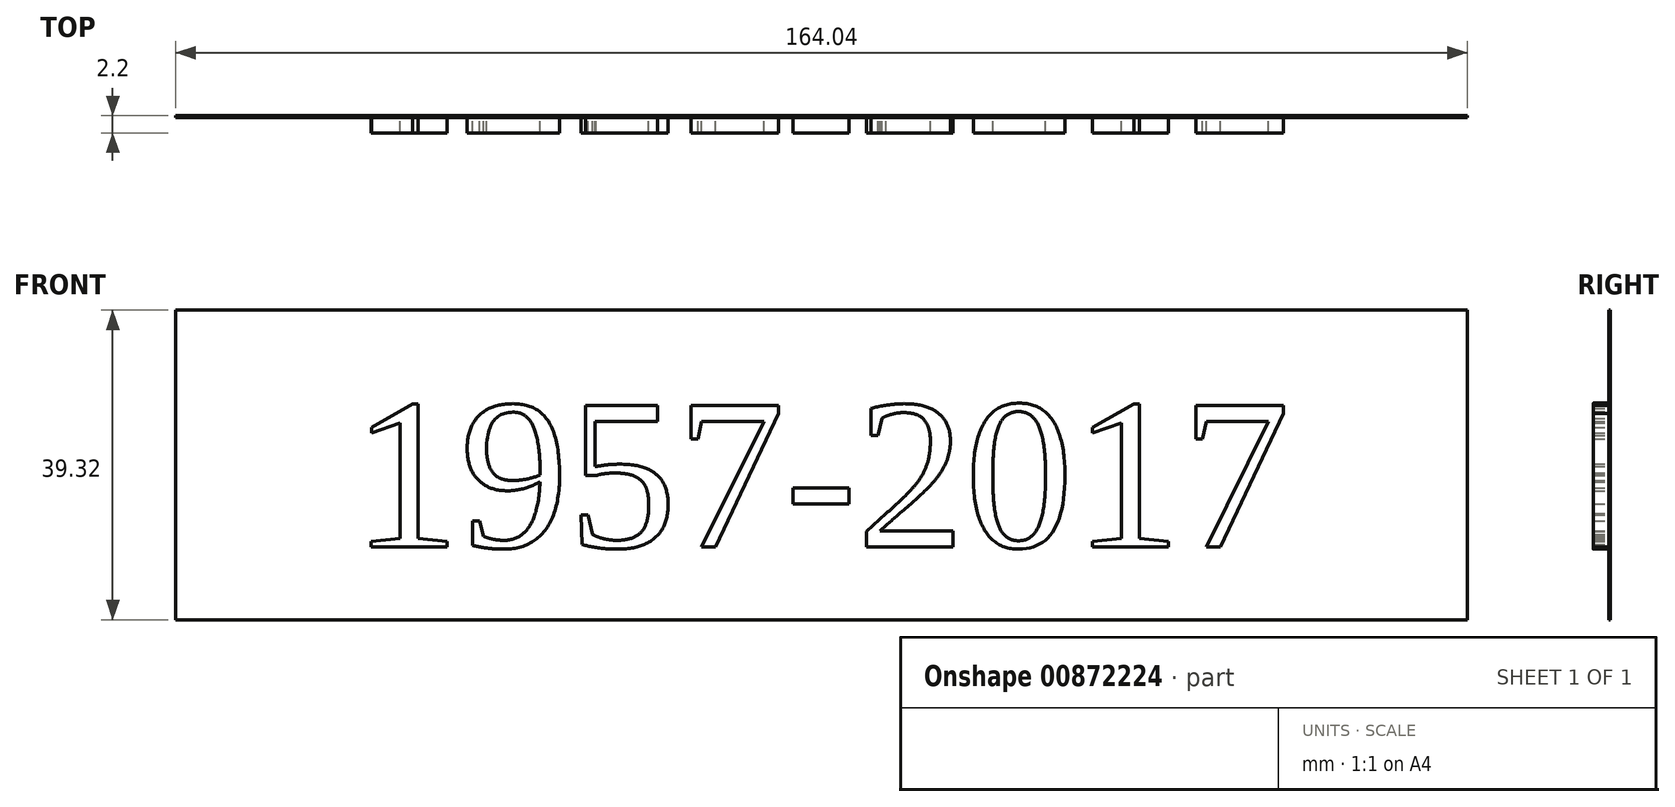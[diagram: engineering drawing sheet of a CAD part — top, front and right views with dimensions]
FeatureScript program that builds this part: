
annotation { "Feature Type Name" : "Feature", "Feature Type Description" : "" }
export const myFeature = defineFeature(function(context is Context, id is Id, definition is map)
    precondition{}
    {
        {
            var Q0;
            Q0=qCreatedBy(makeId("Front.planeOp"),FACE);
            var Q1;
            Q1=qCreatedBy(makeId("Front.planeOp"),FACE);
            var sketch = newSketch(context, id + "F0", { "sketchPlane" : qUnion([Q0, Q1])});
            skLineSegment(sketch, "E0.bottom", {"start": v(-138.77, 57.72) * mm, "end": v(138.77, 57.72) * mm});
            skLineSegment(sketch, "E0.top", {"start": v(-138.77, -57.72) * mm, "end": v(138.77, -57.72) * mm});
            skLineSegment(sketch, "E0.left", {"start": v(-138.77, 57.72) * mm, "end": v(-138.77, -57.72) * mm});
            skLineSegment(sketch, "E0.right", {"start": v(138.77, 57.72) * mm, "end": v(138.77, -57.72) * mm});
            skPoint(sketch, "E0.middle", {"position": v(0, 0) * mm});
            skSolve(sketch);
        }
        {
            var Q0;
            Q0=qCreatedBy(makeId("Front.planeOp"),FACE);
            var sketch = newSketch(context, id + "F1", { "sketchPlane" : qUnion([Q0])});
            skLineSegment(sketch, "E1", {"start": v(-87.08, -6.74) * mm, "end": v(-86.38, -7.27) * mm});
            skLineSegment(sketch, "E2", {"start": v(-86.38, -7.27) * mm, "end": v(-86.52, -7.55) * mm});
            skLineSegment(sketch, "E3", {"start": v(-86.52, -7.55) * mm, "end": v(-86.65, -7.82) * mm});
            skLineSegment(sketch, "E4", {"start": v(-86.65, -7.82) * mm, "end": v(-86.78, -8.07) * mm});
            skLineSegment(sketch, "E5", {"start": v(-86.78, -8.07) * mm, "end": v(-86.91, -8.3) * mm});
            skLineSegment(sketch, "E6", {"start": v(-86.91, -8.3) * mm, "end": v(-86.98, -8.42) * mm});
            skLineSegment(sketch, "E7", {"start": v(-86.98, -8.42) * mm, "end": v(-87.04, -8.54) * mm});
            skLineSegment(sketch, "E8", {"start": v(-87.04, -8.54) * mm, "end": v(-87.12, -8.66) * mm});
            skLineSegment(sketch, "E9", {"start": v(-87.12, -8.66) * mm, "end": v(-87.2, -8.8) * mm});
            skLineSegment(sketch, "E10", {"start": v(-87.2, -8.8) * mm, "end": v(-87.35, -9.07) * mm});
            skLineSegment(sketch, "E11", {"start": v(-87.35, -9.07) * mm, "end": v(-87.52, -9.38) * mm});
            skLineSegment(sketch, "E12", {"start": v(-87.52, -9.38) * mm, "end": v(-87.61, -9.53) * mm});
            skLineSegment(sketch, "E13", {"start": v(-87.61, -9.53) * mm, "end": v(-87.7, -9.67) * mm});
            skLineSegment(sketch, "E14", {"start": v(-87.7, -9.67) * mm, "end": v(-87.77, -9.8) * mm});
            skLineSegment(sketch, "E15", {"start": v(-87.77, -9.8) * mm, "end": v(-87.84, -9.93) * mm});
            skLineSegment(sketch, "E16", {"start": v(-87.84, -9.93) * mm, "end": v(-87.9, -10.05) * mm});
            skLineSegment(sketch, "E17", {"start": v(-87.9, -10.05) * mm, "end": v(-87.94, -10.1) * mm});
            skLineSegment(sketch, "E18", {"start": v(-87.94, -10.1) * mm, "end": v(-87.97, -10.15) * mm});
            skLineSegment(sketch, "E19", {"start": v(-87.97, -10.15) * mm, "end": v(-88, -10.2) * mm});
            skLineSegment(sketch, "E20", {"start": v(-88, -10.2) * mm, "end": v(-88.02, -10.24) * mm});
            skLineSegment(sketch, "E21", {"start": v(-88.02, -10.24) * mm, "end": v(-88.05, -10.29) * mm});
            skLineSegment(sketch, "E22", {"start": v(-88.05, -10.29) * mm, "end": v(-88.07, -10.33) * mm});
            skLineSegment(sketch, "E23", {"start": v(-88.07, -10.33) * mm, "end": v(-88.27, -10.66) * mm});
            skLineSegment(sketch, "E24", {"start": v(-88.27, -10.66) * mm, "end": v(-88.46, -10.97) * mm});
            skLineSegment(sketch, "E25", {"start": v(-88.46, -10.97) * mm, "end": v(-88.66, -11.27) * mm});
            skLineSegment(sketch, "E26", {"start": v(-88.66, -11.27) * mm, "end": v(-88.85, -11.54) * mm});
            skLineSegment(sketch, "E27", {"start": v(-88.85, -11.54) * mm, "end": v(-89.04, -11.78) * mm});
            skLineSegment(sketch, "E28", {"start": v(-89.04, -11.78) * mm, "end": v(-89.23, -12.01) * mm});
            skLineSegment(sketch, "E29", {"start": v(-89.23, -12.01) * mm, "end": v(-89.42, -12.22) * mm});
            skLineSegment(sketch, "E30", {"start": v(-89.42, -12.22) * mm, "end": v(-89.6, -12.4) * mm});
            skLineSegment(sketch, "E31", {"start": v(-89.6, -12.4) * mm, "end": v(-89.7, -12.48) * mm});
            skLineSegment(sketch, "E32", {"start": v(-89.7, -12.48) * mm, "end": v(-89.8, -12.56) * mm});
            skLineSegment(sketch, "E33", {"start": v(-89.8, -12.56) * mm, "end": v(-89.88, -12.63) * mm});
            skLineSegment(sketch, "E34", {"start": v(-89.88, -12.63) * mm, "end": v(-89.98, -12.7) * mm});
            skLineSegment(sketch, "E35", {"start": v(-89.98, -12.7) * mm, "end": v(-90.07, -12.76) * mm});
            skLineSegment(sketch, "E36", {"start": v(-90.07, -12.76) * mm, "end": v(-90.16, -12.82) * mm});
            skLineSegment(sketch, "E37", {"start": v(-90.16, -12.82) * mm, "end": v(-90.25, -12.87) * mm});
            skLineSegment(sketch, "E38", {"start": v(-90.25, -12.87) * mm, "end": v(-90.34, -12.92) * mm});
            skLineSegment(sketch, "E39", {"start": v(-90.34, -12.92) * mm, "end": v(-90.43, -12.96) * mm});
            skLineSegment(sketch, "E40", {"start": v(-90.43, -12.96) * mm, "end": v(-90.52, -13) * mm});
            skLineSegment(sketch, "E41", {"start": v(-90.52, -13) * mm, "end": v(-90.6, -13.02) * mm});
            skLineSegment(sketch, "E42", {"start": v(-90.6, -13.02) * mm, "end": v(-90.7, -13.05) * mm});
            skLineSegment(sketch, "E43", {"start": v(-90.7, -13.05) * mm, "end": v(-90.78, -13.07) * mm});
            skLineSegment(sketch, "E44", {"start": v(-90.78, -13.07) * mm, "end": v(-90.87, -13.08) * mm});
            skLineSegment(sketch, "E45", {"start": v(-90.87, -13.08) * mm, "end": v(-90.96, -13.09) * mm});
            skLineSegment(sketch, "E46", {"start": v(-90.96, -13.09) * mm, "end": v(-91.05, -13.1) * mm});
            skLineSegment(sketch, "E47", {"start": v(-91.05, -13.1) * mm, "end": v(-91.12, -13.09) * mm});
            skLineSegment(sketch, "E48", {"start": v(-91.12, -13.09) * mm, "end": v(-91.2, -13.08) * mm});
            skLineSegment(sketch, "E49", {"start": v(-91.2, -13.08) * mm, "end": v(-91.26, -13.07) * mm});
            skLineSegment(sketch, "E50", {"start": v(-91.26, -13.07) * mm, "end": v(-91.33, -13.06) * mm});
            skLineSegment(sketch, "E51", {"start": v(-91.33, -13.06) * mm, "end": v(-91.4, -13.05) * mm});
            skLineSegment(sketch, "E52", {"start": v(-91.4, -13.05) * mm, "end": v(-91.47, -13.03) * mm});
            skLineSegment(sketch, "E53", {"start": v(-91.47, -13.03) * mm, "end": v(-91.53, -13) * mm});
            skLineSegment(sketch, "E54", {"start": v(-91.53, -13) * mm, "end": v(-91.6, -12.97) * mm});
            skLineSegment(sketch, "E55", {"start": v(-91.6, -12.97) * mm, "end": v(-91.66, -12.94) * mm});
            skLineSegment(sketch, "E56", {"start": v(-91.66, -12.94) * mm, "end": v(-91.72, -12.9) * mm});
            skLineSegment(sketch, "E57", {"start": v(-91.72, -12.9) * mm, "end": v(-91.78, -12.87) * mm});
            skLineSegment(sketch, "E58", {"start": v(-91.78, -12.87) * mm, "end": v(-91.84, -12.83) * mm});
            skLineSegment(sketch, "E59", {"start": v(-91.84, -12.83) * mm, "end": v(-91.9, -12.78) * mm});
            skLineSegment(sketch, "E60", {"start": v(-91.9, -12.78) * mm, "end": v(-91.95, -12.74) * mm});
            skLineSegment(sketch, "E61", {"start": v(-91.95, -12.74) * mm, "end": v(-92, -12.68) * mm});
            skLineSegment(sketch, "E62", {"start": v(-92, -12.68) * mm, "end": v(-92.06, -12.63) * mm});
            skLineSegment(sketch, "E63", {"start": v(-92.06, -12.63) * mm, "end": v(-92.11, -12.57) * mm});
            skLineSegment(sketch, "E64", {"start": v(-92.11, -12.57) * mm, "end": v(-92.16, -12.5) * mm});
            skLineSegment(sketch, "E65", {"start": v(-92.16, -12.5) * mm, "end": v(-92.2, -12.44) * mm});
            skLineSegment(sketch, "E66", {"start": v(-92.2, -12.44) * mm, "end": v(-92.24, -12.37) * mm});
            skLineSegment(sketch, "E67", {"start": v(-92.24, -12.37) * mm, "end": v(-92.28, -12.3) * mm});
            skLineSegment(sketch, "E68", {"start": v(-92.28, -12.3) * mm, "end": v(-92.32, -12.23) * mm});
            skLineSegment(sketch, "E69", {"start": v(-92.32, -12.23) * mm, "end": v(-92.35, -12.16) * mm});
            skLineSegment(sketch, "E70", {"start": v(-92.35, -12.16) * mm, "end": v(-92.38, -12.08) * mm});
            skLineSegment(sketch, "E71", {"start": v(-92.38, -12.08) * mm, "end": v(-92.4, -12) * mm});
            skLineSegment(sketch, "E72", {"start": v(-92.4, -12) * mm, "end": v(-92.42, -11.91) * mm});
            skLineSegment(sketch, "E73", {"start": v(-92.42, -11.91) * mm, "end": v(-92.44, -11.83) * mm});
            skLineSegment(sketch, "E74", {"start": v(-92.44, -11.83) * mm, "end": v(-92.45, -11.74) * mm});
            skLineSegment(sketch, "E75", {"start": v(-92.45, -11.74) * mm, "end": v(-92.47, -11.65) * mm});
            skLineSegment(sketch, "E76", {"start": v(-92.47, -11.65) * mm, "end": v(-92.47, -11.56) * mm});
            skLineSegment(sketch, "E77", {"start": v(-92.47, -11.56) * mm, "end": v(-92.48, -11.36) * mm});
            skLineSegment(sketch, "E78", {"start": v(-92.48, -11.36) * mm, "end": v(-92.48, -11.21) * mm});
            skLineSegment(sketch, "E79", {"start": v(-92.48, -11.21) * mm, "end": v(-92.47, -11.06) * mm});
            skLineSegment(sketch, "E80", {"start": v(-92.47, -11.06) * mm, "end": v(-92.45, -10.9) * mm});
            skLineSegment(sketch, "E81", {"start": v(-92.45, -10.9) * mm, "end": v(-92.43, -10.74) * mm});
            skLineSegment(sketch, "E82", {"start": v(-92.43, -10.74) * mm, "end": v(-92.4, -10.57) * mm});
            skLineSegment(sketch, "E83", {"start": v(-92.4, -10.57) * mm, "end": v(-92.37, -10.39) * mm});
            skLineSegment(sketch, "E84", {"start": v(-92.37, -10.39) * mm, "end": v(-92.33, -10.2) * mm});
            skLineSegment(sketch, "E85", {"start": v(-92.33, -10.2) * mm, "end": v(-92.28, -10.01) * mm});
            skLineSegment(sketch, "E86", {"start": v(-92.28, -10.01) * mm, "end": v(-92.17, -9.6) * mm});
            skLineSegment(sketch, "E87", {"start": v(-92.17, -9.6) * mm, "end": v(-92.03, -9.18) * mm});
            skLineSegment(sketch, "E88", {"start": v(-92.03, -9.18) * mm, "end": v(-91.87, -8.72) * mm});
            skLineSegment(sketch, "E89", {"start": v(-91.87, -8.72) * mm, "end": v(-91.68, -8.24) * mm});
            skLineSegment(sketch, "E90", {"start": v(-91.68, -8.24) * mm, "end": v(-91.46, -7.73) * mm});
            skLineSegment(sketch, "E91", {"start": v(-91.46, -7.73) * mm, "end": v(-91.21, -7.2) * mm});
            skLineSegment(sketch, "E92", {"start": v(-91.21, -7.2) * mm, "end": v(-90.94, -6.62) * mm});
            skLineSegment(sketch, "E93", {"start": v(-90.94, -6.62) * mm, "end": v(-90.64, -6.03) * mm});
            skLineSegment(sketch, "E94", {"start": v(-90.64, -6.03) * mm, "end": v(-90.31, -5.4) * mm});
            skLineSegment(sketch, "E95", {"start": v(-90.31, -5.4) * mm, "end": v(-89.96, -4.75) * mm});
            skLineSegment(sketch, "E96", {"start": v(-89.96, -4.75) * mm, "end": v(-89.58, -4.07) * mm});
            skLineSegment(sketch, "E97", {"start": v(-89.58, -4.07) * mm, "end": v(-89.17, -3.37) * mm});
            skLineSegment(sketch, "E98", {"start": v(-89.17, -3.37) * mm, "end": v(-88.26, -1.86) * mm});
            skLineSegment(sketch, "E99", {"start": v(-88.26, -1.86) * mm, "end": v(-87.24, -0.26) * mm});
            skLineSegment(sketch, "E100", {"start": v(-87.24, -0.26) * mm, "end": v(-86.12, 1.43) * mm});
            skLineSegment(sketch, "E101", {"start": v(-86.12, 1.43) * mm, "end": v(-84.89, 3.22) * mm});
            skLineSegment(sketch, "E102", {"start": v(-84.89, 3.22) * mm, "end": v(-83.56, 5.08) * mm});
            skLineSegment(sketch, "E103", {"start": v(-83.56, 5.08) * mm, "end": v(-80.66, 8.95) * mm});
            skLineSegment(sketch, "E104", {"start": v(-80.66, 8.95) * mm, "end": v(-79.08, 10.96) * mm});
            skLineSegment(sketch, "E105", {"start": v(-79.08, 10.96) * mm, "end": v(-79.56, 11.02) * mm});
            skLineSegment(sketch, "E106", {"start": v(-79.56, 11.02) * mm, "end": v(-80.06, 11.08) * mm});
            skLineSegment(sketch, "E107", {"start": v(-80.06, 11.08) * mm, "end": v(-80.57, 11.13) * mm});
            skLineSegment(sketch, "E108", {"start": v(-80.57, 11.13) * mm, "end": v(-81.68, 11.2) * mm});
            skLineSegment(sketch, "E109", {"start": v(-81.68, 11.2) * mm, "end": v(-82.87, 11.23) * mm});
            skLineSegment(sketch, "E110", {"start": v(-82.87, 11.23) * mm, "end": v(-83.5, 11.23) * mm});
            skLineSegment(sketch, "E111", {"start": v(-83.5, 11.23) * mm, "end": v(-85, 11.2) * mm});
            skLineSegment(sketch, "E112", {"start": v(-85, 11.2) * mm, "end": v(-86.6, 11.07) * mm});
            skLineSegment(sketch, "E113", {"start": v(-86.6, 11.07) * mm, "end": v(-88.27, 10.87) * mm});
            skLineSegment(sketch, "E114", {"start": v(-88.27, 10.87) * mm, "end": v(-90.03, 10.58) * mm});
            skLineSegment(sketch, "E115", {"start": v(-90.03, 10.58) * mm, "end": v(-91.77, 10.24) * mm});
            skLineSegment(sketch, "E116", {"start": v(-91.77, 10.24) * mm, "end": v(-93.4, 9.87) * mm});
            skLineSegment(sketch, "E117", {"start": v(-93.4, 9.87) * mm, "end": v(-94.9, 9.48) * mm});
            skLineSegment(sketch, "E118", {"start": v(-94.9, 9.48) * mm, "end": v(-96.3, 9.06) * mm});
            skLineSegment(sketch, "E119", {"start": v(-96.3, 9.06) * mm, "end": v(-96.62, 8.96) * mm});
            skLineSegment(sketch, "E120", {"start": v(-96.62, 8.96) * mm, "end": v(-96.92, 8.86) * mm});
            skLineSegment(sketch, "E121", {"start": v(-96.92, 8.86) * mm, "end": v(-97.2, 8.76) * mm});
            skLineSegment(sketch, "E122", {"start": v(-97.2, 8.76) * mm, "end": v(-97.46, 8.67) * mm});
            skLineSegment(sketch, "E123", {"start": v(-97.46, 8.67) * mm, "end": v(-97.7, 8.58) * mm});
            skLineSegment(sketch, "E124", {"start": v(-97.7, 8.58) * mm, "end": v(-97.81, 8.53) * mm});
            skLineSegment(sketch, "E125", {"start": v(-97.81, 8.53) * mm, "end": v(-97.92, 8.5) * mm});
            skLineSegment(sketch, "E126", {"start": v(-97.92, 8.5) * mm, "end": v(-98.02, 8.45) * mm});
            skLineSegment(sketch, "E127", {"start": v(-98.02, 8.45) * mm, "end": v(-98.12, 8.4) * mm});
            skLineSegment(sketch, "E128", {"start": v(-98.12, 8.4) * mm, "end": v(-98.2, 8.37) * mm});
            skLineSegment(sketch, "E129", {"start": v(-98.2, 8.37) * mm, "end": v(-98.3, 8.33) * mm});
            skLineSegment(sketch, "E130", {"start": v(-98.3, 8.33) * mm, "end": v(-98.37, 8.29) * mm});
            skLineSegment(sketch, "E131", {"start": v(-98.37, 8.29) * mm, "end": v(-98.45, 8.25) * mm});
            skLineSegment(sketch, "E132", {"start": v(-98.45, 8.25) * mm, "end": v(-98.52, 8.22) * mm});
            skLineSegment(sketch, "E133", {"start": v(-98.52, 8.22) * mm, "end": v(-98.58, 8.18) * mm});
            skLineSegment(sketch, "E134", {"start": v(-98.58, 8.18) * mm, "end": v(-98.64, 8.14) * mm});
            skLineSegment(sketch, "E135", {"start": v(-98.64, 8.14) * mm, "end": v(-98.7, 8.11) * mm});
            skLineSegment(sketch, "E136", {"start": v(-98.7, 8.11) * mm, "end": v(-98.72, 8.1) * mm});
            skLineSegment(sketch, "E137", {"start": v(-98.72, 8.1) * mm, "end": v(-98.75, 8.08) * mm});
            skLineSegment(sketch, "E138", {"start": v(-98.75, 8.08) * mm, "end": v(-98.77, 8.06) * mm});
            skLineSegment(sketch, "E139", {"start": v(-98.77, 8.06) * mm, "end": v(-98.8, 8.04) * mm});
            skLineSegment(sketch, "E140", {"start": v(-98.8, 8.04) * mm, "end": v(-98.81, 8.03) * mm});
            skLineSegment(sketch, "E141", {"start": v(-98.81, 8.03) * mm, "end": v(-98.83, 8.01) * mm});
            skLineSegment(sketch, "E142", {"start": v(-98.83, 8.01) * mm, "end": v(-98.85, 8) * mm});
            skLineSegment(sketch, "E143", {"start": v(-98.85, 8) * mm, "end": v(-98.86, 7.98) * mm});
            skLineSegment(sketch, "E144", {"start": v(-98.86, 7.98) * mm, "end": v(-98.88, 7.97) * mm});
            skLineSegment(sketch, "E145", {"start": v(-98.88, 7.97) * mm, "end": v(-98.9, 7.95) * mm});
            skLineSegment(sketch, "E146", {"start": v(-98.9, 7.95) * mm, "end": v(-98.9, 7.94) * mm});
            skLineSegment(sketch, "E147", {"start": v(-98.9, 7.94) * mm, "end": v(-98.92, 7.92) * mm});
            skLineSegment(sketch, "E148", {"start": v(-98.92, 7.92) * mm, "end": v(-98.93, 7.9) * mm});
            skLineSegment(sketch, "E149", {"start": v(-98.93, 7.9) * mm, "end": v(-98.93, 7.9) * mm});
            skLineSegment(sketch, "E150", {"start": v(-98.93, 7.9) * mm, "end": v(-98.94, 7.88) * mm});
            skLineSegment(sketch, "E151", {"start": v(-98.94, 7.88) * mm, "end": v(-98.94, 7.88) * mm});
            skLineSegment(sketch, "E152", {"start": v(-98.94, 7.88) * mm, "end": v(-98.95, 7.87) * mm});
            skLineSegment(sketch, "E153", {"start": v(-98.95, 7.87) * mm, "end": v(-98.95, 7.86) * mm});
            skLineSegment(sketch, "E154", {"start": v(-98.95, 7.86) * mm, "end": v(-98.95, 7.86) * mm});
            skLineSegment(sketch, "E155", {"start": v(-98.95, 7.86) * mm, "end": v(-98.95, 7.85) * mm});
            skLineSegment(sketch, "E156", {"start": v(-98.95, 7.85) * mm, "end": v(-98.96, 7.84) * mm});
            skLineSegment(sketch, "E157", {"start": v(-98.96, 7.84) * mm, "end": v(-98.96, 7.84) * mm});
            skLineSegment(sketch, "E158", {"start": v(-98.96, 7.84) * mm, "end": v(-98.96, 7.83) * mm});
            skLineSegment(sketch, "E159", {"start": v(-98.96, 7.83) * mm, "end": v(-98.96, 7.82) * mm});
            skLineSegment(sketch, "E160", {"start": v(-98.96, 7.82) * mm, "end": v(-98.96, 7.82) * mm});
            skLineSegment(sketch, "E161", {"start": v(-98.96, 7.82) * mm, "end": v(-98.96, 7.8) * mm});
            skLineSegment(sketch, "E162", {"start": v(-98.96, 7.8) * mm, "end": v(-98.96, 7.78) * mm});
            skLineSegment(sketch, "E163", {"start": v(-98.96, 7.78) * mm, "end": v(-98.95, 7.76) * mm});
            skLineSegment(sketch, "E164", {"start": v(-98.95, 7.76) * mm, "end": v(-98.95, 7.75) * mm});
            skLineSegment(sketch, "E165", {"start": v(-98.95, 7.75) * mm, "end": v(-98.95, 7.73) * mm});
            skLineSegment(sketch, "E166", {"start": v(-98.95, 7.73) * mm, "end": v(-98.94, 7.72) * mm});
            skLineSegment(sketch, "E167", {"start": v(-98.94, 7.72) * mm, "end": v(-98.94, 7.7) * mm});
            skLineSegment(sketch, "E168", {"start": v(-98.94, 7.7) * mm, "end": v(-98.93, 7.69) * mm});
            skLineSegment(sketch, "E169", {"start": v(-98.93, 7.69) * mm, "end": v(-98.92, 7.68) * mm});
            skLineSegment(sketch, "E170", {"start": v(-98.92, 7.68) * mm, "end": v(-98.92, 7.66) * mm});
            skLineSegment(sketch, "E171", {"start": v(-98.92, 7.66) * mm, "end": v(-98.9, 7.65) * mm});
            skLineSegment(sketch, "E172", {"start": v(-98.9, 7.65) * mm, "end": v(-98.9, 7.64) * mm});
            skLineSegment(sketch, "E173", {"start": v(-98.9, 7.64) * mm, "end": v(-98.89, 7.63) * mm});
            skLineSegment(sketch, "E174", {"start": v(-98.89, 7.63) * mm, "end": v(-98.88, 7.62) * mm});
            skLineSegment(sketch, "E175", {"start": v(-98.88, 7.62) * mm, "end": v(-98.87, 7.61) * mm});
            skLineSegment(sketch, "E176", {"start": v(-98.87, 7.61) * mm, "end": v(-98.85, 7.6) * mm});
            skLineSegment(sketch, "E177", {"start": v(-98.85, 7.6) * mm, "end": v(-98.84, 7.6) * mm});
            skLineSegment(sketch, "E178", {"start": v(-98.84, 7.6) * mm, "end": v(-98.82, 7.6) * mm});
            skLineSegment(sketch, "E179", {"start": v(-98.82, 7.6) * mm, "end": v(-98.8, 7.59) * mm});
            skLineSegment(sketch, "E180", {"start": v(-98.8, 7.59) * mm, "end": v(-98.8, 7.58) * mm});
            skLineSegment(sketch, "E181", {"start": v(-98.8, 7.58) * mm, "end": v(-98.77, 7.58) * mm});
            skLineSegment(sketch, "E182", {"start": v(-98.77, 7.58) * mm, "end": v(-98.76, 7.57) * mm});
            skLineSegment(sketch, "E183", {"start": v(-98.76, 7.57) * mm, "end": v(-98.74, 7.57) * mm});
            skLineSegment(sketch, "E184", {"start": v(-98.74, 7.57) * mm, "end": v(-98.72, 7.56) * mm});
            skLineSegment(sketch, "E185", {"start": v(-98.72, 7.56) * mm, "end": v(-98.67, 7.55) * mm});
            skLineSegment(sketch, "E186", {"start": v(-98.67, 7.55) * mm, "end": v(-98.62, 7.54) * mm});
            skLineSegment(sketch, "E187", {"start": v(-98.62, 7.54) * mm, "end": v(-98.57, 7.53) * mm});
            skLineSegment(sketch, "E188", {"start": v(-98.57, 7.53) * mm, "end": v(-98.51, 7.52) * mm});
            skLineSegment(sketch, "E189", {"start": v(-98.51, 7.52) * mm, "end": v(-98.45, 7.52) * mm});
            skLineSegment(sketch, "E190", {"start": v(-98.45, 7.52) * mm, "end": v(-98.38, 7.5) * mm});
            skLineSegment(sketch, "E191", {"start": v(-98.38, 7.5) * mm, "end": v(-98.3, 7.5) * mm});
            skLineSegment(sketch, "E192", {"start": v(-98.3, 7.5) * mm, "end": v(-98.23, 7.5) * mm});
            skLineSegment(sketch, "E193", {"start": v(-98.23, 7.5) * mm, "end": v(-98.15, 7.49) * mm});
            skLineSegment(sketch, "E194", {"start": v(-98.15, 7.49) * mm, "end": v(-98.06, 7.48) * mm});
            skLineSegment(sketch, "E195", {"start": v(-98.06, 7.48) * mm, "end": v(-97.97, 7.47) * mm});
            skLineSegment(sketch, "E196", {"start": v(-97.97, 7.47) * mm, "end": v(-97.88, 7.46) * mm});
            skLineSegment(sketch, "E197", {"start": v(-97.88, 7.46) * mm, "end": v(-97.58, 7.42) * mm});
            skLineSegment(sketch, "E198", {"start": v(-97.58, 7.42) * mm, "end": v(-97.3, 7.37) * mm});
            skLineSegment(sketch, "E199", {"start": v(-97.3, 7.37) * mm, "end": v(-97.04, 7.33) * mm});
            skLineSegment(sketch, "E200", {"start": v(-97.04, 7.33) * mm, "end": v(-96.8, 7.28) * mm});
            skLineSegment(sketch, "E201", {"start": v(-96.8, 7.28) * mm, "end": v(-96.58, 7.24) * mm});
            skLineSegment(sketch, "E202", {"start": v(-96.58, 7.24) * mm, "end": v(-96.48, 7.22) * mm});
            skLineSegment(sketch, "E203", {"start": v(-96.48, 7.22) * mm, "end": v(-96.38, 7.2) * mm});
            skLineSegment(sketch, "E204", {"start": v(-96.38, 7.2) * mm, "end": v(-96.28, 7.17) * mm});
            skLineSegment(sketch, "E205", {"start": v(-96.28, 7.17) * mm, "end": v(-96.2, 7.15) * mm});
            skLineSegment(sketch, "E206", {"start": v(-96.2, 7.15) * mm, "end": v(-96.11, 7.12) * mm});
            skLineSegment(sketch, "E207", {"start": v(-96.11, 7.12) * mm, "end": v(-96.03, 7.1) * mm});
            skLineSegment(sketch, "E208", {"start": v(-96.03, 7.1) * mm, "end": v(-95.96, 7.08) * mm});
            skLineSegment(sketch, "E209", {"start": v(-95.96, 7.08) * mm, "end": v(-95.89, 7.05) * mm});
            skLineSegment(sketch, "E210", {"start": v(-95.89, 7.05) * mm, "end": v(-95.82, 7.03) * mm});
            skLineSegment(sketch, "E211", {"start": v(-95.82, 7.03) * mm, "end": v(-95.76, 7) * mm});
            skLineSegment(sketch, "E212", {"start": v(-95.76, 7) * mm, "end": v(-95.7, 6.98) * mm});
            skLineSegment(sketch, "E213", {"start": v(-95.7, 6.98) * mm, "end": v(-95.65, 6.95) * mm});
            skLineSegment(sketch, "E214", {"start": v(-95.65, 6.95) * mm, "end": v(-95.63, 6.94) * mm});
            skLineSegment(sketch, "E215", {"start": v(-95.63, 6.94) * mm, "end": v(-95.6, 6.93) * mm});
            skLineSegment(sketch, "E216", {"start": v(-95.6, 6.93) * mm, "end": v(-95.59, 6.92) * mm});
            skLineSegment(sketch, "E217", {"start": v(-95.59, 6.92) * mm, "end": v(-95.57, 6.9) * mm});
            skLineSegment(sketch, "E218", {"start": v(-95.57, 6.9) * mm, "end": v(-95.55, 6.9) * mm});
            skLineSegment(sketch, "E219", {"start": v(-95.55, 6.9) * mm, "end": v(-95.53, 6.88) * mm});
            skLineSegment(sketch, "E220", {"start": v(-95.53, 6.88) * mm, "end": v(-95.52, 6.87) * mm});
            skLineSegment(sketch, "E221", {"start": v(-95.52, 6.87) * mm, "end": v(-95.5, 6.85) * mm});
            skLineSegment(sketch, "E222", {"start": v(-95.5, 6.85) * mm, "end": v(-95.49, 6.84) * mm});
            skLineSegment(sketch, "E223", {"start": v(-95.49, 6.84) * mm, "end": v(-95.47, 6.83) * mm});
            skLineSegment(sketch, "E224", {"start": v(-95.47, 6.83) * mm, "end": v(-95.46, 6.82) * mm});
            skLineSegment(sketch, "E225", {"start": v(-95.46, 6.82) * mm, "end": v(-95.45, 6.8) * mm});
            skLineSegment(sketch, "E226", {"start": v(-95.45, 6.8) * mm, "end": v(-95.44, 6.79) * mm});
            skLineSegment(sketch, "E227", {"start": v(-95.44, 6.79) * mm, "end": v(-95.44, 6.78) * mm});
            skLineSegment(sketch, "E228", {"start": v(-95.44, 6.78) * mm, "end": v(-95.43, 6.76) * mm});
            skLineSegment(sketch, "E229", {"start": v(-95.43, 6.76) * mm, "end": v(-95.42, 6.75) * mm});
            skLineSegment(sketch, "E230", {"start": v(-95.42, 6.75) * mm, "end": v(-95.42, 6.74) * mm});
            skLineSegment(sketch, "E231", {"start": v(-95.42, 6.74) * mm, "end": v(-95.42, 6.74) * mm});
            skLineSegment(sketch, "E232", {"start": v(-95.42, 6.74) * mm, "end": v(-95.42, 6.73) * mm});
            skLineSegment(sketch, "E233", {"start": v(-95.42, 6.73) * mm, "end": v(-95.42, 6.72) * mm});
            skLineSegment(sketch, "E234", {"start": v(-95.42, 6.72) * mm, "end": v(-95.41, 6.72) * mm});
            skLineSegment(sketch, "E235", {"start": v(-95.41, 6.72) * mm, "end": v(-95.41, 6.71) * mm});
            skLineSegment(sketch, "E236", {"start": v(-95.41, 6.71) * mm, "end": v(-95.41, 6.7) * mm});
            skLineSegment(sketch, "E237", {"start": v(-95.41, 6.7) * mm, "end": v(-95.41, 6.7) * mm});
            skLineSegment(sketch, "E238", {"start": v(-95.41, 6.7) * mm, "end": v(-95.41, 6.69) * mm});
            skLineSegment(sketch, "E239", {"start": v(-95.41, 6.69) * mm, "end": v(-95.42, 6.68) * mm});
            skLineSegment(sketch, "E240", {"start": v(-95.42, 6.68) * mm, "end": v(-95.42, 6.67) * mm});
            skLineSegment(sketch, "E241", {"start": v(-95.42, 6.67) * mm, "end": v(-95.42, 6.67) * mm});
            skLineSegment(sketch, "E242", {"start": v(-95.42, 6.67) * mm, "end": v(-95.42, 6.66) * mm});
            skLineSegment(sketch, "E243", {"start": v(-95.42, 6.66) * mm, "end": v(-95.43, 6.65) * mm});
            skLineSegment(sketch, "E244", {"start": v(-95.43, 6.65) * mm, "end": v(-95.43, 6.65) * mm});
            skLineSegment(sketch, "E245", {"start": v(-95.43, 6.65) * mm, "end": v(-95.43, 6.64) * mm});
            skLineSegment(sketch, "E246", {"start": v(-95.43, 6.64) * mm, "end": v(-95.44, 6.64) * mm});
            skLineSegment(sketch, "E247", {"start": v(-95.44, 6.64) * mm, "end": v(-95.45, 6.63) * mm});
            skLineSegment(sketch, "E248", {"start": v(-95.45, 6.63) * mm, "end": v(-95.45, 6.63) * mm});
            skLineSegment(sketch, "E249", {"start": v(-95.45, 6.63) * mm, "end": v(-95.46, 6.62) * mm});
            skLineSegment(sketch, "E250", {"start": v(-95.46, 6.62) * mm, "end": v(-95.47, 6.62) * mm});
            skLineSegment(sketch, "E251", {"start": v(-95.47, 6.62) * mm, "end": v(-95.47, 6.61) * mm});
            skLineSegment(sketch, "E252", {"start": v(-95.47, 6.61) * mm, "end": v(-95.48, 6.6) * mm});
            skLineSegment(sketch, "E253", {"start": v(-95.48, 6.6) * mm, "end": v(-95.49, 6.6) * mm});
            skLineSegment(sketch, "E254", {"start": v(-95.49, 6.6) * mm, "end": v(-95.5, 6.6) * mm});
            skLineSegment(sketch, "E255", {"start": v(-95.5, 6.6) * mm, "end": v(-95.5, 6.6) * mm});
            skLineSegment(sketch, "E256", {"start": v(-95.5, 6.6) * mm, "end": v(-95.52, 6.59) * mm});
            skLineSegment(sketch, "E257", {"start": v(-95.52, 6.59) * mm, "end": v(-95.53, 6.58) * mm});
            skLineSegment(sketch, "E258", {"start": v(-95.53, 6.58) * mm, "end": v(-95.55, 6.57) * mm});
            skLineSegment(sketch, "E259", {"start": v(-95.55, 6.57) * mm, "end": v(-95.58, 6.57) * mm});
            skLineSegment(sketch, "E260", {"start": v(-95.58, 6.57) * mm, "end": v(-95.6, 6.56) * mm});
            skLineSegment(sketch, "E261", {"start": v(-95.6, 6.56) * mm, "end": v(-95.63, 6.55) * mm});
            skLineSegment(sketch, "E262", {"start": v(-95.63, 6.55) * mm, "end": v(-95.67, 6.54) * mm});
            skLineSegment(sketch, "E263", {"start": v(-95.67, 6.54) * mm, "end": v(-95.7, 6.54) * mm});
            skLineSegment(sketch, "E264", {"start": v(-95.7, 6.54) * mm, "end": v(-95.74, 6.53) * mm});
            skLineSegment(sketch, "E265", {"start": v(-95.74, 6.53) * mm, "end": v(-95.77, 6.52) * mm});
            skLineSegment(sketch, "E266", {"start": v(-95.77, 6.52) * mm, "end": v(-95.81, 6.52) * mm});
            skLineSegment(sketch, "E267", {"start": v(-95.81, 6.52) * mm, "end": v(-95.86, 6.51) * mm});
            skLineSegment(sketch, "E268", {"start": v(-95.86, 6.51) * mm, "end": v(-95.9, 6.51) * mm});
            skLineSegment(sketch, "E269", {"start": v(-95.9, 6.51) * mm, "end": v(-95.95, 6.5) * mm});
            skLineSegment(sketch, "E270", {"start": v(-95.95, 6.5) * mm, "end": v(-96.04, 6.5) * mm});
            skLineSegment(sketch, "E271", {"start": v(-96.04, 6.5) * mm, "end": v(-96.15, 6.5) * mm});
            skLineSegment(sketch, "E272", {"start": v(-96.15, 6.5) * mm, "end": v(-96.27, 6.49) * mm});
            skLineSegment(sketch, "E273", {"start": v(-96.27, 6.49) * mm, "end": v(-96.4, 6.49) * mm});
            skLineSegment(sketch, "E274", {"start": v(-96.4, 6.49) * mm, "end": v(-96.49, 6.49) * mm});
            skLineSegment(sketch, "E275", {"start": v(-96.49, 6.49) * mm, "end": v(-96.77, 6.5) * mm});
            skLineSegment(sketch, "E276", {"start": v(-96.77, 6.5) * mm, "end": v(-97.06, 6.5) * mm});
            skLineSegment(sketch, "E277", {"start": v(-97.06, 6.5) * mm, "end": v(-97.36, 6.5) * mm});
            skLineSegment(sketch, "E278", {"start": v(-97.36, 6.5) * mm, "end": v(-98, 6.5) * mm});
            skLineSegment(sketch, "E279", {"start": v(-98, 6.5) * mm, "end": v(-98.71, 6.5) * mm});
            skLineSegment(sketch, "E280", {"start": v(-98.71, 6.5) * mm, "end": v(-99.08, 6.5) * mm});
            skLineSegment(sketch, "E281", {"start": v(-99.08, 6.5) * mm, "end": v(-99.37, 6.5) * mm});
            skLineSegment(sketch, "E282", {"start": v(-99.37, 6.5) * mm, "end": v(-99.64, 6.51) * mm});
            skLineSegment(sketch, "E283", {"start": v(-99.64, 6.51) * mm, "end": v(-99.9, 6.52) * mm});
            skLineSegment(sketch, "E284", {"start": v(-99.9, 6.52) * mm, "end": v(-100.01, 6.52) * mm});
            skLineSegment(sketch, "E285", {"start": v(-100.01, 6.52) * mm, "end": v(-100.12, 6.53) * mm});
            skLineSegment(sketch, "E286", {"start": v(-100.12, 6.53) * mm, "end": v(-100.23, 6.54) * mm});
            skLineSegment(sketch, "E287", {"start": v(-100.23, 6.54) * mm, "end": v(-100.33, 6.54) * mm});
            skLineSegment(sketch, "E288", {"start": v(-100.33, 6.54) * mm, "end": v(-100.43, 6.55) * mm});
            skLineSegment(sketch, "E289", {"start": v(-100.43, 6.55) * mm, "end": v(-100.52, 6.56) * mm});
            skLineSegment(sketch, "E290", {"start": v(-100.52, 6.56) * mm, "end": v(-100.6, 6.56) * mm});
            skLineSegment(sketch, "E291", {"start": v(-100.6, 6.56) * mm, "end": v(-100.69, 6.57) * mm});
            skLineSegment(sketch, "E292", {"start": v(-100.69, 6.57) * mm, "end": v(-100.76, 6.58) * mm});
            skLineSegment(sketch, "E293", {"start": v(-100.76, 6.58) * mm, "end": v(-100.84, 6.6) * mm});
            skLineSegment(sketch, "E294", {"start": v(-100.84, 6.6) * mm, "end": v(-100.9, 6.6) * mm});
            skLineSegment(sketch, "E295", {"start": v(-100.9, 6.6) * mm, "end": v(-100.96, 6.62) * mm});
            skLineSegment(sketch, "E296", {"start": v(-100.96, 6.62) * mm, "end": v(-101.02, 6.64) * mm});
            skLineSegment(sketch, "E297", {"start": v(-101.02, 6.64) * mm, "end": v(-101.08, 6.65) * mm});
            skLineSegment(sketch, "E298", {"start": v(-101.08, 6.65) * mm, "end": v(-101.13, 6.67) * mm});
            skLineSegment(sketch, "E299", {"start": v(-101.13, 6.67) * mm, "end": v(-101.18, 6.7) * mm});
            skLineSegment(sketch, "E300", {"start": v(-101.18, 6.7) * mm, "end": v(-101.23, 6.71) * mm});
            skLineSegment(sketch, "E301", {"start": v(-101.23, 6.71) * mm, "end": v(-101.28, 6.74) * mm});
            skLineSegment(sketch, "E302", {"start": v(-101.28, 6.74) * mm, "end": v(-101.32, 6.76) * mm});
            skLineSegment(sketch, "E303", {"start": v(-101.32, 6.76) * mm, "end": v(-101.36, 6.78) * mm});
            skLineSegment(sketch, "E304", {"start": v(-101.36, 6.78) * mm, "end": v(-101.4, 6.8) * mm});
            skLineSegment(sketch, "E305", {"start": v(-101.4, 6.8) * mm, "end": v(-101.44, 6.83) * mm});
            skLineSegment(sketch, "E306", {"start": v(-101.44, 6.83) * mm, "end": v(-101.47, 6.86) * mm});
            skLineSegment(sketch, "E307", {"start": v(-101.47, 6.86) * mm, "end": v(-101.5, 6.9) * mm});
            skLineSegment(sketch, "E308", {"start": v(-101.5, 6.9) * mm, "end": v(-101.53, 6.92) * mm});
            skLineSegment(sketch, "E309", {"start": v(-101.53, 6.92) * mm, "end": v(-101.55, 6.95) * mm});
            skLineSegment(sketch, "E310", {"start": v(-101.55, 6.95) * mm, "end": v(-101.57, 6.99) * mm});
            skLineSegment(sketch, "E311", {"start": v(-101.57, 6.99) * mm, "end": v(-101.6, 7.02) * mm});
            skLineSegment(sketch, "E312", {"start": v(-101.6, 7.02) * mm, "end": v(-101.61, 7.06) * mm});
            skLineSegment(sketch, "E313", {"start": v(-101.61, 7.06) * mm, "end": v(-101.63, 7.1) * mm});
            skLineSegment(sketch, "E314", {"start": v(-101.63, 7.1) * mm, "end": v(-101.64, 7.15) * mm});
            skLineSegment(sketch, "E315", {"start": v(-101.64, 7.15) * mm, "end": v(-101.66, 7.2) * mm});
            skLineSegment(sketch, "E316", {"start": v(-101.66, 7.2) * mm, "end": v(-101.67, 7.24) * mm});
            skLineSegment(sketch, "E317", {"start": v(-101.67, 7.24) * mm, "end": v(-101.68, 7.3) * mm});
            skLineSegment(sketch, "E318", {"start": v(-101.68, 7.3) * mm, "end": v(-101.69, 7.35) * mm});
            skLineSegment(sketch, "E319", {"start": v(-101.69, 7.35) * mm, "end": v(-101.7, 7.4) * mm});
            skLineSegment(sketch, "E320", {"start": v(-101.7, 7.4) * mm, "end": v(-101.71, 7.52) * mm});
            skLineSegment(sketch, "E321", {"start": v(-101.71, 7.52) * mm, "end": v(-101.72, 7.64) * mm});
            skLineSegment(sketch, "E322", {"start": v(-101.72, 7.64) * mm, "end": v(-101.72, 7.77) * mm});
            skLineSegment(sketch, "E323", {"start": v(-101.72, 7.77) * mm, "end": v(-101.72, 7.8) * mm});
            skLineSegment(sketch, "E324", {"start": v(-101.72, 7.8) * mm, "end": v(-101.72, 7.82) * mm});
            skLineSegment(sketch, "E325", {"start": v(-101.72, 7.82) * mm, "end": v(-101.72, 7.85) * mm});
            skLineSegment(sketch, "E326", {"start": v(-101.72, 7.85) * mm, "end": v(-101.72, 7.88) * mm});
            skLineSegment(sketch, "E327", {"start": v(-101.72, 7.88) * mm, "end": v(-101.72, 7.9) * mm});
            skLineSegment(sketch, "E328", {"start": v(-101.72, 7.9) * mm, "end": v(-101.71, 7.94) * mm});
            skLineSegment(sketch, "E329", {"start": v(-101.71, 7.94) * mm, "end": v(-101.71, 7.97) * mm});
            skLineSegment(sketch, "E330", {"start": v(-101.71, 7.97) * mm, "end": v(-101.7, 8) * mm});
            skLineSegment(sketch, "E331", {"start": v(-101.7, 8) * mm, "end": v(-101.7, 8.04) * mm});
            skLineSegment(sketch, "E332", {"start": v(-101.7, 8.04) * mm, "end": v(-101.7, 8.12) * mm});
            skLineSegment(sketch, "E333", {"start": v(-101.7, 8.12) * mm, "end": v(-101.69, 8.2) * mm});
            skLineSegment(sketch, "E334", {"start": v(-101.69, 8.2) * mm, "end": v(-101.68, 8.3) * mm});
            skLineSegment(sketch, "E335", {"start": v(-101.68, 8.3) * mm, "end": v(-101.66, 8.4) * mm});
            skLineSegment(sketch, "E336", {"start": v(-101.66, 8.4) * mm, "end": v(-101.65, 8.5) * mm});
            skLineSegment(sketch, "E337", {"start": v(-101.65, 8.5) * mm, "end": v(-101.63, 8.6) * mm});
            skLineSegment(sketch, "E338", {"start": v(-101.63, 8.6) * mm, "end": v(-101.61, 8.73) * mm});
            skLineSegment(sketch, "E339", {"start": v(-101.61, 8.73) * mm, "end": v(-101.6, 8.85) * mm});
            skLineSegment(sketch, "E340", {"start": v(-101.6, 8.85) * mm, "end": v(-101.57, 8.98) * mm});
            skLineSegment(sketch, "E341", {"start": v(-101.57, 8.98) * mm, "end": v(-101.55, 9.12) * mm});
            skLineSegment(sketch, "E342", {"start": v(-101.55, 9.12) * mm, "end": v(-101.51, 9.34) * mm});
            skLineSegment(sketch, "E343", {"start": v(-101.51, 9.34) * mm, "end": v(-101.4, 9.88) * mm});
            skLineSegment(sketch, "E344", {"start": v(-101.4, 9.88) * mm, "end": v(-101.28, 10.4) * mm});
            skLineSegment(sketch, "E345", {"start": v(-101.28, 10.4) * mm, "end": v(-101.15, 10.89) * mm});
            skLineSegment(sketch, "E346", {"start": v(-101.15, 10.89) * mm, "end": v(-101, 11.35) * mm});
            skLineSegment(sketch, "E347", {"start": v(-101, 11.35) * mm, "end": v(-100.84, 11.78) * mm});
            skLineSegment(sketch, "E348", {"start": v(-100.84, 11.78) * mm, "end": v(-100.67, 12.2) * mm});
            skLineSegment(sketch, "E349", {"start": v(-100.67, 12.2) * mm, "end": v(-100.49, 12.57) * mm});
            skLineSegment(sketch, "E350", {"start": v(-100.49, 12.57) * mm, "end": v(-100.29, 12.92) * mm});
            skLineSegment(sketch, "E351", {"start": v(-100.29, 12.92) * mm, "end": v(-100.06, 13.25) * mm});
            skLineSegment(sketch, "E352", {"start": v(-100.06, 13.25) * mm, "end": v(-99.81, 13.57) * mm});
            skLineSegment(sketch, "E353", {"start": v(-99.81, 13.57) * mm, "end": v(-99.53, 13.86) * mm});
            skLineSegment(sketch, "E354", {"start": v(-99.53, 13.86) * mm, "end": v(-99.23, 14.15) * mm});
            skLineSegment(sketch, "E355", {"start": v(-99.23, 14.15) * mm, "end": v(-98.9, 14.41) * mm});
            skLineSegment(sketch, "E356", {"start": v(-98.9, 14.41) * mm, "end": v(-98.53, 14.66) * mm});
            skLineSegment(sketch, "E357", {"start": v(-98.53, 14.66) * mm, "end": v(-98.15, 14.9) * mm});
            skLineSegment(sketch, "E358", {"start": v(-98.15, 14.9) * mm, "end": v(-97.73, 15.12) * mm});
            skLineSegment(sketch, "E359", {"start": v(-97.73, 15.12) * mm, "end": v(-97.28, 15.33) * mm});
            skLineSegment(sketch, "E360", {"start": v(-97.28, 15.33) * mm, "end": v(-96.79, 15.53) * mm});
            skLineSegment(sketch, "E361", {"start": v(-96.79, 15.53) * mm, "end": v(-96.26, 15.71) * mm});
            skLineSegment(sketch, "E362", {"start": v(-96.26, 15.71) * mm, "end": v(-95.68, 15.9) * mm});
            skLineSegment(sketch, "E363", {"start": v(-95.68, 15.9) * mm, "end": v(-95.07, 16.06) * mm});
            skLineSegment(sketch, "E364", {"start": v(-95.07, 16.06) * mm, "end": v(-94.42, 16.21) * mm});
            skLineSegment(sketch, "E365", {"start": v(-94.42, 16.21) * mm, "end": v(-93.72, 16.36) * mm});
            skLineSegment(sketch, "E366", {"start": v(-93.72, 16.36) * mm, "end": v(-92.99, 16.49) * mm});
            skLineSegment(sketch, "E367", {"start": v(-92.99, 16.49) * mm, "end": v(-91.75, 16.7) * mm});
            skLineSegment(sketch, "E368", {"start": v(-91.75, 16.7) * mm, "end": v(-90.57, 16.87) * mm});
            skLineSegment(sketch, "E369", {"start": v(-90.57, 16.87) * mm, "end": v(-89.44, 17.01) * mm});
            skLineSegment(sketch, "E370", {"start": v(-89.44, 17.01) * mm, "end": v(-88.36, 17.14) * mm});
            skLineSegment(sketch, "E371", {"start": v(-88.36, 17.14) * mm, "end": v(-87.34, 17.23) * mm});
            skLineSegment(sketch, "E372", {"start": v(-87.34, 17.23) * mm, "end": v(-86.38, 17.3) * mm});
            skLineSegment(sketch, "E373", {"start": v(-86.38, 17.3) * mm, "end": v(-85.47, 17.34) * mm});
            skLineSegment(sketch, "E374", {"start": v(-85.47, 17.34) * mm, "end": v(-84.61, 17.35) * mm});
            skLineSegment(sketch, "E375", {"start": v(-84.61, 17.35) * mm, "end": v(-84.02, 17.35) * mm});
            skLineSegment(sketch, "E376", {"start": v(-84.02, 17.35) * mm, "end": v(-83.45, 17.34) * mm});
            skLineSegment(sketch, "E377", {"start": v(-83.45, 17.34) * mm, "end": v(-82.92, 17.32) * mm});
            skLineSegment(sketch, "E378", {"start": v(-82.92, 17.32) * mm, "end": v(-82.42, 17.3) * mm});
            skLineSegment(sketch, "E379", {"start": v(-82.42, 17.3) * mm, "end": v(-81.96, 17.27) * mm});
            skLineSegment(sketch, "E380", {"start": v(-81.96, 17.27) * mm, "end": v(-81.52, 17.23) * mm});
            skLineSegment(sketch, "E381", {"start": v(-81.52, 17.23) * mm, "end": v(-81.12, 17.2) * mm});
            skLineSegment(sketch, "E382", {"start": v(-81.12, 17.2) * mm, "end": v(-80.93, 17.17) * mm});
            skLineSegment(sketch, "E383", {"start": v(-80.93, 17.17) * mm, "end": v(-80.75, 17.14) * mm});
            skLineSegment(sketch, "E384", {"start": v(-80.75, 17.14) * mm, "end": v(-80.4, 17.1) * mm});
            skLineSegment(sketch, "E385", {"start": v(-80.4, 17.1) * mm, "end": v(-80.1, 17.03) * mm});
            skLineSegment(sketch, "E386", {"start": v(-80.1, 17.03) * mm, "end": v(-79.8, 16.97) * mm});
            skLineSegment(sketch, "E387", {"start": v(-79.8, 16.97) * mm, "end": v(-79.66, 16.94) * mm});
            skLineSegment(sketch, "E388", {"start": v(-79.66, 16.94) * mm, "end": v(-79.53, 16.9) * mm});
            skLineSegment(sketch, "E389", {"start": v(-79.53, 16.9) * mm, "end": v(-79.4, 16.87) * mm});
            skLineSegment(sketch, "E390", {"start": v(-79.4, 16.87) * mm, "end": v(-79.28, 16.83) * mm});
            skLineSegment(sketch, "E391", {"start": v(-79.28, 16.83) * mm, "end": v(-79.17, 16.8) * mm});
            skLineSegment(sketch, "E392", {"start": v(-79.17, 16.8) * mm, "end": v(-79.06, 16.75) * mm});
            skLineSegment(sketch, "E393", {"start": v(-79.06, 16.75) * mm, "end": v(-78.96, 16.7) * mm});
            skLineSegment(sketch, "E394", {"start": v(-78.96, 16.7) * mm, "end": v(-78.86, 16.66) * mm});
            skLineSegment(sketch, "E395", {"start": v(-78.86, 16.66) * mm, "end": v(-78.77, 16.62) * mm});
            skLineSegment(sketch, "E396", {"start": v(-78.77, 16.62) * mm, "end": v(-78.68, 16.57) * mm});
            skLineSegment(sketch, "E397", {"start": v(-78.68, 16.57) * mm, "end": v(-78.52, 16.48) * mm});
            skLineSegment(sketch, "E398", {"start": v(-78.52, 16.48) * mm, "end": v(-78.45, 16.43) * mm});
            skLineSegment(sketch, "E399", {"start": v(-78.45, 16.43) * mm, "end": v(-78.38, 16.38) * mm});
            skLineSegment(sketch, "E400", {"start": v(-78.38, 16.38) * mm, "end": v(-78.31, 16.33) * mm});
            skLineSegment(sketch, "E401", {"start": v(-78.31, 16.33) * mm, "end": v(-78.25, 16.29) * mm});
            skLineSegment(sketch, "E402", {"start": v(-78.25, 16.29) * mm, "end": v(-78.19, 16.24) * mm});
            skLineSegment(sketch, "E403", {"start": v(-78.19, 16.24) * mm, "end": v(-78.14, 16.2) * mm});
            skLineSegment(sketch, "E404", {"start": v(-78.14, 16.2) * mm, "end": v(-78.08, 16.14) * mm});
            skLineSegment(sketch, "E405", {"start": v(-78.08, 16.14) * mm, "end": v(-78.04, 16.1) * mm});
            skLineSegment(sketch, "E406", {"start": v(-78.04, 16.1) * mm, "end": v(-78, 16.05) * mm});
            skLineSegment(sketch, "E407", {"start": v(-78, 16.05) * mm, "end": v(-77.96, 16) * mm});
            skLineSegment(sketch, "E408", {"start": v(-77.96, 16) * mm, "end": v(-77.92, 15.95) * mm});
            skLineSegment(sketch, "E409", {"start": v(-77.92, 15.95) * mm, "end": v(-77.89, 15.9) * mm});
            skLineSegment(sketch, "E410", {"start": v(-77.89, 15.9) * mm, "end": v(-77.86, 15.86) * mm});
            skLineSegment(sketch, "E411", {"start": v(-77.86, 15.86) * mm, "end": v(-77.84, 15.81) * mm});
            skLineSegment(sketch, "E412", {"start": v(-77.84, 15.81) * mm, "end": v(-77.82, 15.77) * mm});
            skLineSegment(sketch, "E413", {"start": v(-77.82, 15.77) * mm, "end": v(-77.8, 15.71) * mm});
            skLineSegment(sketch, "E414", {"start": v(-77.8, 15.71) * mm, "end": v(-77.76, 15.66) * mm});
            skLineSegment(sketch, "E415", {"start": v(-77.76, 15.66) * mm, "end": v(-77.74, 15.6) * mm});
            skLineSegment(sketch, "E416", {"start": v(-77.74, 15.6) * mm, "end": v(-77.71, 15.53) * mm});
            skLineSegment(sketch, "E417", {"start": v(-77.71, 15.53) * mm, "end": v(-77.68, 15.47) * mm});
            skLineSegment(sketch, "E418", {"start": v(-77.68, 15.47) * mm, "end": v(-77.65, 15.4) * mm});
            skLineSegment(sketch, "E419", {"start": v(-77.65, 15.4) * mm, "end": v(-77.62, 15.32) * mm});
            skLineSegment(sketch, "E420", {"start": v(-77.62, 15.32) * mm, "end": v(-77.6, 15.24) * mm});
            skLineSegment(sketch, "E421", {"start": v(-77.6, 15.24) * mm, "end": v(-77.56, 15.15) * mm});
            skLineSegment(sketch, "E422", {"start": v(-77.56, 15.15) * mm, "end": v(-77.53, 15.06) * mm});
            skLineSegment(sketch, "E423", {"start": v(-77.53, 15.06) * mm, "end": v(-77.46, 14.87) * mm});
            skLineSegment(sketch, "E424", {"start": v(-77.46, 14.87) * mm, "end": v(-77.4, 14.66) * mm});
            skLineSegment(sketch, "E425", {"start": v(-77.4, 14.66) * mm, "end": v(-77.35, 14.55) * mm});
            skLineSegment(sketch, "E426", {"start": v(-77.35, 14.55) * mm, "end": v(-76.7, 12.6) * mm});
            skLineSegment(sketch, "E427", {"start": v(-76.7, 12.6) * mm, "end": v(-76.67, 12.51) * mm});
            skLineSegment(sketch, "E428", {"start": v(-76.67, 12.51) * mm, "end": v(-76.66, 12.47) * mm});
            skLineSegment(sketch, "E429", {"start": v(-76.66, 12.47) * mm, "end": v(-76.64, 12.43) * mm});
            skLineSegment(sketch, "E430", {"start": v(-76.64, 12.43) * mm, "end": v(-76.63, 12.4) * mm});
            skLineSegment(sketch, "E431", {"start": v(-76.63, 12.4) * mm, "end": v(-76.62, 12.36) * mm});
            skLineSegment(sketch, "E432", {"start": v(-76.62, 12.36) * mm, "end": v(-76.6, 12.32) * mm});
            skLineSegment(sketch, "E433", {"start": v(-76.6, 12.32) * mm, "end": v(-76.6, 12.29) * mm});
            skLineSegment(sketch, "E434", {"start": v(-76.6, 12.29) * mm, "end": v(-76.58, 12.23) * mm});
            skLineSegment(sketch, "E435", {"start": v(-76.58, 12.23) * mm, "end": v(-76.56, 12.18) * mm});
            skLineSegment(sketch, "E436", {"start": v(-76.56, 12.18) * mm, "end": v(-76.54, 12.12) * mm});
            skLineSegment(sketch, "E437", {"start": v(-76.54, 12.12) * mm, "end": v(-76.53, 12.06) * mm});
            skLineSegment(sketch, "E438", {"start": v(-76.53, 12.06) * mm, "end": v(-76.52, 12.03) * mm});
            skLineSegment(sketch, "E439", {"start": v(-76.52, 12.03) * mm, "end": v(-76.51, 12) * mm});
            skLineSegment(sketch, "E440", {"start": v(-76.51, 12) * mm, "end": v(-76.5, 11.96) * mm});
            skLineSegment(sketch, "E441", {"start": v(-76.5, 11.96) * mm, "end": v(-76.5, 11.94) * mm});
            skLineSegment(sketch, "E442", {"start": v(-76.5, 11.94) * mm, "end": v(-76.5, 11.9) * mm});
            skLineSegment(sketch, "E443", {"start": v(-76.5, 11.9) * mm, "end": v(-76.5, 11.88) * mm});
            skLineSegment(sketch, "E444", {"start": v(-76.5, 11.88) * mm, "end": v(-76.5, 11.85) * mm});
            skLineSegment(sketch, "E445", {"start": v(-76.5, 11.85) * mm, "end": v(-76.49, 11.82) * mm});
            skLineSegment(sketch, "E446", {"start": v(-76.49, 11.82) * mm, "end": v(-76.5, 11.62) * mm});
            skLineSegment(sketch, "E447", {"start": v(-76.5, 11.62) * mm, "end": v(-76.51, 11.42) * mm});
            skLineSegment(sketch, "E448", {"start": v(-76.51, 11.42) * mm, "end": v(-76.54, 11.23) * mm});
            skLineSegment(sketch, "E449", {"start": v(-76.54, 11.23) * mm, "end": v(-76.58, 11.04) * mm});
            skLineSegment(sketch, "E450", {"start": v(-76.58, 11.04) * mm, "end": v(-76.64, 10.86) * mm});
            skLineSegment(sketch, "E451", {"start": v(-76.64, 10.86) * mm, "end": v(-76.7, 10.69) * mm});
            skLineSegment(sketch, "E452", {"start": v(-76.7, 10.69) * mm, "end": v(-76.78, 10.51) * mm});
            skLineSegment(sketch, "E453", {"start": v(-76.78, 10.51) * mm, "end": v(-76.87, 10.35) * mm});
            skLineSegment(sketch, "E454", {"start": v(-76.87, 10.35) * mm, "end": v(-76.92, 10.26) * mm});
            skLineSegment(sketch, "E455", {"start": v(-76.92, 10.26) * mm, "end": v(-76.97, 10.17) * mm});
            skLineSegment(sketch, "E456", {"start": v(-76.97, 10.17) * mm, "end": v(-77.03, 10.08) * mm});
            skLineSegment(sketch, "E457", {"start": v(-77.03, 10.08) * mm, "end": v(-77.09, 9.98) * mm});
            skLineSegment(sketch, "E458", {"start": v(-77.09, 9.98) * mm, "end": v(-77.16, 9.88) * mm});
            skLineSegment(sketch, "E459", {"start": v(-77.16, 9.88) * mm, "end": v(-77.23, 9.77) * mm});
            skLineSegment(sketch, "E460", {"start": v(-77.23, 9.77) * mm, "end": v(-77.3, 9.65) * mm});
            skLineSegment(sketch, "E461", {"start": v(-77.3, 9.65) * mm, "end": v(-77.39, 9.53) * mm});
            skLineSegment(sketch, "E462", {"start": v(-77.39, 9.53) * mm, "end": v(-77.47, 9.4) * mm});
            skLineSegment(sketch, "E463", {"start": v(-77.47, 9.4) * mm, "end": v(-77.56, 9.28) * mm});
            skLineSegment(sketch, "E464", {"start": v(-77.56, 9.28) * mm, "end": v(-77.76, 9) * mm});
            skLineSegment(sketch, "E465", {"start": v(-77.76, 9) * mm, "end": v(-77.98, 8.7) * mm});
            skLineSegment(sketch, "E466", {"start": v(-77.98, 8.7) * mm, "end": v(-78.22, 8.39) * mm});
            skLineSegment(sketch, "E467", {"start": v(-78.22, 8.39) * mm, "end": v(-78.45, 8.07) * mm});
            skLineSegment(sketch, "E468", {"start": v(-78.45, 8.07) * mm, "end": v(-78.67, 7.77) * mm});
            skLineSegment(sketch, "E469", {"start": v(-78.67, 7.77) * mm, "end": v(-78.88, 7.49) * mm});
            skLineSegment(sketch, "E470", {"start": v(-78.88, 7.49) * mm, "end": v(-79.06, 7.22) * mm});
            skLineSegment(sketch, "E471", {"start": v(-79.06, 7.22) * mm, "end": v(-79.23, 6.97) * mm});
            skLineSegment(sketch, "E472", {"start": v(-79.23, 6.97) * mm, "end": v(-79.4, 6.74) * mm});
            skLineSegment(sketch, "E473", {"start": v(-79.4, 6.74) * mm, "end": v(-79.46, 6.64) * mm});
            skLineSegment(sketch, "E474", {"start": v(-79.46, 6.64) * mm, "end": v(-79.53, 6.53) * mm});
            skLineSegment(sketch, "E475", {"start": v(-79.53, 6.53) * mm, "end": v(-79.6, 6.43) * mm});
            skLineSegment(sketch, "E476", {"start": v(-79.6, 6.43) * mm, "end": v(-79.65, 6.34) * mm});
            skLineSegment(sketch, "E477", {"start": v(-79.65, 6.34) * mm, "end": v(-80.96, 4.2) * mm});
            skLineSegment(sketch, "E478", {"start": v(-80.96, 4.2) * mm, "end": v(-82.16, 2.2) * mm});
            skLineSegment(sketch, "E479", {"start": v(-82.16, 2.2) * mm, "end": v(-83.25, 0.36) * mm});
            skLineSegment(sketch, "E480", {"start": v(-83.25, 0.36) * mm, "end": v(-83.75, -0.51) * mm});
            skLineSegment(sketch, "E481", {"start": v(-83.75, -0.51) * mm, "end": v(-84.23, -1.35) * mm});
            skLineSegment(sketch, "E482", {"start": v(-84.23, -1.35) * mm, "end": v(-84.68, -2.15) * mm});
            skLineSegment(sketch, "E483", {"start": v(-84.68, -2.15) * mm, "end": v(-85.1, -2.91) * mm});
            skLineSegment(sketch, "E484", {"start": v(-85.1, -2.91) * mm, "end": v(-85.5, -3.64) * mm});
            skLineSegment(sketch, "E485", {"start": v(-85.5, -3.64) * mm, "end": v(-85.87, -4.33) * mm});
            skLineSegment(sketch, "E486", {"start": v(-85.87, -4.33) * mm, "end": v(-86.21, -4.99) * mm});
            skLineSegment(sketch, "E487", {"start": v(-86.21, -4.99) * mm, "end": v(-86.53, -5.6) * mm});
            skLineSegment(sketch, "E488", {"start": v(-86.53, -5.6) * mm, "end": v(-86.82, -6.2) * mm});
            skLineSegment(sketch, "E489", {"start": v(-86.82, -6.2) * mm, "end": v(-87.08, -6.74) * mm});
            skLineSegment(sketch, "E490", {"start": v(-65.79, -2.86) * mm, "end": v(-66.53, -3.83) * mm});
            skLineSegment(sketch, "E491", {"start": v(-66.53, -3.83) * mm, "end": v(-67.23, -4.74) * mm});
            skLineSegment(sketch, "E492", {"start": v(-67.23, -4.74) * mm, "end": v(-67.88, -5.57) * mm});
            skLineSegment(sketch, "E493", {"start": v(-67.88, -5.57) * mm, "end": v(-68.19, -5.95) * mm});
            skLineSegment(sketch, "E494", {"start": v(-68.19, -5.95) * mm, "end": v(-68.48, -6.32) * mm});
            skLineSegment(sketch, "E495", {"start": v(-68.48, -6.32) * mm, "end": v(-68.77, -6.67) * mm});
            skLineSegment(sketch, "E496", {"start": v(-68.77, -6.67) * mm, "end": v(-69.04, -7) * mm});
            skLineSegment(sketch, "E497", {"start": v(-69.04, -7) * mm, "end": v(-69.3, -7.32) * mm});
            skLineSegment(sketch, "E498", {"start": v(-69.3, -7.32) * mm, "end": v(-69.56, -7.62) * mm});
            skLineSegment(sketch, "E499", {"start": v(-69.56, -7.62) * mm, "end": v(-69.8, -7.9) * mm});
            skLineSegment(sketch, "E500", {"start": v(-69.8, -7.9) * mm, "end": v(-70.03, -8.15) * mm});
            skLineSegment(sketch, "E501", {"start": v(-70.03, -8.15) * mm, "end": v(-70.25, -8.4) * mm});
            skLineSegment(sketch, "E502", {"start": v(-70.25, -8.4) * mm, "end": v(-70.45, -8.62) * mm});
            skLineSegment(sketch, "E503", {"start": v(-70.45, -8.62) * mm, "end": v(-70.65, -8.83) * mm});
            skLineSegment(sketch, "E504", {"start": v(-70.65, -8.83) * mm, "end": v(-70.84, -9.02) * mm});
            skLineSegment(sketch, "E505", {"start": v(-70.84, -9.02) * mm, "end": v(-71.03, -9.2) * mm});
            skLineSegment(sketch, "E506", {"start": v(-71.03, -9.2) * mm, "end": v(-71.2, -9.37) * mm});
            skLineSegment(sketch, "E507", {"start": v(-71.2, -9.37) * mm, "end": v(-71.39, -9.52) * mm});
            skLineSegment(sketch, "E508", {"start": v(-71.39, -9.52) * mm, "end": v(-71.56, -9.66) * mm});
            skLineSegment(sketch, "E509", {"start": v(-71.56, -9.66) * mm, "end": v(-71.73, -9.79) * mm});
            skLineSegment(sketch, "E510", {"start": v(-71.73, -9.79) * mm, "end": v(-71.9, -9.9) * mm});
            skLineSegment(sketch, "E511", {"start": v(-71.9, -9.9) * mm, "end": v(-72.05, -10) * mm});
            skLineSegment(sketch, "E512", {"start": v(-72.05, -10) * mm, "end": v(-72.2, -10.09) * mm});
            skLineSegment(sketch, "E513", {"start": v(-72.2, -10.09) * mm, "end": v(-72.36, -10.16) * mm});
            skLineSegment(sketch, "E514", {"start": v(-72.36, -10.16) * mm, "end": v(-72.43, -10.2) * mm});
            skLineSegment(sketch, "E515", {"start": v(-72.43, -10.2) * mm, "end": v(-72.5, -10.22) * mm});
            skLineSegment(sketch, "E516", {"start": v(-72.5, -10.22) * mm, "end": v(-72.58, -10.25) * mm});
            skLineSegment(sketch, "E517", {"start": v(-72.58, -10.25) * mm, "end": v(-72.65, -10.27) * mm});
            skLineSegment(sketch, "E518", {"start": v(-72.65, -10.27) * mm, "end": v(-72.72, -10.29) * mm});
            skLineSegment(sketch, "E519", {"start": v(-72.72, -10.29) * mm, "end": v(-72.78, -10.3) * mm});
            skLineSegment(sketch, "E520", {"start": v(-72.78, -10.3) * mm, "end": v(-72.85, -10.31) * mm});
            skLineSegment(sketch, "E521", {"start": v(-72.85, -10.31) * mm, "end": v(-72.92, -10.32) * mm});
            skLineSegment(sketch, "E522", {"start": v(-72.92, -10.32) * mm, "end": v(-72.98, -10.33) * mm});
            skLineSegment(sketch, "E523", {"start": v(-72.98, -10.33) * mm, "end": v(-73.05, -10.33) * mm});
            skLineSegment(sketch, "E524", {"start": v(-73.05, -10.33) * mm, "end": v(-73.15, -10.32) * mm});
            skLineSegment(sketch, "E525", {"start": v(-73.15, -10.32) * mm, "end": v(-73.25, -10.32) * mm});
            skLineSegment(sketch, "E526", {"start": v(-73.25, -10.32) * mm, "end": v(-73.34, -10.3) * mm});
            skLineSegment(sketch, "E527", {"start": v(-73.34, -10.3) * mm, "end": v(-73.44, -10.29) * mm});
            skLineSegment(sketch, "E528", {"start": v(-73.44, -10.29) * mm, "end": v(-73.54, -10.26) * mm});
            skLineSegment(sketch, "E529", {"start": v(-73.54, -10.26) * mm, "end": v(-73.63, -10.24) * mm});
            skLineSegment(sketch, "E530", {"start": v(-73.63, -10.24) * mm, "end": v(-73.72, -10.2) * mm});
            skLineSegment(sketch, "E531", {"start": v(-73.72, -10.2) * mm, "end": v(-73.82, -10.16) * mm});
            skLineSegment(sketch, "E532", {"start": v(-73.82, -10.16) * mm, "end": v(-73.9, -10.12) * mm});
            skLineSegment(sketch, "E533", {"start": v(-73.9, -10.12) * mm, "end": v(-74, -10.07) * mm});
            skLineSegment(sketch, "E534", {"start": v(-74, -10.07) * mm, "end": v(-74.09, -10.02) * mm});
            skLineSegment(sketch, "E535", {"start": v(-74.09, -10.02) * mm, "end": v(-74.18, -9.96) * mm});
            skLineSegment(sketch, "E536", {"start": v(-74.18, -9.96) * mm, "end": v(-74.27, -9.9) * mm});
            skLineSegment(sketch, "E537", {"start": v(-74.27, -9.9) * mm, "end": v(-74.35, -9.83) * mm});
            skLineSegment(sketch, "E538", {"start": v(-74.35, -9.83) * mm, "end": v(-74.44, -9.75) * mm});
            skLineSegment(sketch, "E539", {"start": v(-74.44, -9.75) * mm, "end": v(-74.52, -9.67) * mm});
            skLineSegment(sketch, "E540", {"start": v(-74.52, -9.67) * mm, "end": v(-74.69, -9.5) * mm});
            skLineSegment(sketch, "E541", {"start": v(-74.69, -9.5) * mm, "end": v(-74.84, -9.3) * mm});
            skLineSegment(sketch, "E542", {"start": v(-74.84, -9.3) * mm, "end": v(-74.99, -9.1) * mm});
            skLineSegment(sketch, "E543", {"start": v(-74.99, -9.1) * mm, "end": v(-75.12, -8.89) * mm});
            skLineSegment(sketch, "E544", {"start": v(-75.12, -8.89) * mm, "end": v(-75.25, -8.66) * mm});
            skLineSegment(sketch, "E545", {"start": v(-75.25, -8.66) * mm, "end": v(-75.37, -8.41) * mm});
            skLineSegment(sketch, "E546", {"start": v(-75.37, -8.41) * mm, "end": v(-75.48, -8.15) * mm});
            skLineSegment(sketch, "E547", {"start": v(-75.48, -8.15) * mm, "end": v(-75.58, -7.88) * mm});
            skLineSegment(sketch, "E548", {"start": v(-75.58, -7.88) * mm, "end": v(-75.74, -7.3) * mm});
            skLineSegment(sketch, "E549", {"start": v(-75.74, -7.3) * mm, "end": v(-75.85, -6.7) * mm});
            skLineSegment(sketch, "E550", {"start": v(-75.85, -6.7) * mm, "end": v(-75.91, -6.09) * mm});
            skLineSegment(sketch, "E551", {"start": v(-75.91, -6.09) * mm, "end": v(-75.94, -5.45) * mm});
            skLineSegment(sketch, "E552", {"start": v(-75.94, -5.45) * mm, "end": v(-75.93, -5.04) * mm});
            skLineSegment(sketch, "E553", {"start": v(-75.93, -5.04) * mm, "end": v(-75.9, -4.65) * mm});
            skLineSegment(sketch, "E554", {"start": v(-75.9, -4.65) * mm, "end": v(-75.85, -4.28) * mm});
            skLineSegment(sketch, "E555", {"start": v(-75.85, -4.28) * mm, "end": v(-75.79, -3.93) * mm});
            skLineSegment(sketch, "E556", {"start": v(-75.79, -3.93) * mm, "end": v(-75.74, -3.76) * mm});
            skLineSegment(sketch, "E557", {"start": v(-75.74, -3.76) * mm, "end": v(-75.69, -3.59) * mm});
            skLineSegment(sketch, "E558", {"start": v(-75.69, -3.59) * mm, "end": v(-75.62, -3.41) * mm});
            skLineSegment(sketch, "E559", {"start": v(-75.62, -3.41) * mm, "end": v(-75.55, -3.23) * mm});
            skLineSegment(sketch, "E560", {"start": v(-75.55, -3.23) * mm, "end": v(-75.47, -3.04) * mm});
            skLineSegment(sketch, "E561", {"start": v(-75.47, -3.04) * mm, "end": v(-75.38, -2.85) * mm});
            skLineSegment(sketch, "E562", {"start": v(-75.38, -2.85) * mm, "end": v(-75.18, -2.46) * mm});
            skLineSegment(sketch, "E563", {"start": v(-75.18, -2.46) * mm, "end": v(-74.94, -2.04) * mm});
            skLineSegment(sketch, "E564", {"start": v(-74.94, -2.04) * mm, "end": v(-74.67, -1.6) * mm});
            skLineSegment(sketch, "E565", {"start": v(-74.67, -1.6) * mm, "end": v(-74.36, -1.15) * mm});
            skLineSegment(sketch, "E566", {"start": v(-74.36, -1.15) * mm, "end": v(-74.02, -0.69) * mm});
            skLineSegment(sketch, "E567", {"start": v(-74.02, -0.69) * mm, "end": v(-73.63, -0.2) * mm});
            skLineSegment(sketch, "E568", {"start": v(-73.63, -0.2) * mm, "end": v(-73.2, 0.33) * mm});
            skLineSegment(sketch, "E569", {"start": v(-73.2, 0.33) * mm, "end": v(-72.73, 0.88) * mm});
            skLineSegment(sketch, "E570", {"start": v(-72.73, 0.88) * mm, "end": v(-72.22, 1.47) * mm});
            skLineSegment(sketch, "E571", {"start": v(-72.22, 1.47) * mm, "end": v(-71.92, 1.82) * mm});
            skLineSegment(sketch, "E572", {"start": v(-71.92, 1.82) * mm, "end": v(-71.78, 1.99) * mm});
            skLineSegment(sketch, "E573", {"start": v(-71.78, 1.99) * mm, "end": v(-71.64, 2.15) * mm});
            skLineSegment(sketch, "E574", {"start": v(-71.64, 2.15) * mm, "end": v(-71.52, 2.3) * mm});
            skLineSegment(sketch, "E575", {"start": v(-71.52, 2.3) * mm, "end": v(-71.4, 2.44) * mm});
            skLineSegment(sketch, "E576", {"start": v(-71.4, 2.44) * mm, "end": v(-71.28, 2.58) * mm});
            skLineSegment(sketch, "E577", {"start": v(-71.28, 2.58) * mm, "end": v(-71.17, 2.71) * mm});
            skLineSegment(sketch, "E578", {"start": v(-71.17, 2.71) * mm, "end": v(-71.06, 2.83) * mm});
            skLineSegment(sketch, "E579", {"start": v(-71.06, 2.83) * mm, "end": v(-70.95, 2.94) * mm});
            skLineSegment(sketch, "E580", {"start": v(-70.95, 2.94) * mm, "end": v(-70.84, 3.04) * mm});
            skLineSegment(sketch, "E581", {"start": v(-70.84, 3.04) * mm, "end": v(-70.74, 3.13) * mm});
            skLineSegment(sketch, "E582", {"start": v(-70.74, 3.13) * mm, "end": v(-70.63, 3.21) * mm});
            skLineSegment(sketch, "E583", {"start": v(-70.63, 3.21) * mm, "end": v(-70.53, 3.28) * mm});
            skLineSegment(sketch, "E584", {"start": v(-70.53, 3.28) * mm, "end": v(-70.48, 3.31) * mm});
            skLineSegment(sketch, "E585", {"start": v(-70.48, 3.31) * mm, "end": v(-70.43, 3.34) * mm});
            skLineSegment(sketch, "E586", {"start": v(-70.43, 3.34) * mm, "end": v(-70.38, 3.36) * mm});
            skLineSegment(sketch, "E587", {"start": v(-70.38, 3.36) * mm, "end": v(-70.33, 3.39) * mm});
            skLineSegment(sketch, "E588", {"start": v(-70.33, 3.39) * mm, "end": v(-70.27, 3.4) * mm});
            skLineSegment(sketch, "E589", {"start": v(-70.27, 3.4) * mm, "end": v(-70.21, 3.43) * mm});
            skLineSegment(sketch, "E590", {"start": v(-70.21, 3.43) * mm, "end": v(-70.15, 3.45) * mm});
            skLineSegment(sketch, "E591", {"start": v(-70.15, 3.45) * mm, "end": v(-70.08, 3.47) * mm});
            skLineSegment(sketch, "E592", {"start": v(-70.08, 3.47) * mm, "end": v(-70.01, 3.49) * mm});
            skLineSegment(sketch, "E593", {"start": v(-70.01, 3.49) * mm, "end": v(-69.94, 3.5) * mm});
            skLineSegment(sketch, "E594", {"start": v(-69.94, 3.5) * mm, "end": v(-69.86, 3.52) * mm});
            skLineSegment(sketch, "E595", {"start": v(-69.86, 3.52) * mm, "end": v(-69.78, 3.53) * mm});
            skLineSegment(sketch, "E596", {"start": v(-69.78, 3.53) * mm, "end": v(-69.7, 3.54) * mm});
            skLineSegment(sketch, "E597", {"start": v(-69.7, 3.54) * mm, "end": v(-69.6, 3.55) * mm});
            skLineSegment(sketch, "E598", {"start": v(-69.6, 3.55) * mm, "end": v(-69.5, 3.56) * mm});
            skLineSegment(sketch, "E599", {"start": v(-69.5, 3.56) * mm, "end": v(-69.3, 3.57) * mm});
            skLineSegment(sketch, "E600", {"start": v(-69.3, 3.57) * mm, "end": v(-69.09, 3.58) * mm});
            skLineSegment(sketch, "E601", {"start": v(-69.09, 3.58) * mm, "end": v(-68.97, 3.58) * mm});
            skLineSegment(sketch, "E602", {"start": v(-68.97, 3.58) * mm, "end": v(-68.64, 3.56) * mm});
            skLineSegment(sketch, "E603", {"start": v(-68.64, 3.56) * mm, "end": v(-68.32, 3.53) * mm});
            skLineSegment(sketch, "E604", {"start": v(-68.32, 3.53) * mm, "end": v(-68, 3.47) * mm});
            skLineSegment(sketch, "E605", {"start": v(-68, 3.47) * mm, "end": v(-67.69, 3.39) * mm});
            skLineSegment(sketch, "E606", {"start": v(-67.69, 3.39) * mm, "end": v(-67.61, 3.36) * mm});
            skLineSegment(sketch, "E607", {"start": v(-67.61, 3.36) * mm, "end": v(-67.54, 3.34) * mm});
            skLineSegment(sketch, "E608", {"start": v(-67.54, 3.34) * mm, "end": v(-67.48, 3.32) * mm});
            skLineSegment(sketch, "E609", {"start": v(-67.48, 3.32) * mm, "end": v(-67.42, 3.3) * mm});
            skLineSegment(sketch, "E610", {"start": v(-67.42, 3.3) * mm, "end": v(-67.37, 3.28) * mm});
            skLineSegment(sketch, "E611", {"start": v(-67.37, 3.28) * mm, "end": v(-67.34, 3.27) * mm});
            skLineSegment(sketch, "E612", {"start": v(-67.34, 3.27) * mm, "end": v(-67.32, 3.26) * mm});
            skLineSegment(sketch, "E613", {"start": v(-67.32, 3.26) * mm, "end": v(-67.3, 3.25) * mm});
            skLineSegment(sketch, "E614", {"start": v(-67.3, 3.25) * mm, "end": v(-67.27, 3.23) * mm});
            skLineSegment(sketch, "E615", {"start": v(-67.27, 3.23) * mm, "end": v(-67.25, 3.22) * mm});
            skLineSegment(sketch, "E616", {"start": v(-67.25, 3.22) * mm, "end": v(-67.23, 3.21) * mm});
            skLineSegment(sketch, "E617", {"start": v(-67.23, 3.21) * mm, "end": v(-67.21, 3.2) * mm});
            skLineSegment(sketch, "E618", {"start": v(-67.21, 3.2) * mm, "end": v(-67.2, 3.19) * mm});
            skLineSegment(sketch, "E619", {"start": v(-67.2, 3.19) * mm, "end": v(-67.18, 3.18) * mm});
            skLineSegment(sketch, "E620", {"start": v(-67.18, 3.18) * mm, "end": v(-67.16, 3.17) * mm});
            skLineSegment(sketch, "E621", {"start": v(-67.16, 3.17) * mm, "end": v(-67.15, 3.16) * mm});
            skLineSegment(sketch, "E622", {"start": v(-67.15, 3.16) * mm, "end": v(-67.14, 3.14) * mm});
            skLineSegment(sketch, "E623", {"start": v(-67.14, 3.14) * mm, "end": v(-67.12, 3.13) * mm});
            skLineSegment(sketch, "E624", {"start": v(-67.12, 3.13) * mm, "end": v(-67.11, 3.12) * mm});
            skLineSegment(sketch, "E625", {"start": v(-67.11, 3.12) * mm, "end": v(-67.1, 3.1) * mm});
            skLineSegment(sketch, "E626", {"start": v(-67.1, 3.1) * mm, "end": v(-67.1, 3.1) * mm});
            skLineSegment(sketch, "E627", {"start": v(-67.1, 3.1) * mm, "end": v(-67.1, 3.09) * mm});
            skLineSegment(sketch, "E628", {"start": v(-67.1, 3.09) * mm, "end": v(-67.09, 3.08) * mm});
            skLineSegment(sketch, "E629", {"start": v(-67.09, 3.08) * mm, "end": v(-67.09, 3.07) * mm});
            skLineSegment(sketch, "E630", {"start": v(-67.09, 3.07) * mm, "end": v(-67.08, 3.07) * mm});
            skLineSegment(sketch, "E631", {"start": v(-67.08, 3.07) * mm, "end": v(-67.08, 3.06) * mm});
            skLineSegment(sketch, "E632", {"start": v(-67.08, 3.06) * mm, "end": v(-67.08, 3.06) * mm});
            skLineSegment(sketch, "E633", {"start": v(-67.08, 3.06) * mm, "end": v(-67.08, 3.05) * mm});
            skLineSegment(sketch, "E634", {"start": v(-67.08, 3.05) * mm, "end": v(-67.08, 3.05) * mm});
            skLineSegment(sketch, "E635", {"start": v(-67.08, 3.05) * mm, "end": v(-67.08, 3.04) * mm});
            skLineSegment(sketch, "E636", {"start": v(-67.08, 3.04) * mm, "end": v(-67.08, 3.03) * mm});
            skLineSegment(sketch, "E637", {"start": v(-67.08, 3.03) * mm, "end": v(-67.08, 3.03) * mm});
            skLineSegment(sketch, "E638", {"start": v(-67.08, 3.03) * mm, "end": v(-67.08, 3) * mm});
            skLineSegment(sketch, "E639", {"start": v(-67.08, 3) * mm, "end": v(-67.08, 2.98) * mm});
            skLineSegment(sketch, "E640", {"start": v(-67.08, 2.98) * mm, "end": v(-67.08, 2.95) * mm});
            skLineSegment(sketch, "E641", {"start": v(-67.08, 2.95) * mm, "end": v(-67.09, 2.92) * mm});
            skLineSegment(sketch, "E642", {"start": v(-67.09, 2.92) * mm, "end": v(-67.1, 2.9) * mm});
            skLineSegment(sketch, "E643", {"start": v(-67.1, 2.9) * mm, "end": v(-67.1, 2.86) * mm});
            skLineSegment(sketch, "E644", {"start": v(-67.1, 2.86) * mm, "end": v(-67.1, 2.83) * mm});
            skLineSegment(sketch, "E645", {"start": v(-67.1, 2.83) * mm, "end": v(-67.12, 2.8) * mm});
            skLineSegment(sketch, "E646", {"start": v(-67.12, 2.8) * mm, "end": v(-67.13, 2.77) * mm});
            skLineSegment(sketch, "E647", {"start": v(-67.13, 2.77) * mm, "end": v(-67.14, 2.73) * mm});
            skLineSegment(sketch, "E648", {"start": v(-67.14, 2.73) * mm, "end": v(-67.15, 2.7) * mm});
            skLineSegment(sketch, "E649", {"start": v(-67.15, 2.7) * mm, "end": v(-67.18, 2.62) * mm});
            skLineSegment(sketch, "E650", {"start": v(-67.18, 2.62) * mm, "end": v(-67.22, 2.54) * mm});
            skLineSegment(sketch, "E651", {"start": v(-67.22, 2.54) * mm, "end": v(-67.25, 2.45) * mm});
            skLineSegment(sketch, "E652", {"start": v(-67.25, 2.45) * mm, "end": v(-67.3, 2.36) * mm});
            skLineSegment(sketch, "E653", {"start": v(-67.3, 2.36) * mm, "end": v(-67.35, 2.27) * mm});
            skLineSegment(sketch, "E654", {"start": v(-67.35, 2.27) * mm, "end": v(-67.4, 2.17) * mm});
            skLineSegment(sketch, "E655", {"start": v(-67.4, 2.17) * mm, "end": v(-67.46, 2.06) * mm});
            skLineSegment(sketch, "E656", {"start": v(-67.46, 2.06) * mm, "end": v(-67.53, 1.95) * mm});
            skLineSegment(sketch, "E657", {"start": v(-67.53, 1.95) * mm, "end": v(-67.6, 1.84) * mm});
            skLineSegment(sketch, "E658", {"start": v(-67.6, 1.84) * mm, "end": v(-67.7, 1.66) * mm});
            skLineSegment(sketch, "E659", {"start": v(-67.7, 1.66) * mm, "end": v(-67.79, 1.53) * mm});
            skLineSegment(sketch, "E660", {"start": v(-67.79, 1.53) * mm, "end": v(-67.87, 1.4) * mm});
            skLineSegment(sketch, "E661", {"start": v(-67.87, 1.4) * mm, "end": v(-68.06, 1.13) * mm});
            skLineSegment(sketch, "E662", {"start": v(-68.06, 1.13) * mm, "end": v(-68.28, 0.85) * mm});
            skLineSegment(sketch, "E663", {"start": v(-68.28, 0.85) * mm, "end": v(-68.52, 0.55) * mm});
            skLineSegment(sketch, "E664", {"start": v(-68.52, 0.55) * mm, "end": v(-68.78, 0.24) * mm});
            skLineSegment(sketch, "E665", {"start": v(-68.78, 0.24) * mm, "end": v(-69.07, -0.08) * mm});
            skLineSegment(sketch, "E666", {"start": v(-69.07, -0.08) * mm, "end": v(-69.38, -0.42) * mm});
            skLineSegment(sketch, "E667", {"start": v(-69.38, -0.42) * mm, "end": v(-69.71, -0.77) * mm});
            skLineSegment(sketch, "E668", {"start": v(-69.71, -0.77) * mm, "end": v(-70.43, -1.47) * mm});
            skLineSegment(sketch, "E669", {"start": v(-70.43, -1.47) * mm, "end": v(-71.2, -2.17) * mm});
            skLineSegment(sketch, "E670", {"start": v(-71.2, -2.17) * mm, "end": v(-72.02, -2.87) * mm});
            skLineSegment(sketch, "E671", {"start": v(-72.02, -2.87) * mm, "end": v(-72.9, -3.55) * mm});
            skLineSegment(sketch, "E672", {"start": v(-72.9, -3.55) * mm, "end": v(-73, -3.86) * mm});
            skLineSegment(sketch, "E673", {"start": v(-73, -3.86) * mm, "end": v(-73.07, -4.14) * mm});
            skLineSegment(sketch, "E674", {"start": v(-73.07, -4.14) * mm, "end": v(-73.14, -4.4) * mm});
            skLineSegment(sketch, "E675", {"start": v(-73.14, -4.4) * mm, "end": v(-73.17, -4.53) * mm});
            skLineSegment(sketch, "E676", {"start": v(-73.17, -4.53) * mm, "end": v(-73.2, -4.65) * mm});
            skLineSegment(sketch, "E677", {"start": v(-73.2, -4.65) * mm, "end": v(-73.22, -4.77) * mm});
            skLineSegment(sketch, "E678", {"start": v(-73.22, -4.77) * mm, "end": v(-73.24, -4.88) * mm});
            skLineSegment(sketch, "E679", {"start": v(-73.24, -4.88) * mm, "end": v(-73.26, -4.99) * mm});
            skLineSegment(sketch, "E680", {"start": v(-73.26, -4.99) * mm, "end": v(-73.27, -5.09) * mm});
            skLineSegment(sketch, "E681", {"start": v(-73.27, -5.09) * mm, "end": v(-73.29, -5.19) * mm});
            skLineSegment(sketch, "E682", {"start": v(-73.29, -5.19) * mm, "end": v(-73.3, -5.28) * mm});
            skLineSegment(sketch, "E683", {"start": v(-73.3, -5.28) * mm, "end": v(-73.3, -5.37) * mm});
            skLineSegment(sketch, "E684", {"start": v(-73.3, -5.37) * mm, "end": v(-73.3, -5.45) * mm});
            skLineSegment(sketch, "E685", {"start": v(-73.3, -5.45) * mm, "end": v(-73.3, -5.56) * mm});
            skLineSegment(sketch, "E686", {"start": v(-73.3, -5.56) * mm, "end": v(-73.29, -5.67) * mm});
            skLineSegment(sketch, "E687", {"start": v(-73.29, -5.67) * mm, "end": v(-73.28, -5.71) * mm});
            skLineSegment(sketch, "E688", {"start": v(-73.28, -5.71) * mm, "end": v(-73.28, -5.76) * mm});
            skLineSegment(sketch, "E689", {"start": v(-73.28, -5.76) * mm, "end": v(-73.27, -5.8) * mm});
            skLineSegment(sketch, "E690", {"start": v(-73.27, -5.8) * mm, "end": v(-73.26, -5.85) * mm});
            skLineSegment(sketch, "E691", {"start": v(-73.26, -5.85) * mm, "end": v(-73.24, -5.9) * mm});
            skLineSegment(sketch, "E692", {"start": v(-73.24, -5.9) * mm, "end": v(-73.23, -5.93) * mm});
            skLineSegment(sketch, "E693", {"start": v(-73.23, -5.93) * mm, "end": v(-73.22, -5.97) * mm});
            skLineSegment(sketch, "E694", {"start": v(-73.22, -5.97) * mm, "end": v(-73.2, -6) * mm});
            skLineSegment(sketch, "E695", {"start": v(-73.2, -6) * mm, "end": v(-73.18, -6.04) * mm});
            skLineSegment(sketch, "E696", {"start": v(-73.18, -6.04) * mm, "end": v(-73.17, -6.07) * mm});
            skLineSegment(sketch, "E697", {"start": v(-73.17, -6.07) * mm, "end": v(-73.15, -6.1) * mm});
            skLineSegment(sketch, "E698", {"start": v(-73.15, -6.1) * mm, "end": v(-73.13, -6.13) * mm});
            skLineSegment(sketch, "E699", {"start": v(-73.13, -6.13) * mm, "end": v(-73.1, -6.16) * mm});
            skLineSegment(sketch, "E700", {"start": v(-73.1, -6.16) * mm, "end": v(-73.08, -6.19) * mm});
            skLineSegment(sketch, "E701", {"start": v(-73.08, -6.19) * mm, "end": v(-73.05, -6.21) * mm});
            skLineSegment(sketch, "E702", {"start": v(-73.05, -6.21) * mm, "end": v(-73.03, -6.23) * mm});
            skLineSegment(sketch, "E703", {"start": v(-73.03, -6.23) * mm, "end": v(-73, -6.25) * mm});
            skLineSegment(sketch, "E704", {"start": v(-73, -6.25) * mm, "end": v(-72.97, -6.27) * mm});
            skLineSegment(sketch, "E705", {"start": v(-72.97, -6.27) * mm, "end": v(-72.94, -6.29) * mm});
            skLineSegment(sketch, "E706", {"start": v(-72.94, -6.29) * mm, "end": v(-72.9, -6.3) * mm});
            skLineSegment(sketch, "E707", {"start": v(-72.9, -6.3) * mm, "end": v(-72.87, -6.32) * mm});
            skLineSegment(sketch, "E708", {"start": v(-72.87, -6.32) * mm, "end": v(-72.84, -6.33) * mm});
            skLineSegment(sketch, "E709", {"start": v(-72.84, -6.33) * mm, "end": v(-72.8, -6.34) * mm});
            skLineSegment(sketch, "E710", {"start": v(-72.8, -6.34) * mm, "end": v(-72.77, -6.35) * mm});
            skLineSegment(sketch, "E711", {"start": v(-72.77, -6.35) * mm, "end": v(-72.73, -6.35) * mm});
            skLineSegment(sketch, "E712", {"start": v(-72.73, -6.35) * mm, "end": v(-72.69, -6.36) * mm});
            skLineSegment(sketch, "E713", {"start": v(-72.69, -6.36) * mm, "end": v(-72.65, -6.36) * mm});
            skLineSegment(sketch, "E714", {"start": v(-72.65, -6.36) * mm, "end": v(-72.6, -6.36) * mm});
            skLineSegment(sketch, "E715", {"start": v(-72.6, -6.36) * mm, "end": v(-72.59, -6.36) * mm});
            skLineSegment(sketch, "E716", {"start": v(-72.59, -6.36) * mm, "end": v(-72.57, -6.36) * mm});
            skLineSegment(sketch, "E717", {"start": v(-72.57, -6.36) * mm, "end": v(-72.55, -6.36) * mm});
            skLineSegment(sketch, "E718", {"start": v(-72.55, -6.36) * mm, "end": v(-72.54, -6.35) * mm});
            skLineSegment(sketch, "E719", {"start": v(-72.54, -6.35) * mm, "end": v(-72.52, -6.35) * mm});
            skLineSegment(sketch, "E720", {"start": v(-72.52, -6.35) * mm, "end": v(-72.5, -6.35) * mm});
            skLineSegment(sketch, "E721", {"start": v(-72.5, -6.35) * mm, "end": v(-72.48, -6.34) * mm});
            skLineSegment(sketch, "E722", {"start": v(-72.48, -6.34) * mm, "end": v(-72.46, -6.33) * mm});
            skLineSegment(sketch, "E723", {"start": v(-72.46, -6.33) * mm, "end": v(-72.43, -6.33) * mm});
            skLineSegment(sketch, "E724", {"start": v(-72.43, -6.33) * mm, "end": v(-72.41, -6.32) * mm});
            skLineSegment(sketch, "E725", {"start": v(-72.41, -6.32) * mm, "end": v(-72.37, -6.3) * mm});
            skLineSegment(sketch, "E726", {"start": v(-72.37, -6.3) * mm, "end": v(-72.32, -6.28) * mm});
            skLineSegment(sketch, "E727", {"start": v(-72.32, -6.28) * mm, "end": v(-72.27, -6.26) * mm});
            skLineSegment(sketch, "E728", {"start": v(-72.27, -6.26) * mm, "end": v(-72.21, -6.23) * mm});
            skLineSegment(sketch, "E729", {"start": v(-72.21, -6.23) * mm, "end": v(-72.16, -6.2) * mm});
            skLineSegment(sketch, "E730", {"start": v(-72.16, -6.2) * mm, "end": v(-72.1, -6.16) * mm});
            skLineSegment(sketch, "E731", {"start": v(-72.1, -6.16) * mm, "end": v(-72.03, -6.12) * mm});
            skLineSegment(sketch, "E732", {"start": v(-72.03, -6.12) * mm, "end": v(-71.97, -6.08) * mm});
            skLineSegment(sketch, "E733", {"start": v(-71.97, -6.08) * mm, "end": v(-71.9, -6.04) * mm});
            skLineSegment(sketch, "E734", {"start": v(-71.9, -6.04) * mm, "end": v(-71.83, -5.99) * mm});
            skLineSegment(sketch, "E735", {"start": v(-71.83, -5.99) * mm, "end": v(-71.76, -5.94) * mm});
            skLineSegment(sketch, "E736", {"start": v(-71.76, -5.94) * mm, "end": v(-71.72, -5.91) * mm});
            skLineSegment(sketch, "E737", {"start": v(-71.72, -5.91) * mm, "end": v(-71.64, -5.85) * mm});
            skLineSegment(sketch, "E738", {"start": v(-71.64, -5.85) * mm, "end": v(-71.56, -5.78) * mm});
            skLineSegment(sketch, "E739", {"start": v(-71.56, -5.78) * mm, "end": v(-71.46, -5.7) * mm});
            skLineSegment(sketch, "E740", {"start": v(-71.46, -5.7) * mm, "end": v(-71.36, -5.63) * mm});
            skLineSegment(sketch, "E741", {"start": v(-71.36, -5.63) * mm, "end": v(-71.26, -5.54) * mm});
            skLineSegment(sketch, "E742", {"start": v(-71.26, -5.54) * mm, "end": v(-71.15, -5.45) * mm});
            skLineSegment(sketch, "E743", {"start": v(-71.15, -5.45) * mm, "end": v(-71.03, -5.35) * mm});
            skLineSegment(sketch, "E744", {"start": v(-71.03, -5.35) * mm, "end": v(-70.9, -5.25) * mm});
            skLineSegment(sketch, "E745", {"start": v(-70.9, -5.25) * mm, "end": v(-70.78, -5.14) * mm});
            skLineSegment(sketch, "E746", {"start": v(-70.78, -5.14) * mm, "end": v(-70.64, -5.02) * mm});
            skLineSegment(sketch, "E747", {"start": v(-70.64, -5.02) * mm, "end": v(-70.5, -4.9) * mm});
            skLineSegment(sketch, "E748", {"start": v(-70.5, -4.9) * mm, "end": v(-70.2, -4.64) * mm});
            skLineSegment(sketch, "E749", {"start": v(-70.2, -4.64) * mm, "end": v(-69.86, -4.35) * mm});
            skLineSegment(sketch, "E750", {"start": v(-69.86, -4.35) * mm, "end": v(-69.78, -4.27) * mm});
            skLineSegment(sketch, "E751", {"start": v(-69.78, -4.27) * mm, "end": v(-69.09, -3.67) * mm});
            skLineSegment(sketch, "E752", {"start": v(-69.09, -3.67) * mm, "end": v(-68.44, -3.1) * mm});
            skLineSegment(sketch, "E753", {"start": v(-68.44, -3.1) * mm, "end": v(-67.82, -2.57) * mm});
            skLineSegment(sketch, "E754", {"start": v(-67.82, -2.57) * mm, "end": v(-67.25, -2.08) * mm});
            skLineSegment(sketch, "E755", {"start": v(-67.25, -2.08) * mm, "end": v(-67.04, -1.89) * mm});
            skLineSegment(sketch, "E756", {"start": v(-67.04, -1.89) * mm, "end": v(-66.82, -1.68) * mm});
            skLineSegment(sketch, "E757", {"start": v(-66.82, -1.68) * mm, "end": v(-66.6, -1.44) * mm});
            skLineSegment(sketch, "E758", {"start": v(-66.6, -1.44) * mm, "end": v(-66.36, -1.19) * mm});
            skLineSegment(sketch, "E759", {"start": v(-66.36, -1.19) * mm, "end": v(-66.12, -0.9) * mm});
            skLineSegment(sketch, "E760", {"start": v(-66.12, -0.9) * mm, "end": v(-65.87, -0.61) * mm});
            skLineSegment(sketch, "E761", {"start": v(-65.87, -0.61) * mm, "end": v(-65.61, -0.29) * mm});
            skLineSegment(sketch, "E762", {"start": v(-65.61, -0.29) * mm, "end": v(-65.35, 0.05) * mm});
            skLineSegment(sketch, "E763", {"start": v(-65.35, 0.05) * mm, "end": v(-65.08, 0.4) * mm});
            skLineSegment(sketch, "E764", {"start": v(-65.08, 0.4) * mm, "end": v(-64.82, 0.73) * mm});
            skLineSegment(sketch, "E765", {"start": v(-64.82, 0.73) * mm, "end": v(-64.58, 1.03) * mm});
            skLineSegment(sketch, "E766", {"start": v(-64.58, 1.03) * mm, "end": v(-64.35, 1.3) * mm});
            skLineSegment(sketch, "E767", {"start": v(-64.35, 1.3) * mm, "end": v(-64.14, 1.57) * mm});
            skLineSegment(sketch, "E768", {"start": v(-64.14, 1.57) * mm, "end": v(-63.94, 1.8) * mm});
            skLineSegment(sketch, "E769", {"start": v(-63.94, 1.8) * mm, "end": v(-63.84, 1.91) * mm});
            skLineSegment(sketch, "E770", {"start": v(-63.84, 1.91) * mm, "end": v(-63.75, 2.01) * mm});
            skLineSegment(sketch, "E771", {"start": v(-63.75, 2.01) * mm, "end": v(-63.66, 2.11) * mm});
            skLineSegment(sketch, "E772", {"start": v(-63.66, 2.11) * mm, "end": v(-63.57, 2.2) * mm});
            skLineSegment(sketch, "E773", {"start": v(-63.57, 2.2) * mm, "end": v(-63.38, 2.4) * mm});
            skLineSegment(sketch, "E774", {"start": v(-63.38, 2.4) * mm, "end": v(-63.2, 2.6) * mm});
            skLineSegment(sketch, "E775", {"start": v(-63.2, 2.6) * mm, "end": v(-63.02, 2.78) * mm});
            skLineSegment(sketch, "E776", {"start": v(-63.02, 2.78) * mm, "end": v(-62.86, 2.95) * mm});
            skLineSegment(sketch, "E777", {"start": v(-62.86, 2.95) * mm, "end": v(-62.7, 3.12) * mm});
            skLineSegment(sketch, "E778", {"start": v(-62.7, 3.12) * mm, "end": v(-62.54, 3.28) * mm});
            skLineSegment(sketch, "E779", {"start": v(-62.54, 3.28) * mm, "end": v(-62.4, 3.42) * mm});
            skLineSegment(sketch, "E780", {"start": v(-62.4, 3.42) * mm, "end": v(-62.26, 3.56) * mm});
            skLineSegment(sketch, "E781", {"start": v(-62.26, 3.56) * mm, "end": v(-62.13, 3.69) * mm});
            skLineSegment(sketch, "E782", {"start": v(-62.13, 3.69) * mm, "end": v(-62, 3.8) * mm});
            skLineSegment(sketch, "E783", {"start": v(-62, 3.8) * mm, "end": v(-61.9, 3.92) * mm});
            skLineSegment(sketch, "E784", {"start": v(-61.9, 3.92) * mm, "end": v(-61.8, 4.02) * mm});
            skLineSegment(sketch, "E785", {"start": v(-61.8, 4.02) * mm, "end": v(-61.74, 4.07) * mm});
            skLineSegment(sketch, "E786", {"start": v(-61.74, 4.07) * mm, "end": v(-61.7, 4.11) * mm});
            skLineSegment(sketch, "E787", {"start": v(-61.7, 4.11) * mm, "end": v(-61.65, 4.16) * mm});
            skLineSegment(sketch, "E788", {"start": v(-61.65, 4.16) * mm, "end": v(-61.6, 4.2) * mm});
            skLineSegment(sketch, "E789", {"start": v(-61.6, 4.2) * mm, "end": v(-61.56, 4.23) * mm});
            skLineSegment(sketch, "E790", {"start": v(-61.56, 4.23) * mm, "end": v(-61.52, 4.27) * mm});
            skLineSegment(sketch, "E791", {"start": v(-61.52, 4.27) * mm, "end": v(-61.48, 4.3) * mm});
            skLineSegment(sketch, "E792", {"start": v(-61.48, 4.3) * mm, "end": v(-61.44, 4.34) * mm});
            skLineSegment(sketch, "E793", {"start": v(-61.44, 4.34) * mm, "end": v(-61.3, 4.45) * mm});
            skLineSegment(sketch, "E794", {"start": v(-61.3, 4.45) * mm, "end": v(-61.23, 4.5) * mm});
            skLineSegment(sketch, "E795", {"start": v(-61.23, 4.5) * mm, "end": v(-61.16, 4.56) * mm});
            skLineSegment(sketch, "E796", {"start": v(-61.16, 4.56) * mm, "end": v(-61.1, 4.6) * mm});
            skLineSegment(sketch, "E797", {"start": v(-61.1, 4.6) * mm, "end": v(-61.02, 4.64) * mm});
            skLineSegment(sketch, "E798", {"start": v(-61.02, 4.64) * mm, "end": v(-60.95, 4.68) * mm});
            skLineSegment(sketch, "E799", {"start": v(-60.95, 4.68) * mm, "end": v(-60.88, 4.72) * mm});
            skLineSegment(sketch, "E800", {"start": v(-60.88, 4.72) * mm, "end": v(-60.82, 4.74) * mm});
            skLineSegment(sketch, "E801", {"start": v(-60.82, 4.74) * mm, "end": v(-60.75, 4.77) * mm});
            skLineSegment(sketch, "E802", {"start": v(-60.75, 4.77) * mm, "end": v(-60.68, 4.8) * mm});
            skLineSegment(sketch, "E803", {"start": v(-60.68, 4.8) * mm, "end": v(-60.61, 4.81) * mm});
            skLineSegment(sketch, "E804", {"start": v(-60.61, 4.81) * mm, "end": v(-60.55, 4.82) * mm});
            skLineSegment(sketch, "E805", {"start": v(-60.55, 4.82) * mm, "end": v(-60.48, 4.83) * mm});
            skLineSegment(sketch, "E806", {"start": v(-60.48, 4.83) * mm, "end": v(-60.41, 4.84) * mm});
            skLineSegment(sketch, "E807", {"start": v(-60.41, 4.84) * mm, "end": v(-60.35, 4.84) * mm});
            skLineSegment(sketch, "E808", {"start": v(-60.35, 4.84) * mm, "end": v(-60.28, 4.84) * mm});
            skLineSegment(sketch, "E809", {"start": v(-60.28, 4.84) * mm, "end": v(-60.22, 4.84) * mm});
            skLineSegment(sketch, "E810", {"start": v(-60.22, 4.84) * mm, "end": v(-60.17, 4.83) * mm});
            skLineSegment(sketch, "E811", {"start": v(-60.17, 4.83) * mm, "end": v(-60.11, 4.82) * mm});
            skLineSegment(sketch, "E812", {"start": v(-60.11, 4.82) * mm, "end": v(-60.06, 4.81) * mm});
            skLineSegment(sketch, "E813", {"start": v(-60.06, 4.81) * mm, "end": v(-60.01, 4.8) * mm});
            skLineSegment(sketch, "E814", {"start": v(-60.01, 4.8) * mm, "end": v(-59.97, 4.78) * mm});
            skLineSegment(sketch, "E815", {"start": v(-59.97, 4.78) * mm, "end": v(-59.92, 4.76) * mm});
            skLineSegment(sketch, "E816", {"start": v(-59.92, 4.76) * mm, "end": v(-59.88, 4.74) * mm});
            skLineSegment(sketch, "E817", {"start": v(-59.88, 4.74) * mm, "end": v(-59.85, 4.72) * mm});
            skLineSegment(sketch, "E818", {"start": v(-59.85, 4.72) * mm, "end": v(-59.8, 4.7) * mm});
            skLineSegment(sketch, "E819", {"start": v(-59.8, 4.7) * mm, "end": v(-59.78, 4.66) * mm});
            skLineSegment(sketch, "E820", {"start": v(-59.78, 4.66) * mm, "end": v(-59.75, 4.63) * mm});
            skLineSegment(sketch, "E821", {"start": v(-59.75, 4.63) * mm, "end": v(-59.72, 4.6) * mm});
            skLineSegment(sketch, "E822", {"start": v(-59.72, 4.6) * mm, "end": v(-59.7, 4.56) * mm});
            skLineSegment(sketch, "E823", {"start": v(-59.7, 4.56) * mm, "end": v(-59.67, 4.53) * mm});
            skLineSegment(sketch, "E824", {"start": v(-59.67, 4.53) * mm, "end": v(-59.66, 4.5) * mm});
            skLineSegment(sketch, "E825", {"start": v(-59.66, 4.5) * mm, "end": v(-59.65, 4.48) * mm});
            skLineSegment(sketch, "E826", {"start": v(-59.65, 4.48) * mm, "end": v(-59.64, 4.46) * mm});
            skLineSegment(sketch, "E827", {"start": v(-59.64, 4.46) * mm, "end": v(-59.63, 4.44) * mm});
            skLineSegment(sketch, "E828", {"start": v(-59.63, 4.44) * mm, "end": v(-59.62, 4.41) * mm});
            skLineSegment(sketch, "E829", {"start": v(-59.62, 4.41) * mm, "end": v(-59.6, 4.38) * mm});
            skLineSegment(sketch, "E830", {"start": v(-59.6, 4.38) * mm, "end": v(-59.6, 4.36) * mm});
            skLineSegment(sketch, "E831", {"start": v(-59.6, 4.36) * mm, "end": v(-59.58, 4.3) * mm});
            skLineSegment(sketch, "E832", {"start": v(-59.58, 4.3) * mm, "end": v(-59.56, 4.23) * mm});
            skLineSegment(sketch, "E833", {"start": v(-59.56, 4.23) * mm, "end": v(-59.55, 4.16) * mm});
            skLineSegment(sketch, "E834", {"start": v(-59.55, 4.16) * mm, "end": v(-59.53, 4.08) * mm});
            skLineSegment(sketch, "E835", {"start": v(-59.53, 4.08) * mm, "end": v(-59.52, 4) * mm});
            skLineSegment(sketch, "E836", {"start": v(-59.52, 4) * mm, "end": v(-59.51, 3.92) * mm});
            skLineSegment(sketch, "E837", {"start": v(-59.51, 3.92) * mm, "end": v(-59.5, 3.83) * mm});
            skLineSegment(sketch, "E838", {"start": v(-59.5, 3.83) * mm, "end": v(-59.5, 3.73) * mm});
            skLineSegment(sketch, "E839", {"start": v(-59.5, 3.73) * mm, "end": v(-59.5, 3.63) * mm});
            skLineSegment(sketch, "E840", {"start": v(-59.5, 3.63) * mm, "end": v(-59.49, 3.53) * mm});
            skLineSegment(sketch, "E841", {"start": v(-59.49, 3.53) * mm, "end": v(-59.48, 3.41) * mm});
            skLineSegment(sketch, "E842", {"start": v(-59.48, 3.41) * mm, "end": v(-59.48, 3.24) * mm});
            skLineSegment(sketch, "E843", {"start": v(-59.48, 3.24) * mm, "end": v(-59.48, 3.13) * mm});
            skLineSegment(sketch, "E844", {"start": v(-59.48, 3.13) * mm, "end": v(-59.49, 3.03) * mm});
            skLineSegment(sketch, "E845", {"start": v(-59.49, 3.03) * mm, "end": v(-59.5, 2.93) * mm});
            skLineSegment(sketch, "E846", {"start": v(-59.5, 2.93) * mm, "end": v(-59.5, 2.84) * mm});
            skLineSegment(sketch, "E847", {"start": v(-59.5, 2.84) * mm, "end": v(-59.51, 2.75) * mm});
            skLineSegment(sketch, "E848", {"start": v(-59.51, 2.75) * mm, "end": v(-59.53, 2.67) * mm});
            skLineSegment(sketch, "E849", {"start": v(-59.53, 2.67) * mm, "end": v(-59.55, 2.6) * mm});
            skLineSegment(sketch, "E850", {"start": v(-59.55, 2.6) * mm, "end": v(-59.57, 2.52) * mm});
            skLineSegment(sketch, "E851", {"start": v(-59.57, 2.52) * mm, "end": v(-59.58, 2.49) * mm});
            skLineSegment(sketch, "E852", {"start": v(-59.58, 2.49) * mm, "end": v(-59.59, 2.45) * mm});
            skLineSegment(sketch, "E853", {"start": v(-59.59, 2.45) * mm, "end": v(-59.6, 2.41) * mm});
            skLineSegment(sketch, "E854", {"start": v(-59.6, 2.41) * mm, "end": v(-59.62, 2.37) * mm});
            skLineSegment(sketch, "E855", {"start": v(-59.62, 2.37) * mm, "end": v(-59.64, 2.33) * mm});
            skLineSegment(sketch, "E856", {"start": v(-59.64, 2.33) * mm, "end": v(-59.68, 2.25) * mm});
            skLineSegment(sketch, "E857", {"start": v(-59.68, 2.25) * mm, "end": v(-59.72, 2.16) * mm});
            skLineSegment(sketch, "E858", {"start": v(-59.72, 2.16) * mm, "end": v(-59.77, 2.06) * mm});
            skLineSegment(sketch, "E859", {"start": v(-59.77, 2.06) * mm, "end": v(-59.83, 1.96) * mm});
            skLineSegment(sketch, "E860", {"start": v(-59.83, 1.96) * mm, "end": v(-59.9, 1.86) * mm});
            skLineSegment(sketch, "E861", {"start": v(-59.9, 1.86) * mm, "end": v(-59.92, 1.8) * mm});
            skLineSegment(sketch, "E862", {"start": v(-59.92, 1.8) * mm, "end": v(-59.94, 1.78) * mm});
            skLineSegment(sketch, "E863", {"start": v(-59.94, 1.78) * mm, "end": v(-59.96, 1.75) * mm});
            skLineSegment(sketch, "E864", {"start": v(-59.96, 1.75) * mm, "end": v(-59.98, 1.72) * mm});
            skLineSegment(sketch, "E865", {"start": v(-59.98, 1.72) * mm, "end": v(-60, 1.69) * mm});
            skLineSegment(sketch, "E866", {"start": v(-60, 1.69) * mm, "end": v(-60.02, 1.65) * mm});
            skLineSegment(sketch, "E867", {"start": v(-60.02, 1.65) * mm, "end": v(-60.06, 1.58) * mm});
            skLineSegment(sketch, "E868", {"start": v(-60.06, 1.58) * mm, "end": v(-60.11, 1.5) * mm});
            skLineSegment(sketch, "E869", {"start": v(-60.11, 1.5) * mm, "end": v(-60.16, 1.43) * mm});
            skLineSegment(sketch, "E870", {"start": v(-60.16, 1.43) * mm, "end": v(-60.22, 1.34) * mm});
            skLineSegment(sketch, "E871", {"start": v(-60.22, 1.34) * mm, "end": v(-60.28, 1.25) * mm});
            skLineSegment(sketch, "E872", {"start": v(-60.28, 1.25) * mm, "end": v(-60.35, 1.15) * mm});
            skLineSegment(sketch, "E873", {"start": v(-60.35, 1.15) * mm, "end": v(-60.42, 1.04) * mm});
            skLineSegment(sketch, "E874", {"start": v(-60.42, 1.04) * mm, "end": v(-60.5, 0.93) * mm});
            skLineSegment(sketch, "E875", {"start": v(-60.5, 0.93) * mm, "end": v(-60.57, 0.82) * mm});
            skLineSegment(sketch, "E876", {"start": v(-60.57, 0.82) * mm, "end": v(-60.65, 0.7) * mm});
            skLineSegment(sketch, "E877", {"start": v(-60.65, 0.7) * mm, "end": v(-60.74, 0.57) * mm});
            skLineSegment(sketch, "E878", {"start": v(-60.74, 0.57) * mm, "end": v(-60.93, 0.3) * mm});
            skLineSegment(sketch, "E879", {"start": v(-60.93, 0.3) * mm, "end": v(-60.98, 0.22) * mm});
            skLineSegment(sketch, "E880", {"start": v(-60.98, 0.22) * mm, "end": v(-61.18, -0.08) * mm});
            skLineSegment(sketch, "E881", {"start": v(-61.18, -0.08) * mm, "end": v(-61.62, -0.7) * mm});
            skLineSegment(sketch, "E882", {"start": v(-61.62, -0.7) * mm, "end": v(-62.1, -1.4) * mm});
            skLineSegment(sketch, "E883", {"start": v(-62.1, -1.4) * mm, "end": v(-62.6, -2.13) * mm});
            skLineSegment(sketch, "E884", {"start": v(-62.6, -2.13) * mm, "end": v(-62.88, -2.52) * mm});
            skLineSegment(sketch, "E885", {"start": v(-62.88, -2.52) * mm, "end": v(-63.16, -2.95) * mm});
            skLineSegment(sketch, "E886", {"start": v(-63.16, -2.95) * mm, "end": v(-63.43, -3.4) * mm});
            skLineSegment(sketch, "E887", {"start": v(-63.43, -3.4) * mm, "end": v(-63.68, -3.88) * mm});
            skLineSegment(sketch, "E888", {"start": v(-63.68, -3.88) * mm, "end": v(-63.91, -4.38) * mm});
            skLineSegment(sketch, "E889", {"start": v(-63.91, -4.38) * mm, "end": v(-64.02, -4.62) * mm});
            skLineSegment(sketch, "E890", {"start": v(-64.02, -4.62) * mm, "end": v(-64.1, -4.84) * mm});
            skLineSegment(sketch, "E891", {"start": v(-64.1, -4.84) * mm, "end": v(-64.15, -4.95) * mm});
            skLineSegment(sketch, "E892", {"start": v(-64.15, -4.95) * mm, "end": v(-64.18, -5.05) * mm});
            skLineSegment(sketch, "E893", {"start": v(-64.18, -5.05) * mm, "end": v(-64.21, -5.15) * mm});
            skLineSegment(sketch, "E894", {"start": v(-64.21, -5.15) * mm, "end": v(-64.24, -5.25) * mm});
            skLineSegment(sketch, "E895", {"start": v(-64.24, -5.25) * mm, "end": v(-64.27, -5.34) * mm});
            skLineSegment(sketch, "E896", {"start": v(-64.27, -5.34) * mm, "end": v(-64.3, -5.43) * mm});
            skLineSegment(sketch, "E897", {"start": v(-64.3, -5.43) * mm, "end": v(-64.31, -5.51) * mm});
            skLineSegment(sketch, "E898", {"start": v(-64.31, -5.51) * mm, "end": v(-64.33, -5.6) * mm});
            skLineSegment(sketch, "E899", {"start": v(-64.33, -5.6) * mm, "end": v(-64.34, -5.67) * mm});
            skLineSegment(sketch, "E900", {"start": v(-64.34, -5.67) * mm, "end": v(-64.35, -5.74) * mm});
            skLineSegment(sketch, "E901", {"start": v(-64.35, -5.74) * mm, "end": v(-64.35, -5.81) * mm});
            skLineSegment(sketch, "E902", {"start": v(-64.35, -5.81) * mm, "end": v(-64.35, -5.88) * mm});
            skLineSegment(sketch, "E903", {"start": v(-64.35, -5.88) * mm, "end": v(-64.35, -6) * mm});
            skLineSegment(sketch, "E904", {"start": v(-64.35, -6) * mm, "end": v(-64.35, -6.07) * mm});
            skLineSegment(sketch, "E905", {"start": v(-64.35, -6.07) * mm, "end": v(-64.34, -6.13) * mm});
            skLineSegment(sketch, "E906", {"start": v(-64.34, -6.13) * mm, "end": v(-64.33, -6.2) * mm});
            skLineSegment(sketch, "E907", {"start": v(-64.33, -6.2) * mm, "end": v(-64.32, -6.25) * mm});
            skLineSegment(sketch, "E908", {"start": v(-64.32, -6.25) * mm, "end": v(-64.31, -6.3) * mm});
            skLineSegment(sketch, "E909", {"start": v(-64.31, -6.3) * mm, "end": v(-64.3, -6.36) * mm});
            skLineSegment(sketch, "E910", {"start": v(-64.3, -6.36) * mm, "end": v(-64.29, -6.4) * mm});
            skLineSegment(sketch, "E911", {"start": v(-64.29, -6.4) * mm, "end": v(-64.27, -6.45) * mm});
            skLineSegment(sketch, "E912", {"start": v(-64.27, -6.45) * mm, "end": v(-64.25, -6.5) * mm});
            skLineSegment(sketch, "E913", {"start": v(-64.25, -6.5) * mm, "end": v(-64.23, -6.54) * mm});
            skLineSegment(sketch, "E914", {"start": v(-64.23, -6.54) * mm, "end": v(-64.21, -6.59) * mm});
            skLineSegment(sketch, "E915", {"start": v(-64.21, -6.59) * mm, "end": v(-64.19, -6.63) * mm});
            skLineSegment(sketch, "E916", {"start": v(-64.19, -6.63) * mm, "end": v(-64.16, -6.66) * mm});
            skLineSegment(sketch, "E917", {"start": v(-64.16, -6.66) * mm, "end": v(-64.14, -6.7) * mm});
            skLineSegment(sketch, "E918", {"start": v(-64.14, -6.7) * mm, "end": v(-64.11, -6.73) * mm});
            skLineSegment(sketch, "E919", {"start": v(-64.11, -6.73) * mm, "end": v(-64.08, -6.76) * mm});
            skLineSegment(sketch, "E920", {"start": v(-64.08, -6.76) * mm, "end": v(-64.05, -6.8) * mm});
            skLineSegment(sketch, "E921", {"start": v(-64.05, -6.8) * mm, "end": v(-64.02, -6.82) * mm});
            skLineSegment(sketch, "E922", {"start": v(-64.02, -6.82) * mm, "end": v(-63.98, -6.84) * mm});
            skLineSegment(sketch, "E923", {"start": v(-63.98, -6.84) * mm, "end": v(-63.95, -6.87) * mm});
            skLineSegment(sketch, "E924", {"start": v(-63.95, -6.87) * mm, "end": v(-63.9, -6.89) * mm});
            skLineSegment(sketch, "E925", {"start": v(-63.9, -6.89) * mm, "end": v(-63.87, -6.9) * mm});
            skLineSegment(sketch, "E926", {"start": v(-63.87, -6.9) * mm, "end": v(-63.83, -6.92) * mm});
            skLineSegment(sketch, "E927", {"start": v(-63.83, -6.92) * mm, "end": v(-63.78, -6.93) * mm});
            skLineSegment(sketch, "E928", {"start": v(-63.78, -6.93) * mm, "end": v(-63.74, -6.95) * mm});
            skLineSegment(sketch, "E929", {"start": v(-63.74, -6.95) * mm, "end": v(-63.7, -6.96) * mm});
            skLineSegment(sketch, "E930", {"start": v(-63.7, -6.96) * mm, "end": v(-63.64, -6.96) * mm});
            skLineSegment(sketch, "E931", {"start": v(-63.64, -6.96) * mm, "end": v(-63.6, -6.97) * mm});
            skLineSegment(sketch, "E932", {"start": v(-63.6, -6.97) * mm, "end": v(-63.54, -6.97) * mm});
            skLineSegment(sketch, "E933", {"start": v(-63.54, -6.97) * mm, "end": v(-63.49, -6.97) * mm});
            skLineSegment(sketch, "E934", {"start": v(-63.49, -6.97) * mm, "end": v(-63.4, -6.97) * mm});
            skLineSegment(sketch, "E935", {"start": v(-63.4, -6.97) * mm, "end": v(-63.3, -6.96) * mm});
            skLineSegment(sketch, "E936", {"start": v(-63.3, -6.96) * mm, "end": v(-63.21, -6.95) * mm});
            skLineSegment(sketch, "E937", {"start": v(-63.21, -6.95) * mm, "end": v(-63.12, -6.94) * mm});
            skLineSegment(sketch, "E938", {"start": v(-63.12, -6.94) * mm, "end": v(-63.02, -6.91) * mm});
            skLineSegment(sketch, "E939", {"start": v(-63.02, -6.91) * mm, "end": v(-62.92, -6.89) * mm});
            skLineSegment(sketch, "E940", {"start": v(-62.92, -6.89) * mm, "end": v(-62.82, -6.86) * mm});
            skLineSegment(sketch, "E941", {"start": v(-62.82, -6.86) * mm, "end": v(-62.71, -6.82) * mm});
            skLineSegment(sketch, "E942", {"start": v(-62.71, -6.82) * mm, "end": v(-62.5, -6.74) * mm});
            skLineSegment(sketch, "E943", {"start": v(-62.5, -6.74) * mm, "end": v(-62.28, -6.64) * mm});
            skLineSegment(sketch, "E944", {"start": v(-62.28, -6.64) * mm, "end": v(-62.06, -6.52) * mm});
            skLineSegment(sketch, "E945", {"start": v(-62.06, -6.52) * mm, "end": v(-61.82, -6.38) * mm});
            skLineSegment(sketch, "E946", {"start": v(-61.82, -6.38) * mm, "end": v(-61.7, -6.3) * mm});
            skLineSegment(sketch, "E947", {"start": v(-61.7, -6.3) * mm, "end": v(-61.57, -6.22) * mm});
            skLineSegment(sketch, "E948", {"start": v(-61.57, -6.22) * mm, "end": v(-61.43, -6.13) * mm});
            skLineSegment(sketch, "E949", {"start": v(-61.43, -6.13) * mm, "end": v(-61.29, -6.03) * mm});
            skLineSegment(sketch, "E950", {"start": v(-61.29, -6.03) * mm, "end": v(-61.13, -5.92) * mm});
            skLineSegment(sketch, "E951", {"start": v(-61.13, -5.92) * mm, "end": v(-60.97, -5.8) * mm});
            skLineSegment(sketch, "E952", {"start": v(-60.97, -5.8) * mm, "end": v(-60.8, -5.68) * mm});
            skLineSegment(sketch, "E953", {"start": v(-60.8, -5.68) * mm, "end": v(-60.62, -5.55) * mm});
            skLineSegment(sketch, "E954", {"start": v(-60.62, -5.55) * mm, "end": v(-60.43, -5.42) * mm});
            skLineSegment(sketch, "E955", {"start": v(-60.43, -5.42) * mm, "end": v(-60.24, -5.27) * mm});
            skLineSegment(sketch, "E956", {"start": v(-60.24, -5.27) * mm, "end": v(-59.83, -4.96) * mm});
            skLineSegment(sketch, "E957", {"start": v(-59.83, -4.96) * mm, "end": v(-59.39, -4.62) * mm});
            skLineSegment(sketch, "E958", {"start": v(-59.39, -4.62) * mm, "end": v(-58.91, -4.25) * mm});
            skLineSegment(sketch, "E959", {"start": v(-58.91, -4.25) * mm, "end": v(-58.91, -5.66) * mm});
            skLineSegment(sketch, "E960", {"start": v(-58.91, -5.66) * mm, "end": v(-59.5, -6.21) * mm});
            skLineSegment(sketch, "E961", {"start": v(-59.5, -6.21) * mm, "end": v(-60.07, -6.73) * mm});
            skLineSegment(sketch, "E962", {"start": v(-60.07, -6.73) * mm, "end": v(-60.58, -7.2) * mm});
            skLineSegment(sketch, "E963", {"start": v(-60.58, -7.2) * mm, "end": v(-61.06, -7.63) * mm});
            skLineSegment(sketch, "E964", {"start": v(-61.06, -7.63) * mm, "end": v(-61.28, -7.83) * mm});
            skLineSegment(sketch, "E965", {"start": v(-61.28, -7.83) * mm, "end": v(-61.5, -8.03) * mm});
            skLineSegment(sketch, "E966", {"start": v(-61.5, -8.03) * mm, "end": v(-61.7, -8.2) * mm});
            skLineSegment(sketch, "E967", {"start": v(-61.7, -8.2) * mm, "end": v(-61.9, -8.38) * mm});
            skLineSegment(sketch, "E968", {"start": v(-61.9, -8.38) * mm, "end": v(-62.07, -8.55) * mm});
            skLineSegment(sketch, "E969", {"start": v(-62.07, -8.55) * mm, "end": v(-62.25, -8.7) * mm});
            skLineSegment(sketch, "E970", {"start": v(-62.25, -8.7) * mm, "end": v(-62.4, -8.84) * mm});
            skLineSegment(sketch, "E971", {"start": v(-62.4, -8.84) * mm, "end": v(-62.56, -8.98) * mm});
            skLineSegment(sketch, "E972", {"start": v(-62.56, -8.98) * mm, "end": v(-62.85, -9.23) * mm});
            skLineSegment(sketch, "E973", {"start": v(-62.85, -9.23) * mm, "end": v(-63.13, -9.46) * mm});
            skLineSegment(sketch, "E974", {"start": v(-63.13, -9.46) * mm, "end": v(-63.4, -9.68) * mm});
            skLineSegment(sketch, "E975", {"start": v(-63.4, -9.68) * mm, "end": v(-63.66, -9.88) * mm});
            skLineSegment(sketch, "E976", {"start": v(-63.66, -9.88) * mm, "end": v(-63.91, -10.07) * mm});
            skLineSegment(sketch, "E977", {"start": v(-63.91, -10.07) * mm, "end": v(-64.16, -10.24) * mm});
            skLineSegment(sketch, "E978", {"start": v(-64.16, -10.24) * mm, "end": v(-64.39, -10.4) * mm});
            skLineSegment(sketch, "E979", {"start": v(-64.39, -10.4) * mm, "end": v(-64.6, -10.54) * mm});
            skLineSegment(sketch, "E980", {"start": v(-64.6, -10.54) * mm, "end": v(-64.82, -10.66) * mm});
            skLineSegment(sketch, "E981", {"start": v(-64.82, -10.66) * mm, "end": v(-65.04, -10.77) * mm});
            skLineSegment(sketch, "E982", {"start": v(-65.04, -10.77) * mm, "end": v(-65.24, -10.86) * mm});
            skLineSegment(sketch, "E983", {"start": v(-65.24, -10.86) * mm, "end": v(-65.45, -10.93) * mm});
            skLineSegment(sketch, "E984", {"start": v(-65.45, -10.93) * mm, "end": v(-65.66, -11) * mm});
            skLineSegment(sketch, "E985", {"start": v(-65.66, -11) * mm, "end": v(-65.86, -11.03) * mm});
            skLineSegment(sketch, "E986", {"start": v(-65.86, -11.03) * mm, "end": v(-66.06, -11.06) * mm});
            skLineSegment(sketch, "E987", {"start": v(-66.06, -11.06) * mm, "end": v(-66.25, -11.07) * mm});
            skLineSegment(sketch, "E988", {"start": v(-66.25, -11.07) * mm, "end": v(-66.36, -11.06) * mm});
            skLineSegment(sketch, "E989", {"start": v(-66.36, -11.06) * mm, "end": v(-66.47, -11.06) * mm});
            skLineSegment(sketch, "E990", {"start": v(-66.47, -11.06) * mm, "end": v(-66.57, -11.05) * mm});
            skLineSegment(sketch, "E991", {"start": v(-66.57, -11.05) * mm, "end": v(-66.67, -11.03) * mm});
            skLineSegment(sketch, "E992", {"start": v(-66.67, -11.03) * mm, "end": v(-66.76, -11.01) * mm});
            skLineSegment(sketch, "E993", {"start": v(-66.76, -11.01) * mm, "end": v(-66.86, -11) * mm});
            skLineSegment(sketch, "E994", {"start": v(-66.86, -11) * mm, "end": v(-66.94, -10.96) * mm});
            skLineSegment(sketch, "E995", {"start": v(-66.94, -10.96) * mm, "end": v(-67.03, -10.93) * mm});
            skLineSegment(sketch, "E996", {"start": v(-67.03, -10.93) * mm, "end": v(-67.11, -10.9) * mm});
            skLineSegment(sketch, "E997", {"start": v(-67.11, -10.9) * mm, "end": v(-67.19, -10.86) * mm});
            skLineSegment(sketch, "E998", {"start": v(-67.19, -10.86) * mm, "end": v(-67.26, -10.82) * mm});
            skLineSegment(sketch, "E999", {"start": v(-67.26, -10.82) * mm, "end": v(-67.33, -10.77) * mm});
            skLineSegment(sketch, "E1000", {"start": v(-67.33, -10.77) * mm, "end": v(-67.4, -10.72) * mm});
            skLineSegment(sketch, "E1001", {"start": v(-67.4, -10.72) * mm, "end": v(-67.46, -10.66) * mm});
            skLineSegment(sketch, "E1002", {"start": v(-67.46, -10.66) * mm, "end": v(-67.53, -10.6) * mm});
            skLineSegment(sketch, "E1003", {"start": v(-67.53, -10.6) * mm, "end": v(-67.58, -10.54) * mm});
            skLineSegment(sketch, "E1004", {"start": v(-67.58, -10.54) * mm, "end": v(-67.64, -10.47) * mm});
            skLineSegment(sketch, "E1005", {"start": v(-67.64, -10.47) * mm, "end": v(-67.69, -10.4) * mm});
            skLineSegment(sketch, "E1006", {"start": v(-67.69, -10.4) * mm, "end": v(-67.73, -10.32) * mm});
            skLineSegment(sketch, "E1007", {"start": v(-67.73, -10.32) * mm, "end": v(-67.78, -10.24) * mm});
            skLineSegment(sketch, "E1008", {"start": v(-67.78, -10.24) * mm, "end": v(-67.82, -10.16) * mm});
            skLineSegment(sketch, "E1009", {"start": v(-67.82, -10.16) * mm, "end": v(-67.85, -10.07) * mm});
            skLineSegment(sketch, "E1010", {"start": v(-67.85, -10.07) * mm, "end": v(-67.89, -9.98) * mm});
            skLineSegment(sketch, "E1011", {"start": v(-67.89, -9.98) * mm, "end": v(-67.91, -9.88) * mm});
            skLineSegment(sketch, "E1012", {"start": v(-67.91, -9.88) * mm, "end": v(-67.94, -9.78) * mm});
            skLineSegment(sketch, "E1013", {"start": v(-67.94, -9.78) * mm, "end": v(-67.96, -9.67) * mm});
            skLineSegment(sketch, "E1014", {"start": v(-67.96, -9.67) * mm, "end": v(-67.98, -9.56) * mm});
            skLineSegment(sketch, "E1015", {"start": v(-67.98, -9.56) * mm, "end": v(-68, -9.45) * mm});
            skLineSegment(sketch, "E1016", {"start": v(-68, -9.45) * mm, "end": v(-68.01, -9.33) * mm});
            skLineSegment(sketch, "E1017", {"start": v(-68.01, -9.33) * mm, "end": v(-68.02, -9.09) * mm});
            skLineSegment(sketch, "E1018", {"start": v(-68.02, -9.09) * mm, "end": v(-68.03, -8.96) * mm});
            skLineSegment(sketch, "E1019", {"start": v(-68.03, -8.96) * mm, "end": v(-68.02, -8.85) * mm});
            skLineSegment(sketch, "E1020", {"start": v(-68.02, -8.85) * mm, "end": v(-68.02, -8.75) * mm});
            skLineSegment(sketch, "E1021", {"start": v(-68.02, -8.75) * mm, "end": v(-68, -8.64) * mm});
            skLineSegment(sketch, "E1022", {"start": v(-68, -8.64) * mm, "end": v(-68, -8.52) * mm});
            skLineSegment(sketch, "E1023", {"start": v(-68, -8.52) * mm, "end": v(-67.97, -8.4) * mm});
            skLineSegment(sketch, "E1024", {"start": v(-67.97, -8.4) * mm, "end": v(-67.95, -8.28) * mm});
            skLineSegment(sketch, "E1025", {"start": v(-67.95, -8.28) * mm, "end": v(-67.92, -8.15) * mm});
            skLineSegment(sketch, "E1026", {"start": v(-67.92, -8.15) * mm, "end": v(-67.86, -7.88) * mm});
            skLineSegment(sketch, "E1027", {"start": v(-67.86, -7.88) * mm, "end": v(-67.78, -7.6) * mm});
            skLineSegment(sketch, "E1028", {"start": v(-67.78, -7.6) * mm, "end": v(-67.68, -7.3) * mm});
            skLineSegment(sketch, "E1029", {"start": v(-67.68, -7.3) * mm, "end": v(-67.56, -6.97) * mm});
            skLineSegment(sketch, "E1030", {"start": v(-67.56, -6.97) * mm, "end": v(-67.5, -6.8) * mm});
            skLineSegment(sketch, "E1031", {"start": v(-67.5, -6.8) * mm, "end": v(-67.43, -6.63) * mm});
            skLineSegment(sketch, "E1032", {"start": v(-67.43, -6.63) * mm, "end": v(-67.36, -6.44) * mm});
            skLineSegment(sketch, "E1033", {"start": v(-67.36, -6.44) * mm, "end": v(-67.28, -6.25) * mm});
            skLineSegment(sketch, "E1034", {"start": v(-67.28, -6.25) * mm, "end": v(-67.2, -6.04) * mm});
            skLineSegment(sketch, "E1035", {"start": v(-67.2, -6.04) * mm, "end": v(-67.1, -5.83) * mm});
            skLineSegment(sketch, "E1036", {"start": v(-67.1, -5.83) * mm, "end": v(-66.91, -5.37) * mm});
            skLineSegment(sketch, "E1037", {"start": v(-66.91, -5.37) * mm, "end": v(-66.7, -4.88) * mm});
            skLineSegment(sketch, "E1038", {"start": v(-66.7, -4.88) * mm, "end": v(-66.46, -4.35) * mm});
            skLineSegment(sketch, "E1039", {"start": v(-66.46, -4.35) * mm, "end": v(-66.2, -3.78) * mm});
            skLineSegment(sketch, "E1040", {"start": v(-66.2, -3.78) * mm, "end": v(-65.93, -3.18) * mm});
            skLineSegment(sketch, "E1041", {"start": v(-65.93, -3.18) * mm, "end": v(-65.79, -2.86) * mm});
            skLineSegment(sketch, "E1042", {"start": v(-48.06, -4.06) * mm, "end": v(-48.06, -5.62) * mm});
            skLineSegment(sketch, "E1043", {"start": v(-48.06, -5.62) * mm, "end": v(-48.6, -6.33) * mm});
            skLineSegment(sketch, "E1044", {"start": v(-48.6, -6.33) * mm, "end": v(-49.14, -7) * mm});
            skLineSegment(sketch, "E1045", {"start": v(-49.14, -7) * mm, "end": v(-49.66, -7.6) * mm});
            skLineSegment(sketch, "E1046", {"start": v(-49.66, -7.6) * mm, "end": v(-50.17, -8.18) * mm});
            skLineSegment(sketch, "E1047", {"start": v(-50.17, -8.18) * mm, "end": v(-50.66, -8.7) * mm});
            skLineSegment(sketch, "E1048", {"start": v(-50.66, -8.7) * mm, "end": v(-51.14, -9.18) * mm});
            skLineSegment(sketch, "E1049", {"start": v(-51.14, -9.18) * mm, "end": v(-51.6, -9.62) * mm});
            skLineSegment(sketch, "E1050", {"start": v(-51.6, -9.62) * mm, "end": v(-52.06, -10) * mm});
            skLineSegment(sketch, "E1051", {"start": v(-52.06, -10) * mm, "end": v(-52.5, -10.35) * mm});
            skLineSegment(sketch, "E1052", {"start": v(-52.5, -10.35) * mm, "end": v(-52.72, -10.5) * mm});
            skLineSegment(sketch, "E1053", {"start": v(-52.72, -10.5) * mm, "end": v(-52.93, -10.64) * mm});
            skLineSegment(sketch, "E1054", {"start": v(-52.93, -10.64) * mm, "end": v(-53.14, -10.78) * mm});
            skLineSegment(sketch, "E1055", {"start": v(-53.14, -10.78) * mm, "end": v(-53.35, -10.9) * mm});
            skLineSegment(sketch, "E1056", {"start": v(-53.35, -10.9) * mm, "end": v(-53.55, -11) * mm});
            skLineSegment(sketch, "E1057", {"start": v(-53.55, -11) * mm, "end": v(-53.75, -11.1) * mm});
            skLineSegment(sketch, "E1058", {"start": v(-53.75, -11.1) * mm, "end": v(-53.95, -11.19) * mm});
            skLineSegment(sketch, "E1059", {"start": v(-53.95, -11.19) * mm, "end": v(-54.14, -11.26) * mm});
            skLineSegment(sketch, "E1060", {"start": v(-54.14, -11.26) * mm, "end": v(-54.33, -11.32) * mm});
            skLineSegment(sketch, "E1061", {"start": v(-54.33, -11.32) * mm, "end": v(-54.52, -11.37) * mm});
            skLineSegment(sketch, "E1062", {"start": v(-54.52, -11.37) * mm, "end": v(-54.7, -11.41) * mm});
            skLineSegment(sketch, "E1063", {"start": v(-54.7, -11.41) * mm, "end": v(-54.88, -11.44) * mm});
            skLineSegment(sketch, "E1064", {"start": v(-54.88, -11.44) * mm, "end": v(-55.06, -11.46) * mm});
            skLineSegment(sketch, "E1065", {"start": v(-55.06, -11.46) * mm, "end": v(-55.24, -11.47) * mm});
            skLineSegment(sketch, "E1066", {"start": v(-55.24, -11.47) * mm, "end": v(-55.42, -11.46) * mm});
            skLineSegment(sketch, "E1067", {"start": v(-55.42, -11.46) * mm, "end": v(-55.6, -11.44) * mm});
            skLineSegment(sketch, "E1068", {"start": v(-55.6, -11.44) * mm, "end": v(-55.78, -11.4) * mm});
            skLineSegment(sketch, "E1069", {"start": v(-55.78, -11.4) * mm, "end": v(-55.95, -11.36) * mm});
            skLineSegment(sketch, "E1070", {"start": v(-55.95, -11.36) * mm, "end": v(-56.11, -11.3) * mm});
            skLineSegment(sketch, "E1071", {"start": v(-56.11, -11.3) * mm, "end": v(-56.27, -11.24) * mm});
            skLineSegment(sketch, "E1072", {"start": v(-56.27, -11.24) * mm, "end": v(-56.43, -11.16) * mm});
            skLineSegment(sketch, "E1073", {"start": v(-56.43, -11.16) * mm, "end": v(-56.58, -11.06) * mm});
            skLineSegment(sketch, "E1074", {"start": v(-56.58, -11.06) * mm, "end": v(-56.72, -10.95) * mm});
            skLineSegment(sketch, "E1075", {"start": v(-56.72, -10.95) * mm, "end": v(-56.86, -10.83) * mm});
            skLineSegment(sketch, "E1076", {"start": v(-56.86, -10.83) * mm, "end": v(-57, -10.7) * mm});
            skLineSegment(sketch, "E1077", {"start": v(-57, -10.7) * mm, "end": v(-57.13, -10.55) * mm});
            skLineSegment(sketch, "E1078", {"start": v(-57.13, -10.55) * mm, "end": v(-57.25, -10.4) * mm});
            skLineSegment(sketch, "E1079", {"start": v(-57.25, -10.4) * mm, "end": v(-57.37, -10.22) * mm});
            skLineSegment(sketch, "E1080", {"start": v(-57.37, -10.22) * mm, "end": v(-57.49, -10.04) * mm});
            skLineSegment(sketch, "E1081", {"start": v(-57.49, -10.04) * mm, "end": v(-57.6, -9.84) * mm});
            skLineSegment(sketch, "E1082", {"start": v(-57.6, -9.84) * mm, "end": v(-57.7, -9.63) * mm});
            skLineSegment(sketch, "E1083", {"start": v(-57.7, -9.63) * mm, "end": v(-57.89, -9.19) * mm});
            skLineSegment(sketch, "E1084", {"start": v(-57.89, -9.19) * mm, "end": v(-58.04, -8.71) * mm});
            skLineSegment(sketch, "E1085", {"start": v(-58.04, -8.71) * mm, "end": v(-58.18, -8.2) * mm});
            skLineSegment(sketch, "E1086", {"start": v(-58.18, -8.2) * mm, "end": v(-58.28, -7.67) * mm});
            skLineSegment(sketch, "E1087", {"start": v(-58.28, -7.67) * mm, "end": v(-58.36, -7.1) * mm});
            skLineSegment(sketch, "E1088", {"start": v(-58.36, -7.1) * mm, "end": v(-58.41, -6.5) * mm});
            skLineSegment(sketch, "E1089", {"start": v(-58.41, -6.5) * mm, "end": v(-58.44, -5.87) * mm});
            skLineSegment(sketch, "E1090", {"start": v(-58.44, -5.87) * mm, "end": v(-58.44, -5.54) * mm});
            skLineSegment(sketch, "E1091", {"start": v(-58.44, -5.54) * mm, "end": v(-58.43, -4.99) * mm});
            skLineSegment(sketch, "E1092", {"start": v(-58.43, -4.99) * mm, "end": v(-58.38, -4.41) * mm});
            skLineSegment(sketch, "E1093", {"start": v(-58.38, -4.41) * mm, "end": v(-58.3, -3.81) * mm});
            skLineSegment(sketch, "E1094", {"start": v(-58.3, -3.81) * mm, "end": v(-58.2, -3.19) * mm});
            skLineSegment(sketch, "E1095", {"start": v(-58.2, -3.19) * mm, "end": v(-58.05, -2.53) * mm});
            skLineSegment(sketch, "E1096", {"start": v(-58.05, -2.53) * mm, "end": v(-57.87, -1.86) * mm});
            skLineSegment(sketch, "E1097", {"start": v(-57.87, -1.86) * mm, "end": v(-57.67, -1.16) * mm});
            skLineSegment(sketch, "E1098", {"start": v(-57.67, -1.16) * mm, "end": v(-57.43, -0.43) * mm});
            skLineSegment(sketch, "E1099", {"start": v(-57.43, -0.43) * mm, "end": v(-56.88, 1.06) * mm});
            skLineSegment(sketch, "E1100", {"start": v(-56.88, 1.06) * mm, "end": v(-56.25, 2.56) * mm});
            skLineSegment(sketch, "E1101", {"start": v(-56.25, 2.56) * mm, "end": v(-55.53, 4.07) * mm});
            skLineSegment(sketch, "E1102", {"start": v(-55.53, 4.07) * mm, "end": v(-54.73, 5.58) * mm});
            skLineSegment(sketch, "E1103", {"start": v(-54.73, 5.58) * mm, "end": v(-53.87, 7.06) * mm});
            skLineSegment(sketch, "E1104", {"start": v(-53.87, 7.06) * mm, "end": v(-53, 8.44) * mm});
            skLineSegment(sketch, "E1105", {"start": v(-53, 8.44) * mm, "end": v(-52.1, 9.72) * mm});
            skLineSegment(sketch, "E1106", {"start": v(-52.1, 9.72) * mm, "end": v(-51.2, 10.9) * mm});
            skLineSegment(sketch, "E1107", {"start": v(-51.2, 10.9) * mm, "end": v(-50.75, 11.44) * mm});
            skLineSegment(sketch, "E1108", {"start": v(-50.75, 11.44) * mm, "end": v(-50.3, 11.95) * mm});
            skLineSegment(sketch, "E1109", {"start": v(-50.3, 11.95) * mm, "end": v(-49.87, 12.41) * mm});
            skLineSegment(sketch, "E1110", {"start": v(-49.87, 12.41) * mm, "end": v(-49.44, 12.83) * mm});
            skLineSegment(sketch, "E1111", {"start": v(-49.44, 12.83) * mm, "end": v(-49.02, 13.2) * mm});
            skLineSegment(sketch, "E1112", {"start": v(-49.02, 13.2) * mm, "end": v(-48.6, 13.54) * mm});
            skLineSegment(sketch, "E1113", {"start": v(-48.6, 13.54) * mm, "end": v(-48.4, 13.7) * mm});
            skLineSegment(sketch, "E1114", {"start": v(-48.4, 13.7) * mm, "end": v(-48.2, 13.83) * mm});
            skLineSegment(sketch, "E1115", {"start": v(-48.2, 13.83) * mm, "end": v(-48, 13.96) * mm});
            skLineSegment(sketch, "E1116", {"start": v(-48, 13.96) * mm, "end": v(-47.81, 14.08) * mm});
            skLineSegment(sketch, "E1117", {"start": v(-47.81, 14.08) * mm, "end": v(-47.66, 14.17) * mm});
            skLineSegment(sketch, "E1118", {"start": v(-47.66, 14.17) * mm, "end": v(-47.58, 14.21) * mm});
            skLineSegment(sketch, "E1119", {"start": v(-47.58, 14.21) * mm, "end": v(-47.51, 14.25) * mm});
            skLineSegment(sketch, "E1120", {"start": v(-47.51, 14.25) * mm, "end": v(-47.44, 14.28) * mm});
            skLineSegment(sketch, "E1121", {"start": v(-47.44, 14.28) * mm, "end": v(-47.37, 14.31) * mm});
            skLineSegment(sketch, "E1122", {"start": v(-47.37, 14.31) * mm, "end": v(-47.3, 14.34) * mm});
            skLineSegment(sketch, "E1123", {"start": v(-47.3, 14.34) * mm, "end": v(-47.25, 14.37) * mm});
            skLineSegment(sketch, "E1124", {"start": v(-47.25, 14.37) * mm, "end": v(-47.19, 14.39) * mm});
            skLineSegment(sketch, "E1125", {"start": v(-47.19, 14.39) * mm, "end": v(-47.13, 14.4) * mm});
            skLineSegment(sketch, "E1126", {"start": v(-47.13, 14.4) * mm, "end": v(-47.07, 14.43) * mm});
            skLineSegment(sketch, "E1127", {"start": v(-47.07, 14.43) * mm, "end": v(-47.02, 14.44) * mm});
            skLineSegment(sketch, "E1128", {"start": v(-47.02, 14.44) * mm, "end": v(-46.96, 14.45) * mm});
            skLineSegment(sketch, "E1129", {"start": v(-46.96, 14.45) * mm, "end": v(-46.91, 14.46) * mm});
            skLineSegment(sketch, "E1130", {"start": v(-46.91, 14.46) * mm, "end": v(-46.86, 14.46) * mm});
            skLineSegment(sketch, "E1131", {"start": v(-46.86, 14.46) * mm, "end": v(-46.82, 14.46) * mm});
            skLineSegment(sketch, "E1132", {"start": v(-46.82, 14.46) * mm, "end": v(-46.76, 14.46) * mm});
            skLineSegment(sketch, "E1133", {"start": v(-46.76, 14.46) * mm, "end": v(-46.71, 14.46) * mm});
            skLineSegment(sketch, "E1134", {"start": v(-46.71, 14.46) * mm, "end": v(-46.66, 14.45) * mm});
            skLineSegment(sketch, "E1135", {"start": v(-46.66, 14.45) * mm, "end": v(-46.62, 14.44) * mm});
            skLineSegment(sketch, "E1136", {"start": v(-46.62, 14.44) * mm, "end": v(-46.57, 14.42) * mm});
            skLineSegment(sketch, "E1137", {"start": v(-46.57, 14.42) * mm, "end": v(-46.53, 14.4) * mm});
            skLineSegment(sketch, "E1138", {"start": v(-46.53, 14.4) * mm, "end": v(-46.49, 14.39) * mm});
            skLineSegment(sketch, "E1139", {"start": v(-46.49, 14.39) * mm, "end": v(-46.45, 14.36) * mm});
            skLineSegment(sketch, "E1140", {"start": v(-46.45, 14.36) * mm, "end": v(-46.43, 14.35) * mm});
            skLineSegment(sketch, "E1141", {"start": v(-46.43, 14.35) * mm, "end": v(-46.4, 14.32) * mm});
            skLineSegment(sketch, "E1142", {"start": v(-46.4, 14.32) * mm, "end": v(-46.36, 14.29) * mm});
            skLineSegment(sketch, "E1143", {"start": v(-46.36, 14.29) * mm, "end": v(-46.33, 14.25) * mm});
            skLineSegment(sketch, "E1144", {"start": v(-46.33, 14.25) * mm, "end": v(-46.3, 14.22) * mm});
            skLineSegment(sketch, "E1145", {"start": v(-46.3, 14.22) * mm, "end": v(-46.28, 14.18) * mm});
            skLineSegment(sketch, "E1146", {"start": v(-46.28, 14.18) * mm, "end": v(-46.26, 14.13) * mm});
            skLineSegment(sketch, "E1147", {"start": v(-46.26, 14.13) * mm, "end": v(-46.24, 14.09) * mm});
            skLineSegment(sketch, "E1148", {"start": v(-46.24, 14.09) * mm, "end": v(-46.23, 14.06) * mm});
            skLineSegment(sketch, "E1149", {"start": v(-46.23, 14.06) * mm, "end": v(-46.21, 14.01) * mm});
            skLineSegment(sketch, "E1150", {"start": v(-46.21, 14.01) * mm, "end": v(-46.2, 13.96) * mm});
            skLineSegment(sketch, "E1151", {"start": v(-46.2, 13.96) * mm, "end": v(-46.18, 13.9) * mm});
            skLineSegment(sketch, "E1152", {"start": v(-46.18, 13.9) * mm, "end": v(-46.16, 13.84) * mm});
            skLineSegment(sketch, "E1153", {"start": v(-46.16, 13.84) * mm, "end": v(-46.15, 13.77) * mm});
            skLineSegment(sketch, "E1154", {"start": v(-46.15, 13.77) * mm, "end": v(-46.14, 13.7) * mm});
            skLineSegment(sketch, "E1155", {"start": v(-46.14, 13.7) * mm, "end": v(-46.13, 13.62) * mm});
            skLineSegment(sketch, "E1156", {"start": v(-46.13, 13.62) * mm, "end": v(-46.12, 13.54) * mm});
            skLineSegment(sketch, "E1157", {"start": v(-46.12, 13.54) * mm, "end": v(-46.1, 13.45) * mm});
            skLineSegment(sketch, "E1158", {"start": v(-46.1, 13.45) * mm, "end": v(-46.1, 13.36) * mm});
            skLineSegment(sketch, "E1159", {"start": v(-46.1, 13.36) * mm, "end": v(-46.1, 13.27) * mm});
            skLineSegment(sketch, "E1160", {"start": v(-46.1, 13.27) * mm, "end": v(-46.09, 13.17) * mm});
            skLineSegment(sketch, "E1161", {"start": v(-46.09, 13.17) * mm, "end": v(-46.09, 13.07) * mm});
            skLineSegment(sketch, "E1162", {"start": v(-46.09, 13.07) * mm, "end": v(-46.08, 12.85) * mm});
            skLineSegment(sketch, "E1163", {"start": v(-46.08, 12.85) * mm, "end": v(-46.08, 12.73) * mm});
            skLineSegment(sketch, "E1164", {"start": v(-46.08, 12.73) * mm, "end": v(-46.09, 12.36) * mm});
            skLineSegment(sketch, "E1165", {"start": v(-46.09, 12.36) * mm, "end": v(-46.12, 11.98) * mm});
            skLineSegment(sketch, "E1166", {"start": v(-46.12, 11.98) * mm, "end": v(-46.16, 11.58) * mm});
            skLineSegment(sketch, "E1167", {"start": v(-46.16, 11.58) * mm, "end": v(-46.23, 11.18) * mm});
            skLineSegment(sketch, "E1168", {"start": v(-46.23, 11.18) * mm, "end": v(-46.31, 10.77) * mm});
            skLineSegment(sketch, "E1169", {"start": v(-46.31, 10.77) * mm, "end": v(-46.42, 10.34) * mm});
            skLineSegment(sketch, "E1170", {"start": v(-46.42, 10.34) * mm, "end": v(-46.54, 9.9) * mm});
            skLineSegment(sketch, "E1171", {"start": v(-46.54, 9.9) * mm, "end": v(-46.68, 9.46) * mm});
            skLineSegment(sketch, "E1172", {"start": v(-46.68, 9.46) * mm, "end": v(-47.01, 8.54) * mm});
            skLineSegment(sketch, "E1173", {"start": v(-47.01, 8.54) * mm, "end": v(-47.42, 7.57) * mm});
            skLineSegment(sketch, "E1174", {"start": v(-47.42, 7.57) * mm, "end": v(-47.9, 6.57) * mm});
            skLineSegment(sketch, "E1175", {"start": v(-47.9, 6.57) * mm, "end": v(-48.46, 5.52) * mm});
            skLineSegment(sketch, "E1176", {"start": v(-48.46, 5.52) * mm, "end": v(-49.09, 4.45) * mm});
            skLineSegment(sketch, "E1177", {"start": v(-49.09, 4.45) * mm, "end": v(-49.77, 3.37) * mm});
            skLineSegment(sketch, "E1178", {"start": v(-49.77, 3.37) * mm, "end": v(-50.52, 2.3) * mm});
            skLineSegment(sketch, "E1179", {"start": v(-50.52, 2.3) * mm, "end": v(-52.18, 0.12) * mm});
            skLineSegment(sketch, "E1180", {"start": v(-52.18, 0.12) * mm, "end": v(-54.07, -2.09) * mm});
            skLineSegment(sketch, "E1181", {"start": v(-54.07, -2.09) * mm, "end": v(-55.11, -3.2) * mm});
            skLineSegment(sketch, "E1182", {"start": v(-55.11, -3.2) * mm, "end": v(-55.16, -3.46) * mm});
            skLineSegment(sketch, "E1183", {"start": v(-55.16, -3.46) * mm, "end": v(-55.2, -3.71) * mm});
            skLineSegment(sketch, "E1184", {"start": v(-55.2, -3.71) * mm, "end": v(-55.24, -3.95) * mm});
            skLineSegment(sketch, "E1185", {"start": v(-55.24, -3.95) * mm, "end": v(-55.27, -4.17) * mm});
            skLineSegment(sketch, "E1186", {"start": v(-55.27, -4.17) * mm, "end": v(-55.3, -4.37) * mm});
            skLineSegment(sketch, "E1187", {"start": v(-55.3, -4.37) * mm, "end": v(-55.3, -4.47) * mm});
            skLineSegment(sketch, "E1188", {"start": v(-55.3, -4.47) * mm, "end": v(-55.3, -4.56) * mm});
            skLineSegment(sketch, "E1189", {"start": v(-55.3, -4.56) * mm, "end": v(-55.31, -4.64) * mm});
            skLineSegment(sketch, "E1190", {"start": v(-55.31, -4.64) * mm, "end": v(-55.32, -4.73) * mm});
            skLineSegment(sketch, "E1191", {"start": v(-55.32, -4.73) * mm, "end": v(-55.32, -4.8) * mm});
            skLineSegment(sketch, "E1192", {"start": v(-55.32, -4.8) * mm, "end": v(-55.32, -4.88) * mm});
            skLineSegment(sketch, "E1193", {"start": v(-55.32, -4.88) * mm, "end": v(-55.31, -5.21) * mm});
            skLineSegment(sketch, "E1194", {"start": v(-55.31, -5.21) * mm, "end": v(-55.29, -5.53) * mm});
            skLineSegment(sketch, "E1195", {"start": v(-55.29, -5.53) * mm, "end": v(-55.24, -5.83) * mm});
            skLineSegment(sketch, "E1196", {"start": v(-55.24, -5.83) * mm, "end": v(-55.18, -6.1) * mm});
            skLineSegment(sketch, "E1197", {"start": v(-55.18, -6.1) * mm, "end": v(-55.1, -6.37) * mm});
            skLineSegment(sketch, "E1198", {"start": v(-55.1, -6.37) * mm, "end": v(-55.05, -6.5) * mm});
            skLineSegment(sketch, "E1199", {"start": v(-55.05, -6.5) * mm, "end": v(-55, -6.62) * mm});
            skLineSegment(sketch, "E1200", {"start": v(-55, -6.62) * mm, "end": v(-54.95, -6.74) * mm});
            skLineSegment(sketch, "E1201", {"start": v(-54.95, -6.74) * mm, "end": v(-54.89, -6.86) * mm});
            skLineSegment(sketch, "E1202", {"start": v(-54.89, -6.86) * mm, "end": v(-54.82, -6.97) * mm});
            skLineSegment(sketch, "E1203", {"start": v(-54.82, -6.97) * mm, "end": v(-54.75, -7.08) * mm});
            skLineSegment(sketch, "E1204", {"start": v(-54.75, -7.08) * mm, "end": v(-54.68, -7.18) * mm});
            skLineSegment(sketch, "E1205", {"start": v(-54.68, -7.18) * mm, "end": v(-54.6, -7.28) * mm});
            skLineSegment(sketch, "E1206", {"start": v(-54.6, -7.28) * mm, "end": v(-54.51, -7.36) * mm});
            skLineSegment(sketch, "E1207", {"start": v(-54.51, -7.36) * mm, "end": v(-54.43, -7.45) * mm});
            skLineSegment(sketch, "E1208", {"start": v(-54.43, -7.45) * mm, "end": v(-54.34, -7.52) * mm});
            skLineSegment(sketch, "E1209", {"start": v(-54.34, -7.52) * mm, "end": v(-54.25, -7.6) * mm});
            skLineSegment(sketch, "E1210", {"start": v(-54.25, -7.6) * mm, "end": v(-54.15, -7.65) * mm});
            skLineSegment(sketch, "E1211", {"start": v(-54.15, -7.65) * mm, "end": v(-54.05, -7.71) * mm});
            skLineSegment(sketch, "E1212", {"start": v(-54.05, -7.71) * mm, "end": v(-53.95, -7.76) * mm});
            skLineSegment(sketch, "E1213", {"start": v(-53.95, -7.76) * mm, "end": v(-53.84, -7.8) * mm});
            skLineSegment(sketch, "E1214", {"start": v(-53.84, -7.8) * mm, "end": v(-53.73, -7.84) * mm});
            skLineSegment(sketch, "E1215", {"start": v(-53.73, -7.84) * mm, "end": v(-53.62, -7.87) * mm});
            skLineSegment(sketch, "E1216", {"start": v(-53.62, -7.87) * mm, "end": v(-53.5, -7.9) * mm});
            skLineSegment(sketch, "E1217", {"start": v(-53.5, -7.9) * mm, "end": v(-53.38, -7.9) * mm});
            skLineSegment(sketch, "E1218", {"start": v(-53.38, -7.9) * mm, "end": v(-53.25, -7.92) * mm});
            skLineSegment(sketch, "E1219", {"start": v(-53.25, -7.92) * mm, "end": v(-53.13, -7.92) * mm});
            skLineSegment(sketch, "E1220", {"start": v(-53.13, -7.92) * mm, "end": v(-53.06, -7.92) * mm});
            skLineSegment(sketch, "E1221", {"start": v(-53.06, -7.92) * mm, "end": v(-53, -7.92) * mm});
            skLineSegment(sketch, "E1222", {"start": v(-53, -7.92) * mm, "end": v(-52.93, -7.9) * mm});
            skLineSegment(sketch, "E1223", {"start": v(-52.93, -7.9) * mm, "end": v(-52.86, -7.9) * mm});
            skLineSegment(sketch, "E1224", {"start": v(-52.86, -7.9) * mm, "end": v(-52.79, -7.88) * mm});
            skLineSegment(sketch, "E1225", {"start": v(-52.79, -7.88) * mm, "end": v(-52.72, -7.87) * mm});
            skLineSegment(sketch, "E1226", {"start": v(-52.72, -7.87) * mm, "end": v(-52.58, -7.82) * mm});
            skLineSegment(sketch, "E1227", {"start": v(-52.58, -7.82) * mm, "end": v(-52.43, -7.77) * mm});
            skLineSegment(sketch, "E1228", {"start": v(-52.43, -7.77) * mm, "end": v(-52.29, -7.7) * mm});
            skLineSegment(sketch, "E1229", {"start": v(-52.29, -7.7) * mm, "end": v(-52.14, -7.62) * mm});
            skLineSegment(sketch, "E1230", {"start": v(-52.14, -7.62) * mm, "end": v(-51.99, -7.52) * mm});
            skLineSegment(sketch, "E1231", {"start": v(-51.99, -7.52) * mm, "end": v(-51.68, -7.3) * mm});
            skLineSegment(sketch, "E1232", {"start": v(-51.68, -7.3) * mm, "end": v(-51.36, -7.05) * mm});
            skLineSegment(sketch, "E1233", {"start": v(-51.36, -7.05) * mm, "end": v(-51.03, -6.78) * mm});
            skLineSegment(sketch, "E1234", {"start": v(-51.03, -6.78) * mm, "end": v(-50.7, -6.49) * mm});
            skLineSegment(sketch, "E1235", {"start": v(-50.7, -6.49) * mm, "end": v(-50.66, -6.45) * mm});
            skLineSegment(sketch, "E1236", {"start": v(-50.66, -6.45) * mm, "end": v(-50.61, -6.4) * mm});
            skLineSegment(sketch, "E1237", {"start": v(-50.61, -6.4) * mm, "end": v(-50.56, -6.36) * mm});
            skLineSegment(sketch, "E1238", {"start": v(-50.56, -6.36) * mm, "end": v(-50.51, -6.32) * mm});
            skLineSegment(sketch, "E1239", {"start": v(-50.51, -6.32) * mm, "end": v(-50.46, -6.27) * mm});
            skLineSegment(sketch, "E1240", {"start": v(-50.46, -6.27) * mm, "end": v(-50.4, -6.22) * mm});
            skLineSegment(sketch, "E1241", {"start": v(-50.4, -6.22) * mm, "end": v(-50.28, -6.1) * mm});
            skLineSegment(sketch, "E1242", {"start": v(-50.28, -6.1) * mm, "end": v(-50.15, -5.99) * mm});
            skLineSegment(sketch, "E1243", {"start": v(-50.15, -5.99) * mm, "end": v(-50.01, -5.86) * mm});
            skLineSegment(sketch, "E1244", {"start": v(-50.01, -5.86) * mm, "end": v(-49.86, -5.72) * mm});
            skLineSegment(sketch, "E1245", {"start": v(-49.86, -5.72) * mm, "end": v(-49.7, -5.57) * mm});
            skLineSegment(sketch, "E1246", {"start": v(-49.7, -5.57) * mm, "end": v(-49.53, -5.42) * mm});
            skLineSegment(sketch, "E1247", {"start": v(-49.53, -5.42) * mm, "end": v(-49.35, -5.25) * mm});
            skLineSegment(sketch, "E1248", {"start": v(-49.35, -5.25) * mm, "end": v(-49.16, -5.08) * mm});
            skLineSegment(sketch, "E1249", {"start": v(-49.16, -5.08) * mm, "end": v(-48.96, -4.9) * mm});
            skLineSegment(sketch, "E1250", {"start": v(-48.96, -4.9) * mm, "end": v(-48.75, -4.7) * mm});
            skLineSegment(sketch, "E1251", {"start": v(-48.75, -4.7) * mm, "end": v(-48.53, -4.5) * mm});
            skLineSegment(sketch, "E1252", {"start": v(-48.53, -4.5) * mm, "end": v(-48.06, -4.06) * mm});
            skLineSegment(sketch, "E1253", {"start": v(-54.37, -0.26) * mm, "end": v(-53.83, 0.3) * mm});
            skLineSegment(sketch, "E1254", {"start": v(-53.83, 0.3) * mm, "end": v(-53.3, 0.89) * mm});
            skLineSegment(sketch, "E1255", {"start": v(-53.3, 0.89) * mm, "end": v(-52.77, 1.52) * mm});
            skLineSegment(sketch, "E1256", {"start": v(-52.77, 1.52) * mm, "end": v(-52.26, 2.18) * mm});
            skLineSegment(sketch, "E1257", {"start": v(-52.26, 2.18) * mm, "end": v(-51.75, 2.88) * mm});
            skLineSegment(sketch, "E1258", {"start": v(-51.75, 2.88) * mm, "end": v(-50.78, 4.35) * mm});
            skLineSegment(sketch, "E1259", {"start": v(-50.78, 4.35) * mm, "end": v(-50.32, 5.12) * mm});
            skLineSegment(sketch, "E1260", {"start": v(-50.32, 5.12) * mm, "end": v(-49.9, 5.88) * mm});
            skLineSegment(sketch, "E1261", {"start": v(-49.9, 5.88) * mm, "end": v(-49.51, 6.6) * mm});
            skLineSegment(sketch, "E1262", {"start": v(-49.51, 6.6) * mm, "end": v(-49.19, 7.28) * mm});
            skLineSegment(sketch, "E1263", {"start": v(-49.19, 7.28) * mm, "end": v(-49.04, 7.6) * mm});
            skLineSegment(sketch, "E1264", {"start": v(-49.04, 7.6) * mm, "end": v(-48.9, 7.92) * mm});
            skLineSegment(sketch, "E1265", {"start": v(-48.9, 7.92) * mm, "end": v(-48.78, 8.22) * mm});
            skLineSegment(sketch, "E1266", {"start": v(-48.78, 8.22) * mm, "end": v(-48.68, 8.5) * mm});
            skLineSegment(sketch, "E1267", {"start": v(-48.68, 8.5) * mm, "end": v(-48.63, 8.64) * mm});
            skLineSegment(sketch, "E1268", {"start": v(-48.63, 8.64) * mm, "end": v(-48.59, 8.77) * mm});
            skLineSegment(sketch, "E1269", {"start": v(-48.59, 8.77) * mm, "end": v(-48.55, 8.9) * mm});
            skLineSegment(sketch, "E1270", {"start": v(-48.55, 8.9) * mm, "end": v(-48.51, 9.01) * mm});
            skLineSegment(sketch, "E1271", {"start": v(-48.51, 9.01) * mm, "end": v(-48.48, 9.13) * mm});
            skLineSegment(sketch, "E1272", {"start": v(-48.48, 9.13) * mm, "end": v(-48.45, 9.24) * mm});
            skLineSegment(sketch, "E1273", {"start": v(-48.45, 9.24) * mm, "end": v(-48.43, 9.34) * mm});
            skLineSegment(sketch, "E1274", {"start": v(-48.43, 9.34) * mm, "end": v(-48.41, 9.44) * mm});
            skLineSegment(sketch, "E1275", {"start": v(-48.41, 9.44) * mm, "end": v(-48.4, 9.54) * mm});
            skLineSegment(sketch, "E1276", {"start": v(-48.4, 9.54) * mm, "end": v(-48.39, 9.63) * mm});
            skLineSegment(sketch, "E1277", {"start": v(-48.39, 9.63) * mm, "end": v(-48.38, 9.72) * mm});
            skLineSegment(sketch, "E1278", {"start": v(-48.38, 9.72) * mm, "end": v(-48.38, 9.8) * mm});
            skLineSegment(sketch, "E1279", {"start": v(-48.38, 9.8) * mm, "end": v(-48.38, 9.86) * mm});
            skLineSegment(sketch, "E1280", {"start": v(-48.38, 9.86) * mm, "end": v(-48.39, 9.91) * mm});
            skLineSegment(sketch, "E1281", {"start": v(-48.39, 9.91) * mm, "end": v(-48.39, 9.94) * mm});
            skLineSegment(sketch, "E1282", {"start": v(-48.39, 9.94) * mm, "end": v(-48.4, 9.96) * mm});
            skLineSegment(sketch, "E1283", {"start": v(-48.4, 9.96) * mm, "end": v(-48.4, 9.99) * mm});
            skLineSegment(sketch, "E1284", {"start": v(-48.4, 9.99) * mm, "end": v(-48.4, 10.01) * mm});
            skLineSegment(sketch, "E1285", {"start": v(-48.4, 10.01) * mm, "end": v(-48.4, 10.03) * mm});
            skLineSegment(sketch, "E1286", {"start": v(-48.4, 10.03) * mm, "end": v(-48.41, 10.06) * mm});
            skLineSegment(sketch, "E1287", {"start": v(-48.41, 10.06) * mm, "end": v(-48.42, 10.08) * mm});
            skLineSegment(sketch, "E1288", {"start": v(-48.42, 10.08) * mm, "end": v(-48.43, 10.1) * mm});
            skLineSegment(sketch, "E1289", {"start": v(-48.43, 10.1) * mm, "end": v(-48.44, 10.11) * mm});
            skLineSegment(sketch, "E1290", {"start": v(-48.44, 10.11) * mm, "end": v(-48.44, 10.13) * mm});
            skLineSegment(sketch, "E1291", {"start": v(-48.44, 10.13) * mm, "end": v(-48.45, 10.15) * mm});
            skLineSegment(sketch, "E1292", {"start": v(-48.45, 10.15) * mm, "end": v(-48.46, 10.16) * mm});
            skLineSegment(sketch, "E1293", {"start": v(-48.46, 10.16) * mm, "end": v(-48.48, 10.18) * mm});
            skLineSegment(sketch, "E1294", {"start": v(-48.48, 10.18) * mm, "end": v(-48.49, 10.2) * mm});
            skLineSegment(sketch, "E1295", {"start": v(-48.49, 10.2) * mm, "end": v(-48.5, 10.2) * mm});
            skLineSegment(sketch, "E1296", {"start": v(-48.5, 10.2) * mm, "end": v(-48.51, 10.22) * mm});
            skLineSegment(sketch, "E1297", {"start": v(-48.51, 10.22) * mm, "end": v(-48.53, 10.23) * mm});
            skLineSegment(sketch, "E1298", {"start": v(-48.53, 10.23) * mm, "end": v(-48.54, 10.24) * mm});
            skLineSegment(sketch, "E1299", {"start": v(-48.54, 10.24) * mm, "end": v(-48.55, 10.25) * mm});
            skLineSegment(sketch, "E1300", {"start": v(-48.55, 10.25) * mm, "end": v(-48.57, 10.25) * mm});
            skLineSegment(sketch, "E1301", {"start": v(-48.57, 10.25) * mm, "end": v(-48.59, 10.26) * mm});
            skLineSegment(sketch, "E1302", {"start": v(-48.59, 10.26) * mm, "end": v(-48.6, 10.27) * mm});
            skLineSegment(sketch, "E1303", {"start": v(-48.6, 10.27) * mm, "end": v(-48.62, 10.27) * mm});
            skLineSegment(sketch, "E1304", {"start": v(-48.62, 10.27) * mm, "end": v(-48.64, 10.28) * mm});
            skLineSegment(sketch, "E1305", {"start": v(-48.64, 10.28) * mm, "end": v(-48.66, 10.28) * mm});
            skLineSegment(sketch, "E1306", {"start": v(-48.66, 10.28) * mm, "end": v(-48.68, 10.28) * mm});
            skLineSegment(sketch, "E1307", {"start": v(-48.68, 10.28) * mm, "end": v(-48.7, 10.28) * mm});
            skLineSegment(sketch, "E1308", {"start": v(-48.7, 10.28) * mm, "end": v(-48.72, 10.28) * mm});
            skLineSegment(sketch, "E1309", {"start": v(-48.72, 10.28) * mm, "end": v(-48.73, 10.28) * mm});
            skLineSegment(sketch, "E1310", {"start": v(-48.73, 10.28) * mm, "end": v(-48.73, 10.28) * mm});
            skLineSegment(sketch, "E1311", {"start": v(-48.73, 10.28) * mm, "end": v(-48.74, 10.28) * mm});
            skLineSegment(sketch, "E1312", {"start": v(-48.74, 10.28) * mm, "end": v(-48.75, 10.28) * mm});
            skLineSegment(sketch, "E1313", {"start": v(-48.75, 10.28) * mm, "end": v(-48.76, 10.28) * mm});
            skLineSegment(sketch, "E1314", {"start": v(-48.76, 10.28) * mm, "end": v(-48.77, 10.28) * mm});
            skLineSegment(sketch, "E1315", {"start": v(-48.77, 10.28) * mm, "end": v(-48.78, 10.27) * mm});
            skLineSegment(sketch, "E1316", {"start": v(-48.78, 10.27) * mm, "end": v(-48.8, 10.27) * mm});
            skLineSegment(sketch, "E1317", {"start": v(-48.8, 10.27) * mm, "end": v(-48.8, 10.27) * mm});
            skLineSegment(sketch, "E1318", {"start": v(-48.8, 10.27) * mm, "end": v(-48.82, 10.26) * mm});
            skLineSegment(sketch, "E1319", {"start": v(-48.82, 10.26) * mm, "end": v(-48.83, 10.26) * mm});
            skLineSegment(sketch, "E1320", {"start": v(-48.83, 10.26) * mm, "end": v(-48.85, 10.25) * mm});
            skLineSegment(sketch, "E1321", {"start": v(-48.85, 10.25) * mm, "end": v(-48.87, 10.24) * mm});
            skLineSegment(sketch, "E1322", {"start": v(-48.87, 10.24) * mm, "end": v(-48.9, 10.23) * mm});
            skLineSegment(sketch, "E1323", {"start": v(-48.9, 10.23) * mm, "end": v(-48.93, 10.21) * mm});
            skLineSegment(sketch, "E1324", {"start": v(-48.93, 10.21) * mm, "end": v(-48.97, 10.2) * mm});
            skLineSegment(sketch, "E1325", {"start": v(-48.97, 10.2) * mm, "end": v(-49, 10.18) * mm});
            skLineSegment(sketch, "E1326", {"start": v(-49, 10.18) * mm, "end": v(-49.04, 10.15) * mm});
            skLineSegment(sketch, "E1327", {"start": v(-49.04, 10.15) * mm, "end": v(-49.08, 10.13) * mm});
            skLineSegment(sketch, "E1328", {"start": v(-49.08, 10.13) * mm, "end": v(-49.12, 10.1) * mm});
            skLineSegment(sketch, "E1329", {"start": v(-49.12, 10.1) * mm, "end": v(-49.16, 10.08) * mm});
            skLineSegment(sketch, "E1330", {"start": v(-49.16, 10.08) * mm, "end": v(-49.2, 10.05) * mm});
            skLineSegment(sketch, "E1331", {"start": v(-49.2, 10.05) * mm, "end": v(-49.37, 9.91) * mm});
            skLineSegment(sketch, "E1332", {"start": v(-49.37, 9.91) * mm, "end": v(-49.53, 9.76) * mm});
            skLineSegment(sketch, "E1333", {"start": v(-49.53, 9.76) * mm, "end": v(-49.7, 9.59) * mm});
            skLineSegment(sketch, "E1334", {"start": v(-49.7, 9.59) * mm, "end": v(-49.87, 9.4) * mm});
            skLineSegment(sketch, "E1335", {"start": v(-49.87, 9.4) * mm, "end": v(-50.04, 9.2) * mm});
            skLineSegment(sketch, "E1336", {"start": v(-50.04, 9.2) * mm, "end": v(-50.21, 8.98) * mm});
            skLineSegment(sketch, "E1337", {"start": v(-50.21, 8.98) * mm, "end": v(-50.39, 8.74) * mm});
            skLineSegment(sketch, "E1338", {"start": v(-50.39, 8.74) * mm, "end": v(-50.57, 8.5) * mm});
            skLineSegment(sketch, "E1339", {"start": v(-50.57, 8.5) * mm, "end": v(-50.75, 8.23) * mm});
            skLineSegment(sketch, "E1340", {"start": v(-50.75, 8.23) * mm, "end": v(-50.94, 7.94) * mm});
            skLineSegment(sketch, "E1341", {"start": v(-50.94, 7.94) * mm, "end": v(-51.12, 7.65) * mm});
            skLineSegment(sketch, "E1342", {"start": v(-51.12, 7.65) * mm, "end": v(-51.5, 7) * mm});
            skLineSegment(sketch, "E1343", {"start": v(-51.5, 7) * mm, "end": v(-51.9, 6.3) * mm});
            skLineSegment(sketch, "E1344", {"start": v(-51.9, 6.3) * mm, "end": v(-52.1, 5.92) * mm});
            skLineSegment(sketch, "E1345", {"start": v(-52.1, 5.92) * mm, "end": v(-52.84, 4.38) * mm});
            skLineSegment(sketch, "E1346", {"start": v(-52.84, 4.38) * mm, "end": v(-53.46, 2.84) * mm});
            skLineSegment(sketch, "E1347", {"start": v(-53.46, 2.84) * mm, "end": v(-53.98, 1.3) * mm});
            skLineSegment(sketch, "E1348", {"start": v(-53.98, 1.3) * mm, "end": v(-54.37, -0.26) * mm});
            skLineSegment(sketch, "E1349", {"start": v(-35.23, -4.06) * mm, "end": v(-35.23, -5.62) * mm});
            skLineSegment(sketch, "E1350", {"start": v(-35.23, -5.62) * mm, "end": v(-35.78, -6.33) * mm});
            skLineSegment(sketch, "E1351", {"start": v(-35.78, -6.33) * mm, "end": v(-36.3, -7) * mm});
            skLineSegment(sketch, "E1352", {"start": v(-36.3, -7) * mm, "end": v(-36.83, -7.6) * mm});
            skLineSegment(sketch, "E1353", {"start": v(-36.83, -7.6) * mm, "end": v(-37.33, -8.18) * mm});
            skLineSegment(sketch, "E1354", {"start": v(-37.33, -8.18) * mm, "end": v(-37.83, -8.7) * mm});
            skLineSegment(sketch, "E1355", {"start": v(-37.83, -8.7) * mm, "end": v(-38.3, -9.18) * mm});
            skLineSegment(sketch, "E1356", {"start": v(-38.3, -9.18) * mm, "end": v(-38.78, -9.62) * mm});
            skLineSegment(sketch, "E1357", {"start": v(-38.78, -9.62) * mm, "end": v(-39.23, -10) * mm});
            skLineSegment(sketch, "E1358", {"start": v(-39.23, -10) * mm, "end": v(-39.67, -10.35) * mm});
            skLineSegment(sketch, "E1359", {"start": v(-39.67, -10.35) * mm, "end": v(-39.89, -10.5) * mm});
            skLineSegment(sketch, "E1360", {"start": v(-39.89, -10.5) * mm, "end": v(-40.1, -10.64) * mm});
            skLineSegment(sketch, "E1361", {"start": v(-40.1, -10.64) * mm, "end": v(-40.31, -10.78) * mm});
            skLineSegment(sketch, "E1362", {"start": v(-40.31, -10.78) * mm, "end": v(-40.52, -10.9) * mm});
            skLineSegment(sketch, "E1363", {"start": v(-40.52, -10.9) * mm, "end": v(-40.72, -11) * mm});
            skLineSegment(sketch, "E1364", {"start": v(-40.72, -11) * mm, "end": v(-40.92, -11.1) * mm});
            skLineSegment(sketch, "E1365", {"start": v(-40.92, -11.1) * mm, "end": v(-41.12, -11.19) * mm});
            skLineSegment(sketch, "E1366", {"start": v(-41.12, -11.19) * mm, "end": v(-41.31, -11.26) * mm});
            skLineSegment(sketch, "E1367", {"start": v(-41.31, -11.26) * mm, "end": v(-41.5, -11.32) * mm});
            skLineSegment(sketch, "E1368", {"start": v(-41.5, -11.32) * mm, "end": v(-41.69, -11.37) * mm});
            skLineSegment(sketch, "E1369", {"start": v(-41.69, -11.37) * mm, "end": v(-41.87, -11.41) * mm});
            skLineSegment(sketch, "E1370", {"start": v(-41.87, -11.41) * mm, "end": v(-42.05, -11.44) * mm});
            skLineSegment(sketch, "E1371", {"start": v(-42.05, -11.44) * mm, "end": v(-42.23, -11.46) * mm});
            skLineSegment(sketch, "E1372", {"start": v(-42.23, -11.46) * mm, "end": v(-42.4, -11.47) * mm});
            skLineSegment(sketch, "E1373", {"start": v(-42.4, -11.47) * mm, "end": v(-42.6, -11.46) * mm});
            skLineSegment(sketch, "E1374", {"start": v(-42.6, -11.46) * mm, "end": v(-42.77, -11.44) * mm});
            skLineSegment(sketch, "E1375", {"start": v(-42.77, -11.44) * mm, "end": v(-42.95, -11.4) * mm});
            skLineSegment(sketch, "E1376", {"start": v(-42.95, -11.4) * mm, "end": v(-43.12, -11.36) * mm});
            skLineSegment(sketch, "E1377", {"start": v(-43.12, -11.36) * mm, "end": v(-43.28, -11.3) * mm});
            skLineSegment(sketch, "E1378", {"start": v(-43.28, -11.3) * mm, "end": v(-43.44, -11.24) * mm});
            skLineSegment(sketch, "E1379", {"start": v(-43.44, -11.24) * mm, "end": v(-43.6, -11.16) * mm});
            skLineSegment(sketch, "E1380", {"start": v(-43.6, -11.16) * mm, "end": v(-43.75, -11.06) * mm});
            skLineSegment(sketch, "E1381", {"start": v(-43.75, -11.06) * mm, "end": v(-43.9, -10.95) * mm});
            skLineSegment(sketch, "E1382", {"start": v(-43.9, -10.95) * mm, "end": v(-44.03, -10.83) * mm});
            skLineSegment(sketch, "E1383", {"start": v(-44.03, -10.83) * mm, "end": v(-44.17, -10.7) * mm});
            skLineSegment(sketch, "E1384", {"start": v(-44.17, -10.7) * mm, "end": v(-44.3, -10.55) * mm});
            skLineSegment(sketch, "E1385", {"start": v(-44.3, -10.55) * mm, "end": v(-44.42, -10.4) * mm});
            skLineSegment(sketch, "E1386", {"start": v(-44.42, -10.4) * mm, "end": v(-44.54, -10.22) * mm});
            skLineSegment(sketch, "E1387", {"start": v(-44.54, -10.22) * mm, "end": v(-44.66, -10.04) * mm});
            skLineSegment(sketch, "E1388", {"start": v(-44.66, -10.04) * mm, "end": v(-44.77, -9.84) * mm});
            skLineSegment(sketch, "E1389", {"start": v(-44.77, -9.84) * mm, "end": v(-44.87, -9.63) * mm});
            skLineSegment(sketch, "E1390", {"start": v(-44.87, -9.63) * mm, "end": v(-45.06, -9.19) * mm});
            skLineSegment(sketch, "E1391", {"start": v(-45.06, -9.19) * mm, "end": v(-45.21, -8.71) * mm});
            skLineSegment(sketch, "E1392", {"start": v(-45.21, -8.71) * mm, "end": v(-45.35, -8.2) * mm});
            skLineSegment(sketch, "E1393", {"start": v(-45.35, -8.2) * mm, "end": v(-45.45, -7.67) * mm});
            skLineSegment(sketch, "E1394", {"start": v(-45.45, -7.67) * mm, "end": v(-45.53, -7.1) * mm});
            skLineSegment(sketch, "E1395", {"start": v(-45.53, -7.1) * mm, "end": v(-45.58, -6.5) * mm});
            skLineSegment(sketch, "E1396", {"start": v(-45.58, -6.5) * mm, "end": v(-45.6, -5.87) * mm});
            skLineSegment(sketch, "E1397", {"start": v(-45.6, -5.87) * mm, "end": v(-45.61, -5.54) * mm});
            skLineSegment(sketch, "E1398", {"start": v(-45.61, -5.54) * mm, "end": v(-45.6, -4.99) * mm});
            skLineSegment(sketch, "E1399", {"start": v(-45.6, -4.99) * mm, "end": v(-45.55, -4.41) * mm});
            skLineSegment(sketch, "E1400", {"start": v(-45.55, -4.41) * mm, "end": v(-45.47, -3.81) * mm});
            skLineSegment(sketch, "E1401", {"start": v(-45.47, -3.81) * mm, "end": v(-45.36, -3.19) * mm});
            skLineSegment(sketch, "E1402", {"start": v(-45.36, -3.19) * mm, "end": v(-45.22, -2.53) * mm});
            skLineSegment(sketch, "E1403", {"start": v(-45.22, -2.53) * mm, "end": v(-45.04, -1.86) * mm});
            skLineSegment(sketch, "E1404", {"start": v(-45.04, -1.86) * mm, "end": v(-44.84, -1.16) * mm});
            skLineSegment(sketch, "E1405", {"start": v(-44.84, -1.16) * mm, "end": v(-44.6, -0.43) * mm});
            skLineSegment(sketch, "E1406", {"start": v(-44.6, -0.43) * mm, "end": v(-44.05, 1.06) * mm});
            skLineSegment(sketch, "E1407", {"start": v(-44.05, 1.06) * mm, "end": v(-43.42, 2.56) * mm});
            skLineSegment(sketch, "E1408", {"start": v(-43.42, 2.56) * mm, "end": v(-42.7, 4.07) * mm});
            skLineSegment(sketch, "E1409", {"start": v(-42.7, 4.07) * mm, "end": v(-41.9, 5.58) * mm});
            skLineSegment(sketch, "E1410", {"start": v(-41.9, 5.58) * mm, "end": v(-41.04, 7.06) * mm});
            skLineSegment(sketch, "E1411", {"start": v(-41.04, 7.06) * mm, "end": v(-40.16, 8.44) * mm});
            skLineSegment(sketch, "E1412", {"start": v(-40.16, 8.44) * mm, "end": v(-39.28, 9.72) * mm});
            skLineSegment(sketch, "E1413", {"start": v(-39.28, 9.72) * mm, "end": v(-38.38, 10.9) * mm});
            skLineSegment(sketch, "E1414", {"start": v(-38.38, 10.9) * mm, "end": v(-37.92, 11.44) * mm});
            skLineSegment(sketch, "E1415", {"start": v(-37.92, 11.44) * mm, "end": v(-37.48, 11.95) * mm});
            skLineSegment(sketch, "E1416", {"start": v(-37.48, 11.95) * mm, "end": v(-37.04, 12.41) * mm});
            skLineSegment(sketch, "E1417", {"start": v(-37.04, 12.41) * mm, "end": v(-36.6, 12.83) * mm});
            skLineSegment(sketch, "E1418", {"start": v(-36.6, 12.83) * mm, "end": v(-36.19, 13.2) * mm});
            skLineSegment(sketch, "E1419", {"start": v(-36.19, 13.2) * mm, "end": v(-35.78, 13.54) * mm});
            skLineSegment(sketch, "E1420", {"start": v(-35.78, 13.54) * mm, "end": v(-35.57, 13.7) * mm});
            skLineSegment(sketch, "E1421", {"start": v(-35.57, 13.7) * mm, "end": v(-35.37, 13.83) * mm});
            skLineSegment(sketch, "E1422", {"start": v(-35.37, 13.83) * mm, "end": v(-35.18, 13.96) * mm});
            skLineSegment(sketch, "E1423", {"start": v(-35.18, 13.96) * mm, "end": v(-34.98, 14.08) * mm});
            skLineSegment(sketch, "E1424", {"start": v(-34.98, 14.08) * mm, "end": v(-34.83, 14.17) * mm});
            skLineSegment(sketch, "E1425", {"start": v(-34.83, 14.17) * mm, "end": v(-34.75, 14.21) * mm});
            skLineSegment(sketch, "E1426", {"start": v(-34.75, 14.21) * mm, "end": v(-34.68, 14.25) * mm});
            skLineSegment(sketch, "E1427", {"start": v(-34.68, 14.25) * mm, "end": v(-34.61, 14.28) * mm});
            skLineSegment(sketch, "E1428", {"start": v(-34.61, 14.28) * mm, "end": v(-34.54, 14.31) * mm});
            skLineSegment(sketch, "E1429", {"start": v(-34.54, 14.31) * mm, "end": v(-34.48, 14.34) * mm});
            skLineSegment(sketch, "E1430", {"start": v(-34.48, 14.34) * mm, "end": v(-34.42, 14.37) * mm});
            skLineSegment(sketch, "E1431", {"start": v(-34.42, 14.37) * mm, "end": v(-34.35, 14.39) * mm});
            skLineSegment(sketch, "E1432", {"start": v(-34.35, 14.39) * mm, "end": v(-34.3, 14.4) * mm});
            skLineSegment(sketch, "E1433", {"start": v(-34.3, 14.4) * mm, "end": v(-34.24, 14.43) * mm});
            skLineSegment(sketch, "E1434", {"start": v(-34.24, 14.43) * mm, "end": v(-34.18, 14.44) * mm});
            skLineSegment(sketch, "E1435", {"start": v(-34.18, 14.44) * mm, "end": v(-34.13, 14.45) * mm});
            skLineSegment(sketch, "E1436", {"start": v(-34.13, 14.45) * mm, "end": v(-34.08, 14.46) * mm});
            skLineSegment(sketch, "E1437", {"start": v(-34.08, 14.46) * mm, "end": v(-34.03, 14.46) * mm});
            skLineSegment(sketch, "E1438", {"start": v(-34.03, 14.46) * mm, "end": v(-33.99, 14.46) * mm});
            skLineSegment(sketch, "E1439", {"start": v(-33.99, 14.46) * mm, "end": v(-33.93, 14.46) * mm});
            skLineSegment(sketch, "E1440", {"start": v(-33.93, 14.46) * mm, "end": v(-33.88, 14.46) * mm});
            skLineSegment(sketch, "E1441", {"start": v(-33.88, 14.46) * mm, "end": v(-33.83, 14.45) * mm});
            skLineSegment(sketch, "E1442", {"start": v(-33.83, 14.45) * mm, "end": v(-33.79, 14.44) * mm});
            skLineSegment(sketch, "E1443", {"start": v(-33.79, 14.44) * mm, "end": v(-33.74, 14.42) * mm});
            skLineSegment(sketch, "E1444", {"start": v(-33.74, 14.42) * mm, "end": v(-33.7, 14.4) * mm});
            skLineSegment(sketch, "E1445", {"start": v(-33.7, 14.4) * mm, "end": v(-33.66, 14.39) * mm});
            skLineSegment(sketch, "E1446", {"start": v(-33.66, 14.39) * mm, "end": v(-33.62, 14.36) * mm});
            skLineSegment(sketch, "E1447", {"start": v(-33.62, 14.36) * mm, "end": v(-33.6, 14.35) * mm});
            skLineSegment(sketch, "E1448", {"start": v(-33.6, 14.35) * mm, "end": v(-33.57, 14.32) * mm});
            skLineSegment(sketch, "E1449", {"start": v(-33.57, 14.32) * mm, "end": v(-33.53, 14.29) * mm});
            skLineSegment(sketch, "E1450", {"start": v(-33.53, 14.29) * mm, "end": v(-33.5, 14.25) * mm});
            skLineSegment(sketch, "E1451", {"start": v(-33.5, 14.25) * mm, "end": v(-33.48, 14.22) * mm});
            skLineSegment(sketch, "E1452", {"start": v(-33.48, 14.22) * mm, "end": v(-33.45, 14.18) * mm});
            skLineSegment(sketch, "E1453", {"start": v(-33.45, 14.18) * mm, "end": v(-33.43, 14.13) * mm});
            skLineSegment(sketch, "E1454", {"start": v(-33.43, 14.13) * mm, "end": v(-33.4, 14.09) * mm});
            skLineSegment(sketch, "E1455", {"start": v(-33.4, 14.09) * mm, "end": v(-33.4, 14.06) * mm});
            skLineSegment(sketch, "E1456", {"start": v(-33.4, 14.06) * mm, "end": v(-33.38, 14.01) * mm});
            skLineSegment(sketch, "E1457", {"start": v(-33.38, 14.01) * mm, "end": v(-33.36, 13.96) * mm});
            skLineSegment(sketch, "E1458", {"start": v(-33.36, 13.96) * mm, "end": v(-33.35, 13.9) * mm});
            skLineSegment(sketch, "E1459", {"start": v(-33.35, 13.9) * mm, "end": v(-33.33, 13.84) * mm});
            skLineSegment(sketch, "E1460", {"start": v(-33.33, 13.84) * mm, "end": v(-33.32, 13.77) * mm});
            skLineSegment(sketch, "E1461", {"start": v(-33.32, 13.77) * mm, "end": v(-33.3, 13.7) * mm});
            skLineSegment(sketch, "E1462", {"start": v(-33.3, 13.7) * mm, "end": v(-33.3, 13.62) * mm});
            skLineSegment(sketch, "E1463", {"start": v(-33.3, 13.62) * mm, "end": v(-33.29, 13.54) * mm});
            skLineSegment(sketch, "E1464", {"start": v(-33.29, 13.54) * mm, "end": v(-33.28, 13.45) * mm});
            skLineSegment(sketch, "E1465", {"start": v(-33.28, 13.45) * mm, "end": v(-33.27, 13.36) * mm});
            skLineSegment(sketch, "E1466", {"start": v(-33.27, 13.36) * mm, "end": v(-33.26, 13.27) * mm});
            skLineSegment(sketch, "E1467", {"start": v(-33.26, 13.27) * mm, "end": v(-33.26, 13.17) * mm});
            skLineSegment(sketch, "E1468", {"start": v(-33.26, 13.17) * mm, "end": v(-33.25, 13.07) * mm});
            skLineSegment(sketch, "E1469", {"start": v(-33.25, 13.07) * mm, "end": v(-33.25, 12.85) * mm});
            skLineSegment(sketch, "E1470", {"start": v(-33.25, 12.85) * mm, "end": v(-33.25, 12.73) * mm});
            skLineSegment(sketch, "E1471", {"start": v(-33.25, 12.73) * mm, "end": v(-33.26, 12.36) * mm});
            skLineSegment(sketch, "E1472", {"start": v(-33.26, 12.36) * mm, "end": v(-33.29, 11.98) * mm});
            skLineSegment(sketch, "E1473", {"start": v(-33.29, 11.98) * mm, "end": v(-33.33, 11.58) * mm});
            skLineSegment(sketch, "E1474", {"start": v(-33.33, 11.58) * mm, "end": v(-33.4, 11.18) * mm});
            skLineSegment(sketch, "E1475", {"start": v(-33.4, 11.18) * mm, "end": v(-33.48, 10.77) * mm});
            skLineSegment(sketch, "E1476", {"start": v(-33.48, 10.77) * mm, "end": v(-33.58, 10.34) * mm});
            skLineSegment(sketch, "E1477", {"start": v(-33.58, 10.34) * mm, "end": v(-33.7, 9.9) * mm});
            skLineSegment(sketch, "E1478", {"start": v(-33.7, 9.9) * mm, "end": v(-33.85, 9.46) * mm});
            skLineSegment(sketch, "E1479", {"start": v(-33.85, 9.46) * mm, "end": v(-34.18, 8.54) * mm});
            skLineSegment(sketch, "E1480", {"start": v(-34.18, 8.54) * mm, "end": v(-34.6, 7.57) * mm});
            skLineSegment(sketch, "E1481", {"start": v(-34.6, 7.57) * mm, "end": v(-35.07, 6.57) * mm});
            skLineSegment(sketch, "E1482", {"start": v(-35.07, 6.57) * mm, "end": v(-35.63, 5.52) * mm});
            skLineSegment(sketch, "E1483", {"start": v(-35.63, 5.52) * mm, "end": v(-36.26, 4.45) * mm});
            skLineSegment(sketch, "E1484", {"start": v(-36.26, 4.45) * mm, "end": v(-36.94, 3.37) * mm});
            skLineSegment(sketch, "E1485", {"start": v(-36.94, 3.37) * mm, "end": v(-37.69, 2.3) * mm});
            skLineSegment(sketch, "E1486", {"start": v(-37.69, 2.3) * mm, "end": v(-39.35, 0.12) * mm});
            skLineSegment(sketch, "E1487", {"start": v(-39.35, 0.12) * mm, "end": v(-41.24, -2.09) * mm});
            skLineSegment(sketch, "E1488", {"start": v(-41.24, -2.09) * mm, "end": v(-42.28, -3.2) * mm});
            skLineSegment(sketch, "E1489", {"start": v(-42.28, -3.2) * mm, "end": v(-42.33, -3.46) * mm});
            skLineSegment(sketch, "E1490", {"start": v(-42.33, -3.46) * mm, "end": v(-42.37, -3.71) * mm});
            skLineSegment(sketch, "E1491", {"start": v(-42.37, -3.71) * mm, "end": v(-42.4, -3.95) * mm});
            skLineSegment(sketch, "E1492", {"start": v(-42.4, -3.95) * mm, "end": v(-42.44, -4.17) * mm});
            skLineSegment(sketch, "E1493", {"start": v(-42.44, -4.17) * mm, "end": v(-42.46, -4.37) * mm});
            skLineSegment(sketch, "E1494", {"start": v(-42.46, -4.37) * mm, "end": v(-42.47, -4.47) * mm});
            skLineSegment(sketch, "E1495", {"start": v(-42.47, -4.47) * mm, "end": v(-42.48, -4.56) * mm});
            skLineSegment(sketch, "E1496", {"start": v(-42.48, -4.56) * mm, "end": v(-42.48, -4.64) * mm});
            skLineSegment(sketch, "E1497", {"start": v(-42.48, -4.64) * mm, "end": v(-42.49, -4.73) * mm});
            skLineSegment(sketch, "E1498", {"start": v(-42.49, -4.73) * mm, "end": v(-42.49, -4.8) * mm});
            skLineSegment(sketch, "E1499", {"start": v(-42.49, -4.8) * mm, "end": v(-42.5, -4.88) * mm});
            skLineSegment(sketch, "E1500", {"start": v(-42.5, -4.88) * mm, "end": v(-42.48, -5.21) * mm});
            skLineSegment(sketch, "E1501", {"start": v(-42.48, -5.21) * mm, "end": v(-42.45, -5.53) * mm});
            skLineSegment(sketch, "E1502", {"start": v(-42.45, -5.53) * mm, "end": v(-42.41, -5.83) * mm});
            skLineSegment(sketch, "E1503", {"start": v(-42.41, -5.83) * mm, "end": v(-42.35, -6.1) * mm});
            skLineSegment(sketch, "E1504", {"start": v(-42.35, -6.1) * mm, "end": v(-42.27, -6.37) * mm});
            skLineSegment(sketch, "E1505", {"start": v(-42.27, -6.37) * mm, "end": v(-42.22, -6.5) * mm});
            skLineSegment(sketch, "E1506", {"start": v(-42.22, -6.5) * mm, "end": v(-42.17, -6.62) * mm});
            skLineSegment(sketch, "E1507", {"start": v(-42.17, -6.62) * mm, "end": v(-42.11, -6.74) * mm});
            skLineSegment(sketch, "E1508", {"start": v(-42.11, -6.74) * mm, "end": v(-42.05, -6.86) * mm});
            skLineSegment(sketch, "E1509", {"start": v(-42.05, -6.86) * mm, "end": v(-41.99, -6.97) * mm});
            skLineSegment(sketch, "E1510", {"start": v(-41.99, -6.97) * mm, "end": v(-41.92, -7.08) * mm});
            skLineSegment(sketch, "E1511", {"start": v(-41.92, -7.08) * mm, "end": v(-41.84, -7.18) * mm});
            skLineSegment(sketch, "E1512", {"start": v(-41.84, -7.18) * mm, "end": v(-41.77, -7.28) * mm});
            skLineSegment(sketch, "E1513", {"start": v(-41.77, -7.28) * mm, "end": v(-41.68, -7.36) * mm});
            skLineSegment(sketch, "E1514", {"start": v(-41.68, -7.36) * mm, "end": v(-41.6, -7.45) * mm});
            skLineSegment(sketch, "E1515", {"start": v(-41.6, -7.45) * mm, "end": v(-41.5, -7.52) * mm});
            skLineSegment(sketch, "E1516", {"start": v(-41.5, -7.52) * mm, "end": v(-41.42, -7.6) * mm});
            skLineSegment(sketch, "E1517", {"start": v(-41.42, -7.6) * mm, "end": v(-41.32, -7.65) * mm});
            skLineSegment(sketch, "E1518", {"start": v(-41.32, -7.65) * mm, "end": v(-41.22, -7.71) * mm});
            skLineSegment(sketch, "E1519", {"start": v(-41.22, -7.71) * mm, "end": v(-41.12, -7.76) * mm});
            skLineSegment(sketch, "E1520", {"start": v(-41.12, -7.76) * mm, "end": v(-41, -7.8) * mm});
            skLineSegment(sketch, "E1521", {"start": v(-41, -7.8) * mm, "end": v(-40.9, -7.84) * mm});
            skLineSegment(sketch, "E1522", {"start": v(-40.9, -7.84) * mm, "end": v(-40.79, -7.87) * mm});
            skLineSegment(sketch, "E1523", {"start": v(-40.79, -7.87) * mm, "end": v(-40.67, -7.9) * mm});
            skLineSegment(sketch, "E1524", {"start": v(-40.67, -7.9) * mm, "end": v(-40.55, -7.9) * mm});
            skLineSegment(sketch, "E1525", {"start": v(-40.55, -7.9) * mm, "end": v(-40.42, -7.92) * mm});
            skLineSegment(sketch, "E1526", {"start": v(-40.42, -7.92) * mm, "end": v(-40.3, -7.92) * mm});
            skLineSegment(sketch, "E1527", {"start": v(-40.3, -7.92) * mm, "end": v(-40.23, -7.92) * mm});
            skLineSegment(sketch, "E1528", {"start": v(-40.23, -7.92) * mm, "end": v(-40.16, -7.92) * mm});
            skLineSegment(sketch, "E1529", {"start": v(-40.16, -7.92) * mm, "end": v(-40.1, -7.9) * mm});
            skLineSegment(sketch, "E1530", {"start": v(-40.1, -7.9) * mm, "end": v(-40.03, -7.9) * mm});
            skLineSegment(sketch, "E1531", {"start": v(-40.03, -7.9) * mm, "end": v(-39.96, -7.88) * mm});
            skLineSegment(sketch, "E1532", {"start": v(-39.96, -7.88) * mm, "end": v(-39.89, -7.87) * mm});
            skLineSegment(sketch, "E1533", {"start": v(-39.89, -7.87) * mm, "end": v(-39.75, -7.82) * mm});
            skLineSegment(sketch, "E1534", {"start": v(-39.75, -7.82) * mm, "end": v(-39.6, -7.77) * mm});
            skLineSegment(sketch, "E1535", {"start": v(-39.6, -7.77) * mm, "end": v(-39.46, -7.7) * mm});
            skLineSegment(sketch, "E1536", {"start": v(-39.46, -7.7) * mm, "end": v(-39.3, -7.62) * mm});
            skLineSegment(sketch, "E1537", {"start": v(-39.3, -7.62) * mm, "end": v(-39.16, -7.52) * mm});
            skLineSegment(sketch, "E1538", {"start": v(-39.16, -7.52) * mm, "end": v(-38.85, -7.3) * mm});
            skLineSegment(sketch, "E1539", {"start": v(-38.85, -7.3) * mm, "end": v(-38.53, -7.05) * mm});
            skLineSegment(sketch, "E1540", {"start": v(-38.53, -7.05) * mm, "end": v(-38.2, -6.78) * mm});
            skLineSegment(sketch, "E1541", {"start": v(-38.2, -6.78) * mm, "end": v(-37.87, -6.49) * mm});
            skLineSegment(sketch, "E1542", {"start": v(-37.87, -6.49) * mm, "end": v(-37.83, -6.45) * mm});
            skLineSegment(sketch, "E1543", {"start": v(-37.83, -6.45) * mm, "end": v(-37.78, -6.4) * mm});
            skLineSegment(sketch, "E1544", {"start": v(-37.78, -6.4) * mm, "end": v(-37.73, -6.36) * mm});
            skLineSegment(sketch, "E1545", {"start": v(-37.73, -6.36) * mm, "end": v(-37.68, -6.32) * mm});
            skLineSegment(sketch, "E1546", {"start": v(-37.68, -6.32) * mm, "end": v(-37.63, -6.27) * mm});
            skLineSegment(sketch, "E1547", {"start": v(-37.63, -6.27) * mm, "end": v(-37.57, -6.22) * mm});
            skLineSegment(sketch, "E1548", {"start": v(-37.57, -6.22) * mm, "end": v(-37.45, -6.1) * mm});
            skLineSegment(sketch, "E1549", {"start": v(-37.45, -6.1) * mm, "end": v(-37.32, -5.99) * mm});
            skLineSegment(sketch, "E1550", {"start": v(-37.32, -5.99) * mm, "end": v(-37.18, -5.86) * mm});
            skLineSegment(sketch, "E1551", {"start": v(-37.18, -5.86) * mm, "end": v(-37.03, -5.72) * mm});
            skLineSegment(sketch, "E1552", {"start": v(-37.03, -5.72) * mm, "end": v(-36.87, -5.57) * mm});
            skLineSegment(sketch, "E1553", {"start": v(-36.87, -5.57) * mm, "end": v(-36.7, -5.42) * mm});
            skLineSegment(sketch, "E1554", {"start": v(-36.7, -5.42) * mm, "end": v(-36.52, -5.25) * mm});
            skLineSegment(sketch, "E1555", {"start": v(-36.52, -5.25) * mm, "end": v(-36.33, -5.08) * mm});
            skLineSegment(sketch, "E1556", {"start": v(-36.33, -5.08) * mm, "end": v(-36.13, -4.9) * mm});
            skLineSegment(sketch, "E1557", {"start": v(-36.13, -4.9) * mm, "end": v(-35.92, -4.7) * mm});
            skLineSegment(sketch, "E1558", {"start": v(-35.92, -4.7) * mm, "end": v(-35.7, -4.5) * mm});
            skLineSegment(sketch, "E1559", {"start": v(-35.7, -4.5) * mm, "end": v(-35.23, -4.06) * mm});
            skLineSegment(sketch, "E1560", {"start": v(-41.54, -0.26) * mm, "end": v(-41, 0.3) * mm});
            skLineSegment(sketch, "E1561", {"start": v(-41, 0.3) * mm, "end": v(-40.46, 0.89) * mm});
            skLineSegment(sketch, "E1562", {"start": v(-40.46, 0.89) * mm, "end": v(-39.94, 1.52) * mm});
            skLineSegment(sketch, "E1563", {"start": v(-39.94, 1.52) * mm, "end": v(-39.43, 2.18) * mm});
            skLineSegment(sketch, "E1564", {"start": v(-39.43, 2.18) * mm, "end": v(-38.92, 2.88) * mm});
            skLineSegment(sketch, "E1565", {"start": v(-38.92, 2.88) * mm, "end": v(-37.95, 4.35) * mm});
            skLineSegment(sketch, "E1566", {"start": v(-37.95, 4.35) * mm, "end": v(-37.5, 5.12) * mm});
            skLineSegment(sketch, "E1567", {"start": v(-37.5, 5.12) * mm, "end": v(-37.06, 5.88) * mm});
            skLineSegment(sketch, "E1568", {"start": v(-37.06, 5.88) * mm, "end": v(-36.68, 6.6) * mm});
            skLineSegment(sketch, "E1569", {"start": v(-36.68, 6.6) * mm, "end": v(-36.35, 7.28) * mm});
            skLineSegment(sketch, "E1570", {"start": v(-36.35, 7.28) * mm, "end": v(-36.2, 7.6) * mm});
            skLineSegment(sketch, "E1571", {"start": v(-36.2, 7.6) * mm, "end": v(-36.08, 7.92) * mm});
            skLineSegment(sketch, "E1572", {"start": v(-36.08, 7.92) * mm, "end": v(-35.95, 8.22) * mm});
            skLineSegment(sketch, "E1573", {"start": v(-35.95, 8.22) * mm, "end": v(-35.85, 8.5) * mm});
            skLineSegment(sketch, "E1574", {"start": v(-35.85, 8.5) * mm, "end": v(-35.8, 8.64) * mm});
            skLineSegment(sketch, "E1575", {"start": v(-35.8, 8.64) * mm, "end": v(-35.76, 8.77) * mm});
            skLineSegment(sketch, "E1576", {"start": v(-35.76, 8.77) * mm, "end": v(-35.72, 8.9) * mm});
            skLineSegment(sketch, "E1577", {"start": v(-35.72, 8.9) * mm, "end": v(-35.68, 9.01) * mm});
            skLineSegment(sketch, "E1578", {"start": v(-35.68, 9.01) * mm, "end": v(-35.65, 9.13) * mm});
            skLineSegment(sketch, "E1579", {"start": v(-35.65, 9.13) * mm, "end": v(-35.62, 9.24) * mm});
            skLineSegment(sketch, "E1580", {"start": v(-35.62, 9.24) * mm, "end": v(-35.6, 9.34) * mm});
            skLineSegment(sketch, "E1581", {"start": v(-35.6, 9.34) * mm, "end": v(-35.58, 9.44) * mm});
            skLineSegment(sketch, "E1582", {"start": v(-35.58, 9.44) * mm, "end": v(-35.57, 9.54) * mm});
            skLineSegment(sketch, "E1583", {"start": v(-35.57, 9.54) * mm, "end": v(-35.56, 9.63) * mm});
            skLineSegment(sketch, "E1584", {"start": v(-35.56, 9.63) * mm, "end": v(-35.55, 9.72) * mm});
            skLineSegment(sketch, "E1585", {"start": v(-35.55, 9.72) * mm, "end": v(-35.55, 9.8) * mm});
            skLineSegment(sketch, "E1586", {"start": v(-35.55, 9.8) * mm, "end": v(-35.55, 9.86) * mm});
            skLineSegment(sketch, "E1587", {"start": v(-35.55, 9.86) * mm, "end": v(-35.55, 9.91) * mm});
            skLineSegment(sketch, "E1588", {"start": v(-35.55, 9.91) * mm, "end": v(-35.56, 9.94) * mm});
            skLineSegment(sketch, "E1589", {"start": v(-35.56, 9.94) * mm, "end": v(-35.56, 9.96) * mm});
            skLineSegment(sketch, "E1590", {"start": v(-35.56, 9.96) * mm, "end": v(-35.57, 9.99) * mm});
            skLineSegment(sketch, "E1591", {"start": v(-35.57, 9.99) * mm, "end": v(-35.57, 10.01) * mm});
            skLineSegment(sketch, "E1592", {"start": v(-35.57, 10.01) * mm, "end": v(-35.58, 10.03) * mm});
            skLineSegment(sketch, "E1593", {"start": v(-35.58, 10.03) * mm, "end": v(-35.58, 10.06) * mm});
            skLineSegment(sketch, "E1594", {"start": v(-35.58, 10.06) * mm, "end": v(-35.59, 10.08) * mm});
            skLineSegment(sketch, "E1595", {"start": v(-35.59, 10.08) * mm, "end": v(-35.6, 10.1) * mm});
            skLineSegment(sketch, "E1596", {"start": v(-35.6, 10.1) * mm, "end": v(-35.6, 10.11) * mm});
            skLineSegment(sketch, "E1597", {"start": v(-35.6, 10.11) * mm, "end": v(-35.61, 10.13) * mm});
            skLineSegment(sketch, "E1598", {"start": v(-35.61, 10.13) * mm, "end": v(-35.62, 10.15) * mm});
            skLineSegment(sketch, "E1599", {"start": v(-35.62, 10.15) * mm, "end": v(-35.63, 10.16) * mm});
            skLineSegment(sketch, "E1600", {"start": v(-35.63, 10.16) * mm, "end": v(-35.64, 10.18) * mm});
            skLineSegment(sketch, "E1601", {"start": v(-35.64, 10.18) * mm, "end": v(-35.66, 10.2) * mm});
            skLineSegment(sketch, "E1602", {"start": v(-35.66, 10.2) * mm, "end": v(-35.67, 10.2) * mm});
            skLineSegment(sketch, "E1603", {"start": v(-35.67, 10.2) * mm, "end": v(-35.68, 10.22) * mm});
            skLineSegment(sketch, "E1604", {"start": v(-35.68, 10.22) * mm, "end": v(-35.7, 10.23) * mm});
            skLineSegment(sketch, "E1605", {"start": v(-35.7, 10.23) * mm, "end": v(-35.7, 10.24) * mm});
            skLineSegment(sketch, "E1606", {"start": v(-35.7, 10.24) * mm, "end": v(-35.72, 10.25) * mm});
            skLineSegment(sketch, "E1607", {"start": v(-35.72, 10.25) * mm, "end": v(-35.74, 10.25) * mm});
            skLineSegment(sketch, "E1608", {"start": v(-35.74, 10.25) * mm, "end": v(-35.76, 10.26) * mm});
            skLineSegment(sketch, "E1609", {"start": v(-35.76, 10.26) * mm, "end": v(-35.77, 10.27) * mm});
            skLineSegment(sketch, "E1610", {"start": v(-35.77, 10.27) * mm, "end": v(-35.79, 10.27) * mm});
            skLineSegment(sketch, "E1611", {"start": v(-35.79, 10.27) * mm, "end": v(-35.8, 10.28) * mm});
            skLineSegment(sketch, "E1612", {"start": v(-35.8, 10.28) * mm, "end": v(-35.83, 10.28) * mm});
            skLineSegment(sketch, "E1613", {"start": v(-35.83, 10.28) * mm, "end": v(-35.85, 10.28) * mm});
            skLineSegment(sketch, "E1614", {"start": v(-35.85, 10.28) * mm, "end": v(-35.87, 10.28) * mm});
            skLineSegment(sketch, "E1615", {"start": v(-35.87, 10.28) * mm, "end": v(-35.89, 10.28) * mm});
            skLineSegment(sketch, "E1616", {"start": v(-35.89, 10.28) * mm, "end": v(-35.9, 10.28) * mm});
            skLineSegment(sketch, "E1617", {"start": v(-35.9, 10.28) * mm, "end": v(-35.9, 10.28) * mm});
            skLineSegment(sketch, "E1618", {"start": v(-35.9, 10.28) * mm, "end": v(-35.91, 10.28) * mm});
            skLineSegment(sketch, "E1619", {"start": v(-35.91, 10.28) * mm, "end": v(-35.92, 10.28) * mm});
            skLineSegment(sketch, "E1620", {"start": v(-35.92, 10.28) * mm, "end": v(-35.93, 10.28) * mm});
            skLineSegment(sketch, "E1621", {"start": v(-35.93, 10.28) * mm, "end": v(-35.94, 10.28) * mm});
            skLineSegment(sketch, "E1622", {"start": v(-35.94, 10.28) * mm, "end": v(-35.95, 10.27) * mm});
            skLineSegment(sketch, "E1623", {"start": v(-35.95, 10.27) * mm, "end": v(-35.96, 10.27) * mm});
            skLineSegment(sketch, "E1624", {"start": v(-35.96, 10.27) * mm, "end": v(-35.98, 10.27) * mm});
            skLineSegment(sketch, "E1625", {"start": v(-35.98, 10.27) * mm, "end": v(-35.99, 10.26) * mm});
            skLineSegment(sketch, "E1626", {"start": v(-35.99, 10.26) * mm, "end": v(-36, 10.26) * mm});
            skLineSegment(sketch, "E1627", {"start": v(-36, 10.26) * mm, "end": v(-36.01, 10.25) * mm});
            skLineSegment(sketch, "E1628", {"start": v(-36.01, 10.25) * mm, "end": v(-36.04, 10.24) * mm});
            skLineSegment(sketch, "E1629", {"start": v(-36.04, 10.24) * mm, "end": v(-36.07, 10.23) * mm});
            skLineSegment(sketch, "E1630", {"start": v(-36.07, 10.23) * mm, "end": v(-36.1, 10.21) * mm});
            skLineSegment(sketch, "E1631", {"start": v(-36.1, 10.21) * mm, "end": v(-36.14, 10.2) * mm});
            skLineSegment(sketch, "E1632", {"start": v(-36.14, 10.2) * mm, "end": v(-36.17, 10.18) * mm});
            skLineSegment(sketch, "E1633", {"start": v(-36.17, 10.18) * mm, "end": v(-36.2, 10.15) * mm});
            skLineSegment(sketch, "E1634", {"start": v(-36.2, 10.15) * mm, "end": v(-36.25, 10.13) * mm});
            skLineSegment(sketch, "E1635", {"start": v(-36.25, 10.13) * mm, "end": v(-36.29, 10.1) * mm});
            skLineSegment(sketch, "E1636", {"start": v(-36.29, 10.1) * mm, "end": v(-36.33, 10.08) * mm});
            skLineSegment(sketch, "E1637", {"start": v(-36.33, 10.08) * mm, "end": v(-36.37, 10.05) * mm});
            skLineSegment(sketch, "E1638", {"start": v(-36.37, 10.05) * mm, "end": v(-36.53, 9.91) * mm});
            skLineSegment(sketch, "E1639", {"start": v(-36.53, 9.91) * mm, "end": v(-36.7, 9.76) * mm});
            skLineSegment(sketch, "E1640", {"start": v(-36.7, 9.76) * mm, "end": v(-36.87, 9.59) * mm});
            skLineSegment(sketch, "E1641", {"start": v(-36.87, 9.59) * mm, "end": v(-37.04, 9.4) * mm});
            skLineSegment(sketch, "E1642", {"start": v(-37.04, 9.4) * mm, "end": v(-37.2, 9.2) * mm});
            skLineSegment(sketch, "E1643", {"start": v(-37.2, 9.2) * mm, "end": v(-37.38, 8.98) * mm});
            skLineSegment(sketch, "E1644", {"start": v(-37.38, 8.98) * mm, "end": v(-37.56, 8.74) * mm});
            skLineSegment(sketch, "E1645", {"start": v(-37.56, 8.74) * mm, "end": v(-37.74, 8.5) * mm});
            skLineSegment(sketch, "E1646", {"start": v(-37.74, 8.5) * mm, "end": v(-37.92, 8.23) * mm});
            skLineSegment(sketch, "E1647", {"start": v(-37.92, 8.23) * mm, "end": v(-38.1, 7.94) * mm});
            skLineSegment(sketch, "E1648", {"start": v(-38.1, 7.94) * mm, "end": v(-38.3, 7.65) * mm});
            skLineSegment(sketch, "E1649", {"start": v(-38.3, 7.65) * mm, "end": v(-38.67, 7) * mm});
            skLineSegment(sketch, "E1650", {"start": v(-38.67, 7) * mm, "end": v(-39.06, 6.3) * mm});
            skLineSegment(sketch, "E1651", {"start": v(-39.06, 6.3) * mm, "end": v(-39.26, 5.92) * mm});
            skLineSegment(sketch, "E1652", {"start": v(-39.26, 5.92) * mm, "end": v(-40, 4.38) * mm});
            skLineSegment(sketch, "E1653", {"start": v(-40, 4.38) * mm, "end": v(-40.63, 2.84) * mm});
            skLineSegment(sketch, "E1654", {"start": v(-40.63, 2.84) * mm, "end": v(-41.15, 1.3) * mm});
            skLineSegment(sketch, "E1655", {"start": v(-41.15, 1.3) * mm, "end": v(-41.54, -0.26) * mm});
            skLineSegment(sketch, "E1656", {"start": v(-29.11, -5.05) * mm, "end": v(-29.11, -5.58) * mm});
            skLineSegment(sketch, "E1657", {"start": v(-29.11, -5.58) * mm, "end": v(-29.1, -5.88) * mm});
            skLineSegment(sketch, "E1658", {"start": v(-29.1, -5.88) * mm, "end": v(-29.09, -6.03) * mm});
            skLineSegment(sketch, "E1659", {"start": v(-29.09, -6.03) * mm, "end": v(-29.07, -6.17) * mm});
            skLineSegment(sketch, "E1660", {"start": v(-29.07, -6.17) * mm, "end": v(-29.05, -6.3) * mm});
            skLineSegment(sketch, "E1661", {"start": v(-29.05, -6.3) * mm, "end": v(-29.02, -6.44) * mm});
            skLineSegment(sketch, "E1662", {"start": v(-29.02, -6.44) * mm, "end": v(-29, -6.56) * mm});
            skLineSegment(sketch, "E1663", {"start": v(-29, -6.56) * mm, "end": v(-28.96, -6.69) * mm});
            skLineSegment(sketch, "E1664", {"start": v(-28.96, -6.69) * mm, "end": v(-28.92, -6.8) * mm});
            skLineSegment(sketch, "E1665", {"start": v(-28.92, -6.8) * mm, "end": v(-28.87, -6.92) * mm});
            skLineSegment(sketch, "E1666", {"start": v(-28.87, -6.92) * mm, "end": v(-28.82, -7.03) * mm});
            skLineSegment(sketch, "E1667", {"start": v(-28.82, -7.03) * mm, "end": v(-28.77, -7.14) * mm});
            skLineSegment(sketch, "E1668", {"start": v(-28.77, -7.14) * mm, "end": v(-28.7, -7.24) * mm});
            skLineSegment(sketch, "E1669", {"start": v(-28.7, -7.24) * mm, "end": v(-28.64, -7.34) * mm});
            skLineSegment(sketch, "E1670", {"start": v(-28.64, -7.34) * mm, "end": v(-28.57, -7.43) * mm});
            skLineSegment(sketch, "E1671", {"start": v(-28.57, -7.43) * mm, "end": v(-28.5, -7.52) * mm});
            skLineSegment(sketch, "E1672", {"start": v(-28.5, -7.52) * mm, "end": v(-28.42, -7.6) * mm});
            skLineSegment(sketch, "E1673", {"start": v(-28.42, -7.6) * mm, "end": v(-28.34, -7.68) * mm});
            skLineSegment(sketch, "E1674", {"start": v(-28.34, -7.68) * mm, "end": v(-28.26, -7.76) * mm});
            skLineSegment(sketch, "E1675", {"start": v(-28.26, -7.76) * mm, "end": v(-28.17, -7.83) * mm});
            skLineSegment(sketch, "E1676", {"start": v(-28.17, -7.83) * mm, "end": v(-28.08, -7.89) * mm});
            skLineSegment(sketch, "E1677", {"start": v(-28.08, -7.89) * mm, "end": v(-27.99, -7.95) * mm});
            skLineSegment(sketch, "E1678", {"start": v(-27.99, -7.95) * mm, "end": v(-27.9, -8) * mm});
            skLineSegment(sketch, "E1679", {"start": v(-27.9, -8) * mm, "end": v(-27.8, -8.04) * mm});
            skLineSegment(sketch, "E1680", {"start": v(-27.8, -8.04) * mm, "end": v(-27.7, -8.08) * mm});
            skLineSegment(sketch, "E1681", {"start": v(-27.7, -8.08) * mm, "end": v(-27.59, -8.12) * mm});
            skLineSegment(sketch, "E1682", {"start": v(-27.59, -8.12) * mm, "end": v(-27.48, -8.15) * mm});
            skLineSegment(sketch, "E1683", {"start": v(-27.48, -8.15) * mm, "end": v(-27.37, -8.17) * mm});
            skLineSegment(sketch, "E1684", {"start": v(-27.37, -8.17) * mm, "end": v(-27.25, -8.2) * mm});
            skLineSegment(sketch, "E1685", {"start": v(-27.25, -8.2) * mm, "end": v(-27.14, -8.2) * mm});
            skLineSegment(sketch, "E1686", {"start": v(-27.14, -8.2) * mm, "end": v(-27.02, -8.21) * mm});
            skLineSegment(sketch, "E1687", {"start": v(-27.02, -8.21) * mm, "end": v(-26.9, -8.22) * mm});
            skLineSegment(sketch, "E1688", {"start": v(-26.9, -8.22) * mm, "end": v(-26.64, -8.2) * mm});
            skLineSegment(sketch, "E1689", {"start": v(-26.64, -8.2) * mm, "end": v(-26.37, -8.19) * mm});
            skLineSegment(sketch, "E1690", {"start": v(-26.37, -8.19) * mm, "end": v(-26.11, -8.15) * mm});
            skLineSegment(sketch, "E1691", {"start": v(-26.11, -8.15) * mm, "end": v(-25.85, -8.1) * mm});
            skLineSegment(sketch, "E1692", {"start": v(-25.85, -8.1) * mm, "end": v(-25.58, -8.03) * mm});
            skLineSegment(sketch, "E1693", {"start": v(-25.58, -8.03) * mm, "end": v(-25.3, -7.94) * mm});
            skLineSegment(sketch, "E1694", {"start": v(-25.3, -7.94) * mm, "end": v(-25.04, -7.85) * mm});
            skLineSegment(sketch, "E1695", {"start": v(-25.04, -7.85) * mm, "end": v(-24.76, -7.73) * mm});
            skLineSegment(sketch, "E1696", {"start": v(-24.76, -7.73) * mm, "end": v(-24.2, -7.47) * mm});
            skLineSegment(sketch, "E1697", {"start": v(-24.2, -7.47) * mm, "end": v(-23.65, -7.17) * mm});
            skLineSegment(sketch, "E1698", {"start": v(-23.65, -7.17) * mm, "end": v(-23.1, -6.83) * mm});
            skLineSegment(sketch, "E1699", {"start": v(-23.1, -6.83) * mm, "end": v(-22.55, -6.45) * mm});
            skLineSegment(sketch, "E1700", {"start": v(-22.55, -6.45) * mm, "end": v(-22.27, -6.24) * mm});
            skLineSegment(sketch, "E1701", {"start": v(-22.27, -6.24) * mm, "end": v(-21.97, -6.01) * mm});
            skLineSegment(sketch, "E1702", {"start": v(-21.97, -6.01) * mm, "end": v(-21.66, -5.77) * mm});
            skLineSegment(sketch, "E1703", {"start": v(-21.66, -5.77) * mm, "end": v(-21.33, -5.5) * mm});
            skLineSegment(sketch, "E1704", {"start": v(-21.33, -5.5) * mm, "end": v(-20.99, -5.23) * mm});
            skLineSegment(sketch, "E1705", {"start": v(-20.99, -5.23) * mm, "end": v(-20.63, -4.93) * mm});
            skLineSegment(sketch, "E1706", {"start": v(-20.63, -4.93) * mm, "end": v(-20.26, -4.62) * mm});
            skLineSegment(sketch, "E1707", {"start": v(-20.26, -4.62) * mm, "end": v(-19.87, -4.3) * mm});
            skLineSegment(sketch, "E1708", {"start": v(-19.87, -4.3) * mm, "end": v(-19.87, -5.58) * mm});
            skLineSegment(sketch, "E1709", {"start": v(-19.87, -5.58) * mm, "end": v(-20.46, -6.28) * mm});
            skLineSegment(sketch, "E1710", {"start": v(-20.46, -6.28) * mm, "end": v(-21.04, -6.93) * mm});
            skLineSegment(sketch, "E1711", {"start": v(-21.04, -6.93) * mm, "end": v(-21.62, -7.55) * mm});
            skLineSegment(sketch, "E1712", {"start": v(-21.62, -7.55) * mm, "end": v(-22.18, -8.12) * mm});
            skLineSegment(sketch, "E1713", {"start": v(-22.18, -8.12) * mm, "end": v(-22.73, -8.65) * mm});
            skLineSegment(sketch, "E1714", {"start": v(-22.73, -8.65) * mm, "end": v(-23.28, -9.14) * mm});
            skLineSegment(sketch, "E1715", {"start": v(-23.28, -9.14) * mm, "end": v(-23.82, -9.58) * mm});
            skLineSegment(sketch, "E1716", {"start": v(-23.82, -9.58) * mm, "end": v(-24.34, -9.99) * mm});
            skLineSegment(sketch, "E1717", {"start": v(-24.34, -9.99) * mm, "end": v(-24.87, -10.35) * mm});
            skLineSegment(sketch, "E1718", {"start": v(-24.87, -10.35) * mm, "end": v(-25.4, -10.65) * mm});
            skLineSegment(sketch, "E1719", {"start": v(-25.4, -10.65) * mm, "end": v(-25.92, -10.92) * mm});
            skLineSegment(sketch, "E1720", {"start": v(-25.92, -10.92) * mm, "end": v(-26.45, -11.13) * mm});
            skLineSegment(sketch, "E1721", {"start": v(-26.45, -11.13) * mm, "end": v(-26.98, -11.3) * mm});
            skLineSegment(sketch, "E1722", {"start": v(-26.98, -11.3) * mm, "end": v(-27.51, -11.41) * mm});
            skLineSegment(sketch, "E1723", {"start": v(-27.51, -11.41) * mm, "end": v(-27.78, -11.46) * mm});
            skLineSegment(sketch, "E1724", {"start": v(-27.78, -11.46) * mm, "end": v(-28.05, -11.48) * mm});
            skLineSegment(sketch, "E1725", {"start": v(-28.05, -11.48) * mm, "end": v(-28.31, -11.5) * mm});
            skLineSegment(sketch, "E1726", {"start": v(-28.31, -11.5) * mm, "end": v(-28.58, -11.5) * mm});
            skLineSegment(sketch, "E1727", {"start": v(-28.58, -11.5) * mm, "end": v(-28.81, -11.5) * mm});
            skLineSegment(sketch, "E1728", {"start": v(-28.81, -11.5) * mm, "end": v(-29.04, -11.49) * mm});
            skLineSegment(sketch, "E1729", {"start": v(-29.04, -11.49) * mm, "end": v(-29.26, -11.46) * mm});
            skLineSegment(sketch, "E1730", {"start": v(-29.26, -11.46) * mm, "end": v(-29.47, -11.42) * mm});
            skLineSegment(sketch, "E1731", {"start": v(-29.47, -11.42) * mm, "end": v(-29.68, -11.37) * mm});
            skLineSegment(sketch, "E1732", {"start": v(-29.68, -11.37) * mm, "end": v(-29.88, -11.3) * mm});
            skLineSegment(sketch, "E1733", {"start": v(-29.88, -11.3) * mm, "end": v(-30.08, -11.23) * mm});
            skLineSegment(sketch, "E1734", {"start": v(-30.08, -11.23) * mm, "end": v(-30.27, -11.14) * mm});
            skLineSegment(sketch, "E1735", {"start": v(-30.27, -11.14) * mm, "end": v(-30.45, -11.05) * mm});
            skLineSegment(sketch, "E1736", {"start": v(-30.45, -11.05) * mm, "end": v(-30.63, -10.94) * mm});
            skLineSegment(sketch, "E1737", {"start": v(-30.63, -10.94) * mm, "end": v(-30.8, -10.82) * mm});
            skLineSegment(sketch, "E1738", {"start": v(-30.8, -10.82) * mm, "end": v(-30.96, -10.69) * mm});
            skLineSegment(sketch, "E1739", {"start": v(-30.96, -10.69) * mm, "end": v(-31.12, -10.55) * mm});
            skLineSegment(sketch, "E1740", {"start": v(-31.12, -10.55) * mm, "end": v(-31.27, -10.4) * mm});
            skLineSegment(sketch, "E1741", {"start": v(-31.27, -10.4) * mm, "end": v(-31.42, -10.23) * mm});
            skLineSegment(sketch, "E1742", {"start": v(-31.42, -10.23) * mm, "end": v(-31.56, -10.05) * mm});
            skLineSegment(sketch, "E1743", {"start": v(-31.56, -10.05) * mm, "end": v(-31.7, -9.87) * mm});
            skLineSegment(sketch, "E1744", {"start": v(-31.7, -9.87) * mm, "end": v(-31.82, -9.67) * mm});
            skLineSegment(sketch, "E1745", {"start": v(-31.82, -9.67) * mm, "end": v(-31.93, -9.47) * mm});
            skLineSegment(sketch, "E1746", {"start": v(-31.93, -9.47) * mm, "end": v(-32.04, -9.26) * mm});
            skLineSegment(sketch, "E1747", {"start": v(-32.04, -9.26) * mm, "end": v(-32.14, -9.04) * mm});
            skLineSegment(sketch, "E1748", {"start": v(-32.14, -9.04) * mm, "end": v(-32.23, -8.8) * mm});
            skLineSegment(sketch, "E1749", {"start": v(-32.23, -8.8) * mm, "end": v(-32.3, -8.57) * mm});
            skLineSegment(sketch, "E1750", {"start": v(-32.3, -8.57) * mm, "end": v(-32.38, -8.33) * mm});
            skLineSegment(sketch, "E1751", {"start": v(-32.38, -8.33) * mm, "end": v(-32.44, -8.07) * mm});
            skLineSegment(sketch, "E1752", {"start": v(-32.44, -8.07) * mm, "end": v(-32.5, -7.81) * mm});
            skLineSegment(sketch, "E1753", {"start": v(-32.5, -7.81) * mm, "end": v(-32.59, -7.26) * mm});
            skLineSegment(sketch, "E1754", {"start": v(-32.59, -7.26) * mm, "end": v(-32.64, -6.68) * mm});
            skLineSegment(sketch, "E1755", {"start": v(-32.64, -6.68) * mm, "end": v(-32.65, -6.07) * mm});
            skLineSegment(sketch, "E1756", {"start": v(-32.65, -6.07) * mm, "end": v(-32.64, -5.52) * mm});
            skLineSegment(sketch, "E1757", {"start": v(-32.64, -5.52) * mm, "end": v(-32.6, -4.98) * mm});
            skLineSegment(sketch, "E1758", {"start": v(-32.6, -4.98) * mm, "end": v(-32.5, -4.46) * mm});
            skLineSegment(sketch, "E1759", {"start": v(-32.5, -4.46) * mm, "end": v(-32.4, -3.96) * mm});
            skLineSegment(sketch, "E1760", {"start": v(-32.4, -3.96) * mm, "end": v(-32.25, -3.46) * mm});
            skLineSegment(sketch, "E1761", {"start": v(-32.25, -3.46) * mm, "end": v(-32.07, -2.98) * mm});
            skLineSegment(sketch, "E1762", {"start": v(-32.07, -2.98) * mm, "end": v(-31.86, -2.51) * mm});
            skLineSegment(sketch, "E1763", {"start": v(-31.86, -2.51) * mm, "end": v(-31.62, -2.06) * mm});
            skLineSegment(sketch, "E1764", {"start": v(-31.62, -2.06) * mm, "end": v(-31.34, -1.6) * mm});
            skLineSegment(sketch, "E1765", {"start": v(-31.34, -1.6) * mm, "end": v(-31.02, -1.14) * mm});
            skLineSegment(sketch, "E1766", {"start": v(-31.02, -1.14) * mm, "end": v(-30.66, -0.67) * mm});
            skLineSegment(sketch, "E1767", {"start": v(-30.66, -0.67) * mm, "end": v(-30.26, -0.2) * mm});
            skLineSegment(sketch, "E1768", {"start": v(-30.26, -0.2) * mm, "end": v(-29.82, 0.29) * mm});
            skLineSegment(sketch, "E1769", {"start": v(-29.82, 0.29) * mm, "end": v(-29.33, 0.77) * mm});
            skLineSegment(sketch, "E1770", {"start": v(-29.33, 0.77) * mm, "end": v(-28.81, 1.26) * mm});
            skLineSegment(sketch, "E1771", {"start": v(-28.81, 1.26) * mm, "end": v(-28.25, 1.76) * mm});
            skLineSegment(sketch, "E1772", {"start": v(-28.25, 1.76) * mm, "end": v(-27.45, 2.4) * mm});
            skLineSegment(sketch, "E1773", {"start": v(-27.45, 2.4) * mm, "end": v(-26.65, 2.96) * mm});
            skLineSegment(sketch, "E1774", {"start": v(-26.65, 2.96) * mm, "end": v(-26.25, 3.21) * mm});
            skLineSegment(sketch, "E1775", {"start": v(-26.25, 3.21) * mm, "end": v(-25.85, 3.44) * mm});
            skLineSegment(sketch, "E1776", {"start": v(-25.85, 3.44) * mm, "end": v(-25.46, 3.64) * mm});
            skLineSegment(sketch, "E1777", {"start": v(-25.46, 3.64) * mm, "end": v(-25.06, 3.83) * mm});
            skLineSegment(sketch, "E1778", {"start": v(-25.06, 3.83) * mm, "end": v(-24.67, 4) * mm});
            skLineSegment(sketch, "E1779", {"start": v(-24.67, 4) * mm, "end": v(-24.29, 4.13) * mm});
            skLineSegment(sketch, "E1780", {"start": v(-24.29, 4.13) * mm, "end": v(-23.92, 4.25) * mm});
            skLineSegment(sketch, "E1781", {"start": v(-23.92, 4.25) * mm, "end": v(-23.56, 4.35) * mm});
            skLineSegment(sketch, "E1782", {"start": v(-23.56, 4.35) * mm, "end": v(-23.21, 4.43) * mm});
            skLineSegment(sketch, "E1783", {"start": v(-23.21, 4.43) * mm, "end": v(-22.88, 4.48) * mm});
            skLineSegment(sketch, "E1784", {"start": v(-22.88, 4.48) * mm, "end": v(-22.55, 4.51) * mm});
            skLineSegment(sketch, "E1785", {"start": v(-22.55, 4.51) * mm, "end": v(-22.23, 4.53) * mm});
            skLineSegment(sketch, "E1786", {"start": v(-22.23, 4.53) * mm, "end": v(-22, 4.52) * mm});
            skLineSegment(sketch, "E1787", {"start": v(-22, 4.52) * mm, "end": v(-21.76, 4.5) * mm});
            skLineSegment(sketch, "E1788", {"start": v(-21.76, 4.5) * mm, "end": v(-21.65, 4.48) * mm});
            skLineSegment(sketch, "E1789", {"start": v(-21.65, 4.48) * mm, "end": v(-21.55, 4.46) * mm});
            skLineSegment(sketch, "E1790", {"start": v(-21.55, 4.46) * mm, "end": v(-21.45, 4.44) * mm});
            skLineSegment(sketch, "E1791", {"start": v(-21.45, 4.44) * mm, "end": v(-21.35, 4.4) * mm});
            skLineSegment(sketch, "E1792", {"start": v(-21.35, 4.4) * mm, "end": v(-21.25, 4.38) * mm});
            skLineSegment(sketch, "E1793", {"start": v(-21.25, 4.38) * mm, "end": v(-21.16, 4.34) * mm});
            skLineSegment(sketch, "E1794", {"start": v(-21.16, 4.34) * mm, "end": v(-21.07, 4.3) * mm});
            skLineSegment(sketch, "E1795", {"start": v(-21.07, 4.3) * mm, "end": v(-20.98, 4.26) * mm});
            skLineSegment(sketch, "E1796", {"start": v(-20.98, 4.26) * mm, "end": v(-20.9, 4.22) * mm});
            skLineSegment(sketch, "E1797", {"start": v(-20.9, 4.22) * mm, "end": v(-20.82, 4.17) * mm});
            skLineSegment(sketch, "E1798", {"start": v(-20.82, 4.17) * mm, "end": v(-20.74, 4.12) * mm});
            skLineSegment(sketch, "E1799", {"start": v(-20.74, 4.12) * mm, "end": v(-20.67, 4.06) * mm});
            skLineSegment(sketch, "E1800", {"start": v(-20.67, 4.06) * mm, "end": v(-20.6, 4) * mm});
            skLineSegment(sketch, "E1801", {"start": v(-20.6, 4) * mm, "end": v(-20.53, 3.94) * mm});
            skLineSegment(sketch, "E1802", {"start": v(-20.53, 3.94) * mm, "end": v(-20.47, 3.88) * mm});
            skLineSegment(sketch, "E1803", {"start": v(-20.47, 3.88) * mm, "end": v(-20.41, 3.81) * mm});
            skLineSegment(sketch, "E1804", {"start": v(-20.41, 3.81) * mm, "end": v(-20.36, 3.74) * mm});
            skLineSegment(sketch, "E1805", {"start": v(-20.36, 3.74) * mm, "end": v(-20.31, 3.66) * mm});
            skLineSegment(sketch, "E1806", {"start": v(-20.31, 3.66) * mm, "end": v(-20.27, 3.58) * mm});
            skLineSegment(sketch, "E1807", {"start": v(-20.27, 3.58) * mm, "end": v(-20.23, 3.5) * mm});
            skLineSegment(sketch, "E1808", {"start": v(-20.23, 3.5) * mm, "end": v(-20.2, 3.42) * mm});
            skLineSegment(sketch, "E1809", {"start": v(-20.2, 3.42) * mm, "end": v(-20.16, 3.33) * mm});
            skLineSegment(sketch, "E1810", {"start": v(-20.16, 3.33) * mm, "end": v(-20.14, 3.23) * mm});
            skLineSegment(sketch, "E1811", {"start": v(-20.14, 3.23) * mm, "end": v(-20.12, 3.14) * mm});
            skLineSegment(sketch, "E1812", {"start": v(-20.12, 3.14) * mm, "end": v(-20.1, 3.03) * mm});
            skLineSegment(sketch, "E1813", {"start": v(-20.1, 3.03) * mm, "end": v(-20.1, 2.93) * mm});
            skLineSegment(sketch, "E1814", {"start": v(-20.1, 2.93) * mm, "end": v(-20.08, 2.82) * mm});
            skLineSegment(sketch, "E1815", {"start": v(-20.08, 2.82) * mm, "end": v(-20.08, 2.71) * mm});
            skLineSegment(sketch, "E1816", {"start": v(-20.08, 2.71) * mm, "end": v(-20.08, 2.54) * mm});
            skLineSegment(sketch, "E1817", {"start": v(-20.08, 2.54) * mm, "end": v(-20.1, 2.38) * mm});
            skLineSegment(sketch, "E1818", {"start": v(-20.1, 2.38) * mm, "end": v(-20.12, 2.21) * mm});
            skLineSegment(sketch, "E1819", {"start": v(-20.12, 2.21) * mm, "end": v(-20.14, 2.05) * mm});
            skLineSegment(sketch, "E1820", {"start": v(-20.14, 2.05) * mm, "end": v(-20.18, 1.88) * mm});
            skLineSegment(sketch, "E1821", {"start": v(-20.18, 1.88) * mm, "end": v(-20.22, 1.71) * mm});
            skLineSegment(sketch, "E1822", {"start": v(-20.22, 1.71) * mm, "end": v(-20.27, 1.55) * mm});
            skLineSegment(sketch, "E1823", {"start": v(-20.27, 1.55) * mm, "end": v(-20.33, 1.38) * mm});
            skLineSegment(sketch, "E1824", {"start": v(-20.33, 1.38) * mm, "end": v(-20.47, 1.05) * mm});
            skLineSegment(sketch, "E1825", {"start": v(-20.47, 1.05) * mm, "end": v(-20.64, 0.72) * mm});
            skLineSegment(sketch, "E1826", {"start": v(-20.64, 0.72) * mm, "end": v(-20.84, 0.38) * mm});
            skLineSegment(sketch, "E1827", {"start": v(-20.84, 0.38) * mm, "end": v(-21.07, 0.05) * mm});
            skLineSegment(sketch, "E1828", {"start": v(-21.07, 0.05) * mm, "end": v(-21.34, -0.27) * mm});
            skLineSegment(sketch, "E1829", {"start": v(-21.34, -0.27) * mm, "end": v(-21.63, -0.6) * mm});
            skLineSegment(sketch, "E1830", {"start": v(-21.63, -0.6) * mm, "end": v(-21.96, -0.93) * mm});
            skLineSegment(sketch, "E1831", {"start": v(-21.96, -0.93) * mm, "end": v(-22.33, -1.26) * mm});
            skLineSegment(sketch, "E1832", {"start": v(-22.33, -1.26) * mm, "end": v(-22.72, -1.58) * mm});
            skLineSegment(sketch, "E1833", {"start": v(-22.72, -1.58) * mm, "end": v(-23.15, -1.9) * mm});
            skLineSegment(sketch, "E1834", {"start": v(-23.15, -1.9) * mm, "end": v(-23.62, -2.24) * mm});
            skLineSegment(sketch, "E1835", {"start": v(-23.62, -2.24) * mm, "end": v(-24.11, -2.56) * mm});
            skLineSegment(sketch, "E1836", {"start": v(-24.11, -2.56) * mm, "end": v(-24.63, -2.88) * mm});
            skLineSegment(sketch, "E1837", {"start": v(-24.63, -2.88) * mm, "end": v(-25.18, -3.2) * mm});
            skLineSegment(sketch, "E1838", {"start": v(-25.18, -3.2) * mm, "end": v(-25.76, -3.52) * mm});
            skLineSegment(sketch, "E1839", {"start": v(-25.76, -3.52) * mm, "end": v(-27.01, -4.14) * mm});
            skLineSegment(sketch, "E1840", {"start": v(-27.01, -4.14) * mm, "end": v(-28.38, -4.75) * mm});
            skLineSegment(sketch, "E1841", {"start": v(-28.38, -4.75) * mm, "end": v(-29.11, -5.05) * mm});
            skLineSegment(sketch, "E1842", {"start": v(-28.9, -3.68) * mm, "end": v(-27.98, -3.29) * mm});
            skLineSegment(sketch, "E1843", {"start": v(-27.98, -3.29) * mm, "end": v(-27.14, -2.85) * mm});
            skLineSegment(sketch, "E1844", {"start": v(-27.14, -2.85) * mm, "end": v(-26.74, -2.62) * mm});
            skLineSegment(sketch, "E1845", {"start": v(-26.74, -2.62) * mm, "end": v(-26.36, -2.37) * mm});
            skLineSegment(sketch, "E1846", {"start": v(-26.36, -2.37) * mm, "end": v(-26, -2.11) * mm});
            skLineSegment(sketch, "E1847", {"start": v(-26, -2.11) * mm, "end": v(-25.65, -1.85) * mm});
            skLineSegment(sketch, "E1848", {"start": v(-25.65, -1.85) * mm, "end": v(-25.32, -1.57) * mm});
            skLineSegment(sketch, "E1849", {"start": v(-25.32, -1.57) * mm, "end": v(-25.02, -1.3) * mm});
            skLineSegment(sketch, "E1850", {"start": v(-25.02, -1.3) * mm, "end": v(-24.74, -1.04) * mm});
            skLineSegment(sketch, "E1851", {"start": v(-24.74, -1.04) * mm, "end": v(-24.48, -0.78) * mm});
            skLineSegment(sketch, "E1852", {"start": v(-24.48, -0.78) * mm, "end": v(-24.24, -0.52) * mm});
            skLineSegment(sketch, "E1853", {"start": v(-24.24, -0.52) * mm, "end": v(-24.03, -0.26) * mm});
            skLineSegment(sketch, "E1854", {"start": v(-24.03, -0.26) * mm, "end": v(-23.84, 0) * mm});
            skLineSegment(sketch, "E1855", {"start": v(-23.84, 0) * mm, "end": v(-23.67, 0.24) * mm});
            skLineSegment(sketch, "E1856", {"start": v(-23.67, 0.24) * mm, "end": v(-23.59, 0.37) * mm});
            skLineSegment(sketch, "E1857", {"start": v(-23.59, 0.37) * mm, "end": v(-23.51, 0.49) * mm});
            skLineSegment(sketch, "E1858", {"start": v(-23.51, 0.49) * mm, "end": v(-23.45, 0.6) * mm});
            skLineSegment(sketch, "E1859", {"start": v(-23.45, 0.6) * mm, "end": v(-23.38, 0.71) * mm});
            skLineSegment(sketch, "E1860", {"start": v(-23.38, 0.71) * mm, "end": v(-23.32, 0.82) * mm});
            skLineSegment(sketch, "E1861", {"start": v(-23.32, 0.82) * mm, "end": v(-23.27, 0.92) * mm});
            skLineSegment(sketch, "E1862", {"start": v(-23.27, 0.92) * mm, "end": v(-23.22, 1.02) * mm});
            skLineSegment(sketch, "E1863", {"start": v(-23.22, 1.02) * mm, "end": v(-23.18, 1.12) * mm});
            skLineSegment(sketch, "E1864", {"start": v(-23.18, 1.12) * mm, "end": v(-23.14, 1.2) * mm});
            skLineSegment(sketch, "E1865", {"start": v(-23.14, 1.2) * mm, "end": v(-23.1, 1.3) * mm});
            skLineSegment(sketch, "E1866", {"start": v(-23.1, 1.3) * mm, "end": v(-23.08, 1.38) * mm});
            skLineSegment(sketch, "E1867", {"start": v(-23.08, 1.38) * mm, "end": v(-23.05, 1.45) * mm});
            skLineSegment(sketch, "E1868", {"start": v(-23.05, 1.45) * mm, "end": v(-23.04, 1.5) * mm});
            skLineSegment(sketch, "E1869", {"start": v(-23.04, 1.5) * mm, "end": v(-23.04, 1.53) * mm});
            skLineSegment(sketch, "E1870", {"start": v(-23.04, 1.53) * mm, "end": v(-23.03, 1.56) * mm});
            skLineSegment(sketch, "E1871", {"start": v(-23.03, 1.56) * mm, "end": v(-23.02, 1.6) * mm});
            skLineSegment(sketch, "E1872", {"start": v(-23.02, 1.6) * mm, "end": v(-23.02, 1.63) * mm});
            skLineSegment(sketch, "E1873", {"start": v(-23.02, 1.63) * mm, "end": v(-23.02, 1.66) * mm});
            skLineSegment(sketch, "E1874", {"start": v(-23.02, 1.66) * mm, "end": v(-23.01, 1.69) * mm});
            skLineSegment(sketch, "E1875", {"start": v(-23.01, 1.69) * mm, "end": v(-23.01, 1.72) * mm});
            skLineSegment(sketch, "E1876", {"start": v(-23.01, 1.72) * mm, "end": v(-23.01, 1.75) * mm});
            skLineSegment(sketch, "E1877", {"start": v(-23.01, 1.75) * mm, "end": v(-23.02, 1.78) * mm});
            skLineSegment(sketch, "E1878", {"start": v(-23.02, 1.78) * mm, "end": v(-23.02, 1.8) * mm});
            skLineSegment(sketch, "E1879", {"start": v(-23.02, 1.8) * mm, "end": v(-23.02, 1.83) * mm});
            skLineSegment(sketch, "E1880", {"start": v(-23.02, 1.83) * mm, "end": v(-23.02, 1.86) * mm});
            skLineSegment(sketch, "E1881", {"start": v(-23.02, 1.86) * mm, "end": v(-23.03, 1.88) * mm});
            skLineSegment(sketch, "E1882", {"start": v(-23.03, 1.88) * mm, "end": v(-23.03, 1.9) * mm});
            skLineSegment(sketch, "E1883", {"start": v(-23.03, 1.9) * mm, "end": v(-23.04, 1.93) * mm});
            skLineSegment(sketch, "E1884", {"start": v(-23.04, 1.93) * mm, "end": v(-23.05, 1.95) * mm});
            skLineSegment(sketch, "E1885", {"start": v(-23.05, 1.95) * mm, "end": v(-23.06, 1.98) * mm});
            skLineSegment(sketch, "E1886", {"start": v(-23.06, 1.98) * mm, "end": v(-23.07, 2) * mm});
            skLineSegment(sketch, "E1887", {"start": v(-23.07, 2) * mm, "end": v(-23.08, 2.02) * mm});
            skLineSegment(sketch, "E1888", {"start": v(-23.08, 2.02) * mm, "end": v(-23.09, 2.03) * mm});
            skLineSegment(sketch, "E1889", {"start": v(-23.09, 2.03) * mm, "end": v(-23.1, 2.05) * mm});
            skLineSegment(sketch, "E1890", {"start": v(-23.1, 2.05) * mm, "end": v(-23.11, 2.07) * mm});
            skLineSegment(sketch, "E1891", {"start": v(-23.11, 2.07) * mm, "end": v(-23.12, 2.08) * mm});
            skLineSegment(sketch, "E1892", {"start": v(-23.12, 2.08) * mm, "end": v(-23.14, 2.1) * mm});
            skLineSegment(sketch, "E1893", {"start": v(-23.14, 2.1) * mm, "end": v(-23.15, 2.11) * mm});
            skLineSegment(sketch, "E1894", {"start": v(-23.15, 2.11) * mm, "end": v(-23.17, 2.12) * mm});
            skLineSegment(sketch, "E1895", {"start": v(-23.17, 2.12) * mm, "end": v(-23.19, 2.14) * mm});
            skLineSegment(sketch, "E1896", {"start": v(-23.19, 2.14) * mm, "end": v(-23.2, 2.15) * mm});
            skLineSegment(sketch, "E1897", {"start": v(-23.2, 2.15) * mm, "end": v(-23.22, 2.16) * mm});
            skLineSegment(sketch, "E1898", {"start": v(-23.22, 2.16) * mm, "end": v(-23.24, 2.17) * mm});
            skLineSegment(sketch, "E1899", {"start": v(-23.24, 2.17) * mm, "end": v(-23.26, 2.17) * mm});
            skLineSegment(sketch, "E1900", {"start": v(-23.26, 2.17) * mm, "end": v(-23.28, 2.18) * mm});
            skLineSegment(sketch, "E1901", {"start": v(-23.28, 2.18) * mm, "end": v(-23.3, 2.19) * mm});
            skLineSegment(sketch, "E1902", {"start": v(-23.3, 2.19) * mm, "end": v(-23.33, 2.2) * mm});
            skLineSegment(sketch, "E1903", {"start": v(-23.33, 2.2) * mm, "end": v(-23.35, 2.2) * mm});
            skLineSegment(sketch, "E1904", {"start": v(-23.35, 2.2) * mm, "end": v(-23.38, 2.2) * mm});
            skLineSegment(sketch, "E1905", {"start": v(-23.38, 2.2) * mm, "end": v(-23.4, 2.2) * mm});
            skLineSegment(sketch, "E1906", {"start": v(-23.4, 2.2) * mm, "end": v(-23.43, 2.2) * mm});
            skLineSegment(sketch, "E1907", {"start": v(-23.43, 2.2) * mm, "end": v(-23.46, 2.2) * mm});
            skLineSegment(sketch, "E1908", {"start": v(-23.46, 2.2) * mm, "end": v(-23.48, 2.2) * mm});
            skLineSegment(sketch, "E1909", {"start": v(-23.48, 2.2) * mm, "end": v(-23.5, 2.2) * mm});
            skLineSegment(sketch, "E1910", {"start": v(-23.5, 2.2) * mm, "end": v(-23.53, 2.2) * mm});
            skLineSegment(sketch, "E1911", {"start": v(-23.53, 2.2) * mm, "end": v(-23.56, 2.2) * mm});
            skLineSegment(sketch, "E1912", {"start": v(-23.56, 2.2) * mm, "end": v(-23.59, 2.2) * mm});
            skLineSegment(sketch, "E1913", {"start": v(-23.59, 2.2) * mm, "end": v(-23.62, 2.19) * mm});
            skLineSegment(sketch, "E1914", {"start": v(-23.62, 2.19) * mm, "end": v(-23.68, 2.17) * mm});
            skLineSegment(sketch, "E1915", {"start": v(-23.68, 2.17) * mm, "end": v(-23.74, 2.16) * mm});
            skLineSegment(sketch, "E1916", {"start": v(-23.74, 2.16) * mm, "end": v(-23.8, 2.14) * mm});
            skLineSegment(sketch, "E1917", {"start": v(-23.8, 2.14) * mm, "end": v(-23.88, 2.11) * mm});
            skLineSegment(sketch, "E1918", {"start": v(-23.88, 2.11) * mm, "end": v(-23.96, 2.08) * mm});
            skLineSegment(sketch, "E1919", {"start": v(-23.96, 2.08) * mm, "end": v(-24.04, 2.05) * mm});
            skLineSegment(sketch, "E1920", {"start": v(-24.04, 2.05) * mm, "end": v(-24.12, 2.02) * mm});
            skLineSegment(sketch, "E1921", {"start": v(-24.12, 2.02) * mm, "end": v(-24.2, 1.98) * mm});
            skLineSegment(sketch, "E1922", {"start": v(-24.2, 1.98) * mm, "end": v(-24.3, 1.93) * mm});
            skLineSegment(sketch, "E1923", {"start": v(-24.3, 1.93) * mm, "end": v(-24.4, 1.88) * mm});
            skLineSegment(sketch, "E1924", {"start": v(-24.4, 1.88) * mm, "end": v(-24.5, 1.83) * mm});
            skLineSegment(sketch, "E1925", {"start": v(-24.5, 1.83) * mm, "end": v(-24.6, 1.78) * mm});
            skLineSegment(sketch, "E1926", {"start": v(-24.6, 1.78) * mm, "end": v(-24.7, 1.72) * mm});
            skLineSegment(sketch, "E1927", {"start": v(-24.7, 1.72) * mm, "end": v(-25.13, 1.46) * mm});
            skLineSegment(sketch, "E1928", {"start": v(-25.13, 1.46) * mm, "end": v(-25.56, 1.16) * mm});
            skLineSegment(sketch, "E1929", {"start": v(-25.56, 1.16) * mm, "end": v(-26, 0.83) * mm});
            skLineSegment(sketch, "E1930", {"start": v(-26, 0.83) * mm, "end": v(-26.43, 0.45) * mm});
            skLineSegment(sketch, "E1931", {"start": v(-26.43, 0.45) * mm, "end": v(-26.85, 0.05) * mm});
            skLineSegment(sketch, "E1932", {"start": v(-26.85, 0.05) * mm, "end": v(-27.25, -0.4) * mm});
            skLineSegment(sketch, "E1933", {"start": v(-27.25, -0.4) * mm, "end": v(-27.63, -0.87) * mm});
            skLineSegment(sketch, "E1934", {"start": v(-27.63, -0.87) * mm, "end": v(-28, -1.38) * mm});
            skLineSegment(sketch, "E1935", {"start": v(-28, -1.38) * mm, "end": v(-28.16, -1.65) * mm});
            skLineSegment(sketch, "E1936", {"start": v(-28.16, -1.65) * mm, "end": v(-28.31, -1.92) * mm});
            skLineSegment(sketch, "E1937", {"start": v(-28.31, -1.92) * mm, "end": v(-28.45, -2.2) * mm});
            skLineSegment(sketch, "E1938", {"start": v(-28.45, -2.2) * mm, "end": v(-28.57, -2.48) * mm});
            skLineSegment(sketch, "E1939", {"start": v(-28.57, -2.48) * mm, "end": v(-28.67, -2.77) * mm});
            skLineSegment(sketch, "E1940", {"start": v(-28.67, -2.77) * mm, "end": v(-28.76, -3.07) * mm});
            skLineSegment(sketch, "E1941", {"start": v(-28.76, -3.07) * mm, "end": v(-28.84, -3.37) * mm});
            skLineSegment(sketch, "E1942", {"start": v(-28.84, -3.37) * mm, "end": v(-28.9, -3.68) * mm});
            skLineSegment(sketch, "E1943", {"start": v(-1.1, -10.77) * mm, "end": v(-1.47, -10.76) * mm});
            skLineSegment(sketch, "E1944", {"start": v(-1.47, -10.76) * mm, "end": v(-1.84, -10.71) * mm});
            skLineSegment(sketch, "E1945", {"start": v(-1.84, -10.71) * mm, "end": v(-2.2, -10.64) * mm});
            skLineSegment(sketch, "E1946", {"start": v(-2.2, -10.64) * mm, "end": v(-2.57, -10.54) * mm});
            skLineSegment(sketch, "E1947", {"start": v(-2.57, -10.54) * mm, "end": v(-2.93, -10.4) * mm});
            skLineSegment(sketch, "E1948", {"start": v(-2.93, -10.4) * mm, "end": v(-3.28, -10.25) * mm});
            skLineSegment(sketch, "E1949", {"start": v(-3.28, -10.25) * mm, "end": v(-3.64, -10.06) * mm});
            skLineSegment(sketch, "E1950", {"start": v(-3.64, -10.06) * mm, "end": v(-3.99, -9.84) * mm});
            skLineSegment(sketch, "E1951", {"start": v(-3.99, -9.84) * mm, "end": v(-4.32, -9.6) * mm});
            skLineSegment(sketch, "E1952", {"start": v(-4.32, -9.6) * mm, "end": v(-4.65, -9.33) * mm});
            skLineSegment(sketch, "E1953", {"start": v(-4.65, -9.33) * mm, "end": v(-4.95, -9.04) * mm});
            skLineSegment(sketch, "E1954", {"start": v(-4.95, -9.04) * mm, "end": v(-5.24, -8.73) * mm});
            skLineSegment(sketch, "E1955", {"start": v(-5.24, -8.73) * mm, "end": v(-5.51, -8.4) * mm});
            skLineSegment(sketch, "E1956", {"start": v(-5.51, -8.4) * mm, "end": v(-5.77, -8.05) * mm});
            skLineSegment(sketch, "E1957", {"start": v(-5.77, -8.05) * mm, "end": v(-6, -7.67) * mm});
            skLineSegment(sketch, "E1958", {"start": v(-6, -7.67) * mm, "end": v(-6.22, -7.27) * mm});
            skLineSegment(sketch, "E1959", {"start": v(-6.22, -7.27) * mm, "end": v(-6.42, -6.85) * mm});
            skLineSegment(sketch, "E1960", {"start": v(-6.42, -6.85) * mm, "end": v(-6.6, -6.42) * mm});
            skLineSegment(sketch, "E1961", {"start": v(-6.6, -6.42) * mm, "end": v(-6.74, -5.98) * mm});
            skLineSegment(sketch, "E1962", {"start": v(-6.74, -5.98) * mm, "end": v(-6.85, -5.53) * mm});
            skLineSegment(sketch, "E1963", {"start": v(-6.85, -5.53) * mm, "end": v(-6.95, -5.06) * mm});
            skLineSegment(sketch, "E1964", {"start": v(-6.95, -5.06) * mm, "end": v(-7.01, -4.59) * mm});
            skLineSegment(sketch, "E1965", {"start": v(-7.01, -4.59) * mm, "end": v(-7.05, -4.1) * mm});
            skLineSegment(sketch, "E1966", {"start": v(-7.05, -4.1) * mm, "end": v(-7.07, -3.6) * mm});
            skLineSegment(sketch, "E1967", {"start": v(-7.07, -3.6) * mm, "end": v(-7.06, -3.26) * mm});
            skLineSegment(sketch, "E1968", {"start": v(-7.06, -3.26) * mm, "end": v(-7.03, -2.93) * mm});
            skLineSegment(sketch, "E1969", {"start": v(-7.03, -2.93) * mm, "end": v(-7, -2.6) * mm});
            skLineSegment(sketch, "E1970", {"start": v(-7, -2.6) * mm, "end": v(-6.94, -2.28) * mm});
            skLineSegment(sketch, "E1971", {"start": v(-6.94, -2.28) * mm, "end": v(-6.87, -1.96) * mm});
            skLineSegment(sketch, "E1972", {"start": v(-6.87, -1.96) * mm, "end": v(-6.78, -1.64) * mm});
            skLineSegment(sketch, "E1973", {"start": v(-6.78, -1.64) * mm, "end": v(-6.67, -1.33) * mm});
            skLineSegment(sketch, "E1974", {"start": v(-6.67, -1.33) * mm, "end": v(-6.55, -1.02) * mm});
            skLineSegment(sketch, "E1975", {"start": v(-6.55, -1.02) * mm, "end": v(-6.42, -0.71) * mm});
            skLineSegment(sketch, "E1976", {"start": v(-6.42, -0.71) * mm, "end": v(-6.27, -0.41) * mm});
            skLineSegment(sketch, "E1977", {"start": v(-6.27, -0.41) * mm, "end": v(-6.1, -0.11) * mm});
            skLineSegment(sketch, "E1978", {"start": v(-6.1, -0.11) * mm, "end": v(-5.91, 0.18) * mm});
            skLineSegment(sketch, "E1979", {"start": v(-5.91, 0.18) * mm, "end": v(-5.71, 0.47) * mm});
            skLineSegment(sketch, "E1980", {"start": v(-5.71, 0.47) * mm, "end": v(-5.5, 0.76) * mm});
            skLineSegment(sketch, "E1981", {"start": v(-5.5, 0.76) * mm, "end": v(-5.27, 1.04) * mm});
            skLineSegment(sketch, "E1982", {"start": v(-5.27, 1.04) * mm, "end": v(-5.02, 1.32) * mm});
            skLineSegment(sketch, "E1983", {"start": v(-5.02, 1.32) * mm, "end": v(-4.47, 1.87) * mm});
            skLineSegment(sketch, "E1984", {"start": v(-4.47, 1.87) * mm, "end": v(-3.86, 2.42) * mm});
            skLineSegment(sketch, "E1985", {"start": v(-3.86, 2.42) * mm, "end": v(-3.2, 2.97) * mm});
            skLineSegment(sketch, "E1986", {"start": v(-3.2, 2.97) * mm, "end": v(-2.47, 3.52) * mm});
            skLineSegment(sketch, "E1987", {"start": v(-2.47, 3.52) * mm, "end": v(-1.68, 4.06) * mm});
            skLineSegment(sketch, "E1988", {"start": v(-1.68, 4.06) * mm, "end": v(-0.83, 4.6) * mm});
            skLineSegment(sketch, "E1989", {"start": v(-0.83, 4.6) * mm, "end": v(0.09, 5.15) * mm});
            skLineSegment(sketch, "E1990", {"start": v(0.09, 5.15) * mm, "end": v(1.06, 5.69) * mm});
            skLineSegment(sketch, "E1991", {"start": v(1.06, 5.69) * mm, "end": v(1, 6) * mm});
            skLineSegment(sketch, "E1992", {"start": v(1, 6) * mm, "end": v(0.96, 6.3) * mm});
            skLineSegment(sketch, "E1993", {"start": v(0.96, 6.3) * mm, "end": v(0.95, 6.44) * mm});
            skLineSegment(sketch, "E1994", {"start": v(0.95, 6.44) * mm, "end": v(0.93, 6.57) * mm});
            skLineSegment(sketch, "E1995", {"start": v(0.93, 6.57) * mm, "end": v(0.91, 6.7) * mm});
            skLineSegment(sketch, "E1996", {"start": v(0.91, 6.7) * mm, "end": v(0.9, 6.82) * mm});
            skLineSegment(sketch, "E1997", {"start": v(0.9, 6.82) * mm, "end": v(0.89, 6.93) * mm});
            skLineSegment(sketch, "E1998", {"start": v(0.89, 6.93) * mm, "end": v(0.88, 7.04) * mm});
            skLineSegment(sketch, "E1999", {"start": v(0.88, 7.04) * mm, "end": v(0.87, 7.14) * mm});
            skLineSegment(sketch, "E2000", {"start": v(0.87, 7.14) * mm, "end": v(0.86, 7.24) * mm});
            skLineSegment(sketch, "E2001", {"start": v(0.86, 7.24) * mm, "end": v(0.85, 7.33) * mm});
            skLineSegment(sketch, "E2002", {"start": v(0.85, 7.33) * mm, "end": v(0.85, 7.41) * mm});
            skLineSegment(sketch, "E2003", {"start": v(0.85, 7.41) * mm, "end": v(0.85, 7.5) * mm});
            skLineSegment(sketch, "E2004", {"start": v(0.85, 7.5) * mm, "end": v(0.85, 7.53) * mm});
            skLineSegment(sketch, "E2005", {"start": v(0.85, 7.53) * mm, "end": v(0.85, 7.56) * mm});
            skLineSegment(sketch, "E2006", {"start": v(0.85, 7.56) * mm, "end": v(0.86, 8.1) * mm});
            skLineSegment(sketch, "E2007", {"start": v(0.86, 8.1) * mm, "end": v(0.9, 8.61) * mm});
            skLineSegment(sketch, "E2008", {"start": v(0.9, 8.61) * mm, "end": v(0.97, 9.13) * mm});
            skLineSegment(sketch, "E2009", {"start": v(0.97, 9.13) * mm, "end": v(1.07, 9.63) * mm});
            skLineSegment(sketch, "E2010", {"start": v(1.07, 9.63) * mm, "end": v(1.2, 10.13) * mm});
            skLineSegment(sketch, "E2011", {"start": v(1.2, 10.13) * mm, "end": v(1.34, 10.62) * mm});
            skLineSegment(sketch, "E2012", {"start": v(1.34, 10.62) * mm, "end": v(1.52, 11.1) * mm});
            skLineSegment(sketch, "E2013", {"start": v(1.52, 11.1) * mm, "end": v(1.73, 11.57) * mm});
            skLineSegment(sketch, "E2014", {"start": v(1.73, 11.57) * mm, "end": v(1.97, 12.03) * mm});
            skLineSegment(sketch, "E2015", {"start": v(1.97, 12.03) * mm, "end": v(2.22, 12.47) * mm});
            skLineSegment(sketch, "E2016", {"start": v(2.22, 12.47) * mm, "end": v(2.49, 12.9) * mm});
            skLineSegment(sketch, "E2017", {"start": v(2.49, 12.9) * mm, "end": v(2.77, 13.3) * mm});
            skLineSegment(sketch, "E2018", {"start": v(2.77, 13.3) * mm, "end": v(3.07, 13.7) * mm});
            skLineSegment(sketch, "E2019", {"start": v(3.07, 13.7) * mm, "end": v(3.39, 14.07) * mm});
            skLineSegment(sketch, "E2020", {"start": v(3.39, 14.07) * mm, "end": v(3.72, 14.42) * mm});
            skLineSegment(sketch, "E2021", {"start": v(3.72, 14.42) * mm, "end": v(4.07, 14.76) * mm});
            skLineSegment(sketch, "E2022", {"start": v(4.07, 14.76) * mm, "end": v(4.8, 15.38) * mm});
            skLineSegment(sketch, "E2023", {"start": v(4.8, 15.38) * mm, "end": v(5.17, 15.67) * mm});
            skLineSegment(sketch, "E2024", {"start": v(5.17, 15.67) * mm, "end": v(5.55, 15.93) * mm});
            skLineSegment(sketch, "E2025", {"start": v(5.55, 15.93) * mm, "end": v(5.93, 16.17) * mm});
            skLineSegment(sketch, "E2026", {"start": v(5.93, 16.17) * mm, "end": v(6.32, 16.4) * mm});
            skLineSegment(sketch, "E2027", {"start": v(6.32, 16.4) * mm, "end": v(6.71, 16.6) * mm});
            skLineSegment(sketch, "E2028", {"start": v(6.71, 16.6) * mm, "end": v(7.11, 16.78) * mm});
            skLineSegment(sketch, "E2029", {"start": v(7.11, 16.78) * mm, "end": v(7.51, 16.95) * mm});
            skLineSegment(sketch, "E2030", {"start": v(7.51, 16.95) * mm, "end": v(7.9, 17.1) * mm});
            skLineSegment(sketch, "E2031", {"start": v(7.9, 17.1) * mm, "end": v(8.3, 17.22) * mm});
            skLineSegment(sketch, "E2032", {"start": v(8.3, 17.22) * mm, "end": v(8.68, 17.32) * mm});
            skLineSegment(sketch, "E2033", {"start": v(8.68, 17.32) * mm, "end": v(9.06, 17.4) * mm});
            skLineSegment(sketch, "E2034", {"start": v(9.06, 17.4) * mm, "end": v(9.43, 17.46) * mm});
            skLineSegment(sketch, "E2035", {"start": v(9.43, 17.46) * mm, "end": v(9.8, 17.49) * mm});
            skLineSegment(sketch, "E2036", {"start": v(9.8, 17.49) * mm, "end": v(10.17, 17.5) * mm});
            skLineSegment(sketch, "E2037", {"start": v(10.17, 17.5) * mm, "end": v(10.58, 17.49) * mm});
            skLineSegment(sketch, "E2038", {"start": v(10.58, 17.49) * mm, "end": v(10.97, 17.45) * mm});
            skLineSegment(sketch, "E2039", {"start": v(10.97, 17.45) * mm, "end": v(11.16, 17.42) * mm});
            skLineSegment(sketch, "E2040", {"start": v(11.16, 17.42) * mm, "end": v(11.34, 17.38) * mm});
            skLineSegment(sketch, "E2041", {"start": v(11.34, 17.38) * mm, "end": v(11.52, 17.34) * mm});
            skLineSegment(sketch, "E2042", {"start": v(11.52, 17.34) * mm, "end": v(11.7, 17.3) * mm});
            skLineSegment(sketch, "E2043", {"start": v(11.7, 17.3) * mm, "end": v(11.86, 17.24) * mm});
            skLineSegment(sketch, "E2044", {"start": v(11.86, 17.24) * mm, "end": v(12.03, 17.18) * mm});
            skLineSegment(sketch, "E2045", {"start": v(12.03, 17.18) * mm, "end": v(12.18, 17.11) * mm});
            skLineSegment(sketch, "E2046", {"start": v(12.18, 17.11) * mm, "end": v(12.33, 17.04) * mm});
            skLineSegment(sketch, "E2047", {"start": v(12.33, 17.04) * mm, "end": v(12.48, 16.96) * mm});
            skLineSegment(sketch, "E2048", {"start": v(12.48, 16.96) * mm, "end": v(12.62, 16.87) * mm});
            skLineSegment(sketch, "E2049", {"start": v(12.62, 16.87) * mm, "end": v(12.76, 16.78) * mm});
            skLineSegment(sketch, "E2050", {"start": v(12.76, 16.78) * mm, "end": v(12.9, 16.68) * mm});
            skLineSegment(sketch, "E2051", {"start": v(12.9, 16.68) * mm, "end": v(13.02, 16.58) * mm});
            skLineSegment(sketch, "E2052", {"start": v(13.02, 16.58) * mm, "end": v(13.13, 16.47) * mm});
            skLineSegment(sketch, "E2053", {"start": v(13.13, 16.47) * mm, "end": v(13.24, 16.36) * mm});
            skLineSegment(sketch, "E2054", {"start": v(13.24, 16.36) * mm, "end": v(13.34, 16.25) * mm});
            skLineSegment(sketch, "E2055", {"start": v(13.34, 16.25) * mm, "end": v(13.44, 16.13) * mm});
            skLineSegment(sketch, "E2056", {"start": v(13.44, 16.13) * mm, "end": v(13.52, 16) * mm});
            skLineSegment(sketch, "E2057", {"start": v(13.52, 16) * mm, "end": v(13.6, 15.88) * mm});
            skLineSegment(sketch, "E2058", {"start": v(13.6, 15.88) * mm, "end": v(13.67, 15.75) * mm});
            skLineSegment(sketch, "E2059", {"start": v(13.67, 15.75) * mm, "end": v(13.73, 15.62) * mm});
            skLineSegment(sketch, "E2060", {"start": v(13.73, 15.62) * mm, "end": v(13.78, 15.49) * mm});
            skLineSegment(sketch, "E2061", {"start": v(13.78, 15.49) * mm, "end": v(13.83, 15.35) * mm});
            skLineSegment(sketch, "E2062", {"start": v(13.83, 15.35) * mm, "end": v(13.86, 15.2) * mm});
            skLineSegment(sketch, "E2063", {"start": v(13.86, 15.2) * mm, "end": v(13.89, 15.05) * mm});
            skLineSegment(sketch, "E2064", {"start": v(13.89, 15.05) * mm, "end": v(13.9, 14.9) * mm});
            skLineSegment(sketch, "E2065", {"start": v(13.9, 14.9) * mm, "end": v(13.92, 14.75) * mm});
            skLineSegment(sketch, "E2066", {"start": v(13.92, 14.75) * mm, "end": v(13.93, 14.59) * mm});
            skLineSegment(sketch, "E2067", {"start": v(13.93, 14.59) * mm, "end": v(13.91, 14.17) * mm});
            skLineSegment(sketch, "E2068", {"start": v(13.91, 14.17) * mm, "end": v(13.87, 13.76) * mm});
            skLineSegment(sketch, "E2069", {"start": v(13.87, 13.76) * mm, "end": v(13.8, 13.36) * mm});
            skLineSegment(sketch, "E2070", {"start": v(13.8, 13.36) * mm, "end": v(13.7, 12.97) * mm});
            skLineSegment(sketch, "E2071", {"start": v(13.7, 12.97) * mm, "end": v(13.58, 12.6) * mm});
            skLineSegment(sketch, "E2072", {"start": v(13.58, 12.6) * mm, "end": v(13.43, 12.23) * mm});
            skLineSegment(sketch, "E2073", {"start": v(13.43, 12.23) * mm, "end": v(13.25, 11.87) * mm});
            skLineSegment(sketch, "E2074", {"start": v(13.25, 11.87) * mm, "end": v(13.04, 11.53) * mm});
            skLineSegment(sketch, "E2075", {"start": v(13.04, 11.53) * mm, "end": v(12.82, 11.2) * mm});
            skLineSegment(sketch, "E2076", {"start": v(12.82, 11.2) * mm, "end": v(12.58, 10.87) * mm});
            skLineSegment(sketch, "E2077", {"start": v(12.58, 10.87) * mm, "end": v(12.32, 10.56) * mm});
            skLineSegment(sketch, "E2078", {"start": v(12.32, 10.56) * mm, "end": v(12.05, 10.25) * mm});
            skLineSegment(sketch, "E2079", {"start": v(12.05, 10.25) * mm, "end": v(11.46, 9.66) * mm});
            skLineSegment(sketch, "E2080", {"start": v(11.46, 9.66) * mm, "end": v(10.8, 9.1) * mm});
            skLineSegment(sketch, "E2081", {"start": v(10.8, 9.1) * mm, "end": v(10.46, 8.84) * mm});
            skLineSegment(sketch, "E2082", {"start": v(10.46, 8.84) * mm, "end": v(10.09, 8.56) * mm});
            skLineSegment(sketch, "E2083", {"start": v(10.09, 8.56) * mm, "end": v(9.3, 8) * mm});
            skLineSegment(sketch, "E2084", {"start": v(9.3, 8) * mm, "end": v(8.42, 7.41) * mm});
            skLineSegment(sketch, "E2085", {"start": v(8.42, 7.41) * mm, "end": v(7.47, 6.8) * mm});
            skLineSegment(sketch, "E2086", {"start": v(7.47, 6.8) * mm, "end": v(7.23, 6.65) * mm});
            skLineSegment(sketch, "E2087", {"start": v(7.23, 6.65) * mm, "end": v(7, 6.51) * mm});
            skLineSegment(sketch, "E2088", {"start": v(7, 6.51) * mm, "end": v(6.78, 6.38) * mm});
            skLineSegment(sketch, "E2089", {"start": v(6.78, 6.38) * mm, "end": v(6.58, 6.25) * mm});
            skLineSegment(sketch, "E2090", {"start": v(6.58, 6.25) * mm, "end": v(6.38, 6.13) * mm});
            skLineSegment(sketch, "E2091", {"start": v(6.38, 6.13) * mm, "end": v(6.2, 6.01) * mm});
            skLineSegment(sketch, "E2092", {"start": v(6.2, 6.01) * mm, "end": v(6.03, 5.9) * mm});
            skLineSegment(sketch, "E2093", {"start": v(6.03, 5.9) * mm, "end": v(5.88, 5.8) * mm});
            skLineSegment(sketch, "E2094", {"start": v(5.88, 5.8) * mm, "end": v(5.73, 5.71) * mm});
            skLineSegment(sketch, "E2095", {"start": v(5.73, 5.71) * mm, "end": v(5.67, 5.67) * mm});
            skLineSegment(sketch, "E2096", {"start": v(5.67, 5.67) * mm, "end": v(5.6, 5.63) * mm});
            skLineSegment(sketch, "E2097", {"start": v(5.6, 5.63) * mm, "end": v(5.54, 5.59) * mm});
            skLineSegment(sketch, "E2098", {"start": v(5.54, 5.59) * mm, "end": v(5.48, 5.55) * mm});
            skLineSegment(sketch, "E2099", {"start": v(5.48, 5.55) * mm, "end": v(5.43, 5.51) * mm});
            skLineSegment(sketch, "E2100", {"start": v(5.43, 5.51) * mm, "end": v(5.37, 5.48) * mm});
            skLineSegment(sketch, "E2101", {"start": v(5.37, 5.48) * mm, "end": v(5.32, 5.45) * mm});
            skLineSegment(sketch, "E2102", {"start": v(5.32, 5.45) * mm, "end": v(5.28, 5.41) * mm});
            skLineSegment(sketch, "E2103", {"start": v(5.28, 5.41) * mm, "end": v(5.24, 5.38) * mm});
            skLineSegment(sketch, "E2104", {"start": v(5.24, 5.38) * mm, "end": v(5.2, 5.36) * mm});
            skLineSegment(sketch, "E2105", {"start": v(5.2, 5.36) * mm, "end": v(5.16, 5.33) * mm});
            skLineSegment(sketch, "E2106", {"start": v(5.16, 5.33) * mm, "end": v(5.12, 5.3) * mm});
            skLineSegment(sketch, "E2107", {"start": v(5.12, 5.3) * mm, "end": v(5.1, 5.3) * mm});
            skLineSegment(sketch, "E2108", {"start": v(5.1, 5.3) * mm, "end": v(5.1, 5.28) * mm});
            skLineSegment(sketch, "E2109", {"start": v(5.1, 5.28) * mm, "end": v(5.08, 5.27) * mm});
            skLineSegment(sketch, "E2110", {"start": v(5.08, 5.27) * mm, "end": v(5.07, 5.26) * mm});
            skLineSegment(sketch, "E2111", {"start": v(5.07, 5.26) * mm, "end": v(5.45, 3.93) * mm});
            skLineSegment(sketch, "E2112", {"start": v(5.45, 3.93) * mm, "end": v(5.91, 2.57) * mm});
            skLineSegment(sketch, "E2113", {"start": v(5.91, 2.57) * mm, "end": v(6.47, 1.2) * mm});
            skLineSegment(sketch, "E2114", {"start": v(6.47, 1.2) * mm, "end": v(7.11, -0.18) * mm});
            skLineSegment(sketch, "E2115", {"start": v(7.11, -0.18) * mm, "end": v(7.57, 0.14) * mm});
            skLineSegment(sketch, "E2116", {"start": v(7.57, 0.14) * mm, "end": v(8, 0.45) * mm});
            skLineSegment(sketch, "E2117", {"start": v(8, 0.45) * mm, "end": v(8.42, 0.75) * mm});
            skLineSegment(sketch, "E2118", {"start": v(8.42, 0.75) * mm, "end": v(8.8, 1.04) * mm});
            skLineSegment(sketch, "E2119", {"start": v(8.8, 1.04) * mm, "end": v(9.16, 1.32) * mm});
            skLineSegment(sketch, "E2120", {"start": v(9.16, 1.32) * mm, "end": v(9.5, 1.6) * mm});
            skLineSegment(sketch, "E2121", {"start": v(9.5, 1.6) * mm, "end": v(9.8, 1.86) * mm});
            skLineSegment(sketch, "E2122", {"start": v(9.8, 1.86) * mm, "end": v(10.09, 2.12) * mm});
            skLineSegment(sketch, "E2123", {"start": v(10.09, 2.12) * mm, "end": v(10.6, 2.63) * mm});
            skLineSegment(sketch, "E2124", {"start": v(10.6, 2.63) * mm, "end": v(11.08, 3.11) * mm});
            skLineSegment(sketch, "E2125", {"start": v(11.08, 3.11) * mm, "end": v(11.51, 3.58) * mm});
            skLineSegment(sketch, "E2126", {"start": v(11.51, 3.58) * mm, "end": v(11.9, 4.02) * mm});
            skLineSegment(sketch, "E2127", {"start": v(11.9, 4.02) * mm, "end": v(12, 4.12) * mm});
            skLineSegment(sketch, "E2128", {"start": v(12, 4.12) * mm, "end": v(12.08, 4.22) * mm});
            skLineSegment(sketch, "E2129", {"start": v(12.08, 4.22) * mm, "end": v(12.16, 4.31) * mm});
            skLineSegment(sketch, "E2130", {"start": v(12.16, 4.31) * mm, "end": v(12.24, 4.4) * mm});
            skLineSegment(sketch, "E2131", {"start": v(12.24, 4.4) * mm, "end": v(12.31, 4.48) * mm});
            skLineSegment(sketch, "E2132", {"start": v(12.31, 4.48) * mm, "end": v(12.39, 4.55) * mm});
            skLineSegment(sketch, "E2133", {"start": v(12.39, 4.55) * mm, "end": v(12.45, 4.61) * mm});
            skLineSegment(sketch, "E2134", {"start": v(12.45, 4.61) * mm, "end": v(12.49, 4.64) * mm});
            skLineSegment(sketch, "E2135", {"start": v(12.49, 4.64) * mm, "end": v(12.52, 4.67) * mm});
            skLineSegment(sketch, "E2136", {"start": v(12.52, 4.67) * mm, "end": v(12.55, 4.7) * mm});
            skLineSegment(sketch, "E2137", {"start": v(12.55, 4.7) * mm, "end": v(12.58, 4.72) * mm});
            skLineSegment(sketch, "E2138", {"start": v(12.58, 4.72) * mm, "end": v(12.6, 4.74) * mm});
            skLineSegment(sketch, "E2139", {"start": v(12.6, 4.74) * mm, "end": v(12.63, 4.76) * mm});
            skLineSegment(sketch, "E2140", {"start": v(12.63, 4.76) * mm, "end": v(12.66, 4.78) * mm});
            skLineSegment(sketch, "E2141", {"start": v(12.66, 4.78) * mm, "end": v(12.69, 4.8) * mm});
            skLineSegment(sketch, "E2142", {"start": v(12.69, 4.8) * mm, "end": v(12.71, 4.82) * mm});
            skLineSegment(sketch, "E2143", {"start": v(12.71, 4.82) * mm, "end": v(12.74, 4.83) * mm});
            skLineSegment(sketch, "E2144", {"start": v(12.74, 4.83) * mm, "end": v(12.76, 4.84) * mm});
            skLineSegment(sketch, "E2145", {"start": v(12.76, 4.84) * mm, "end": v(12.78, 4.85) * mm});
            skLineSegment(sketch, "E2146", {"start": v(12.78, 4.85) * mm, "end": v(12.8, 4.86) * mm});
            skLineSegment(sketch, "E2147", {"start": v(12.8, 4.86) * mm, "end": v(12.81, 4.87) * mm});
            skLineSegment(sketch, "E2148", {"start": v(12.81, 4.87) * mm, "end": v(12.82, 4.87) * mm});
            skLineSegment(sketch, "E2149", {"start": v(12.82, 4.87) * mm, "end": v(12.83, 4.87) * mm});
            skLineSegment(sketch, "E2150", {"start": v(12.83, 4.87) * mm, "end": v(12.84, 4.88) * mm});
            skLineSegment(sketch, "E2151", {"start": v(12.84, 4.88) * mm, "end": v(12.85, 4.88) * mm});
            skLineSegment(sketch, "E2152", {"start": v(12.85, 4.88) * mm, "end": v(12.86, 4.88) * mm});
            skLineSegment(sketch, "E2153", {"start": v(12.86, 4.88) * mm, "end": v(12.87, 4.88) * mm});
            skLineSegment(sketch, "E2154", {"start": v(12.87, 4.88) * mm, "end": v(12.88, 4.88) * mm});
            skLineSegment(sketch, "E2155", {"start": v(12.88, 4.88) * mm, "end": v(12.88, 4.88) * mm});
            skLineSegment(sketch, "E2156", {"start": v(12.88, 4.88) * mm, "end": v(12.9, 4.88) * mm});
            skLineSegment(sketch, "E2157", {"start": v(12.9, 4.88) * mm, "end": v(12.9, 4.88) * mm});
            skLineSegment(sketch, "E2158", {"start": v(12.9, 4.88) * mm, "end": v(12.92, 4.88) * mm});
            skLineSegment(sketch, "E2159", {"start": v(12.92, 4.88) * mm, "end": v(12.93, 4.88) * mm});
            skLineSegment(sketch, "E2160", {"start": v(12.93, 4.88) * mm, "end": v(12.94, 4.88) * mm});
            skLineSegment(sketch, "E2161", {"start": v(12.94, 4.88) * mm, "end": v(12.95, 4.87) * mm});
            skLineSegment(sketch, "E2162", {"start": v(12.95, 4.87) * mm, "end": v(12.96, 4.87) * mm});
            skLineSegment(sketch, "E2163", {"start": v(12.96, 4.87) * mm, "end": v(12.97, 4.86) * mm});
            skLineSegment(sketch, "E2164", {"start": v(12.97, 4.86) * mm, "end": v(12.98, 4.85) * mm});
            skLineSegment(sketch, "E2165", {"start": v(12.98, 4.85) * mm, "end": v(13, 4.85) * mm});
            skLineSegment(sketch, "E2166", {"start": v(13, 4.85) * mm, "end": v(13, 4.84) * mm});
            skLineSegment(sketch, "E2167", {"start": v(13, 4.84) * mm, "end": v(13.02, 4.83) * mm});
            skLineSegment(sketch, "E2168", {"start": v(13.02, 4.83) * mm, "end": v(13.03, 4.82) * mm});
            skLineSegment(sketch, "E2169", {"start": v(13.03, 4.82) * mm, "end": v(13.04, 4.8) * mm});
            skLineSegment(sketch, "E2170", {"start": v(13.04, 4.8) * mm, "end": v(13.05, 4.8) * mm});
            skLineSegment(sketch, "E2171", {"start": v(13.05, 4.8) * mm, "end": v(13.06, 4.78) * mm});
            skLineSegment(sketch, "E2172", {"start": v(13.06, 4.78) * mm, "end": v(13.07, 4.77) * mm});
            skLineSegment(sketch, "E2173", {"start": v(13.07, 4.77) * mm, "end": v(13.08, 4.75) * mm});
            skLineSegment(sketch, "E2174", {"start": v(13.08, 4.75) * mm, "end": v(13.09, 4.74) * mm});
            skLineSegment(sketch, "E2175", {"start": v(13.09, 4.74) * mm, "end": v(13.1, 4.72) * mm});
            skLineSegment(sketch, "E2176", {"start": v(13.1, 4.72) * mm, "end": v(13.1, 4.7) * mm});
            skLineSegment(sketch, "E2177", {"start": v(13.1, 4.7) * mm, "end": v(13.12, 4.66) * mm});
            skLineSegment(sketch, "E2178", {"start": v(13.12, 4.66) * mm, "end": v(13.14, 4.62) * mm});
            skLineSegment(sketch, "E2179", {"start": v(13.14, 4.62) * mm, "end": v(13.16, 4.58) * mm});
            skLineSegment(sketch, "E2180", {"start": v(13.16, 4.58) * mm, "end": v(13.18, 4.53) * mm});
            skLineSegment(sketch, "E2181", {"start": v(13.18, 4.53) * mm, "end": v(13.2, 4.48) * mm});
            skLineSegment(sketch, "E2182", {"start": v(13.2, 4.48) * mm, "end": v(13.2, 4.42) * mm});
            skLineSegment(sketch, "E2183", {"start": v(13.2, 4.42) * mm, "end": v(13.26, 4.18) * mm});
            skLineSegment(sketch, "E2184", {"start": v(13.26, 4.18) * mm, "end": v(13.3, 3.93) * mm});
            skLineSegment(sketch, "E2185", {"start": v(13.3, 3.93) * mm, "end": v(13.33, 3.68) * mm});
            skLineSegment(sketch, "E2186", {"start": v(13.33, 3.68) * mm, "end": v(13.34, 3.4) * mm});
            skLineSegment(sketch, "E2187", {"start": v(13.34, 3.4) * mm, "end": v(13.33, 3.09) * mm});
            skLineSegment(sketch, "E2188", {"start": v(13.33, 3.09) * mm, "end": v(13.3, 2.77) * mm});
            skLineSegment(sketch, "E2189", {"start": v(13.3, 2.77) * mm, "end": v(13.27, 2.46) * mm});
            skLineSegment(sketch, "E2190", {"start": v(13.27, 2.46) * mm, "end": v(13.22, 2.16) * mm});
            skLineSegment(sketch, "E2191", {"start": v(13.22, 2.16) * mm, "end": v(13.15, 1.86) * mm});
            skLineSegment(sketch, "E2192", {"start": v(13.15, 1.86) * mm, "end": v(13.07, 1.56) * mm});
            skLineSegment(sketch, "E2193", {"start": v(13.07, 1.56) * mm, "end": v(12.98, 1.27) * mm});
            skLineSegment(sketch, "E2194", {"start": v(12.98, 1.27) * mm, "end": v(12.87, 0.98) * mm});
            skLineSegment(sketch, "E2195", {"start": v(12.87, 0.98) * mm, "end": v(12.61, 0.41) * mm});
            skLineSegment(sketch, "E2196", {"start": v(12.61, 0.41) * mm, "end": v(12.3, -0.16) * mm});
            skLineSegment(sketch, "E2197", {"start": v(12.3, -0.16) * mm, "end": v(11.95, -0.73) * mm});
            skLineSegment(sketch, "E2198", {"start": v(11.95, -0.73) * mm, "end": v(11.54, -1.3) * mm});
            skLineSegment(sketch, "E2199", {"start": v(11.54, -1.3) * mm, "end": v(11.1, -1.88) * mm});
            skLineSegment(sketch, "E2200", {"start": v(11.1, -1.88) * mm, "end": v(10.6, -2.47) * mm});
            skLineSegment(sketch, "E2201", {"start": v(10.6, -2.47) * mm, "end": v(10.04, -3.09) * mm});
            skLineSegment(sketch, "E2202", {"start": v(10.04, -3.09) * mm, "end": v(9.43, -3.72) * mm});
            skLineSegment(sketch, "E2203", {"start": v(9.43, -3.72) * mm, "end": v(10.82, -5.24) * mm});
            skLineSegment(sketch, "E2204", {"start": v(10.82, -5.24) * mm, "end": v(10.87, -5.2) * mm});
            skLineSegment(sketch, "E2205", {"start": v(10.87, -5.2) * mm, "end": v(10.93, -5.15) * mm});
            skLineSegment(sketch, "E2206", {"start": v(10.93, -5.15) * mm, "end": v(10.98, -5.1) * mm});
            skLineSegment(sketch, "E2207", {"start": v(10.98, -5.1) * mm, "end": v(11.04, -5.04) * mm});
            skLineSegment(sketch, "E2208", {"start": v(11.04, -5.04) * mm, "end": v(11.1, -4.97) * mm});
            skLineSegment(sketch, "E2209", {"start": v(11.1, -4.97) * mm, "end": v(11.16, -4.9) * mm});
            skLineSegment(sketch, "E2210", {"start": v(11.16, -4.9) * mm, "end": v(11.22, -4.83) * mm});
            skLineSegment(sketch, "E2211", {"start": v(11.22, -4.83) * mm, "end": v(11.29, -4.76) * mm});
            skLineSegment(sketch, "E2212", {"start": v(11.29, -4.76) * mm, "end": v(11.36, -4.68) * mm});
            skLineSegment(sketch, "E2213", {"start": v(11.36, -4.68) * mm, "end": v(11.42, -4.61) * mm});
            skLineSegment(sketch, "E2214", {"start": v(11.42, -4.61) * mm, "end": v(11.45, -4.58) * mm});
            skLineSegment(sketch, "E2215", {"start": v(11.45, -4.58) * mm, "end": v(11.48, -4.55) * mm});
            skLineSegment(sketch, "E2216", {"start": v(11.48, -4.55) * mm, "end": v(11.5, -4.52) * mm});
            skLineSegment(sketch, "E2217", {"start": v(11.5, -4.52) * mm, "end": v(11.53, -4.5) * mm});
            skLineSegment(sketch, "E2218", {"start": v(11.53, -4.5) * mm, "end": v(11.56, -4.47) * mm});
            skLineSegment(sketch, "E2219", {"start": v(11.56, -4.47) * mm, "end": v(11.58, -4.44) * mm});
            skLineSegment(sketch, "E2220", {"start": v(11.58, -4.44) * mm, "end": v(11.6, -4.42) * mm});
            skLineSegment(sketch, "E2221", {"start": v(11.6, -4.42) * mm, "end": v(11.63, -4.4) * mm});
            skLineSegment(sketch, "E2222", {"start": v(11.63, -4.4) * mm, "end": v(11.65, -4.38) * mm});
            skLineSegment(sketch, "E2223", {"start": v(11.65, -4.38) * mm, "end": v(11.67, -4.37) * mm});
            skLineSegment(sketch, "E2224", {"start": v(11.67, -4.37) * mm, "end": v(11.7, -4.35) * mm});
            skLineSegment(sketch, "E2225", {"start": v(11.7, -4.35) * mm, "end": v(11.71, -4.34) * mm});
            skLineSegment(sketch, "E2226", {"start": v(11.71, -4.34) * mm, "end": v(11.75, -4.3) * mm});
            skLineSegment(sketch, "E2227", {"start": v(11.75, -4.3) * mm, "end": v(11.77, -4.3) * mm});
            skLineSegment(sketch, "E2228", {"start": v(11.77, -4.3) * mm, "end": v(11.79, -4.28) * mm});
            skLineSegment(sketch, "E2229", {"start": v(11.79, -4.28) * mm, "end": v(11.8, -4.27) * mm});
            skLineSegment(sketch, "E2230", {"start": v(11.8, -4.27) * mm, "end": v(11.82, -4.26) * mm});
            skLineSegment(sketch, "E2231", {"start": v(11.82, -4.26) * mm, "end": v(11.84, -4.25) * mm});
            skLineSegment(sketch, "E2232", {"start": v(11.84, -4.25) * mm, "end": v(11.86, -4.24) * mm});
            skLineSegment(sketch, "E2233", {"start": v(11.86, -4.24) * mm, "end": v(11.88, -4.23) * mm});
            skLineSegment(sketch, "E2234", {"start": v(11.88, -4.23) * mm, "end": v(11.9, -4.23) * mm});
            skLineSegment(sketch, "E2235", {"start": v(11.9, -4.23) * mm, "end": v(11.92, -4.22) * mm});
            skLineSegment(sketch, "E2236", {"start": v(11.92, -4.22) * mm, "end": v(11.94, -4.22) * mm});
            skLineSegment(sketch, "E2237", {"start": v(11.94, -4.22) * mm, "end": v(11.96, -4.21) * mm});
            skLineSegment(sketch, "E2238", {"start": v(11.96, -4.21) * mm, "end": v(11.99, -4.21) * mm});
            skLineSegment(sketch, "E2239", {"start": v(11.99, -4.21) * mm, "end": v(12, -4.2) * mm});
            skLineSegment(sketch, "E2240", {"start": v(12, -4.2) * mm, "end": v(12.03, -4.2) * mm});
            skLineSegment(sketch, "E2241", {"start": v(12.03, -4.2) * mm, "end": v(12.05, -4.2) * mm});
            skLineSegment(sketch, "E2242", {"start": v(12.05, -4.2) * mm, "end": v(12.08, -4.21) * mm});
            skLineSegment(sketch, "E2243", {"start": v(12.08, -4.21) * mm, "end": v(12.1, -4.21) * mm});
            skLineSegment(sketch, "E2244", {"start": v(12.1, -4.21) * mm, "end": v(12.13, -4.22) * mm});
            skLineSegment(sketch, "E2245", {"start": v(12.13, -4.22) * mm, "end": v(12.15, -4.23) * mm});
            skLineSegment(sketch, "E2246", {"start": v(12.15, -4.23) * mm, "end": v(12.17, -4.23) * mm});
            skLineSegment(sketch, "E2247", {"start": v(12.17, -4.23) * mm, "end": v(12.2, -4.24) * mm});
            skLineSegment(sketch, "E2248", {"start": v(12.2, -4.24) * mm, "end": v(12.21, -4.25) * mm});
            skLineSegment(sketch, "E2249", {"start": v(12.21, -4.25) * mm, "end": v(12.23, -4.26) * mm});
            skLineSegment(sketch, "E2250", {"start": v(12.23, -4.26) * mm, "end": v(12.25, -4.27) * mm});
            skLineSegment(sketch, "E2251", {"start": v(12.25, -4.27) * mm, "end": v(12.27, -4.29) * mm});
            skLineSegment(sketch, "E2252", {"start": v(12.27, -4.29) * mm, "end": v(12.28, -4.3) * mm});
            skLineSegment(sketch, "E2253", {"start": v(12.28, -4.3) * mm, "end": v(12.3, -4.32) * mm});
            skLineSegment(sketch, "E2254", {"start": v(12.3, -4.32) * mm, "end": v(12.32, -4.34) * mm});
            skLineSegment(sketch, "E2255", {"start": v(12.32, -4.34) * mm, "end": v(12.33, -4.36) * mm});
            skLineSegment(sketch, "E2256", {"start": v(12.33, -4.36) * mm, "end": v(12.34, -4.38) * mm});
            skLineSegment(sketch, "E2257", {"start": v(12.34, -4.38) * mm, "end": v(12.37, -4.42) * mm});
            skLineSegment(sketch, "E2258", {"start": v(12.37, -4.42) * mm, "end": v(12.4, -4.46) * mm});
            skLineSegment(sketch, "E2259", {"start": v(12.4, -4.46) * mm, "end": v(12.42, -4.51) * mm});
            skLineSegment(sketch, "E2260", {"start": v(12.42, -4.51) * mm, "end": v(12.44, -4.56) * mm});
            skLineSegment(sketch, "E2261", {"start": v(12.44, -4.56) * mm, "end": v(12.45, -4.6) * mm});
            skLineSegment(sketch, "E2262", {"start": v(12.45, -4.6) * mm, "end": v(12.46, -4.65) * mm});
            skLineSegment(sketch, "E2263", {"start": v(12.46, -4.65) * mm, "end": v(12.47, -4.7) * mm});
            skLineSegment(sketch, "E2264", {"start": v(12.47, -4.7) * mm, "end": v(12.47, -4.76) * mm});
            skLineSegment(sketch, "E2265", {"start": v(12.47, -4.76) * mm, "end": v(12.47, -4.81) * mm});
            skLineSegment(sketch, "E2266", {"start": v(12.47, -4.81) * mm, "end": v(12.47, -4.87) * mm});
            skLineSegment(sketch, "E2267", {"start": v(12.47, -4.87) * mm, "end": v(12.46, -4.93) * mm});
            skLineSegment(sketch, "E2268", {"start": v(12.46, -4.93) * mm, "end": v(12.45, -5) * mm});
            skLineSegment(sketch, "E2269", {"start": v(12.45, -5) * mm, "end": v(12.44, -5.06) * mm});
            skLineSegment(sketch, "E2270", {"start": v(12.44, -5.06) * mm, "end": v(12.43, -5.12) * mm});
            skLineSegment(sketch, "E2271", {"start": v(12.43, -5.12) * mm, "end": v(12.41, -5.2) * mm});
            skLineSegment(sketch, "E2272", {"start": v(12.41, -5.2) * mm, "end": v(12.4, -5.26) * mm});
            skLineSegment(sketch, "E2273", {"start": v(12.4, -5.26) * mm, "end": v(12.35, -5.41) * mm});
            skLineSegment(sketch, "E2274", {"start": v(12.35, -5.41) * mm, "end": v(12.3, -5.57) * mm});
            skLineSegment(sketch, "E2275", {"start": v(12.3, -5.57) * mm, "end": v(12.24, -5.74) * mm});
            skLineSegment(sketch, "E2276", {"start": v(12.24, -5.74) * mm, "end": v(12.16, -5.92) * mm});
            skLineSegment(sketch, "E2277", {"start": v(12.16, -5.92) * mm, "end": v(12.08, -6.1) * mm});
            skLineSegment(sketch, "E2278", {"start": v(12.08, -6.1) * mm, "end": v(12, -6.3) * mm});
            skLineSegment(sketch, "E2279", {"start": v(12, -6.3) * mm, "end": v(11.9, -6.5) * mm});
            skLineSegment(sketch, "E2280", {"start": v(11.9, -6.5) * mm, "end": v(11.78, -6.72) * mm});
            skLineSegment(sketch, "E2281", {"start": v(11.78, -6.72) * mm, "end": v(11.66, -6.94) * mm});
            skLineSegment(sketch, "E2282", {"start": v(11.66, -6.94) * mm, "end": v(11.53, -7.18) * mm});
            skLineSegment(sketch, "E2283", {"start": v(11.53, -7.18) * mm, "end": v(11.4, -7.42) * mm});
            skLineSegment(sketch, "E2284", {"start": v(11.4, -7.42) * mm, "end": v(11.25, -7.67) * mm});
            skLineSegment(sketch, "E2285", {"start": v(11.25, -7.67) * mm, "end": v(11.1, -7.91) * mm});
            skLineSegment(sketch, "E2286", {"start": v(11.1, -7.91) * mm, "end": v(10.95, -8.14) * mm});
            skLineSegment(sketch, "E2287", {"start": v(10.95, -8.14) * mm, "end": v(10.8, -8.36) * mm});
            skLineSegment(sketch, "E2288", {"start": v(10.8, -8.36) * mm, "end": v(10.66, -8.55) * mm});
            skLineSegment(sketch, "E2289", {"start": v(10.66, -8.55) * mm, "end": v(10.52, -8.74) * mm});
            skLineSegment(sketch, "E2290", {"start": v(10.52, -8.74) * mm, "end": v(10.39, -8.9) * mm});
            skLineSegment(sketch, "E2291", {"start": v(10.39, -8.9) * mm, "end": v(10.26, -9.05) * mm});
            skLineSegment(sketch, "E2292", {"start": v(10.26, -9.05) * mm, "end": v(10.13, -9.19) * mm});
            skLineSegment(sketch, "E2293", {"start": v(10.13, -9.19) * mm, "end": v(10.07, -9.25) * mm});
            skLineSegment(sketch, "E2294", {"start": v(10.07, -9.25) * mm, "end": v(10, -9.3) * mm});
            skLineSegment(sketch, "E2295", {"start": v(10, -9.3) * mm, "end": v(9.94, -9.36) * mm});
            skLineSegment(sketch, "E2296", {"start": v(9.94, -9.36) * mm, "end": v(9.88, -9.4) * mm});
            skLineSegment(sketch, "E2297", {"start": v(9.88, -9.4) * mm, "end": v(9.82, -9.45) * mm});
            skLineSegment(sketch, "E2298", {"start": v(9.82, -9.45) * mm, "end": v(9.76, -9.5) * mm});
            skLineSegment(sketch, "E2299", {"start": v(9.76, -9.5) * mm, "end": v(9.7, -9.53) * mm});
            skLineSegment(sketch, "E2300", {"start": v(9.7, -9.53) * mm, "end": v(9.65, -9.57) * mm});
            skLineSegment(sketch, "E2301", {"start": v(9.65, -9.57) * mm, "end": v(9.6, -9.6) * mm});
            skLineSegment(sketch, "E2302", {"start": v(9.6, -9.6) * mm, "end": v(9.54, -9.62) * mm});
            skLineSegment(sketch, "E2303", {"start": v(9.54, -9.62) * mm, "end": v(9.48, -9.64) * mm});
            skLineSegment(sketch, "E2304", {"start": v(9.48, -9.64) * mm, "end": v(9.43, -9.66) * mm});
            skLineSegment(sketch, "E2305", {"start": v(9.43, -9.66) * mm, "end": v(9.38, -9.68) * mm});
            skLineSegment(sketch, "E2306", {"start": v(9.38, -9.68) * mm, "end": v(9.32, -9.69) * mm});
            skLineSegment(sketch, "E2307", {"start": v(9.32, -9.69) * mm, "end": v(9.27, -9.7) * mm});
            skLineSegment(sketch, "E2308", {"start": v(9.27, -9.7) * mm, "end": v(9.22, -9.7) * mm});
            skLineSegment(sketch, "E2309", {"start": v(9.22, -9.7) * mm, "end": v(9.17, -9.7) * mm});
            skLineSegment(sketch, "E2310", {"start": v(9.17, -9.7) * mm, "end": v(9.12, -9.69) * mm});
            skLineSegment(sketch, "E2311", {"start": v(9.12, -9.69) * mm, "end": v(9.06, -9.68) * mm});
            skLineSegment(sketch, "E2312", {"start": v(9.06, -9.68) * mm, "end": v(9.01, -9.67) * mm});
            skLineSegment(sketch, "E2313", {"start": v(9.01, -9.67) * mm, "end": v(8.96, -9.66) * mm});
            skLineSegment(sketch, "E2314", {"start": v(8.96, -9.66) * mm, "end": v(8.9, -9.65) * mm});
            skLineSegment(sketch, "E2315", {"start": v(8.9, -9.65) * mm, "end": v(8.86, -9.63) * mm});
            skLineSegment(sketch, "E2316", {"start": v(8.86, -9.63) * mm, "end": v(8.8, -9.6) * mm});
            skLineSegment(sketch, "E2317", {"start": v(8.8, -9.6) * mm, "end": v(8.75, -9.59) * mm});
            skLineSegment(sketch, "E2318", {"start": v(8.75, -9.59) * mm, "end": v(8.7, -9.56) * mm});
            skLineSegment(sketch, "E2319", {"start": v(8.7, -9.56) * mm, "end": v(8.65, -9.53) * mm});
            skLineSegment(sketch, "E2320", {"start": v(8.65, -9.53) * mm, "end": v(8.6, -9.5) * mm});
            skLineSegment(sketch, "E2321", {"start": v(8.6, -9.5) * mm, "end": v(8.5, -9.44) * mm});
            skLineSegment(sketch, "E2322", {"start": v(8.5, -9.44) * mm, "end": v(8.4, -9.36) * mm});
            skLineSegment(sketch, "E2323", {"start": v(8.4, -9.36) * mm, "end": v(8.35, -9.31) * mm});
            skLineSegment(sketch, "E2324", {"start": v(8.35, -9.31) * mm, "end": v(8.3, -9.26) * mm});
            skLineSegment(sketch, "E2325", {"start": v(8.3, -9.26) * mm, "end": v(8.24, -9.2) * mm});
            skLineSegment(sketch, "E2326", {"start": v(8.24, -9.2) * mm, "end": v(8.13, -9.1) * mm});
            skLineSegment(sketch, "E2327", {"start": v(8.13, -9.1) * mm, "end": v(8.02, -8.97) * mm});
            skLineSegment(sketch, "E2328", {"start": v(8.02, -8.97) * mm, "end": v(7.9, -8.83) * mm});
            skLineSegment(sketch, "E2329", {"start": v(7.9, -8.83) * mm, "end": v(7.77, -8.67) * mm});
            skLineSegment(sketch, "E2330", {"start": v(7.77, -8.67) * mm, "end": v(7.64, -8.5) * mm});
            skLineSegment(sketch, "E2331", {"start": v(7.64, -8.5) * mm, "end": v(7.5, -8.33) * mm});
            skLineSegment(sketch, "E2332", {"start": v(7.5, -8.33) * mm, "end": v(7.43, -8.24) * mm});
            skLineSegment(sketch, "E2333", {"start": v(7.43, -8.24) * mm, "end": v(7.29, -8.05) * mm});
            skLineSegment(sketch, "E2334", {"start": v(7.29, -8.05) * mm, "end": v(7.16, -7.86) * mm});
            skLineSegment(sketch, "E2335", {"start": v(7.16, -7.86) * mm, "end": v(7.03, -7.69) * mm});
            skLineSegment(sketch, "E2336", {"start": v(7.03, -7.69) * mm, "end": v(6.91, -7.52) * mm});
            skLineSegment(sketch, "E2337", {"start": v(6.91, -7.52) * mm, "end": v(6.8, -7.36) * mm});
            skLineSegment(sketch, "E2338", {"start": v(6.8, -7.36) * mm, "end": v(6.7, -7.2) * mm});
            skLineSegment(sketch, "E2339", {"start": v(6.7, -7.2) * mm, "end": v(6.6, -7.07) * mm});
            skLineSegment(sketch, "E2340", {"start": v(6.6, -7.07) * mm, "end": v(6.5, -6.93) * mm});
            skLineSegment(sketch, "E2341", {"start": v(6.5, -6.93) * mm, "end": v(5.32, -7.8) * mm});
            skLineSegment(sketch, "E2342", {"start": v(5.32, -7.8) * mm, "end": v(4.75, -8.2) * mm});
            skLineSegment(sketch, "E2343", {"start": v(4.75, -8.2) * mm, "end": v(4.2, -8.57) * mm});
            skLineSegment(sketch, "E2344", {"start": v(4.2, -8.57) * mm, "end": v(3.67, -8.91) * mm});
            skLineSegment(sketch, "E2345", {"start": v(3.67, -8.91) * mm, "end": v(3.16, -9.23) * mm});
            skLineSegment(sketch, "E2346", {"start": v(3.16, -9.23) * mm, "end": v(2.66, -9.52) * mm});
            skLineSegment(sketch, "E2347", {"start": v(2.66, -9.52) * mm, "end": v(2.18, -9.78) * mm});
            skLineSegment(sketch, "E2348", {"start": v(2.18, -9.78) * mm, "end": v(1.71, -10.01) * mm});
            skLineSegment(sketch, "E2349", {"start": v(1.71, -10.01) * mm, "end": v(1.27, -10.21) * mm});
            skLineSegment(sketch, "E2350", {"start": v(1.27, -10.21) * mm, "end": v(0.84, -10.38) * mm});
            skLineSegment(sketch, "E2351", {"start": v(0.84, -10.38) * mm, "end": v(0.42, -10.52) * mm});
            skLineSegment(sketch, "E2352", {"start": v(0.42, -10.52) * mm, "end": v(0.02, -10.63) * mm});
            skLineSegment(sketch, "E2353", {"start": v(0.02, -10.63) * mm, "end": v(-0.18, -10.67) * mm});
            skLineSegment(sketch, "E2354", {"start": v(-0.18, -10.67) * mm, "end": v(-0.37, -10.7) * mm});
            skLineSegment(sketch, "E2355", {"start": v(-0.37, -10.7) * mm, "end": v(-0.56, -10.74) * mm});
            skLineSegment(sketch, "E2356", {"start": v(-0.56, -10.74) * mm, "end": v(-0.74, -10.75) * mm});
            skLineSegment(sketch, "E2357", {"start": v(-0.74, -10.75) * mm, "end": v(-0.92, -10.77) * mm});
            skLineSegment(sketch, "E2358", {"start": v(-0.92, -10.77) * mm, "end": v(-1.1, -10.77) * mm});
            skLineSegment(sketch, "E2359", {"start": v(4.6, 9.23) * mm, "end": v(4.6, 8.36) * mm});
            skLineSegment(sketch, "E2360", {"start": v(4.6, 8.36) * mm, "end": v(5.34, 8.8) * mm});
            skLineSegment(sketch, "E2361", {"start": v(5.34, 8.8) * mm, "end": v(6.03, 9.23) * mm});
            skLineSegment(sketch, "E2362", {"start": v(6.03, 9.23) * mm, "end": v(6.69, 9.67) * mm});
            skLineSegment(sketch, "E2363", {"start": v(6.69, 9.67) * mm, "end": v(7.3, 10.12) * mm});
            skLineSegment(sketch, "E2364", {"start": v(7.3, 10.12) * mm, "end": v(7.86, 10.58) * mm});
            skLineSegment(sketch, "E2365", {"start": v(7.86, 10.58) * mm, "end": v(8.39, 11.04) * mm});
            skLineSegment(sketch, "E2366", {"start": v(8.39, 11.04) * mm, "end": v(8.87, 11.5) * mm});
            skLineSegment(sketch, "E2367", {"start": v(8.87, 11.5) * mm, "end": v(9.3, 11.97) * mm});
            skLineSegment(sketch, "E2368", {"start": v(9.3, 11.97) * mm, "end": v(9.51, 12.2) * mm});
            skLineSegment(sketch, "E2369", {"start": v(9.51, 12.2) * mm, "end": v(9.7, 12.44) * mm});
            skLineSegment(sketch, "E2370", {"start": v(9.7, 12.44) * mm, "end": v(9.88, 12.66) * mm});
            skLineSegment(sketch, "E2371", {"start": v(9.88, 12.66) * mm, "end": v(10.04, 12.87) * mm});
            skLineSegment(sketch, "E2372", {"start": v(10.04, 12.87) * mm, "end": v(10.2, 13.08) * mm});
            skLineSegment(sketch, "E2373", {"start": v(10.2, 13.08) * mm, "end": v(10.33, 13.29) * mm});
            skLineSegment(sketch, "E2374", {"start": v(10.33, 13.29) * mm, "end": v(10.46, 13.48) * mm});
            skLineSegment(sketch, "E2375", {"start": v(10.46, 13.48) * mm, "end": v(10.57, 13.68) * mm});
            skLineSegment(sketch, "E2376", {"start": v(10.57, 13.68) * mm, "end": v(10.67, 13.86) * mm});
            skLineSegment(sketch, "E2377", {"start": v(10.67, 13.86) * mm, "end": v(10.76, 14.04) * mm});
            skLineSegment(sketch, "E2378", {"start": v(10.76, 14.04) * mm, "end": v(10.83, 14.21) * mm});
            skLineSegment(sketch, "E2379", {"start": v(10.83, 14.21) * mm, "end": v(10.89, 14.38) * mm});
            skLineSegment(sketch, "E2380", {"start": v(10.89, 14.38) * mm, "end": v(10.93, 14.54) * mm});
            skLineSegment(sketch, "E2381", {"start": v(10.93, 14.54) * mm, "end": v(10.95, 14.62) * mm});
            skLineSegment(sketch, "E2382", {"start": v(10.95, 14.62) * mm, "end": v(10.97, 14.7) * mm});
            skLineSegment(sketch, "E2383", {"start": v(10.97, 14.7) * mm, "end": v(10.98, 14.77) * mm});
            skLineSegment(sketch, "E2384", {"start": v(10.98, 14.77) * mm, "end": v(10.99, 14.85) * mm});
            skLineSegment(sketch, "E2385", {"start": v(10.99, 14.85) * mm, "end": v(11, 14.92) * mm});
            skLineSegment(sketch, "E2386", {"start": v(11, 14.92) * mm, "end": v(11, 14.99) * mm});
            skLineSegment(sketch, "E2387", {"start": v(11, 14.99) * mm, "end": v(11, 15.05) * mm});
            skLineSegment(sketch, "E2388", {"start": v(11, 15.05) * mm, "end": v(10.99, 15.1) * mm});
            skLineSegment(sketch, "E2389", {"start": v(10.99, 15.1) * mm, "end": v(10.99, 15.16) * mm});
            skLineSegment(sketch, "E2390", {"start": v(10.99, 15.16) * mm, "end": v(10.98, 15.21) * mm});
            skLineSegment(sketch, "E2391", {"start": v(10.98, 15.21) * mm, "end": v(10.97, 15.26) * mm});
            skLineSegment(sketch, "E2392", {"start": v(10.97, 15.26) * mm, "end": v(10.96, 15.31) * mm});
            skLineSegment(sketch, "E2393", {"start": v(10.96, 15.31) * mm, "end": v(10.95, 15.36) * mm});
            skLineSegment(sketch, "E2394", {"start": v(10.95, 15.36) * mm, "end": v(10.93, 15.4) * mm});
            skLineSegment(sketch, "E2395", {"start": v(10.93, 15.4) * mm, "end": v(10.92, 15.45) * mm});
            skLineSegment(sketch, "E2396", {"start": v(10.92, 15.45) * mm, "end": v(10.9, 15.5) * mm});
            skLineSegment(sketch, "E2397", {"start": v(10.9, 15.5) * mm, "end": v(10.88, 15.53) * mm});
            skLineSegment(sketch, "E2398", {"start": v(10.88, 15.53) * mm, "end": v(10.86, 15.57) * mm});
            skLineSegment(sketch, "E2399", {"start": v(10.86, 15.57) * mm, "end": v(10.84, 15.6) * mm});
            skLineSegment(sketch, "E2400", {"start": v(10.84, 15.6) * mm, "end": v(10.81, 15.64) * mm});
            skLineSegment(sketch, "E2401", {"start": v(10.81, 15.64) * mm, "end": v(10.78, 15.67) * mm});
            skLineSegment(sketch, "E2402", {"start": v(10.78, 15.67) * mm, "end": v(10.76, 15.7) * mm});
            skLineSegment(sketch, "E2403", {"start": v(10.76, 15.7) * mm, "end": v(10.73, 15.73) * mm});
            skLineSegment(sketch, "E2404", {"start": v(10.73, 15.73) * mm, "end": v(10.7, 15.76) * mm});
            skLineSegment(sketch, "E2405", {"start": v(10.7, 15.76) * mm, "end": v(10.66, 15.78) * mm});
            skLineSegment(sketch, "E2406", {"start": v(10.66, 15.78) * mm, "end": v(10.62, 15.8) * mm});
            skLineSegment(sketch, "E2407", {"start": v(10.62, 15.8) * mm, "end": v(10.58, 15.83) * mm});
            skLineSegment(sketch, "E2408", {"start": v(10.58, 15.83) * mm, "end": v(10.54, 15.85) * mm});
            skLineSegment(sketch, "E2409", {"start": v(10.54, 15.85) * mm, "end": v(10.5, 15.86) * mm});
            skLineSegment(sketch, "E2410", {"start": v(10.5, 15.86) * mm, "end": v(10.46, 15.88) * mm});
            skLineSegment(sketch, "E2411", {"start": v(10.46, 15.88) * mm, "end": v(10.41, 15.9) * mm});
            skLineSegment(sketch, "E2412", {"start": v(10.41, 15.9) * mm, "end": v(10.37, 15.9) * mm});
            skLineSegment(sketch, "E2413", {"start": v(10.37, 15.9) * mm, "end": v(10.32, 15.92) * mm});
            skLineSegment(sketch, "E2414", {"start": v(10.32, 15.92) * mm, "end": v(10.27, 15.92) * mm});
            skLineSegment(sketch, "E2415", {"start": v(10.27, 15.92) * mm, "end": v(10.21, 15.93) * mm});
            skLineSegment(sketch, "E2416", {"start": v(10.21, 15.93) * mm, "end": v(10.16, 15.94) * mm});
            skLineSegment(sketch, "E2417", {"start": v(10.16, 15.94) * mm, "end": v(10.1, 15.94) * mm});
            skLineSegment(sketch, "E2418", {"start": v(10.1, 15.94) * mm, "end": v(10.04, 15.94) * mm});
            skLineSegment(sketch, "E2419", {"start": v(10.04, 15.94) * mm, "end": v(9.93, 15.93) * mm});
            skLineSegment(sketch, "E2420", {"start": v(9.93, 15.93) * mm, "end": v(9.82, 15.92) * mm});
            skLineSegment(sketch, "E2421", {"start": v(9.82, 15.92) * mm, "end": v(9.7, 15.9) * mm});
            skLineSegment(sketch, "E2422", {"start": v(9.7, 15.9) * mm, "end": v(9.58, 15.87) * mm});
            skLineSegment(sketch, "E2423", {"start": v(9.58, 15.87) * mm, "end": v(9.46, 15.84) * mm});
            skLineSegment(sketch, "E2424", {"start": v(9.46, 15.84) * mm, "end": v(9.33, 15.8) * mm});
            skLineSegment(sketch, "E2425", {"start": v(9.33, 15.8) * mm, "end": v(9.2, 15.74) * mm});
            skLineSegment(sketch, "E2426", {"start": v(9.2, 15.74) * mm, "end": v(9.06, 15.68) * mm});
            skLineSegment(sketch, "E2427", {"start": v(9.06, 15.68) * mm, "end": v(8.92, 15.61) * mm});
            skLineSegment(sketch, "E2428", {"start": v(8.92, 15.61) * mm, "end": v(8.78, 15.54) * mm});
            skLineSegment(sketch, "E2429", {"start": v(8.78, 15.54) * mm, "end": v(8.64, 15.45) * mm});
            skLineSegment(sketch, "E2430", {"start": v(8.64, 15.45) * mm, "end": v(8.49, 15.36) * mm});
            skLineSegment(sketch, "E2431", {"start": v(8.49, 15.36) * mm, "end": v(8.33, 15.26) * mm});
            skLineSegment(sketch, "E2432", {"start": v(8.33, 15.26) * mm, "end": v(8.18, 15.15) * mm});
            skLineSegment(sketch, "E2433", {"start": v(8.18, 15.15) * mm, "end": v(8.01, 15.03) * mm});
            skLineSegment(sketch, "E2434", {"start": v(8.01, 15.03) * mm, "end": v(7.85, 14.9) * mm});
            skLineSegment(sketch, "E2435", {"start": v(7.85, 14.9) * mm, "end": v(7.52, 14.64) * mm});
            skLineSegment(sketch, "E2436", {"start": v(7.52, 14.64) * mm, "end": v(7.2, 14.36) * mm});
            skLineSegment(sketch, "E2437", {"start": v(7.2, 14.36) * mm, "end": v(6.9, 14.07) * mm});
            skLineSegment(sketch, "E2438", {"start": v(6.9, 14.07) * mm, "end": v(6.61, 13.76) * mm});
            skLineSegment(sketch, "E2439", {"start": v(6.61, 13.76) * mm, "end": v(6.33, 13.43) * mm});
            skLineSegment(sketch, "E2440", {"start": v(6.33, 13.43) * mm, "end": v(6.06, 13.08) * mm});
            skLineSegment(sketch, "E2441", {"start": v(6.06, 13.08) * mm, "end": v(5.8, 12.71) * mm});
            skLineSegment(sketch, "E2442", {"start": v(5.8, 12.71) * mm, "end": v(5.55, 12.33) * mm});
            skLineSegment(sketch, "E2443", {"start": v(5.55, 12.33) * mm, "end": v(5.33, 11.95) * mm});
            skLineSegment(sketch, "E2444", {"start": v(5.33, 11.95) * mm, "end": v(5.14, 11.56) * mm});
            skLineSegment(sketch, "E2445", {"start": v(5.14, 11.56) * mm, "end": v(4.97, 11.17) * mm});
            skLineSegment(sketch, "E2446", {"start": v(4.97, 11.17) * mm, "end": v(4.84, 10.79) * mm});
            skLineSegment(sketch, "E2447", {"start": v(4.84, 10.79) * mm, "end": v(4.73, 10.4) * mm});
            skLineSegment(sketch, "E2448", {"start": v(4.73, 10.4) * mm, "end": v(4.66, 10) * mm});
            skLineSegment(sketch, "E2449", {"start": v(4.66, 10) * mm, "end": v(4.62, 9.62) * mm});
            skLineSegment(sketch, "E2450", {"start": v(4.62, 9.62) * mm, "end": v(4.6, 9.23) * mm});
            skLineSegment(sketch, "E2451", {"start": v(1.75, 2.92) * mm, "end": v(1, 2.37) * mm});
            skLineSegment(sketch, "E2452", {"start": v(1, 2.37) * mm, "end": v(0.28, 1.8) * mm});
            skLineSegment(sketch, "E2453", {"start": v(0.28, 1.8) * mm, "end": v(-0.4, 1.21) * mm});
            skLineSegment(sketch, "E2454", {"start": v(-0.4, 1.21) * mm, "end": v(-1.03, 0.6) * mm});
            skLineSegment(sketch, "E2455", {"start": v(-1.03, 0.6) * mm, "end": v(-1.6, -0.02) * mm});
            skLineSegment(sketch, "E2456", {"start": v(-1.6, -0.02) * mm, "end": v(-2.11, -0.63) * mm});
            skLineSegment(sketch, "E2457", {"start": v(-2.11, -0.63) * mm, "end": v(-2.56, -1.23) * mm});
            skLineSegment(sketch, "E2458", {"start": v(-2.56, -1.23) * mm, "end": v(-2.95, -1.82) * mm});
            skLineSegment(sketch, "E2459", {"start": v(-2.95, -1.82) * mm, "end": v(-3.11, -2.1) * mm});
            skLineSegment(sketch, "E2460", {"start": v(-3.11, -2.1) * mm, "end": v(-3.26, -2.38) * mm});
            skLineSegment(sketch, "E2461", {"start": v(-3.26, -2.38) * mm, "end": v(-3.38, -2.64) * mm});
            skLineSegment(sketch, "E2462", {"start": v(-3.38, -2.64) * mm, "end": v(-3.43, -2.77) * mm});
            skLineSegment(sketch, "E2463", {"start": v(-3.43, -2.77) * mm, "end": v(-3.47, -2.9) * mm});
            skLineSegment(sketch, "E2464", {"start": v(-3.47, -2.9) * mm, "end": v(-3.51, -3.01) * mm});
            skLineSegment(sketch, "E2465", {"start": v(-3.51, -3.01) * mm, "end": v(-3.55, -3.13) * mm});
            skLineSegment(sketch, "E2466", {"start": v(-3.55, -3.13) * mm, "end": v(-3.58, -3.24) * mm});
            skLineSegment(sketch, "E2467", {"start": v(-3.58, -3.24) * mm, "end": v(-3.6, -3.35) * mm});
            skLineSegment(sketch, "E2468", {"start": v(-3.6, -3.35) * mm, "end": v(-3.62, -3.46) * mm});
            skLineSegment(sketch, "E2469", {"start": v(-3.62, -3.46) * mm, "end": v(-3.64, -3.56) * mm});
            skLineSegment(sketch, "E2470", {"start": v(-3.64, -3.56) * mm, "end": v(-3.65, -3.67) * mm});
            skLineSegment(sketch, "E2471", {"start": v(-3.65, -3.67) * mm, "end": v(-3.65, -3.77) * mm});
            skLineSegment(sketch, "E2472", {"start": v(-3.65, -3.77) * mm, "end": v(-3.64, -3.95) * mm});
            skLineSegment(sketch, "E2473", {"start": v(-3.64, -3.95) * mm, "end": v(-3.64, -4.04) * mm});
            skLineSegment(sketch, "E2474", {"start": v(-3.64, -4.04) * mm, "end": v(-3.63, -4.13) * mm});
            skLineSegment(sketch, "E2475", {"start": v(-3.63, -4.13) * mm, "end": v(-3.61, -4.22) * mm});
            skLineSegment(sketch, "E2476", {"start": v(-3.61, -4.22) * mm, "end": v(-3.6, -4.3) * mm});
            skLineSegment(sketch, "E2477", {"start": v(-3.6, -4.3) * mm, "end": v(-3.58, -4.37) * mm});
            skLineSegment(sketch, "E2478", {"start": v(-3.58, -4.37) * mm, "end": v(-3.56, -4.45) * mm});
            skLineSegment(sketch, "E2479", {"start": v(-3.56, -4.45) * mm, "end": v(-3.54, -4.52) * mm});
            skLineSegment(sketch, "E2480", {"start": v(-3.54, -4.52) * mm, "end": v(-3.5, -4.59) * mm});
            skLineSegment(sketch, "E2481", {"start": v(-3.5, -4.59) * mm, "end": v(-3.48, -4.65) * mm});
            skLineSegment(sketch, "E2482", {"start": v(-3.48, -4.65) * mm, "end": v(-3.45, -4.72) * mm});
            skLineSegment(sketch, "E2483", {"start": v(-3.45, -4.72) * mm, "end": v(-3.41, -4.78) * mm});
            skLineSegment(sketch, "E2484", {"start": v(-3.41, -4.78) * mm, "end": v(-3.38, -4.83) * mm});
            skLineSegment(sketch, "E2485", {"start": v(-3.38, -4.83) * mm, "end": v(-3.34, -4.89) * mm});
            skLineSegment(sketch, "E2486", {"start": v(-3.34, -4.89) * mm, "end": v(-3.3, -4.94) * mm});
            skLineSegment(sketch, "E2487", {"start": v(-3.3, -4.94) * mm, "end": v(-3.25, -4.98) * mm});
            skLineSegment(sketch, "E2488", {"start": v(-3.25, -4.98) * mm, "end": v(-3.2, -5.03) * mm});
            skLineSegment(sketch, "E2489", {"start": v(-3.2, -5.03) * mm, "end": v(-3.15, -5.07) * mm});
            skLineSegment(sketch, "E2490", {"start": v(-3.15, -5.07) * mm, "end": v(-3.1, -5.1) * mm});
            skLineSegment(sketch, "E2491", {"start": v(-3.1, -5.1) * mm, "end": v(-3.04, -5.14) * mm});
            skLineSegment(sketch, "E2492", {"start": v(-3.04, -5.14) * mm, "end": v(-2.98, -5.17) * mm});
            skLineSegment(sketch, "E2493", {"start": v(-2.98, -5.17) * mm, "end": v(-2.92, -5.2) * mm});
            skLineSegment(sketch, "E2494", {"start": v(-2.92, -5.2) * mm, "end": v(-2.85, -5.23) * mm});
            skLineSegment(sketch, "E2495", {"start": v(-2.85, -5.23) * mm, "end": v(-2.79, -5.25) * mm});
            skLineSegment(sketch, "E2496", {"start": v(-2.79, -5.25) * mm, "end": v(-2.71, -5.27) * mm});
            skLineSegment(sketch, "E2497", {"start": v(-2.71, -5.27) * mm, "end": v(-2.64, -5.29) * mm});
            skLineSegment(sketch, "E2498", {"start": v(-2.64, -5.29) * mm, "end": v(-2.57, -5.3) * mm});
            skLineSegment(sketch, "E2499", {"start": v(-2.57, -5.3) * mm, "end": v(-2.49, -5.31) * mm});
            skLineSegment(sketch, "E2500", {"start": v(-2.49, -5.31) * mm, "end": v(-2.4, -5.32) * mm});
            skLineSegment(sketch, "E2501", {"start": v(-2.4, -5.32) * mm, "end": v(-2.32, -5.33) * mm});
            skLineSegment(sketch, "E2502", {"start": v(-2.32, -5.33) * mm, "end": v(-2.23, -5.33) * mm});
            skLineSegment(sketch, "E2503", {"start": v(-2.23, -5.33) * mm, "end": v(-2.1, -5.32) * mm});
            skLineSegment(sketch, "E2504", {"start": v(-2.1, -5.32) * mm, "end": v(-1.96, -5.32) * mm});
            skLineSegment(sketch, "E2505", {"start": v(-1.96, -5.32) * mm, "end": v(-1.82, -5.3) * mm});
            skLineSegment(sketch, "E2506", {"start": v(-1.82, -5.3) * mm, "end": v(-1.67, -5.28) * mm});
            skLineSegment(sketch, "E2507", {"start": v(-1.67, -5.28) * mm, "end": v(-1.52, -5.26) * mm});
            skLineSegment(sketch, "E2508", {"start": v(-1.52, -5.26) * mm, "end": v(-1.36, -5.23) * mm});
            skLineSegment(sketch, "E2509", {"start": v(-1.36, -5.23) * mm, "end": v(-1.19, -5.2) * mm});
            skLineSegment(sketch, "E2510", {"start": v(-1.19, -5.2) * mm, "end": v(-0.84, -5.11) * mm});
            skLineSegment(sketch, "E2511", {"start": v(-0.84, -5.11) * mm, "end": v(-0.46, -5) * mm});
            skLineSegment(sketch, "E2512", {"start": v(-0.46, -5) * mm, "end": v(-0.07, -4.88) * mm});
            skLineSegment(sketch, "E2513", {"start": v(-0.07, -4.88) * mm, "end": v(0.35, -4.73) * mm});
            skLineSegment(sketch, "E2514", {"start": v(0.35, -4.73) * mm, "end": v(0.57, -4.65) * mm});
            skLineSegment(sketch, "E2515", {"start": v(0.57, -4.65) * mm, "end": v(1.46, -4.27) * mm});
            skLineSegment(sketch, "E2516", {"start": v(1.46, -4.27) * mm, "end": v(2.34, -3.8) * mm});
            skLineSegment(sketch, "E2517", {"start": v(2.34, -3.8) * mm, "end": v(3.23, -3.26) * mm});
            skLineSegment(sketch, "E2518", {"start": v(3.23, -3.26) * mm, "end": v(4.12, -2.65) * mm});
            skLineSegment(sketch, "E2519", {"start": v(4.12, -2.65) * mm, "end": v(3.88, -2.09) * mm});
            skLineSegment(sketch, "E2520", {"start": v(3.88, -2.09) * mm, "end": v(3.62, -1.5) * mm});
            skLineSegment(sketch, "E2521", {"start": v(3.62, -1.5) * mm, "end": v(3.35, -0.86) * mm});
            skLineSegment(sketch, "E2522", {"start": v(3.35, -0.86) * mm, "end": v(3.06, -0.18) * mm});
            skLineSegment(sketch, "E2523", {"start": v(3.06, -0.18) * mm, "end": v(2.76, 0.54) * mm});
            skLineSegment(sketch, "E2524", {"start": v(2.76, 0.54) * mm, "end": v(2.44, 1.3) * mm});
            skLineSegment(sketch, "E2525", {"start": v(2.44, 1.3) * mm, "end": v(2.1, 2.09) * mm});
            skLineSegment(sketch, "E2526", {"start": v(2.1, 2.09) * mm, "end": v(1.75, 2.92) * mm});
            skLineSegment(sketch, "E2527", {"start": v(39, -0.43) * mm, "end": v(42.2, -0.43) * mm});
            skLineSegment(sketch, "E2528", {"start": v(42.2, -0.43) * mm, "end": v(42.87, 0.48) * mm});
            skLineSegment(sketch, "E2529", {"start": v(42.87, 0.48) * mm, "end": v(43.5, 1.36) * mm});
            skLineSegment(sketch, "E2530", {"start": v(43.5, 1.36) * mm, "end": v(44.08, 2.22) * mm});
            skLineSegment(sketch, "E2531", {"start": v(44.08, 2.22) * mm, "end": v(44.63, 3.04) * mm});
            skLineSegment(sketch, "E2532", {"start": v(44.63, 3.04) * mm, "end": v(45.13, 3.84) * mm});
            skLineSegment(sketch, "E2533", {"start": v(45.13, 3.84) * mm, "end": v(45.6, 4.6) * mm});
            skLineSegment(sketch, "E2534", {"start": v(45.6, 4.6) * mm, "end": v(46.01, 5.34) * mm});
            skLineSegment(sketch, "E2535", {"start": v(46.01, 5.34) * mm, "end": v(46.4, 6.04) * mm});
            skLineSegment(sketch, "E2536", {"start": v(46.4, 6.04) * mm, "end": v(46.57, 6.38) * mm});
            skLineSegment(sketch, "E2537", {"start": v(46.57, 6.38) * mm, "end": v(46.73, 6.7) * mm});
            skLineSegment(sketch, "E2538", {"start": v(46.73, 6.7) * mm, "end": v(46.89, 7.01) * mm});
            skLineSegment(sketch, "E2539", {"start": v(46.89, 7.01) * mm, "end": v(47.03, 7.3) * mm});
            skLineSegment(sketch, "E2540", {"start": v(47.03, 7.3) * mm, "end": v(47.16, 7.59) * mm});
            skLineSegment(sketch, "E2541", {"start": v(47.16, 7.59) * mm, "end": v(47.28, 7.85) * mm});
            skLineSegment(sketch, "E2542", {"start": v(47.28, 7.85) * mm, "end": v(47.39, 8.1) * mm});
            skLineSegment(sketch, "E2543", {"start": v(47.39, 8.1) * mm, "end": v(47.48, 8.33) * mm});
            skLineSegment(sketch, "E2544", {"start": v(47.48, 8.33) * mm, "end": v(47.57, 8.55) * mm});
            skLineSegment(sketch, "E2545", {"start": v(47.57, 8.55) * mm, "end": v(47.64, 8.76) * mm});
            skLineSegment(sketch, "E2546", {"start": v(47.64, 8.76) * mm, "end": v(47.68, 8.85) * mm});
            skLineSegment(sketch, "E2547", {"start": v(47.68, 8.85) * mm, "end": v(47.7, 8.95) * mm});
            skLineSegment(sketch, "E2548", {"start": v(47.7, 8.95) * mm, "end": v(47.73, 9.04) * mm});
            skLineSegment(sketch, "E2549", {"start": v(47.73, 9.04) * mm, "end": v(47.76, 9.12) * mm});
            skLineSegment(sketch, "E2550", {"start": v(47.76, 9.12) * mm, "end": v(47.78, 9.2) * mm});
            skLineSegment(sketch, "E2551", {"start": v(47.78, 9.2) * mm, "end": v(47.8, 9.28) * mm});
            skLineSegment(sketch, "E2552", {"start": v(47.8, 9.28) * mm, "end": v(47.81, 9.36) * mm});
            skLineSegment(sketch, "E2553", {"start": v(47.81, 9.36) * mm, "end": v(47.83, 9.43) * mm});
            skLineSegment(sketch, "E2554", {"start": v(47.83, 9.43) * mm, "end": v(47.84, 9.5) * mm});
            skLineSegment(sketch, "E2555", {"start": v(47.84, 9.5) * mm, "end": v(47.84, 9.56) * mm});
            skLineSegment(sketch, "E2556", {"start": v(47.84, 9.56) * mm, "end": v(47.85, 9.62) * mm});
            skLineSegment(sketch, "E2557", {"start": v(47.85, 9.62) * mm, "end": v(47.85, 9.67) * mm});
            skLineSegment(sketch, "E2558", {"start": v(47.85, 9.67) * mm, "end": v(47.85, 9.75) * mm});
            skLineSegment(sketch, "E2559", {"start": v(47.85, 9.75) * mm, "end": v(47.84, 9.82) * mm});
            skLineSegment(sketch, "E2560", {"start": v(47.84, 9.82) * mm, "end": v(47.83, 9.89) * mm});
            skLineSegment(sketch, "E2561", {"start": v(47.83, 9.89) * mm, "end": v(47.82, 9.95) * mm});
            skLineSegment(sketch, "E2562", {"start": v(47.82, 9.95) * mm, "end": v(47.8, 10.02) * mm});
            skLineSegment(sketch, "E2563", {"start": v(47.8, 10.02) * mm, "end": v(47.78, 10.08) * mm});
            skLineSegment(sketch, "E2564", {"start": v(47.78, 10.08) * mm, "end": v(47.75, 10.14) * mm});
            skLineSegment(sketch, "E2565", {"start": v(47.75, 10.14) * mm, "end": v(47.72, 10.2) * mm});
            skLineSegment(sketch, "E2566", {"start": v(47.72, 10.2) * mm, "end": v(47.69, 10.25) * mm});
            skLineSegment(sketch, "E2567", {"start": v(47.69, 10.25) * mm, "end": v(47.65, 10.3) * mm});
            skLineSegment(sketch, "E2568", {"start": v(47.65, 10.3) * mm, "end": v(47.6, 10.36) * mm});
            skLineSegment(sketch, "E2569", {"start": v(47.6, 10.36) * mm, "end": v(47.56, 10.4) * mm});
            skLineSegment(sketch, "E2570", {"start": v(47.56, 10.4) * mm, "end": v(47.5, 10.45) * mm});
            skLineSegment(sketch, "E2571", {"start": v(47.5, 10.45) * mm, "end": v(47.45, 10.5) * mm});
            skLineSegment(sketch, "E2572", {"start": v(47.45, 10.5) * mm, "end": v(47.4, 10.54) * mm});
            skLineSegment(sketch, "E2573", {"start": v(47.4, 10.54) * mm, "end": v(47.33, 10.57) * mm});
            skLineSegment(sketch, "E2574", {"start": v(47.33, 10.57) * mm, "end": v(47.27, 10.61) * mm});
            skLineSegment(sketch, "E2575", {"start": v(47.27, 10.61) * mm, "end": v(47.2, 10.65) * mm});
            skLineSegment(sketch, "E2576", {"start": v(47.2, 10.65) * mm, "end": v(47.12, 10.68) * mm});
            skLineSegment(sketch, "E2577", {"start": v(47.12, 10.68) * mm, "end": v(47.04, 10.7) * mm});
            skLineSegment(sketch, "E2578", {"start": v(47.04, 10.7) * mm, "end": v(46.96, 10.73) * mm});
            skLineSegment(sketch, "E2579", {"start": v(46.96, 10.73) * mm, "end": v(46.87, 10.76) * mm});
            skLineSegment(sketch, "E2580", {"start": v(46.87, 10.76) * mm, "end": v(46.78, 10.78) * mm});
            skLineSegment(sketch, "E2581", {"start": v(46.78, 10.78) * mm, "end": v(46.69, 10.8) * mm});
            skLineSegment(sketch, "E2582", {"start": v(46.69, 10.8) * mm, "end": v(46.59, 10.82) * mm});
            skLineSegment(sketch, "E2583", {"start": v(46.59, 10.82) * mm, "end": v(46.48, 10.83) * mm});
            skLineSegment(sketch, "E2584", {"start": v(46.48, 10.83) * mm, "end": v(46.27, 10.86) * mm});
            skLineSegment(sketch, "E2585", {"start": v(46.27, 10.86) * mm, "end": v(46.03, 10.87) * mm});
            skLineSegment(sketch, "E2586", {"start": v(46.03, 10.87) * mm, "end": v(45.78, 10.88) * mm});
            skLineSegment(sketch, "E2587", {"start": v(45.78, 10.88) * mm, "end": v(45.7, 10.87) * mm});
            skLineSegment(sketch, "E2588", {"start": v(45.7, 10.87) * mm, "end": v(45.62, 10.86) * mm});
            skLineSegment(sketch, "E2589", {"start": v(45.62, 10.86) * mm, "end": v(45.45, 10.84) * mm});
            skLineSegment(sketch, "E2590", {"start": v(45.45, 10.84) * mm, "end": v(45.27, 10.82) * mm});
            skLineSegment(sketch, "E2591", {"start": v(45.27, 10.82) * mm, "end": v(45.06, 10.8) * mm});
            skLineSegment(sketch, "E2592", {"start": v(45.06, 10.8) * mm, "end": v(44.85, 10.78) * mm});
            skLineSegment(sketch, "E2593", {"start": v(44.85, 10.78) * mm, "end": v(44.62, 10.75) * mm});
            skLineSegment(sketch, "E2594", {"start": v(44.62, 10.75) * mm, "end": v(44.37, 10.72) * mm});
            skLineSegment(sketch, "E2595", {"start": v(44.37, 10.72) * mm, "end": v(44.11, 10.7) * mm});
            skLineSegment(sketch, "E2596", {"start": v(44.11, 10.7) * mm, "end": v(43.84, 10.66) * mm});
            skLineSegment(sketch, "E2597", {"start": v(43.84, 10.66) * mm, "end": v(43.55, 10.62) * mm});
            skLineSegment(sketch, "E2598", {"start": v(43.55, 10.62) * mm, "end": v(43.25, 10.58) * mm});
            skLineSegment(sketch, "E2599", {"start": v(43.25, 10.58) * mm, "end": v(42.93, 10.54) * mm});
            skLineSegment(sketch, "E2600", {"start": v(42.93, 10.54) * mm, "end": v(42.26, 10.45) * mm});
            skLineSegment(sketch, "E2601", {"start": v(42.26, 10.45) * mm, "end": v(41.52, 10.35) * mm});
            skLineSegment(sketch, "E2602", {"start": v(41.52, 10.35) * mm, "end": v(40, 10.14) * mm});
            skLineSegment(sketch, "E2603", {"start": v(40, 10.14) * mm, "end": v(37.04, 9.65) * mm});
            skLineSegment(sketch, "E2604", {"start": v(37.04, 9.65) * mm, "end": v(35.6, 9.38) * mm});
            skLineSegment(sketch, "E2605", {"start": v(35.6, 9.38) * mm, "end": v(34.96, 9.26) * mm});
            skLineSegment(sketch, "E2606", {"start": v(34.96, 9.26) * mm, "end": v(34.37, 9.13) * mm});
            skLineSegment(sketch, "E2607", {"start": v(34.37, 9.13) * mm, "end": v(33.8, 9) * mm});
            skLineSegment(sketch, "E2608", {"start": v(33.8, 9) * mm, "end": v(33.27, 8.88) * mm});
            skLineSegment(sketch, "E2609", {"start": v(33.27, 8.88) * mm, "end": v(32.77, 8.75) * mm});
            skLineSegment(sketch, "E2610", {"start": v(32.77, 8.75) * mm, "end": v(32.3, 8.63) * mm});
            skLineSegment(sketch, "E2611", {"start": v(32.3, 8.63) * mm, "end": v(31.86, 8.5) * mm});
            skLineSegment(sketch, "E2612", {"start": v(31.86, 8.5) * mm, "end": v(31.46, 8.36) * mm});
            skLineSegment(sketch, "E2613", {"start": v(31.46, 8.36) * mm, "end": v(31.09, 8.24) * mm});
            skLineSegment(sketch, "E2614", {"start": v(31.09, 8.24) * mm, "end": v(30.74, 8.12) * mm});
            skLineSegment(sketch, "E2615", {"start": v(30.74, 8.12) * mm, "end": v(30.43, 8) * mm});
            skLineSegment(sketch, "E2616", {"start": v(30.43, 8) * mm, "end": v(30.28, 7.95) * mm});
            skLineSegment(sketch, "E2617", {"start": v(30.28, 7.95) * mm, "end": v(30.14, 7.9) * mm});
            skLineSegment(sketch, "E2618", {"start": v(30.14, 7.9) * mm, "end": v(30.01, 7.85) * mm});
            skLineSegment(sketch, "E2619", {"start": v(30.01, 7.85) * mm, "end": v(29.89, 7.8) * mm});
            skLineSegment(sketch, "E2620", {"start": v(29.89, 7.8) * mm, "end": v(29.77, 7.75) * mm});
            skLineSegment(sketch, "E2621", {"start": v(29.77, 7.75) * mm, "end": v(29.66, 7.7) * mm});
            skLineSegment(sketch, "E2622", {"start": v(29.66, 7.7) * mm, "end": v(29.55, 7.65) * mm});
            skLineSegment(sketch, "E2623", {"start": v(29.55, 7.65) * mm, "end": v(29.46, 7.6) * mm});
            skLineSegment(sketch, "E2624", {"start": v(29.46, 7.6) * mm, "end": v(29.37, 7.56) * mm});
            skLineSegment(sketch, "E2625", {"start": v(29.37, 7.56) * mm, "end": v(29.28, 7.52) * mm});
            skLineSegment(sketch, "E2626", {"start": v(29.28, 7.52) * mm, "end": v(29.2, 7.48) * mm});
            skLineSegment(sketch, "E2627", {"start": v(29.2, 7.48) * mm, "end": v(29.13, 7.44) * mm});
            skLineSegment(sketch, "E2628", {"start": v(29.13, 7.44) * mm, "end": v(29.06, 7.4) * mm});
            skLineSegment(sketch, "E2629", {"start": v(29.06, 7.4) * mm, "end": v(29, 7.36) * mm});
            skLineSegment(sketch, "E2630", {"start": v(29, 7.36) * mm, "end": v(28.94, 7.33) * mm});
            skLineSegment(sketch, "E2631", {"start": v(28.94, 7.33) * mm, "end": v(28.88, 7.3) * mm});
            skLineSegment(sketch, "E2632", {"start": v(28.88, 7.3) * mm, "end": v(28.82, 7.26) * mm});
            skLineSegment(sketch, "E2633", {"start": v(28.82, 7.26) * mm, "end": v(28.77, 7.23) * mm});
            skLineSegment(sketch, "E2634", {"start": v(28.77, 7.23) * mm, "end": v(28.72, 7.2) * mm});
            skLineSegment(sketch, "E2635", {"start": v(28.72, 7.2) * mm, "end": v(28.68, 7.17) * mm});
            skLineSegment(sketch, "E2636", {"start": v(28.68, 7.17) * mm, "end": v(28.64, 7.15) * mm});
            skLineSegment(sketch, "E2637", {"start": v(28.64, 7.15) * mm, "end": v(28.62, 7.13) * mm});
            skLineSegment(sketch, "E2638", {"start": v(28.62, 7.13) * mm, "end": v(28.6, 7.12) * mm});
            skLineSegment(sketch, "E2639", {"start": v(28.6, 7.12) * mm, "end": v(28.6, 7.1) * mm});
            skLineSegment(sketch, "E2640", {"start": v(28.6, 7.1) * mm, "end": v(28.58, 7.1) * mm});
            skLineSegment(sketch, "E2641", {"start": v(28.58, 7.1) * mm, "end": v(28.56, 7.09) * mm});
            skLineSegment(sketch, "E2642", {"start": v(28.56, 7.09) * mm, "end": v(28.55, 7.08) * mm});
            skLineSegment(sketch, "E2643", {"start": v(28.55, 7.08) * mm, "end": v(28.53, 7.07) * mm});
            skLineSegment(sketch, "E2644", {"start": v(28.53, 7.07) * mm, "end": v(28.52, 7.06) * mm});
            skLineSegment(sketch, "E2645", {"start": v(28.52, 7.06) * mm, "end": v(28.51, 7.05) * mm});
            skLineSegment(sketch, "E2646", {"start": v(28.51, 7.05) * mm, "end": v(28.5, 7.04) * mm});
            skLineSegment(sketch, "E2647", {"start": v(28.5, 7.04) * mm, "end": v(29.25, 7.07) * mm});
            skLineSegment(sketch, "E2648", {"start": v(29.25, 7.07) * mm, "end": v(29.6, 7.09) * mm});
            skLineSegment(sketch, "E2649", {"start": v(29.6, 7.09) * mm, "end": v(29.94, 7.1) * mm});
            skLineSegment(sketch, "E2650", {"start": v(29.94, 7.1) * mm, "end": v(30.26, 7.1) * mm});
            skLineSegment(sketch, "E2651", {"start": v(30.26, 7.1) * mm, "end": v(30.57, 7.11) * mm});
            skLineSegment(sketch, "E2652", {"start": v(30.57, 7.11) * mm, "end": v(30.86, 7.12) * mm});
            skLineSegment(sketch, "E2653", {"start": v(30.86, 7.12) * mm, "end": v(31.14, 7.12) * mm});
            skLineSegment(sketch, "E2654", {"start": v(31.14, 7.12) * mm, "end": v(31.34, 7.12) * mm});
            skLineSegment(sketch, "E2655", {"start": v(31.34, 7.12) * mm, "end": v(31.54, 7.11) * mm});
            skLineSegment(sketch, "E2656", {"start": v(31.54, 7.11) * mm, "end": v(31.71, 7.1) * mm});
            skLineSegment(sketch, "E2657", {"start": v(31.71, 7.1) * mm, "end": v(31.88, 7.1) * mm});
            skLineSegment(sketch, "E2658", {"start": v(31.88, 7.1) * mm, "end": v(31.96, 7.1) * mm});
            skLineSegment(sketch, "E2659", {"start": v(31.96, 7.1) * mm, "end": v(32.03, 7.08) * mm});
            skLineSegment(sketch, "E2660", {"start": v(32.03, 7.08) * mm, "end": v(32.1, 7.08) * mm});
            skLineSegment(sketch, "E2661", {"start": v(32.1, 7.08) * mm, "end": v(32.17, 7.07) * mm});
            skLineSegment(sketch, "E2662", {"start": v(32.17, 7.07) * mm, "end": v(32.23, 7.06) * mm});
            skLineSegment(sketch, "E2663", {"start": v(32.23, 7.06) * mm, "end": v(32.3, 7.05) * mm});
            skLineSegment(sketch, "E2664", {"start": v(32.3, 7.05) * mm, "end": v(32.35, 7.04) * mm});
            skLineSegment(sketch, "E2665", {"start": v(32.35, 7.04) * mm, "end": v(32.4, 7.03) * mm});
            skLineSegment(sketch, "E2666", {"start": v(32.4, 7.03) * mm, "end": v(32.46, 7.01) * mm});
            skLineSegment(sketch, "E2667", {"start": v(32.46, 7.01) * mm, "end": v(32.5, 7) * mm});
            skLineSegment(sketch, "E2668", {"start": v(32.5, 7) * mm, "end": v(32.55, 6.99) * mm});
            skLineSegment(sketch, "E2669", {"start": v(32.55, 6.99) * mm, "end": v(32.6, 6.97) * mm});
            skLineSegment(sketch, "E2670", {"start": v(32.6, 6.97) * mm, "end": v(32.63, 6.96) * mm});
            skLineSegment(sketch, "E2671", {"start": v(32.63, 6.96) * mm, "end": v(32.65, 6.95) * mm});
            skLineSegment(sketch, "E2672", {"start": v(32.65, 6.95) * mm, "end": v(32.66, 6.94) * mm});
            skLineSegment(sketch, "E2673", {"start": v(32.66, 6.94) * mm, "end": v(32.68, 6.93) * mm});
            skLineSegment(sketch, "E2674", {"start": v(32.68, 6.93) * mm, "end": v(32.7, 6.92) * mm});
            skLineSegment(sketch, "E2675", {"start": v(32.7, 6.92) * mm, "end": v(32.7, 6.92) * mm});
            skLineSegment(sketch, "E2676", {"start": v(32.7, 6.92) * mm, "end": v(32.72, 6.9) * mm});
            skLineSegment(sketch, "E2677", {"start": v(32.72, 6.9) * mm, "end": v(32.74, 6.9) * mm});
            skLineSegment(sketch, "E2678", {"start": v(32.74, 6.9) * mm, "end": v(32.75, 6.89) * mm});
            skLineSegment(sketch, "E2679", {"start": v(32.75, 6.89) * mm, "end": v(32.76, 6.88) * mm});
            skLineSegment(sketch, "E2680", {"start": v(32.76, 6.88) * mm, "end": v(32.77, 6.87) * mm});
            skLineSegment(sketch, "E2681", {"start": v(32.77, 6.87) * mm, "end": v(32.78, 6.86) * mm});
            skLineSegment(sketch, "E2682", {"start": v(32.78, 6.86) * mm, "end": v(32.79, 6.85) * mm});
            skLineSegment(sketch, "E2683", {"start": v(32.79, 6.85) * mm, "end": v(32.8, 6.84) * mm});
            skLineSegment(sketch, "E2684", {"start": v(32.8, 6.84) * mm, "end": v(32.8, 6.83) * mm});
            skLineSegment(sketch, "E2685", {"start": v(32.8, 6.83) * mm, "end": v(32.8, 6.82) * mm});
            skLineSegment(sketch, "E2686", {"start": v(32.8, 6.82) * mm, "end": v(32.81, 6.8) * mm});
            skLineSegment(sketch, "E2687", {"start": v(32.81, 6.8) * mm, "end": v(32.82, 6.8) * mm});
            skLineSegment(sketch, "E2688", {"start": v(32.82, 6.8) * mm, "end": v(32.82, 6.79) * mm});
            skLineSegment(sketch, "E2689", {"start": v(32.82, 6.79) * mm, "end": v(32.82, 6.78) * mm});
            skLineSegment(sketch, "E2690", {"start": v(32.82, 6.78) * mm, "end": v(32.83, 6.76) * mm});
            skLineSegment(sketch, "E2691", {"start": v(32.83, 6.76) * mm, "end": v(32.83, 6.75) * mm});
            skLineSegment(sketch, "E2692", {"start": v(32.83, 6.75) * mm, "end": v(32.83, 6.74) * mm});
            skLineSegment(sketch, "E2693", {"start": v(32.83, 6.74) * mm, "end": v(32.83, 6.74) * mm});
            skLineSegment(sketch, "E2694", {"start": v(32.83, 6.74) * mm, "end": v(32.83, 6.73) * mm});
            skLineSegment(sketch, "E2695", {"start": v(32.83, 6.73) * mm, "end": v(32.83, 6.73) * mm});
            skLineSegment(sketch, "E2696", {"start": v(32.83, 6.73) * mm, "end": v(32.83, 6.72) * mm});
            skLineSegment(sketch, "E2697", {"start": v(32.83, 6.72) * mm, "end": v(32.82, 6.72) * mm});
            skLineSegment(sketch, "E2698", {"start": v(32.82, 6.72) * mm, "end": v(32.82, 6.72) * mm});
            skLineSegment(sketch, "E2699", {"start": v(32.82, 6.72) * mm, "end": v(32.82, 6.71) * mm});
            skLineSegment(sketch, "E2700", {"start": v(32.82, 6.71) * mm, "end": v(32.82, 6.71) * mm});
            skLineSegment(sketch, "E2701", {"start": v(32.82, 6.71) * mm, "end": v(32.82, 6.7) * mm});
            skLineSegment(sketch, "E2702", {"start": v(32.82, 6.7) * mm, "end": v(32.81, 6.7) * mm});
            skLineSegment(sketch, "E2703", {"start": v(32.81, 6.7) * mm, "end": v(32.8, 6.7) * mm});
            skLineSegment(sketch, "E2704", {"start": v(32.8, 6.7) * mm, "end": v(32.8, 6.7) * mm});
            skLineSegment(sketch, "E2705", {"start": v(32.8, 6.7) * mm, "end": v(32.8, 6.69) * mm});
            skLineSegment(sketch, "E2706", {"start": v(32.8, 6.69) * mm, "end": v(32.8, 6.68) * mm});
            skLineSegment(sketch, "E2707", {"start": v(32.8, 6.68) * mm, "end": v(32.79, 6.67) * mm});
            skLineSegment(sketch, "E2708", {"start": v(32.79, 6.67) * mm, "end": v(32.78, 6.67) * mm});
            skLineSegment(sketch, "E2709", {"start": v(32.78, 6.67) * mm, "end": v(32.77, 6.66) * mm});
            skLineSegment(sketch, "E2710", {"start": v(32.77, 6.66) * mm, "end": v(32.76, 6.66) * mm});
            skLineSegment(sketch, "E2711", {"start": v(32.76, 6.66) * mm, "end": v(32.75, 6.65) * mm});
            skLineSegment(sketch, "E2712", {"start": v(32.75, 6.65) * mm, "end": v(32.74, 6.64) * mm});
            skLineSegment(sketch, "E2713", {"start": v(32.74, 6.64) * mm, "end": v(32.73, 6.64) * mm});
            skLineSegment(sketch, "E2714", {"start": v(32.73, 6.64) * mm, "end": v(32.72, 6.63) * mm});
            skLineSegment(sketch, "E2715", {"start": v(32.72, 6.63) * mm, "end": v(32.71, 6.62) * mm});
            skLineSegment(sketch, "E2716", {"start": v(32.71, 6.62) * mm, "end": v(32.69, 6.61) * mm});
            skLineSegment(sketch, "E2717", {"start": v(32.69, 6.61) * mm, "end": v(32.66, 6.6) * mm});
            skLineSegment(sketch, "E2718", {"start": v(32.66, 6.6) * mm, "end": v(32.63, 6.59) * mm});
            skLineSegment(sketch, "E2719", {"start": v(32.63, 6.59) * mm, "end": v(32.6, 6.57) * mm});
            skLineSegment(sketch, "E2720", {"start": v(32.6, 6.57) * mm, "end": v(32.57, 6.56) * mm});
            skLineSegment(sketch, "E2721", {"start": v(32.57, 6.56) * mm, "end": v(32.53, 6.55) * mm});
            skLineSegment(sketch, "E2722", {"start": v(32.53, 6.55) * mm, "end": v(32.5, 6.53) * mm});
            skLineSegment(sketch, "E2723", {"start": v(32.5, 6.53) * mm, "end": v(32.45, 6.52) * mm});
            skLineSegment(sketch, "E2724", {"start": v(32.45, 6.52) * mm, "end": v(32.41, 6.5) * mm});
            skLineSegment(sketch, "E2725", {"start": v(32.41, 6.5) * mm, "end": v(32.37, 6.49) * mm});
            skLineSegment(sketch, "E2726", {"start": v(32.37, 6.49) * mm, "end": v(32.32, 6.47) * mm});
            skLineSegment(sketch, "E2727", {"start": v(32.32, 6.47) * mm, "end": v(32.27, 6.46) * mm});
            skLineSegment(sketch, "E2728", {"start": v(32.27, 6.46) * mm, "end": v(32.16, 6.43) * mm});
            skLineSegment(sketch, "E2729", {"start": v(32.16, 6.43) * mm, "end": v(32.05, 6.4) * mm});
            skLineSegment(sketch, "E2730", {"start": v(32.05, 6.4) * mm, "end": v(31.92, 6.36) * mm});
            skLineSegment(sketch, "E2731", {"start": v(31.92, 6.36) * mm, "end": v(31.79, 6.33) * mm});
            skLineSegment(sketch, "E2732", {"start": v(31.79, 6.33) * mm, "end": v(31.65, 6.3) * mm});
            skLineSegment(sketch, "E2733", {"start": v(31.65, 6.3) * mm, "end": v(31.06, 6.17) * mm});
            skLineSegment(sketch, "E2734", {"start": v(31.06, 6.17) * mm, "end": v(29.95, 5.9) * mm});
            skLineSegment(sketch, "E2735", {"start": v(29.95, 5.9) * mm, "end": v(29.41, 5.75) * mm});
            skLineSegment(sketch, "E2736", {"start": v(29.41, 5.75) * mm, "end": v(28.9, 5.6) * mm});
            skLineSegment(sketch, "E2737", {"start": v(28.9, 5.6) * mm, "end": v(27.88, 5.25) * mm});
            skLineSegment(sketch, "E2738", {"start": v(27.88, 5.25) * mm, "end": v(27.38, 5.05) * mm});
            skLineSegment(sketch, "E2739", {"start": v(27.38, 5.05) * mm, "end": v(27.27, 5) * mm});
            skLineSegment(sketch, "E2740", {"start": v(27.27, 5) * mm, "end": v(27.15, 4.96) * mm});
            skLineSegment(sketch, "E2741", {"start": v(27.15, 4.96) * mm, "end": v(27.05, 4.92) * mm});
            skLineSegment(sketch, "E2742", {"start": v(27.05, 4.92) * mm, "end": v(26.95, 4.88) * mm});
            skLineSegment(sketch, "E2743", {"start": v(26.95, 4.88) * mm, "end": v(26.85, 4.84) * mm});
            skLineSegment(sketch, "E2744", {"start": v(26.85, 4.84) * mm, "end": v(26.76, 4.8) * mm});
            skLineSegment(sketch, "E2745", {"start": v(26.76, 4.8) * mm, "end": v(26.68, 4.78) * mm});
            skLineSegment(sketch, "E2746", {"start": v(26.68, 4.78) * mm, "end": v(26.6, 4.75) * mm});
            skLineSegment(sketch, "E2747", {"start": v(26.6, 4.75) * mm, "end": v(26.57, 4.74) * mm});
            skLineSegment(sketch, "E2748", {"start": v(26.57, 4.74) * mm, "end": v(26.53, 4.73) * mm});
            skLineSegment(sketch, "E2749", {"start": v(26.53, 4.73) * mm, "end": v(26.5, 4.72) * mm});
            skLineSegment(sketch, "E2750", {"start": v(26.5, 4.72) * mm, "end": v(26.47, 4.7) * mm});
            skLineSegment(sketch, "E2751", {"start": v(26.47, 4.7) * mm, "end": v(26.44, 4.7) * mm});
            skLineSegment(sketch, "E2752", {"start": v(26.44, 4.7) * mm, "end": v(26.4, 4.7) * mm});
            skLineSegment(sketch, "E2753", {"start": v(26.4, 4.7) * mm, "end": v(26.38, 4.68) * mm});
            skLineSegment(sketch, "E2754", {"start": v(26.38, 4.68) * mm, "end": v(26.36, 4.68) * mm});
            skLineSegment(sketch, "E2755", {"start": v(26.36, 4.68) * mm, "end": v(26.33, 4.67) * mm});
            skLineSegment(sketch, "E2756", {"start": v(26.33, 4.67) * mm, "end": v(26.3, 4.67) * mm});
            skLineSegment(sketch, "E2757", {"start": v(26.3, 4.67) * mm, "end": v(26.29, 4.66) * mm});
            skLineSegment(sketch, "E2758", {"start": v(26.29, 4.66) * mm, "end": v(26.27, 4.66) * mm});
            skLineSegment(sketch, "E2759", {"start": v(26.27, 4.66) * mm, "end": v(26.26, 4.66) * mm});
            skLineSegment(sketch, "E2760", {"start": v(26.26, 4.66) * mm, "end": v(26.25, 4.66) * mm});
            skLineSegment(sketch, "E2761", {"start": v(26.25, 4.66) * mm, "end": v(26.24, 4.65) * mm});
            skLineSegment(sketch, "E2762", {"start": v(26.24, 4.65) * mm, "end": v(26.23, 4.65) * mm});
            skLineSegment(sketch, "E2763", {"start": v(26.23, 4.65) * mm, "end": v(26.22, 4.65) * mm});
            skLineSegment(sketch, "E2764", {"start": v(26.22, 4.65) * mm, "end": v(26.22, 4.65) * mm});
            skLineSegment(sketch, "E2765", {"start": v(26.22, 4.65) * mm, "end": v(26.21, 4.65) * mm});
            skLineSegment(sketch, "E2766", {"start": v(26.21, 4.65) * mm, "end": v(26.2, 4.65) * mm});
            skLineSegment(sketch, "E2767", {"start": v(26.2, 4.65) * mm, "end": v(26.14, 4.65) * mm});
            skLineSegment(sketch, "E2768", {"start": v(26.14, 4.65) * mm, "end": v(26.08, 4.66) * mm});
            skLineSegment(sketch, "E2769", {"start": v(26.08, 4.66) * mm, "end": v(26.03, 4.66) * mm});
            skLineSegment(sketch, "E2770", {"start": v(26.03, 4.66) * mm, "end": v(25.97, 4.67) * mm});
            skLineSegment(sketch, "E2771", {"start": v(25.97, 4.67) * mm, "end": v(25.92, 4.69) * mm});
            skLineSegment(sketch, "E2772", {"start": v(25.92, 4.69) * mm, "end": v(25.86, 4.7) * mm});
            skLineSegment(sketch, "E2773", {"start": v(25.86, 4.7) * mm, "end": v(25.81, 4.72) * mm});
            skLineSegment(sketch, "E2774", {"start": v(25.81, 4.72) * mm, "end": v(25.76, 4.74) * mm});
            skLineSegment(sketch, "E2775", {"start": v(25.76, 4.74) * mm, "end": v(25.71, 4.77) * mm});
            skLineSegment(sketch, "E2776", {"start": v(25.71, 4.77) * mm, "end": v(25.66, 4.8) * mm});
            skLineSegment(sketch, "E2777", {"start": v(25.66, 4.8) * mm, "end": v(25.62, 4.82) * mm});
            skLineSegment(sketch, "E2778", {"start": v(25.62, 4.82) * mm, "end": v(25.57, 4.85) * mm});
            skLineSegment(sketch, "E2779", {"start": v(25.57, 4.85) * mm, "end": v(25.53, 4.89) * mm});
            skLineSegment(sketch, "E2780", {"start": v(25.53, 4.89) * mm, "end": v(25.48, 4.93) * mm});
            skLineSegment(sketch, "E2781", {"start": v(25.48, 4.93) * mm, "end": v(25.44, 4.97) * mm});
            skLineSegment(sketch, "E2782", {"start": v(25.44, 4.97) * mm, "end": v(25.4, 5.01) * mm});
            skLineSegment(sketch, "E2783", {"start": v(25.4, 5.01) * mm, "end": v(25.36, 5.06) * mm});
            skLineSegment(sketch, "E2784", {"start": v(25.36, 5.06) * mm, "end": v(25.33, 5.1) * mm});
            skLineSegment(sketch, "E2785", {"start": v(25.33, 5.1) * mm, "end": v(25.3, 5.16) * mm});
            skLineSegment(sketch, "E2786", {"start": v(25.3, 5.16) * mm, "end": v(25.26, 5.2) * mm});
            skLineSegment(sketch, "E2787", {"start": v(25.26, 5.2) * mm, "end": v(25.23, 5.26) * mm});
            skLineSegment(sketch, "E2788", {"start": v(25.23, 5.26) * mm, "end": v(25.2, 5.32) * mm});
            skLineSegment(sketch, "E2789", {"start": v(25.2, 5.32) * mm, "end": v(25.19, 5.37) * mm});
            skLineSegment(sketch, "E2790", {"start": v(25.19, 5.37) * mm, "end": v(25.16, 5.43) * mm});
            skLineSegment(sketch, "E2791", {"start": v(25.16, 5.43) * mm, "end": v(25.15, 5.48) * mm});
            skLineSegment(sketch, "E2792", {"start": v(25.15, 5.48) * mm, "end": v(25.13, 5.54) * mm});
            skLineSegment(sketch, "E2793", {"start": v(25.13, 5.54) * mm, "end": v(25.12, 5.6) * mm});
            skLineSegment(sketch, "E2794", {"start": v(25.12, 5.6) * mm, "end": v(25.1, 5.66) * mm});
            skLineSegment(sketch, "E2795", {"start": v(25.1, 5.66) * mm, "end": v(25.1, 5.79) * mm});
            skLineSegment(sketch, "E2796", {"start": v(25.1, 5.79) * mm, "end": v(25.09, 5.92) * mm});
            skLineSegment(sketch, "E2797", {"start": v(25.09, 5.92) * mm, "end": v(25.09, 5.93) * mm});
            skLineSegment(sketch, "E2798", {"start": v(25.09, 5.93) * mm, "end": v(25.09, 5.94) * mm});
            skLineSegment(sketch, "E2799", {"start": v(25.09, 5.94) * mm, "end": v(25.09, 5.95) * mm});
            skLineSegment(sketch, "E2800", {"start": v(25.09, 5.95) * mm, "end": v(25.09, 5.97) * mm});
            skLineSegment(sketch, "E2801", {"start": v(25.09, 5.97) * mm, "end": v(25.09, 5.98) * mm});
            skLineSegment(sketch, "E2802", {"start": v(25.09, 5.98) * mm, "end": v(25.1, 6) * mm});
            skLineSegment(sketch, "E2803", {"start": v(25.1, 6) * mm, "end": v(25.1, 6.04) * mm});
            skLineSegment(sketch, "E2804", {"start": v(25.1, 6.04) * mm, "end": v(25.1, 6.07) * mm});
            skLineSegment(sketch, "E2805", {"start": v(25.1, 6.07) * mm, "end": v(25.1, 6.11) * mm});
            skLineSegment(sketch, "E2806", {"start": v(25.1, 6.11) * mm, "end": v(25.12, 6.15) * mm});
            skLineSegment(sketch, "E2807", {"start": v(25.12, 6.15) * mm, "end": v(25.13, 6.19) * mm});
            skLineSegment(sketch, "E2808", {"start": v(25.13, 6.19) * mm, "end": v(25.14, 6.23) * mm});
            skLineSegment(sketch, "E2809", {"start": v(25.14, 6.23) * mm, "end": v(25.15, 6.28) * mm});
            skLineSegment(sketch, "E2810", {"start": v(25.15, 6.28) * mm, "end": v(25.16, 6.32) * mm});
            skLineSegment(sketch, "E2811", {"start": v(25.16, 6.32) * mm, "end": v(25.17, 6.37) * mm});
            skLineSegment(sketch, "E2812", {"start": v(25.17, 6.37) * mm, "end": v(25.19, 6.42) * mm});
            skLineSegment(sketch, "E2813", {"start": v(25.19, 6.42) * mm, "end": v(25.2, 6.48) * mm});
            skLineSegment(sketch, "E2814", {"start": v(25.2, 6.48) * mm, "end": v(25.24, 6.6) * mm});
            skLineSegment(sketch, "E2815", {"start": v(25.24, 6.6) * mm, "end": v(25.28, 6.71) * mm});
            skLineSegment(sketch, "E2816", {"start": v(25.28, 6.71) * mm, "end": v(25.32, 6.84) * mm});
            skLineSegment(sketch, "E2817", {"start": v(25.32, 6.84) * mm, "end": v(25.37, 6.99) * mm});
            skLineSegment(sketch, "E2818", {"start": v(25.37, 6.99) * mm, "end": v(25.42, 7.13) * mm});
            skLineSegment(sketch, "E2819", {"start": v(25.42, 7.13) * mm, "end": v(25.48, 7.3) * mm});
            skLineSegment(sketch, "E2820", {"start": v(25.48, 7.3) * mm, "end": v(25.54, 7.46) * mm});
            skLineSegment(sketch, "E2821", {"start": v(25.54, 7.46) * mm, "end": v(25.6, 7.64) * mm});
            skLineSegment(sketch, "E2822", {"start": v(25.6, 7.64) * mm, "end": v(25.65, 7.77) * mm});
            skLineSegment(sketch, "E2823", {"start": v(25.65, 7.77) * mm, "end": v(25.98, 8.53) * mm});
            skLineSegment(sketch, "E2824", {"start": v(25.98, 8.53) * mm, "end": v(26.36, 9.3) * mm});
            skLineSegment(sketch, "E2825", {"start": v(26.36, 9.3) * mm, "end": v(26.8, 10.05) * mm});
            skLineSegment(sketch, "E2826", {"start": v(26.8, 10.05) * mm, "end": v(27.3, 10.81) * mm});
            skLineSegment(sketch, "E2827", {"start": v(27.3, 10.81) * mm, "end": v(27.57, 11.18) * mm});
            skLineSegment(sketch, "E2828", {"start": v(27.57, 11.18) * mm, "end": v(27.86, 11.53) * mm});
            skLineSegment(sketch, "E2829", {"start": v(27.86, 11.53) * mm, "end": v(28.16, 11.85) * mm});
            skLineSegment(sketch, "E2830", {"start": v(28.16, 11.85) * mm, "end": v(28.48, 12.15) * mm});
            skLineSegment(sketch, "E2831", {"start": v(28.48, 12.15) * mm, "end": v(28.82, 12.42) * mm});
            skLineSegment(sketch, "E2832", {"start": v(28.82, 12.42) * mm, "end": v(29.17, 12.67) * mm});
            skLineSegment(sketch, "E2833", {"start": v(29.17, 12.67) * mm, "end": v(29.53, 12.9) * mm});
            skLineSegment(sketch, "E2834", {"start": v(29.53, 12.9) * mm, "end": v(29.92, 13.1) * mm});
            skLineSegment(sketch, "E2835", {"start": v(29.92, 13.1) * mm, "end": v(29.93, 13.1) * mm});
            skLineSegment(sketch, "E2836", {"start": v(29.93, 13.1) * mm, "end": v(29.95, 13.1) * mm});
            skLineSegment(sketch, "E2837", {"start": v(29.95, 13.1) * mm, "end": v(29.98, 13.12) * mm});
            skLineSegment(sketch, "E2838", {"start": v(29.98, 13.12) * mm, "end": v(30, 13.13) * mm});
            skLineSegment(sketch, "E2839", {"start": v(30, 13.13) * mm, "end": v(30.02, 13.14) * mm});
            skLineSegment(sketch, "E2840", {"start": v(30.02, 13.14) * mm, "end": v(30.05, 13.15) * mm});
            skLineSegment(sketch, "E2841", {"start": v(30.05, 13.15) * mm, "end": v(30.07, 13.16) * mm});
            skLineSegment(sketch, "E2842", {"start": v(30.07, 13.16) * mm, "end": v(30.13, 13.18) * mm});
            skLineSegment(sketch, "E2843", {"start": v(30.13, 13.18) * mm, "end": v(30.19, 13.2) * mm});
            skLineSegment(sketch, "E2844", {"start": v(30.19, 13.2) * mm, "end": v(30.25, 13.22) * mm});
            skLineSegment(sketch, "E2845", {"start": v(30.25, 13.22) * mm, "end": v(30.32, 13.24) * mm});
            skLineSegment(sketch, "E2846", {"start": v(30.32, 13.24) * mm, "end": v(30.4, 13.27) * mm});
            skLineSegment(sketch, "E2847", {"start": v(30.4, 13.27) * mm, "end": v(30.47, 13.3) * mm});
            skLineSegment(sketch, "E2848", {"start": v(30.47, 13.3) * mm, "end": v(30.56, 13.32) * mm});
            skLineSegment(sketch, "E2849", {"start": v(30.56, 13.32) * mm, "end": v(30.65, 13.35) * mm});
            skLineSegment(sketch, "E2850", {"start": v(30.65, 13.35) * mm, "end": v(30.74, 13.37) * mm});
            skLineSegment(sketch, "E2851", {"start": v(30.74, 13.37) * mm, "end": v(30.84, 13.4) * mm});
            skLineSegment(sketch, "E2852", {"start": v(30.84, 13.4) * mm, "end": v(30.94, 13.43) * mm});
            skLineSegment(sketch, "E2853", {"start": v(30.94, 13.43) * mm, "end": v(31.17, 13.5) * mm});
            skLineSegment(sketch, "E2854", {"start": v(31.17, 13.5) * mm, "end": v(31.4, 13.56) * mm});
            skLineSegment(sketch, "E2855", {"start": v(31.4, 13.56) * mm, "end": v(31.67, 13.62) * mm});
            skLineSegment(sketch, "E2856", {"start": v(31.67, 13.62) * mm, "end": v(31.95, 13.7) * mm});
            skLineSegment(sketch, "E2857", {"start": v(31.95, 13.7) * mm, "end": v(32.25, 13.77) * mm});
            skLineSegment(sketch, "E2858", {"start": v(32.25, 13.77) * mm, "end": v(32.57, 13.85) * mm});
            skLineSegment(sketch, "E2859", {"start": v(32.57, 13.85) * mm, "end": v(32.9, 13.93) * mm});
            skLineSegment(sketch, "E2860", {"start": v(32.9, 13.93) * mm, "end": v(33.26, 14.02) * mm});
            skLineSegment(sketch, "E2861", {"start": v(33.26, 14.02) * mm, "end": v(33.55, 14.08) * mm});
            skLineSegment(sketch, "E2862", {"start": v(33.55, 14.08) * mm, "end": v(35.13, 14.43) * mm});
            skLineSegment(sketch, "E2863", {"start": v(35.13, 14.43) * mm, "end": v(36.82, 14.77) * mm});
            skLineSegment(sketch, "E2864", {"start": v(36.82, 14.77) * mm, "end": v(38.6, 15.09) * mm});
            skLineSegment(sketch, "E2865", {"start": v(38.6, 15.09) * mm, "end": v(40.49, 15.4) * mm});
            skLineSegment(sketch, "E2866", {"start": v(40.49, 15.4) * mm, "end": v(42.38, 15.65) * mm});
            skLineSegment(sketch, "E2867", {"start": v(42.38, 15.65) * mm, "end": v(44.18, 15.83) * mm});
            skLineSegment(sketch, "E2868", {"start": v(44.18, 15.83) * mm, "end": v(45.9, 15.94) * mm});
            skLineSegment(sketch, "E2869", {"start": v(45.9, 15.94) * mm, "end": v(47.55, 15.98) * mm});
            skLineSegment(sketch, "E2870", {"start": v(47.55, 15.98) * mm, "end": v(48.03, 15.97) * mm});
            skLineSegment(sketch, "E2871", {"start": v(48.03, 15.97) * mm, "end": v(48.48, 15.95) * mm});
            skLineSegment(sketch, "E2872", {"start": v(48.48, 15.95) * mm, "end": v(48.9, 15.9) * mm});
            skLineSegment(sketch, "E2873", {"start": v(48.9, 15.9) * mm, "end": v(49.3, 15.84) * mm});
            skLineSegment(sketch, "E2874", {"start": v(49.3, 15.84) * mm, "end": v(49.67, 15.77) * mm});
            skLineSegment(sketch, "E2875", {"start": v(49.67, 15.77) * mm, "end": v(50.03, 15.67) * mm});
            skLineSegment(sketch, "E2876", {"start": v(50.03, 15.67) * mm, "end": v(50.35, 15.56) * mm});
            skLineSegment(sketch, "E2877", {"start": v(50.35, 15.56) * mm, "end": v(50.5, 15.5) * mm});
            skLineSegment(sketch, "E2878", {"start": v(50.5, 15.5) * mm, "end": v(50.65, 15.43) * mm});
            skLineSegment(sketch, "E2879", {"start": v(50.65, 15.43) * mm, "end": v(50.8, 15.36) * mm});
            skLineSegment(sketch, "E2880", {"start": v(50.8, 15.36) * mm, "end": v(50.93, 15.28) * mm});
            skLineSegment(sketch, "E2881", {"start": v(50.93, 15.28) * mm, "end": v(51.06, 15.2) * mm});
            skLineSegment(sketch, "E2882", {"start": v(51.06, 15.2) * mm, "end": v(51.12, 15.14) * mm});
            skLineSegment(sketch, "E2883", {"start": v(51.12, 15.14) * mm, "end": v(51.17, 15.1) * mm});
            skLineSegment(sketch, "E2884", {"start": v(51.17, 15.1) * mm, "end": v(51.23, 15.04) * mm});
            skLineSegment(sketch, "E2885", {"start": v(51.23, 15.04) * mm, "end": v(51.28, 14.98) * mm});
            skLineSegment(sketch, "E2886", {"start": v(51.28, 14.98) * mm, "end": v(51.37, 14.86) * mm});
            skLineSegment(sketch, "E2887", {"start": v(51.37, 14.86) * mm, "end": v(51.46, 14.73) * mm});
            skLineSegment(sketch, "E2888", {"start": v(51.46, 14.73) * mm, "end": v(51.54, 14.6) * mm});
            skLineSegment(sketch, "E2889", {"start": v(51.54, 14.6) * mm, "end": v(51.61, 14.45) * mm});
            skLineSegment(sketch, "E2890", {"start": v(51.61, 14.45) * mm, "end": v(51.67, 14.29) * mm});
            skLineSegment(sketch, "E2891", {"start": v(51.67, 14.29) * mm, "end": v(51.72, 14.12) * mm});
            skLineSegment(sketch, "E2892", {"start": v(51.72, 14.12) * mm, "end": v(51.76, 13.94) * mm});
            skLineSegment(sketch, "E2893", {"start": v(51.76, 13.94) * mm, "end": v(51.8, 13.75) * mm});
            skLineSegment(sketch, "E2894", {"start": v(51.8, 13.75) * mm, "end": v(51.82, 13.56) * mm});
            skLineSegment(sketch, "E2895", {"start": v(51.82, 13.56) * mm, "end": v(51.83, 13.35) * mm});
            skLineSegment(sketch, "E2896", {"start": v(51.83, 13.35) * mm, "end": v(51.84, 13.13) * mm});
            skLineSegment(sketch, "E2897", {"start": v(51.84, 13.13) * mm, "end": v(51.83, 13.06) * mm});
            skLineSegment(sketch, "E2898", {"start": v(51.83, 13.06) * mm, "end": v(51.83, 12.98) * mm});
            skLineSegment(sketch, "E2899", {"start": v(51.83, 12.98) * mm, "end": v(51.82, 12.9) * mm});
            skLineSegment(sketch, "E2900", {"start": v(51.82, 12.9) * mm, "end": v(51.8, 12.8) * mm});
            skLineSegment(sketch, "E2901", {"start": v(51.8, 12.8) * mm, "end": v(51.8, 12.72) * mm});
            skLineSegment(sketch, "E2902", {"start": v(51.8, 12.72) * mm, "end": v(51.78, 12.62) * mm});
            skLineSegment(sketch, "E2903", {"start": v(51.78, 12.62) * mm, "end": v(51.76, 12.51) * mm});
            skLineSegment(sketch, "E2904", {"start": v(51.76, 12.51) * mm, "end": v(51.73, 12.4) * mm});
            skLineSegment(sketch, "E2905", {"start": v(51.73, 12.4) * mm, "end": v(51.7, 12.3) * mm});
            skLineSegment(sketch, "E2906", {"start": v(51.7, 12.3) * mm, "end": v(51.67, 12.17) * mm});
            skLineSegment(sketch, "E2907", {"start": v(51.67, 12.17) * mm, "end": v(51.64, 12.05) * mm});
            skLineSegment(sketch, "E2908", {"start": v(51.64, 12.05) * mm, "end": v(51.56, 11.79) * mm});
            skLineSegment(sketch, "E2909", {"start": v(51.56, 11.79) * mm, "end": v(51.47, 11.5) * mm});
            skLineSegment(sketch, "E2910", {"start": v(51.47, 11.5) * mm, "end": v(51.41, 11.36) * mm});
            skLineSegment(sketch, "E2911", {"start": v(51.41, 11.36) * mm, "end": v(51.3, 11.05) * mm});
            skLineSegment(sketch, "E2912", {"start": v(51.3, 11.05) * mm, "end": v(51.17, 10.73) * mm});
            skLineSegment(sketch, "E2913", {"start": v(51.17, 10.73) * mm, "end": v(51.03, 10.38) * mm});
            skLineSegment(sketch, "E2914", {"start": v(51.03, 10.38) * mm, "end": v(50.87, 10.01) * mm});
            skLineSegment(sketch, "E2915", {"start": v(50.87, 10.01) * mm, "end": v(50.69, 9.62) * mm});
            skLineSegment(sketch, "E2916", {"start": v(50.69, 9.62) * mm, "end": v(50.5, 9.2) * mm});
            skLineSegment(sketch, "E2917", {"start": v(50.5, 9.2) * mm, "end": v(50.29, 8.78) * mm});
            skLineSegment(sketch, "E2918", {"start": v(50.29, 8.78) * mm, "end": v(50.06, 8.32) * mm});
            skLineSegment(sketch, "E2919", {"start": v(50.06, 8.32) * mm, "end": v(49.58, 7.37) * mm});
            skLineSegment(sketch, "E2920", {"start": v(49.58, 7.37) * mm, "end": v(49.05, 6.38) * mm});
            skLineSegment(sketch, "E2921", {"start": v(49.05, 6.38) * mm, "end": v(48.47, 5.34) * mm});
            skLineSegment(sketch, "E2922", {"start": v(48.47, 5.34) * mm, "end": v(47.83, 4.25) * mm});
            skLineSegment(sketch, "E2923", {"start": v(47.83, 4.25) * mm, "end": v(47.15, 3.13) * mm});
            skLineSegment(sketch, "E2924", {"start": v(47.15, 3.13) * mm, "end": v(45.65, 0.79) * mm});
            skLineSegment(sketch, "E2925", {"start": v(45.65, 0.79) * mm, "end": v(44.83, -0.43) * mm});
            skLineSegment(sketch, "E2926", {"start": v(44.83, -0.43) * mm, "end": v(48.08, -0.43) * mm});
            skLineSegment(sketch, "E2927", {"start": v(48.08, -0.43) * mm, "end": v(45.28, -4.46) * mm});
            skLineSegment(sketch, "E2928", {"start": v(45.28, -4.46) * mm, "end": v(45.13, -4.47) * mm});
            skLineSegment(sketch, "E2929", {"start": v(45.13, -4.47) * mm, "end": v(44.97, -4.48) * mm});
            skLineSegment(sketch, "E2930", {"start": v(44.97, -4.48) * mm, "end": v(44.8, -4.5) * mm});
            skLineSegment(sketch, "E2931", {"start": v(44.8, -4.5) * mm, "end": v(44.63, -4.5) * mm});
            skLineSegment(sketch, "E2932", {"start": v(44.63, -4.5) * mm, "end": v(44.45, -4.5) * mm});
            skLineSegment(sketch, "E2933", {"start": v(44.45, -4.5) * mm, "end": v(44.25, -4.51) * mm});
            skLineSegment(sketch, "E2934", {"start": v(44.25, -4.51) * mm, "end": v(44.05, -4.52) * mm});
            skLineSegment(sketch, "E2935", {"start": v(44.05, -4.52) * mm, "end": v(43.84, -4.53) * mm});
            skLineSegment(sketch, "E2936", {"start": v(43.84, -4.53) * mm, "end": v(43.4, -4.54) * mm});
            skLineSegment(sketch, "E2937", {"start": v(43.4, -4.54) * mm, "end": v(42.95, -4.55) * mm});
            skLineSegment(sketch, "E2938", {"start": v(42.95, -4.55) * mm, "end": v(42.48, -4.57) * mm});
            skLineSegment(sketch, "E2939", {"start": v(42.48, -4.57) * mm, "end": v(41.98, -4.59) * mm});
            skLineSegment(sketch, "E2940", {"start": v(41.98, -4.59) * mm, "end": v(40.66, -6.25) * mm});
            skLineSegment(sketch, "E2941", {"start": v(40.66, -6.25) * mm, "end": v(37.84, -9.43) * mm});
            skLineSegment(sketch, "E2942", {"start": v(37.84, -9.43) * mm, "end": v(36.35, -10.94) * mm});
            skLineSegment(sketch, "E2943", {"start": v(36.35, -10.94) * mm, "end": v(34.88, -12.35) * mm});
            skLineSegment(sketch, "E2944", {"start": v(34.88, -12.35) * mm, "end": v(33.47, -13.62) * mm});
            skLineSegment(sketch, "E2945", {"start": v(33.47, -13.62) * mm, "end": v(32.8, -14.2) * mm});
            skLineSegment(sketch, "E2946", {"start": v(32.8, -14.2) * mm, "end": v(32.13, -14.74) * mm});
            skLineSegment(sketch, "E2947", {"start": v(32.13, -14.74) * mm, "end": v(31.5, -15.24) * mm});
            skLineSegment(sketch, "E2948", {"start": v(31.5, -15.24) * mm, "end": v(30.87, -15.7) * mm});
            skLineSegment(sketch, "E2949", {"start": v(30.87, -15.7) * mm, "end": v(30.57, -15.92) * mm});
            skLineSegment(sketch, "E2950", {"start": v(30.57, -15.92) * mm, "end": v(30.28, -16.13) * mm});
            skLineSegment(sketch, "E2951", {"start": v(30.28, -16.13) * mm, "end": v(30, -16.32) * mm});
            skLineSegment(sketch, "E2952", {"start": v(30, -16.32) * mm, "end": v(29.73, -16.5) * mm});
            skLineSegment(sketch, "E2953", {"start": v(29.73, -16.5) * mm, "end": v(29.48, -16.65) * mm});
            skLineSegment(sketch, "E2954", {"start": v(29.48, -16.65) * mm, "end": v(29.23, -16.8) * mm});
            skLineSegment(sketch, "E2955", {"start": v(29.23, -16.8) * mm, "end": v(29, -16.93) * mm});
            skLineSegment(sketch, "E2956", {"start": v(29, -16.93) * mm, "end": v(28.78, -17.05) * mm});
            skLineSegment(sketch, "E2957", {"start": v(28.78, -17.05) * mm, "end": v(28.57, -17.16) * mm});
            skLineSegment(sketch, "E2958", {"start": v(28.57, -17.16) * mm, "end": v(28.38, -17.25) * mm});
            skLineSegment(sketch, "E2959", {"start": v(28.38, -17.25) * mm, "end": v(28.28, -17.29) * mm});
            skLineSegment(sketch, "E2960", {"start": v(28.28, -17.29) * mm, "end": v(28.19, -17.32) * mm});
            skLineSegment(sketch, "E2961", {"start": v(28.19, -17.32) * mm, "end": v(28.1, -17.36) * mm});
            skLineSegment(sketch, "E2962", {"start": v(28.1, -17.36) * mm, "end": v(28.01, -17.39) * mm});
            skLineSegment(sketch, "E2963", {"start": v(28.01, -17.39) * mm, "end": v(27.93, -17.41) * mm});
            skLineSegment(sketch, "E2964", {"start": v(27.93, -17.41) * mm, "end": v(27.85, -17.44) * mm});
            skLineSegment(sketch, "E2965", {"start": v(27.85, -17.44) * mm, "end": v(27.77, -17.46) * mm});
            skLineSegment(sketch, "E2966", {"start": v(27.77, -17.46) * mm, "end": v(27.7, -17.47) * mm});
            skLineSegment(sketch, "E2967", {"start": v(27.7, -17.47) * mm, "end": v(27.63, -17.48) * mm});
            skLineSegment(sketch, "E2968", {"start": v(27.63, -17.48) * mm, "end": v(27.56, -17.5) * mm});
            skLineSegment(sketch, "E2969", {"start": v(27.56, -17.5) * mm, "end": v(27.5, -17.5) * mm});
            skLineSegment(sketch, "E2970", {"start": v(27.5, -17.5) * mm, "end": v(27.43, -17.5) * mm});
            skLineSegment(sketch, "E2971", {"start": v(27.43, -17.5) * mm, "end": v(27.38, -17.5) * mm});
            skLineSegment(sketch, "E2972", {"start": v(27.38, -17.5) * mm, "end": v(27.33, -17.5) * mm});
            skLineSegment(sketch, "E2973", {"start": v(27.33, -17.5) * mm, "end": v(27.28, -17.5) * mm});
            skLineSegment(sketch, "E2974", {"start": v(27.28, -17.5) * mm, "end": v(27.23, -17.48) * mm});
            skLineSegment(sketch, "E2975", {"start": v(27.23, -17.48) * mm, "end": v(27.19, -17.47) * mm});
            skLineSegment(sketch, "E2976", {"start": v(27.19, -17.47) * mm, "end": v(27.14, -17.46) * mm});
            skLineSegment(sketch, "E2977", {"start": v(27.14, -17.46) * mm, "end": v(27.1, -17.45) * mm});
            skLineSegment(sketch, "E2978", {"start": v(27.1, -17.45) * mm, "end": v(27.05, -17.43) * mm});
            skLineSegment(sketch, "E2979", {"start": v(27.05, -17.43) * mm, "end": v(27, -17.41) * mm});
            skLineSegment(sketch, "E2980", {"start": v(27, -17.41) * mm, "end": v(26.97, -17.4) * mm});
            skLineSegment(sketch, "E2981", {"start": v(26.97, -17.4) * mm, "end": v(26.93, -17.37) * mm});
            skLineSegment(sketch, "E2982", {"start": v(26.93, -17.37) * mm, "end": v(26.88, -17.35) * mm});
            skLineSegment(sketch, "E2983", {"start": v(26.88, -17.35) * mm, "end": v(26.85, -17.32) * mm});
            skLineSegment(sketch, "E2984", {"start": v(26.85, -17.32) * mm, "end": v(26.8, -17.29) * mm});
            skLineSegment(sketch, "E2985", {"start": v(26.8, -17.29) * mm, "end": v(26.77, -17.26) * mm});
            skLineSegment(sketch, "E2986", {"start": v(26.77, -17.26) * mm, "end": v(26.73, -17.23) * mm});
            skLineSegment(sketch, "E2987", {"start": v(26.73, -17.23) * mm, "end": v(26.7, -17.2) * mm});
            skLineSegment(sketch, "E2988", {"start": v(26.7, -17.2) * mm, "end": v(26.66, -17.16) * mm});
            skLineSegment(sketch, "E2989", {"start": v(26.66, -17.16) * mm, "end": v(26.63, -17.12) * mm});
            skLineSegment(sketch, "E2990", {"start": v(26.63, -17.12) * mm, "end": v(26.6, -17.09) * mm});
            skLineSegment(sketch, "E2991", {"start": v(26.6, -17.09) * mm, "end": v(26.57, -17.05) * mm});
            skLineSegment(sketch, "E2992", {"start": v(26.57, -17.05) * mm, "end": v(26.55, -17.01) * mm});
            skLineSegment(sketch, "E2993", {"start": v(26.55, -17.01) * mm, "end": v(26.53, -16.97) * mm});
            skLineSegment(sketch, "E2994", {"start": v(26.53, -16.97) * mm, "end": v(26.5, -16.93) * mm});
            skLineSegment(sketch, "E2995", {"start": v(26.5, -16.93) * mm, "end": v(26.5, -16.89) * mm});
            skLineSegment(sketch, "E2996", {"start": v(26.5, -16.89) * mm, "end": v(26.48, -16.84) * mm});
            skLineSegment(sketch, "E2997", {"start": v(26.48, -16.84) * mm, "end": v(26.46, -16.8) * mm});
            skLineSegment(sketch, "E2998", {"start": v(26.46, -16.8) * mm, "end": v(26.45, -16.75) * mm});
            skLineSegment(sketch, "E2999", {"start": v(26.45, -16.75) * mm, "end": v(26.45, -16.7) * mm});
            skLineSegment(sketch, "E3000", {"start": v(26.45, -16.7) * mm, "end": v(26.44, -16.65) * mm});
            skLineSegment(sketch, "E3001", {"start": v(26.44, -16.65) * mm, "end": v(26.44, -16.6) * mm});
            skLineSegment(sketch, "E3002", {"start": v(26.44, -16.6) * mm, "end": v(26.44, -16.55) * mm});
            skLineSegment(sketch, "E3003", {"start": v(26.44, -16.55) * mm, "end": v(26.44, -16.54) * mm});
            skLineSegment(sketch, "E3004", {"start": v(26.44, -16.54) * mm, "end": v(26.44, -16.53) * mm});
            skLineSegment(sketch, "E3005", {"start": v(26.44, -16.53) * mm, "end": v(26.44, -16.51) * mm});
            skLineSegment(sketch, "E3006", {"start": v(26.44, -16.51) * mm, "end": v(26.44, -16.5) * mm});
            skLineSegment(sketch, "E3007", {"start": v(26.44, -16.5) * mm, "end": v(26.44, -16.49) * mm});
            skLineSegment(sketch, "E3008", {"start": v(26.44, -16.49) * mm, "end": v(26.44, -16.47) * mm});
            skLineSegment(sketch, "E3009", {"start": v(26.44, -16.47) * mm, "end": v(26.45, -16.46) * mm});
            skLineSegment(sketch, "E3010", {"start": v(26.45, -16.46) * mm, "end": v(26.45, -16.44) * mm});
            skLineSegment(sketch, "E3011", {"start": v(26.45, -16.44) * mm, "end": v(26.46, -16.41) * mm});
            skLineSegment(sketch, "E3012", {"start": v(26.46, -16.41) * mm, "end": v(26.47, -16.38) * mm});
            skLineSegment(sketch, "E3013", {"start": v(26.47, -16.38) * mm, "end": v(26.48, -16.34) * mm});
            skLineSegment(sketch, "E3014", {"start": v(26.48, -16.34) * mm, "end": v(26.5, -16.3) * mm});
            skLineSegment(sketch, "E3015", {"start": v(26.5, -16.3) * mm, "end": v(26.5, -16.26) * mm});
            skLineSegment(sketch, "E3016", {"start": v(26.5, -16.26) * mm, "end": v(26.53, -16.22) * mm});
            skLineSegment(sketch, "E3017", {"start": v(26.53, -16.22) * mm, "end": v(26.55, -16.17) * mm});
            skLineSegment(sketch, "E3018", {"start": v(26.55, -16.17) * mm, "end": v(26.57, -16.12) * mm});
            skLineSegment(sketch, "E3019", {"start": v(26.57, -16.12) * mm, "end": v(26.59, -16.07) * mm});
            skLineSegment(sketch, "E3020", {"start": v(26.59, -16.07) * mm, "end": v(26.61, -16.02) * mm});
            skLineSegment(sketch, "E3021", {"start": v(26.61, -16.02) * mm, "end": v(26.64, -15.97) * mm});
            skLineSegment(sketch, "E3022", {"start": v(26.64, -15.97) * mm, "end": v(26.67, -15.91) * mm});
            skLineSegment(sketch, "E3023", {"start": v(26.67, -15.91) * mm, "end": v(26.73, -15.8) * mm});
            skLineSegment(sketch, "E3024", {"start": v(26.73, -15.8) * mm, "end": v(26.8, -15.67) * mm});
            skLineSegment(sketch, "E3025", {"start": v(26.8, -15.67) * mm, "end": v(26.87, -15.53) * mm});
            skLineSegment(sketch, "E3026", {"start": v(26.87, -15.53) * mm, "end": v(26.96, -15.38) * mm});
            skLineSegment(sketch, "E3027", {"start": v(26.96, -15.38) * mm, "end": v(27.05, -15.23) * mm});
            skLineSegment(sketch, "E3028", {"start": v(27.05, -15.23) * mm, "end": v(27.15, -15.07) * mm});
            skLineSegment(sketch, "E3029", {"start": v(27.15, -15.07) * mm, "end": v(27.25, -14.9) * mm});
            skLineSegment(sketch, "E3030", {"start": v(27.25, -14.9) * mm, "end": v(27.36, -14.72) * mm});
            skLineSegment(sketch, "E3031", {"start": v(27.36, -14.72) * mm, "end": v(27.61, -14.35) * mm});
            skLineSegment(sketch, "E3032", {"start": v(27.61, -14.35) * mm, "end": v(27.88, -13.99) * mm});
            skLineSegment(sketch, "E3033", {"start": v(27.88, -13.99) * mm, "end": v(28.18, -13.63) * mm});
            skLineSegment(sketch, "E3034", {"start": v(28.18, -13.63) * mm, "end": v(28.5, -13.29) * mm});
            skLineSegment(sketch, "E3035", {"start": v(28.5, -13.29) * mm, "end": v(28.83, -12.94) * mm});
            skLineSegment(sketch, "E3036", {"start": v(28.83, -12.94) * mm, "end": v(29.2, -12.6) * mm});
            skLineSegment(sketch, "E3037", {"start": v(29.2, -12.6) * mm, "end": v(29.57, -12.28) * mm});
            skLineSegment(sketch, "E3038", {"start": v(29.57, -12.28) * mm, "end": v(29.98, -11.95) * mm});
            skLineSegment(sketch, "E3039", {"start": v(29.98, -11.95) * mm, "end": v(30.4, -11.65) * mm});
            skLineSegment(sketch, "E3040", {"start": v(30.4, -11.65) * mm, "end": v(30.84, -11.38) * mm});
            skLineSegment(sketch, "E3041", {"start": v(30.84, -11.38) * mm, "end": v(31.3, -11.15) * mm});
            skLineSegment(sketch, "E3042", {"start": v(31.3, -11.15) * mm, "end": v(31.76, -10.95) * mm});
            skLineSegment(sketch, "E3043", {"start": v(31.76, -10.95) * mm, "end": v(32.24, -10.79) * mm});
            skLineSegment(sketch, "E3044", {"start": v(32.24, -10.79) * mm, "end": v(32.74, -10.66) * mm});
            skLineSegment(sketch, "E3045", {"start": v(32.74, -10.66) * mm, "end": v(33.25, -10.57) * mm});
            skLineSegment(sketch, "E3046", {"start": v(33.25, -10.57) * mm, "end": v(33.78, -10.52) * mm});
            skLineSegment(sketch, "E3047", {"start": v(33.78, -10.52) * mm, "end": v(34.2, -10.08) * mm});
            skLineSegment(sketch, "E3048", {"start": v(34.2, -10.08) * mm, "end": v(34.58, -9.66) * mm});
            skLineSegment(sketch, "E3049", {"start": v(34.58, -9.66) * mm, "end": v(34.93, -9.27) * mm});
            skLineSegment(sketch, "E3050", {"start": v(34.93, -9.27) * mm, "end": v(35.25, -8.91) * mm});
            skLineSegment(sketch, "E3051", {"start": v(35.25, -8.91) * mm, "end": v(35.34, -8.82) * mm});
            skLineSegment(sketch, "E3052", {"start": v(35.34, -8.82) * mm, "end": v(35.42, -8.72) * mm});
            skLineSegment(sketch, "E3053", {"start": v(35.42, -8.72) * mm, "end": v(35.5, -8.62) * mm});
            skLineSegment(sketch, "E3054", {"start": v(35.5, -8.62) * mm, "end": v(35.7, -8.4) * mm});
            skLineSegment(sketch, "E3055", {"start": v(35.7, -8.4) * mm, "end": v(35.9, -8.17) * mm});
            skLineSegment(sketch, "E3056", {"start": v(35.9, -8.17) * mm, "end": v(36.13, -7.91) * mm});
            skLineSegment(sketch, "E3057", {"start": v(36.13, -7.91) * mm, "end": v(36.36, -7.64) * mm});
            skLineSegment(sketch, "E3058", {"start": v(36.36, -7.64) * mm, "end": v(36.62, -7.34) * mm});
            skLineSegment(sketch, "E3059", {"start": v(36.62, -7.34) * mm, "end": v(36.89, -7.03) * mm});
            skLineSegment(sketch, "E3060", {"start": v(36.89, -7.03) * mm, "end": v(37.03, -6.87) * mm});
            skLineSegment(sketch, "E3061", {"start": v(37.03, -6.87) * mm, "end": v(37.3, -6.54) * mm});
            skLineSegment(sketch, "E3062", {"start": v(37.3, -6.54) * mm, "end": v(37.56, -6.23) * mm});
            skLineSegment(sketch, "E3063", {"start": v(37.56, -6.23) * mm, "end": v(37.8, -5.94) * mm});
            skLineSegment(sketch, "E3064", {"start": v(37.8, -5.94) * mm, "end": v(38.03, -5.68) * mm});
            skLineSegment(sketch, "E3065", {"start": v(38.03, -5.68) * mm, "end": v(38.24, -5.43) * mm});
            skLineSegment(sketch, "E3066", {"start": v(38.24, -5.43) * mm, "end": v(38.44, -5.2) * mm});
            skLineSegment(sketch, "E3067", {"start": v(38.44, -5.2) * mm, "end": v(38.53, -5.1) * mm});
            skLineSegment(sketch, "E3068", {"start": v(38.53, -5.1) * mm, "end": v(38.62, -4.99) * mm});
            skLineSegment(sketch, "E3069", {"start": v(38.62, -4.99) * mm, "end": v(38.7, -4.9) * mm});
            skLineSegment(sketch, "E3070", {"start": v(38.7, -4.9) * mm, "end": v(38.78, -4.8) * mm});
            skLineSegment(sketch, "E3071", {"start": v(38.78, -4.8) * mm, "end": v(32.43, -5.12) * mm});
            skLineSegment(sketch, "E3072", {"start": v(32.43, -5.12) * mm, "end": v(32.18, -5.12) * mm});
            skLineSegment(sketch, "E3073", {"start": v(32.18, -5.12) * mm, "end": v(32.06, -5.13) * mm});
            skLineSegment(sketch, "E3074", {"start": v(32.06, -5.13) * mm, "end": v(31.95, -5.13) * mm});
            skLineSegment(sketch, "E3075", {"start": v(31.95, -5.13) * mm, "end": v(31.84, -5.13) * mm});
            skLineSegment(sketch, "E3076", {"start": v(31.84, -5.13) * mm, "end": v(31.74, -5.12) * mm});
            skLineSegment(sketch, "E3077", {"start": v(31.74, -5.12) * mm, "end": v(31.64, -5.12) * mm});
            skLineSegment(sketch, "E3078", {"start": v(31.64, -5.12) * mm, "end": v(31.55, -5.12) * mm});
            skLineSegment(sketch, "E3079", {"start": v(31.55, -5.12) * mm, "end": v(31.46, -5.11) * mm});
            skLineSegment(sketch, "E3080", {"start": v(31.46, -5.11) * mm, "end": v(31.38, -5.1) * mm});
            skLineSegment(sketch, "E3081", {"start": v(31.38, -5.1) * mm, "end": v(31.3, -5.1) * mm});
            skLineSegment(sketch, "E3082", {"start": v(31.3, -5.1) * mm, "end": v(31.23, -5.08) * mm});
            skLineSegment(sketch, "E3083", {"start": v(31.23, -5.08) * mm, "end": v(31.16, -5.07) * mm});
            skLineSegment(sketch, "E3084", {"start": v(31.16, -5.07) * mm, "end": v(31.1, -5.06) * mm});
            skLineSegment(sketch, "E3085", {"start": v(31.1, -5.06) * mm, "end": v(31.04, -5.05) * mm});
            skLineSegment(sketch, "E3086", {"start": v(31.04, -5.05) * mm, "end": v(31.02, -5.04) * mm});
            skLineSegment(sketch, "E3087", {"start": v(31.02, -5.04) * mm, "end": v(31, -5.03) * mm});
            skLineSegment(sketch, "E3088", {"start": v(31, -5.03) * mm, "end": v(30.95, -5.01) * mm});
            skLineSegment(sketch, "E3089", {"start": v(30.95, -5.01) * mm, "end": v(30.92, -5) * mm});
            skLineSegment(sketch, "E3090", {"start": v(30.92, -5) * mm, "end": v(30.9, -4.99) * mm});
            skLineSegment(sketch, "E3091", {"start": v(30.9, -4.99) * mm, "end": v(30.88, -4.98) * mm});
            skLineSegment(sketch, "E3092", {"start": v(30.88, -4.98) * mm, "end": v(30.86, -4.96) * mm});
            skLineSegment(sketch, "E3093", {"start": v(30.86, -4.96) * mm, "end": v(30.84, -4.95) * mm});
            skLineSegment(sketch, "E3094", {"start": v(30.84, -4.95) * mm, "end": v(30.83, -4.93) * mm});
            skLineSegment(sketch, "E3095", {"start": v(30.83, -4.93) * mm, "end": v(30.8, -4.92) * mm});
            skLineSegment(sketch, "E3096", {"start": v(30.8, -4.92) * mm, "end": v(30.8, -4.9) * mm});
            skLineSegment(sketch, "E3097", {"start": v(30.8, -4.9) * mm, "end": v(30.78, -4.88) * mm});
            skLineSegment(sketch, "E3098", {"start": v(30.78, -4.88) * mm, "end": v(30.76, -4.86) * mm});
            skLineSegment(sketch, "E3099", {"start": v(30.76, -4.86) * mm, "end": v(30.75, -4.85) * mm});
            skLineSegment(sketch, "E3100", {"start": v(30.75, -4.85) * mm, "end": v(30.73, -4.83) * mm});
            skLineSegment(sketch, "E3101", {"start": v(30.73, -4.83) * mm, "end": v(30.72, -4.8) * mm});
            skLineSegment(sketch, "E3102", {"start": v(30.72, -4.8) * mm, "end": v(30.7, -4.76) * mm});
            skLineSegment(sketch, "E3103", {"start": v(30.7, -4.76) * mm, "end": v(30.68, -4.71) * mm});
            skLineSegment(sketch, "E3104", {"start": v(30.68, -4.71) * mm, "end": v(30.66, -4.67) * mm});
            skLineSegment(sketch, "E3105", {"start": v(30.66, -4.67) * mm, "end": v(30.64, -4.61) * mm});
            skLineSegment(sketch, "E3106", {"start": v(30.64, -4.61) * mm, "end": v(30.63, -4.56) * mm});
            skLineSegment(sketch, "E3107", {"start": v(30.63, -4.56) * mm, "end": v(30.62, -4.5) * mm});
            skLineSegment(sketch, "E3108", {"start": v(30.62, -4.5) * mm, "end": v(30.62, -4.43) * mm});
            skLineSegment(sketch, "E3109", {"start": v(30.62, -4.43) * mm, "end": v(30.61, -4.37) * mm});
            skLineSegment(sketch, "E3110", {"start": v(30.61, -4.37) * mm, "end": v(30.61, -4.34) * mm});
            skLineSegment(sketch, "E3111", {"start": v(30.61, -4.34) * mm, "end": v(30.61, -4.34) * mm});
            skLineSegment(sketch, "E3112", {"start": v(30.61, -4.34) * mm, "end": v(30.61, -4.33) * mm});
            skLineSegment(sketch, "E3113", {"start": v(30.61, -4.33) * mm, "end": v(30.61, -4.33) * mm});
            skLineSegment(sketch, "E3114", {"start": v(30.61, -4.33) * mm, "end": v(30.61, -4.33) * mm});
            skLineSegment(sketch, "E3115", {"start": v(30.61, -4.33) * mm, "end": v(30.61, -4.33) * mm});
            skLineSegment(sketch, "E3116", {"start": v(30.61, -4.33) * mm, "end": v(30.62, -4.33) * mm});
            skLineSegment(sketch, "E3117", {"start": v(30.62, -4.33) * mm, "end": v(30.62, -4.33) * mm});
            skLineSegment(sketch, "E3118", {"start": v(30.62, -4.33) * mm, "end": v(30.62, -4.32) * mm});
            skLineSegment(sketch, "E3119", {"start": v(30.62, -4.32) * mm, "end": v(30.62, -4.32) * mm});
            skLineSegment(sketch, "E3120", {"start": v(30.62, -4.32) * mm, "end": v(30.62, -4.31) * mm});
            skLineSegment(sketch, "E3121", {"start": v(30.62, -4.31) * mm, "end": v(30.62, -4.31) * mm});
            skLineSegment(sketch, "E3122", {"start": v(30.62, -4.31) * mm, "end": v(30.62, -4.3) * mm});
            skLineSegment(sketch, "E3123", {"start": v(30.62, -4.3) * mm, "end": v(30.63, -4.3) * mm});
            skLineSegment(sketch, "E3124", {"start": v(30.63, -4.3) * mm, "end": v(30.63, -4.3) * mm});
            skLineSegment(sketch, "E3125", {"start": v(30.63, -4.3) * mm, "end": v(30.63, -4.29) * mm});
            skLineSegment(sketch, "E3126", {"start": v(30.63, -4.29) * mm, "end": v(30.63, -4.28) * mm});
            skLineSegment(sketch, "E3127", {"start": v(30.63, -4.28) * mm, "end": v(30.64, -4.28) * mm});
            skLineSegment(sketch, "E3128", {"start": v(30.64, -4.28) * mm, "end": v(30.64, -4.27) * mm});
            skLineSegment(sketch, "E3129", {"start": v(30.64, -4.27) * mm, "end": v(30.64, -4.26) * mm});
            skLineSegment(sketch, "E3130", {"start": v(30.64, -4.26) * mm, "end": v(30.65, -4.25) * mm});
            skLineSegment(sketch, "E3131", {"start": v(30.65, -4.25) * mm, "end": v(30.65, -4.23) * mm});
            skLineSegment(sketch, "E3132", {"start": v(30.65, -4.23) * mm, "end": v(30.66, -4.22) * mm});
            skLineSegment(sketch, "E3133", {"start": v(30.66, -4.22) * mm, "end": v(30.67, -4.2) * mm});
            skLineSegment(sketch, "E3134", {"start": v(30.67, -4.2) * mm, "end": v(30.67, -4.19) * mm});
            skLineSegment(sketch, "E3135", {"start": v(30.67, -4.19) * mm, "end": v(30.68, -4.17) * mm});
            skLineSegment(sketch, "E3136", {"start": v(30.68, -4.17) * mm, "end": v(30.69, -4.15) * mm});
            skLineSegment(sketch, "E3137", {"start": v(30.69, -4.15) * mm, "end": v(30.7, -4.13) * mm});
            skLineSegment(sketch, "E3138", {"start": v(30.7, -4.13) * mm, "end": v(30.7, -4.1) * mm});
            skLineSegment(sketch, "E3139", {"start": v(30.7, -4.1) * mm, "end": v(30.71, -4.09) * mm});
            skLineSegment(sketch, "E3140", {"start": v(30.71, -4.09) * mm, "end": v(30.73, -4.04) * mm});
            skLineSegment(sketch, "E3141", {"start": v(30.73, -4.04) * mm, "end": v(30.75, -3.99) * mm});
            skLineSegment(sketch, "E3142", {"start": v(30.75, -3.99) * mm, "end": v(30.77, -3.93) * mm});
            skLineSegment(sketch, "E3143", {"start": v(30.77, -3.93) * mm, "end": v(30.8, -3.87) * mm});
            skLineSegment(sketch, "E3144", {"start": v(30.8, -3.87) * mm, "end": v(30.82, -3.8) * mm});
            skLineSegment(sketch, "E3145", {"start": v(30.82, -3.8) * mm, "end": v(30.93, -3.54) * mm});
            skLineSegment(sketch, "E3146", {"start": v(30.93, -3.54) * mm, "end": v(31.04, -3.3) * mm});
            skLineSegment(sketch, "E3147", {"start": v(31.04, -3.3) * mm, "end": v(31.15, -3.07) * mm});
            skLineSegment(sketch, "E3148", {"start": v(31.15, -3.07) * mm, "end": v(31.27, -2.86) * mm});
            skLineSegment(sketch, "E3149", {"start": v(31.27, -2.86) * mm, "end": v(31.3, -2.78) * mm});
            skLineSegment(sketch, "E3150", {"start": v(31.3, -2.78) * mm, "end": v(31.35, -2.71) * mm});
            skLineSegment(sketch, "E3151", {"start": v(31.35, -2.71) * mm, "end": v(31.39, -2.65) * mm});
            skLineSegment(sketch, "E3152", {"start": v(31.39, -2.65) * mm, "end": v(31.43, -2.58) * mm});
            skLineSegment(sketch, "E3153", {"start": v(31.43, -2.58) * mm, "end": v(31.46, -2.52) * mm});
            skLineSegment(sketch, "E3154", {"start": v(31.46, -2.52) * mm, "end": v(31.5, -2.47) * mm});
            skLineSegment(sketch, "E3155", {"start": v(31.5, -2.47) * mm, "end": v(31.53, -2.42) * mm});
            skLineSegment(sketch, "E3156", {"start": v(31.53, -2.42) * mm, "end": v(31.57, -2.37) * mm});
            skLineSegment(sketch, "E3157", {"start": v(31.57, -2.37) * mm, "end": v(31.6, -2.32) * mm});
            skLineSegment(sketch, "E3158", {"start": v(31.6, -2.32) * mm, "end": v(31.63, -2.28) * mm});
            skLineSegment(sketch, "E3159", {"start": v(31.63, -2.28) * mm, "end": v(31.66, -2.25) * mm});
            skLineSegment(sketch, "E3160", {"start": v(31.66, -2.25) * mm, "end": v(31.68, -2.23) * mm});
            skLineSegment(sketch, "E3161", {"start": v(31.68, -2.23) * mm, "end": v(31.69, -2.21) * mm});
            skLineSegment(sketch, "E3162", {"start": v(31.69, -2.21) * mm, "end": v(31.7, -2.2) * mm});
            skLineSegment(sketch, "E3163", {"start": v(31.7, -2.2) * mm, "end": v(31.72, -2.18) * mm});
            skLineSegment(sketch, "E3164", {"start": v(31.72, -2.18) * mm, "end": v(31.73, -2.17) * mm});
            skLineSegment(sketch, "E3165", {"start": v(31.73, -2.17) * mm, "end": v(31.74, -2.16) * mm});
            skLineSegment(sketch, "E3166", {"start": v(31.74, -2.16) * mm, "end": v(31.76, -2.15) * mm});
            skLineSegment(sketch, "E3167", {"start": v(31.76, -2.15) * mm, "end": v(31.77, -2.14) * mm});
            skLineSegment(sketch, "E3168", {"start": v(31.77, -2.14) * mm, "end": v(31.78, -2.13) * mm});
            skLineSegment(sketch, "E3169", {"start": v(31.78, -2.13) * mm, "end": v(31.8, -2.12) * mm});
            skLineSegment(sketch, "E3170", {"start": v(31.8, -2.12) * mm, "end": v(31.8, -2.12) * mm});
            skLineSegment(sketch, "E3171", {"start": v(31.8, -2.12) * mm, "end": v(31.82, -2.1) * mm});
            skLineSegment(sketch, "E3172", {"start": v(31.82, -2.1) * mm, "end": v(31.83, -2.1) * mm});
            skLineSegment(sketch, "E3173", {"start": v(31.83, -2.1) * mm, "end": v(31.85, -2.1) * mm});
            skLineSegment(sketch, "E3174", {"start": v(31.85, -2.1) * mm, "end": v(31.87, -2.08) * mm});
            skLineSegment(sketch, "E3175", {"start": v(31.87, -2.08) * mm, "end": v(31.89, -2.07) * mm});
            skLineSegment(sketch, "E3176", {"start": v(31.89, -2.07) * mm, "end": v(31.91, -2.07) * mm});
            skLineSegment(sketch, "E3177", {"start": v(31.91, -2.07) * mm, "end": v(31.93, -2.06) * mm});
            skLineSegment(sketch, "E3178", {"start": v(31.93, -2.06) * mm, "end": v(31.96, -2.05) * mm});
            skLineSegment(sketch, "E3179", {"start": v(31.96, -2.05) * mm, "end": v(31.98, -2.04) * mm});
            skLineSegment(sketch, "E3180", {"start": v(31.98, -2.04) * mm, "end": v(32.01, -2.03) * mm});
            skLineSegment(sketch, "E3181", {"start": v(32.01, -2.03) * mm, "end": v(32.04, -2.02) * mm});
            skLineSegment(sketch, "E3182", {"start": v(32.04, -2.02) * mm, "end": v(32.07, -2) * mm});
            skLineSegment(sketch, "E3183", {"start": v(32.07, -2) * mm, "end": v(32.14, -1.99) * mm});
            skLineSegment(sketch, "E3184", {"start": v(32.14, -1.99) * mm, "end": v(32.2, -1.97) * mm});
            skLineSegment(sketch, "E3185", {"start": v(32.2, -1.97) * mm, "end": v(32.28, -1.95) * mm});
            skLineSegment(sketch, "E3186", {"start": v(32.28, -1.95) * mm, "end": v(32.37, -1.92) * mm});
            skLineSegment(sketch, "E3187", {"start": v(32.37, -1.92) * mm, "end": v(32.46, -1.9) * mm});
            skLineSegment(sketch, "E3188", {"start": v(32.46, -1.9) * mm, "end": v(32.55, -1.88) * mm});
            skLineSegment(sketch, "E3189", {"start": v(32.55, -1.88) * mm, "end": v(32.65, -1.85) * mm});
            skLineSegment(sketch, "E3190", {"start": v(32.65, -1.85) * mm, "end": v(32.76, -1.83) * mm});
            skLineSegment(sketch, "E3191", {"start": v(32.76, -1.83) * mm, "end": v(32.95, -1.78) * mm});
            skLineSegment(sketch, "E3192", {"start": v(32.95, -1.78) * mm, "end": v(36.84, -0.83) * mm});
            skLineSegment(sketch, "E3193", {"start": v(36.84, -0.83) * mm, "end": v(37.21, -0.74) * mm});
            skLineSegment(sketch, "E3194", {"start": v(37.21, -0.74) * mm, "end": v(37.39, -0.7) * mm});
            skLineSegment(sketch, "E3195", {"start": v(37.39, -0.7) * mm, "end": v(37.56, -0.66) * mm});
            skLineSegment(sketch, "E3196", {"start": v(37.56, -0.66) * mm, "end": v(37.72, -0.62) * mm});
            skLineSegment(sketch, "E3197", {"start": v(37.72, -0.62) * mm, "end": v(37.87, -0.59) * mm});
            skLineSegment(sketch, "E3198", {"start": v(37.87, -0.59) * mm, "end": v(38.02, -0.56) * mm});
            skLineSegment(sketch, "E3199", {"start": v(38.02, -0.56) * mm, "end": v(38.16, -0.53) * mm});
            skLineSegment(sketch, "E3200", {"start": v(38.16, -0.53) * mm, "end": v(38.3, -0.5) * mm});
            skLineSegment(sketch, "E3201", {"start": v(38.3, -0.5) * mm, "end": v(38.42, -0.49) * mm});
            skLineSegment(sketch, "E3202", {"start": v(38.42, -0.49) * mm, "end": v(38.53, -0.47) * mm});
            skLineSegment(sketch, "E3203", {"start": v(38.53, -0.47) * mm, "end": v(38.64, -0.46) * mm});
            skLineSegment(sketch, "E3204", {"start": v(38.64, -0.46) * mm, "end": v(38.75, -0.45) * mm});
            skLineSegment(sketch, "E3205", {"start": v(38.75, -0.45) * mm, "end": v(38.84, -0.44) * mm});
            skLineSegment(sketch, "E3206", {"start": v(38.84, -0.44) * mm, "end": v(38.89, -0.44) * mm});
            skLineSegment(sketch, "E3207", {"start": v(38.89, -0.44) * mm, "end": v(38.93, -0.43) * mm});
            skLineSegment(sketch, "E3208", {"start": v(38.93, -0.43) * mm, "end": v(38.97, -0.43) * mm});
            skLineSegment(sketch, "E3209", {"start": v(38.97, -0.43) * mm, "end": v(39, -0.43) * mm});
            skLineSegment(sketch, "E3210", {"start": v(61.25, 5.14) * mm, "end": v(61.18, 5.14) * mm});
            skLineSegment(sketch, "E3211", {"start": v(61.18, 5.14) * mm, "end": v(61.12, 5.14) * mm});
            skLineSegment(sketch, "E3212", {"start": v(61.12, 5.14) * mm, "end": v(61.05, 5.15) * mm});
            skLineSegment(sketch, "E3213", {"start": v(61.05, 5.15) * mm, "end": v(60.99, 5.16) * mm});
            skLineSegment(sketch, "E3214", {"start": v(60.99, 5.16) * mm, "end": v(60.92, 5.18) * mm});
            skLineSegment(sketch, "E3215", {"start": v(60.92, 5.18) * mm, "end": v(60.86, 5.2) * mm});
            skLineSegment(sketch, "E3216", {"start": v(60.86, 5.2) * mm, "end": v(60.8, 5.21) * mm});
            skLineSegment(sketch, "E3217", {"start": v(60.8, 5.21) * mm, "end": v(60.73, 5.24) * mm});
            skLineSegment(sketch, "E3218", {"start": v(60.73, 5.24) * mm, "end": v(60.67, 5.26) * mm});
            skLineSegment(sketch, "E3219", {"start": v(60.67, 5.26) * mm, "end": v(60.6, 5.3) * mm});
            skLineSegment(sketch, "E3220", {"start": v(60.6, 5.3) * mm, "end": v(60.54, 5.33) * mm});
            skLineSegment(sketch, "E3221", {"start": v(60.54, 5.33) * mm, "end": v(60.42, 5.4) * mm});
            skLineSegment(sketch, "E3222", {"start": v(60.42, 5.4) * mm, "end": v(60.3, 5.49) * mm});
            skLineSegment(sketch, "E3223", {"start": v(60.3, 5.49) * mm, "end": v(60.24, 5.54) * mm});
            skLineSegment(sketch, "E3224", {"start": v(60.24, 5.54) * mm, "end": v(60.18, 5.59) * mm});
            skLineSegment(sketch, "E3225", {"start": v(60.18, 5.59) * mm, "end": v(60.13, 5.64) * mm});
            skLineSegment(sketch, "E3226", {"start": v(60.13, 5.64) * mm, "end": v(60.08, 5.7) * mm});
            skLineSegment(sketch, "E3227", {"start": v(60.08, 5.7) * mm, "end": v(60.03, 5.75) * mm});
            skLineSegment(sketch, "E3228", {"start": v(60.03, 5.75) * mm, "end": v(60, 5.8) * mm});
            skLineSegment(sketch, "E3229", {"start": v(60, 5.8) * mm, "end": v(59.95, 5.87) * mm});
            skLineSegment(sketch, "E3230", {"start": v(59.95, 5.87) * mm, "end": v(59.92, 5.93) * mm});
            skLineSegment(sketch, "E3231", {"start": v(59.92, 5.93) * mm, "end": v(59.89, 6) * mm});
            skLineSegment(sketch, "E3232", {"start": v(59.89, 6) * mm, "end": v(59.86, 6.06) * mm});
            skLineSegment(sketch, "E3233", {"start": v(59.86, 6.06) * mm, "end": v(59.84, 6.12) * mm});
            skLineSegment(sketch, "E3234", {"start": v(59.84, 6.12) * mm, "end": v(59.82, 6.19) * mm});
            skLineSegment(sketch, "E3235", {"start": v(59.82, 6.19) * mm, "end": v(59.8, 6.26) * mm});
            skLineSegment(sketch, "E3236", {"start": v(59.8, 6.26) * mm, "end": v(59.79, 6.33) * mm});
            skLineSegment(sketch, "E3237", {"start": v(59.79, 6.33) * mm, "end": v(59.78, 6.4) * mm});
            skLineSegment(sketch, "E3238", {"start": v(59.78, 6.4) * mm, "end": v(59.77, 6.47) * mm});
            skLineSegment(sketch, "E3239", {"start": v(59.77, 6.47) * mm, "end": v(59.77, 6.55) * mm});
            skLineSegment(sketch, "E3240", {"start": v(59.77, 6.55) * mm, "end": v(59.78, 6.67) * mm});
            skLineSegment(sketch, "E3241", {"start": v(59.78, 6.67) * mm, "end": v(59.79, 6.79) * mm});
            skLineSegment(sketch, "E3242", {"start": v(59.79, 6.79) * mm, "end": v(59.8, 6.9) * mm});
            skLineSegment(sketch, "E3243", {"start": v(59.8, 6.9) * mm, "end": v(59.83, 7.03) * mm});
            skLineSegment(sketch, "E3244", {"start": v(59.83, 7.03) * mm, "end": v(59.86, 7.15) * mm});
            skLineSegment(sketch, "E3245", {"start": v(59.86, 7.15) * mm, "end": v(59.9, 7.28) * mm});
            skLineSegment(sketch, "E3246", {"start": v(59.9, 7.28) * mm, "end": v(59.94, 7.4) * mm});
            skLineSegment(sketch, "E3247", {"start": v(59.94, 7.4) * mm, "end": v(60, 7.53) * mm});
            skLineSegment(sketch, "E3248", {"start": v(60, 7.53) * mm, "end": v(60.05, 7.66) * mm});
            skLineSegment(sketch, "E3249", {"start": v(60.05, 7.66) * mm, "end": v(60.12, 7.8) * mm});
            skLineSegment(sketch, "E3250", {"start": v(60.12, 7.8) * mm, "end": v(60.2, 7.93) * mm});
            skLineSegment(sketch, "E3251", {"start": v(60.2, 7.93) * mm, "end": v(60.27, 8.06) * mm});
            skLineSegment(sketch, "E3252", {"start": v(60.27, 8.06) * mm, "end": v(60.45, 8.34) * mm});
            skLineSegment(sketch, "E3253", {"start": v(60.45, 8.34) * mm, "end": v(60.66, 8.62) * mm});
            skLineSegment(sketch, "E3254", {"start": v(60.66, 8.62) * mm, "end": v(60.77, 8.76) * mm});
            skLineSegment(sketch, "E3255", {"start": v(60.77, 8.76) * mm, "end": v(60.88, 8.89) * mm});
            skLineSegment(sketch, "E3256", {"start": v(60.88, 8.89) * mm, "end": v(61, 9) * mm});
            skLineSegment(sketch, "E3257", {"start": v(61, 9) * mm, "end": v(61.1, 9.12) * mm});
            skLineSegment(sketch, "E3258", {"start": v(61.1, 9.12) * mm, "end": v(61.22, 9.22) * mm});
            skLineSegment(sketch, "E3259", {"start": v(61.22, 9.22) * mm, "end": v(61.33, 9.31) * mm});
            skLineSegment(sketch, "E3260", {"start": v(61.33, 9.31) * mm, "end": v(61.45, 9.4) * mm});
            skLineSegment(sketch, "E3261", {"start": v(61.45, 9.4) * mm, "end": v(61.56, 9.47) * mm});
            skLineSegment(sketch, "E3262", {"start": v(61.56, 9.47) * mm, "end": v(61.68, 9.54) * mm});
            skLineSegment(sketch, "E3263", {"start": v(61.68, 9.54) * mm, "end": v(61.8, 9.6) * mm});
            skLineSegment(sketch, "E3264", {"start": v(61.8, 9.6) * mm, "end": v(61.9, 9.65) * mm});
            skLineSegment(sketch, "E3265", {"start": v(61.9, 9.65) * mm, "end": v(62.02, 9.69) * mm});
            skLineSegment(sketch, "E3266", {"start": v(62.02, 9.69) * mm, "end": v(62.14, 9.72) * mm});
            skLineSegment(sketch, "E3267", {"start": v(62.14, 9.72) * mm, "end": v(62.26, 9.74) * mm});
            skLineSegment(sketch, "E3268", {"start": v(62.26, 9.74) * mm, "end": v(62.38, 9.75) * mm});
            skLineSegment(sketch, "E3269", {"start": v(62.38, 9.75) * mm, "end": v(62.5, 9.76) * mm});
            skLineSegment(sketch, "E3270", {"start": v(62.5, 9.76) * mm, "end": v(62.57, 9.76) * mm});
            skLineSegment(sketch, "E3271", {"start": v(62.57, 9.76) * mm, "end": v(62.65, 9.75) * mm});
            skLineSegment(sketch, "E3272", {"start": v(62.65, 9.75) * mm, "end": v(62.72, 9.74) * mm});
            skLineSegment(sketch, "E3273", {"start": v(62.72, 9.74) * mm, "end": v(62.8, 9.73) * mm});
            skLineSegment(sketch, "E3274", {"start": v(62.8, 9.73) * mm, "end": v(62.87, 9.72) * mm});
            skLineSegment(sketch, "E3275", {"start": v(62.87, 9.72) * mm, "end": v(62.94, 9.7) * mm});
            skLineSegment(sketch, "E3276", {"start": v(62.94, 9.7) * mm, "end": v(63, 9.68) * mm});
            skLineSegment(sketch, "E3277", {"start": v(63, 9.68) * mm, "end": v(63.07, 9.66) * mm});
            skLineSegment(sketch, "E3278", {"start": v(63.07, 9.66) * mm, "end": v(63.14, 9.63) * mm});
            skLineSegment(sketch, "E3279", {"start": v(63.14, 9.63) * mm, "end": v(63.2, 9.6) * mm});
            skLineSegment(sketch, "E3280", {"start": v(63.2, 9.6) * mm, "end": v(63.26, 9.57) * mm});
            skLineSegment(sketch, "E3281", {"start": v(63.26, 9.57) * mm, "end": v(63.32, 9.53) * mm});
            skLineSegment(sketch, "E3282", {"start": v(63.32, 9.53) * mm, "end": v(63.38, 9.5) * mm});
            skLineSegment(sketch, "E3283", {"start": v(63.38, 9.5) * mm, "end": v(63.44, 9.45) * mm});
            skLineSegment(sketch, "E3284", {"start": v(63.44, 9.45) * mm, "end": v(63.5, 9.4) * mm});
            skLineSegment(sketch, "E3285", {"start": v(63.5, 9.4) * mm, "end": v(63.55, 9.36) * mm});
            skLineSegment(sketch, "E3286", {"start": v(63.55, 9.36) * mm, "end": v(63.6, 9.3) * mm});
            skLineSegment(sketch, "E3287", {"start": v(63.6, 9.3) * mm, "end": v(63.65, 9.26) * mm});
            skLineSegment(sketch, "E3288", {"start": v(63.65, 9.26) * mm, "end": v(63.7, 9.2) * mm});
            skLineSegment(sketch, "E3289", {"start": v(63.7, 9.2) * mm, "end": v(63.73, 9.14) * mm});
            skLineSegment(sketch, "E3290", {"start": v(63.73, 9.14) * mm, "end": v(63.77, 9.08) * mm});
            skLineSegment(sketch, "E3291", {"start": v(63.77, 9.08) * mm, "end": v(63.8, 9.02) * mm});
            skLineSegment(sketch, "E3292", {"start": v(63.8, 9.02) * mm, "end": v(63.84, 8.96) * mm});
            skLineSegment(sketch, "E3293", {"start": v(63.84, 8.96) * mm, "end": v(63.87, 8.89) * mm});
            skLineSegment(sketch, "E3294", {"start": v(63.87, 8.89) * mm, "end": v(63.9, 8.82) * mm});
            skLineSegment(sketch, "E3295", {"start": v(63.9, 8.82) * mm, "end": v(63.91, 8.74) * mm});
            skLineSegment(sketch, "E3296", {"start": v(63.91, 8.74) * mm, "end": v(63.93, 8.66) * mm});
            skLineSegment(sketch, "E3297", {"start": v(63.93, 8.66) * mm, "end": v(63.94, 8.59) * mm});
            skLineSegment(sketch, "E3298", {"start": v(63.94, 8.59) * mm, "end": v(63.96, 8.5) * mm});
            skLineSegment(sketch, "E3299", {"start": v(63.96, 8.5) * mm, "end": v(63.96, 8.42) * mm});
            skLineSegment(sketch, "E3300", {"start": v(63.96, 8.42) * mm, "end": v(63.97, 8.33) * mm});
            skLineSegment(sketch, "E3301", {"start": v(63.97, 8.33) * mm, "end": v(63.97, 8.24) * mm});
            skLineSegment(sketch, "E3302", {"start": v(63.97, 8.24) * mm, "end": v(63.97, 8.12) * mm});
            skLineSegment(sketch, "E3303", {"start": v(63.97, 8.12) * mm, "end": v(63.96, 8) * mm});
            skLineSegment(sketch, "E3304", {"start": v(63.96, 8) * mm, "end": v(63.94, 7.9) * mm});
            skLineSegment(sketch, "E3305", {"start": v(63.94, 7.9) * mm, "end": v(63.92, 7.77) * mm});
            skLineSegment(sketch, "E3306", {"start": v(63.92, 7.77) * mm, "end": v(63.89, 7.65) * mm});
            skLineSegment(sketch, "E3307", {"start": v(63.89, 7.65) * mm, "end": v(63.85, 7.53) * mm});
            skLineSegment(sketch, "E3308", {"start": v(63.85, 7.53) * mm, "end": v(63.8, 7.4) * mm});
            skLineSegment(sketch, "E3309", {"start": v(63.8, 7.4) * mm, "end": v(63.75, 7.28) * mm});
            skLineSegment(sketch, "E3310", {"start": v(63.75, 7.28) * mm, "end": v(63.7, 7.16) * mm});
            skLineSegment(sketch, "E3311", {"start": v(63.7, 7.16) * mm, "end": v(63.63, 7.03) * mm});
            skLineSegment(sketch, "E3312", {"start": v(63.63, 7.03) * mm, "end": v(63.56, 6.9) * mm});
            skLineSegment(sketch, "E3313", {"start": v(63.56, 6.9) * mm, "end": v(63.48, 6.77) * mm});
            skLineSegment(sketch, "E3314", {"start": v(63.48, 6.77) * mm, "end": v(63.3, 6.5) * mm});
            skLineSegment(sketch, "E3315", {"start": v(63.3, 6.5) * mm, "end": v(63.1, 6.23) * mm});
            skLineSegment(sketch, "E3316", {"start": v(63.1, 6.23) * mm, "end": v(63, 6.1) * mm});
            skLineSegment(sketch, "E3317", {"start": v(63, 6.1) * mm, "end": v(62.89, 5.98) * mm});
            skLineSegment(sketch, "E3318", {"start": v(62.89, 5.98) * mm, "end": v(62.78, 5.86) * mm});
            skLineSegment(sketch, "E3319", {"start": v(62.78, 5.86) * mm, "end": v(62.67, 5.75) * mm});
            skLineSegment(sketch, "E3320", {"start": v(62.67, 5.75) * mm, "end": v(62.55, 5.66) * mm});
            skLineSegment(sketch, "E3321", {"start": v(62.55, 5.66) * mm, "end": v(62.44, 5.57) * mm});
            skLineSegment(sketch, "E3322", {"start": v(62.44, 5.57) * mm, "end": v(62.32, 5.48) * mm});
            skLineSegment(sketch, "E3323", {"start": v(62.32, 5.48) * mm, "end": v(62.2, 5.41) * mm});
            skLineSegment(sketch, "E3324", {"start": v(62.2, 5.41) * mm, "end": v(62.1, 5.35) * mm});
            skLineSegment(sketch, "E3325", {"start": v(62.1, 5.35) * mm, "end": v(61.98, 5.3) * mm});
            skLineSegment(sketch, "E3326", {"start": v(61.98, 5.3) * mm, "end": v(61.86, 5.24) * mm});
            skLineSegment(sketch, "E3327", {"start": v(61.86, 5.24) * mm, "end": v(61.74, 5.2) * mm});
            skLineSegment(sketch, "E3328", {"start": v(61.74, 5.2) * mm, "end": v(61.62, 5.18) * mm});
            skLineSegment(sketch, "E3329", {"start": v(61.62, 5.18) * mm, "end": v(61.5, 5.15) * mm});
            skLineSegment(sketch, "E3330", {"start": v(61.5, 5.15) * mm, "end": v(61.37, 5.14) * mm});
            skLineSegment(sketch, "E3331", {"start": v(61.37, 5.14) * mm, "end": v(61.25, 5.14) * mm});
            skLineSegment(sketch, "E3332", {"start": v(62.68, -4.3) * mm, "end": v(62.68, -5.83) * mm});
            skLineSegment(sketch, "E3333", {"start": v(62.68, -5.83) * mm, "end": v(62.18, -6.47) * mm});
            skLineSegment(sketch, "E3334", {"start": v(62.18, -6.47) * mm, "end": v(61.68, -7.07) * mm});
            skLineSegment(sketch, "E3335", {"start": v(61.68, -7.07) * mm, "end": v(61.19, -7.63) * mm});
            skLineSegment(sketch, "E3336", {"start": v(61.19, -7.63) * mm, "end": v(60.7, -8.15) * mm});
            skLineSegment(sketch, "E3337", {"start": v(60.7, -8.15) * mm, "end": v(60.23, -8.63) * mm});
            skLineSegment(sketch, "E3338", {"start": v(60.23, -8.63) * mm, "end": v(59.77, -9.07) * mm});
            skLineSegment(sketch, "E3339", {"start": v(59.77, -9.07) * mm, "end": v(59.31, -9.46) * mm});
            skLineSegment(sketch, "E3340", {"start": v(59.31, -9.46) * mm, "end": v(58.87, -9.82) * mm});
            skLineSegment(sketch, "E3341", {"start": v(58.87, -9.82) * mm, "end": v(58.43, -10.13) * mm});
            skLineSegment(sketch, "E3342", {"start": v(58.43, -10.13) * mm, "end": v(58.22, -10.27) * mm});
            skLineSegment(sketch, "E3343", {"start": v(58.22, -10.27) * mm, "end": v(58.01, -10.4) * mm});
            skLineSegment(sketch, "E3344", {"start": v(58.01, -10.4) * mm, "end": v(57.8, -10.52) * mm});
            skLineSegment(sketch, "E3345", {"start": v(57.8, -10.52) * mm, "end": v(57.61, -10.63) * mm});
            skLineSegment(sketch, "E3346", {"start": v(57.61, -10.63) * mm, "end": v(57.42, -10.73) * mm});
            skLineSegment(sketch, "E3347", {"start": v(57.42, -10.73) * mm, "end": v(57.23, -10.82) * mm});
            skLineSegment(sketch, "E3348", {"start": v(57.23, -10.82) * mm, "end": v(57.04, -10.9) * mm});
            skLineSegment(sketch, "E3349", {"start": v(57.04, -10.9) * mm, "end": v(56.86, -10.96) * mm});
            skLineSegment(sketch, "E3350", {"start": v(56.86, -10.96) * mm, "end": v(56.68, -11.02) * mm});
            skLineSegment(sketch, "E3351", {"start": v(56.68, -11.02) * mm, "end": v(56.5, -11.07) * mm});
            skLineSegment(sketch, "E3352", {"start": v(56.5, -11.07) * mm, "end": v(56.33, -11.1) * mm});
            skLineSegment(sketch, "E3353", {"start": v(56.33, -11.1) * mm, "end": v(56.17, -11.13) * mm});
            skLineSegment(sketch, "E3354", {"start": v(56.17, -11.13) * mm, "end": v(56, -11.14) * mm});
            skLineSegment(sketch, "E3355", {"start": v(56, -11.14) * mm, "end": v(55.85, -11.15) * mm});
            skLineSegment(sketch, "E3356", {"start": v(55.85, -11.15) * mm, "end": v(55.64, -11.14) * mm});
            skLineSegment(sketch, "E3357", {"start": v(55.64, -11.14) * mm, "end": v(55.43, -11.12) * mm});
            skLineSegment(sketch, "E3358", {"start": v(55.43, -11.12) * mm, "end": v(55.23, -11.09) * mm});
            skLineSegment(sketch, "E3359", {"start": v(55.23, -11.09) * mm, "end": v(55.04, -11.04) * mm});
            skLineSegment(sketch, "E3360", {"start": v(55.04, -11.04) * mm, "end": v(54.85, -10.97) * mm});
            skLineSegment(sketch, "E3361", {"start": v(54.85, -10.97) * mm, "end": v(54.68, -10.9) * mm});
            skLineSegment(sketch, "E3362", {"start": v(54.68, -10.9) * mm, "end": v(54.5, -10.8) * mm});
            skLineSegment(sketch, "E3363", {"start": v(54.5, -10.8) * mm, "end": v(54.34, -10.7) * mm});
            skLineSegment(sketch, "E3364", {"start": v(54.34, -10.7) * mm, "end": v(54.18, -10.58) * mm});
            skLineSegment(sketch, "E3365", {"start": v(54.18, -10.58) * mm, "end": v(54.03, -10.44) * mm});
            skLineSegment(sketch, "E3366", {"start": v(54.03, -10.44) * mm, "end": v(53.89, -10.3) * mm});
            skLineSegment(sketch, "E3367", {"start": v(53.89, -10.3) * mm, "end": v(53.75, -10.13) * mm});
            skLineSegment(sketch, "E3368", {"start": v(53.75, -10.13) * mm, "end": v(53.62, -9.95) * mm});
            skLineSegment(sketch, "E3369", {"start": v(53.62, -9.95) * mm, "end": v(53.5, -9.76) * mm});
            skLineSegment(sketch, "E3370", {"start": v(53.5, -9.76) * mm, "end": v(53.38, -9.56) * mm});
            skLineSegment(sketch, "E3371", {"start": v(53.38, -9.56) * mm, "end": v(53.27, -9.34) * mm});
            skLineSegment(sketch, "E3372", {"start": v(53.27, -9.34) * mm, "end": v(53.08, -8.88) * mm});
            skLineSegment(sketch, "E3373", {"start": v(53.08, -8.88) * mm, "end": v(52.9, -8.4) * mm});
            skLineSegment(sketch, "E3374", {"start": v(52.9, -8.4) * mm, "end": v(52.76, -7.93) * mm});
            skLineSegment(sketch, "E3375", {"start": v(52.76, -7.93) * mm, "end": v(52.64, -7.44) * mm});
            skLineSegment(sketch, "E3376", {"start": v(52.64, -7.44) * mm, "end": v(52.55, -6.94) * mm});
            skLineSegment(sketch, "E3377", {"start": v(52.55, -6.94) * mm, "end": v(52.48, -6.42) * mm});
            skLineSegment(sketch, "E3378", {"start": v(52.48, -6.42) * mm, "end": v(52.44, -5.9) * mm});
            skLineSegment(sketch, "E3379", {"start": v(52.44, -5.9) * mm, "end": v(52.43, -5.37) * mm});
            skLineSegment(sketch, "E3380", {"start": v(52.43, -5.37) * mm, "end": v(52.44, -4.96) * mm});
            skLineSegment(sketch, "E3381", {"start": v(52.44, -4.96) * mm, "end": v(52.47, -4.57) * mm});
            skLineSegment(sketch, "E3382", {"start": v(52.47, -4.57) * mm, "end": v(52.53, -4.18) * mm});
            skLineSegment(sketch, "E3383", {"start": v(52.53, -4.18) * mm, "end": v(52.6, -3.8) * mm});
            skLineSegment(sketch, "E3384", {"start": v(52.6, -3.8) * mm, "end": v(52.64, -3.62) * mm});
            skLineSegment(sketch, "E3385", {"start": v(52.64, -3.62) * mm, "end": v(52.69, -3.45) * mm});
            skLineSegment(sketch, "E3386", {"start": v(52.69, -3.45) * mm, "end": v(52.74, -3.28) * mm});
            skLineSegment(sketch, "E3387", {"start": v(52.74, -3.28) * mm, "end": v(52.78, -3.12) * mm});
            skLineSegment(sketch, "E3388", {"start": v(52.78, -3.12) * mm, "end": v(52.84, -2.97) * mm});
            skLineSegment(sketch, "E3389", {"start": v(52.84, -2.97) * mm, "end": v(52.89, -2.82) * mm});
            skLineSegment(sketch, "E3390", {"start": v(52.89, -2.82) * mm, "end": v(52.94, -2.69) * mm});
            skLineSegment(sketch, "E3391", {"start": v(52.94, -2.69) * mm, "end": v(53, -2.56) * mm});
            skLineSegment(sketch, "E3392", {"start": v(53, -2.56) * mm, "end": v(53.03, -2.5) * mm});
            skLineSegment(sketch, "E3393", {"start": v(53.03, -2.5) * mm, "end": v(53.06, -2.43) * mm});
            skLineSegment(sketch, "E3394", {"start": v(53.06, -2.43) * mm, "end": v(53.1, -2.36) * mm});
            skLineSegment(sketch, "E3395", {"start": v(53.1, -2.36) * mm, "end": v(53.14, -2.29) * mm});
            skLineSegment(sketch, "E3396", {"start": v(53.14, -2.29) * mm, "end": v(53.18, -2.2) * mm});
            skLineSegment(sketch, "E3397", {"start": v(53.18, -2.2) * mm, "end": v(53.23, -2.12) * mm});
            skLineSegment(sketch, "E3398", {"start": v(53.23, -2.12) * mm, "end": v(53.28, -2.03) * mm});
            skLineSegment(sketch, "E3399", {"start": v(53.28, -2.03) * mm, "end": v(53.33, -1.94) * mm});
            skLineSegment(sketch, "E3400", {"start": v(53.33, -1.94) * mm, "end": v(53.39, -1.84) * mm});
            skLineSegment(sketch, "E3401", {"start": v(53.39, -1.84) * mm, "end": v(53.45, -1.74) * mm});
            skLineSegment(sketch, "E3402", {"start": v(53.45, -1.74) * mm, "end": v(53.57, -1.53) * mm});
            skLineSegment(sketch, "E3403", {"start": v(53.57, -1.53) * mm, "end": v(53.71, -1.3) * mm});
            skLineSegment(sketch, "E3404", {"start": v(53.71, -1.3) * mm, "end": v(53.87, -1.04) * mm});
            skLineSegment(sketch, "E3405", {"start": v(53.87, -1.04) * mm, "end": v(54.24, -0.48) * mm});
            skLineSegment(sketch, "E3406", {"start": v(54.24, -0.48) * mm, "end": v(54.6, 0.05) * mm});
            skLineSegment(sketch, "E3407", {"start": v(54.6, 0.05) * mm, "end": v(54.97, 0.54) * mm});
            skLineSegment(sketch, "E3408", {"start": v(54.97, 0.54) * mm, "end": v(55.33, 1) * mm});
            skLineSegment(sketch, "E3409", {"start": v(55.33, 1) * mm, "end": v(55.69, 1.41) * mm});
            skLineSegment(sketch, "E3410", {"start": v(55.69, 1.41) * mm, "end": v(56.04, 1.8) * mm});
            skLineSegment(sketch, "E3411", {"start": v(56.04, 1.8) * mm, "end": v(56.39, 2.14) * mm});
            skLineSegment(sketch, "E3412", {"start": v(56.39, 2.14) * mm, "end": v(56.73, 2.45) * mm});
            skLineSegment(sketch, "E3413", {"start": v(56.73, 2.45) * mm, "end": v(57.08, 2.73) * mm});
            skLineSegment(sketch, "E3414", {"start": v(57.08, 2.73) * mm, "end": v(57.24, 2.85) * mm});
            skLineSegment(sketch, "E3415", {"start": v(57.24, 2.85) * mm, "end": v(57.41, 2.96) * mm});
            skLineSegment(sketch, "E3416", {"start": v(57.41, 2.96) * mm, "end": v(57.58, 3.07) * mm});
            skLineSegment(sketch, "E3417", {"start": v(57.58, 3.07) * mm, "end": v(57.75, 3.16) * mm});
            skLineSegment(sketch, "E3418", {"start": v(57.75, 3.16) * mm, "end": v(57.91, 3.25) * mm});
            skLineSegment(sketch, "E3419", {"start": v(57.91, 3.25) * mm, "end": v(58.07, 3.33) * mm});
            skLineSegment(sketch, "E3420", {"start": v(58.07, 3.33) * mm, "end": v(58.24, 3.4) * mm});
            skLineSegment(sketch, "E3421", {"start": v(58.24, 3.4) * mm, "end": v(58.4, 3.45) * mm});
            skLineSegment(sketch, "E3422", {"start": v(58.4, 3.45) * mm, "end": v(58.56, 3.5) * mm});
            skLineSegment(sketch, "E3423", {"start": v(58.56, 3.5) * mm, "end": v(58.72, 3.55) * mm});
            skLineSegment(sketch, "E3424", {"start": v(58.72, 3.55) * mm, "end": v(58.88, 3.58) * mm});
            skLineSegment(sketch, "E3425", {"start": v(58.88, 3.58) * mm, "end": v(59.04, 3.6) * mm});
            skLineSegment(sketch, "E3426", {"start": v(59.04, 3.6) * mm, "end": v(59.2, 3.61) * mm});
            skLineSegment(sketch, "E3427", {"start": v(59.2, 3.61) * mm, "end": v(59.35, 3.62) * mm});
            skLineSegment(sketch, "E3428", {"start": v(59.35, 3.62) * mm, "end": v(59.5, 3.61) * mm});
            skLineSegment(sketch, "E3429", {"start": v(59.5, 3.61) * mm, "end": v(59.65, 3.6) * mm});
            skLineSegment(sketch, "E3430", {"start": v(59.65, 3.6) * mm, "end": v(59.72, 3.6) * mm});
            skLineSegment(sketch, "E3431", {"start": v(59.72, 3.6) * mm, "end": v(59.79, 3.58) * mm});
            skLineSegment(sketch, "E3432", {"start": v(59.79, 3.58) * mm, "end": v(59.85, 3.57) * mm});
            skLineSegment(sketch, "E3433", {"start": v(59.85, 3.57) * mm, "end": v(59.91, 3.56) * mm});
            skLineSegment(sketch, "E3434", {"start": v(59.91, 3.56) * mm, "end": v(59.97, 3.54) * mm});
            skLineSegment(sketch, "E3435", {"start": v(59.97, 3.54) * mm, "end": v(60.03, 3.52) * mm});
            skLineSegment(sketch, "E3436", {"start": v(60.03, 3.52) * mm, "end": v(60.08, 3.5) * mm});
            skLineSegment(sketch, "E3437", {"start": v(60.08, 3.5) * mm, "end": v(60.13, 3.48) * mm});
            skLineSegment(sketch, "E3438", {"start": v(60.13, 3.48) * mm, "end": v(60.18, 3.45) * mm});
            skLineSegment(sketch, "E3439", {"start": v(60.18, 3.45) * mm, "end": v(60.23, 3.43) * mm});
            skLineSegment(sketch, "E3440", {"start": v(60.23, 3.43) * mm, "end": v(60.27, 3.4) * mm});
            skLineSegment(sketch, "E3441", {"start": v(60.27, 3.4) * mm, "end": v(60.32, 3.37) * mm});
            skLineSegment(sketch, "E3442", {"start": v(60.32, 3.37) * mm, "end": v(60.35, 3.34) * mm});
            skLineSegment(sketch, "E3443", {"start": v(60.35, 3.34) * mm, "end": v(60.4, 3.3) * mm});
            skLineSegment(sketch, "E3444", {"start": v(60.4, 3.3) * mm, "end": v(60.43, 3.27) * mm});
            skLineSegment(sketch, "E3445", {"start": v(60.43, 3.27) * mm, "end": v(60.46, 3.23) * mm});
            skLineSegment(sketch, "E3446", {"start": v(60.46, 3.23) * mm, "end": v(60.49, 3.2) * mm});
            skLineSegment(sketch, "E3447", {"start": v(60.49, 3.2) * mm, "end": v(60.51, 3.15) * mm});
            skLineSegment(sketch, "E3448", {"start": v(60.51, 3.15) * mm, "end": v(60.54, 3.1) * mm});
            skLineSegment(sketch, "E3449", {"start": v(60.54, 3.1) * mm, "end": v(60.56, 3.06) * mm});
            skLineSegment(sketch, "E3450", {"start": v(60.56, 3.06) * mm, "end": v(60.58, 3.01) * mm});
            skLineSegment(sketch, "E3451", {"start": v(60.58, 3.01) * mm, "end": v(60.6, 2.96) * mm});
            skLineSegment(sketch, "E3452", {"start": v(60.6, 2.96) * mm, "end": v(60.6, 2.91) * mm});
            skLineSegment(sketch, "E3453", {"start": v(60.6, 2.91) * mm, "end": v(60.62, 2.86) * mm});
            skLineSegment(sketch, "E3454", {"start": v(60.62, 2.86) * mm, "end": v(60.63, 2.8) * mm});
            skLineSegment(sketch, "E3455", {"start": v(60.63, 2.8) * mm, "end": v(60.63, 2.75) * mm});
            skLineSegment(sketch, "E3456", {"start": v(60.63, 2.75) * mm, "end": v(60.64, 2.69) * mm});
            skLineSegment(sketch, "E3457", {"start": v(60.64, 2.69) * mm, "end": v(60.64, 2.63) * mm});
            skLineSegment(sketch, "E3458", {"start": v(60.64, 2.63) * mm, "end": v(60.64, 2.58) * mm});
            skLineSegment(sketch, "E3459", {"start": v(60.64, 2.58) * mm, "end": v(60.63, 2.54) * mm});
            skLineSegment(sketch, "E3460", {"start": v(60.63, 2.54) * mm, "end": v(60.63, 2.5) * mm});
            skLineSegment(sketch, "E3461", {"start": v(60.63, 2.5) * mm, "end": v(60.62, 2.45) * mm});
            skLineSegment(sketch, "E3462", {"start": v(60.62, 2.45) * mm, "end": v(60.62, 2.4) * mm});
            skLineSegment(sketch, "E3463", {"start": v(60.62, 2.4) * mm, "end": v(60.6, 2.3) * mm});
            skLineSegment(sketch, "E3464", {"start": v(60.6, 2.3) * mm, "end": v(60.57, 2.19) * mm});
            skLineSegment(sketch, "E3465", {"start": v(60.57, 2.19) * mm, "end": v(60.54, 2.07) * mm});
            skLineSegment(sketch, "E3466", {"start": v(60.54, 2.07) * mm, "end": v(60.5, 1.95) * mm});
            skLineSegment(sketch, "E3467", {"start": v(60.5, 1.95) * mm, "end": v(60.45, 1.83) * mm});
            skLineSegment(sketch, "E3468", {"start": v(60.45, 1.83) * mm, "end": v(60.4, 1.7) * mm});
            skLineSegment(sketch, "E3469", {"start": v(60.4, 1.7) * mm, "end": v(60.34, 1.56) * mm});
            skLineSegment(sketch, "E3470", {"start": v(60.34, 1.56) * mm, "end": v(60.27, 1.41) * mm});
            skLineSegment(sketch, "E3471", {"start": v(60.27, 1.41) * mm, "end": v(60.2, 1.26) * mm});
            skLineSegment(sketch, "E3472", {"start": v(60.2, 1.26) * mm, "end": v(60.12, 1.1) * mm});
            skLineSegment(sketch, "E3473", {"start": v(60.12, 1.1) * mm, "end": v(60.04, 0.95) * mm});
            skLineSegment(sketch, "E3474", {"start": v(60.04, 0.95) * mm, "end": v(59.94, 0.78) * mm});
            skLineSegment(sketch, "E3475", {"start": v(59.94, 0.78) * mm, "end": v(59.8, 0.52) * mm});
            skLineSegment(sketch, "E3476", {"start": v(59.8, 0.52) * mm, "end": v(59.6, 0.17) * mm});
            skLineSegment(sketch, "E3477", {"start": v(59.6, 0.17) * mm, "end": v(59.4, -0.15) * mm});
            skLineSegment(sketch, "E3478", {"start": v(59.4, -0.15) * mm, "end": v(59.2, -0.44) * mm});
            skLineSegment(sketch, "E3479", {"start": v(59.2, -0.44) * mm, "end": v(59.01, -0.71) * mm});
            skLineSegment(sketch, "E3480", {"start": v(59.01, -0.71) * mm, "end": v(58.83, -0.96) * mm});
            skLineSegment(sketch, "E3481", {"start": v(58.83, -0.96) * mm, "end": v(58.74, -1.07) * mm});
            skLineSegment(sketch, "E3482", {"start": v(58.74, -1.07) * mm, "end": v(58.65, -1.17) * mm});
            skLineSegment(sketch, "E3483", {"start": v(58.65, -1.17) * mm, "end": v(58.57, -1.27) * mm});
            skLineSegment(sketch, "E3484", {"start": v(58.57, -1.27) * mm, "end": v(58.48, -1.36) * mm});
            skLineSegment(sketch, "E3485", {"start": v(58.48, -1.36) * mm, "end": v(58.4, -1.45) * mm});
            skLineSegment(sketch, "E3486", {"start": v(58.4, -1.45) * mm, "end": v(58.32, -1.53) * mm});
            skLineSegment(sketch, "E3487", {"start": v(58.32, -1.53) * mm, "end": v(57.88, -1.96) * mm});
            skLineSegment(sketch, "E3488", {"start": v(57.88, -1.96) * mm, "end": v(57.67, -2.16) * mm});
            skLineSegment(sketch, "E3489", {"start": v(57.67, -2.16) * mm, "end": v(57.48, -2.35) * mm});
            skLineSegment(sketch, "E3490", {"start": v(57.48, -2.35) * mm, "end": v(57.3, -2.53) * mm});
            skLineSegment(sketch, "E3491", {"start": v(57.3, -2.53) * mm, "end": v(57.12, -2.7) * mm});
            skLineSegment(sketch, "E3492", {"start": v(57.12, -2.7) * mm, "end": v(56.95, -2.87) * mm});
            skLineSegment(sketch, "E3493", {"start": v(56.95, -2.87) * mm, "end": v(56.8, -3.03) * mm});
            skLineSegment(sketch, "E3494", {"start": v(56.8, -3.03) * mm, "end": v(56.65, -3.18) * mm});
            skLineSegment(sketch, "E3495", {"start": v(56.65, -3.18) * mm, "end": v(56.52, -3.32) * mm});
            skLineSegment(sketch, "E3496", {"start": v(56.52, -3.32) * mm, "end": v(56.4, -3.46) * mm});
            skLineSegment(sketch, "E3497", {"start": v(56.4, -3.46) * mm, "end": v(56.28, -3.58) * mm});
            skLineSegment(sketch, "E3498", {"start": v(56.28, -3.58) * mm, "end": v(56.17, -3.7) * mm});
            skLineSegment(sketch, "E3499", {"start": v(56.17, -3.7) * mm, "end": v(56.12, -3.75) * mm});
            skLineSegment(sketch, "E3500", {"start": v(56.12, -3.75) * mm, "end": v(56.07, -3.8) * mm});
            skLineSegment(sketch, "E3501", {"start": v(56.07, -3.8) * mm, "end": v(56.03, -3.86) * mm});
            skLineSegment(sketch, "E3502", {"start": v(56.03, -3.86) * mm, "end": v(55.99, -3.9) * mm});
            skLineSegment(sketch, "E3503", {"start": v(55.99, -3.9) * mm, "end": v(55.95, -3.95) * mm});
            skLineSegment(sketch, "E3504", {"start": v(55.95, -3.95) * mm, "end": v(55.91, -4) * mm});
            skLineSegment(sketch, "E3505", {"start": v(55.91, -4) * mm, "end": v(55.78, -4.17) * mm});
            skLineSegment(sketch, "E3506", {"start": v(55.78, -4.17) * mm, "end": v(55.67, -4.36) * mm});
            skLineSegment(sketch, "E3507", {"start": v(55.67, -4.36) * mm, "end": v(55.58, -4.55) * mm});
            skLineSegment(sketch, "E3508", {"start": v(55.58, -4.55) * mm, "end": v(55.5, -4.74) * mm});
            skLineSegment(sketch, "E3509", {"start": v(55.5, -4.74) * mm, "end": v(55.44, -4.94) * mm});
            skLineSegment(sketch, "E3510", {"start": v(55.44, -4.94) * mm, "end": v(55.4, -5.15) * mm});
            skLineSegment(sketch, "E3511", {"start": v(55.4, -5.15) * mm, "end": v(55.37, -5.36) * mm});
            skLineSegment(sketch, "E3512", {"start": v(55.37, -5.36) * mm, "end": v(55.36, -5.58) * mm});
            skLineSegment(sketch, "E3513", {"start": v(55.36, -5.58) * mm, "end": v(55.37, -5.67) * mm});
            skLineSegment(sketch, "E3514", {"start": v(55.37, -5.67) * mm, "end": v(55.37, -5.77) * mm});
            skLineSegment(sketch, "E3515", {"start": v(55.37, -5.77) * mm, "end": v(55.38, -5.86) * mm});
            skLineSegment(sketch, "E3516", {"start": v(55.38, -5.86) * mm, "end": v(55.4, -5.94) * mm});
            skLineSegment(sketch, "E3517", {"start": v(55.4, -5.94) * mm, "end": v(55.42, -6.03) * mm});
            skLineSegment(sketch, "E3518", {"start": v(55.42, -6.03) * mm, "end": v(55.44, -6.11) * mm});
            skLineSegment(sketch, "E3519", {"start": v(55.44, -6.11) * mm, "end": v(55.47, -6.2) * mm});
            skLineSegment(sketch, "E3520", {"start": v(55.47, -6.2) * mm, "end": v(55.5, -6.28) * mm});
            skLineSegment(sketch, "E3521", {"start": v(55.5, -6.28) * mm, "end": v(55.54, -6.35) * mm});
            skLineSegment(sketch, "E3522", {"start": v(55.54, -6.35) * mm, "end": v(55.59, -6.43) * mm});
            skLineSegment(sketch, "E3523", {"start": v(55.59, -6.43) * mm, "end": v(55.63, -6.5) * mm});
            skLineSegment(sketch, "E3524", {"start": v(55.63, -6.5) * mm, "end": v(55.68, -6.58) * mm});
            skLineSegment(sketch, "E3525", {"start": v(55.68, -6.58) * mm, "end": v(55.74, -6.65) * mm});
            skLineSegment(sketch, "E3526", {"start": v(55.74, -6.65) * mm, "end": v(55.8, -6.72) * mm});
            skLineSegment(sketch, "E3527", {"start": v(55.8, -6.72) * mm, "end": v(55.86, -6.78) * mm});
            skLineSegment(sketch, "E3528", {"start": v(55.86, -6.78) * mm, "end": v(55.93, -6.85) * mm});
            skLineSegment(sketch, "E3529", {"start": v(55.93, -6.85) * mm, "end": v(56, -6.9) * mm});
            skLineSegment(sketch, "E3530", {"start": v(56, -6.9) * mm, "end": v(56.08, -6.96) * mm});
            skLineSegment(sketch, "E3531", {"start": v(56.08, -6.96) * mm, "end": v(56.16, -7.02) * mm});
            skLineSegment(sketch, "E3532", {"start": v(56.16, -7.02) * mm, "end": v(56.24, -7.07) * mm});
            skLineSegment(sketch, "E3533", {"start": v(56.24, -7.07) * mm, "end": v(56.32, -7.11) * mm});
            skLineSegment(sketch, "E3534", {"start": v(56.32, -7.11) * mm, "end": v(56.4, -7.15) * mm});
            skLineSegment(sketch, "E3535", {"start": v(56.4, -7.15) * mm, "end": v(56.5, -7.2) * mm});
            skLineSegment(sketch, "E3536", {"start": v(56.5, -7.2) * mm, "end": v(56.59, -7.23) * mm});
            skLineSegment(sketch, "E3537", {"start": v(56.59, -7.23) * mm, "end": v(56.68, -7.26) * mm});
            skLineSegment(sketch, "E3538", {"start": v(56.68, -7.26) * mm, "end": v(56.78, -7.28) * mm});
            skLineSegment(sketch, "E3539", {"start": v(56.78, -7.28) * mm, "end": v(56.88, -7.3) * mm});
            skLineSegment(sketch, "E3540", {"start": v(56.88, -7.3) * mm, "end": v(56.98, -7.32) * mm});
            skLineSegment(sketch, "E3541", {"start": v(56.98, -7.32) * mm, "end": v(57.08, -7.33) * mm});
            skLineSegment(sketch, "E3542", {"start": v(57.08, -7.33) * mm, "end": v(57.19, -7.34) * mm});
            skLineSegment(sketch, "E3543", {"start": v(57.19, -7.34) * mm, "end": v(57.4, -7.35) * mm});
            skLineSegment(sketch, "E3544", {"start": v(57.4, -7.35) * mm, "end": v(57.53, -7.35) * mm});
            skLineSegment(sketch, "E3545", {"start": v(57.53, -7.35) * mm, "end": v(57.66, -7.34) * mm});
            skLineSegment(sketch, "E3546", {"start": v(57.66, -7.34) * mm, "end": v(57.79, -7.33) * mm});
            skLineSegment(sketch, "E3547", {"start": v(57.79, -7.33) * mm, "end": v(57.92, -7.3) * mm});
            skLineSegment(sketch, "E3548", {"start": v(57.92, -7.3) * mm, "end": v(58.18, -7.25) * mm});
            skLineSegment(sketch, "E3549", {"start": v(58.18, -7.25) * mm, "end": v(58.45, -7.17) * mm});
            skLineSegment(sketch, "E3550", {"start": v(58.45, -7.17) * mm, "end": v(58.72, -7.07) * mm});
            skLineSegment(sketch, "E3551", {"start": v(58.72, -7.07) * mm, "end": v(59, -6.95) * mm});
            skLineSegment(sketch, "E3552", {"start": v(59, -6.95) * mm, "end": v(59.3, -6.8) * mm});
            skLineSegment(sketch, "E3553", {"start": v(59.3, -6.8) * mm, "end": v(59.58, -6.64) * mm});
            skLineSegment(sketch, "E3554", {"start": v(59.58, -6.64) * mm, "end": v(59.74, -6.54) * mm});
            skLineSegment(sketch, "E3555", {"start": v(59.74, -6.54) * mm, "end": v(59.9, -6.44) * mm});
            skLineSegment(sketch, "E3556", {"start": v(59.9, -6.44) * mm, "end": v(60.23, -6.21) * mm});
            skLineSegment(sketch, "E3557", {"start": v(60.23, -6.21) * mm, "end": v(60.58, -5.96) * mm});
            skLineSegment(sketch, "E3558", {"start": v(60.58, -5.96) * mm, "end": v(60.96, -5.68) * mm});
            skLineSegment(sketch, "E3559", {"start": v(60.96, -5.68) * mm, "end": v(61.36, -5.37) * mm});
            skLineSegment(sketch, "E3560", {"start": v(61.36, -5.37) * mm, "end": v(61.78, -5.04) * mm});
            skLineSegment(sketch, "E3561", {"start": v(61.78, -5.04) * mm, "end": v(62.22, -4.68) * mm});
            skLineSegment(sketch, "E3562", {"start": v(62.22, -4.68) * mm, "end": v(62.68, -4.3) * mm});
            skLineSegment(sketch, "E3563", {"start": v(78.95, -0.47) * mm, "end": v(78.5, -0.98) * mm});
            skLineSegment(sketch, "E3564", {"start": v(78.5, -0.98) * mm, "end": v(78.08, -1.47) * mm});
            skLineSegment(sketch, "E3565", {"start": v(78.08, -1.47) * mm, "end": v(77.7, -1.94) * mm});
            skLineSegment(sketch, "E3566", {"start": v(77.7, -1.94) * mm, "end": v(77.33, -2.39) * mm});
            skLineSegment(sketch, "E3567", {"start": v(77.33, -2.39) * mm, "end": v(77, -2.81) * mm});
            skLineSegment(sketch, "E3568", {"start": v(77, -2.81) * mm, "end": v(76.7, -3.22) * mm});
            skLineSegment(sketch, "E3569", {"start": v(76.7, -3.22) * mm, "end": v(76.42, -3.61) * mm});
            skLineSegment(sketch, "E3570", {"start": v(76.42, -3.61) * mm, "end": v(76.17, -3.98) * mm});
            skLineSegment(sketch, "E3571", {"start": v(76.17, -3.98) * mm, "end": v(75.95, -4.33) * mm});
            skLineSegment(sketch, "E3572", {"start": v(75.95, -4.33) * mm, "end": v(75.85, -4.5) * mm});
            skLineSegment(sketch, "E3573", {"start": v(75.85, -4.5) * mm, "end": v(75.76, -4.66) * mm});
            skLineSegment(sketch, "E3574", {"start": v(75.76, -4.66) * mm, "end": v(75.68, -4.82) * mm});
            skLineSegment(sketch, "E3575", {"start": v(75.68, -4.82) * mm, "end": v(75.6, -4.97) * mm});
            skLineSegment(sketch, "E3576", {"start": v(75.6, -4.97) * mm, "end": v(75.53, -5.12) * mm});
            skLineSegment(sketch, "E3577", {"start": v(75.53, -5.12) * mm, "end": v(75.47, -5.27) * mm});
            skLineSegment(sketch, "E3578", {"start": v(75.47, -5.27) * mm, "end": v(75.42, -5.4) * mm});
            skLineSegment(sketch, "E3579", {"start": v(75.42, -5.4) * mm, "end": v(75.37, -5.54) * mm});
            skLineSegment(sketch, "E3580", {"start": v(75.37, -5.54) * mm, "end": v(75.33, -5.67) * mm});
            skLineSegment(sketch, "E3581", {"start": v(75.33, -5.67) * mm, "end": v(75.3, -5.79) * mm});
            skLineSegment(sketch, "E3582", {"start": v(75.3, -5.79) * mm, "end": v(75.27, -5.9) * mm});
            skLineSegment(sketch, "E3583", {"start": v(75.27, -5.9) * mm, "end": v(75.26, -6.02) * mm});
            skLineSegment(sketch, "E3584", {"start": v(75.26, -6.02) * mm, "end": v(75.24, -6.13) * mm});
            skLineSegment(sketch, "E3585", {"start": v(75.24, -6.13) * mm, "end": v(75.24, -6.23) * mm});
            skLineSegment(sketch, "E3586", {"start": v(75.24, -6.23) * mm, "end": v(75.24, -6.34) * mm});
            skLineSegment(sketch, "E3587", {"start": v(75.24, -6.34) * mm, "end": v(75.25, -6.4) * mm});
            skLineSegment(sketch, "E3588", {"start": v(75.25, -6.4) * mm, "end": v(75.25, -6.45) * mm});
            skLineSegment(sketch, "E3589", {"start": v(75.25, -6.45) * mm, "end": v(75.26, -6.5) * mm});
            skLineSegment(sketch, "E3590", {"start": v(75.26, -6.5) * mm, "end": v(75.27, -6.54) * mm});
            skLineSegment(sketch, "E3591", {"start": v(75.27, -6.54) * mm, "end": v(75.28, -6.59) * mm});
            skLineSegment(sketch, "E3592", {"start": v(75.28, -6.59) * mm, "end": v(75.29, -6.63) * mm});
            skLineSegment(sketch, "E3593", {"start": v(75.29, -6.63) * mm, "end": v(75.3, -6.67) * mm});
            skLineSegment(sketch, "E3594", {"start": v(75.3, -6.67) * mm, "end": v(75.31, -6.71) * mm});
            skLineSegment(sketch, "E3595", {"start": v(75.31, -6.71) * mm, "end": v(75.33, -6.75) * mm});
            skLineSegment(sketch, "E3596", {"start": v(75.33, -6.75) * mm, "end": v(75.34, -6.79) * mm});
            skLineSegment(sketch, "E3597", {"start": v(75.34, -6.79) * mm, "end": v(75.36, -6.82) * mm});
            skLineSegment(sketch, "E3598", {"start": v(75.36, -6.82) * mm, "end": v(75.38, -6.85) * mm});
            skLineSegment(sketch, "E3599", {"start": v(75.38, -6.85) * mm, "end": v(75.4, -6.89) * mm});
            skLineSegment(sketch, "E3600", {"start": v(75.4, -6.89) * mm, "end": v(75.43, -6.91) * mm});
            skLineSegment(sketch, "E3601", {"start": v(75.43, -6.91) * mm, "end": v(75.45, -6.94) * mm});
            skLineSegment(sketch, "E3602", {"start": v(75.45, -6.94) * mm, "end": v(75.47, -6.97) * mm});
            skLineSegment(sketch, "E3603", {"start": v(75.47, -6.97) * mm, "end": v(75.5, -7) * mm});
            skLineSegment(sketch, "E3604", {"start": v(75.5, -7) * mm, "end": v(75.53, -7.01) * mm});
            skLineSegment(sketch, "E3605", {"start": v(75.53, -7.01) * mm, "end": v(75.56, -7.03) * mm});
            skLineSegment(sketch, "E3606", {"start": v(75.56, -7.03) * mm, "end": v(75.59, -7.05) * mm});
            skLineSegment(sketch, "E3607", {"start": v(75.59, -7.05) * mm, "end": v(75.62, -7.07) * mm});
            skLineSegment(sketch, "E3608", {"start": v(75.62, -7.07) * mm, "end": v(75.66, -7.08) * mm});
            skLineSegment(sketch, "E3609", {"start": v(75.66, -7.08) * mm, "end": v(75.7, -7.1) * mm});
            skLineSegment(sketch, "E3610", {"start": v(75.7, -7.1) * mm, "end": v(75.73, -7.1) * mm});
            skLineSegment(sketch, "E3611", {"start": v(75.73, -7.1) * mm, "end": v(75.77, -7.12) * mm});
            skLineSegment(sketch, "E3612", {"start": v(75.77, -7.12) * mm, "end": v(75.8, -7.13) * mm});
            skLineSegment(sketch, "E3613", {"start": v(75.8, -7.13) * mm, "end": v(75.85, -7.13) * mm});
            skLineSegment(sketch, "E3614", {"start": v(75.85, -7.13) * mm, "end": v(75.89, -7.14) * mm});
            skLineSegment(sketch, "E3615", {"start": v(75.89, -7.14) * mm, "end": v(75.93, -7.14) * mm});
            skLineSegment(sketch, "E3616", {"start": v(75.93, -7.14) * mm, "end": v(75.98, -7.14) * mm});
            skLineSegment(sketch, "E3617", {"start": v(75.98, -7.14) * mm, "end": v(76.06, -7.14) * mm});
            skLineSegment(sketch, "E3618", {"start": v(76.06, -7.14) * mm, "end": v(76.14, -7.13) * mm});
            skLineSegment(sketch, "E3619", {"start": v(76.14, -7.13) * mm, "end": v(76.22, -7.12) * mm});
            skLineSegment(sketch, "E3620", {"start": v(76.22, -7.12) * mm, "end": v(76.3, -7.1) * mm});
            skLineSegment(sketch, "E3621", {"start": v(76.3, -7.1) * mm, "end": v(76.4, -7.08) * mm});
            skLineSegment(sketch, "E3622", {"start": v(76.4, -7.08) * mm, "end": v(76.49, -7.05) * mm});
            skLineSegment(sketch, "E3623", {"start": v(76.49, -7.05) * mm, "end": v(76.58, -7.02) * mm});
            skLineSegment(sketch, "E3624", {"start": v(76.58, -7.02) * mm, "end": v(76.68, -6.98) * mm});
            skLineSegment(sketch, "E3625", {"start": v(76.68, -6.98) * mm, "end": v(76.78, -6.94) * mm});
            skLineSegment(sketch, "E3626", {"start": v(76.78, -6.94) * mm, "end": v(76.88, -6.9) * mm});
            skLineSegment(sketch, "E3627", {"start": v(76.88, -6.9) * mm, "end": v(76.99, -6.84) * mm});
            skLineSegment(sketch, "E3628", {"start": v(76.99, -6.84) * mm, "end": v(77.1, -6.79) * mm});
            skLineSegment(sketch, "E3629", {"start": v(77.1, -6.79) * mm, "end": v(77.21, -6.72) * mm});
            skLineSegment(sketch, "E3630", {"start": v(77.21, -6.72) * mm, "end": v(77.44, -6.59) * mm});
            skLineSegment(sketch, "E3631", {"start": v(77.44, -6.59) * mm, "end": v(77.56, -6.5) * mm});
            skLineSegment(sketch, "E3632", {"start": v(77.56, -6.5) * mm, "end": v(77.69, -6.42) * mm});
            skLineSegment(sketch, "E3633", {"start": v(77.69, -6.42) * mm, "end": v(77.83, -6.33) * mm});
            skLineSegment(sketch, "E3634", {"start": v(77.83, -6.33) * mm, "end": v(77.97, -6.23) * mm});
            skLineSegment(sketch, "E3635", {"start": v(77.97, -6.23) * mm, "end": v(78.13, -6.12) * mm});
            skLineSegment(sketch, "E3636", {"start": v(78.13, -6.12) * mm, "end": v(78.29, -6) * mm});
            skLineSegment(sketch, "E3637", {"start": v(78.29, -6) * mm, "end": v(78.46, -5.88) * mm});
            skLineSegment(sketch, "E3638", {"start": v(78.46, -5.88) * mm, "end": v(78.64, -5.75) * mm});
            skLineSegment(sketch, "E3639", {"start": v(78.64, -5.75) * mm, "end": v(78.83, -5.6) * mm});
            skLineSegment(sketch, "E3640", {"start": v(78.83, -5.6) * mm, "end": v(79.02, -5.46) * mm});
            skLineSegment(sketch, "E3641", {"start": v(79.02, -5.46) * mm, "end": v(79.23, -5.3) * mm});
            skLineSegment(sketch, "E3642", {"start": v(79.23, -5.3) * mm, "end": v(79.67, -4.97) * mm});
            skLineSegment(sketch, "E3643", {"start": v(79.67, -4.97) * mm, "end": v(80.14, -4.6) * mm});
            skLineSegment(sketch, "E3644", {"start": v(80.14, -4.6) * mm, "end": v(80.64, -4.2) * mm});
            skLineSegment(sketch, "E3645", {"start": v(80.64, -4.2) * mm, "end": v(80.64, -5.66) * mm});
            skLineSegment(sketch, "E3646", {"start": v(80.64, -5.66) * mm, "end": v(79.91, -6.38) * mm});
            skLineSegment(sketch, "E3647", {"start": v(79.91, -6.38) * mm, "end": v(79.23, -7.04) * mm});
            skLineSegment(sketch, "E3648", {"start": v(79.23, -7.04) * mm, "end": v(78.6, -7.65) * mm});
            skLineSegment(sketch, "E3649", {"start": v(78.6, -7.65) * mm, "end": v(78, -8.2) * mm});
            skLineSegment(sketch, "E3650", {"start": v(78, -8.2) * mm, "end": v(77.71, -8.47) * mm});
            skLineSegment(sketch, "E3651", {"start": v(77.71, -8.47) * mm, "end": v(77.44, -8.71) * mm});
            skLineSegment(sketch, "E3652", {"start": v(77.44, -8.71) * mm, "end": v(77.18, -8.95) * mm});
            skLineSegment(sketch, "E3653", {"start": v(77.18, -8.95) * mm, "end": v(76.93, -9.17) * mm});
            skLineSegment(sketch, "E3654", {"start": v(76.93, -9.17) * mm, "end": v(76.7, -9.38) * mm});
            skLineSegment(sketch, "E3655", {"start": v(76.7, -9.38) * mm, "end": v(76.47, -9.57) * mm});
            skLineSegment(sketch, "E3656", {"start": v(76.47, -9.57) * mm, "end": v(76.25, -9.76) * mm});
            skLineSegment(sketch, "E3657", {"start": v(76.25, -9.76) * mm, "end": v(76.04, -9.93) * mm});
            skLineSegment(sketch, "E3658", {"start": v(76.04, -9.93) * mm, "end": v(75.84, -10.08) * mm});
            skLineSegment(sketch, "E3659", {"start": v(75.84, -10.08) * mm, "end": v(75.65, -10.23) * mm});
            skLineSegment(sketch, "E3660", {"start": v(75.65, -10.23) * mm, "end": v(75.46, -10.37) * mm});
            skLineSegment(sketch, "E3661", {"start": v(75.46, -10.37) * mm, "end": v(75.28, -10.5) * mm});
            skLineSegment(sketch, "E3662", {"start": v(75.28, -10.5) * mm, "end": v(75.1, -10.62) * mm});
            skLineSegment(sketch, "E3663", {"start": v(75.1, -10.62) * mm, "end": v(74.92, -10.72) * mm});
            skLineSegment(sketch, "E3664", {"start": v(74.92, -10.72) * mm, "end": v(74.75, -10.82) * mm});
            skLineSegment(sketch, "E3665", {"start": v(74.75, -10.82) * mm, "end": v(74.59, -10.9) * mm});
            skLineSegment(sketch, "E3666", {"start": v(74.59, -10.9) * mm, "end": v(74.43, -10.98) * mm});
            skLineSegment(sketch, "E3667", {"start": v(74.43, -10.98) * mm, "end": v(74.27, -11.05) * mm});
            skLineSegment(sketch, "E3668", {"start": v(74.27, -11.05) * mm, "end": v(74.12, -11.1) * mm});
            skLineSegment(sketch, "E3669", {"start": v(74.12, -11.1) * mm, "end": v(73.97, -11.15) * mm});
            skLineSegment(sketch, "E3670", {"start": v(73.97, -11.15) * mm, "end": v(73.83, -11.19) * mm});
            skLineSegment(sketch, "E3671", {"start": v(73.83, -11.19) * mm, "end": v(73.69, -11.21) * mm});
            skLineSegment(sketch, "E3672", {"start": v(73.69, -11.21) * mm, "end": v(73.56, -11.23) * mm});
            skLineSegment(sketch, "E3673", {"start": v(73.56, -11.23) * mm, "end": v(73.43, -11.23) * mm});
            skLineSegment(sketch, "E3674", {"start": v(73.43, -11.23) * mm, "end": v(73.32, -11.23) * mm});
            skLineSegment(sketch, "E3675", {"start": v(73.32, -11.23) * mm, "end": v(73.22, -11.23) * mm});
            skLineSegment(sketch, "E3676", {"start": v(73.22, -11.23) * mm, "end": v(73.12, -11.21) * mm});
            skLineSegment(sketch, "E3677", {"start": v(73.12, -11.21) * mm, "end": v(73.02, -11.2) * mm});
            skLineSegment(sketch, "E3678", {"start": v(73.02, -11.2) * mm, "end": v(72.93, -11.18) * mm});
            skLineSegment(sketch, "E3679", {"start": v(72.93, -11.18) * mm, "end": v(72.84, -11.15) * mm});
            skLineSegment(sketch, "E3680", {"start": v(72.84, -11.15) * mm, "end": v(72.75, -11.13) * mm});
            skLineSegment(sketch, "E3681", {"start": v(72.75, -11.13) * mm, "end": v(72.67, -11.1) * mm});
            skLineSegment(sketch, "E3682", {"start": v(72.67, -11.1) * mm, "end": v(72.6, -11.05) * mm});
            skLineSegment(sketch, "E3683", {"start": v(72.6, -11.05) * mm, "end": v(72.51, -11.01) * mm});
            skLineSegment(sketch, "E3684", {"start": v(72.51, -11.01) * mm, "end": v(72.44, -10.96) * mm});
            skLineSegment(sketch, "E3685", {"start": v(72.44, -10.96) * mm, "end": v(72.37, -10.91) * mm});
            skLineSegment(sketch, "E3686", {"start": v(72.37, -10.91) * mm, "end": v(72.3, -10.86) * mm});
            skLineSegment(sketch, "E3687", {"start": v(72.3, -10.86) * mm, "end": v(72.24, -10.8) * mm});
            skLineSegment(sketch, "E3688", {"start": v(72.24, -10.8) * mm, "end": v(72.18, -10.73) * mm});
            skLineSegment(sketch, "E3689", {"start": v(72.18, -10.73) * mm, "end": v(72.13, -10.66) * mm});
            skLineSegment(sketch, "E3690", {"start": v(72.13, -10.66) * mm, "end": v(72.08, -10.6) * mm});
            skLineSegment(sketch, "E3691", {"start": v(72.08, -10.6) * mm, "end": v(72.03, -10.51) * mm});
            skLineSegment(sketch, "E3692", {"start": v(72.03, -10.51) * mm, "end": v(71.98, -10.43) * mm});
            skLineSegment(sketch, "E3693", {"start": v(71.98, -10.43) * mm, "end": v(71.94, -10.34) * mm});
            skLineSegment(sketch, "E3694", {"start": v(71.94, -10.34) * mm, "end": v(71.9, -10.25) * mm});
            skLineSegment(sketch, "E3695", {"start": v(71.9, -10.25) * mm, "end": v(71.87, -10.16) * mm});
            skLineSegment(sketch, "E3696", {"start": v(71.87, -10.16) * mm, "end": v(71.83, -10.06) * mm});
            skLineSegment(sketch, "E3697", {"start": v(71.83, -10.06) * mm, "end": v(71.8, -9.95) * mm});
            skLineSegment(sketch, "E3698", {"start": v(71.8, -9.95) * mm, "end": v(71.78, -9.84) * mm});
            skLineSegment(sketch, "E3699", {"start": v(71.78, -9.84) * mm, "end": v(71.76, -9.73) * mm});
            skLineSegment(sketch, "E3700", {"start": v(71.76, -9.73) * mm, "end": v(71.74, -9.61) * mm});
            skLineSegment(sketch, "E3701", {"start": v(71.74, -9.61) * mm, "end": v(71.72, -9.49) * mm});
            skLineSegment(sketch, "E3702", {"start": v(71.72, -9.49) * mm, "end": v(71.7, -9.23) * mm});
            skLineSegment(sketch, "E3703", {"start": v(71.7, -9.23) * mm, "end": v(71.7, -8.96) * mm});
            skLineSegment(sketch, "E3704", {"start": v(71.7, -8.96) * mm, "end": v(71.7, -8.62) * mm});
            skLineSegment(sketch, "E3705", {"start": v(71.7, -8.62) * mm, "end": v(71.75, -8.29) * mm});
            skLineSegment(sketch, "E3706", {"start": v(71.75, -8.29) * mm, "end": v(71.82, -7.95) * mm});
            skLineSegment(sketch, "E3707", {"start": v(71.82, -7.95) * mm, "end": v(71.9, -7.63) * mm});
            skLineSegment(sketch, "E3708", {"start": v(71.9, -7.63) * mm, "end": v(72.02, -7.3) * mm});
            skLineSegment(sketch, "E3709", {"start": v(72.02, -7.3) * mm, "end": v(72.16, -6.96) * mm});
            skLineSegment(sketch, "E3710", {"start": v(72.16, -6.96) * mm, "end": v(72.3, -6.62) * mm});
            skLineSegment(sketch, "E3711", {"start": v(72.3, -6.62) * mm, "end": v(72.48, -6.28) * mm});
            skLineSegment(sketch, "E3712", {"start": v(72.48, -6.28) * mm, "end": v(72.53, -6.18) * mm});
            skLineSegment(sketch, "E3713", {"start": v(72.53, -6.18) * mm, "end": v(72.58, -6.09) * mm});
            skLineSegment(sketch, "E3714", {"start": v(72.58, -6.09) * mm, "end": v(72.63, -5.99) * mm});
            skLineSegment(sketch, "E3715", {"start": v(72.63, -5.99) * mm, "end": v(72.7, -5.88) * mm});
            skLineSegment(sketch, "E3716", {"start": v(72.7, -5.88) * mm, "end": v(72.82, -5.66) * mm});
            skLineSegment(sketch, "E3717", {"start": v(72.82, -5.66) * mm, "end": v(72.95, -5.41) * mm});
            skLineSegment(sketch, "E3718", {"start": v(72.95, -5.41) * mm, "end": v(73.1, -5.15) * mm});
            skLineSegment(sketch, "E3719", {"start": v(73.1, -5.15) * mm, "end": v(73.26, -4.87) * mm});
            skLineSegment(sketch, "E3720", {"start": v(73.26, -4.87) * mm, "end": v(73.43, -4.57) * mm});
            skLineSegment(sketch, "E3721", {"start": v(73.43, -4.57) * mm, "end": v(73.62, -4.25) * mm});
            skLineSegment(sketch, "E3722", {"start": v(73.62, -4.25) * mm, "end": v(74.01, -3.57) * mm});
            skLineSegment(sketch, "E3723", {"start": v(74.01, -3.57) * mm, "end": v(74.43, -2.84) * mm});
            skLineSegment(sketch, "E3724", {"start": v(74.43, -2.84) * mm, "end": v(74.89, -2.07) * mm});
            skLineSegment(sketch, "E3725", {"start": v(74.89, -2.07) * mm, "end": v(75.37, -1.26) * mm});
            skLineSegment(sketch, "E3726", {"start": v(75.37, -1.26) * mm, "end": v(75.21, -1.34) * mm});
            skLineSegment(sketch, "E3727", {"start": v(75.21, -1.34) * mm, "end": v(75.06, -1.43) * mm});
            skLineSegment(sketch, "E3728", {"start": v(75.06, -1.43) * mm, "end": v(74.9, -1.53) * mm});
            skLineSegment(sketch, "E3729", {"start": v(74.9, -1.53) * mm, "end": v(74.73, -1.64) * mm});
            skLineSegment(sketch, "E3730", {"start": v(74.73, -1.64) * mm, "end": v(74.56, -1.76) * mm});
            skLineSegment(sketch, "E3731", {"start": v(74.56, -1.76) * mm, "end": v(74.38, -1.88) * mm});
            skLineSegment(sketch, "E3732", {"start": v(74.38, -1.88) * mm, "end": v(74.2, -2.02) * mm});
            skLineSegment(sketch, "E3733", {"start": v(74.2, -2.02) * mm, "end": v(73.82, -2.32) * mm});
            skLineSegment(sketch, "E3734", {"start": v(73.82, -2.32) * mm, "end": v(73.42, -2.66) * mm});
            skLineSegment(sketch, "E3735", {"start": v(73.42, -2.66) * mm, "end": v(73, -3.04) * mm});
            skLineSegment(sketch, "E3736", {"start": v(73, -3.04) * mm, "end": v(72.57, -3.46) * mm});
            skLineSegment(sketch, "E3737", {"start": v(72.57, -3.46) * mm, "end": v(72.35, -3.68) * mm});
            skLineSegment(sketch, "E3738", {"start": v(72.35, -3.68) * mm, "end": v(71.78, -4.24) * mm});
            skLineSegment(sketch, "E3739", {"start": v(71.78, -4.24) * mm, "end": v(71.26, -4.8) * mm});
            skLineSegment(sketch, "E3740", {"start": v(71.26, -4.8) * mm, "end": v(70.78, -5.33) * mm});
            skLineSegment(sketch, "E3741", {"start": v(70.78, -5.33) * mm, "end": v(70.35, -5.85) * mm});
            skLineSegment(sketch, "E3742", {"start": v(70.35, -5.85) * mm, "end": v(69.93, -6.38) * mm});
            skLineSegment(sketch, "E3743", {"start": v(69.93, -6.38) * mm, "end": v(69.5, -6.93) * mm});
            skLineSegment(sketch, "E3744", {"start": v(69.5, -6.93) * mm, "end": v(69.04, -7.52) * mm});
            skLineSegment(sketch, "E3745", {"start": v(69.04, -7.52) * mm, "end": v(68.57, -8.13) * mm});
            skLineSegment(sketch, "E3746", {"start": v(68.57, -8.13) * mm, "end": v(68.35, -8.43) * mm});
            skLineSegment(sketch, "E3747", {"start": v(68.35, -8.43) * mm, "end": v(68.14, -8.7) * mm});
            skLineSegment(sketch, "E3748", {"start": v(68.14, -8.7) * mm, "end": v(68.04, -8.83) * mm});
            skLineSegment(sketch, "E3749", {"start": v(68.04, -8.83) * mm, "end": v(67.95, -8.95) * mm});
            skLineSegment(sketch, "E3750", {"start": v(67.95, -8.95) * mm, "end": v(67.85, -9.07) * mm});
            skLineSegment(sketch, "E3751", {"start": v(67.85, -9.07) * mm, "end": v(67.77, -9.18) * mm});
            skLineSegment(sketch, "E3752", {"start": v(67.77, -9.18) * mm, "end": v(67.68, -9.28) * mm});
            skLineSegment(sketch, "E3753", {"start": v(67.68, -9.28) * mm, "end": v(67.6, -9.38) * mm});
            skLineSegment(sketch, "E3754", {"start": v(67.6, -9.38) * mm, "end": v(67.53, -9.47) * mm});
            skLineSegment(sketch, "E3755", {"start": v(67.53, -9.47) * mm, "end": v(67.45, -9.55) * mm});
            skLineSegment(sketch, "E3756", {"start": v(67.45, -9.55) * mm, "end": v(67.39, -9.63) * mm});
            skLineSegment(sketch, "E3757", {"start": v(67.39, -9.63) * mm, "end": v(67.32, -9.7) * mm});
            skLineSegment(sketch, "E3758", {"start": v(67.32, -9.7) * mm, "end": v(67.26, -9.76) * mm});
            skLineSegment(sketch, "E3759", {"start": v(67.26, -9.76) * mm, "end": v(67.23, -9.8) * mm});
            skLineSegment(sketch, "E3760", {"start": v(67.23, -9.8) * mm, "end": v(67.2, -9.82) * mm});
            skLineSegment(sketch, "E3761", {"start": v(67.2, -9.82) * mm, "end": v(67.15, -9.87) * mm});
            skLineSegment(sketch, "E3762", {"start": v(67.15, -9.87) * mm, "end": v(67.1, -9.92) * mm});
            skLineSegment(sketch, "E3763", {"start": v(67.1, -9.92) * mm, "end": v(67.04, -9.96) * mm});
            skLineSegment(sketch, "E3764", {"start": v(67.04, -9.96) * mm, "end": v(67, -10) * mm});
            skLineSegment(sketch, "E3765", {"start": v(67, -10) * mm, "end": v(66.94, -10.04) * mm});
            skLineSegment(sketch, "E3766", {"start": v(66.94, -10.04) * mm, "end": v(66.88, -10.08) * mm});
            skLineSegment(sketch, "E3767", {"start": v(66.88, -10.08) * mm, "end": v(66.83, -10.1) * mm});
            skLineSegment(sketch, "E3768", {"start": v(66.83, -10.1) * mm, "end": v(66.78, -10.14) * mm});
            skLineSegment(sketch, "E3769", {"start": v(66.78, -10.14) * mm, "end": v(66.72, -10.16) * mm});
            skLineSegment(sketch, "E3770", {"start": v(66.72, -10.16) * mm, "end": v(66.67, -10.18) * mm});
            skLineSegment(sketch, "E3771", {"start": v(66.67, -10.18) * mm, "end": v(66.61, -10.2) * mm});
            skLineSegment(sketch, "E3772", {"start": v(66.61, -10.2) * mm, "end": v(66.56, -10.22) * mm});
            skLineSegment(sketch, "E3773", {"start": v(66.56, -10.22) * mm, "end": v(66.5, -10.23) * mm});
            skLineSegment(sketch, "E3774", {"start": v(66.5, -10.23) * mm, "end": v(66.45, -10.24) * mm});
            skLineSegment(sketch, "E3775", {"start": v(66.45, -10.24) * mm, "end": v(66.4, -10.24) * mm});
            skLineSegment(sketch, "E3776", {"start": v(66.4, -10.24) * mm, "end": v(66.34, -10.24) * mm});
            skLineSegment(sketch, "E3777", {"start": v(66.34, -10.24) * mm, "end": v(66.3, -10.24) * mm});
            skLineSegment(sketch, "E3778", {"start": v(66.3, -10.24) * mm, "end": v(66.25, -10.24) * mm});
            skLineSegment(sketch, "E3779", {"start": v(66.25, -10.24) * mm, "end": v(66.21, -10.23) * mm});
            skLineSegment(sketch, "E3780", {"start": v(66.21, -10.23) * mm, "end": v(66.17, -10.22) * mm});
            skLineSegment(sketch, "E3781", {"start": v(66.17, -10.22) * mm, "end": v(66.13, -10.2) * mm});
            skLineSegment(sketch, "E3782", {"start": v(66.13, -10.2) * mm, "end": v(66.09, -10.2) * mm});
            skLineSegment(sketch, "E3783", {"start": v(66.09, -10.2) * mm, "end": v(66.05, -10.18) * mm});
            skLineSegment(sketch, "E3784", {"start": v(66.05, -10.18) * mm, "end": v(66, -10.15) * mm});
            skLineSegment(sketch, "E3785", {"start": v(66, -10.15) * mm, "end": v(65.97, -10.13) * mm});
            skLineSegment(sketch, "E3786", {"start": v(65.97, -10.13) * mm, "end": v(65.93, -10.1) * mm});
            skLineSegment(sketch, "E3787", {"start": v(65.93, -10.1) * mm, "end": v(65.89, -10.08) * mm});
            skLineSegment(sketch, "E3788", {"start": v(65.89, -10.08) * mm, "end": v(65.85, -10.04) * mm});
            skLineSegment(sketch, "E3789", {"start": v(65.85, -10.04) * mm, "end": v(65.8, -10) * mm});
            skLineSegment(sketch, "E3790", {"start": v(65.8, -10) * mm, "end": v(65.77, -9.97) * mm});
            skLineSegment(sketch, "E3791", {"start": v(65.77, -9.97) * mm, "end": v(65.73, -9.93) * mm});
            skLineSegment(sketch, "E3792", {"start": v(65.73, -9.93) * mm, "end": v(65.69, -9.89) * mm});
            skLineSegment(sketch, "E3793", {"start": v(65.69, -9.89) * mm, "end": v(65.65, -9.84) * mm});
            skLineSegment(sketch, "E3794", {"start": v(65.65, -9.84) * mm, "end": v(65.61, -9.8) * mm});
            skLineSegment(sketch, "E3795", {"start": v(65.61, -9.8) * mm, "end": v(65.54, -9.7) * mm});
            skLineSegment(sketch, "E3796", {"start": v(65.54, -9.7) * mm, "end": v(65.46, -9.57) * mm});
            skLineSegment(sketch, "E3797", {"start": v(65.46, -9.57) * mm, "end": v(65.38, -9.45) * mm});
            skLineSegment(sketch, "E3798", {"start": v(65.38, -9.45) * mm, "end": v(65.31, -9.3) * mm});
            skLineSegment(sketch, "E3799", {"start": v(65.31, -9.3) * mm, "end": v(65.24, -9.16) * mm});
            skLineSegment(sketch, "E3800", {"start": v(65.24, -9.16) * mm, "end": v(65.16, -9) * mm});
            skLineSegment(sketch, "E3801", {"start": v(65.16, -9) * mm, "end": v(65.1, -8.83) * mm});
            skLineSegment(sketch, "E3802", {"start": v(65.1, -8.83) * mm, "end": v(64.96, -8.47) * mm});
            skLineSegment(sketch, "E3803", {"start": v(64.96, -8.47) * mm, "end": v(64.84, -8.1) * mm});
            skLineSegment(sketch, "E3804", {"start": v(64.84, -8.1) * mm, "end": v(64.75, -7.7) * mm});
            skLineSegment(sketch, "E3805", {"start": v(64.75, -7.7) * mm, "end": v(64.67, -7.3) * mm});
            skLineSegment(sketch, "E3806", {"start": v(64.67, -7.3) * mm, "end": v(64.6, -6.88) * mm});
            skLineSegment(sketch, "E3807", {"start": v(64.6, -6.88) * mm, "end": v(64.56, -6.45) * mm});
            skLineSegment(sketch, "E3808", {"start": v(64.56, -6.45) * mm, "end": v(64.53, -6) * mm});
            skLineSegment(sketch, "E3809", {"start": v(64.53, -6) * mm, "end": v(64.52, -5.54) * mm});
            skLineSegment(sketch, "E3810", {"start": v(64.52, -5.54) * mm, "end": v(64.53, -5.26) * mm});
            skLineSegment(sketch, "E3811", {"start": v(64.53, -5.26) * mm, "end": v(64.54, -4.99) * mm});
            skLineSegment(sketch, "E3812", {"start": v(64.54, -4.99) * mm, "end": v(64.56, -4.74) * mm});
            skLineSegment(sketch, "E3813", {"start": v(64.56, -4.74) * mm, "end": v(64.59, -4.5) * mm});
            skLineSegment(sketch, "E3814", {"start": v(64.59, -4.5) * mm, "end": v(64.62, -4.29) * mm});
            skLineSegment(sketch, "E3815", {"start": v(64.62, -4.29) * mm, "end": v(64.67, -4.08) * mm});
            skLineSegment(sketch, "E3816", {"start": v(64.67, -4.08) * mm, "end": v(64.7, -3.99) * mm});
            skLineSegment(sketch, "E3817", {"start": v(64.7, -3.99) * mm, "end": v(64.72, -3.9) * mm});
            skLineSegment(sketch, "E3818", {"start": v(64.72, -3.9) * mm, "end": v(64.75, -3.8) * mm});
            skLineSegment(sketch, "E3819", {"start": v(64.75, -3.8) * mm, "end": v(64.78, -3.72) * mm});
            skLineSegment(sketch, "E3820", {"start": v(64.78, -3.72) * mm, "end": v(64.81, -3.64) * mm});
            skLineSegment(sketch, "E3821", {"start": v(64.81, -3.64) * mm, "end": v(64.85, -3.55) * mm});
            skLineSegment(sketch, "E3822", {"start": v(64.85, -3.55) * mm, "end": v(64.9, -3.46) * mm});
            skLineSegment(sketch, "E3823", {"start": v(64.9, -3.46) * mm, "end": v(64.95, -3.36) * mm});
            skLineSegment(sketch, "E3824", {"start": v(64.95, -3.36) * mm, "end": v(65, -3.26) * mm});
            skLineSegment(sketch, "E3825", {"start": v(65, -3.26) * mm, "end": v(65.05, -3.16) * mm});
            skLineSegment(sketch, "E3826", {"start": v(65.05, -3.16) * mm, "end": v(65.11, -3.05) * mm});
            skLineSegment(sketch, "E3827", {"start": v(65.11, -3.05) * mm, "end": v(65.18, -2.93) * mm});
            skLineSegment(sketch, "E3828", {"start": v(65.18, -2.93) * mm, "end": v(65.32, -2.7) * mm});
            skLineSegment(sketch, "E3829", {"start": v(65.32, -2.7) * mm, "end": v(65.47, -2.43) * mm});
            skLineSegment(sketch, "E3830", {"start": v(65.47, -2.43) * mm, "end": v(65.64, -2.16) * mm});
            skLineSegment(sketch, "E3831", {"start": v(65.64, -2.16) * mm, "end": v(65.83, -1.87) * mm});
            skLineSegment(sketch, "E3832", {"start": v(65.83, -1.87) * mm, "end": v(66.19, -1.33) * mm});
            skLineSegment(sketch, "E3833", {"start": v(66.19, -1.33) * mm, "end": v(66.53, -0.82) * mm});
            skLineSegment(sketch, "E3834", {"start": v(66.53, -0.82) * mm, "end": v(66.87, -0.36) * mm});
            skLineSegment(sketch, "E3835", {"start": v(66.87, -0.36) * mm, "end": v(67.19, 0.07) * mm});
            skLineSegment(sketch, "E3836", {"start": v(67.19, 0.07) * mm, "end": v(67.5, 0.46) * mm});
            skLineSegment(sketch, "E3837", {"start": v(67.5, 0.46) * mm, "end": v(67.79, 0.81) * mm});
            skLineSegment(sketch, "E3838", {"start": v(67.79, 0.81) * mm, "end": v(67.93, 0.97) * mm});
            skLineSegment(sketch, "E3839", {"start": v(67.93, 0.97) * mm, "end": v(68.07, 1.13) * mm});
            skLineSegment(sketch, "E3840", {"start": v(68.07, 1.13) * mm, "end": v(68.2, 1.27) * mm});
            skLineSegment(sketch, "E3841", {"start": v(68.2, 1.27) * mm, "end": v(68.34, 1.4) * mm});
            skLineSegment(sketch, "E3842", {"start": v(68.34, 1.4) * mm, "end": v(68.47, 1.53) * mm});
            skLineSegment(sketch, "E3843", {"start": v(68.47, 1.53) * mm, "end": v(68.6, 1.65) * mm});
            skLineSegment(sketch, "E3844", {"start": v(68.6, 1.65) * mm, "end": v(68.73, 1.76) * mm});
            skLineSegment(sketch, "E3845", {"start": v(68.73, 1.76) * mm, "end": v(68.86, 1.86) * mm});
            skLineSegment(sketch, "E3846", {"start": v(68.86, 1.86) * mm, "end": v(69, 1.96) * mm});
            skLineSegment(sketch, "E3847", {"start": v(69, 1.96) * mm, "end": v(69.12, 2.05) * mm});
            skLineSegment(sketch, "E3848", {"start": v(69.12, 2.05) * mm, "end": v(69.25, 2.12) * mm});
            skLineSegment(sketch, "E3849", {"start": v(69.25, 2.12) * mm, "end": v(69.38, 2.2) * mm});
            skLineSegment(sketch, "E3850", {"start": v(69.38, 2.2) * mm, "end": v(69.5, 2.26) * mm});
            skLineSegment(sketch, "E3851", {"start": v(69.5, 2.26) * mm, "end": v(69.63, 2.3) * mm});
            skLineSegment(sketch, "E3852", {"start": v(69.63, 2.3) * mm, "end": v(69.75, 2.35) * mm});
            skLineSegment(sketch, "E3853", {"start": v(69.75, 2.35) * mm, "end": v(69.88, 2.4) * mm});
            skLineSegment(sketch, "E3854", {"start": v(69.88, 2.4) * mm, "end": v(70, 2.42) * mm});
            skLineSegment(sketch, "E3855", {"start": v(70, 2.42) * mm, "end": v(70.12, 2.44) * mm});
            skLineSegment(sketch, "E3856", {"start": v(70.12, 2.44) * mm, "end": v(70.25, 2.45) * mm});
            skLineSegment(sketch, "E3857", {"start": v(70.25, 2.45) * mm, "end": v(70.37, 2.46) * mm});
            skLineSegment(sketch, "E3858", {"start": v(70.37, 2.46) * mm, "end": v(70.53, 2.45) * mm});
            skLineSegment(sketch, "E3859", {"start": v(70.53, 2.45) * mm, "end": v(70.69, 2.44) * mm});
            skLineSegment(sketch, "E3860", {"start": v(70.69, 2.44) * mm, "end": v(70.84, 2.43) * mm});
            skLineSegment(sketch, "E3861", {"start": v(70.84, 2.43) * mm, "end": v(70.97, 2.4) * mm});
            skLineSegment(sketch, "E3862", {"start": v(70.97, 2.4) * mm, "end": v(71.1, 2.37) * mm});
            skLineSegment(sketch, "E3863", {"start": v(71.1, 2.37) * mm, "end": v(71.17, 2.35) * mm});
            skLineSegment(sketch, "E3864", {"start": v(71.17, 2.35) * mm, "end": v(71.23, 2.33) * mm});
            skLineSegment(sketch, "E3865", {"start": v(71.23, 2.33) * mm, "end": v(71.28, 2.3) * mm});
            skLineSegment(sketch, "E3866", {"start": v(71.28, 2.3) * mm, "end": v(71.34, 2.28) * mm});
            skLineSegment(sketch, "E3867", {"start": v(71.34, 2.28) * mm, "end": v(71.4, 2.25) * mm});
            skLineSegment(sketch, "E3868", {"start": v(71.4, 2.25) * mm, "end": v(71.44, 2.23) * mm});
            skLineSegment(sketch, "E3869", {"start": v(71.44, 2.23) * mm, "end": v(71.5, 2.2) * mm});
            skLineSegment(sketch, "E3870", {"start": v(71.5, 2.2) * mm, "end": v(71.54, 2.16) * mm});
            skLineSegment(sketch, "E3871", {"start": v(71.54, 2.16) * mm, "end": v(71.59, 2.13) * mm});
            skLineSegment(sketch, "E3872", {"start": v(71.59, 2.13) * mm, "end": v(71.63, 2.1) * mm});
            skLineSegment(sketch, "E3873", {"start": v(71.63, 2.1) * mm, "end": v(71.67, 2.06) * mm});
            skLineSegment(sketch, "E3874", {"start": v(71.67, 2.06) * mm, "end": v(71.7, 2.02) * mm});
            skLineSegment(sketch, "E3875", {"start": v(71.7, 2.02) * mm, "end": v(71.73, 1.97) * mm});
            skLineSegment(sketch, "E3876", {"start": v(71.73, 1.97) * mm, "end": v(71.76, 1.93) * mm});
            skLineSegment(sketch, "E3877", {"start": v(71.76, 1.93) * mm, "end": v(71.78, 1.88) * mm});
            skLineSegment(sketch, "E3878", {"start": v(71.78, 1.88) * mm, "end": v(71.8, 1.84) * mm});
            skLineSegment(sketch, "E3879", {"start": v(71.8, 1.84) * mm, "end": v(71.82, 1.79) * mm});
            skLineSegment(sketch, "E3880", {"start": v(71.82, 1.79) * mm, "end": v(71.84, 1.74) * mm});
            skLineSegment(sketch, "E3881", {"start": v(71.84, 1.74) * mm, "end": v(71.85, 1.68) * mm});
            skLineSegment(sketch, "E3882", {"start": v(71.85, 1.68) * mm, "end": v(71.86, 1.63) * mm});
            skLineSegment(sketch, "E3883", {"start": v(71.86, 1.63) * mm, "end": v(71.86, 1.57) * mm});
            skLineSegment(sketch, "E3884", {"start": v(71.86, 1.57) * mm, "end": v(71.87, 1.5) * mm});
            skLineSegment(sketch, "E3885", {"start": v(71.87, 1.5) * mm, "end": v(71.86, 1.46) * mm});
            skLineSegment(sketch, "E3886", {"start": v(71.86, 1.46) * mm, "end": v(71.86, 1.4) * mm});
            skLineSegment(sketch, "E3887", {"start": v(71.86, 1.4) * mm, "end": v(71.85, 1.35) * mm});
            skLineSegment(sketch, "E3888", {"start": v(71.85, 1.35) * mm, "end": v(71.83, 1.3) * mm});
            skLineSegment(sketch, "E3889", {"start": v(71.83, 1.3) * mm, "end": v(71.82, 1.24) * mm});
            skLineSegment(sketch, "E3890", {"start": v(71.82, 1.24) * mm, "end": v(71.8, 1.18) * mm});
            skLineSegment(sketch, "E3891", {"start": v(71.8, 1.18) * mm, "end": v(71.77, 1.12) * mm});
            skLineSegment(sketch, "E3892", {"start": v(71.77, 1.12) * mm, "end": v(71.74, 1.07) * mm});
            skLineSegment(sketch, "E3893", {"start": v(71.74, 1.07) * mm, "end": v(71.67, 0.95) * mm});
            skLineSegment(sketch, "E3894", {"start": v(71.67, 0.95) * mm, "end": v(71.6, 0.84) * mm});
            skLineSegment(sketch, "E3895", {"start": v(71.6, 0.84) * mm, "end": v(71.53, 0.74) * mm});
            skLineSegment(sketch, "E3896", {"start": v(71.53, 0.74) * mm, "end": v(71.44, 0.64) * mm});
            skLineSegment(sketch, "E3897", {"start": v(71.44, 0.64) * mm, "end": v(71.43, 0.63) * mm});
            skLineSegment(sketch, "E3898", {"start": v(71.43, 0.63) * mm, "end": v(71.42, 0.62) * mm});
            skLineSegment(sketch, "E3899", {"start": v(71.42, 0.62) * mm, "end": v(71.41, 0.6) * mm});
            skLineSegment(sketch, "E3900", {"start": v(71.41, 0.6) * mm, "end": v(71.4, 0.6) * mm});
            skLineSegment(sketch, "E3901", {"start": v(71.4, 0.6) * mm, "end": v(71.39, 0.58) * mm});
            skLineSegment(sketch, "E3902", {"start": v(71.39, 0.58) * mm, "end": v(71.38, 0.56) * mm});
            skLineSegment(sketch, "E3903", {"start": v(71.38, 0.56) * mm, "end": v(71.36, 0.54) * mm});
            skLineSegment(sketch, "E3904", {"start": v(71.36, 0.54) * mm, "end": v(71.33, 0.5) * mm});
            skLineSegment(sketch, "E3905", {"start": v(71.33, 0.5) * mm, "end": v(71.3, 0.47) * mm});
            skLineSegment(sketch, "E3906", {"start": v(71.3, 0.47) * mm, "end": v(71.26, 0.43) * mm});
            skLineSegment(sketch, "E3907", {"start": v(71.26, 0.43) * mm, "end": v(71.23, 0.39) * mm});
            skLineSegment(sketch, "E3908", {"start": v(71.23, 0.39) * mm, "end": v(71.19, 0.34) * mm});
            skLineSegment(sketch, "E3909", {"start": v(71.19, 0.34) * mm, "end": v(71.14, 0.3) * mm});
            skLineSegment(sketch, "E3910", {"start": v(71.14, 0.3) * mm, "end": v(71.1, 0.24) * mm});
            skLineSegment(sketch, "E3911", {"start": v(71.1, 0.24) * mm, "end": v(71.05, 0.19) * mm});
            skLineSegment(sketch, "E3912", {"start": v(71.05, 0.19) * mm, "end": v(71, 0.13) * mm});
            skLineSegment(sketch, "E3913", {"start": v(71, 0.13) * mm, "end": v(70.94, 0.07) * mm});
            skLineSegment(sketch, "E3914", {"start": v(70.94, 0.07) * mm, "end": v(70.88, 0) * mm});
            skLineSegment(sketch, "E3915", {"start": v(70.88, 0) * mm, "end": v(70.79, -0.1) * mm});
            skLineSegment(sketch, "E3916", {"start": v(70.79, -0.1) * mm, "end": v(70.39, -0.55) * mm});
            skLineSegment(sketch, "E3917", {"start": v(70.39, -0.55) * mm, "end": v(70, -0.98) * mm});
            skLineSegment(sketch, "E3918", {"start": v(70, -0.98) * mm, "end": v(69.66, -1.39) * mm});
            skLineSegment(sketch, "E3919", {"start": v(69.66, -1.39) * mm, "end": v(69.33, -1.78) * mm});
            skLineSegment(sketch, "E3920", {"start": v(69.33, -1.78) * mm, "end": v(69.03, -2.15) * mm});
            skLineSegment(sketch, "E3921", {"start": v(69.03, -2.15) * mm, "end": v(68.76, -2.5) * mm});
            skLineSegment(sketch, "E3922", {"start": v(68.76, -2.5) * mm, "end": v(68.51, -2.83) * mm});
            skLineSegment(sketch, "E3923", {"start": v(68.51, -2.83) * mm, "end": v(68.29, -3.14) * mm});
            skLineSegment(sketch, "E3924", {"start": v(68.29, -3.14) * mm, "end": v(68.19, -3.29) * mm});
            skLineSegment(sketch, "E3925", {"start": v(68.19, -3.29) * mm, "end": v(68.1, -3.43) * mm});
            skLineSegment(sketch, "E3926", {"start": v(68.1, -3.43) * mm, "end": v(68, -3.56) * mm});
            skLineSegment(sketch, "E3927", {"start": v(68, -3.56) * mm, "end": v(67.92, -3.7) * mm});
            skLineSegment(sketch, "E3928", {"start": v(67.92, -3.7) * mm, "end": v(67.85, -3.82) * mm});
            skLineSegment(sketch, "E3929", {"start": v(67.85, -3.82) * mm, "end": v(67.78, -3.94) * mm});
            skLineSegment(sketch, "E3930", {"start": v(67.78, -3.94) * mm, "end": v(67.72, -4.06) * mm});
            skLineSegment(sketch, "E3931", {"start": v(67.72, -4.06) * mm, "end": v(67.66, -4.17) * mm});
            skLineSegment(sketch, "E3932", {"start": v(67.66, -4.17) * mm, "end": v(67.62, -4.28) * mm});
            skLineSegment(sketch, "E3933", {"start": v(67.62, -4.28) * mm, "end": v(67.57, -4.38) * mm});
            skLineSegment(sketch, "E3934", {"start": v(67.57, -4.38) * mm, "end": v(67.54, -4.48) * mm});
            skLineSegment(sketch, "E3935", {"start": v(67.54, -4.48) * mm, "end": v(67.5, -4.57) * mm});
            skLineSegment(sketch, "E3936", {"start": v(67.5, -4.57) * mm, "end": v(67.5, -4.61) * mm});
            skLineSegment(sketch, "E3937", {"start": v(67.5, -4.61) * mm, "end": v(67.49, -4.66) * mm});
            skLineSegment(sketch, "E3938", {"start": v(67.49, -4.66) * mm, "end": v(67.48, -4.7) * mm});
            skLineSegment(sketch, "E3939", {"start": v(67.48, -4.7) * mm, "end": v(67.47, -4.74) * mm});
            skLineSegment(sketch, "E3940", {"start": v(67.47, -4.74) * mm, "end": v(67.46, -4.78) * mm});
            skLineSegment(sketch, "E3941", {"start": v(67.46, -4.78) * mm, "end": v(67.46, -4.81) * mm});
            skLineSegment(sketch, "E3942", {"start": v(67.46, -4.81) * mm, "end": v(67.46, -4.85) * mm});
            skLineSegment(sketch, "E3943", {"start": v(67.46, -4.85) * mm, "end": v(67.46, -4.88) * mm});
            skLineSegment(sketch, "E3944", {"start": v(67.46, -4.88) * mm, "end": v(67.46, -4.96) * mm});
            skLineSegment(sketch, "E3945", {"start": v(67.46, -4.96) * mm, "end": v(67.46, -5.03) * mm});
            skLineSegment(sketch, "E3946", {"start": v(67.46, -5.03) * mm, "end": v(67.47, -5.06) * mm});
            skLineSegment(sketch, "E3947", {"start": v(67.47, -5.06) * mm, "end": v(67.47, -5.1) * mm});
            skLineSegment(sketch, "E3948", {"start": v(67.47, -5.1) * mm, "end": v(67.48, -5.12) * mm});
            skLineSegment(sketch, "E3949", {"start": v(67.48, -5.12) * mm, "end": v(67.48, -5.15) * mm});
            skLineSegment(sketch, "E3950", {"start": v(67.48, -5.15) * mm, "end": v(67.49, -5.18) * mm});
            skLineSegment(sketch, "E3951", {"start": v(67.49, -5.18) * mm, "end": v(67.5, -5.2) * mm});
            skLineSegment(sketch, "E3952", {"start": v(67.5, -5.2) * mm, "end": v(67.5, -5.23) * mm});
            skLineSegment(sketch, "E3953", {"start": v(67.5, -5.23) * mm, "end": v(67.51, -5.26) * mm});
            skLineSegment(sketch, "E3954", {"start": v(67.51, -5.26) * mm, "end": v(67.52, -5.28) * mm});
            skLineSegment(sketch, "E3955", {"start": v(67.52, -5.28) * mm, "end": v(67.53, -5.3) * mm});
            skLineSegment(sketch, "E3956", {"start": v(67.53, -5.3) * mm, "end": v(67.54, -5.32) * mm});
            skLineSegment(sketch, "E3957", {"start": v(67.54, -5.32) * mm, "end": v(67.56, -5.34) * mm});
            skLineSegment(sketch, "E3958", {"start": v(67.56, -5.34) * mm, "end": v(67.57, -5.36) * mm});
            skLineSegment(sketch, "E3959", {"start": v(67.57, -5.36) * mm, "end": v(67.58, -5.38) * mm});
            skLineSegment(sketch, "E3960", {"start": v(67.58, -5.38) * mm, "end": v(67.6, -5.4) * mm});
            skLineSegment(sketch, "E3961", {"start": v(67.6, -5.4) * mm, "end": v(67.61, -5.4) * mm});
            skLineSegment(sketch, "E3962", {"start": v(67.61, -5.4) * mm, "end": v(67.63, -5.42) * mm});
            skLineSegment(sketch, "E3963", {"start": v(67.63, -5.42) * mm, "end": v(67.65, -5.44) * mm});
            skLineSegment(sketch, "E3964", {"start": v(67.65, -5.44) * mm, "end": v(67.66, -5.45) * mm});
            skLineSegment(sketch, "E3965", {"start": v(67.66, -5.45) * mm, "end": v(67.68, -5.46) * mm});
            skLineSegment(sketch, "E3966", {"start": v(67.68, -5.46) * mm, "end": v(67.7, -5.47) * mm});
            skLineSegment(sketch, "E3967", {"start": v(67.7, -5.47) * mm, "end": v(67.72, -5.47) * mm});
            skLineSegment(sketch, "E3968", {"start": v(67.72, -5.47) * mm, "end": v(67.74, -5.48) * mm});
            skLineSegment(sketch, "E3969", {"start": v(67.74, -5.48) * mm, "end": v(67.76, -5.49) * mm});
            skLineSegment(sketch, "E3970", {"start": v(67.76, -5.49) * mm, "end": v(67.79, -5.5) * mm});
            skLineSegment(sketch, "E3971", {"start": v(67.79, -5.5) * mm, "end": v(67.8, -5.5) * mm});
            skLineSegment(sketch, "E3972", {"start": v(67.8, -5.5) * mm, "end": v(67.83, -5.5) * mm});
            skLineSegment(sketch, "E3973", {"start": v(67.83, -5.5) * mm, "end": v(67.86, -5.5) * mm});
            skLineSegment(sketch, "E3974", {"start": v(67.86, -5.5) * mm, "end": v(67.86, -5.5) * mm});
            skLineSegment(sketch, "E3975", {"start": v(67.86, -5.5) * mm, "end": v(67.87, -5.5) * mm});
            skLineSegment(sketch, "E3976", {"start": v(67.87, -5.5) * mm, "end": v(67.88, -5.5) * mm});
            skLineSegment(sketch, "E3977", {"start": v(67.88, -5.5) * mm, "end": v(67.9, -5.5) * mm});
            skLineSegment(sketch, "E3978", {"start": v(67.9, -5.5) * mm, "end": v(67.9, -5.5) * mm});
            skLineSegment(sketch, "E3979", {"start": v(67.9, -5.5) * mm, "end": v(67.9, -5.49) * mm});
            skLineSegment(sketch, "E3980", {"start": v(67.9, -5.49) * mm, "end": v(67.92, -5.49) * mm});
            skLineSegment(sketch, "E3981", {"start": v(67.92, -5.49) * mm, "end": v(67.93, -5.48) * mm});
            skLineSegment(sketch, "E3982", {"start": v(67.93, -5.48) * mm, "end": v(67.95, -5.48) * mm});
            skLineSegment(sketch, "E3983", {"start": v(67.95, -5.48) * mm, "end": v(67.97, -5.47) * mm});
            skLineSegment(sketch, "E3984", {"start": v(67.97, -5.47) * mm, "end": v(67.99, -5.46) * mm});
            skLineSegment(sketch, "E3985", {"start": v(67.99, -5.46) * mm, "end": v(68.01, -5.45) * mm});
            skLineSegment(sketch, "E3986", {"start": v(68.01, -5.45) * mm, "end": v(68.04, -5.43) * mm});
            skLineSegment(sketch, "E3987", {"start": v(68.04, -5.43) * mm, "end": v(68.06, -5.42) * mm});
            skLineSegment(sketch, "E3988", {"start": v(68.06, -5.42) * mm, "end": v(68.09, -5.4) * mm});
            skLineSegment(sketch, "E3989", {"start": v(68.09, -5.4) * mm, "end": v(68.11, -5.38) * mm});
            skLineSegment(sketch, "E3990", {"start": v(68.11, -5.38) * mm, "end": v(68.14, -5.36) * mm});
            skLineSegment(sketch, "E3991", {"start": v(68.14, -5.36) * mm, "end": v(68.17, -5.34) * mm});
            skLineSegment(sketch, "E3992", {"start": v(68.17, -5.34) * mm, "end": v(68.2, -5.32) * mm});
            skLineSegment(sketch, "E3993", {"start": v(68.2, -5.32) * mm, "end": v(68.23, -5.3) * mm});
            skLineSegment(sketch, "E3994", {"start": v(68.23, -5.3) * mm, "end": v(68.26, -5.27) * mm});
            skLineSegment(sketch, "E3995", {"start": v(68.26, -5.27) * mm, "end": v(68.32, -5.21) * mm});
            skLineSegment(sketch, "E3996", {"start": v(68.32, -5.21) * mm, "end": v(68.39, -5.15) * mm});
            skLineSegment(sketch, "E3997", {"start": v(68.39, -5.15) * mm, "end": v(68.46, -5.08) * mm});
            skLineSegment(sketch, "E3998", {"start": v(68.46, -5.08) * mm, "end": v(68.54, -5) * mm});
            skLineSegment(sketch, "E3999", {"start": v(68.54, -5) * mm, "end": v(68.61, -4.93) * mm});
            skLineSegment(sketch, "E4000", {"start": v(68.61, -4.93) * mm, "end": v(68.7, -4.84) * mm});
            skLineSegment(sketch, "E4001", {"start": v(68.7, -4.84) * mm, "end": v(68.83, -4.7) * mm});
            skLineSegment(sketch, "E4002", {"start": v(68.83, -4.7) * mm, "end": v(69.02, -4.48) * mm});
            skLineSegment(sketch, "E4003", {"start": v(69.02, -4.48) * mm, "end": v(69.22, -4.25) * mm});
            skLineSegment(sketch, "E4004", {"start": v(69.22, -4.25) * mm, "end": v(69.44, -4) * mm});
            skLineSegment(sketch, "E4005", {"start": v(69.44, -4) * mm, "end": v(69.67, -3.75) * mm});
            skLineSegment(sketch, "E4006", {"start": v(69.67, -3.75) * mm, "end": v(69.9, -3.48) * mm});
            skLineSegment(sketch, "E4007", {"start": v(69.9, -3.48) * mm, "end": v(70.16, -3.19) * mm});
            skLineSegment(sketch, "E4008", {"start": v(70.16, -3.19) * mm, "end": v(70.43, -2.88) * mm});
            skLineSegment(sketch, "E4009", {"start": v(70.43, -2.88) * mm, "end": v(70.7, -2.56) * mm});
            skLineSegment(sketch, "E4010", {"start": v(70.7, -2.56) * mm, "end": v(71.31, -1.9) * mm});
            skLineSegment(sketch, "E4011", {"start": v(71.31, -1.9) * mm, "end": v(71.97, -1.2) * mm});
            skLineSegment(sketch, "E4012", {"start": v(71.97, -1.2) * mm, "end": v(72.67, -0.51) * mm});
            skLineSegment(sketch, "E4013", {"start": v(72.67, -0.51) * mm, "end": v(73.43, 0.2) * mm});
            skLineSegment(sketch, "E4014", {"start": v(73.43, 0.2) * mm, "end": v(74.24, 0.91) * mm});
            skLineSegment(sketch, "E4015", {"start": v(74.24, 0.91) * mm, "end": v(75.11, 1.6) * mm});
            skLineSegment(sketch, "E4016", {"start": v(75.11, 1.6) * mm, "end": v(76.04, 2.3) * mm});
            skLineSegment(sketch, "E4017", {"start": v(76.04, 2.3) * mm, "end": v(77.01, 2.96) * mm});
            skLineSegment(sketch, "E4018", {"start": v(77.01, 2.96) * mm, "end": v(77.29, 3.15) * mm});
            skLineSegment(sketch, "E4019", {"start": v(77.29, 3.15) * mm, "end": v(77.42, 3.23) * mm});
            skLineSegment(sketch, "E4020", {"start": v(77.42, 3.23) * mm, "end": v(77.55, 3.3) * mm});
            skLineSegment(sketch, "E4021", {"start": v(77.55, 3.3) * mm, "end": v(77.67, 3.38) * mm});
            skLineSegment(sketch, "E4022", {"start": v(77.67, 3.38) * mm, "end": v(77.8, 3.44) * mm});
            skLineSegment(sketch, "E4023", {"start": v(77.8, 3.44) * mm, "end": v(77.92, 3.5) * mm});
            skLineSegment(sketch, "E4024", {"start": v(77.92, 3.5) * mm, "end": v(78.04, 3.55) * mm});
            skLineSegment(sketch, "E4025", {"start": v(78.04, 3.55) * mm, "end": v(78.15, 3.6) * mm});
            skLineSegment(sketch, "E4026", {"start": v(78.15, 3.6) * mm, "end": v(78.26, 3.63) * mm});
            skLineSegment(sketch, "E4027", {"start": v(78.26, 3.63) * mm, "end": v(78.37, 3.67) * mm});
            skLineSegment(sketch, "E4028", {"start": v(78.37, 3.67) * mm, "end": v(78.48, 3.7) * mm});
            skLineSegment(sketch, "E4029", {"start": v(78.48, 3.7) * mm, "end": v(78.58, 3.72) * mm});
            skLineSegment(sketch, "E4030", {"start": v(78.58, 3.72) * mm, "end": v(78.68, 3.73) * mm});
            skLineSegment(sketch, "E4031", {"start": v(78.68, 3.73) * mm, "end": v(78.78, 3.74) * mm});
            skLineSegment(sketch, "E4032", {"start": v(78.78, 3.74) * mm, "end": v(78.87, 3.74) * mm});
            skLineSegment(sketch, "E4033", {"start": v(78.87, 3.74) * mm, "end": v(78.9, 3.74) * mm});
            skLineSegment(sketch, "E4034", {"start": v(78.9, 3.74) * mm, "end": v(78.91, 3.74) * mm});
            skLineSegment(sketch, "E4035", {"start": v(78.91, 3.74) * mm, "end": v(78.93, 3.74) * mm});
            skLineSegment(sketch, "E4036", {"start": v(78.93, 3.74) * mm, "end": v(78.95, 3.73) * mm});
            skLineSegment(sketch, "E4037", {"start": v(78.95, 3.73) * mm, "end": v(78.97, 3.72) * mm});
            skLineSegment(sketch, "E4038", {"start": v(78.97, 3.72) * mm, "end": v(79, 3.71) * mm});
            skLineSegment(sketch, "E4039", {"start": v(79, 3.71) * mm, "end": v(79.02, 3.7) * mm});
            skLineSegment(sketch, "E4040", {"start": v(79.02, 3.7) * mm, "end": v(79.04, 3.69) * mm});
            skLineSegment(sketch, "E4041", {"start": v(79.04, 3.69) * mm, "end": v(79.06, 3.67) * mm});
            skLineSegment(sketch, "E4042", {"start": v(79.06, 3.67) * mm, "end": v(79.08, 3.65) * mm});
            skLineSegment(sketch, "E4043", {"start": v(79.08, 3.65) * mm, "end": v(79.1, 3.64) * mm});
            skLineSegment(sketch, "E4044", {"start": v(79.1, 3.64) * mm, "end": v(79.12, 3.61) * mm});
            skLineSegment(sketch, "E4045", {"start": v(79.12, 3.61) * mm, "end": v(79.14, 3.6) * mm});
            skLineSegment(sketch, "E4046", {"start": v(79.14, 3.6) * mm, "end": v(79.16, 3.57) * mm});
            skLineSegment(sketch, "E4047", {"start": v(79.16, 3.57) * mm, "end": v(79.18, 3.54) * mm});
            skLineSegment(sketch, "E4048", {"start": v(79.18, 3.54) * mm, "end": v(79.2, 3.51) * mm});
            skLineSegment(sketch, "E4049", {"start": v(79.2, 3.51) * mm, "end": v(79.22, 3.48) * mm});
            skLineSegment(sketch, "E4050", {"start": v(79.22, 3.48) * mm, "end": v(79.24, 3.45) * mm});
            skLineSegment(sketch, "E4051", {"start": v(79.24, 3.45) * mm, "end": v(79.26, 3.42) * mm});
            skLineSegment(sketch, "E4052", {"start": v(79.26, 3.42) * mm, "end": v(79.28, 3.38) * mm});
            skLineSegment(sketch, "E4053", {"start": v(79.28, 3.38) * mm, "end": v(79.32, 3.3) * mm});
            skLineSegment(sketch, "E4054", {"start": v(79.32, 3.3) * mm, "end": v(79.36, 3.22) * mm});
            skLineSegment(sketch, "E4055", {"start": v(79.36, 3.22) * mm, "end": v(79.4, 3.13) * mm});
            skLineSegment(sketch, "E4056", {"start": v(79.4, 3.13) * mm, "end": v(79.44, 3.03) * mm});
            skLineSegment(sketch, "E4057", {"start": v(79.44, 3.03) * mm, "end": v(79.48, 2.93) * mm});
            skLineSegment(sketch, "E4058", {"start": v(79.48, 2.93) * mm, "end": v(79.52, 2.82) * mm});
            skLineSegment(sketch, "E4059", {"start": v(79.52, 2.82) * mm, "end": v(79.67, 2.35) * mm});
            skLineSegment(sketch, "E4060", {"start": v(79.67, 2.35) * mm, "end": v(79.73, 2.12) * mm});
            skLineSegment(sketch, "E4061", {"start": v(79.73, 2.12) * mm, "end": v(79.78, 1.88) * mm});
            skLineSegment(sketch, "E4062", {"start": v(79.78, 1.88) * mm, "end": v(79.81, 1.65) * mm});
            skLineSegment(sketch, "E4063", {"start": v(79.81, 1.65) * mm, "end": v(79.84, 1.41) * mm});
            skLineSegment(sketch, "E4064", {"start": v(79.84, 1.41) * mm, "end": v(79.86, 1.18) * mm});
            skLineSegment(sketch, "E4065", {"start": v(79.86, 1.18) * mm, "end": v(79.86, 0.94) * mm});
            skLineSegment(sketch, "E4066", {"start": v(79.86, 0.94) * mm, "end": v(79.86, 0.9) * mm});
            skLineSegment(sketch, "E4067", {"start": v(79.86, 0.9) * mm, "end": v(79.86, 0.88) * mm});
            skLineSegment(sketch, "E4068", {"start": v(79.86, 0.88) * mm, "end": v(79.85, 0.85) * mm});
            skLineSegment(sketch, "E4069", {"start": v(79.85, 0.85) * mm, "end": v(79.85, 0.82) * mm});
            skLineSegment(sketch, "E4070", {"start": v(79.85, 0.82) * mm, "end": v(79.84, 0.78) * mm});
            skLineSegment(sketch, "E4071", {"start": v(79.84, 0.78) * mm, "end": v(79.83, 0.75) * mm});
            skLineSegment(sketch, "E4072", {"start": v(79.83, 0.75) * mm, "end": v(79.82, 0.71) * mm});
            skLineSegment(sketch, "E4073", {"start": v(79.82, 0.71) * mm, "end": v(79.8, 0.68) * mm});
            skLineSegment(sketch, "E4074", {"start": v(79.8, 0.68) * mm, "end": v(79.79, 0.64) * mm});
            skLineSegment(sketch, "E4075", {"start": v(79.79, 0.64) * mm, "end": v(79.77, 0.6) * mm});
            skLineSegment(sketch, "E4076", {"start": v(79.77, 0.6) * mm, "end": v(79.75, 0.56) * mm});
            skLineSegment(sketch, "E4077", {"start": v(79.75, 0.56) * mm, "end": v(79.73, 0.52) * mm});
            skLineSegment(sketch, "E4078", {"start": v(79.73, 0.52) * mm, "end": v(79.69, 0.44) * mm});
            skLineSegment(sketch, "E4079", {"start": v(79.69, 0.44) * mm, "end": v(79.63, 0.35) * mm});
            skLineSegment(sketch, "E4080", {"start": v(79.63, 0.35) * mm, "end": v(79.57, 0.26) * mm});
            skLineSegment(sketch, "E4081", {"start": v(79.57, 0.26) * mm, "end": v(79.5, 0.17) * mm});
            skLineSegment(sketch, "E4082", {"start": v(79.5, 0.17) * mm, "end": v(79.43, 0.07) * mm});
            skLineSegment(sketch, "E4083", {"start": v(79.43, 0.07) * mm, "end": v(79.35, -0.03) * mm});
            skLineSegment(sketch, "E4084", {"start": v(79.35, -0.03) * mm, "end": v(79.26, -0.14) * mm});
            skLineSegment(sketch, "E4085", {"start": v(79.26, -0.14) * mm, "end": v(79.17, -0.24) * mm});
            skLineSegment(sketch, "E4086", {"start": v(79.17, -0.24) * mm, "end": v(79.06, -0.36) * mm});
            skLineSegment(sketch, "E4087", {"start": v(79.06, -0.36) * mm, "end": v(78.95, -0.47) * mm});
            skLineSegment(sketch, "E4088", {"start": v(91.05, -4.34) * mm, "end": v(90.14, -5.35) * mm});
            skLineSegment(sketch, "E4089", {"start": v(90.14, -5.35) * mm, "end": v(89.28, -6.29) * mm});
            skLineSegment(sketch, "E4090", {"start": v(89.28, -6.29) * mm, "end": v(88.48, -7.14) * mm});
            skLineSegment(sketch, "E4091", {"start": v(88.48, -7.14) * mm, "end": v(87.71, -7.92) * mm});
            skLineSegment(sketch, "E4092", {"start": v(87.71, -7.92) * mm, "end": v(87.36, -8.28) * mm});
            skLineSegment(sketch, "E4093", {"start": v(87.36, -8.28) * mm, "end": v(87.02, -8.61) * mm});
            skLineSegment(sketch, "E4094", {"start": v(87.02, -8.61) * mm, "end": v(86.7, -8.93) * mm});
            skLineSegment(sketch, "E4095", {"start": v(86.7, -8.93) * mm, "end": v(86.39, -9.21) * mm});
            skLineSegment(sketch, "E4096", {"start": v(86.39, -9.21) * mm, "end": v(86.1, -9.48) * mm});
            skLineSegment(sketch, "E4097", {"start": v(86.1, -9.48) * mm, "end": v(85.83, -9.72) * mm});
            skLineSegment(sketch, "E4098", {"start": v(85.83, -9.72) * mm, "end": v(85.57, -9.94) * mm});
            skLineSegment(sketch, "E4099", {"start": v(85.57, -9.94) * mm, "end": v(85.45, -10.04) * mm});
            skLineSegment(sketch, "E4100", {"start": v(85.45, -10.04) * mm, "end": v(85.33, -10.14) * mm});
            skLineSegment(sketch, "E4101", {"start": v(85.33, -10.14) * mm, "end": v(85.22, -10.22) * mm});
            skLineSegment(sketch, "E4102", {"start": v(85.22, -10.22) * mm, "end": v(85.11, -10.3) * mm});
            skLineSegment(sketch, "E4103", {"start": v(85.11, -10.3) * mm, "end": v(85, -10.38) * mm});
            skLineSegment(sketch, "E4104", {"start": v(85, -10.38) * mm, "end": v(84.91, -10.45) * mm});
            skLineSegment(sketch, "E4105", {"start": v(84.91, -10.45) * mm, "end": v(84.82, -10.52) * mm});
            skLineSegment(sketch, "E4106", {"start": v(84.82, -10.52) * mm, "end": v(84.73, -10.57) * mm});
            skLineSegment(sketch, "E4107", {"start": v(84.73, -10.57) * mm, "end": v(84.64, -10.63) * mm});
            skLineSegment(sketch, "E4108", {"start": v(84.64, -10.63) * mm, "end": v(84.56, -10.68) * mm});
            skLineSegment(sketch, "E4109", {"start": v(84.56, -10.68) * mm, "end": v(84.49, -10.72) * mm});
            skLineSegment(sketch, "E4110", {"start": v(84.49, -10.72) * mm, "end": v(84.45, -10.74) * mm});
            skLineSegment(sketch, "E4111", {"start": v(84.45, -10.74) * mm, "end": v(84.42, -10.75) * mm});
            skLineSegment(sketch, "E4112", {"start": v(84.42, -10.75) * mm, "end": v(84.38, -10.77) * mm});
            skLineSegment(sketch, "E4113", {"start": v(84.38, -10.77) * mm, "end": v(84.35, -10.78) * mm});
            skLineSegment(sketch, "E4114", {"start": v(84.35, -10.78) * mm, "end": v(84.32, -10.8) * mm});
            skLineSegment(sketch, "E4115", {"start": v(84.32, -10.8) * mm, "end": v(84.29, -10.8) * mm});
            skLineSegment(sketch, "E4116", {"start": v(84.29, -10.8) * mm, "end": v(84.26, -10.82) * mm});
            skLineSegment(sketch, "E4117", {"start": v(84.26, -10.82) * mm, "end": v(84.23, -10.83) * mm});
            skLineSegment(sketch, "E4118", {"start": v(84.23, -10.83) * mm, "end": v(84.2, -10.84) * mm});
            skLineSegment(sketch, "E4119", {"start": v(84.2, -10.84) * mm, "end": v(84.18, -10.84) * mm});
            skLineSegment(sketch, "E4120", {"start": v(84.18, -10.84) * mm, "end": v(84.15, -10.85) * mm});
            skLineSegment(sketch, "E4121", {"start": v(84.15, -10.85) * mm, "end": v(84.13, -10.85) * mm});
            skLineSegment(sketch, "E4122", {"start": v(84.13, -10.85) * mm, "end": v(84.1, -10.85) * mm});
            skLineSegment(sketch, "E4123", {"start": v(84.1, -10.85) * mm, "end": v(84.08, -10.85) * mm});
            skLineSegment(sketch, "E4124", {"start": v(84.08, -10.85) * mm, "end": v(84.05, -10.85) * mm});
            skLineSegment(sketch, "E4125", {"start": v(84.05, -10.85) * mm, "end": v(84.02, -10.85) * mm});
            skLineSegment(sketch, "E4126", {"start": v(84.02, -10.85) * mm, "end": v(83.98, -10.85) * mm});
            skLineSegment(sketch, "E4127", {"start": v(83.98, -10.85) * mm, "end": v(83.95, -10.84) * mm});
            skLineSegment(sketch, "E4128", {"start": v(83.95, -10.84) * mm, "end": v(83.9, -10.83) * mm});
            skLineSegment(sketch, "E4129", {"start": v(83.9, -10.83) * mm, "end": v(83.87, -10.82) * mm});
            skLineSegment(sketch, "E4130", {"start": v(83.87, -10.82) * mm, "end": v(83.84, -10.81) * mm});
            skLineSegment(sketch, "E4131", {"start": v(83.84, -10.81) * mm, "end": v(83.8, -10.8) * mm});
            skLineSegment(sketch, "E4132", {"start": v(83.8, -10.8) * mm, "end": v(83.76, -10.78) * mm});
            skLineSegment(sketch, "E4133", {"start": v(83.76, -10.78) * mm, "end": v(83.69, -10.75) * mm});
            skLineSegment(sketch, "E4134", {"start": v(83.69, -10.75) * mm, "end": v(83.61, -10.7) * mm});
            skLineSegment(sketch, "E4135", {"start": v(83.61, -10.7) * mm, "end": v(83.54, -10.66) * mm});
            skLineSegment(sketch, "E4136", {"start": v(83.54, -10.66) * mm, "end": v(83.46, -10.6) * mm});
            skLineSegment(sketch, "E4137", {"start": v(83.46, -10.6) * mm, "end": v(83.38, -10.54) * mm});
            skLineSegment(sketch, "E4138", {"start": v(83.38, -10.54) * mm, "end": v(83.3, -10.47) * mm});
            skLineSegment(sketch, "E4139", {"start": v(83.3, -10.47) * mm, "end": v(83.22, -10.4) * mm});
            skLineSegment(sketch, "E4140", {"start": v(83.22, -10.4) * mm, "end": v(83.14, -10.31) * mm});
            skLineSegment(sketch, "E4141", {"start": v(83.14, -10.31) * mm, "end": v(83.05, -10.22) * mm});
            skLineSegment(sketch, "E4142", {"start": v(83.05, -10.22) * mm, "end": v(82.97, -10.13) * mm});
            skLineSegment(sketch, "E4143", {"start": v(82.97, -10.13) * mm, "end": v(82.84, -9.97) * mm});
            skLineSegment(sketch, "E4144", {"start": v(82.84, -9.97) * mm, "end": v(82.67, -9.74) * mm});
            skLineSegment(sketch, "E4145", {"start": v(82.67, -9.74) * mm, "end": v(82.51, -9.5) * mm});
            skLineSegment(sketch, "E4146", {"start": v(82.51, -9.5) * mm, "end": v(82.36, -9.24) * mm});
            skLineSegment(sketch, "E4147", {"start": v(82.36, -9.24) * mm, "end": v(82.21, -8.96) * mm});
            skLineSegment(sketch, "E4148", {"start": v(82.21, -8.96) * mm, "end": v(82.07, -8.67) * mm});
            skLineSegment(sketch, "E4149", {"start": v(82.07, -8.67) * mm, "end": v(81.93, -8.37) * mm});
            skLineSegment(sketch, "E4150", {"start": v(81.93, -8.37) * mm, "end": v(81.8, -8.05) * mm});
            skLineSegment(sketch, "E4151", {"start": v(81.8, -8.05) * mm, "end": v(81.68, -7.71) * mm});
            skLineSegment(sketch, "E4152", {"start": v(81.68, -7.71) * mm, "end": v(81.47, -7.02) * mm});
            skLineSegment(sketch, "E4153", {"start": v(81.47, -7.02) * mm, "end": v(81.32, -6.33) * mm});
            skLineSegment(sketch, "E4154", {"start": v(81.32, -6.33) * mm, "end": v(81.22, -5.63) * mm});
            skLineSegment(sketch, "E4155", {"start": v(81.22, -5.63) * mm, "end": v(81.2, -4.93) * mm});
            skLineSegment(sketch, "E4156", {"start": v(81.2, -4.93) * mm, "end": v(81.2, -4.67) * mm});
            skLineSegment(sketch, "E4157", {"start": v(81.2, -4.67) * mm, "end": v(81.23, -4.41) * mm});
            skLineSegment(sketch, "E4158", {"start": v(81.23, -4.41) * mm, "end": v(81.26, -4.16) * mm});
            skLineSegment(sketch, "E4159", {"start": v(81.26, -4.16) * mm, "end": v(81.32, -3.9) * mm});
            skLineSegment(sketch, "E4160", {"start": v(81.32, -3.9) * mm, "end": v(81.39, -3.65) * mm});
            skLineSegment(sketch, "E4161", {"start": v(81.39, -3.65) * mm, "end": v(81.47, -3.39) * mm});
            skLineSegment(sketch, "E4162", {"start": v(81.47, -3.39) * mm, "end": v(81.57, -3.13) * mm});
            skLineSegment(sketch, "E4163", {"start": v(81.57, -3.13) * mm, "end": v(81.69, -2.87) * mm});
            skLineSegment(sketch, "E4164", {"start": v(81.69, -2.87) * mm, "end": v(81.82, -2.62) * mm});
            skLineSegment(sketch, "E4165", {"start": v(81.82, -2.62) * mm, "end": v(81.97, -2.36) * mm});
            skLineSegment(sketch, "E4166", {"start": v(81.97, -2.36) * mm, "end": v(82.13, -2.1) * mm});
            skLineSegment(sketch, "E4167", {"start": v(82.13, -2.1) * mm, "end": v(82.3, -1.84) * mm});
            skLineSegment(sketch, "E4168", {"start": v(82.3, -1.84) * mm, "end": v(82.5, -1.59) * mm});
            skLineSegment(sketch, "E4169", {"start": v(82.5, -1.59) * mm, "end": v(82.71, -1.33) * mm});
            skLineSegment(sketch, "E4170", {"start": v(82.71, -1.33) * mm, "end": v(82.94, -1.07) * mm});
            skLineSegment(sketch, "E4171", {"start": v(82.94, -1.07) * mm, "end": v(83.18, -0.81) * mm});
            skLineSegment(sketch, "E4172", {"start": v(83.18, -0.81) * mm, "end": v(84.2, 0.19) * mm});
            skLineSegment(sketch, "E4173", {"start": v(84.2, 0.19) * mm, "end": v(85.3, 1.1) * mm});
            skLineSegment(sketch, "E4174", {"start": v(85.3, 1.1) * mm, "end": v(86.46, 1.92) * mm});
            skLineSegment(sketch, "E4175", {"start": v(86.46, 1.92) * mm, "end": v(87.7, 2.65) * mm});
            skLineSegment(sketch, "E4176", {"start": v(87.7, 2.65) * mm, "end": v(88.3, 2.97) * mm});
            skLineSegment(sketch, "E4177", {"start": v(88.3, 2.97) * mm, "end": v(88.6, 3.11) * mm});
            skLineSegment(sketch, "E4178", {"start": v(88.6, 3.11) * mm, "end": v(88.88, 3.25) * mm});
            skLineSegment(sketch, "E4179", {"start": v(88.88, 3.25) * mm, "end": v(89.15, 3.37) * mm});
            skLineSegment(sketch, "E4180", {"start": v(89.15, 3.37) * mm, "end": v(89.41, 3.48) * mm});
            skLineSegment(sketch, "E4181", {"start": v(89.41, 3.48) * mm, "end": v(89.67, 3.59) * mm});
            skLineSegment(sketch, "E4182", {"start": v(89.67, 3.59) * mm, "end": v(89.9, 3.68) * mm});
            skLineSegment(sketch, "E4183", {"start": v(89.9, 3.68) * mm, "end": v(90.14, 3.76) * mm});
            skLineSegment(sketch, "E4184", {"start": v(90.14, 3.76) * mm, "end": v(90.36, 3.83) * mm});
            skLineSegment(sketch, "E4185", {"start": v(90.36, 3.83) * mm, "end": v(90.57, 3.89) * mm});
            skLineSegment(sketch, "E4186", {"start": v(90.57, 3.89) * mm, "end": v(90.78, 3.93) * mm});
            skLineSegment(sketch, "E4187", {"start": v(90.78, 3.93) * mm, "end": v(90.97, 3.97) * mm});
            skLineSegment(sketch, "E4188", {"start": v(90.97, 3.97) * mm, "end": v(91.15, 4) * mm});
            skLineSegment(sketch, "E4189", {"start": v(91.15, 4) * mm, "end": v(91.33, 4.01) * mm});
            skLineSegment(sketch, "E4190", {"start": v(91.33, 4.01) * mm, "end": v(91.4, 4.02) * mm});
            skLineSegment(sketch, "E4191", {"start": v(91.4, 4.02) * mm, "end": v(91.49, 4.02) * mm});
            skLineSegment(sketch, "E4192", {"start": v(91.49, 4.02) * mm, "end": v(91.62, 4.01) * mm});
            skLineSegment(sketch, "E4193", {"start": v(91.62, 4.01) * mm, "end": v(91.75, 4) * mm});
            skLineSegment(sketch, "E4194", {"start": v(91.75, 4) * mm, "end": v(91.88, 3.97) * mm});
            skLineSegment(sketch, "E4195", {"start": v(91.88, 3.97) * mm, "end": v(92, 3.94) * mm});
            skLineSegment(sketch, "E4196", {"start": v(92, 3.94) * mm, "end": v(92.13, 3.9) * mm});
            skLineSegment(sketch, "E4197", {"start": v(92.13, 3.9) * mm, "end": v(92.26, 3.84) * mm});
            skLineSegment(sketch, "E4198", {"start": v(92.26, 3.84) * mm, "end": v(92.39, 3.77) * mm});
            skLineSegment(sketch, "E4199", {"start": v(92.39, 3.77) * mm, "end": v(92.51, 3.7) * mm});
            skLineSegment(sketch, "E4200", {"start": v(92.51, 3.7) * mm, "end": v(92.64, 3.6) * mm});
            skLineSegment(sketch, "E4201", {"start": v(92.64, 3.6) * mm, "end": v(92.77, 3.5) * mm});
            skLineSegment(sketch, "E4202", {"start": v(92.77, 3.5) * mm, "end": v(92.9, 3.4) * mm});
            skLineSegment(sketch, "E4203", {"start": v(92.9, 3.4) * mm, "end": v(93.02, 3.28) * mm});
            skLineSegment(sketch, "E4204", {"start": v(93.02, 3.28) * mm, "end": v(93.14, 3.16) * mm});
            skLineSegment(sketch, "E4205", {"start": v(93.14, 3.16) * mm, "end": v(93.27, 3.02) * mm});
            skLineSegment(sketch, "E4206", {"start": v(93.27, 3.02) * mm, "end": v(93.4, 2.87) * mm});
            skLineSegment(sketch, "E4207", {"start": v(93.4, 2.87) * mm, "end": v(93.51, 2.71) * mm});
            skLineSegment(sketch, "E4208", {"start": v(93.51, 2.71) * mm, "end": v(94.32, 4.36) * mm});
            skLineSegment(sketch, "E4209", {"start": v(94.32, 4.36) * mm, "end": v(95.1, 5.92) * mm});
            skLineSegment(sketch, "E4210", {"start": v(95.1, 5.92) * mm, "end": v(95.86, 7.38) * mm});
            skLineSegment(sketch, "E4211", {"start": v(95.86, 7.38) * mm, "end": v(96.6, 8.74) * mm});
            skLineSegment(sketch, "E4212", {"start": v(96.6, 8.74) * mm, "end": v(96.96, 9.38) * mm});
            skLineSegment(sketch, "E4213", {"start": v(96.96, 9.38) * mm, "end": v(97.3, 9.98) * mm});
            skLineSegment(sketch, "E4214", {"start": v(97.3, 9.98) * mm, "end": v(97.63, 10.53) * mm});
            skLineSegment(sketch, "E4215", {"start": v(97.63, 10.53) * mm, "end": v(97.95, 11.04) * mm});
            skLineSegment(sketch, "E4216", {"start": v(97.95, 11.04) * mm, "end": v(98.25, 11.51) * mm});
            skLineSegment(sketch, "E4217", {"start": v(98.25, 11.51) * mm, "end": v(98.54, 11.94) * mm});
            skLineSegment(sketch, "E4218", {"start": v(98.54, 11.94) * mm, "end": v(98.67, 12.14) * mm});
            skLineSegment(sketch, "E4219", {"start": v(98.67, 12.14) * mm, "end": v(98.8, 12.33) * mm});
            skLineSegment(sketch, "E4220", {"start": v(98.8, 12.33) * mm, "end": v(98.94, 12.5) * mm});
            skLineSegment(sketch, "E4221", {"start": v(98.94, 12.5) * mm, "end": v(99.06, 12.67) * mm});
            skLineSegment(sketch, "E4222", {"start": v(99.06, 12.67) * mm, "end": v(99.19, 12.82) * mm});
            skLineSegment(sketch, "E4223", {"start": v(99.19, 12.82) * mm, "end": v(99.3, 12.97) * mm});
            skLineSegment(sketch, "E4224", {"start": v(99.3, 12.97) * mm, "end": v(99.42, 13.1) * mm});
            skLineSegment(sketch, "E4225", {"start": v(99.42, 13.1) * mm, "end": v(99.52, 13.23) * mm});
            skLineSegment(sketch, "E4226", {"start": v(99.52, 13.23) * mm, "end": v(99.63, 13.35) * mm});
            skLineSegment(sketch, "E4227", {"start": v(99.63, 13.35) * mm, "end": v(99.73, 13.45) * mm});
            skLineSegment(sketch, "E4228", {"start": v(99.73, 13.45) * mm, "end": v(99.82, 13.55) * mm});
            skLineSegment(sketch, "E4229", {"start": v(99.82, 13.55) * mm, "end": v(99.87, 13.6) * mm});
            skLineSegment(sketch, "E4230", {"start": v(99.87, 13.6) * mm, "end": v(99.91, 13.63) * mm});
            skLineSegment(sketch, "E4231", {"start": v(99.91, 13.63) * mm, "end": v(99.96, 13.67) * mm});
            skLineSegment(sketch, "E4232", {"start": v(99.96, 13.67) * mm, "end": v(100, 13.7) * mm});
            skLineSegment(sketch, "E4233", {"start": v(100, 13.7) * mm, "end": v(100.04, 13.74) * mm});
            skLineSegment(sketch, "E4234", {"start": v(100.04, 13.74) * mm, "end": v(100.08, 13.77) * mm});
            skLineSegment(sketch, "E4235", {"start": v(100.08, 13.77) * mm, "end": v(100.12, 13.8) * mm});
            skLineSegment(sketch, "E4236", {"start": v(100.12, 13.8) * mm, "end": v(100.16, 13.83) * mm});
            skLineSegment(sketch, "E4237", {"start": v(100.16, 13.83) * mm, "end": v(100.2, 13.85) * mm});
            skLineSegment(sketch, "E4238", {"start": v(100.2, 13.85) * mm, "end": v(100.23, 13.88) * mm});
            skLineSegment(sketch, "E4239", {"start": v(100.23, 13.88) * mm, "end": v(100.27, 13.9) * mm});
            skLineSegment(sketch, "E4240", {"start": v(100.27, 13.9) * mm, "end": v(100.3, 13.91) * mm});
            skLineSegment(sketch, "E4241", {"start": v(100.3, 13.91) * mm, "end": v(100.33, 13.92) * mm});
            skLineSegment(sketch, "E4242", {"start": v(100.33, 13.92) * mm, "end": v(100.36, 13.94) * mm});
            skLineSegment(sketch, "E4243", {"start": v(100.36, 13.94) * mm, "end": v(100.4, 13.94) * mm});
            skLineSegment(sketch, "E4244", {"start": v(100.4, 13.94) * mm, "end": v(100.4, 13.95) * mm});
            skLineSegment(sketch, "E4245", {"start": v(100.4, 13.95) * mm, "end": v(100.42, 13.95) * mm});
            skLineSegment(sketch, "E4246", {"start": v(100.42, 13.95) * mm, "end": v(100.44, 13.95) * mm});
            skLineSegment(sketch, "E4247", {"start": v(100.44, 13.95) * mm, "end": v(100.45, 13.95) * mm});
            skLineSegment(sketch, "E4248", {"start": v(100.45, 13.95) * mm, "end": v(100.46, 13.96) * mm});
            skLineSegment(sketch, "E4249", {"start": v(100.46, 13.96) * mm, "end": v(100.48, 13.96) * mm});
            skLineSegment(sketch, "E4250", {"start": v(100.48, 13.96) * mm, "end": v(100.53, 13.95) * mm});
            skLineSegment(sketch, "E4251", {"start": v(100.53, 13.95) * mm, "end": v(100.6, 13.95) * mm});
            skLineSegment(sketch, "E4252", {"start": v(100.6, 13.95) * mm, "end": v(100.65, 13.94) * mm});
            skLineSegment(sketch, "E4253", {"start": v(100.65, 13.94) * mm, "end": v(100.7, 13.93) * mm});
            skLineSegment(sketch, "E4254", {"start": v(100.7, 13.93) * mm, "end": v(100.76, 13.91) * mm});
            skLineSegment(sketch, "E4255", {"start": v(100.76, 13.91) * mm, "end": v(100.81, 13.9) * mm});
            skLineSegment(sketch, "E4256", {"start": v(100.81, 13.9) * mm, "end": v(100.87, 13.87) * mm});
            skLineSegment(sketch, "E4257", {"start": v(100.87, 13.87) * mm, "end": v(100.92, 13.84) * mm});
            skLineSegment(sketch, "E4258", {"start": v(100.92, 13.84) * mm, "end": v(100.97, 13.8) * mm});
            skLineSegment(sketch, "E4259", {"start": v(100.97, 13.8) * mm, "end": v(101.02, 13.77) * mm});
            skLineSegment(sketch, "E4260", {"start": v(101.02, 13.77) * mm, "end": v(101.08, 13.74) * mm});
            skLineSegment(sketch, "E4261", {"start": v(101.08, 13.74) * mm, "end": v(101.13, 13.7) * mm});
            skLineSegment(sketch, "E4262", {"start": v(101.13, 13.7) * mm, "end": v(101.18, 13.65) * mm});
            skLineSegment(sketch, "E4263", {"start": v(101.18, 13.65) * mm, "end": v(101.22, 13.6) * mm});
            skLineSegment(sketch, "E4264", {"start": v(101.22, 13.6) * mm, "end": v(101.27, 13.55) * mm});
            skLineSegment(sketch, "E4265", {"start": v(101.27, 13.55) * mm, "end": v(101.32, 13.5) * mm});
            skLineSegment(sketch, "E4266", {"start": v(101.32, 13.5) * mm, "end": v(101.37, 13.44) * mm});
            skLineSegment(sketch, "E4267", {"start": v(101.37, 13.44) * mm, "end": v(101.41, 13.38) * mm});
            skLineSegment(sketch, "E4268", {"start": v(101.41, 13.38) * mm, "end": v(101.46, 13.32) * mm});
            skLineSegment(sketch, "E4269", {"start": v(101.46, 13.32) * mm, "end": v(101.5, 13.26) * mm});
            skLineSegment(sketch, "E4270", {"start": v(101.5, 13.26) * mm, "end": v(101.53, 13.2) * mm});
            skLineSegment(sketch, "E4271", {"start": v(101.53, 13.2) * mm, "end": v(101.57, 13.14) * mm});
            skLineSegment(sketch, "E4272", {"start": v(101.57, 13.14) * mm, "end": v(101.6, 13.08) * mm});
            skLineSegment(sketch, "E4273", {"start": v(101.6, 13.08) * mm, "end": v(101.62, 13.02) * mm});
            skLineSegment(sketch, "E4274", {"start": v(101.62, 13.02) * mm, "end": v(101.64, 12.95) * mm});
            skLineSegment(sketch, "E4275", {"start": v(101.64, 12.95) * mm, "end": v(101.67, 12.89) * mm});
            skLineSegment(sketch, "E4276", {"start": v(101.67, 12.89) * mm, "end": v(101.68, 12.82) * mm});
            skLineSegment(sketch, "E4277", {"start": v(101.68, 12.82) * mm, "end": v(101.7, 12.76) * mm});
            skLineSegment(sketch, "E4278", {"start": v(101.7, 12.76) * mm, "end": v(101.7, 12.69) * mm});
            skLineSegment(sketch, "E4279", {"start": v(101.7, 12.69) * mm, "end": v(101.72, 12.62) * mm});
            skLineSegment(sketch, "E4280", {"start": v(101.72, 12.62) * mm, "end": v(101.72, 12.55) * mm});
            skLineSegment(sketch, "E4281", {"start": v(101.72, 12.55) * mm, "end": v(101.72, 12.48) * mm});
            skLineSegment(sketch, "E4282", {"start": v(101.72, 12.48) * mm, "end": v(101.72, 12.4) * mm});
            skLineSegment(sketch, "E4283", {"start": v(101.72, 12.4) * mm, "end": v(101.72, 12.34) * mm});
            skLineSegment(sketch, "E4284", {"start": v(101.72, 12.34) * mm, "end": v(101.7, 12.26) * mm});
            skLineSegment(sketch, "E4285", {"start": v(101.7, 12.26) * mm, "end": v(101.7, 12.18) * mm});
            skLineSegment(sketch, "E4286", {"start": v(101.7, 12.18) * mm, "end": v(101.68, 12.1) * mm});
            skLineSegment(sketch, "E4287", {"start": v(101.68, 12.1) * mm, "end": v(101.67, 12.01) * mm});
            skLineSegment(sketch, "E4288", {"start": v(101.67, 12.01) * mm, "end": v(101.64, 11.92) * mm});
            skLineSegment(sketch, "E4289", {"start": v(101.64, 11.92) * mm, "end": v(101.62, 11.83) * mm});
            skLineSegment(sketch, "E4290", {"start": v(101.62, 11.83) * mm, "end": v(101.6, 11.74) * mm});
            skLineSegment(sketch, "E4291", {"start": v(101.6, 11.74) * mm, "end": v(101.53, 11.54) * mm});
            skLineSegment(sketch, "E4292", {"start": v(101.53, 11.54) * mm, "end": v(101.46, 11.33) * mm});
            skLineSegment(sketch, "E4293", {"start": v(101.46, 11.33) * mm, "end": v(101.37, 11.1) * mm});
            skLineSegment(sketch, "E4294", {"start": v(101.37, 11.1) * mm, "end": v(101.27, 10.87) * mm});
            skLineSegment(sketch, "E4295", {"start": v(101.27, 10.87) * mm, "end": v(101.16, 10.62) * mm});
            skLineSegment(sketch, "E4296", {"start": v(101.16, 10.62) * mm, "end": v(101.03, 10.36) * mm});
            skLineSegment(sketch, "E4297", {"start": v(101.03, 10.36) * mm, "end": v(100.9, 10.08) * mm});
            skLineSegment(sketch, "E4298", {"start": v(100.9, 10.08) * mm, "end": v(100.74, 9.8) * mm});
            skLineSegment(sketch, "E4299", {"start": v(100.74, 9.8) * mm, "end": v(100.58, 9.5) * mm});
            skLineSegment(sketch, "E4300", {"start": v(100.58, 9.5) * mm, "end": v(100.4, 9.2) * mm});
            skLineSegment(sketch, "E4301", {"start": v(100.4, 9.2) * mm, "end": v(100.12, 8.7) * mm});
            skLineSegment(sketch, "E4302", {"start": v(100.12, 8.7) * mm, "end": v(99.32, 7.38) * mm});
            skLineSegment(sketch, "E4303", {"start": v(99.32, 7.38) * mm, "end": v(97.74, 4.79) * mm});
            skLineSegment(sketch, "E4304", {"start": v(97.74, 4.79) * mm, "end": v(96.95, 3.51) * mm});
            skLineSegment(sketch, "E4305", {"start": v(96.95, 3.51) * mm, "end": v(96.2, 2.25) * mm});
            skLineSegment(sketch, "E4306", {"start": v(96.2, 2.25) * mm, "end": v(94.86, -0.25) * mm});
            skLineSegment(sketch, "E4307", {"start": v(94.86, -0.25) * mm, "end": v(94.27, -1.49) * mm});
            skLineSegment(sketch, "E4308", {"start": v(94.27, -1.49) * mm, "end": v(94.01, -2.1) * mm});
            skLineSegment(sketch, "E4309", {"start": v(94.01, -2.1) * mm, "end": v(93.79, -2.69) * mm});
            skLineSegment(sketch, "E4310", {"start": v(93.79, -2.69) * mm, "end": v(93.6, -3.27) * mm});
            skLineSegment(sketch, "E4311", {"start": v(93.6, -3.27) * mm, "end": v(93.44, -3.84) * mm});
            skLineSegment(sketch, "E4312", {"start": v(93.44, -3.84) * mm, "end": v(93.31, -4.4) * mm});
            skLineSegment(sketch, "E4313", {"start": v(93.31, -4.4) * mm, "end": v(93.23, -4.96) * mm});
            skLineSegment(sketch, "E4314", {"start": v(93.23, -4.96) * mm, "end": v(93.17, -5.5) * mm});
            skLineSegment(sketch, "E4315", {"start": v(93.17, -5.5) * mm, "end": v(93.16, -6.02) * mm});
            skLineSegment(sketch, "E4316", {"start": v(93.16, -6.02) * mm, "end": v(93.16, -6.25) * mm});
            skLineSegment(sketch, "E4317", {"start": v(93.16, -6.25) * mm, "end": v(93.18, -6.47) * mm});
            skLineSegment(sketch, "E4318", {"start": v(93.18, -6.47) * mm, "end": v(93.19, -6.57) * mm});
            skLineSegment(sketch, "E4319", {"start": v(93.19, -6.57) * mm, "end": v(93.2, -6.67) * mm});
            skLineSegment(sketch, "E4320", {"start": v(93.2, -6.67) * mm, "end": v(93.21, -6.76) * mm});
            skLineSegment(sketch, "E4321", {"start": v(93.21, -6.76) * mm, "end": v(93.23, -6.85) * mm});
            skLineSegment(sketch, "E4322", {"start": v(93.23, -6.85) * mm, "end": v(93.25, -6.94) * mm});
            skLineSegment(sketch, "E4323", {"start": v(93.25, -6.94) * mm, "end": v(93.28, -7.02) * mm});
            skLineSegment(sketch, "E4324", {"start": v(93.28, -7.02) * mm, "end": v(93.3, -7.1) * mm});
            skLineSegment(sketch, "E4325", {"start": v(93.3, -7.1) * mm, "end": v(93.33, -7.18) * mm});
            skLineSegment(sketch, "E4326", {"start": v(93.33, -7.18) * mm, "end": v(93.36, -7.25) * mm});
            skLineSegment(sketch, "E4327", {"start": v(93.36, -7.25) * mm, "end": v(93.4, -7.32) * mm});
            skLineSegment(sketch, "E4328", {"start": v(93.4, -7.32) * mm, "end": v(93.43, -7.39) * mm});
            skLineSegment(sketch, "E4329", {"start": v(93.43, -7.39) * mm, "end": v(93.46, -7.45) * mm});
            skLineSegment(sketch, "E4330", {"start": v(93.46, -7.45) * mm, "end": v(93.5, -7.5) * mm});
            skLineSegment(sketch, "E4331", {"start": v(93.5, -7.5) * mm, "end": v(93.54, -7.56) * mm});
            skLineSegment(sketch, "E4332", {"start": v(93.54, -7.56) * mm, "end": v(93.59, -7.6) * mm});
            skLineSegment(sketch, "E4333", {"start": v(93.59, -7.6) * mm, "end": v(93.63, -7.65) * mm});
            skLineSegment(sketch, "E4334", {"start": v(93.63, -7.65) * mm, "end": v(93.68, -7.7) * mm});
            skLineSegment(sketch, "E4335", {"start": v(93.68, -7.7) * mm, "end": v(93.73, -7.74) * mm});
            skLineSegment(sketch, "E4336", {"start": v(93.73, -7.74) * mm, "end": v(93.79, -7.77) * mm});
            skLineSegment(sketch, "E4337", {"start": v(93.79, -7.77) * mm, "end": v(93.84, -7.8) * mm});
            skLineSegment(sketch, "E4338", {"start": v(93.84, -7.8) * mm, "end": v(93.9, -7.83) * mm});
            skLineSegment(sketch, "E4339", {"start": v(93.9, -7.83) * mm, "end": v(93.96, -7.86) * mm});
            skLineSegment(sketch, "E4340", {"start": v(93.96, -7.86) * mm, "end": v(94.03, -7.88) * mm});
            skLineSegment(sketch, "E4341", {"start": v(94.03, -7.88) * mm, "end": v(94.1, -7.9) * mm});
            skLineSegment(sketch, "E4342", {"start": v(94.1, -7.9) * mm, "end": v(94.16, -7.9) * mm});
            skLineSegment(sketch, "E4343", {"start": v(94.16, -7.9) * mm, "end": v(94.23, -7.91) * mm});
            skLineSegment(sketch, "E4344", {"start": v(94.23, -7.91) * mm, "end": v(94.3, -7.92) * mm});
            skLineSegment(sketch, "E4345", {"start": v(94.3, -7.92) * mm, "end": v(94.38, -7.92) * mm});
            skLineSegment(sketch, "E4346", {"start": v(94.38, -7.92) * mm, "end": v(94.47, -7.92) * mm});
            skLineSegment(sketch, "E4347", {"start": v(94.47, -7.92) * mm, "end": v(94.57, -7.9) * mm});
            skLineSegment(sketch, "E4348", {"start": v(94.57, -7.9) * mm, "end": v(94.67, -7.9) * mm});
            skLineSegment(sketch, "E4349", {"start": v(94.67, -7.9) * mm, "end": v(94.77, -7.87) * mm});
            skLineSegment(sketch, "E4350", {"start": v(94.77, -7.87) * mm, "end": v(94.88, -7.84) * mm});
            skLineSegment(sketch, "E4351", {"start": v(94.88, -7.84) * mm, "end": v(94.99, -7.8) * mm});
            skLineSegment(sketch, "E4352", {"start": v(94.99, -7.8) * mm, "end": v(95.1, -7.76) * mm});
            skLineSegment(sketch, "E4353", {"start": v(95.1, -7.76) * mm, "end": v(95.21, -7.72) * mm});
            skLineSegment(sketch, "E4354", {"start": v(95.21, -7.72) * mm, "end": v(95.33, -7.66) * mm});
            skLineSegment(sketch, "E4355", {"start": v(95.33, -7.66) * mm, "end": v(95.45, -7.6) * mm});
            skLineSegment(sketch, "E4356", {"start": v(95.45, -7.6) * mm, "end": v(95.57, -7.53) * mm});
            skLineSegment(sketch, "E4357", {"start": v(95.57, -7.53) * mm, "end": v(95.7, -7.46) * mm});
            skLineSegment(sketch, "E4358", {"start": v(95.7, -7.46) * mm, "end": v(95.83, -7.38) * mm});
            skLineSegment(sketch, "E4359", {"start": v(95.83, -7.38) * mm, "end": v(95.96, -7.3) * mm});
            skLineSegment(sketch, "E4360", {"start": v(95.96, -7.3) * mm, "end": v(96.24, -7.1) * mm});
            skLineSegment(sketch, "E4361", {"start": v(96.24, -7.1) * mm, "end": v(96.38, -6.99) * mm});
            skLineSegment(sketch, "E4362", {"start": v(96.38, -6.99) * mm, "end": v(96.53, -6.87) * mm});
            skLineSegment(sketch, "E4363", {"start": v(96.53, -6.87) * mm, "end": v(96.69, -6.74) * mm});
            skLineSegment(sketch, "E4364", {"start": v(96.69, -6.74) * mm, "end": v(96.85, -6.6) * mm});
            skLineSegment(sketch, "E4365", {"start": v(96.85, -6.6) * mm, "end": v(97.03, -6.46) * mm});
            skLineSegment(sketch, "E4366", {"start": v(97.03, -6.46) * mm, "end": v(97.2, -6.3) * mm});
            skLineSegment(sketch, "E4367", {"start": v(97.2, -6.3) * mm, "end": v(97.4, -6.15) * mm});
            skLineSegment(sketch, "E4368", {"start": v(97.4, -6.15) * mm, "end": v(97.8, -5.8) * mm});
            skLineSegment(sketch, "E4369", {"start": v(97.8, -5.8) * mm, "end": v(98.22, -5.41) * mm});
            skLineSegment(sketch, "E4370", {"start": v(98.22, -5.41) * mm, "end": v(98.68, -4.99) * mm});
            skLineSegment(sketch, "E4371", {"start": v(98.68, -4.99) * mm, "end": v(99.17, -4.53) * mm});
            skLineSegment(sketch, "E4372", {"start": v(99.17, -4.53) * mm, "end": v(99.42, -4.3) * mm});
            skLineSegment(sketch, "E4373", {"start": v(99.42, -4.3) * mm, "end": v(99.42, -5.83) * mm});
            skLineSegment(sketch, "E4374", {"start": v(99.42, -5.83) * mm, "end": v(98.86, -6.55) * mm});
            skLineSegment(sketch, "E4375", {"start": v(98.86, -6.55) * mm, "end": v(98.32, -7.21) * mm});
            skLineSegment(sketch, "E4376", {"start": v(98.32, -7.21) * mm, "end": v(97.79, -7.83) * mm});
            skLineSegment(sketch, "E4377", {"start": v(97.79, -7.83) * mm, "end": v(97.27, -8.4) * mm});
            skLineSegment(sketch, "E4378", {"start": v(97.27, -8.4) * mm, "end": v(96.78, -8.94) * mm});
            skLineSegment(sketch, "E4379", {"start": v(96.78, -8.94) * mm, "end": v(96.3, -9.42) * mm});
            skLineSegment(sketch, "E4380", {"start": v(96.3, -9.42) * mm, "end": v(95.83, -9.86) * mm});
            skLineSegment(sketch, "E4381", {"start": v(95.83, -9.86) * mm, "end": v(95.39, -10.25) * mm});
            skLineSegment(sketch, "E4382", {"start": v(95.39, -10.25) * mm, "end": v(95.17, -10.43) * mm});
            skLineSegment(sketch, "E4383", {"start": v(95.17, -10.43) * mm, "end": v(94.96, -10.6) * mm});
            skLineSegment(sketch, "E4384", {"start": v(94.96, -10.6) * mm, "end": v(94.75, -10.75) * mm});
            skLineSegment(sketch, "E4385", {"start": v(94.75, -10.75) * mm, "end": v(94.54, -10.9) * mm});
            skLineSegment(sketch, "E4386", {"start": v(94.54, -10.9) * mm, "end": v(94.34, -11.02) * mm});
            skLineSegment(sketch, "E4387", {"start": v(94.34, -11.02) * mm, "end": v(94.14, -11.14) * mm});
            skLineSegment(sketch, "E4388", {"start": v(94.14, -11.14) * mm, "end": v(93.95, -11.25) * mm});
            skLineSegment(sketch, "E4389", {"start": v(93.95, -11.25) * mm, "end": v(93.76, -11.35) * mm});
            skLineSegment(sketch, "E4390", {"start": v(93.76, -11.35) * mm, "end": v(93.58, -11.44) * mm});
            skLineSegment(sketch, "E4391", {"start": v(93.58, -11.44) * mm, "end": v(93.4, -11.51) * mm});
            skLineSegment(sketch, "E4392", {"start": v(93.4, -11.51) * mm, "end": v(93.22, -11.58) * mm});
            skLineSegment(sketch, "E4393", {"start": v(93.22, -11.58) * mm, "end": v(93.05, -11.63) * mm});
            skLineSegment(sketch, "E4394", {"start": v(93.05, -11.63) * mm, "end": v(92.88, -11.67) * mm});
            skLineSegment(sketch, "E4395", {"start": v(92.88, -11.67) * mm, "end": v(92.71, -11.7) * mm});
            skLineSegment(sketch, "E4396", {"start": v(92.71, -11.7) * mm, "end": v(92.55, -11.71) * mm});
            skLineSegment(sketch, "E4397", {"start": v(92.55, -11.71) * mm, "end": v(92.4, -11.72) * mm});
            skLineSegment(sketch, "E4398", {"start": v(92.4, -11.72) * mm, "end": v(92.27, -11.72) * mm});
            skLineSegment(sketch, "E4399", {"start": v(92.27, -11.72) * mm, "end": v(92.16, -11.7) * mm});
            skLineSegment(sketch, "E4400", {"start": v(92.16, -11.7) * mm, "end": v(92.04, -11.7) * mm});
            skLineSegment(sketch, "E4401", {"start": v(92.04, -11.7) * mm, "end": v(91.94, -11.67) * mm});
            skLineSegment(sketch, "E4402", {"start": v(91.94, -11.67) * mm, "end": v(91.83, -11.65) * mm});
            skLineSegment(sketch, "E4403", {"start": v(91.83, -11.65) * mm, "end": v(91.73, -11.61) * mm});
            skLineSegment(sketch, "E4404", {"start": v(91.73, -11.61) * mm, "end": v(91.63, -11.57) * mm});
            skLineSegment(sketch, "E4405", {"start": v(91.63, -11.57) * mm, "end": v(91.54, -11.53) * mm});
            skLineSegment(sketch, "E4406", {"start": v(91.54, -11.53) * mm, "end": v(91.45, -11.48) * mm});
            skLineSegment(sketch, "E4407", {"start": v(91.45, -11.48) * mm, "end": v(91.37, -11.42) * mm});
            skLineSegment(sketch, "E4408", {"start": v(91.37, -11.42) * mm, "end": v(91.3, -11.36) * mm});
            skLineSegment(sketch, "E4409", {"start": v(91.3, -11.36) * mm, "end": v(91.22, -11.3) * mm});
            skLineSegment(sketch, "E4410", {"start": v(91.22, -11.3) * mm, "end": v(91.15, -11.22) * mm});
            skLineSegment(sketch, "E4411", {"start": v(91.15, -11.22) * mm, "end": v(91.08, -11.14) * mm});
            skLineSegment(sketch, "E4412", {"start": v(91.08, -11.14) * mm, "end": v(91.02, -11.05) * mm});
            skLineSegment(sketch, "E4413", {"start": v(91.02, -11.05) * mm, "end": v(90.96, -10.96) * mm});
            skLineSegment(sketch, "E4414", {"start": v(90.96, -10.96) * mm, "end": v(90.91, -10.86) * mm});
            skLineSegment(sketch, "E4415", {"start": v(90.91, -10.86) * mm, "end": v(90.86, -10.76) * mm});
            skLineSegment(sketch, "E4416", {"start": v(90.86, -10.76) * mm, "end": v(90.82, -10.65) * mm});
            skLineSegment(sketch, "E4417", {"start": v(90.82, -10.65) * mm, "end": v(90.78, -10.53) * mm});
            skLineSegment(sketch, "E4418", {"start": v(90.78, -10.53) * mm, "end": v(90.74, -10.41) * mm});
            skLineSegment(sketch, "E4419", {"start": v(90.74, -10.41) * mm, "end": v(90.7, -10.29) * mm});
            skLineSegment(sketch, "E4420", {"start": v(90.7, -10.29) * mm, "end": v(90.67, -10.15) * mm});
            skLineSegment(sketch, "E4421", {"start": v(90.67, -10.15) * mm, "end": v(90.65, -10.02) * mm});
            skLineSegment(sketch, "E4422", {"start": v(90.65, -10.02) * mm, "end": v(90.62, -9.87) * mm});
            skLineSegment(sketch, "E4423", {"start": v(90.62, -9.87) * mm, "end": v(90.58, -9.57) * mm});
            skLineSegment(sketch, "E4424", {"start": v(90.58, -9.57) * mm, "end": v(90.56, -9.24) * mm});
            skLineSegment(sketch, "E4425", {"start": v(90.56, -9.24) * mm, "end": v(90.54, -8.89) * mm});
            skLineSegment(sketch, "E4426", {"start": v(90.54, -8.89) * mm, "end": v(90.54, -8.7) * mm});
            skLineSegment(sketch, "E4427", {"start": v(90.54, -8.7) * mm, "end": v(90.57, -7.67) * mm});
            skLineSegment(sketch, "E4428", {"start": v(90.57, -7.67) * mm, "end": v(90.67, -6.6) * mm});
            skLineSegment(sketch, "E4429", {"start": v(90.67, -6.6) * mm, "end": v(90.83, -5.49) * mm});
            skLineSegment(sketch, "E4430", {"start": v(90.83, -5.49) * mm, "end": v(91.05, -4.34) * mm});
            skLineSegment(sketch, "E4431", {"start": v(92.6, 0.81) * mm, "end": v(92.13, 0.64) * mm});
            skLineSegment(sketch, "E4432", {"start": v(92.13, 0.64) * mm, "end": v(91.63, 0.45) * mm});
            skLineSegment(sketch, "E4433", {"start": v(91.63, 0.45) * mm, "end": v(91.1, 0.23) * mm});
            skLineSegment(sketch, "E4434", {"start": v(91.1, 0.23) * mm, "end": v(90.57, -0.02) * mm});
            skLineSegment(sketch, "E4435", {"start": v(90.57, -0.02) * mm, "end": v(90, -0.28) * mm});
            skLineSegment(sketch, "E4436", {"start": v(90, -0.28) * mm, "end": v(89.42, -0.58) * mm});
            skLineSegment(sketch, "E4437", {"start": v(89.42, -0.58) * mm, "end": v(88.82, -0.9) * mm});
            skLineSegment(sketch, "E4438", {"start": v(88.82, -0.9) * mm, "end": v(88.2, -1.23) * mm});
            skLineSegment(sketch, "E4439", {"start": v(88.2, -1.23) * mm, "end": v(87.89, -1.4) * mm});
            skLineSegment(sketch, "E4440", {"start": v(87.89, -1.4) * mm, "end": v(87.6, -1.57) * mm});
            skLineSegment(sketch, "E4441", {"start": v(87.6, -1.57) * mm, "end": v(87.32, -1.73) * mm});
            skLineSegment(sketch, "E4442", {"start": v(87.32, -1.73) * mm, "end": v(87.06, -1.88) * mm});
            skLineSegment(sketch, "E4443", {"start": v(87.06, -1.88) * mm, "end": v(86.81, -2.02) * mm});
            skLineSegment(sketch, "E4444", {"start": v(86.81, -2.02) * mm, "end": v(86.58, -2.16) * mm});
            skLineSegment(sketch, "E4445", {"start": v(86.58, -2.16) * mm, "end": v(86.37, -2.29) * mm});
            skLineSegment(sketch, "E4446", {"start": v(86.37, -2.29) * mm, "end": v(86.17, -2.41) * mm});
            skLineSegment(sketch, "E4447", {"start": v(86.17, -2.41) * mm, "end": v(85.98, -2.53) * mm});
            skLineSegment(sketch, "E4448", {"start": v(85.98, -2.53) * mm, "end": v(85.82, -2.64) * mm});
            skLineSegment(sketch, "E4449", {"start": v(85.82, -2.64) * mm, "end": v(85.74, -2.69) * mm});
            skLineSegment(sketch, "E4450", {"start": v(85.74, -2.69) * mm, "end": v(85.66, -2.74) * mm});
            skLineSegment(sketch, "E4451", {"start": v(85.66, -2.74) * mm, "end": v(85.6, -2.79) * mm});
            skLineSegment(sketch, "E4452", {"start": v(85.6, -2.79) * mm, "end": v(85.53, -2.84) * mm});
            skLineSegment(sketch, "E4453", {"start": v(85.53, -2.84) * mm, "end": v(85.47, -2.88) * mm});
            skLineSegment(sketch, "E4454", {"start": v(85.47, -2.88) * mm, "end": v(85.4, -2.93) * mm});
            skLineSegment(sketch, "E4455", {"start": v(85.4, -2.93) * mm, "end": v(85.35, -2.97) * mm});
            skLineSegment(sketch, "E4456", {"start": v(85.35, -2.97) * mm, "end": v(85.3, -3) * mm});
            skLineSegment(sketch, "E4457", {"start": v(85.3, -3) * mm, "end": v(85.26, -3.05) * mm});
            skLineSegment(sketch, "E4458", {"start": v(85.26, -3.05) * mm, "end": v(85.21, -3.08) * mm});
            skLineSegment(sketch, "E4459", {"start": v(85.21, -3.08) * mm, "end": v(85.17, -3.12) * mm});
            skLineSegment(sketch, "E4460", {"start": v(85.17, -3.12) * mm, "end": v(85.16, -3.14) * mm});
            skLineSegment(sketch, "E4461", {"start": v(85.16, -3.14) * mm, "end": v(85.14, -3.15) * mm});
            skLineSegment(sketch, "E4462", {"start": v(85.14, -3.15) * mm, "end": v(85.08, -3.2) * mm});
            skLineSegment(sketch, "E4463", {"start": v(85.08, -3.2) * mm, "end": v(85.02, -3.27) * mm});
            skLineSegment(sketch, "E4464", {"start": v(85.02, -3.27) * mm, "end": v(84.97, -3.34) * mm});
            skLineSegment(sketch, "E4465", {"start": v(84.97, -3.34) * mm, "end": v(84.91, -3.41) * mm});
            skLineSegment(sketch, "E4466", {"start": v(84.91, -3.41) * mm, "end": v(84.86, -3.49) * mm});
            skLineSegment(sketch, "E4467", {"start": v(84.86, -3.49) * mm, "end": v(84.8, -3.57) * mm});
            skLineSegment(sketch, "E4468", {"start": v(84.8, -3.57) * mm, "end": v(84.75, -3.66) * mm});
            skLineSegment(sketch, "E4469", {"start": v(84.75, -3.66) * mm, "end": v(84.7, -3.76) * mm});
            skLineSegment(sketch, "E4470", {"start": v(84.7, -3.76) * mm, "end": v(84.65, -3.86) * mm});
            skLineSegment(sketch, "E4471", {"start": v(84.65, -3.86) * mm, "end": v(84.6, -3.97) * mm});
            skLineSegment(sketch, "E4472", {"start": v(84.6, -3.97) * mm, "end": v(84.55, -4.08) * mm});
            skLineSegment(sketch, "E4473", {"start": v(84.55, -4.08) * mm, "end": v(84.5, -4.2) * mm});
            skLineSegment(sketch, "E4474", {"start": v(84.5, -4.2) * mm, "end": v(84.4, -4.46) * mm});
            skLineSegment(sketch, "E4475", {"start": v(84.4, -4.46) * mm, "end": v(84.32, -4.74) * mm});
            skLineSegment(sketch, "E4476", {"start": v(84.32, -4.74) * mm, "end": v(84.23, -5.02) * mm});
            skLineSegment(sketch, "E4477", {"start": v(84.23, -5.02) * mm, "end": v(84.16, -5.28) * mm});
            skLineSegment(sketch, "E4478", {"start": v(84.16, -5.28) * mm, "end": v(84.1, -5.53) * mm});
            skLineSegment(sketch, "E4479", {"start": v(84.1, -5.53) * mm, "end": v(84.07, -5.64) * mm});
            skLineSegment(sketch, "E4480", {"start": v(84.07, -5.64) * mm, "end": v(84.05, -5.75) * mm});
            skLineSegment(sketch, "E4481", {"start": v(84.05, -5.75) * mm, "end": v(84.03, -5.86) * mm});
            skLineSegment(sketch, "E4482", {"start": v(84.03, -5.86) * mm, "end": v(84, -5.96) * mm});
            skLineSegment(sketch, "E4483", {"start": v(84, -5.96) * mm, "end": v(84, -6.06) * mm});
            skLineSegment(sketch, "E4484", {"start": v(84, -6.06) * mm, "end": v(83.98, -6.16) * mm});
            skLineSegment(sketch, "E4485", {"start": v(83.98, -6.16) * mm, "end": v(83.97, -6.25) * mm});
            skLineSegment(sketch, "E4486", {"start": v(83.97, -6.25) * mm, "end": v(83.96, -6.33) * mm});
            skLineSegment(sketch, "E4487", {"start": v(83.96, -6.33) * mm, "end": v(83.96, -6.41) * mm});
            skLineSegment(sketch, "E4488", {"start": v(83.96, -6.41) * mm, "end": v(83.96, -6.49) * mm});
            skLineSegment(sketch, "E4489", {"start": v(83.96, -6.49) * mm, "end": v(83.96, -6.53) * mm});
            skLineSegment(sketch, "E4490", {"start": v(83.96, -6.53) * mm, "end": v(83.96, -6.58) * mm});
            skLineSegment(sketch, "E4491", {"start": v(83.96, -6.58) * mm, "end": v(83.97, -6.62) * mm});
            skLineSegment(sketch, "E4492", {"start": v(83.97, -6.62) * mm, "end": v(83.97, -6.66) * mm});
            skLineSegment(sketch, "E4493", {"start": v(83.97, -6.66) * mm, "end": v(83.98, -6.7) * mm});
            skLineSegment(sketch, "E4494", {"start": v(83.98, -6.7) * mm, "end": v(83.99, -6.74) * mm});
            skLineSegment(sketch, "E4495", {"start": v(83.99, -6.74) * mm, "end": v(84, -6.78) * mm});
            skLineSegment(sketch, "E4496", {"start": v(84, -6.78) * mm, "end": v(84.01, -6.81) * mm});
            skLineSegment(sketch, "E4497", {"start": v(84.01, -6.81) * mm, "end": v(84.02, -6.85) * mm});
            skLineSegment(sketch, "E4498", {"start": v(84.02, -6.85) * mm, "end": v(84.04, -6.89) * mm});
            skLineSegment(sketch, "E4499", {"start": v(84.04, -6.89) * mm, "end": v(84.06, -6.92) * mm});
            skLineSegment(sketch, "E4500", {"start": v(84.06, -6.92) * mm, "end": v(84.08, -6.95) * mm});
            skLineSegment(sketch, "E4501", {"start": v(84.08, -6.95) * mm, "end": v(84.1, -6.99) * mm});
            skLineSegment(sketch, "E4502", {"start": v(84.1, -6.99) * mm, "end": v(84.12, -7.02) * mm});
            skLineSegment(sketch, "E4503", {"start": v(84.12, -7.02) * mm, "end": v(84.14, -7.05) * mm});
            skLineSegment(sketch, "E4504", {"start": v(84.14, -7.05) * mm, "end": v(84.17, -7.08) * mm});
            skLineSegment(sketch, "E4505", {"start": v(84.17, -7.08) * mm, "end": v(84.2, -7.1) * mm});
            skLineSegment(sketch, "E4506", {"start": v(84.2, -7.1) * mm, "end": v(84.22, -7.13) * mm});
            skLineSegment(sketch, "E4507", {"start": v(84.22, -7.13) * mm, "end": v(84.25, -7.16) * mm});
            skLineSegment(sketch, "E4508", {"start": v(84.25, -7.16) * mm, "end": v(84.28, -7.18) * mm});
            skLineSegment(sketch, "E4509", {"start": v(84.28, -7.18) * mm, "end": v(84.31, -7.2) * mm});
            skLineSegment(sketch, "E4510", {"start": v(84.31, -7.2) * mm, "end": v(84.34, -7.22) * mm});
            skLineSegment(sketch, "E4511", {"start": v(84.34, -7.22) * mm, "end": v(84.37, -7.24) * mm});
            skLineSegment(sketch, "E4512", {"start": v(84.37, -7.24) * mm, "end": v(84.4, -7.25) * mm});
            skLineSegment(sketch, "E4513", {"start": v(84.4, -7.25) * mm, "end": v(84.44, -7.27) * mm});
            skLineSegment(sketch, "E4514", {"start": v(84.44, -7.27) * mm, "end": v(84.47, -7.28) * mm});
            skLineSegment(sketch, "E4515", {"start": v(84.47, -7.28) * mm, "end": v(84.5, -7.29) * mm});
            skLineSegment(sketch, "E4516", {"start": v(84.5, -7.29) * mm, "end": v(84.54, -7.3) * mm});
            skLineSegment(sketch, "E4517", {"start": v(84.54, -7.3) * mm, "end": v(84.58, -7.3) * mm});
            skLineSegment(sketch, "E4518", {"start": v(84.58, -7.3) * mm, "end": v(84.62, -7.3) * mm});
            skLineSegment(sketch, "E4519", {"start": v(84.62, -7.3) * mm, "end": v(84.66, -7.3) * mm});
            skLineSegment(sketch, "E4520", {"start": v(84.66, -7.3) * mm, "end": v(84.7, -7.31) * mm});
            skLineSegment(sketch, "E4521", {"start": v(84.7, -7.31) * mm, "end": v(84.73, -7.3) * mm});
            skLineSegment(sketch, "E4522", {"start": v(84.73, -7.3) * mm, "end": v(84.77, -7.3) * mm});
            skLineSegment(sketch, "E4523", {"start": v(84.77, -7.3) * mm, "end": v(84.81, -7.3) * mm});
            skLineSegment(sketch, "E4524", {"start": v(84.81, -7.3) * mm, "end": v(84.85, -7.3) * mm});
            skLineSegment(sketch, "E4525", {"start": v(84.85, -7.3) * mm, "end": v(84.89, -7.29) * mm});
            skLineSegment(sketch, "E4526", {"start": v(84.89, -7.29) * mm, "end": v(84.93, -7.27) * mm});
            skLineSegment(sketch, "E4527", {"start": v(84.93, -7.27) * mm, "end": v(84.97, -7.26) * mm});
            skLineSegment(sketch, "E4528", {"start": v(84.97, -7.26) * mm, "end": v(85.01, -7.25) * mm});
            skLineSegment(sketch, "E4529", {"start": v(85.01, -7.25) * mm, "end": v(85.06, -7.23) * mm});
            skLineSegment(sketch, "E4530", {"start": v(85.06, -7.23) * mm, "end": v(85.1, -7.21) * mm});
            skLineSegment(sketch, "E4531", {"start": v(85.1, -7.21) * mm, "end": v(85.19, -7.17) * mm});
            skLineSegment(sketch, "E4532", {"start": v(85.19, -7.17) * mm, "end": v(85.28, -7.12) * mm});
            skLineSegment(sketch, "E4533", {"start": v(85.28, -7.12) * mm, "end": v(85.37, -7.06) * mm});
            skLineSegment(sketch, "E4534", {"start": v(85.37, -7.06) * mm, "end": v(85.42, -7.02) * mm});
            skLineSegment(sketch, "E4535", {"start": v(85.42, -7.02) * mm, "end": v(85.47, -6.99) * mm});
            skLineSegment(sketch, "E4536", {"start": v(85.47, -6.99) * mm, "end": v(85.53, -6.94) * mm});
            skLineSegment(sketch, "E4537", {"start": v(85.53, -6.94) * mm, "end": v(85.59, -6.9) * mm});
            skLineSegment(sketch, "E4538", {"start": v(85.59, -6.9) * mm, "end": v(85.65, -6.85) * mm});
            skLineSegment(sketch, "E4539", {"start": v(85.65, -6.85) * mm, "end": v(85.72, -6.8) * mm});
            skLineSegment(sketch, "E4540", {"start": v(85.72, -6.8) * mm, "end": v(85.79, -6.74) * mm});
            skLineSegment(sketch, "E4541", {"start": v(85.79, -6.74) * mm, "end": v(85.86, -6.68) * mm});
            skLineSegment(sketch, "E4542", {"start": v(85.86, -6.68) * mm, "end": v(85.94, -6.62) * mm});
            skLineSegment(sketch, "E4543", {"start": v(85.94, -6.62) * mm, "end": v(86.02, -6.55) * mm});
            skLineSegment(sketch, "E4544", {"start": v(86.02, -6.55) * mm, "end": v(86.1, -6.48) * mm});
            skLineSegment(sketch, "E4545", {"start": v(86.1, -6.48) * mm, "end": v(86.28, -6.33) * mm});
            skLineSegment(sketch, "E4546", {"start": v(86.28, -6.33) * mm, "end": v(86.47, -6.16) * mm});
            skLineSegment(sketch, "E4547", {"start": v(86.47, -6.16) * mm, "end": v(86.57, -6.07) * mm});
            skLineSegment(sketch, "E4548", {"start": v(86.57, -6.07) * mm, "end": v(86.68, -5.98) * mm});
            skLineSegment(sketch, "E4549", {"start": v(86.68, -5.98) * mm, "end": v(86.78, -5.89) * mm});
            skLineSegment(sketch, "E4550", {"start": v(86.78, -5.89) * mm, "end": v(86.87, -5.8) * mm});
            skLineSegment(sketch, "E4551", {"start": v(86.87, -5.8) * mm, "end": v(86.96, -5.73) * mm});
            skLineSegment(sketch, "E4552", {"start": v(86.96, -5.73) * mm, "end": v(87.04, -5.66) * mm});
            skLineSegment(sketch, "E4553", {"start": v(87.04, -5.66) * mm, "end": v(87.12, -5.59) * mm});
            skLineSegment(sketch, "E4554", {"start": v(87.12, -5.59) * mm, "end": v(87.2, -5.52) * mm});
            skLineSegment(sketch, "E4555", {"start": v(87.2, -5.52) * mm, "end": v(87.27, -5.46) * mm});
            skLineSegment(sketch, "E4556", {"start": v(87.27, -5.46) * mm, "end": v(87.34, -5.4) * mm});
            skLineSegment(sketch, "E4557", {"start": v(87.34, -5.4) * mm, "end": v(87.4, -5.35) * mm});
            skLineSegment(sketch, "E4558", {"start": v(87.4, -5.35) * mm, "end": v(87.46, -5.3) * mm});
            skLineSegment(sketch, "E4559", {"start": v(87.46, -5.3) * mm, "end": v(87.48, -5.28) * mm});
            skLineSegment(sketch, "E4560", {"start": v(87.48, -5.28) * mm, "end": v(87.5, -5.25) * mm});
            skLineSegment(sketch, "E4561", {"start": v(87.5, -5.25) * mm, "end": v(87.53, -5.23) * mm});
            skLineSegment(sketch, "E4562", {"start": v(87.53, -5.23) * mm, "end": v(87.56, -5.21) * mm});
            skLineSegment(sketch, "E4563", {"start": v(87.56, -5.21) * mm, "end": v(87.58, -5.2) * mm});
            skLineSegment(sketch, "E4564", {"start": v(87.58, -5.2) * mm, "end": v(87.6, -5.18) * mm});
            skLineSegment(sketch, "E4565", {"start": v(87.6, -5.18) * mm, "end": v(87.62, -5.16) * mm});
            skLineSegment(sketch, "E4566", {"start": v(87.62, -5.16) * mm, "end": v(87.64, -5.14) * mm});
            skLineSegment(sketch, "E4567", {"start": v(87.64, -5.14) * mm, "end": v(87.65, -5.13) * mm});
            skLineSegment(sketch, "E4568", {"start": v(87.65, -5.13) * mm, "end": v(87.67, -5.12) * mm});
            skLineSegment(sketch, "E4569", {"start": v(87.67, -5.12) * mm, "end": v(87.7, -5.1) * mm});
            skLineSegment(sketch, "E4570", {"start": v(87.7, -5.1) * mm, "end": v(87.72, -5.07) * mm});
            skLineSegment(sketch, "E4571", {"start": v(87.72, -5.07) * mm, "end": v(87.75, -5.05) * mm});
            skLineSegment(sketch, "E4572", {"start": v(87.75, -5.05) * mm, "end": v(87.77, -5.03) * mm});
            skLineSegment(sketch, "E4573", {"start": v(87.77, -5.03) * mm, "end": v(87.8, -5) * mm});
            skLineSegment(sketch, "E4574", {"start": v(87.8, -5) * mm, "end": v(87.84, -4.97) * mm});
            skLineSegment(sketch, "E4575", {"start": v(87.84, -4.97) * mm, "end": v(87.87, -4.94) * mm});
            skLineSegment(sketch, "E4576", {"start": v(87.87, -4.94) * mm, "end": v(87.9, -4.91) * mm});
            skLineSegment(sketch, "E4577", {"start": v(87.9, -4.91) * mm, "end": v(87.94, -4.88) * mm});
            skLineSegment(sketch, "E4578", {"start": v(87.94, -4.88) * mm, "end": v(88.02, -4.81) * mm});
            skLineSegment(sketch, "E4579", {"start": v(88.02, -4.81) * mm, "end": v(88.1, -4.74) * mm});
            skLineSegment(sketch, "E4580", {"start": v(88.1, -4.74) * mm, "end": v(88.2, -4.66) * mm});
            skLineSegment(sketch, "E4581", {"start": v(88.2, -4.66) * mm, "end": v(88.3, -4.58) * mm});
            skLineSegment(sketch, "E4582", {"start": v(88.3, -4.58) * mm, "end": v(88.4, -4.49) * mm});
            skLineSegment(sketch, "E4583", {"start": v(88.4, -4.49) * mm, "end": v(88.51, -4.4) * mm});
            skLineSegment(sketch, "E4584", {"start": v(88.51, -4.4) * mm, "end": v(88.63, -4.3) * mm});
            skLineSegment(sketch, "E4585", {"start": v(88.63, -4.3) * mm, "end": v(88.76, -4.18) * mm});
            skLineSegment(sketch, "E4586", {"start": v(88.76, -4.18) * mm, "end": v(88.9, -4.07) * mm});
            skLineSegment(sketch, "E4587", {"start": v(88.9, -4.07) * mm, "end": v(89.03, -3.95) * mm});
            skLineSegment(sketch, "E4588", {"start": v(89.03, -3.95) * mm, "end": v(89.25, -3.77) * mm});
            skLineSegment(sketch, "E4589", {"start": v(89.25, -3.77) * mm, "end": v(89.55, -3.5) * mm});
            skLineSegment(sketch, "E4590", {"start": v(89.55, -3.5) * mm, "end": v(89.83, -3.27) * mm});
            skLineSegment(sketch, "E4591", {"start": v(89.83, -3.27) * mm, "end": v(90.1, -3.04) * mm});
            skLineSegment(sketch, "E4592", {"start": v(90.1, -3.04) * mm, "end": v(90.33, -2.83) * mm});
            skLineSegment(sketch, "E4593", {"start": v(90.33, -2.83) * mm, "end": v(90.55, -2.63) * mm});
            skLineSegment(sketch, "E4594", {"start": v(90.55, -2.63) * mm, "end": v(90.65, -2.53) * mm});
            skLineSegment(sketch, "E4595", {"start": v(90.65, -2.53) * mm, "end": v(90.74, -2.44) * mm});
            skLineSegment(sketch, "E4596", {"start": v(90.74, -2.44) * mm, "end": v(90.83, -2.36) * mm});
            skLineSegment(sketch, "E4597", {"start": v(90.83, -2.36) * mm, "end": v(90.91, -2.28) * mm});
            skLineSegment(sketch, "E4598", {"start": v(90.91, -2.28) * mm, "end": v(91, -2.2) * mm});
            skLineSegment(sketch, "E4599", {"start": v(91, -2.2) * mm, "end": v(91.07, -2.12) * mm});
            skLineSegment(sketch, "E4600", {"start": v(91.07, -2.12) * mm, "end": v(91.34, -1.82) * mm});
            skLineSegment(sketch, "E4601", {"start": v(91.34, -1.82) * mm, "end": v(91.6, -1.5) * mm});
            skLineSegment(sketch, "E4602", {"start": v(91.6, -1.5) * mm, "end": v(91.83, -1.16) * mm});
            skLineSegment(sketch, "E4603", {"start": v(91.83, -1.16) * mm, "end": v(92.04, -0.81) * mm});
            skLineSegment(sketch, "E4604", {"start": v(92.04, -0.81) * mm, "end": v(92.22, -0.43) * mm});
            skLineSegment(sketch, "E4605", {"start": v(92.22, -0.43) * mm, "end": v(92.38, -0.04) * mm});
            skLineSegment(sketch, "E4606", {"start": v(92.38, -0.04) * mm, "end": v(92.5, 0.38) * mm});
            skLineSegment(sketch, "E4607", {"start": v(92.5, 0.38) * mm, "end": v(92.6, 0.81) * mm});
            skSolve(sketch);
        }
        {
            var Q0;
            Q0=qCreatedBy(makeId("Front.planeOp"),FACE);
            var sketch = newSketch(context, id + "F2", { "sketchPlane" : qUnion([Q0])});
            skLineSegment(sketch, "E4608.bottom", {"start": v(83.13, 16.11) * mm, "end": v(-83.13, 16.11) * mm});
            skLineSegment(sketch, "E4608.top", {"start": v(83.13, -16.11) * mm, "end": v(-83.13, -16.11) * mm});
            skLineSegment(sketch, "E4608.left", {"start": v(83.13, 16.11) * mm, "end": v(83.13, -16.11) * mm});
            skLineSegment(sketch, "E4608.right", {"start": v(-83.13, 16.11) * mm, "end": v(-83.13, -16.11) * mm});
            skPoint(sketch, "E4608.middle", {"position": v(0, 0) * mm});
            skSolve(sketch);
        }
        {
            var Q0;
            Q0=qCreatedBy(makeId("Front.planeOp"),FACE);
            var sketch = newSketch(context, id + "F3", { "sketchPlane" : qUnion([Q0])});
            skLineSegment(sketch, "E4609", {"start": v(-74.23, 6.08) * mm, "end": v(-73.86, 6.06) * mm});
            skLineSegment(sketch, "E4610", {"start": v(-73.86, 6.06) * mm, "end": v(-73.52, 6.04) * mm});
            skLineSegment(sketch, "E4611", {"start": v(-73.52, 6.04) * mm, "end": v(-73.21, 6.02) * mm});
            skLineSegment(sketch, "E4612", {"start": v(-73.21, 6.02) * mm, "end": v(-73.07, 6) * mm});
            skLineSegment(sketch, "E4613", {"start": v(-73.07, 6) * mm, "end": v(-72.93, 6) * mm});
            skLineSegment(sketch, "E4614", {"start": v(-72.93, 6) * mm, "end": v(-72.8, 5.98) * mm});
            skLineSegment(sketch, "E4615", {"start": v(-72.8, 5.98) * mm, "end": v(-72.67, 5.97) * mm});
            skLineSegment(sketch, "E4616", {"start": v(-72.67, 5.97) * mm, "end": v(-72.55, 5.95) * mm});
            skLineSegment(sketch, "E4617", {"start": v(-72.55, 5.95) * mm, "end": v(-72.44, 5.94) * mm});
            skLineSegment(sketch, "E4618", {"start": v(-72.44, 5.94) * mm, "end": v(-72.33, 5.92) * mm});
            skLineSegment(sketch, "E4619", {"start": v(-72.33, 5.92) * mm, "end": v(-72.24, 5.9) * mm});
            skLineSegment(sketch, "E4620", {"start": v(-72.24, 5.9) * mm, "end": v(-72.14, 5.9) * mm});
            skLineSegment(sketch, "E4621", {"start": v(-72.14, 5.9) * mm, "end": v(-72.06, 5.88) * mm});
            skLineSegment(sketch, "E4622", {"start": v(-72.06, 5.88) * mm, "end": v(-71.98, 5.86) * mm});
            skLineSegment(sketch, "E4623", {"start": v(-71.98, 5.86) * mm, "end": v(-71.9, 5.84) * mm});
            skLineSegment(sketch, "E4624", {"start": v(-71.9, 5.84) * mm, "end": v(-71.84, 5.82) * mm});
            skLineSegment(sketch, "E4625", {"start": v(-71.84, 5.82) * mm, "end": v(-71.77, 5.8) * mm});
            skLineSegment(sketch, "E4626", {"start": v(-71.77, 5.8) * mm, "end": v(-71.72, 5.77) * mm});
            skLineSegment(sketch, "E4627", {"start": v(-71.72, 5.77) * mm, "end": v(-71.69, 5.76) * mm});
            skLineSegment(sketch, "E4628", {"start": v(-71.69, 5.76) * mm, "end": v(-71.66, 5.74) * mm});
            skLineSegment(sketch, "E4629", {"start": v(-71.66, 5.74) * mm, "end": v(-71.64, 5.73) * mm});
            skLineSegment(sketch, "E4630", {"start": v(-71.64, 5.73) * mm, "end": v(-71.61, 5.71) * mm});
            skLineSegment(sketch, "E4631", {"start": v(-71.61, 5.71) * mm, "end": v(-71.6, 5.7) * mm});
            skLineSegment(sketch, "E4632", {"start": v(-71.6, 5.7) * mm, "end": v(-71.57, 5.68) * mm});
            skLineSegment(sketch, "E4633", {"start": v(-71.57, 5.68) * mm, "end": v(-71.55, 5.67) * mm});
            skLineSegment(sketch, "E4634", {"start": v(-71.55, 5.67) * mm, "end": v(-71.53, 5.65) * mm});
            skLineSegment(sketch, "E4635", {"start": v(-71.53, 5.65) * mm, "end": v(-71.52, 5.63) * mm});
            skLineSegment(sketch, "E4636", {"start": v(-71.52, 5.63) * mm, "end": v(-71.5, 5.61) * mm});
            skLineSegment(sketch, "E4637", {"start": v(-71.5, 5.61) * mm, "end": v(-71.49, 5.6) * mm});
            skLineSegment(sketch, "E4638", {"start": v(-71.49, 5.6) * mm, "end": v(-71.47, 5.58) * mm});
            skLineSegment(sketch, "E4639", {"start": v(-71.47, 5.58) * mm, "end": v(-71.46, 5.56) * mm});
            skLineSegment(sketch, "E4640", {"start": v(-71.46, 5.56) * mm, "end": v(-71.45, 5.54) * mm});
            skLineSegment(sketch, "E4641", {"start": v(-71.45, 5.54) * mm, "end": v(-71.44, 5.52) * mm});
            skLineSegment(sketch, "E4642", {"start": v(-71.44, 5.52) * mm, "end": v(-71.43, 5.5) * mm});
            skLineSegment(sketch, "E4643", {"start": v(-71.43, 5.5) * mm, "end": v(-71.42, 5.47) * mm});
            skLineSegment(sketch, "E4644", {"start": v(-71.42, 5.47) * mm, "end": v(-71.42, 5.45) * mm});
            skLineSegment(sketch, "E4645", {"start": v(-71.42, 5.45) * mm, "end": v(-71.41, 5.43) * mm});
            skLineSegment(sketch, "E4646", {"start": v(-71.41, 5.43) * mm, "end": v(-71.41, 5.4) * mm});
            skLineSegment(sketch, "E4647", {"start": v(-71.41, 5.4) * mm, "end": v(-71.4, 5.38) * mm});
            skLineSegment(sketch, "E4648", {"start": v(-71.4, 5.38) * mm, "end": v(-71.4, 5.36) * mm});
            skLineSegment(sketch, "E4649", {"start": v(-71.4, 5.36) * mm, "end": v(-71.4, 5.34) * mm});
            skLineSegment(sketch, "E4650", {"start": v(-71.4, 5.34) * mm, "end": v(-71.41, 5.32) * mm});
            skLineSegment(sketch, "E4651", {"start": v(-71.41, 5.32) * mm, "end": v(-71.41, 5.3) * mm});
            skLineSegment(sketch, "E4652", {"start": v(-71.41, 5.3) * mm, "end": v(-71.42, 5.28) * mm});
            skLineSegment(sketch, "E4653", {"start": v(-71.42, 5.28) * mm, "end": v(-71.42, 5.26) * mm});
            skLineSegment(sketch, "E4654", {"start": v(-71.42, 5.26) * mm, "end": v(-71.42, 5.24) * mm});
            skLineSegment(sketch, "E4655", {"start": v(-71.42, 5.24) * mm, "end": v(-71.43, 5.22) * mm});
            skLineSegment(sketch, "E4656", {"start": v(-71.43, 5.22) * mm, "end": v(-71.44, 5.2) * mm});
            skLineSegment(sketch, "E4657", {"start": v(-71.44, 5.2) * mm, "end": v(-71.44, 5.2) * mm});
            skLineSegment(sketch, "E4658", {"start": v(-71.44, 5.2) * mm, "end": v(-71.45, 5.18) * mm});
            skLineSegment(sketch, "E4659", {"start": v(-71.45, 5.18) * mm, "end": v(-71.46, 5.17) * mm});
            skLineSegment(sketch, "E4660", {"start": v(-71.46, 5.17) * mm, "end": v(-71.47, 5.15) * mm});
            skLineSegment(sketch, "E4661", {"start": v(-71.47, 5.15) * mm, "end": v(-71.48, 5.14) * mm});
            skLineSegment(sketch, "E4662", {"start": v(-71.48, 5.14) * mm, "end": v(-71.5, 5.13) * mm});
            skLineSegment(sketch, "E4663", {"start": v(-71.5, 5.13) * mm, "end": v(-71.51, 5.12) * mm});
            skLineSegment(sketch, "E4664", {"start": v(-71.51, 5.12) * mm, "end": v(-71.52, 5.11) * mm});
            skLineSegment(sketch, "E4665", {"start": v(-71.52, 5.11) * mm, "end": v(-71.54, 5.1) * mm});
            skLineSegment(sketch, "E4666", {"start": v(-71.54, 5.1) * mm, "end": v(-71.55, 5.1) * mm});
            skLineSegment(sketch, "E4667", {"start": v(-71.55, 5.1) * mm, "end": v(-71.57, 5.1) * mm});
            skLineSegment(sketch, "E4668", {"start": v(-71.57, 5.1) * mm, "end": v(-71.58, 5.08) * mm});
            skLineSegment(sketch, "E4669", {"start": v(-71.58, 5.08) * mm, "end": v(-71.6, 5.08) * mm});
            skLineSegment(sketch, "E4670", {"start": v(-71.6, 5.08) * mm, "end": v(-71.62, 5.07) * mm});
            skLineSegment(sketch, "E4671", {"start": v(-71.62, 5.07) * mm, "end": v(-71.64, 5.06) * mm});
            skLineSegment(sketch, "E4672", {"start": v(-71.64, 5.06) * mm, "end": v(-71.66, 5.06) * mm});
            skLineSegment(sketch, "E4673", {"start": v(-71.66, 5.06) * mm, "end": v(-71.68, 5.05) * mm});
            skLineSegment(sketch, "E4674", {"start": v(-71.68, 5.05) * mm, "end": v(-71.7, 5.04) * mm});
            skLineSegment(sketch, "E4675", {"start": v(-71.7, 5.04) * mm, "end": v(-71.73, 5.04) * mm});
            skLineSegment(sketch, "E4676", {"start": v(-71.73, 5.04) * mm, "end": v(-71.78, 5.03) * mm});
            skLineSegment(sketch, "E4677", {"start": v(-71.78, 5.03) * mm, "end": v(-71.84, 5.02) * mm});
            skLineSegment(sketch, "E4678", {"start": v(-71.84, 5.02) * mm, "end": v(-71.87, 5.01) * mm});
            skLineSegment(sketch, "E4679", {"start": v(-71.87, 5.01) * mm, "end": v(-71.93, 5) * mm});
            skLineSegment(sketch, "E4680", {"start": v(-71.93, 5) * mm, "end": v(-72.07, 4.98) * mm});
            skLineSegment(sketch, "E4681", {"start": v(-72.07, 4.98) * mm, "end": v(-72.21, 4.96) * mm});
            skLineSegment(sketch, "E4682", {"start": v(-72.21, 4.96) * mm, "end": v(-72.37, 4.94) * mm});
            skLineSegment(sketch, "E4683", {"start": v(-72.37, 4.94) * mm, "end": v(-72.45, 4.92) * mm});
            skLineSegment(sketch, "E4684", {"start": v(-72.45, 4.92) * mm, "end": v(-72.51, 4.91) * mm});
            skLineSegment(sketch, "E4685", {"start": v(-72.51, 4.91) * mm, "end": v(-72.58, 4.9) * mm});
            skLineSegment(sketch, "E4686", {"start": v(-72.58, 4.9) * mm, "end": v(-72.66, 4.88) * mm});
            skLineSegment(sketch, "E4687", {"start": v(-72.66, 4.88) * mm, "end": v(-72.73, 4.87) * mm});
            skLineSegment(sketch, "E4688", {"start": v(-72.73, 4.87) * mm, "end": v(-72.82, 4.85) * mm});
            skLineSegment(sketch, "E4689", {"start": v(-72.82, 4.85) * mm, "end": v(-72.9, 4.83) * mm});
            skLineSegment(sketch, "E4690", {"start": v(-72.9, 4.83) * mm, "end": v(-73, 4.81) * mm});
            skLineSegment(sketch, "E4691", {"start": v(-73, 4.81) * mm, "end": v(-73.1, 4.8) * mm});
            skLineSegment(sketch, "E4692", {"start": v(-73.1, 4.8) * mm, "end": v(-73.2, 4.77) * mm});
            skLineSegment(sketch, "E4693", {"start": v(-73.2, 4.77) * mm, "end": v(-73.31, 4.75) * mm});
            skLineSegment(sketch, "E4694", {"start": v(-73.31, 4.75) * mm, "end": v(-73.54, 4.7) * mm});
            skLineSegment(sketch, "E4695", {"start": v(-73.54, 4.7) * mm, "end": v(-73.8, 4.64) * mm});
            skLineSegment(sketch, "E4696", {"start": v(-73.8, 4.64) * mm, "end": v(-74.07, 4.58) * mm});
            skLineSegment(sketch, "E4697", {"start": v(-74.07, 4.58) * mm, "end": v(-74.2, 4.55) * mm});
            skLineSegment(sketch, "E4698", {"start": v(-74.2, 4.55) * mm, "end": v(-74.33, 4.52) * mm});
            skLineSegment(sketch, "E4699", {"start": v(-74.33, 4.52) * mm, "end": v(-74.46, 4.5) * mm});
            skLineSegment(sketch, "E4700", {"start": v(-74.46, 4.5) * mm, "end": v(-74.57, 4.47) * mm});
            skLineSegment(sketch, "E4701", {"start": v(-74.57, 4.47) * mm, "end": v(-74.67, 4.45) * mm});
            skLineSegment(sketch, "E4702", {"start": v(-74.67, 4.45) * mm, "end": v(-74.77, 4.43) * mm});
            skLineSegment(sketch, "E4703", {"start": v(-74.77, 4.43) * mm, "end": v(-74.82, 4.42) * mm});
            skLineSegment(sketch, "E4704", {"start": v(-74.82, 4.42) * mm, "end": v(-74.86, 4.4) * mm});
            skLineSegment(sketch, "E4705", {"start": v(-74.86, 4.4) * mm, "end": v(-74.9, 4.4) * mm});
            skLineSegment(sketch, "E4706", {"start": v(-74.9, 4.4) * mm, "end": v(-74.94, 4.4) * mm});
            skLineSegment(sketch, "E4707", {"start": v(-74.94, 4.4) * mm, "end": v(-74.98, 4.38) * mm});
            skLineSegment(sketch, "E4708", {"start": v(-74.98, 4.38) * mm, "end": v(-75.02, 4.38) * mm});
            skLineSegment(sketch, "E4709", {"start": v(-75.02, 4.38) * mm, "end": v(-75.05, 4.37) * mm});
            skLineSegment(sketch, "E4710", {"start": v(-75.05, 4.37) * mm, "end": v(-75.08, 4.37) * mm});
            skLineSegment(sketch, "E4711", {"start": v(-75.08, 4.37) * mm, "end": v(-75.11, 4.36) * mm});
            skLineSegment(sketch, "E4712", {"start": v(-75.11, 4.36) * mm, "end": v(-75.14, 4.35) * mm});
            skLineSegment(sketch, "E4713", {"start": v(-75.14, 4.35) * mm, "end": v(-75.17, 4.35) * mm});
            skLineSegment(sketch, "E4714", {"start": v(-75.17, 4.35) * mm, "end": v(-75.2, 4.35) * mm});
            skLineSegment(sketch, "E4715", {"start": v(-75.2, 4.35) * mm, "end": v(-75.2, 4.34) * mm});
            skLineSegment(sketch, "E4716", {"start": v(-75.2, 4.34) * mm, "end": v(-75.21, 4.34) * mm});
            skLineSegment(sketch, "E4717", {"start": v(-75.21, 4.34) * mm, "end": v(-75.22, 4.34) * mm});
            skLineSegment(sketch, "E4718", {"start": v(-75.22, 4.34) * mm, "end": v(-75.23, 4.34) * mm});
            skLineSegment(sketch, "E4719", {"start": v(-75.23, 4.34) * mm, "end": v(-75.24, 4.34) * mm});
            skLineSegment(sketch, "E4720", {"start": v(-75.24, 4.34) * mm, "end": v(-75.25, 4.34) * mm});
            skLineSegment(sketch, "E4721", {"start": v(-75.25, 4.34) * mm, "end": v(-75.26, 4.34) * mm});
            skLineSegment(sketch, "E4722", {"start": v(-75.26, 4.34) * mm, "end": v(-75.27, 4.33) * mm});
            skLineSegment(sketch, "E4723", {"start": v(-75.27, 4.33) * mm, "end": v(-75.27, 4.33) * mm});
            skLineSegment(sketch, "E4724", {"start": v(-75.27, 4.33) * mm, "end": v(-75.28, 4.33) * mm});
            skLineSegment(sketch, "E4725", {"start": v(-75.28, 4.33) * mm, "end": v(-75.29, 4.33) * mm});
            skLineSegment(sketch, "E4726", {"start": v(-75.29, 4.33) * mm, "end": v(-75.3, 4.33) * mm});
            skLineSegment(sketch, "E4727", {"start": v(-75.3, 4.33) * mm, "end": v(-75.3, 4.33) * mm});
            skLineSegment(sketch, "E4728", {"start": v(-75.3, 4.33) * mm, "end": v(-75.31, 4.33) * mm});
            skLineSegment(sketch, "E4729", {"start": v(-75.31, 4.33) * mm, "end": v(-75.31, 4.33) * mm});
            skLineSegment(sketch, "E4730", {"start": v(-75.31, 4.33) * mm, "end": v(-75.35, 4.33) * mm});
            skLineSegment(sketch, "E4731", {"start": v(-75.35, 4.33) * mm, "end": v(-75.38, 4.33) * mm});
            skLineSegment(sketch, "E4732", {"start": v(-75.38, 4.33) * mm, "end": v(-75.41, 4.34) * mm});
            skLineSegment(sketch, "E4733", {"start": v(-75.41, 4.34) * mm, "end": v(-75.44, 4.34) * mm});
            skLineSegment(sketch, "E4734", {"start": v(-75.44, 4.34) * mm, "end": v(-75.47, 4.35) * mm});
            skLineSegment(sketch, "E4735", {"start": v(-75.47, 4.35) * mm, "end": v(-75.5, 4.36) * mm});
            skLineSegment(sketch, "E4736", {"start": v(-75.5, 4.36) * mm, "end": v(-75.53, 4.36) * mm});
            skLineSegment(sketch, "E4737", {"start": v(-75.53, 4.36) * mm, "end": v(-75.56, 4.37) * mm});
            skLineSegment(sketch, "E4738", {"start": v(-75.56, 4.37) * mm, "end": v(-75.58, 4.39) * mm});
            skLineSegment(sketch, "E4739", {"start": v(-75.58, 4.39) * mm, "end": v(-75.6, 4.4) * mm});
            skLineSegment(sketch, "E4740", {"start": v(-75.6, 4.4) * mm, "end": v(-75.63, 4.41) * mm});
            skLineSegment(sketch, "E4741", {"start": v(-75.63, 4.41) * mm, "end": v(-75.66, 4.43) * mm});
            skLineSegment(sketch, "E4742", {"start": v(-75.66, 4.43) * mm, "end": v(-75.68, 4.45) * mm});
            skLineSegment(sketch, "E4743", {"start": v(-75.68, 4.45) * mm, "end": v(-75.7, 4.47) * mm});
            skLineSegment(sketch, "E4744", {"start": v(-75.7, 4.47) * mm, "end": v(-75.72, 4.49) * mm});
            skLineSegment(sketch, "E4745", {"start": v(-75.72, 4.49) * mm, "end": v(-75.74, 4.5) * mm});
            skLineSegment(sketch, "E4746", {"start": v(-75.74, 4.5) * mm, "end": v(-75.75, 4.53) * mm});
            skLineSegment(sketch, "E4747", {"start": v(-75.75, 4.53) * mm, "end": v(-75.77, 4.55) * mm});
            skLineSegment(sketch, "E4748", {"start": v(-75.77, 4.55) * mm, "end": v(-75.78, 4.58) * mm});
            skLineSegment(sketch, "E4749", {"start": v(-75.78, 4.58) * mm, "end": v(-75.8, 4.6) * mm});
            skLineSegment(sketch, "E4750", {"start": v(-75.8, 4.6) * mm, "end": v(-75.8, 4.64) * mm});
            skLineSegment(sketch, "E4751", {"start": v(-75.8, 4.64) * mm, "end": v(-75.82, 4.67) * mm});
            skLineSegment(sketch, "E4752", {"start": v(-75.82, 4.67) * mm, "end": v(-75.83, 4.7) * mm});
            skLineSegment(sketch, "E4753", {"start": v(-75.83, 4.7) * mm, "end": v(-75.84, 4.73) * mm});
            skLineSegment(sketch, "E4754", {"start": v(-75.84, 4.73) * mm, "end": v(-75.85, 4.76) * mm});
            skLineSegment(sketch, "E4755", {"start": v(-75.85, 4.76) * mm, "end": v(-75.86, 4.8) * mm});
            skLineSegment(sketch, "E4756", {"start": v(-75.86, 4.8) * mm, "end": v(-75.86, 4.83) * mm});
            skLineSegment(sketch, "E4757", {"start": v(-75.86, 4.83) * mm, "end": v(-75.87, 4.87) * mm});
            skLineSegment(sketch, "E4758", {"start": v(-75.87, 4.87) * mm, "end": v(-75.87, 4.91) * mm});
            skLineSegment(sketch, "E4759", {"start": v(-75.87, 4.91) * mm, "end": v(-75.88, 5) * mm});
            skLineSegment(sketch, "E4760", {"start": v(-75.88, 5) * mm, "end": v(-75.88, 5.04) * mm});
            skLineSegment(sketch, "E4761", {"start": v(-75.88, 5.04) * mm, "end": v(-75.87, 5.2) * mm});
            skLineSegment(sketch, "E4762", {"start": v(-75.87, 5.2) * mm, "end": v(-75.86, 5.38) * mm});
            skLineSegment(sketch, "E4763", {"start": v(-75.86, 5.38) * mm, "end": v(-75.84, 5.57) * mm});
            skLineSegment(sketch, "E4764", {"start": v(-75.84, 5.57) * mm, "end": v(-75.81, 5.77) * mm});
            skLineSegment(sketch, "E4765", {"start": v(-75.81, 5.77) * mm, "end": v(-75.77, 5.98) * mm});
            skLineSegment(sketch, "E4766", {"start": v(-75.77, 5.98) * mm, "end": v(-75.73, 6.2) * mm});
            skLineSegment(sketch, "E4767", {"start": v(-75.73, 6.2) * mm, "end": v(-75.68, 6.43) * mm});
            skLineSegment(sketch, "E4768", {"start": v(-75.68, 6.43) * mm, "end": v(-75.62, 6.67) * mm});
            skLineSegment(sketch, "E4769", {"start": v(-75.62, 6.67) * mm, "end": v(-75.47, 7.16) * mm});
            skLineSegment(sketch, "E4770", {"start": v(-75.47, 7.16) * mm, "end": v(-75.3, 7.63) * mm});
            skLineSegment(sketch, "E4771", {"start": v(-75.3, 7.63) * mm, "end": v(-75.1, 8.09) * mm});
            skLineSegment(sketch, "E4772", {"start": v(-75.1, 8.09) * mm, "end": v(-74.9, 8.52) * mm});
            skLineSegment(sketch, "E4773", {"start": v(-74.9, 8.52) * mm, "end": v(-74.78, 8.73) * mm});
            skLineSegment(sketch, "E4774", {"start": v(-74.78, 8.73) * mm, "end": v(-74.66, 8.93) * mm});
            skLineSegment(sketch, "E4775", {"start": v(-74.66, 8.93) * mm, "end": v(-74.54, 9.1) * mm});
            skLineSegment(sketch, "E4776", {"start": v(-74.54, 9.1) * mm, "end": v(-74.42, 9.26) * mm});
            skLineSegment(sketch, "E4777", {"start": v(-74.42, 9.26) * mm, "end": v(-74.3, 9.41) * mm});
            skLineSegment(sketch, "E4778", {"start": v(-74.3, 9.41) * mm, "end": v(-74.24, 9.48) * mm});
            skLineSegment(sketch, "E4779", {"start": v(-74.24, 9.48) * mm, "end": v(-74.17, 9.54) * mm});
            skLineSegment(sketch, "E4780", {"start": v(-74.17, 9.54) * mm, "end": v(-74.11, 9.6) * mm});
            skLineSegment(sketch, "E4781", {"start": v(-74.11, 9.6) * mm, "end": v(-74.05, 9.65) * mm});
            skLineSegment(sketch, "E4782", {"start": v(-74.05, 9.65) * mm, "end": v(-73.99, 9.7) * mm});
            skLineSegment(sketch, "E4783", {"start": v(-73.99, 9.7) * mm, "end": v(-73.92, 9.75) * mm});
            skLineSegment(sketch, "E4784", {"start": v(-73.92, 9.75) * mm, "end": v(-73.85, 9.8) * mm});
            skLineSegment(sketch, "E4785", {"start": v(-73.85, 9.8) * mm, "end": v(-73.77, 9.86) * mm});
            skLineSegment(sketch, "E4786", {"start": v(-73.77, 9.86) * mm, "end": v(-73.68, 9.9) * mm});
            skLineSegment(sketch, "E4787", {"start": v(-73.68, 9.9) * mm, "end": v(-73.59, 9.96) * mm});
            skLineSegment(sketch, "E4788", {"start": v(-73.59, 9.96) * mm, "end": v(-73.5, 10.01) * mm});
            skLineSegment(sketch, "E4789", {"start": v(-73.5, 10.01) * mm, "end": v(-73.28, 10.12) * mm});
            skLineSegment(sketch, "E4790", {"start": v(-73.28, 10.12) * mm, "end": v(-73.05, 10.22) * mm});
            skLineSegment(sketch, "E4791", {"start": v(-73.05, 10.22) * mm, "end": v(-72.8, 10.33) * mm});
            skLineSegment(sketch, "E4792", {"start": v(-72.8, 10.33) * mm, "end": v(-72.53, 10.43) * mm});
            skLineSegment(sketch, "E4793", {"start": v(-72.53, 10.43) * mm, "end": v(-72.24, 10.54) * mm});
            skLineSegment(sketch, "E4794", {"start": v(-72.24, 10.54) * mm, "end": v(-72.09, 10.6) * mm});
            skLineSegment(sketch, "E4795", {"start": v(-72.09, 10.6) * mm, "end": v(-71.44, 10.8) * mm});
            skLineSegment(sketch, "E4796", {"start": v(-71.44, 10.8) * mm, "end": v(-70.76, 10.99) * mm});
            skLineSegment(sketch, "E4797", {"start": v(-70.76, 10.99) * mm, "end": v(-70.04, 11.16) * mm});
            skLineSegment(sketch, "E4798", {"start": v(-70.04, 11.16) * mm, "end": v(-69.28, 11.31) * mm});
            skLineSegment(sketch, "E4799", {"start": v(-69.28, 11.31) * mm, "end": v(-68.52, 11.45) * mm});
            skLineSegment(sketch, "E4800", {"start": v(-68.52, 11.45) * mm, "end": v(-67.79, 11.54) * mm});
            skLineSegment(sketch, "E4801", {"start": v(-67.79, 11.54) * mm, "end": v(-67.1, 11.6) * mm});
            skLineSegment(sketch, "E4802", {"start": v(-67.1, 11.6) * mm, "end": v(-66.43, 11.62) * mm});
            skLineSegment(sketch, "E4803", {"start": v(-66.43, 11.62) * mm, "end": v(-66.28, 11.61) * mm});
            skLineSegment(sketch, "E4804", {"start": v(-66.28, 11.61) * mm, "end": v(-66.13, 11.6) * mm});
            skLineSegment(sketch, "E4805", {"start": v(-66.13, 11.6) * mm, "end": v(-66.06, 11.6) * mm});
            skLineSegment(sketch, "E4806", {"start": v(-66.06, 11.6) * mm, "end": v(-66, 11.6) * mm});
            skLineSegment(sketch, "E4807", {"start": v(-66, 11.6) * mm, "end": v(-65.93, 11.58) * mm});
            skLineSegment(sketch, "E4808", {"start": v(-65.93, 11.58) * mm, "end": v(-65.87, 11.57) * mm});
            skLineSegment(sketch, "E4809", {"start": v(-65.87, 11.57) * mm, "end": v(-65.81, 11.56) * mm});
            skLineSegment(sketch, "E4810", {"start": v(-65.81, 11.56) * mm, "end": v(-65.76, 11.54) * mm});
            skLineSegment(sketch, "E4811", {"start": v(-65.76, 11.54) * mm, "end": v(-65.7, 11.53) * mm});
            skLineSegment(sketch, "E4812", {"start": v(-65.7, 11.53) * mm, "end": v(-65.65, 11.51) * mm});
            skLineSegment(sketch, "E4813", {"start": v(-65.65, 11.51) * mm, "end": v(-65.6, 11.5) * mm});
            skLineSegment(sketch, "E4814", {"start": v(-65.6, 11.5) * mm, "end": v(-65.56, 11.47) * mm});
            skLineSegment(sketch, "E4815", {"start": v(-65.56, 11.47) * mm, "end": v(-65.52, 11.45) * mm});
            skLineSegment(sketch, "E4816", {"start": v(-65.52, 11.45) * mm, "end": v(-65.48, 11.43) * mm});
            skLineSegment(sketch, "E4817", {"start": v(-65.48, 11.43) * mm, "end": v(-65.4, 11.38) * mm});
            skLineSegment(sketch, "E4818", {"start": v(-65.4, 11.38) * mm, "end": v(-65.33, 11.33) * mm});
            skLineSegment(sketch, "E4819", {"start": v(-65.33, 11.33) * mm, "end": v(-65.3, 11.3) * mm});
            skLineSegment(sketch, "E4820", {"start": v(-65.3, 11.3) * mm, "end": v(-65.27, 11.28) * mm});
            skLineSegment(sketch, "E4821", {"start": v(-65.27, 11.28) * mm, "end": v(-65.24, 11.25) * mm});
            skLineSegment(sketch, "E4822", {"start": v(-65.24, 11.25) * mm, "end": v(-65.2, 11.22) * mm});
            skLineSegment(sketch, "E4823", {"start": v(-65.2, 11.22) * mm, "end": v(-65.18, 11.19) * mm});
            skLineSegment(sketch, "E4824", {"start": v(-65.18, 11.19) * mm, "end": v(-65.16, 11.16) * mm});
            skLineSegment(sketch, "E4825", {"start": v(-65.16, 11.16) * mm, "end": v(-65.13, 11.12) * mm});
            skLineSegment(sketch, "E4826", {"start": v(-65.13, 11.12) * mm, "end": v(-65.1, 11.09) * mm});
            skLineSegment(sketch, "E4827", {"start": v(-65.1, 11.09) * mm, "end": v(-65.09, 11.05) * mm});
            skLineSegment(sketch, "E4828", {"start": v(-65.09, 11.05) * mm, "end": v(-65.07, 11.02) * mm});
            skLineSegment(sketch, "E4829", {"start": v(-65.07, 11.02) * mm, "end": v(-65.03, 10.94) * mm});
            skLineSegment(sketch, "E4830", {"start": v(-65.03, 10.94) * mm, "end": v(-65.02, 10.92) * mm});
            skLineSegment(sketch, "E4831", {"start": v(-65.02, 10.92) * mm, "end": v(-65.01, 10.9) * mm});
            skLineSegment(sketch, "E4832", {"start": v(-65.01, 10.9) * mm, "end": v(-65, 10.88) * mm});
            skLineSegment(sketch, "E4833", {"start": v(-65, 10.88) * mm, "end": v(-65, 10.85) * mm});
            skLineSegment(sketch, "E4834", {"start": v(-65, 10.85) * mm, "end": v(-64.99, 10.83) * mm});
            skLineSegment(sketch, "E4835", {"start": v(-64.99, 10.83) * mm, "end": v(-64.98, 10.8) * mm});
            skLineSegment(sketch, "E4836", {"start": v(-64.98, 10.8) * mm, "end": v(-64.97, 10.77) * mm});
            skLineSegment(sketch, "E4837", {"start": v(-64.97, 10.77) * mm, "end": v(-64.94, 10.72) * mm});
            skLineSegment(sketch, "E4838", {"start": v(-64.94, 10.72) * mm, "end": v(-64.92, 10.65) * mm});
            skLineSegment(sketch, "E4839", {"start": v(-64.92, 10.65) * mm, "end": v(-64.9, 10.58) * mm});
            skLineSegment(sketch, "E4840", {"start": v(-64.9, 10.58) * mm, "end": v(-64.87, 10.51) * mm});
            skLineSegment(sketch, "E4841", {"start": v(-64.87, 10.51) * mm, "end": v(-64.84, 10.43) * mm});
            skLineSegment(sketch, "E4842", {"start": v(-64.84, 10.43) * mm, "end": v(-64.82, 10.35) * mm});
            skLineSegment(sketch, "E4843", {"start": v(-64.82, 10.35) * mm, "end": v(-64.79, 10.26) * mm});
            skLineSegment(sketch, "E4844", {"start": v(-64.79, 10.26) * mm, "end": v(-64.76, 10.17) * mm});
            skLineSegment(sketch, "E4845", {"start": v(-64.76, 10.17) * mm, "end": v(-64.72, 10.07) * mm});
            skLineSegment(sketch, "E4846", {"start": v(-64.72, 10.07) * mm, "end": v(-64.69, 9.96) * mm});
            skLineSegment(sketch, "E4847", {"start": v(-64.69, 9.96) * mm, "end": v(-64.65, 9.85) * mm});
            skLineSegment(sketch, "E4848", {"start": v(-64.65, 9.85) * mm, "end": v(-64.6, 9.68) * mm});
            skLineSegment(sketch, "E4849", {"start": v(-64.6, 9.68) * mm, "end": v(-64.53, 9.46) * mm});
            skLineSegment(sketch, "E4850", {"start": v(-64.53, 9.46) * mm, "end": v(-64.47, 9.22) * mm});
            skLineSegment(sketch, "E4851", {"start": v(-64.47, 9.22) * mm, "end": v(-64.42, 8.98) * mm});
            skLineSegment(sketch, "E4852", {"start": v(-64.42, 8.98) * mm, "end": v(-64.38, 8.74) * mm});
            skLineSegment(sketch, "E4853", {"start": v(-64.38, 8.74) * mm, "end": v(-64.35, 8.48) * mm});
            skLineSegment(sketch, "E4854", {"start": v(-64.35, 8.48) * mm, "end": v(-64.33, 8.22) * mm});
            skLineSegment(sketch, "E4855", {"start": v(-64.33, 8.22) * mm, "end": v(-64.3, 7.67) * mm});
            skLineSegment(sketch, "E4856", {"start": v(-64.3, 7.67) * mm, "end": v(-64.32, 7.33) * mm});
            skLineSegment(sketch, "E4857", {"start": v(-64.32, 7.33) * mm, "end": v(-64.35, 7) * mm});
            skLineSegment(sketch, "E4858", {"start": v(-64.35, 7) * mm, "end": v(-64.4, 6.7) * mm});
            skLineSegment(sketch, "E4859", {"start": v(-64.4, 6.7) * mm, "end": v(-64.47, 6.4) * mm});
            skLineSegment(sketch, "E4860", {"start": v(-64.47, 6.4) * mm, "end": v(-64.56, 6.1) * mm});
            skLineSegment(sketch, "E4861", {"start": v(-64.56, 6.1) * mm, "end": v(-64.67, 5.82) * mm});
            skLineSegment(sketch, "E4862", {"start": v(-64.67, 5.82) * mm, "end": v(-64.8, 5.55) * mm});
            skLineSegment(sketch, "E4863", {"start": v(-64.8, 5.55) * mm, "end": v(-64.95, 5.3) * mm});
            skLineSegment(sketch, "E4864", {"start": v(-64.95, 5.3) * mm, "end": v(-65.11, 5.05) * mm});
            skLineSegment(sketch, "E4865", {"start": v(-65.11, 5.05) * mm, "end": v(-65.3, 4.81) * mm});
            skLineSegment(sketch, "E4866", {"start": v(-65.3, 4.81) * mm, "end": v(-65.5, 4.57) * mm});
            skLineSegment(sketch, "E4867", {"start": v(-65.5, 4.57) * mm, "end": v(-65.7, 4.34) * mm});
            skLineSegment(sketch, "E4868", {"start": v(-65.7, 4.34) * mm, "end": v(-65.93, 4.11) * mm});
            skLineSegment(sketch, "E4869", {"start": v(-65.93, 4.11) * mm, "end": v(-66.18, 3.9) * mm});
            skLineSegment(sketch, "E4870", {"start": v(-66.18, 3.9) * mm, "end": v(-66.43, 3.68) * mm});
            skLineSegment(sketch, "E4871", {"start": v(-66.43, 3.68) * mm, "end": v(-66.7, 3.46) * mm});
            skLineSegment(sketch, "E4872", {"start": v(-66.7, 3.46) * mm, "end": v(-66.86, 3.35) * mm});
            skLineSegment(sketch, "E4873", {"start": v(-66.86, 3.35) * mm, "end": v(-67.02, 3.24) * mm});
            skLineSegment(sketch, "E4874", {"start": v(-67.02, 3.24) * mm, "end": v(-67.2, 3.12) * mm});
            skLineSegment(sketch, "E4875", {"start": v(-67.2, 3.12) * mm, "end": v(-67.38, 2.99) * mm});
            skLineSegment(sketch, "E4876", {"start": v(-67.38, 2.99) * mm, "end": v(-67.58, 2.85) * mm});
            skLineSegment(sketch, "E4877", {"start": v(-67.58, 2.85) * mm, "end": v(-67.8, 2.7) * mm});
            skLineSegment(sketch, "E4878", {"start": v(-67.8, 2.7) * mm, "end": v(-68.02, 2.55) * mm});
            skLineSegment(sketch, "E4879", {"start": v(-68.02, 2.55) * mm, "end": v(-68.26, 2.4) * mm});
            skLineSegment(sketch, "E4880", {"start": v(-68.26, 2.4) * mm, "end": v(-68.51, 2.23) * mm});
            skLineSegment(sketch, "E4881", {"start": v(-68.51, 2.23) * mm, "end": v(-68.78, 2.05) * mm});
            skLineSegment(sketch, "E4882", {"start": v(-68.78, 2.05) * mm, "end": v(-69.06, 1.87) * mm});
            skLineSegment(sketch, "E4883", {"start": v(-69.06, 1.87) * mm, "end": v(-69.66, 1.49) * mm});
            skLineSegment(sketch, "E4884", {"start": v(-69.66, 1.49) * mm, "end": v(-70.31, 1.08) * mm});
            skLineSegment(sketch, "E4885", {"start": v(-70.31, 1.08) * mm, "end": v(-70.66, 0.86) * mm});
            skLineSegment(sketch, "E4886", {"start": v(-70.66, 0.86) * mm, "end": v(-71.34, 0.43) * mm});
            skLineSegment(sketch, "E4887", {"start": v(-71.34, 0.43) * mm, "end": v(-71.98, 0.03) * mm});
            skLineSegment(sketch, "E4888", {"start": v(-71.98, 0.03) * mm, "end": v(-72.59, -0.35) * mm});
            skLineSegment(sketch, "E4889", {"start": v(-72.59, -0.35) * mm, "end": v(-73.15, -0.72) * mm});
            skLineSegment(sketch, "E4890", {"start": v(-73.15, -0.72) * mm, "end": v(-73.68, -1.06) * mm});
            skLineSegment(sketch, "E4891", {"start": v(-73.68, -1.06) * mm, "end": v(-74.16, -1.37) * mm});
            skLineSegment(sketch, "E4892", {"start": v(-74.16, -1.37) * mm, "end": v(-74.61, -1.67) * mm});
            skLineSegment(sketch, "E4893", {"start": v(-74.61, -1.67) * mm, "end": v(-74.82, -1.81) * mm});
            skLineSegment(sketch, "E4894", {"start": v(-74.82, -1.81) * mm, "end": v(-75.02, -1.94) * mm});
            skLineSegment(sketch, "E4895", {"start": v(-75.02, -1.94) * mm, "end": v(-75.03, -1.95) * mm});
            skLineSegment(sketch, "E4896", {"start": v(-75.03, -1.95) * mm, "end": v(-75.04, -1.96) * mm});
            skLineSegment(sketch, "E4897", {"start": v(-75.04, -1.96) * mm, "end": v(-75.05, -1.97) * mm});
            skLineSegment(sketch, "E4898", {"start": v(-75.05, -1.97) * mm, "end": v(-75.06, -1.97) * mm});
            skLineSegment(sketch, "E4899", {"start": v(-75.06, -1.97) * mm, "end": v(-75.08, -1.98) * mm});
            skLineSegment(sketch, "E4900", {"start": v(-75.08, -1.98) * mm, "end": v(-75.09, -1.99) * mm});
            skLineSegment(sketch, "E4901", {"start": v(-75.09, -1.99) * mm, "end": v(-75.1, -2) * mm});
            skLineSegment(sketch, "E4902", {"start": v(-75.1, -2) * mm, "end": v(-75.13, -2.02) * mm});
            skLineSegment(sketch, "E4903", {"start": v(-75.13, -2.02) * mm, "end": v(-75.16, -2.04) * mm});
            skLineSegment(sketch, "E4904", {"start": v(-75.16, -2.04) * mm, "end": v(-75.2, -2.06) * mm});
            skLineSegment(sketch, "E4905", {"start": v(-75.2, -2.06) * mm, "end": v(-75.23, -2.08) * mm});
            skLineSegment(sketch, "E4906", {"start": v(-75.23, -2.08) * mm, "end": v(-75.26, -2.1) * mm});
            skLineSegment(sketch, "E4907", {"start": v(-75.26, -2.1) * mm, "end": v(-75.3, -2.13) * mm});
            skLineSegment(sketch, "E4908", {"start": v(-75.3, -2.13) * mm, "end": v(-75.34, -2.16) * mm});
            skLineSegment(sketch, "E4909", {"start": v(-75.34, -2.16) * mm, "end": v(-75.39, -2.19) * mm});
            skLineSegment(sketch, "E4910", {"start": v(-75.39, -2.19) * mm, "end": v(-75.43, -2.22) * mm});
            skLineSegment(sketch, "E4911", {"start": v(-75.43, -2.22) * mm, "end": v(-75.48, -2.25) * mm});
            skLineSegment(sketch, "E4912", {"start": v(-75.48, -2.25) * mm, "end": v(-75.53, -2.28) * mm});
            skLineSegment(sketch, "E4913", {"start": v(-75.53, -2.28) * mm, "end": v(-75.62, -2.34) * mm});
            skLineSegment(sketch, "E4914", {"start": v(-75.62, -2.34) * mm, "end": v(-75.83, -2.47) * mm});
            skLineSegment(sketch, "E4915", {"start": v(-75.83, -2.47) * mm, "end": v(-76.04, -2.62) * mm});
            skLineSegment(sketch, "E4916", {"start": v(-76.04, -2.62) * mm, "end": v(-76.23, -2.76) * mm});
            skLineSegment(sketch, "E4917", {"start": v(-76.23, -2.76) * mm, "end": v(-76.41, -2.91) * mm});
            skLineSegment(sketch, "E4918", {"start": v(-76.41, -2.91) * mm, "end": v(-76.5, -3) * mm});
            skLineSegment(sketch, "E4919", {"start": v(-76.5, -3) * mm, "end": v(-76.59, -3.08) * mm});
            skLineSegment(sketch, "E4920", {"start": v(-76.59, -3.08) * mm, "end": v(-76.76, -3.26) * mm});
            skLineSegment(sketch, "E4921", {"start": v(-76.76, -3.26) * mm, "end": v(-76.94, -3.47) * mm});
            skLineSegment(sketch, "E4922", {"start": v(-76.94, -3.47) * mm, "end": v(-77.12, -3.7) * mm});
            skLineSegment(sketch, "E4923", {"start": v(-77.12, -3.7) * mm, "end": v(-76.87, -3.67) * mm});
            skLineSegment(sketch, "E4924", {"start": v(-76.87, -3.67) * mm, "end": v(-76.6, -3.64) * mm});
            skLineSegment(sketch, "E4925", {"start": v(-76.6, -3.64) * mm, "end": v(-76.31, -3.6) * mm});
            skLineSegment(sketch, "E4926", {"start": v(-76.31, -3.6) * mm, "end": v(-76.01, -3.56) * mm});
            skLineSegment(sketch, "E4927", {"start": v(-76.01, -3.56) * mm, "end": v(-75.69, -3.51) * mm});
            skLineSegment(sketch, "E4928", {"start": v(-75.69, -3.51) * mm, "end": v(-75.35, -3.46) * mm});
            skLineSegment(sketch, "E4929", {"start": v(-75.35, -3.46) * mm, "end": v(-75, -3.4) * mm});
            skLineSegment(sketch, "E4930", {"start": v(-75, -3.4) * mm, "end": v(-74.62, -3.34) * mm});
            skLineSegment(sketch, "E4931", {"start": v(-74.62, -3.34) * mm, "end": v(-74.23, -3.27) * mm});
            skLineSegment(sketch, "E4932", {"start": v(-74.23, -3.27) * mm, "end": v(-73.39, -3.11) * mm});
            skLineSegment(sketch, "E4933", {"start": v(-73.39, -3.11) * mm, "end": v(-72.48, -2.94) * mm});
            skLineSegment(sketch, "E4934", {"start": v(-72.48, -2.94) * mm, "end": v(-71.5, -2.74) * mm});
            skLineSegment(sketch, "E4935", {"start": v(-71.5, -2.74) * mm, "end": v(-70.99, -2.64) * mm});
            skLineSegment(sketch, "E4936", {"start": v(-70.99, -2.64) * mm, "end": v(-70.42, -2.51) * mm});
            skLineSegment(sketch, "E4937", {"start": v(-70.42, -2.51) * mm, "end": v(-69.32, -2.25) * mm});
            skLineSegment(sketch, "E4938", {"start": v(-69.32, -2.25) * mm, "end": v(-68.78, -2.1) * mm});
            skLineSegment(sketch, "E4939", {"start": v(-68.78, -2.1) * mm, "end": v(-68.64, -2.07) * mm});
            skLineSegment(sketch, "E4940", {"start": v(-68.64, -2.07) * mm, "end": v(-68.52, -2.03) * mm});
            skLineSegment(sketch, "E4941", {"start": v(-68.52, -2.03) * mm, "end": v(-68.4, -2) * mm});
            skLineSegment(sketch, "E4942", {"start": v(-68.4, -2) * mm, "end": v(-68.29, -1.97) * mm});
            skLineSegment(sketch, "E4943", {"start": v(-68.29, -1.97) * mm, "end": v(-68.18, -1.94) * mm});
            skLineSegment(sketch, "E4944", {"start": v(-68.18, -1.94) * mm, "end": v(-68.09, -1.92) * mm});
            skLineSegment(sketch, "E4945", {"start": v(-68.09, -1.92) * mm, "end": v(-68, -1.9) * mm});
            skLineSegment(sketch, "E4946", {"start": v(-68, -1.9) * mm, "end": v(-67.9, -1.88) * mm});
            skLineSegment(sketch, "E4947", {"start": v(-67.9, -1.88) * mm, "end": v(-67.87, -1.87) * mm});
            skLineSegment(sketch, "E4948", {"start": v(-67.87, -1.87) * mm, "end": v(-67.83, -1.86) * mm});
            skLineSegment(sketch, "E4949", {"start": v(-67.83, -1.86) * mm, "end": v(-67.8, -1.85) * mm});
            skLineSegment(sketch, "E4950", {"start": v(-67.8, -1.85) * mm, "end": v(-67.76, -1.84) * mm});
            skLineSegment(sketch, "E4951", {"start": v(-67.76, -1.84) * mm, "end": v(-67.73, -1.84) * mm});
            skLineSegment(sketch, "E4952", {"start": v(-67.73, -1.84) * mm, "end": v(-67.7, -1.83) * mm});
            skLineSegment(sketch, "E4953", {"start": v(-67.7, -1.83) * mm, "end": v(-67.67, -1.82) * mm});
            skLineSegment(sketch, "E4954", {"start": v(-67.67, -1.82) * mm, "end": v(-67.64, -1.82) * mm});
            skLineSegment(sketch, "E4955", {"start": v(-67.64, -1.82) * mm, "end": v(-67.61, -1.81) * mm});
            skLineSegment(sketch, "E4956", {"start": v(-67.61, -1.81) * mm, "end": v(-67.59, -1.81) * mm});
            skLineSegment(sketch, "E4957", {"start": v(-67.59, -1.81) * mm, "end": v(-67.56, -1.8) * mm});
            skLineSegment(sketch, "E4958", {"start": v(-67.56, -1.8) * mm, "end": v(-67.54, -1.8) * mm});
            skLineSegment(sketch, "E4959", {"start": v(-67.54, -1.8) * mm, "end": v(-67.53, -1.8) * mm});
            skLineSegment(sketch, "E4960", {"start": v(-67.53, -1.8) * mm, "end": v(-67.52, -1.8) * mm});
            skLineSegment(sketch, "E4961", {"start": v(-67.52, -1.8) * mm, "end": v(-67.51, -1.8) * mm});
            skLineSegment(sketch, "E4962", {"start": v(-67.51, -1.8) * mm, "end": v(-67.5, -1.8) * mm});
            skLineSegment(sketch, "E4963", {"start": v(-67.5, -1.8) * mm, "end": v(-67.5, -1.8) * mm});
            skLineSegment(sketch, "E4964", {"start": v(-67.5, -1.8) * mm, "end": v(-67.49, -1.8) * mm});
            skLineSegment(sketch, "E4965", {"start": v(-67.49, -1.8) * mm, "end": v(-67.48, -1.8) * mm});
            skLineSegment(sketch, "E4966", {"start": v(-67.48, -1.8) * mm, "end": v(-67.48, -1.8) * mm});
            skLineSegment(sketch, "E4967", {"start": v(-67.48, -1.8) * mm, "end": v(-67.45, -1.8) * mm});
            skLineSegment(sketch, "E4968", {"start": v(-67.45, -1.8) * mm, "end": v(-67.43, -1.8) * mm});
            skLineSegment(sketch, "E4969", {"start": v(-67.43, -1.8) * mm, "end": v(-67.41, -1.8) * mm});
            skLineSegment(sketch, "E4970", {"start": v(-67.41, -1.8) * mm, "end": v(-67.4, -1.8) * mm});
            skLineSegment(sketch, "E4971", {"start": v(-67.4, -1.8) * mm, "end": v(-67.37, -1.8) * mm});
            skLineSegment(sketch, "E4972", {"start": v(-67.37, -1.8) * mm, "end": v(-67.35, -1.81) * mm});
            skLineSegment(sketch, "E4973", {"start": v(-67.35, -1.81) * mm, "end": v(-67.33, -1.82) * mm});
            skLineSegment(sketch, "E4974", {"start": v(-67.33, -1.82) * mm, "end": v(-67.32, -1.82) * mm});
            skLineSegment(sketch, "E4975", {"start": v(-67.32, -1.82) * mm, "end": v(-67.3, -1.83) * mm});
            skLineSegment(sketch, "E4976", {"start": v(-67.3, -1.83) * mm, "end": v(-67.28, -1.84) * mm});
            skLineSegment(sketch, "E4977", {"start": v(-67.28, -1.84) * mm, "end": v(-67.27, -1.84) * mm});
            skLineSegment(sketch, "E4978", {"start": v(-67.27, -1.84) * mm, "end": v(-67.26, -1.85) * mm});
            skLineSegment(sketch, "E4979", {"start": v(-67.26, -1.85) * mm, "end": v(-67.24, -1.86) * mm});
            skLineSegment(sketch, "E4980", {"start": v(-67.24, -1.86) * mm, "end": v(-67.23, -1.87) * mm});
            skLineSegment(sketch, "E4981", {"start": v(-67.23, -1.87) * mm, "end": v(-67.22, -1.88) * mm});
            skLineSegment(sketch, "E4982", {"start": v(-67.22, -1.88) * mm, "end": v(-67.2, -1.9) * mm});
            skLineSegment(sketch, "E4983", {"start": v(-67.2, -1.9) * mm, "end": v(-67.2, -1.9) * mm});
            skLineSegment(sketch, "E4984", {"start": v(-67.2, -1.9) * mm, "end": v(-67.18, -1.91) * mm});
            skLineSegment(sketch, "E4985", {"start": v(-67.18, -1.91) * mm, "end": v(-67.17, -1.93) * mm});
            skLineSegment(sketch, "E4986", {"start": v(-67.17, -1.93) * mm, "end": v(-67.16, -1.94) * mm});
            skLineSegment(sketch, "E4987", {"start": v(-67.16, -1.94) * mm, "end": v(-67.16, -1.96) * mm});
            skLineSegment(sketch, "E4988", {"start": v(-67.16, -1.96) * mm, "end": v(-67.15, -1.97) * mm});
            skLineSegment(sketch, "E4989", {"start": v(-67.15, -1.97) * mm, "end": v(-67.14, -1.99) * mm});
            skLineSegment(sketch, "E4990", {"start": v(-67.14, -1.99) * mm, "end": v(-67.14, -2) * mm});
            skLineSegment(sketch, "E4991", {"start": v(-67.14, -2) * mm, "end": v(-67.13, -2.02) * mm});
            skLineSegment(sketch, "E4992", {"start": v(-67.13, -2.02) * mm, "end": v(-67.13, -2.04) * mm});
            skLineSegment(sketch, "E4993", {"start": v(-67.13, -2.04) * mm, "end": v(-67.12, -2.06) * mm});
            skLineSegment(sketch, "E4994", {"start": v(-67.12, -2.06) * mm, "end": v(-67.12, -2.08) * mm});
            skLineSegment(sketch, "E4995", {"start": v(-67.12, -2.08) * mm, "end": v(-67.12, -2.1) * mm});
            skLineSegment(sketch, "E4996", {"start": v(-67.12, -2.1) * mm, "end": v(-67.12, -2.12) * mm});
            skLineSegment(sketch, "E4997", {"start": v(-67.12, -2.12) * mm, "end": v(-67.11, -2.14) * mm});
            skLineSegment(sketch, "E4998", {"start": v(-67.11, -2.14) * mm, "end": v(-67.11, -2.16) * mm});
            skLineSegment(sketch, "E4999", {"start": v(-67.11, -2.16) * mm, "end": v(-67.12, -2.25) * mm});
            skLineSegment(sketch, "E5000", {"start": v(-67.12, -2.25) * mm, "end": v(-67.12, -2.34) * mm});
            skLineSegment(sketch, "E5001", {"start": v(-67.12, -2.34) * mm, "end": v(-67.14, -2.43) * mm});
            skLineSegment(sketch, "E5002", {"start": v(-67.14, -2.43) * mm, "end": v(-67.15, -2.53) * mm});
            skLineSegment(sketch, "E5003", {"start": v(-67.15, -2.53) * mm, "end": v(-67.18, -2.64) * mm});
            skLineSegment(sketch, "E5004", {"start": v(-67.18, -2.64) * mm, "end": v(-67.2, -2.75) * mm});
            skLineSegment(sketch, "E5005", {"start": v(-67.2, -2.75) * mm, "end": v(-67.24, -2.87) * mm});
            skLineSegment(sketch, "E5006", {"start": v(-67.24, -2.87) * mm, "end": v(-67.27, -2.99) * mm});
            skLineSegment(sketch, "E5007", {"start": v(-67.27, -2.99) * mm, "end": v(-67.35, -3.23) * mm});
            skLineSegment(sketch, "E5008", {"start": v(-67.35, -3.23) * mm, "end": v(-67.45, -3.47) * mm});
            skLineSegment(sketch, "E5009", {"start": v(-67.45, -3.47) * mm, "end": v(-67.57, -3.72) * mm});
            skLineSegment(sketch, "E5010", {"start": v(-67.57, -3.72) * mm, "end": v(-67.7, -3.97) * mm});
            skLineSegment(sketch, "E5011", {"start": v(-67.7, -3.97) * mm, "end": v(-67.86, -4.2) * mm});
            skLineSegment(sketch, "E5012", {"start": v(-67.86, -4.2) * mm, "end": v(-68.02, -4.43) * mm});
            skLineSegment(sketch, "E5013", {"start": v(-68.02, -4.43) * mm, "end": v(-68.2, -4.63) * mm});
            skLineSegment(sketch, "E5014", {"start": v(-68.2, -4.63) * mm, "end": v(-68.39, -4.82) * mm});
            skLineSegment(sketch, "E5015", {"start": v(-68.39, -4.82) * mm, "end": v(-68.5, -4.93) * mm});
            skLineSegment(sketch, "E5016", {"start": v(-68.5, -4.93) * mm, "end": v(-68.64, -5.04) * mm});
            skLineSegment(sketch, "E5017", {"start": v(-68.64, -5.04) * mm, "end": v(-68.78, -5.14) * mm});
            skLineSegment(sketch, "E5018", {"start": v(-68.78, -5.14) * mm, "end": v(-68.92, -5.24) * mm});
            skLineSegment(sketch, "E5019", {"start": v(-68.92, -5.24) * mm, "end": v(-69.23, -5.43) * mm});
            skLineSegment(sketch, "E5020", {"start": v(-69.23, -5.43) * mm, "end": v(-69.56, -5.6) * mm});
            skLineSegment(sketch, "E5021", {"start": v(-69.56, -5.6) * mm, "end": v(-69.93, -5.76) * mm});
            skLineSegment(sketch, "E5022", {"start": v(-69.93, -5.76) * mm, "end": v(-70.32, -5.9) * mm});
            skLineSegment(sketch, "E5023", {"start": v(-70.32, -5.9) * mm, "end": v(-70.74, -6.04) * mm});
            skLineSegment(sketch, "E5024", {"start": v(-70.74, -6.04) * mm, "end": v(-71.18, -6.16) * mm});
            skLineSegment(sketch, "E5025", {"start": v(-71.18, -6.16) * mm, "end": v(-71.66, -6.26) * mm});
            skLineSegment(sketch, "E5026", {"start": v(-71.66, -6.26) * mm, "end": v(-72.16, -6.35) * mm});
            skLineSegment(sketch, "E5027", {"start": v(-72.16, -6.35) * mm, "end": v(-72.7, -6.43) * mm});
            skLineSegment(sketch, "E5028", {"start": v(-72.7, -6.43) * mm, "end": v(-73.25, -6.49) * mm});
            skLineSegment(sketch, "E5029", {"start": v(-73.25, -6.49) * mm, "end": v(-73.84, -6.54) * mm});
            skLineSegment(sketch, "E5030", {"start": v(-73.84, -6.54) * mm, "end": v(-74.45, -6.57) * mm});
            skLineSegment(sketch, "E5031", {"start": v(-74.45, -6.57) * mm, "end": v(-75.1, -6.6) * mm});
            skLineSegment(sketch, "E5032", {"start": v(-75.1, -6.6) * mm, "end": v(-75.76, -6.6) * mm});
            skLineSegment(sketch, "E5033", {"start": v(-75.76, -6.6) * mm, "end": v(-75.93, -6.6) * mm});
            skLineSegment(sketch, "E5034", {"start": v(-75.93, -6.6) * mm, "end": v(-76.1, -6.6) * mm});
            skLineSegment(sketch, "E5035", {"start": v(-76.1, -6.6) * mm, "end": v(-76.26, -6.58) * mm});
            skLineSegment(sketch, "E5036", {"start": v(-76.26, -6.58) * mm, "end": v(-76.41, -6.57) * mm});
            skLineSegment(sketch, "E5037", {"start": v(-76.41, -6.57) * mm, "end": v(-76.55, -6.56) * mm});
            skLineSegment(sketch, "E5038", {"start": v(-76.55, -6.56) * mm, "end": v(-76.7, -6.54) * mm});
            skLineSegment(sketch, "E5039", {"start": v(-76.7, -6.54) * mm, "end": v(-76.82, -6.51) * mm});
            skLineSegment(sketch, "E5040", {"start": v(-76.82, -6.51) * mm, "end": v(-76.94, -6.49) * mm});
            skLineSegment(sketch, "E5041", {"start": v(-76.94, -6.49) * mm, "end": v(-77.06, -6.46) * mm});
            skLineSegment(sketch, "E5042", {"start": v(-77.06, -6.46) * mm, "end": v(-77.16, -6.43) * mm});
            skLineSegment(sketch, "E5043", {"start": v(-77.16, -6.43) * mm, "end": v(-77.26, -6.39) * mm});
            skLineSegment(sketch, "E5044", {"start": v(-77.26, -6.39) * mm, "end": v(-77.36, -6.35) * mm});
            skLineSegment(sketch, "E5045", {"start": v(-77.36, -6.35) * mm, "end": v(-77.44, -6.3) * mm});
            skLineSegment(sketch, "E5046", {"start": v(-77.44, -6.3) * mm, "end": v(-77.48, -6.28) * mm});
            skLineSegment(sketch, "E5047", {"start": v(-77.48, -6.28) * mm, "end": v(-77.52, -6.26) * mm});
            skLineSegment(sketch, "E5048", {"start": v(-77.52, -6.26) * mm, "end": v(-77.56, -6.23) * mm});
            skLineSegment(sketch, "E5049", {"start": v(-77.56, -6.23) * mm, "end": v(-77.6, -6.2) * mm});
            skLineSegment(sketch, "E5050", {"start": v(-77.6, -6.2) * mm, "end": v(-77.62, -6.18) * mm});
            skLineSegment(sketch, "E5051", {"start": v(-77.62, -6.18) * mm, "end": v(-77.65, -6.15) * mm});
            skLineSegment(sketch, "E5052", {"start": v(-77.65, -6.15) * mm, "end": v(-77.67, -6.14) * mm});
            skLineSegment(sketch, "E5053", {"start": v(-77.67, -6.14) * mm, "end": v(-77.7, -6.12) * mm});
            skLineSegment(sketch, "E5054", {"start": v(-77.7, -6.12) * mm, "end": v(-77.7, -6.1) * mm});
            skLineSegment(sketch, "E5055", {"start": v(-77.7, -6.1) * mm, "end": v(-77.73, -6.08) * mm});
            skLineSegment(sketch, "E5056", {"start": v(-77.73, -6.08) * mm, "end": v(-77.75, -6.06) * mm});
            skLineSegment(sketch, "E5057", {"start": v(-77.75, -6.06) * mm, "end": v(-77.78, -6) * mm});
            skLineSegment(sketch, "E5058", {"start": v(-77.78, -6) * mm, "end": v(-77.82, -5.95) * mm});
            skLineSegment(sketch, "E5059", {"start": v(-77.82, -5.95) * mm, "end": v(-77.86, -5.9) * mm});
            skLineSegment(sketch, "E5060", {"start": v(-77.86, -5.9) * mm, "end": v(-77.9, -5.83) * mm});
            skLineSegment(sketch, "E5061", {"start": v(-77.9, -5.83) * mm, "end": v(-77.93, -5.77) * mm});
            skLineSegment(sketch, "E5062", {"start": v(-77.93, -5.77) * mm, "end": v(-77.97, -5.7) * mm});
            skLineSegment(sketch, "E5063", {"start": v(-77.97, -5.7) * mm, "end": v(-78, -5.61) * mm});
            skLineSegment(sketch, "E5064", {"start": v(-78, -5.61) * mm, "end": v(-78.05, -5.53) * mm});
            skLineSegment(sketch, "E5065", {"start": v(-78.05, -5.53) * mm, "end": v(-78.09, -5.44) * mm});
            skLineSegment(sketch, "E5066", {"start": v(-78.09, -5.44) * mm, "end": v(-78.12, -5.35) * mm});
            skLineSegment(sketch, "E5067", {"start": v(-78.12, -5.35) * mm, "end": v(-78.16, -5.25) * mm});
            skLineSegment(sketch, "E5068", {"start": v(-78.16, -5.25) * mm, "end": v(-78.2, -5.15) * mm});
            skLineSegment(sketch, "E5069", {"start": v(-78.2, -5.15) * mm, "end": v(-78.26, -4.98) * mm});
            skLineSegment(sketch, "E5070", {"start": v(-78.26, -4.98) * mm, "end": v(-78.34, -4.76) * mm});
            skLineSegment(sketch, "E5071", {"start": v(-78.34, -4.76) * mm, "end": v(-78.4, -4.56) * mm});
            skLineSegment(sketch, "E5072", {"start": v(-78.4, -4.56) * mm, "end": v(-78.43, -4.46) * mm});
            skLineSegment(sketch, "E5073", {"start": v(-78.43, -4.46) * mm, "end": v(-78.46, -4.37) * mm});
            skLineSegment(sketch, "E5074", {"start": v(-78.46, -4.37) * mm, "end": v(-78.48, -4.28) * mm});
            skLineSegment(sketch, "E5075", {"start": v(-78.48, -4.28) * mm, "end": v(-78.5, -4.19) * mm});
            skLineSegment(sketch, "E5076", {"start": v(-78.5, -4.19) * mm, "end": v(-78.52, -4.1) * mm});
            skLineSegment(sketch, "E5077", {"start": v(-78.52, -4.1) * mm, "end": v(-78.54, -4.03) * mm});
            skLineSegment(sketch, "E5078", {"start": v(-78.54, -4.03) * mm, "end": v(-78.55, -3.95) * mm});
            skLineSegment(sketch, "E5079", {"start": v(-78.55, -3.95) * mm, "end": v(-78.56, -3.88) * mm});
            skLineSegment(sketch, "E5080", {"start": v(-78.56, -3.88) * mm, "end": v(-78.57, -3.82) * mm});
            skLineSegment(sketch, "E5081", {"start": v(-78.57, -3.82) * mm, "end": v(-78.58, -3.75) * mm});
            skLineSegment(sketch, "E5082", {"start": v(-78.58, -3.75) * mm, "end": v(-78.58, -3.7) * mm});
            skLineSegment(sketch, "E5083", {"start": v(-78.58, -3.7) * mm, "end": v(-78.58, -3.64) * mm});
            skLineSegment(sketch, "E5084", {"start": v(-78.58, -3.64) * mm, "end": v(-78.58, -3.54) * mm});
            skLineSegment(sketch, "E5085", {"start": v(-78.58, -3.54) * mm, "end": v(-78.57, -3.44) * mm});
            skLineSegment(sketch, "E5086", {"start": v(-78.57, -3.44) * mm, "end": v(-78.55, -3.34) * mm});
            skLineSegment(sketch, "E5087", {"start": v(-78.55, -3.34) * mm, "end": v(-78.53, -3.24) * mm});
            skLineSegment(sketch, "E5088", {"start": v(-78.53, -3.24) * mm, "end": v(-78.5, -3.13) * mm});
            skLineSegment(sketch, "E5089", {"start": v(-78.5, -3.13) * mm, "end": v(-78.48, -3.03) * mm});
            skLineSegment(sketch, "E5090", {"start": v(-78.48, -3.03) * mm, "end": v(-78.44, -2.92) * mm});
            skLineSegment(sketch, "E5091", {"start": v(-78.44, -2.92) * mm, "end": v(-78.4, -2.8) * mm});
            skLineSegment(sketch, "E5092", {"start": v(-78.4, -2.8) * mm, "end": v(-78.35, -2.69) * mm});
            skLineSegment(sketch, "E5093", {"start": v(-78.35, -2.69) * mm, "end": v(-78.3, -2.57) * mm});
            skLineSegment(sketch, "E5094", {"start": v(-78.3, -2.57) * mm, "end": v(-78.23, -2.45) * mm});
            skLineSegment(sketch, "E5095", {"start": v(-78.23, -2.45) * mm, "end": v(-78.17, -2.32) * mm});
            skLineSegment(sketch, "E5096", {"start": v(-78.17, -2.32) * mm, "end": v(-78.02, -2.07) * mm});
            skLineSegment(sketch, "E5097", {"start": v(-78.02, -2.07) * mm, "end": v(-77.84, -1.8) * mm});
            skLineSegment(sketch, "E5098", {"start": v(-77.84, -1.8) * mm, "end": v(-77.65, -1.52) * mm});
            skLineSegment(sketch, "E5099", {"start": v(-77.65, -1.52) * mm, "end": v(-77.44, -1.25) * mm});
            skLineSegment(sketch, "E5100", {"start": v(-77.44, -1.25) * mm, "end": v(-77.21, -0.97) * mm});
            skLineSegment(sketch, "E5101", {"start": v(-77.21, -0.97) * mm, "end": v(-76.97, -0.7) * mm});
            skLineSegment(sketch, "E5102", {"start": v(-76.97, -0.7) * mm, "end": v(-76.7, -0.4) * mm});
            skLineSegment(sketch, "E5103", {"start": v(-76.7, -0.4) * mm, "end": v(-76.13, 0.16) * mm});
            skLineSegment(sketch, "E5104", {"start": v(-76.13, 0.16) * mm, "end": v(-75.82, 0.44) * mm});
            skLineSegment(sketch, "E5105", {"start": v(-75.82, 0.44) * mm, "end": v(-75.16, 1) * mm});
            skLineSegment(sketch, "E5106", {"start": v(-75.16, 1) * mm, "end": v(-74.47, 1.53) * mm});
            skLineSegment(sketch, "E5107", {"start": v(-74.47, 1.53) * mm, "end": v(-73.74, 2.03) * mm});
            skLineSegment(sketch, "E5108", {"start": v(-73.74, 2.03) * mm, "end": v(-72.98, 2.5) * mm});
            skLineSegment(sketch, "E5109", {"start": v(-72.98, 2.5) * mm, "end": v(-72.41, 2.82) * mm});
            skLineSegment(sketch, "E5110", {"start": v(-72.41, 2.82) * mm, "end": v(-71.88, 3.13) * mm});
            skLineSegment(sketch, "E5111", {"start": v(-71.88, 3.13) * mm, "end": v(-71.37, 3.42) * mm});
            skLineSegment(sketch, "E5112", {"start": v(-71.37, 3.42) * mm, "end": v(-70.9, 3.68) * mm});
            skLineSegment(sketch, "E5113", {"start": v(-70.9, 3.68) * mm, "end": v(-70.47, 3.93) * mm});
            skLineSegment(sketch, "E5114", {"start": v(-70.47, 3.93) * mm, "end": v(-70.07, 4.16) * mm});
            skLineSegment(sketch, "E5115", {"start": v(-70.07, 4.16) * mm, "end": v(-69.88, 4.27) * mm});
            skLineSegment(sketch, "E5116", {"start": v(-69.88, 4.27) * mm, "end": v(-69.7, 4.37) * mm});
            skLineSegment(sketch, "E5117", {"start": v(-69.7, 4.37) * mm, "end": v(-69.54, 4.47) * mm});
            skLineSegment(sketch, "E5118", {"start": v(-69.54, 4.47) * mm, "end": v(-69.38, 4.56) * mm});
            skLineSegment(sketch, "E5119", {"start": v(-69.38, 4.56) * mm, "end": v(-69.22, 4.65) * mm});
            skLineSegment(sketch, "E5120", {"start": v(-69.22, 4.65) * mm, "end": v(-69.08, 4.73) * mm});
            skLineSegment(sketch, "E5121", {"start": v(-69.08, 4.73) * mm, "end": v(-68.95, 4.81) * mm});
            skLineSegment(sketch, "E5122", {"start": v(-68.95, 4.81) * mm, "end": v(-68.82, 4.88) * mm});
            skLineSegment(sketch, "E5123", {"start": v(-68.82, 4.88) * mm, "end": v(-68.7, 4.95) * mm});
            skLineSegment(sketch, "E5124", {"start": v(-68.7, 4.95) * mm, "end": v(-68.6, 5.02) * mm});
            skLineSegment(sketch, "E5125", {"start": v(-68.6, 5.02) * mm, "end": v(-68.5, 5.08) * mm});
            skLineSegment(sketch, "E5126", {"start": v(-68.5, 5.08) * mm, "end": v(-68.45, 5.1) * mm});
            skLineSegment(sketch, "E5127", {"start": v(-68.45, 5.1) * mm, "end": v(-68.4, 5.13) * mm});
            skLineSegment(sketch, "E5128", {"start": v(-68.4, 5.13) * mm, "end": v(-68.36, 5.15) * mm});
            skLineSegment(sketch, "E5129", {"start": v(-68.36, 5.15) * mm, "end": v(-68.32, 5.18) * mm});
            skLineSegment(sketch, "E5130", {"start": v(-68.32, 5.18) * mm, "end": v(-68.28, 5.2) * mm});
            skLineSegment(sketch, "E5131", {"start": v(-68.28, 5.2) * mm, "end": v(-68.25, 5.22) * mm});
            skLineSegment(sketch, "E5132", {"start": v(-68.25, 5.22) * mm, "end": v(-68.21, 5.24) * mm});
            skLineSegment(sketch, "E5133", {"start": v(-68.21, 5.24) * mm, "end": v(-68.18, 5.26) * mm});
            skLineSegment(sketch, "E5134", {"start": v(-68.18, 5.26) * mm, "end": v(-68.15, 5.28) * mm});
            skLineSegment(sketch, "E5135", {"start": v(-68.15, 5.28) * mm, "end": v(-68.12, 5.3) * mm});
            skLineSegment(sketch, "E5136", {"start": v(-68.12, 5.3) * mm, "end": v(-68.1, 5.31) * mm});
            skLineSegment(sketch, "E5137", {"start": v(-68.1, 5.31) * mm, "end": v(-68.09, 5.32) * mm});
            skLineSegment(sketch, "E5138", {"start": v(-68.09, 5.32) * mm, "end": v(-68.07, 5.33) * mm});
            skLineSegment(sketch, "E5139", {"start": v(-68.07, 5.33) * mm, "end": v(-68.06, 5.33) * mm});
            skLineSegment(sketch, "E5140", {"start": v(-68.06, 5.33) * mm, "end": v(-68.05, 5.34) * mm});
            skLineSegment(sketch, "E5141", {"start": v(-68.05, 5.34) * mm, "end": v(-68.04, 5.35) * mm});
            skLineSegment(sketch, "E5142", {"start": v(-68.04, 5.35) * mm, "end": v(-68.03, 5.35) * mm});
            skLineSegment(sketch, "E5143", {"start": v(-68.03, 5.35) * mm, "end": v(-68.03, 5.36) * mm});
            skLineSegment(sketch, "E5144", {"start": v(-68.03, 5.36) * mm, "end": v(-68.02, 5.36) * mm});
            skLineSegment(sketch, "E5145", {"start": v(-68.02, 5.36) * mm, "end": v(-68.01, 5.37) * mm});
            skLineSegment(sketch, "E5146", {"start": v(-68.01, 5.37) * mm, "end": v(-68, 5.37) * mm});
            skLineSegment(sketch, "E5147", {"start": v(-68, 5.37) * mm, "end": v(-68, 5.38) * mm});
            skLineSegment(sketch, "E5148", {"start": v(-68, 5.38) * mm, "end": v(-68, 5.38) * mm});
            skLineSegment(sketch, "E5149", {"start": v(-68, 5.38) * mm, "end": v(-67.99, 5.38) * mm});
            skLineSegment(sketch, "E5150", {"start": v(-67.99, 5.38) * mm, "end": v(-67.99, 5.38) * mm});
            skLineSegment(sketch, "E5151", {"start": v(-67.99, 5.38) * mm, "end": v(-67.98, 5.38) * mm});
            skLineSegment(sketch, "E5152", {"start": v(-67.98, 5.38) * mm, "end": v(-67.98, 5.39) * mm});
            skLineSegment(sketch, "E5153", {"start": v(-67.98, 5.39) * mm, "end": v(-67.72, 5.57) * mm});
            skLineSegment(sketch, "E5154", {"start": v(-67.72, 5.57) * mm, "end": v(-67.48, 5.75) * mm});
            skLineSegment(sketch, "E5155", {"start": v(-67.48, 5.75) * mm, "end": v(-67.25, 5.93) * mm});
            skLineSegment(sketch, "E5156", {"start": v(-67.25, 5.93) * mm, "end": v(-67.04, 6.11) * mm});
            skLineSegment(sketch, "E5157", {"start": v(-67.04, 6.11) * mm, "end": v(-66.84, 6.3) * mm});
            skLineSegment(sketch, "E5158", {"start": v(-66.84, 6.3) * mm, "end": v(-66.66, 6.48) * mm});
            skLineSegment(sketch, "E5159", {"start": v(-66.66, 6.48) * mm, "end": v(-66.49, 6.66) * mm});
            skLineSegment(sketch, "E5160", {"start": v(-66.49, 6.66) * mm, "end": v(-66.33, 6.85) * mm});
            skLineSegment(sketch, "E5161", {"start": v(-66.33, 6.85) * mm, "end": v(-66.26, 6.94) * mm});
            skLineSegment(sketch, "E5162", {"start": v(-66.26, 6.94) * mm, "end": v(-66.2, 7.03) * mm});
            skLineSegment(sketch, "E5163", {"start": v(-66.2, 7.03) * mm, "end": v(-66.13, 7.11) * mm});
            skLineSegment(sketch, "E5164", {"start": v(-66.13, 7.11) * mm, "end": v(-66.07, 7.2) * mm});
            skLineSegment(sketch, "E5165", {"start": v(-66.07, 7.2) * mm, "end": v(-66.01, 7.28) * mm});
            skLineSegment(sketch, "E5166", {"start": v(-66.01, 7.28) * mm, "end": v(-65.96, 7.36) * mm});
            skLineSegment(sketch, "E5167", {"start": v(-65.96, 7.36) * mm, "end": v(-65.92, 7.44) * mm});
            skLineSegment(sketch, "E5168", {"start": v(-65.92, 7.44) * mm, "end": v(-65.88, 7.51) * mm});
            skLineSegment(sketch, "E5169", {"start": v(-65.88, 7.51) * mm, "end": v(-65.84, 7.58) * mm});
            skLineSegment(sketch, "E5170", {"start": v(-65.84, 7.58) * mm, "end": v(-65.81, 7.66) * mm});
            skLineSegment(sketch, "E5171", {"start": v(-65.81, 7.66) * mm, "end": v(-65.79, 7.72) * mm});
            skLineSegment(sketch, "E5172", {"start": v(-65.79, 7.72) * mm, "end": v(-65.76, 7.79) * mm});
            skLineSegment(sketch, "E5173", {"start": v(-65.76, 7.79) * mm, "end": v(-65.75, 7.85) * mm});
            skLineSegment(sketch, "E5174", {"start": v(-65.75, 7.85) * mm, "end": v(-65.74, 7.92) * mm});
            skLineSegment(sketch, "E5175", {"start": v(-65.74, 7.92) * mm, "end": v(-65.73, 7.95) * mm});
            skLineSegment(sketch, "E5176", {"start": v(-65.73, 7.95) * mm, "end": v(-65.73, 7.97) * mm});
            skLineSegment(sketch, "E5177", {"start": v(-65.73, 7.97) * mm, "end": v(-65.73, 8) * mm});
            skLineSegment(sketch, "E5178", {"start": v(-65.73, 8) * mm, "end": v(-65.73, 8.03) * mm});
            skLineSegment(sketch, "E5179", {"start": v(-65.73, 8.03) * mm, "end": v(-65.73, 8.08) * mm});
            skLineSegment(sketch, "E5180", {"start": v(-65.73, 8.08) * mm, "end": v(-65.73, 8.13) * mm});
            skLineSegment(sketch, "E5181", {"start": v(-65.73, 8.13) * mm, "end": v(-65.74, 8.18) * mm});
            skLineSegment(sketch, "E5182", {"start": v(-65.74, 8.18) * mm, "end": v(-65.75, 8.22) * mm});
            skLineSegment(sketch, "E5183", {"start": v(-65.75, 8.22) * mm, "end": v(-65.76, 8.27) * mm});
            skLineSegment(sketch, "E5184", {"start": v(-65.76, 8.27) * mm, "end": v(-65.77, 8.3) * mm});
            skLineSegment(sketch, "E5185", {"start": v(-65.77, 8.3) * mm, "end": v(-65.79, 8.35) * mm});
            skLineSegment(sketch, "E5186", {"start": v(-65.79, 8.35) * mm, "end": v(-65.8, 8.39) * mm});
            skLineSegment(sketch, "E5187", {"start": v(-65.8, 8.39) * mm, "end": v(-65.83, 8.43) * mm});
            skLineSegment(sketch, "E5188", {"start": v(-65.83, 8.43) * mm, "end": v(-65.86, 8.46) * mm});
            skLineSegment(sketch, "E5189", {"start": v(-65.86, 8.46) * mm, "end": v(-65.88, 8.5) * mm});
            skLineSegment(sketch, "E5190", {"start": v(-65.88, 8.5) * mm, "end": v(-65.91, 8.53) * mm});
            skLineSegment(sketch, "E5191", {"start": v(-65.91, 8.53) * mm, "end": v(-65.95, 8.57) * mm});
            skLineSegment(sketch, "E5192", {"start": v(-65.95, 8.57) * mm, "end": v(-65.98, 8.6) * mm});
            skLineSegment(sketch, "E5193", {"start": v(-65.98, 8.6) * mm, "end": v(-66.02, 8.63) * mm});
            skLineSegment(sketch, "E5194", {"start": v(-66.02, 8.63) * mm, "end": v(-66.06, 8.65) * mm});
            skLineSegment(sketch, "E5195", {"start": v(-66.06, 8.65) * mm, "end": v(-66.1, 8.68) * mm});
            skLineSegment(sketch, "E5196", {"start": v(-66.1, 8.68) * mm, "end": v(-66.14, 8.7) * mm});
            skLineSegment(sketch, "E5197", {"start": v(-66.14, 8.7) * mm, "end": v(-66.19, 8.73) * mm});
            skLineSegment(sketch, "E5198", {"start": v(-66.19, 8.73) * mm, "end": v(-66.23, 8.76) * mm});
            skLineSegment(sketch, "E5199", {"start": v(-66.23, 8.76) * mm, "end": v(-66.28, 8.78) * mm});
            skLineSegment(sketch, "E5200", {"start": v(-66.28, 8.78) * mm, "end": v(-66.34, 8.8) * mm});
            skLineSegment(sketch, "E5201", {"start": v(-66.34, 8.8) * mm, "end": v(-66.39, 8.81) * mm});
            skLineSegment(sketch, "E5202", {"start": v(-66.39, 8.81) * mm, "end": v(-66.45, 8.83) * mm});
            skLineSegment(sketch, "E5203", {"start": v(-66.45, 8.83) * mm, "end": v(-66.5, 8.84) * mm});
            skLineSegment(sketch, "E5204", {"start": v(-66.5, 8.84) * mm, "end": v(-66.56, 8.85) * mm});
            skLineSegment(sketch, "E5205", {"start": v(-66.56, 8.85) * mm, "end": v(-66.63, 8.86) * mm});
            skLineSegment(sketch, "E5206", {"start": v(-66.63, 8.86) * mm, "end": v(-66.76, 8.88) * mm});
            skLineSegment(sketch, "E5207", {"start": v(-66.76, 8.88) * mm, "end": v(-66.9, 8.88) * mm});
            skLineSegment(sketch, "E5208", {"start": v(-66.9, 8.88) * mm, "end": v(-66.97, 8.89) * mm});
            skLineSegment(sketch, "E5209", {"start": v(-66.97, 8.89) * mm, "end": v(-67.21, 8.88) * mm});
            skLineSegment(sketch, "E5210", {"start": v(-67.21, 8.88) * mm, "end": v(-67.46, 8.86) * mm});
            skLineSegment(sketch, "E5211", {"start": v(-67.46, 8.86) * mm, "end": v(-67.73, 8.84) * mm});
            skLineSegment(sketch, "E5212", {"start": v(-67.73, 8.84) * mm, "end": v(-68, 8.8) * mm});
            skLineSegment(sketch, "E5213", {"start": v(-68, 8.8) * mm, "end": v(-68.3, 8.75) * mm});
            skLineSegment(sketch, "E5214", {"start": v(-68.3, 8.75) * mm, "end": v(-68.6, 8.7) * mm});
            skLineSegment(sketch, "E5215", {"start": v(-68.6, 8.7) * mm, "end": v(-68.91, 8.62) * mm});
            skLineSegment(sketch, "E5216", {"start": v(-68.91, 8.62) * mm, "end": v(-69.24, 8.54) * mm});
            skLineSegment(sketch, "E5217", {"start": v(-69.24, 8.54) * mm, "end": v(-69.9, 8.35) * mm});
            skLineSegment(sketch, "E5218", {"start": v(-69.9, 8.35) * mm, "end": v(-70.57, 8.13) * mm});
            skLineSegment(sketch, "E5219", {"start": v(-70.57, 8.13) * mm, "end": v(-71.24, 7.86) * mm});
            skLineSegment(sketch, "E5220", {"start": v(-71.24, 7.86) * mm, "end": v(-71.91, 7.55) * mm});
            skLineSegment(sketch, "E5221", {"start": v(-71.91, 7.55) * mm, "end": v(-72.56, 7.22) * mm});
            skLineSegment(sketch, "E5222", {"start": v(-72.56, 7.22) * mm, "end": v(-73.17, 6.87) * mm});
            skLineSegment(sketch, "E5223", {"start": v(-73.17, 6.87) * mm, "end": v(-73.72, 6.49) * mm});
            skLineSegment(sketch, "E5224", {"start": v(-73.72, 6.49) * mm, "end": v(-74.23, 6.08) * mm});
            skLineSegment(sketch, "E5225", {"start": v(-59.94, 7.2) * mm, "end": v(-59.94, 8.38) * mm});
            skLineSegment(sketch, "E5226", {"start": v(-59.94, 8.38) * mm, "end": v(-59.68, 8.6) * mm});
            skLineSegment(sketch, "E5227", {"start": v(-59.68, 8.6) * mm, "end": v(-59.15, 9.06) * mm});
            skLineSegment(sketch, "E5228", {"start": v(-59.15, 9.06) * mm, "end": v(-58.89, 9.28) * mm});
            skLineSegment(sketch, "E5229", {"start": v(-58.89, 9.28) * mm, "end": v(-58.61, 9.5) * mm});
            skLineSegment(sketch, "E5230", {"start": v(-58.61, 9.5) * mm, "end": v(-58.32, 9.73) * mm});
            skLineSegment(sketch, "E5231", {"start": v(-58.32, 9.73) * mm, "end": v(-57.7, 10.22) * mm});
            skLineSegment(sketch, "E5232", {"start": v(-57.7, 10.22) * mm, "end": v(-57.37, 10.47) * mm});
            skLineSegment(sketch, "E5233", {"start": v(-57.37, 10.47) * mm, "end": v(-56.69, 10.95) * mm});
            skLineSegment(sketch, "E5234", {"start": v(-56.69, 10.95) * mm, "end": v(-56.34, 11.18) * mm});
            skLineSegment(sketch, "E5235", {"start": v(-56.34, 11.18) * mm, "end": v(-55.98, 11.42) * mm});
            skLineSegment(sketch, "E5236", {"start": v(-55.98, 11.42) * mm, "end": v(-55.59, 11.65) * mm});
            skLineSegment(sketch, "E5237", {"start": v(-55.59, 11.65) * mm, "end": v(-55.17, 11.9) * mm});
            skLineSegment(sketch, "E5238", {"start": v(-55.17, 11.9) * mm, "end": v(-54.74, 12.14) * mm});
            skLineSegment(sketch, "E5239", {"start": v(-54.74, 12.14) * mm, "end": v(-54.55, 11.85) * mm});
            skLineSegment(sketch, "E5240", {"start": v(-54.55, 11.85) * mm, "end": v(-54.39, 11.57) * mm});
            skLineSegment(sketch, "E5241", {"start": v(-54.39, 11.57) * mm, "end": v(-54.25, 11.29) * mm});
            skLineSegment(sketch, "E5242", {"start": v(-54.25, 11.29) * mm, "end": v(-54.14, 11) * mm});
            skLineSegment(sketch, "E5243", {"start": v(-54.14, 11) * mm, "end": v(-54.05, 10.73) * mm});
            skLineSegment(sketch, "E5244", {"start": v(-54.05, 10.73) * mm, "end": v(-54.02, 10.6) * mm});
            skLineSegment(sketch, "E5245", {"start": v(-54.02, 10.6) * mm, "end": v(-54, 10.46) * mm});
            skLineSegment(sketch, "E5246", {"start": v(-54, 10.46) * mm, "end": v(-53.97, 10.33) * mm});
            skLineSegment(sketch, "E5247", {"start": v(-53.97, 10.33) * mm, "end": v(-53.95, 10.2) * mm});
            skLineSegment(sketch, "E5248", {"start": v(-53.95, 10.2) * mm, "end": v(-53.95, 10.06) * mm});
            skLineSegment(sketch, "E5249", {"start": v(-53.95, 10.06) * mm, "end": v(-53.94, 9.93) * mm});
            skLineSegment(sketch, "E5250", {"start": v(-53.94, 9.93) * mm, "end": v(-53.95, 9.78) * mm});
            skLineSegment(sketch, "E5251", {"start": v(-53.95, 9.78) * mm, "end": v(-53.96, 9.63) * mm});
            skLineSegment(sketch, "E5252", {"start": v(-53.96, 9.63) * mm, "end": v(-53.98, 9.47) * mm});
            skLineSegment(sketch, "E5253", {"start": v(-53.98, 9.47) * mm, "end": v(-54, 9.32) * mm});
            skLineSegment(sketch, "E5254", {"start": v(-54, 9.32) * mm, "end": v(-54.04, 9.15) * mm});
            skLineSegment(sketch, "E5255", {"start": v(-54.04, 9.15) * mm, "end": v(-54.08, 8.99) * mm});
            skLineSegment(sketch, "E5256", {"start": v(-54.08, 8.99) * mm, "end": v(-54.13, 8.81) * mm});
            skLineSegment(sketch, "E5257", {"start": v(-54.13, 8.81) * mm, "end": v(-54.19, 8.64) * mm});
            skLineSegment(sketch, "E5258", {"start": v(-54.19, 8.64) * mm, "end": v(-54.25, 8.46) * mm});
            skLineSegment(sketch, "E5259", {"start": v(-54.25, 8.46) * mm, "end": v(-54.4, 8.08) * mm});
            skLineSegment(sketch, "E5260", {"start": v(-54.4, 8.08) * mm, "end": v(-54.57, 7.67) * mm});
            skLineSegment(sketch, "E5261", {"start": v(-54.57, 7.67) * mm, "end": v(-54.76, 7.24) * mm});
            skLineSegment(sketch, "E5262", {"start": v(-54.76, 7.24) * mm, "end": v(-54.87, 7.02) * mm});
            skLineSegment(sketch, "E5263", {"start": v(-54.87, 7.02) * mm, "end": v(-54.98, 6.78) * mm});
            skLineSegment(sketch, "E5264", {"start": v(-54.98, 6.78) * mm, "end": v(-55.1, 6.54) * mm});
            skLineSegment(sketch, "E5265", {"start": v(-55.1, 6.54) * mm, "end": v(-55.21, 6.27) * mm});
            skLineSegment(sketch, "E5266", {"start": v(-55.21, 6.27) * mm, "end": v(-55.34, 6) * mm});
            skLineSegment(sketch, "E5267", {"start": v(-55.34, 6) * mm, "end": v(-55.48, 5.7) * mm});
            skLineSegment(sketch, "E5268", {"start": v(-55.48, 5.7) * mm, "end": v(-55.62, 5.4) * mm});
            skLineSegment(sketch, "E5269", {"start": v(-55.62, 5.4) * mm, "end": v(-55.77, 5.07) * mm});
            skLineSegment(sketch, "E5270", {"start": v(-55.77, 5.07) * mm, "end": v(-55.92, 4.74) * mm});
            skLineSegment(sketch, "E5271", {"start": v(-55.92, 4.74) * mm, "end": v(-56.34, 3.81) * mm});
            skLineSegment(sketch, "E5272", {"start": v(-56.34, 3.81) * mm, "end": v(-56.72, 2.93) * mm});
            skLineSegment(sketch, "E5273", {"start": v(-56.72, 2.93) * mm, "end": v(-57.08, 2.09) * mm});
            skLineSegment(sketch, "E5274", {"start": v(-57.08, 2.09) * mm, "end": v(-57.42, 1.3) * mm});
            skLineSegment(sketch, "E5275", {"start": v(-57.42, 1.3) * mm, "end": v(-57.72, 0.53) * mm});
            skLineSegment(sketch, "E5276", {"start": v(-57.72, 0.53) * mm, "end": v(-58, -0.19) * mm});
            skLineSegment(sketch, "E5277", {"start": v(-58, -0.19) * mm, "end": v(-58.26, -0.86) * mm});
            skLineSegment(sketch, "E5278", {"start": v(-58.26, -0.86) * mm, "end": v(-58.48, -1.5) * mm});
            skLineSegment(sketch, "E5279", {"start": v(-58.48, -1.5) * mm, "end": v(-58.58, -1.8) * mm});
            skLineSegment(sketch, "E5280", {"start": v(-58.58, -1.8) * mm, "end": v(-58.68, -2.08) * mm});
            skLineSegment(sketch, "E5281", {"start": v(-58.68, -2.08) * mm, "end": v(-58.77, -2.36) * mm});
            skLineSegment(sketch, "E5282", {"start": v(-58.77, -2.36) * mm, "end": v(-58.85, -2.62) * mm});
            skLineSegment(sketch, "E5283", {"start": v(-58.85, -2.62) * mm, "end": v(-58.92, -2.87) * mm});
            skLineSegment(sketch, "E5284", {"start": v(-58.92, -2.87) * mm, "end": v(-59, -3.1) * mm});
            skLineSegment(sketch, "E5285", {"start": v(-59, -3.1) * mm, "end": v(-59.06, -3.34) * mm});
            skLineSegment(sketch, "E5286", {"start": v(-59.06, -3.34) * mm, "end": v(-59.11, -3.55) * mm});
            skLineSegment(sketch, "E5287", {"start": v(-59.11, -3.55) * mm, "end": v(-59.16, -3.75) * mm});
            skLineSegment(sketch, "E5288", {"start": v(-59.16, -3.75) * mm, "end": v(-59.2, -3.94) * mm});
            skLineSegment(sketch, "E5289", {"start": v(-59.2, -3.94) * mm, "end": v(-59.24, -4.12) * mm});
            skLineSegment(sketch, "E5290", {"start": v(-59.24, -4.12) * mm, "end": v(-59.27, -4.28) * mm});
            skLineSegment(sketch, "E5291", {"start": v(-59.27, -4.28) * mm, "end": v(-59.28, -4.36) * mm});
            skLineSegment(sketch, "E5292", {"start": v(-59.28, -4.36) * mm, "end": v(-59.3, -4.44) * mm});
            skLineSegment(sketch, "E5293", {"start": v(-59.3, -4.44) * mm, "end": v(-59.3, -4.5) * mm});
            skLineSegment(sketch, "E5294", {"start": v(-59.3, -4.5) * mm, "end": v(-59.3, -4.58) * mm});
            skLineSegment(sketch, "E5295", {"start": v(-59.3, -4.58) * mm, "end": v(-59.31, -4.64) * mm});
            skLineSegment(sketch, "E5296", {"start": v(-59.31, -4.64) * mm, "end": v(-59.32, -4.7) * mm});
            skLineSegment(sketch, "E5297", {"start": v(-59.32, -4.7) * mm, "end": v(-59.32, -4.77) * mm});
            skLineSegment(sketch, "E5298", {"start": v(-59.32, -4.77) * mm, "end": v(-59.32, -4.82) * mm});
            skLineSegment(sketch, "E5299", {"start": v(-59.32, -4.82) * mm, "end": v(-59.32, -4.82) * mm});
            skLineSegment(sketch, "E5300", {"start": v(-59.32, -4.82) * mm, "end": v(-59.32, -4.83) * mm});
            skLineSegment(sketch, "E5301", {"start": v(-59.32, -4.83) * mm, "end": v(-59.32, -4.83) * mm});
            skLineSegment(sketch, "E5302", {"start": v(-59.32, -4.83) * mm, "end": v(-59.32, -4.84) * mm});
            skLineSegment(sketch, "E5303", {"start": v(-59.32, -4.84) * mm, "end": v(-59.32, -4.84) * mm});
            skLineSegment(sketch, "E5304", {"start": v(-59.32, -4.84) * mm, "end": v(-59.32, -4.85) * mm});
            skLineSegment(sketch, "E5305", {"start": v(-59.32, -4.85) * mm, "end": v(-59.32, -4.85) * mm});
            skLineSegment(sketch, "E5306", {"start": v(-59.32, -4.85) * mm, "end": v(-59.32, -4.86) * mm});
            skLineSegment(sketch, "E5307", {"start": v(-59.32, -4.86) * mm, "end": v(-59.32, -4.86) * mm});
            skLineSegment(sketch, "E5308", {"start": v(-59.32, -4.86) * mm, "end": v(-59.32, -4.87) * mm});
            skLineSegment(sketch, "E5309", {"start": v(-59.32, -4.87) * mm, "end": v(-59.32, -4.88) * mm});
            skLineSegment(sketch, "E5310", {"start": v(-59.32, -4.88) * mm, "end": v(-59.31, -4.9) * mm});
            skLineSegment(sketch, "E5311", {"start": v(-59.31, -4.9) * mm, "end": v(-59.31, -4.9) * mm});
            skLineSegment(sketch, "E5312", {"start": v(-59.31, -4.9) * mm, "end": v(-59.3, -4.92) * mm});
            skLineSegment(sketch, "E5313", {"start": v(-59.3, -4.92) * mm, "end": v(-59.3, -4.93) * mm});
            skLineSegment(sketch, "E5314", {"start": v(-59.3, -4.93) * mm, "end": v(-59.3, -4.95) * mm});
            skLineSegment(sketch, "E5315", {"start": v(-59.3, -4.95) * mm, "end": v(-59.3, -4.96) * mm});
            skLineSegment(sketch, "E5316", {"start": v(-59.3, -4.96) * mm, "end": v(-59.3, -4.98) * mm});
            skLineSegment(sketch, "E5317", {"start": v(-59.3, -4.98) * mm, "end": v(-59.3, -5) * mm});
            skLineSegment(sketch, "E5318", {"start": v(-59.3, -5) * mm, "end": v(-59.3, -5.01) * mm});
            skLineSegment(sketch, "E5319", {"start": v(-59.3, -5.01) * mm, "end": v(-59.29, -5.05) * mm});
            skLineSegment(sketch, "E5320", {"start": v(-59.29, -5.05) * mm, "end": v(-59.28, -5.1) * mm});
            skLineSegment(sketch, "E5321", {"start": v(-59.28, -5.1) * mm, "end": v(-59.27, -5.14) * mm});
            skLineSegment(sketch, "E5322", {"start": v(-59.27, -5.14) * mm, "end": v(-59.26, -5.18) * mm});
            skLineSegment(sketch, "E5323", {"start": v(-59.26, -5.18) * mm, "end": v(-59.25, -5.24) * mm});
            skLineSegment(sketch, "E5324", {"start": v(-59.25, -5.24) * mm, "end": v(-59.24, -5.3) * mm});
            skLineSegment(sketch, "E5325", {"start": v(-59.24, -5.3) * mm, "end": v(-59.23, -5.35) * mm});
            skLineSegment(sketch, "E5326", {"start": v(-59.23, -5.35) * mm, "end": v(-59.22, -5.39) * mm});
            skLineSegment(sketch, "E5327", {"start": v(-59.22, -5.39) * mm, "end": v(-59.2, -5.5) * mm});
            skLineSegment(sketch, "E5328", {"start": v(-59.2, -5.5) * mm, "end": v(-59.18, -5.62) * mm});
            skLineSegment(sketch, "E5329", {"start": v(-59.18, -5.62) * mm, "end": v(-59.16, -5.72) * mm});
            skLineSegment(sketch, "E5330", {"start": v(-59.16, -5.72) * mm, "end": v(-59.14, -5.82) * mm});
            skLineSegment(sketch, "E5331", {"start": v(-59.14, -5.82) * mm, "end": v(-59.14, -5.86) * mm});
            skLineSegment(sketch, "E5332", {"start": v(-59.14, -5.86) * mm, "end": v(-59.13, -5.9) * mm});
            skLineSegment(sketch, "E5333", {"start": v(-59.13, -5.9) * mm, "end": v(-59.13, -5.95) * mm});
            skLineSegment(sketch, "E5334", {"start": v(-59.13, -5.95) * mm, "end": v(-59.13, -5.99) * mm});
            skLineSegment(sketch, "E5335", {"start": v(-59.13, -5.99) * mm, "end": v(-59.12, -6.02) * mm});
            skLineSegment(sketch, "E5336", {"start": v(-59.12, -6.02) * mm, "end": v(-59.12, -6.06) * mm});
            skLineSegment(sketch, "E5337", {"start": v(-59.12, -6.06) * mm, "end": v(-59.12, -6.1) * mm});
            skLineSegment(sketch, "E5338", {"start": v(-59.12, -6.1) * mm, "end": v(-59.12, -6.12) * mm});
            skLineSegment(sketch, "E5339", {"start": v(-59.12, -6.12) * mm, "end": v(-59.12, -6.17) * mm});
            skLineSegment(sketch, "E5340", {"start": v(-59.12, -6.17) * mm, "end": v(-59.12, -6.22) * mm});
            skLineSegment(sketch, "E5341", {"start": v(-59.12, -6.22) * mm, "end": v(-59.13, -6.27) * mm});
            skLineSegment(sketch, "E5342", {"start": v(-59.13, -6.27) * mm, "end": v(-59.13, -6.3) * mm});
            skLineSegment(sketch, "E5343", {"start": v(-59.13, -6.3) * mm, "end": v(-59.14, -6.33) * mm});
            skLineSegment(sketch, "E5344", {"start": v(-59.14, -6.33) * mm, "end": v(-59.14, -6.35) * mm});
            skLineSegment(sketch, "E5345", {"start": v(-59.14, -6.35) * mm, "end": v(-59.15, -6.37) * mm});
            skLineSegment(sketch, "E5346", {"start": v(-59.15, -6.37) * mm, "end": v(-59.15, -6.38) * mm});
            skLineSegment(sketch, "E5347", {"start": v(-59.15, -6.38) * mm, "end": v(-59.16, -6.4) * mm});
            skLineSegment(sketch, "E5348", {"start": v(-59.16, -6.4) * mm, "end": v(-59.17, -6.42) * mm});
            skLineSegment(sketch, "E5349", {"start": v(-59.17, -6.42) * mm, "end": v(-59.17, -6.43) * mm});
            skLineSegment(sketch, "E5350", {"start": v(-59.17, -6.43) * mm, "end": v(-59.18, -6.45) * mm});
            skLineSegment(sketch, "E5351", {"start": v(-59.18, -6.45) * mm, "end": v(-59.19, -6.46) * mm});
            skLineSegment(sketch, "E5352", {"start": v(-59.19, -6.46) * mm, "end": v(-59.2, -6.47) * mm});
            skLineSegment(sketch, "E5353", {"start": v(-59.2, -6.47) * mm, "end": v(-59.2, -6.48) * mm});
            skLineSegment(sketch, "E5354", {"start": v(-59.2, -6.48) * mm, "end": v(-59.21, -6.5) * mm});
            skLineSegment(sketch, "E5355", {"start": v(-59.21, -6.5) * mm, "end": v(-59.22, -6.5) * mm});
            skLineSegment(sketch, "E5356", {"start": v(-59.22, -6.5) * mm, "end": v(-59.23, -6.52) * mm});
            skLineSegment(sketch, "E5357", {"start": v(-59.23, -6.52) * mm, "end": v(-59.25, -6.52) * mm});
            skLineSegment(sketch, "E5358", {"start": v(-59.25, -6.52) * mm, "end": v(-59.26, -6.53) * mm});
            skLineSegment(sketch, "E5359", {"start": v(-59.26, -6.53) * mm, "end": v(-59.27, -6.54) * mm});
            skLineSegment(sketch, "E5360", {"start": v(-59.27, -6.54) * mm, "end": v(-59.28, -6.55) * mm});
            skLineSegment(sketch, "E5361", {"start": v(-59.28, -6.55) * mm, "end": v(-59.3, -6.55) * mm});
            skLineSegment(sketch, "E5362", {"start": v(-59.3, -6.55) * mm, "end": v(-59.3, -6.56) * mm});
            skLineSegment(sketch, "E5363", {"start": v(-59.3, -6.56) * mm, "end": v(-59.32, -6.56) * mm});
            skLineSegment(sketch, "E5364", {"start": v(-59.32, -6.56) * mm, "end": v(-59.33, -6.57) * mm});
            skLineSegment(sketch, "E5365", {"start": v(-59.33, -6.57) * mm, "end": v(-59.35, -6.57) * mm});
            skLineSegment(sketch, "E5366", {"start": v(-59.35, -6.57) * mm, "end": v(-59.36, -6.57) * mm});
            skLineSegment(sketch, "E5367", {"start": v(-59.36, -6.57) * mm, "end": v(-59.4, -6.57) * mm});
            skLineSegment(sketch, "E5368", {"start": v(-59.4, -6.57) * mm, "end": v(-59.43, -6.58) * mm});
            skLineSegment(sketch, "E5369", {"start": v(-59.43, -6.58) * mm, "end": v(-59.46, -6.57) * mm});
            skLineSegment(sketch, "E5370", {"start": v(-59.46, -6.57) * mm, "end": v(-59.5, -6.57) * mm});
            skLineSegment(sketch, "E5371", {"start": v(-59.5, -6.57) * mm, "end": v(-59.53, -6.57) * mm});
            skLineSegment(sketch, "E5372", {"start": v(-59.53, -6.57) * mm, "end": v(-59.57, -6.56) * mm});
            skLineSegment(sketch, "E5373", {"start": v(-59.57, -6.56) * mm, "end": v(-59.6, -6.55) * mm});
            skLineSegment(sketch, "E5374", {"start": v(-59.6, -6.55) * mm, "end": v(-59.65, -6.54) * mm});
            skLineSegment(sketch, "E5375", {"start": v(-59.65, -6.54) * mm, "end": v(-59.69, -6.53) * mm});
            skLineSegment(sketch, "E5376", {"start": v(-59.69, -6.53) * mm, "end": v(-59.73, -6.52) * mm});
            skLineSegment(sketch, "E5377", {"start": v(-59.73, -6.52) * mm, "end": v(-59.78, -6.5) * mm});
            skLineSegment(sketch, "E5378", {"start": v(-59.78, -6.5) * mm, "end": v(-59.83, -6.49) * mm});
            skLineSegment(sketch, "E5379", {"start": v(-59.83, -6.49) * mm, "end": v(-59.87, -6.47) * mm});
            skLineSegment(sketch, "E5380", {"start": v(-59.87, -6.47) * mm, "end": v(-59.98, -6.42) * mm});
            skLineSegment(sketch, "E5381", {"start": v(-59.98, -6.42) * mm, "end": v(-60.03, -6.4) * mm});
            skLineSegment(sketch, "E5382", {"start": v(-60.03, -6.4) * mm, "end": v(-60.3, -6.26) * mm});
            skLineSegment(sketch, "E5383", {"start": v(-60.3, -6.26) * mm, "end": v(-60.54, -6.13) * mm});
            skLineSegment(sketch, "E5384", {"start": v(-60.54, -6.13) * mm, "end": v(-60.65, -6.06) * mm});
            skLineSegment(sketch, "E5385", {"start": v(-60.65, -6.06) * mm, "end": v(-60.76, -6) * mm});
            skLineSegment(sketch, "E5386", {"start": v(-60.76, -6) * mm, "end": v(-60.86, -5.93) * mm});
            skLineSegment(sketch, "E5387", {"start": v(-60.86, -5.93) * mm, "end": v(-60.96, -5.86) * mm});
            skLineSegment(sketch, "E5388", {"start": v(-60.96, -5.86) * mm, "end": v(-61.05, -5.8) * mm});
            skLineSegment(sketch, "E5389", {"start": v(-61.05, -5.8) * mm, "end": v(-61.13, -5.73) * mm});
            skLineSegment(sketch, "E5390", {"start": v(-61.13, -5.73) * mm, "end": v(-61.21, -5.67) * mm});
            skLineSegment(sketch, "E5391", {"start": v(-61.21, -5.67) * mm, "end": v(-61.28, -5.6) * mm});
            skLineSegment(sketch, "E5392", {"start": v(-61.28, -5.6) * mm, "end": v(-61.35, -5.54) * mm});
            skLineSegment(sketch, "E5393", {"start": v(-61.35, -5.54) * mm, "end": v(-61.41, -5.48) * mm});
            skLineSegment(sketch, "E5394", {"start": v(-61.41, -5.48) * mm, "end": v(-61.47, -5.42) * mm});
            skLineSegment(sketch, "E5395", {"start": v(-61.47, -5.42) * mm, "end": v(-61.52, -5.36) * mm});
            skLineSegment(sketch, "E5396", {"start": v(-61.52, -5.36) * mm, "end": v(-61.56, -5.3) * mm});
            skLineSegment(sketch, "E5397", {"start": v(-61.56, -5.3) * mm, "end": v(-61.6, -5.23) * mm});
            skLineSegment(sketch, "E5398", {"start": v(-61.6, -5.23) * mm, "end": v(-61.65, -5.16) * mm});
            skLineSegment(sketch, "E5399", {"start": v(-61.65, -5.16) * mm, "end": v(-61.68, -5.1) * mm});
            skLineSegment(sketch, "E5400", {"start": v(-61.68, -5.1) * mm, "end": v(-61.72, -5.02) * mm});
            skLineSegment(sketch, "E5401", {"start": v(-61.72, -5.02) * mm, "end": v(-61.75, -4.95) * mm});
            skLineSegment(sketch, "E5402", {"start": v(-61.75, -4.95) * mm, "end": v(-61.78, -4.87) * mm});
            skLineSegment(sketch, "E5403", {"start": v(-61.78, -4.87) * mm, "end": v(-61.8, -4.8) * mm});
            skLineSegment(sketch, "E5404", {"start": v(-61.8, -4.8) * mm, "end": v(-61.82, -4.71) * mm});
            skLineSegment(sketch, "E5405", {"start": v(-61.82, -4.71) * mm, "end": v(-61.86, -4.54) * mm});
            skLineSegment(sketch, "E5406", {"start": v(-61.86, -4.54) * mm, "end": v(-61.88, -4.37) * mm});
            skLineSegment(sketch, "E5407", {"start": v(-61.88, -4.37) * mm, "end": v(-61.9, -4.18) * mm});
            skLineSegment(sketch, "E5408", {"start": v(-61.9, -4.18) * mm, "end": v(-61.9, -4.08) * mm});
            skLineSegment(sketch, "E5409", {"start": v(-61.9, -4.08) * mm, "end": v(-61.9, -3.9) * mm});
            skLineSegment(sketch, "E5410", {"start": v(-61.9, -3.9) * mm, "end": v(-61.88, -3.71) * mm});
            skLineSegment(sketch, "E5411", {"start": v(-61.88, -3.71) * mm, "end": v(-61.86, -3.5) * mm});
            skLineSegment(sketch, "E5412", {"start": v(-61.86, -3.5) * mm, "end": v(-61.83, -3.29) * mm});
            skLineSegment(sketch, "E5413", {"start": v(-61.83, -3.29) * mm, "end": v(-61.8, -3.06) * mm});
            skLineSegment(sketch, "E5414", {"start": v(-61.8, -3.06) * mm, "end": v(-61.75, -2.82) * mm});
            skLineSegment(sketch, "E5415", {"start": v(-61.75, -2.82) * mm, "end": v(-61.7, -2.56) * mm});
            skLineSegment(sketch, "E5416", {"start": v(-61.7, -2.56) * mm, "end": v(-61.64, -2.3) * mm});
            skLineSegment(sketch, "E5417", {"start": v(-61.64, -2.3) * mm, "end": v(-61.57, -2.02) * mm});
            skLineSegment(sketch, "E5418", {"start": v(-61.57, -2.02) * mm, "end": v(-61.5, -1.73) * mm});
            skLineSegment(sketch, "E5419", {"start": v(-61.5, -1.73) * mm, "end": v(-61.4, -1.42) * mm});
            skLineSegment(sketch, "E5420", {"start": v(-61.4, -1.42) * mm, "end": v(-61.22, -0.78) * mm});
            skLineSegment(sketch, "E5421", {"start": v(-61.22, -0.78) * mm, "end": v(-61, -0.1) * mm});
            skLineSegment(sketch, "E5422", {"start": v(-61, -0.1) * mm, "end": v(-60.87, 0.27) * mm});
            skLineSegment(sketch, "E5423", {"start": v(-60.87, 0.27) * mm, "end": v(-60.6, 1.01) * mm});
            skLineSegment(sketch, "E5424", {"start": v(-60.6, 1.01) * mm, "end": v(-59.99, 2.5) * mm});
            skLineSegment(sketch, "E5425", {"start": v(-59.99, 2.5) * mm, "end": v(-59.65, 3.23) * mm});
            skLineSegment(sketch, "E5426", {"start": v(-59.65, 3.23) * mm, "end": v(-59.3, 3.97) * mm});
            skLineSegment(sketch, "E5427", {"start": v(-59.3, 3.97) * mm, "end": v(-58.53, 5.46) * mm});
            skLineSegment(sketch, "E5428", {"start": v(-58.53, 5.46) * mm, "end": v(-58.12, 6.21) * mm});
            skLineSegment(sketch, "E5429", {"start": v(-58.12, 6.21) * mm, "end": v(-57.7, 6.95) * mm});
            skLineSegment(sketch, "E5430", {"start": v(-57.7, 6.95) * mm, "end": v(-56.9, 8.35) * mm});
            skLineSegment(sketch, "E5431", {"start": v(-56.9, 8.35) * mm, "end": v(-56.52, 9) * mm});
            skLineSegment(sketch, "E5432", {"start": v(-56.52, 9) * mm, "end": v(-57.34, 8.63) * mm});
            skLineSegment(sketch, "E5433", {"start": v(-57.34, 8.63) * mm, "end": v(-58.19, 8.2) * mm});
            skLineSegment(sketch, "E5434", {"start": v(-58.19, 8.2) * mm, "end": v(-59.06, 7.73) * mm});
            skLineSegment(sketch, "E5435", {"start": v(-59.06, 7.73) * mm, "end": v(-59.94, 7.2) * mm});
            skLineSegment(sketch, "E5436", {"start": v(-50.2, -6.69) * mm, "end": v(-50.23, -6.69) * mm});
            skLineSegment(sketch, "E5437", {"start": v(-50.23, -6.69) * mm, "end": v(-50.26, -6.68) * mm});
            skLineSegment(sketch, "E5438", {"start": v(-50.26, -6.68) * mm, "end": v(-50.29, -6.68) * mm});
            skLineSegment(sketch, "E5439", {"start": v(-50.29, -6.68) * mm, "end": v(-50.32, -6.68) * mm});
            skLineSegment(sketch, "E5440", {"start": v(-50.32, -6.68) * mm, "end": v(-50.34, -6.67) * mm});
            skLineSegment(sketch, "E5441", {"start": v(-50.34, -6.67) * mm, "end": v(-50.37, -6.66) * mm});
            skLineSegment(sketch, "E5442", {"start": v(-50.37, -6.66) * mm, "end": v(-50.4, -6.65) * mm});
            skLineSegment(sketch, "E5443", {"start": v(-50.4, -6.65) * mm, "end": v(-50.43, -6.64) * mm});
            skLineSegment(sketch, "E5444", {"start": v(-50.43, -6.64) * mm, "end": v(-50.45, -6.63) * mm});
            skLineSegment(sketch, "E5445", {"start": v(-50.45, -6.63) * mm, "end": v(-50.48, -6.61) * mm});
            skLineSegment(sketch, "E5446", {"start": v(-50.48, -6.61) * mm, "end": v(-50.5, -6.6) * mm});
            skLineSegment(sketch, "E5447", {"start": v(-50.5, -6.6) * mm, "end": v(-50.53, -6.58) * mm});
            skLineSegment(sketch, "E5448", {"start": v(-50.53, -6.58) * mm, "end": v(-50.55, -6.56) * mm});
            skLineSegment(sketch, "E5449", {"start": v(-50.55, -6.56) * mm, "end": v(-50.57, -6.54) * mm});
            skLineSegment(sketch, "E5450", {"start": v(-50.57, -6.54) * mm, "end": v(-50.6, -6.52) * mm});
            skLineSegment(sketch, "E5451", {"start": v(-50.6, -6.52) * mm, "end": v(-50.62, -6.5) * mm});
            skLineSegment(sketch, "E5452", {"start": v(-50.62, -6.5) * mm, "end": v(-50.64, -6.48) * mm});
            skLineSegment(sketch, "E5453", {"start": v(-50.64, -6.48) * mm, "end": v(-50.66, -6.45) * mm});
            skLineSegment(sketch, "E5454", {"start": v(-50.66, -6.45) * mm, "end": v(-50.68, -6.42) * mm});
            skLineSegment(sketch, "E5455", {"start": v(-50.68, -6.42) * mm, "end": v(-50.7, -6.4) * mm});
            skLineSegment(sketch, "E5456", {"start": v(-50.7, -6.4) * mm, "end": v(-50.7, -6.37) * mm});
            skLineSegment(sketch, "E5457", {"start": v(-50.7, -6.37) * mm, "end": v(-50.72, -6.34) * mm});
            skLineSegment(sketch, "E5458", {"start": v(-50.72, -6.34) * mm, "end": v(-50.74, -6.3) * mm});
            skLineSegment(sketch, "E5459", {"start": v(-50.74, -6.3) * mm, "end": v(-50.75, -6.28) * mm});
            skLineSegment(sketch, "E5460", {"start": v(-50.75, -6.28) * mm, "end": v(-50.76, -6.24) * mm});
            skLineSegment(sketch, "E5461", {"start": v(-50.76, -6.24) * mm, "end": v(-50.77, -6.2) * mm});
            skLineSegment(sketch, "E5462", {"start": v(-50.77, -6.2) * mm, "end": v(-50.77, -6.17) * mm});
            skLineSegment(sketch, "E5463", {"start": v(-50.77, -6.17) * mm, "end": v(-50.78, -6.14) * mm});
            skLineSegment(sketch, "E5464", {"start": v(-50.78, -6.14) * mm, "end": v(-50.78, -6.1) * mm});
            skLineSegment(sketch, "E5465", {"start": v(-50.78, -6.1) * mm, "end": v(-50.79, -6.06) * mm});
            skLineSegment(sketch, "E5466", {"start": v(-50.79, -6.06) * mm, "end": v(-50.8, -5.98) * mm});
            skLineSegment(sketch, "E5467", {"start": v(-50.8, -5.98) * mm, "end": v(-50.8, -5.96) * mm});
            skLineSegment(sketch, "E5468", {"start": v(-50.8, -5.96) * mm, "end": v(-50.79, -5.94) * mm});
            skLineSegment(sketch, "E5469", {"start": v(-50.79, -5.94) * mm, "end": v(-50.79, -5.93) * mm});
            skLineSegment(sketch, "E5470", {"start": v(-50.79, -5.93) * mm, "end": v(-50.79, -5.9) * mm});
            skLineSegment(sketch, "E5471", {"start": v(-50.79, -5.9) * mm, "end": v(-50.78, -5.89) * mm});
            skLineSegment(sketch, "E5472", {"start": v(-50.78, -5.89) * mm, "end": v(-50.78, -5.87) * mm});
            skLineSegment(sketch, "E5473", {"start": v(-50.78, -5.87) * mm, "end": v(-50.78, -5.85) * mm});
            skLineSegment(sketch, "E5474", {"start": v(-50.78, -5.85) * mm, "end": v(-50.77, -5.8) * mm});
            skLineSegment(sketch, "E5475", {"start": v(-50.77, -5.8) * mm, "end": v(-50.75, -5.75) * mm});
            skLineSegment(sketch, "E5476", {"start": v(-50.75, -5.75) * mm, "end": v(-50.74, -5.7) * mm});
            skLineSegment(sketch, "E5477", {"start": v(-50.74, -5.7) * mm, "end": v(-50.72, -5.65) * mm});
            skLineSegment(sketch, "E5478", {"start": v(-50.72, -5.65) * mm, "end": v(-50.7, -5.59) * mm});
            skLineSegment(sketch, "E5479", {"start": v(-50.7, -5.59) * mm, "end": v(-50.68, -5.53) * mm});
            skLineSegment(sketch, "E5480", {"start": v(-50.68, -5.53) * mm, "end": v(-50.66, -5.46) * mm});
            skLineSegment(sketch, "E5481", {"start": v(-50.66, -5.46) * mm, "end": v(-50.63, -5.4) * mm});
            skLineSegment(sketch, "E5482", {"start": v(-50.63, -5.4) * mm, "end": v(-50.6, -5.33) * mm});
            skLineSegment(sketch, "E5483", {"start": v(-50.6, -5.33) * mm, "end": v(-50.57, -5.25) * mm});
            skLineSegment(sketch, "E5484", {"start": v(-50.57, -5.25) * mm, "end": v(-50.54, -5.17) * mm});
            skLineSegment(sketch, "E5485", {"start": v(-50.54, -5.17) * mm, "end": v(-50.49, -5.05) * mm});
            skLineSegment(sketch, "E5486", {"start": v(-50.49, -5.05) * mm, "end": v(-50.32, -4.72) * mm});
            skLineSegment(sketch, "E5487", {"start": v(-50.32, -4.72) * mm, "end": v(-50.13, -4.41) * mm});
            skLineSegment(sketch, "E5488", {"start": v(-50.13, -4.41) * mm, "end": v(-49.93, -4.12) * mm});
            skLineSegment(sketch, "E5489", {"start": v(-49.93, -4.12) * mm, "end": v(-49.7, -3.85) * mm});
            skLineSegment(sketch, "E5490", {"start": v(-49.7, -3.85) * mm, "end": v(-49.65, -3.79) * mm});
            skLineSegment(sketch, "E5491", {"start": v(-49.65, -3.79) * mm, "end": v(-49.59, -3.73) * mm});
            skLineSegment(sketch, "E5492", {"start": v(-49.59, -3.73) * mm, "end": v(-49.53, -3.67) * mm});
            skLineSegment(sketch, "E5493", {"start": v(-49.53, -3.67) * mm, "end": v(-49.47, -3.62) * mm});
            skLineSegment(sketch, "E5494", {"start": v(-49.47, -3.62) * mm, "end": v(-49.4, -3.57) * mm});
            skLineSegment(sketch, "E5495", {"start": v(-49.4, -3.57) * mm, "end": v(-49.34, -3.53) * mm});
            skLineSegment(sketch, "E5496", {"start": v(-49.34, -3.53) * mm, "end": v(-49.28, -3.49) * mm});
            skLineSegment(sketch, "E5497", {"start": v(-49.28, -3.49) * mm, "end": v(-49.22, -3.45) * mm});
            skLineSegment(sketch, "E5498", {"start": v(-49.22, -3.45) * mm, "end": v(-49.16, -3.42) * mm});
            skLineSegment(sketch, "E5499", {"start": v(-49.16, -3.42) * mm, "end": v(-49.1, -3.4) * mm});
            skLineSegment(sketch, "E5500", {"start": v(-49.1, -3.4) * mm, "end": v(-49.04, -3.37) * mm});
            skLineSegment(sketch, "E5501", {"start": v(-49.04, -3.37) * mm, "end": v(-48.97, -3.35) * mm});
            skLineSegment(sketch, "E5502", {"start": v(-48.97, -3.35) * mm, "end": v(-48.91, -3.34) * mm});
            skLineSegment(sketch, "E5503", {"start": v(-48.91, -3.34) * mm, "end": v(-48.85, -3.33) * mm});
            skLineSegment(sketch, "E5504", {"start": v(-48.85, -3.33) * mm, "end": v(-48.79, -3.32) * mm});
            skLineSegment(sketch, "E5505", {"start": v(-48.79, -3.32) * mm, "end": v(-48.72, -3.32) * mm});
            skLineSegment(sketch, "E5506", {"start": v(-48.72, -3.32) * mm, "end": v(-48.69, -3.32) * mm});
            skLineSegment(sketch, "E5507", {"start": v(-48.69, -3.32) * mm, "end": v(-48.65, -3.32) * mm});
            skLineSegment(sketch, "E5508", {"start": v(-48.65, -3.32) * mm, "end": v(-48.61, -3.32) * mm});
            skLineSegment(sketch, "E5509", {"start": v(-48.61, -3.32) * mm, "end": v(-48.58, -3.33) * mm});
            skLineSegment(sketch, "E5510", {"start": v(-48.58, -3.33) * mm, "end": v(-48.54, -3.34) * mm});
            skLineSegment(sketch, "E5511", {"start": v(-48.54, -3.34) * mm, "end": v(-48.51, -3.34) * mm});
            skLineSegment(sketch, "E5512", {"start": v(-48.51, -3.34) * mm, "end": v(-48.48, -3.35) * mm});
            skLineSegment(sketch, "E5513", {"start": v(-48.48, -3.35) * mm, "end": v(-48.45, -3.36) * mm});
            skLineSegment(sketch, "E5514", {"start": v(-48.45, -3.36) * mm, "end": v(-48.42, -3.38) * mm});
            skLineSegment(sketch, "E5515", {"start": v(-48.42, -3.38) * mm, "end": v(-48.4, -3.4) * mm});
            skLineSegment(sketch, "E5516", {"start": v(-48.4, -3.4) * mm, "end": v(-48.37, -3.4) * mm});
            skLineSegment(sketch, "E5517", {"start": v(-48.37, -3.4) * mm, "end": v(-48.34, -3.42) * mm});
            skLineSegment(sketch, "E5518", {"start": v(-48.34, -3.42) * mm, "end": v(-48.32, -3.44) * mm});
            skLineSegment(sketch, "E5519", {"start": v(-48.32, -3.44) * mm, "end": v(-48.3, -3.46) * mm});
            skLineSegment(sketch, "E5520", {"start": v(-48.3, -3.46) * mm, "end": v(-48.28, -3.48) * mm});
            skLineSegment(sketch, "E5521", {"start": v(-48.28, -3.48) * mm, "end": v(-48.26, -3.5) * mm});
            skLineSegment(sketch, "E5522", {"start": v(-48.26, -3.5) * mm, "end": v(-48.24, -3.53) * mm});
            skLineSegment(sketch, "E5523", {"start": v(-48.24, -3.53) * mm, "end": v(-48.22, -3.55) * mm});
            skLineSegment(sketch, "E5524", {"start": v(-48.22, -3.55) * mm, "end": v(-48.2, -3.58) * mm});
            skLineSegment(sketch, "E5525", {"start": v(-48.2, -3.58) * mm, "end": v(-48.19, -3.6) * mm});
            skLineSegment(sketch, "E5526", {"start": v(-48.19, -3.6) * mm, "end": v(-48.17, -3.64) * mm});
            skLineSegment(sketch, "E5527", {"start": v(-48.17, -3.64) * mm, "end": v(-48.16, -3.67) * mm});
            skLineSegment(sketch, "E5528", {"start": v(-48.16, -3.67) * mm, "end": v(-48.15, -3.7) * mm});
            skLineSegment(sketch, "E5529", {"start": v(-48.15, -3.7) * mm, "end": v(-48.14, -3.73) * mm});
            skLineSegment(sketch, "E5530", {"start": v(-48.14, -3.73) * mm, "end": v(-48.13, -3.77) * mm});
            skLineSegment(sketch, "E5531", {"start": v(-48.13, -3.77) * mm, "end": v(-48.12, -3.8) * mm});
            skLineSegment(sketch, "E5532", {"start": v(-48.12, -3.8) * mm, "end": v(-48.12, -3.84) * mm});
            skLineSegment(sketch, "E5533", {"start": v(-48.12, -3.84) * mm, "end": v(-48.11, -3.88) * mm});
            skLineSegment(sketch, "E5534", {"start": v(-48.11, -3.88) * mm, "end": v(-48.1, -3.92) * mm});
            skLineSegment(sketch, "E5535", {"start": v(-48.1, -3.92) * mm, "end": v(-48.1, -4.01) * mm});
            skLineSegment(sketch, "E5536", {"start": v(-48.1, -4.01) * mm, "end": v(-48.1, -4.06) * mm});
            skLineSegment(sketch, "E5537", {"start": v(-48.1, -4.06) * mm, "end": v(-48.1, -4.1) * mm});
            skLineSegment(sketch, "E5538", {"start": v(-48.1, -4.1) * mm, "end": v(-48.1, -4.16) * mm});
            skLineSegment(sketch, "E5539", {"start": v(-48.1, -4.16) * mm, "end": v(-48.11, -4.22) * mm});
            skLineSegment(sketch, "E5540", {"start": v(-48.11, -4.22) * mm, "end": v(-48.12, -4.27) * mm});
            skLineSegment(sketch, "E5541", {"start": v(-48.12, -4.27) * mm, "end": v(-48.13, -4.33) * mm});
            skLineSegment(sketch, "E5542", {"start": v(-48.13, -4.33) * mm, "end": v(-48.15, -4.4) * mm});
            skLineSegment(sketch, "E5543", {"start": v(-48.15, -4.4) * mm, "end": v(-48.17, -4.46) * mm});
            skLineSegment(sketch, "E5544", {"start": v(-48.17, -4.46) * mm, "end": v(-48.18, -4.52) * mm});
            skLineSegment(sketch, "E5545", {"start": v(-48.18, -4.52) * mm, "end": v(-48.2, -4.59) * mm});
            skLineSegment(sketch, "E5546", {"start": v(-48.2, -4.59) * mm, "end": v(-48.26, -4.73) * mm});
            skLineSegment(sketch, "E5547", {"start": v(-48.26, -4.73) * mm, "end": v(-48.32, -4.88) * mm});
            skLineSegment(sketch, "E5548", {"start": v(-48.32, -4.88) * mm, "end": v(-48.4, -5.03) * mm});
            skLineSegment(sketch, "E5549", {"start": v(-48.4, -5.03) * mm, "end": v(-48.43, -5.11) * mm});
            skLineSegment(sketch, "E5550", {"start": v(-48.43, -5.11) * mm, "end": v(-48.61, -5.42) * mm});
            skLineSegment(sketch, "E5551", {"start": v(-48.61, -5.42) * mm, "end": v(-48.8, -5.7) * mm});
            skLineSegment(sketch, "E5552", {"start": v(-48.8, -5.7) * mm, "end": v(-49.02, -5.98) * mm});
            skLineSegment(sketch, "E5553", {"start": v(-49.02, -5.98) * mm, "end": v(-49.26, -6.22) * mm});
            skLineSegment(sketch, "E5554", {"start": v(-49.26, -6.22) * mm, "end": v(-49.32, -6.28) * mm});
            skLineSegment(sketch, "E5555", {"start": v(-49.32, -6.28) * mm, "end": v(-49.38, -6.33) * mm});
            skLineSegment(sketch, "E5556", {"start": v(-49.38, -6.33) * mm, "end": v(-49.44, -6.38) * mm});
            skLineSegment(sketch, "E5557", {"start": v(-49.44, -6.38) * mm, "end": v(-49.5, -6.43) * mm});
            skLineSegment(sketch, "E5558", {"start": v(-49.5, -6.43) * mm, "end": v(-49.56, -6.47) * mm});
            skLineSegment(sketch, "E5559", {"start": v(-49.56, -6.47) * mm, "end": v(-49.62, -6.5) * mm});
            skLineSegment(sketch, "E5560", {"start": v(-49.62, -6.5) * mm, "end": v(-49.68, -6.54) * mm});
            skLineSegment(sketch, "E5561", {"start": v(-49.68, -6.54) * mm, "end": v(-49.74, -6.57) * mm});
            skLineSegment(sketch, "E5562", {"start": v(-49.74, -6.57) * mm, "end": v(-49.8, -6.6) * mm});
            skLineSegment(sketch, "E5563", {"start": v(-49.8, -6.6) * mm, "end": v(-49.86, -6.62) * mm});
            skLineSegment(sketch, "E5564", {"start": v(-49.86, -6.62) * mm, "end": v(-49.91, -6.64) * mm});
            skLineSegment(sketch, "E5565", {"start": v(-49.91, -6.64) * mm, "end": v(-49.97, -6.66) * mm});
            skLineSegment(sketch, "E5566", {"start": v(-49.97, -6.66) * mm, "end": v(-50.03, -6.67) * mm});
            skLineSegment(sketch, "E5567", {"start": v(-50.03, -6.67) * mm, "end": v(-50.09, -6.68) * mm});
            skLineSegment(sketch, "E5568", {"start": v(-50.09, -6.68) * mm, "end": v(-50.14, -6.69) * mm});
            skLineSegment(sketch, "E5569", {"start": v(-50.14, -6.69) * mm, "end": v(-50.2, -6.69) * mm});
            skLineSegment(sketch, "E5570", {"start": v(-24.15, -2.45) * mm, "end": v(-24.24, -2.29) * mm});
            skLineSegment(sketch, "E5571", {"start": v(-24.24, -2.29) * mm, "end": v(-24.35, -2.13) * mm});
            skLineSegment(sketch, "E5572", {"start": v(-24.35, -2.13) * mm, "end": v(-24.47, -1.97) * mm});
            skLineSegment(sketch, "E5573", {"start": v(-24.47, -1.97) * mm, "end": v(-24.6, -1.82) * mm});
            skLineSegment(sketch, "E5574", {"start": v(-24.6, -1.82) * mm, "end": v(-24.74, -1.67) * mm});
            skLineSegment(sketch, "E5575", {"start": v(-24.74, -1.67) * mm, "end": v(-24.9, -1.53) * mm});
            skLineSegment(sketch, "E5576", {"start": v(-24.9, -1.53) * mm, "end": v(-25.06, -1.39) * mm});
            skLineSegment(sketch, "E5577", {"start": v(-25.06, -1.39) * mm, "end": v(-25.23, -1.25) * mm});
            skLineSegment(sketch, "E5578", {"start": v(-25.23, -1.25) * mm, "end": v(-25.6, -1) * mm});
            skLineSegment(sketch, "E5579", {"start": v(-25.6, -1) * mm, "end": v(-26, -0.77) * mm});
            skLineSegment(sketch, "E5580", {"start": v(-26, -0.77) * mm, "end": v(-26.42, -0.57) * mm});
            skLineSegment(sketch, "E5581", {"start": v(-26.42, -0.57) * mm, "end": v(-26.87, -0.4) * mm});
            skLineSegment(sketch, "E5582", {"start": v(-26.87, -0.4) * mm, "end": v(-27.32, -0.24) * mm});
            skLineSegment(sketch, "E5583", {"start": v(-27.32, -0.24) * mm, "end": v(-27.78, -0.1) * mm});
            skLineSegment(sketch, "E5584", {"start": v(-27.78, -0.1) * mm, "end": v(-28.26, 0) * mm});
            skLineSegment(sketch, "E5585", {"start": v(-28.26, 0) * mm, "end": v(-28.74, 0.1) * mm});
            skLineSegment(sketch, "E5586", {"start": v(-28.74, 0.1) * mm, "end": v(-29.47, 0.22) * mm});
            skLineSegment(sketch, "E5587", {"start": v(-29.47, 0.22) * mm, "end": v(-30.18, 0.38) * mm});
            skLineSegment(sketch, "E5588", {"start": v(-30.18, 0.38) * mm, "end": v(-30.88, 0.56) * mm});
            skLineSegment(sketch, "E5589", {"start": v(-30.88, 0.56) * mm, "end": v(-31.57, 0.78) * mm});
            skLineSegment(sketch, "E5590", {"start": v(-31.57, 0.78) * mm, "end": v(-32.24, 1.04) * mm});
            skLineSegment(sketch, "E5591", {"start": v(-32.24, 1.04) * mm, "end": v(-32.9, 1.32) * mm});
            skLineSegment(sketch, "E5592", {"start": v(-32.9, 1.32) * mm, "end": v(-33.56, 1.64) * mm});
            skLineSegment(sketch, "E5593", {"start": v(-33.56, 1.64) * mm, "end": v(-34.2, 1.99) * mm});
            skLineSegment(sketch, "E5594", {"start": v(-34.2, 1.99) * mm, "end": v(-34.22, 2) * mm});
            skLineSegment(sketch, "E5595", {"start": v(-34.22, 2) * mm, "end": v(-34.25, 2.02) * mm});
            skLineSegment(sketch, "E5596", {"start": v(-34.25, 2.02) * mm, "end": v(-34.28, 2.04) * mm});
            skLineSegment(sketch, "E5597", {"start": v(-34.28, 2.04) * mm, "end": v(-34.3, 2.06) * mm});
            skLineSegment(sketch, "E5598", {"start": v(-34.3, 2.06) * mm, "end": v(-34.33, 2.09) * mm});
            skLineSegment(sketch, "E5599", {"start": v(-34.33, 2.09) * mm, "end": v(-34.36, 2.11) * mm});
            skLineSegment(sketch, "E5600", {"start": v(-34.36, 2.11) * mm, "end": v(-34.4, 2.14) * mm});
            skLineSegment(sketch, "E5601", {"start": v(-34.4, 2.14) * mm, "end": v(-34.42, 2.17) * mm});
            skLineSegment(sketch, "E5602", {"start": v(-34.42, 2.17) * mm, "end": v(-34.45, 2.2) * mm});
            skLineSegment(sketch, "E5603", {"start": v(-34.45, 2.2) * mm, "end": v(-34.48, 2.23) * mm});
            skLineSegment(sketch, "E5604", {"start": v(-34.48, 2.23) * mm, "end": v(-34.54, 2.3) * mm});
            skLineSegment(sketch, "E5605", {"start": v(-34.54, 2.3) * mm, "end": v(-34.6, 2.39) * mm});
            skLineSegment(sketch, "E5606", {"start": v(-34.6, 2.39) * mm, "end": v(-34.66, 2.48) * mm});
            skLineSegment(sketch, "E5607", {"start": v(-34.66, 2.48) * mm, "end": v(-34.72, 2.57) * mm});
            skLineSegment(sketch, "E5608", {"start": v(-34.72, 2.57) * mm, "end": v(-34.77, 2.67) * mm});
            skLineSegment(sketch, "E5609", {"start": v(-34.77, 2.67) * mm, "end": v(-34.8, 2.76) * mm});
            skLineSegment(sketch, "E5610", {"start": v(-34.8, 2.76) * mm, "end": v(-34.84, 2.85) * mm});
            skLineSegment(sketch, "E5611", {"start": v(-34.84, 2.85) * mm, "end": v(-34.87, 2.94) * mm});
            skLineSegment(sketch, "E5612", {"start": v(-34.87, 2.94) * mm, "end": v(-34.89, 3.03) * mm});
            skLineSegment(sketch, "E5613", {"start": v(-34.89, 3.03) * mm, "end": v(-34.9, 3.12) * mm});
            skLineSegment(sketch, "E5614", {"start": v(-34.9, 3.12) * mm, "end": v(-34.9, 3.16) * mm});
            skLineSegment(sketch, "E5615", {"start": v(-34.9, 3.16) * mm, "end": v(-34.9, 3.2) * mm});
            skLineSegment(sketch, "E5616", {"start": v(-34.9, 3.2) * mm, "end": v(-34.88, 3.84) * mm});
            skLineSegment(sketch, "E5617", {"start": v(-34.88, 3.84) * mm, "end": v(-34.8, 4.48) * mm});
            skLineSegment(sketch, "E5618", {"start": v(-34.8, 4.48) * mm, "end": v(-34.67, 5.11) * mm});
            skLineSegment(sketch, "E5619", {"start": v(-34.67, 5.11) * mm, "end": v(-34.49, 5.75) * mm});
            skLineSegment(sketch, "E5620", {"start": v(-34.49, 5.75) * mm, "end": v(-34.37, 6.06) * mm});
            skLineSegment(sketch, "E5621", {"start": v(-34.37, 6.06) * mm, "end": v(-34.25, 6.36) * mm});
            skLineSegment(sketch, "E5622", {"start": v(-34.25, 6.36) * mm, "end": v(-34.13, 6.63) * mm});
            skLineSegment(sketch, "E5623", {"start": v(-34.13, 6.63) * mm, "end": v(-34, 6.9) * mm});
            skLineSegment(sketch, "E5624", {"start": v(-34, 6.9) * mm, "end": v(-33.85, 7.14) * mm});
            skLineSegment(sketch, "E5625", {"start": v(-33.85, 7.14) * mm, "end": v(-33.7, 7.36) * mm});
            skLineSegment(sketch, "E5626", {"start": v(-33.7, 7.36) * mm, "end": v(-33.55, 7.57) * mm});
            skLineSegment(sketch, "E5627", {"start": v(-33.55, 7.57) * mm, "end": v(-33.39, 7.76) * mm});
            skLineSegment(sketch, "E5628", {"start": v(-33.39, 7.76) * mm, "end": v(-33.25, 7.9) * mm});
            skLineSegment(sketch, "E5629", {"start": v(-33.25, 7.9) * mm, "end": v(-33.1, 8.05) * mm});
            skLineSegment(sketch, "E5630", {"start": v(-33.1, 8.05) * mm, "end": v(-32.93, 8.2) * mm});
            skLineSegment(sketch, "E5631", {"start": v(-32.93, 8.2) * mm, "end": v(-32.74, 8.34) * mm});
            skLineSegment(sketch, "E5632", {"start": v(-32.74, 8.34) * mm, "end": v(-32.55, 8.48) * mm});
            skLineSegment(sketch, "E5633", {"start": v(-32.55, 8.48) * mm, "end": v(-32.34, 8.61) * mm});
            skLineSegment(sketch, "E5634", {"start": v(-32.34, 8.61) * mm, "end": v(-32.12, 8.75) * mm});
            skLineSegment(sketch, "E5635", {"start": v(-32.12, 8.75) * mm, "end": v(-31.89, 8.88) * mm});
            skLineSegment(sketch, "E5636", {"start": v(-31.89, 8.88) * mm, "end": v(-31.64, 9.01) * mm});
            skLineSegment(sketch, "E5637", {"start": v(-31.64, 9.01) * mm, "end": v(-31.38, 9.14) * mm});
            skLineSegment(sketch, "E5638", {"start": v(-31.38, 9.14) * mm, "end": v(-31.1, 9.26) * mm});
            skLineSegment(sketch, "E5639", {"start": v(-31.1, 9.26) * mm, "end": v(-30.52, 9.5) * mm});
            skLineSegment(sketch, "E5640", {"start": v(-30.52, 9.5) * mm, "end": v(-29.88, 9.74) * mm});
            skLineSegment(sketch, "E5641", {"start": v(-29.88, 9.74) * mm, "end": v(-29.54, 9.85) * mm});
            skLineSegment(sketch, "E5642", {"start": v(-29.54, 9.85) * mm, "end": v(-28.83, 10.06) * mm});
            skLineSegment(sketch, "E5643", {"start": v(-28.83, 10.06) * mm, "end": v(-28.1, 10.25) * mm});
            skLineSegment(sketch, "E5644", {"start": v(-28.1, 10.25) * mm, "end": v(-27.35, 10.4) * mm});
            skLineSegment(sketch, "E5645", {"start": v(-27.35, 10.4) * mm, "end": v(-26.58, 10.53) * mm});
            skLineSegment(sketch, "E5646", {"start": v(-26.58, 10.53) * mm, "end": v(-25.78, 10.62) * mm});
            skLineSegment(sketch, "E5647", {"start": v(-25.78, 10.62) * mm, "end": v(-24.13, 10.74) * mm});
            skLineSegment(sketch, "E5648", {"start": v(-24.13, 10.74) * mm, "end": v(-23.26, 10.75) * mm});
            skLineSegment(sketch, "E5649", {"start": v(-23.26, 10.75) * mm, "end": v(-22.76, 10.75) * mm});
            skLineSegment(sketch, "E5650", {"start": v(-22.76, 10.75) * mm, "end": v(-22.28, 10.73) * mm});
            skLineSegment(sketch, "E5651", {"start": v(-22.28, 10.73) * mm, "end": v(-21.84, 10.7) * mm});
            skLineSegment(sketch, "E5652", {"start": v(-21.84, 10.7) * mm, "end": v(-21.42, 10.67) * mm});
            skLineSegment(sketch, "E5653", {"start": v(-21.42, 10.67) * mm, "end": v(-21.03, 10.63) * mm});
            skLineSegment(sketch, "E5654", {"start": v(-21.03, 10.63) * mm, "end": v(-20.68, 10.57) * mm});
            skLineSegment(sketch, "E5655", {"start": v(-20.68, 10.57) * mm, "end": v(-20.51, 10.54) * mm});
            skLineSegment(sketch, "E5656", {"start": v(-20.51, 10.54) * mm, "end": v(-20.35, 10.5) * mm});
            skLineSegment(sketch, "E5657", {"start": v(-20.35, 10.5) * mm, "end": v(-20.2, 10.47) * mm});
            skLineSegment(sketch, "E5658", {"start": v(-20.2, 10.47) * mm, "end": v(-20.05, 10.43) * mm});
            skLineSegment(sketch, "E5659", {"start": v(-20.05, 10.43) * mm, "end": v(-19.92, 10.4) * mm});
            skLineSegment(sketch, "E5660", {"start": v(-19.92, 10.4) * mm, "end": v(-19.79, 10.35) * mm});
            skLineSegment(sketch, "E5661", {"start": v(-19.79, 10.35) * mm, "end": v(-19.67, 10.3) * mm});
            skLineSegment(sketch, "E5662", {"start": v(-19.67, 10.3) * mm, "end": v(-19.56, 10.25) * mm});
            skLineSegment(sketch, "E5663", {"start": v(-19.56, 10.25) * mm, "end": v(-19.45, 10.2) * mm});
            skLineSegment(sketch, "E5664", {"start": v(-19.45, 10.2) * mm, "end": v(-19.36, 10.14) * mm});
            skLineSegment(sketch, "E5665", {"start": v(-19.36, 10.14) * mm, "end": v(-19.32, 10.12) * mm});
            skLineSegment(sketch, "E5666", {"start": v(-19.32, 10.12) * mm, "end": v(-19.27, 10.09) * mm});
            skLineSegment(sketch, "E5667", {"start": v(-19.27, 10.09) * mm, "end": v(-19.23, 10.06) * mm});
            skLineSegment(sketch, "E5668", {"start": v(-19.23, 10.06) * mm, "end": v(-19.2, 10.03) * mm});
            skLineSegment(sketch, "E5669", {"start": v(-19.2, 10.03) * mm, "end": v(-19.16, 10) * mm});
            skLineSegment(sketch, "E5670", {"start": v(-19.16, 10) * mm, "end": v(-19.13, 9.96) * mm});
            skLineSegment(sketch, "E5671", {"start": v(-19.13, 9.96) * mm, "end": v(-19.1, 9.93) * mm});
            skLineSegment(sketch, "E5672", {"start": v(-19.1, 9.93) * mm, "end": v(-19.07, 9.9) * mm});
            skLineSegment(sketch, "E5673", {"start": v(-19.07, 9.9) * mm, "end": v(-19.05, 9.87) * mm});
            skLineSegment(sketch, "E5674", {"start": v(-19.05, 9.87) * mm, "end": v(-19.02, 9.83) * mm});
            skLineSegment(sketch, "E5675", {"start": v(-19.02, 9.83) * mm, "end": v(-19, 9.8) * mm});
            skLineSegment(sketch, "E5676", {"start": v(-19, 9.8) * mm, "end": v(-18.98, 9.76) * mm});
            skLineSegment(sketch, "E5677", {"start": v(-18.98, 9.76) * mm, "end": v(-18.97, 9.72) * mm});
            skLineSegment(sketch, "E5678", {"start": v(-18.97, 9.72) * mm, "end": v(-18.95, 9.69) * mm});
            skLineSegment(sketch, "E5679", {"start": v(-18.95, 9.69) * mm, "end": v(-18.94, 9.65) * mm});
            skLineSegment(sketch, "E5680", {"start": v(-18.94, 9.65) * mm, "end": v(-18.93, 9.6) * mm});
            skLineSegment(sketch, "E5681", {"start": v(-18.93, 9.6) * mm, "end": v(-18.92, 9.57) * mm});
            skLineSegment(sketch, "E5682", {"start": v(-18.92, 9.57) * mm, "end": v(-18.92, 9.53) * mm});
            skLineSegment(sketch, "E5683", {"start": v(-18.92, 9.53) * mm, "end": v(-18.91, 9.5) * mm});
            skLineSegment(sketch, "E5684", {"start": v(-18.91, 9.5) * mm, "end": v(-18.91, 9.45) * mm});
            skLineSegment(sketch, "E5685", {"start": v(-18.91, 9.45) * mm, "end": v(-18.92, 9.19) * mm});
            skLineSegment(sketch, "E5686", {"start": v(-18.92, 9.19) * mm, "end": v(-18.93, 8.94) * mm});
            skLineSegment(sketch, "E5687", {"start": v(-18.93, 8.94) * mm, "end": v(-18.96, 8.7) * mm});
            skLineSegment(sketch, "E5688", {"start": v(-18.96, 8.7) * mm, "end": v(-18.99, 8.49) * mm});
            skLineSegment(sketch, "E5689", {"start": v(-18.99, 8.49) * mm, "end": v(-19, 8.38) * mm});
            skLineSegment(sketch, "E5690", {"start": v(-19, 8.38) * mm, "end": v(-19.03, 8.29) * mm});
            skLineSegment(sketch, "E5691", {"start": v(-19.03, 8.29) * mm, "end": v(-19.06, 8.2) * mm});
            skLineSegment(sketch, "E5692", {"start": v(-19.06, 8.2) * mm, "end": v(-19.08, 8.1) * mm});
            skLineSegment(sketch, "E5693", {"start": v(-19.08, 8.1) * mm, "end": v(-19.11, 8.01) * mm});
            skLineSegment(sketch, "E5694", {"start": v(-19.11, 8.01) * mm, "end": v(-19.15, 7.93) * mm});
            skLineSegment(sketch, "E5695", {"start": v(-19.15, 7.93) * mm, "end": v(-19.18, 7.85) * mm});
            skLineSegment(sketch, "E5696", {"start": v(-19.18, 7.85) * mm, "end": v(-19.22, 7.77) * mm});
            skLineSegment(sketch, "E5697", {"start": v(-19.22, 7.77) * mm, "end": v(-19.29, 7.63) * mm});
            skLineSegment(sketch, "E5698", {"start": v(-19.29, 7.63) * mm, "end": v(-19.36, 7.5) * mm});
            skLineSegment(sketch, "E5699", {"start": v(-19.36, 7.5) * mm, "end": v(-19.4, 7.44) * mm});
            skLineSegment(sketch, "E5700", {"start": v(-19.4, 7.44) * mm, "end": v(-19.44, 7.38) * mm});
            skLineSegment(sketch, "E5701", {"start": v(-19.44, 7.38) * mm, "end": v(-19.48, 7.33) * mm});
            skLineSegment(sketch, "E5702", {"start": v(-19.48, 7.33) * mm, "end": v(-19.52, 7.28) * mm});
            skLineSegment(sketch, "E5703", {"start": v(-19.52, 7.28) * mm, "end": v(-19.56, 7.23) * mm});
            skLineSegment(sketch, "E5704", {"start": v(-19.56, 7.23) * mm, "end": v(-19.6, 7.18) * mm});
            skLineSegment(sketch, "E5705", {"start": v(-19.6, 7.18) * mm, "end": v(-19.64, 7.14) * mm});
            skLineSegment(sketch, "E5706", {"start": v(-19.64, 7.14) * mm, "end": v(-19.68, 7.1) * mm});
            skLineSegment(sketch, "E5707", {"start": v(-19.68, 7.1) * mm, "end": v(-19.72, 7.07) * mm});
            skLineSegment(sketch, "E5708", {"start": v(-19.72, 7.07) * mm, "end": v(-19.77, 7.03) * mm});
            skLineSegment(sketch, "E5709", {"start": v(-19.77, 7.03) * mm, "end": v(-19.8, 7) * mm});
            skLineSegment(sketch, "E5710", {"start": v(-19.8, 7) * mm, "end": v(-19.85, 6.98) * mm});
            skLineSegment(sketch, "E5711", {"start": v(-19.85, 6.98) * mm, "end": v(-19.9, 6.95) * mm});
            skLineSegment(sketch, "E5712", {"start": v(-19.9, 6.95) * mm, "end": v(-19.94, 6.93) * mm});
            skLineSegment(sketch, "E5713", {"start": v(-19.94, 6.93) * mm, "end": v(-20, 6.9) * mm});
            skLineSegment(sketch, "E5714", {"start": v(-20, 6.9) * mm, "end": v(-20.05, 6.87) * mm});
            skLineSegment(sketch, "E5715", {"start": v(-20.05, 6.87) * mm, "end": v(-20.11, 6.84) * mm});
            skLineSegment(sketch, "E5716", {"start": v(-20.11, 6.84) * mm, "end": v(-20.18, 6.82) * mm});
            skLineSegment(sketch, "E5717", {"start": v(-20.18, 6.82) * mm, "end": v(-20.24, 6.78) * mm});
            skLineSegment(sketch, "E5718", {"start": v(-20.24, 6.78) * mm, "end": v(-20.32, 6.75) * mm});
            skLineSegment(sketch, "E5719", {"start": v(-20.32, 6.75) * mm, "end": v(-20.4, 6.72) * mm});
            skLineSegment(sketch, "E5720", {"start": v(-20.4, 6.72) * mm, "end": v(-20.47, 6.69) * mm});
            skLineSegment(sketch, "E5721", {"start": v(-20.47, 6.69) * mm, "end": v(-20.56, 6.65) * mm});
            skLineSegment(sketch, "E5722", {"start": v(-20.56, 6.65) * mm, "end": v(-20.74, 6.58) * mm});
            skLineSegment(sketch, "E5723", {"start": v(-20.74, 6.58) * mm, "end": v(-20.93, 6.5) * mm});
            skLineSegment(sketch, "E5724", {"start": v(-20.93, 6.5) * mm, "end": v(-21.04, 6.46) * mm});
            skLineSegment(sketch, "E5725", {"start": v(-21.04, 6.46) * mm, "end": v(-21.48, 6.3) * mm});
            skLineSegment(sketch, "E5726", {"start": v(-21.48, 6.3) * mm, "end": v(-21.9, 6.13) * mm});
            skLineSegment(sketch, "E5727", {"start": v(-21.9, 6.13) * mm, "end": v(-22.27, 5.96) * mm});
            skLineSegment(sketch, "E5728", {"start": v(-22.27, 5.96) * mm, "end": v(-22.63, 5.8) * mm});
            skLineSegment(sketch, "E5729", {"start": v(-22.63, 5.8) * mm, "end": v(-22.95, 5.62) * mm});
            skLineSegment(sketch, "E5730", {"start": v(-22.95, 5.62) * mm, "end": v(-23.25, 5.45) * mm});
            skLineSegment(sketch, "E5731", {"start": v(-23.25, 5.45) * mm, "end": v(-23.52, 5.29) * mm});
            skLineSegment(sketch, "E5732", {"start": v(-23.52, 5.29) * mm, "end": v(-23.77, 5.13) * mm});
            skLineSegment(sketch, "E5733", {"start": v(-23.77, 5.13) * mm, "end": v(-23.83, 5.09) * mm});
            skLineSegment(sketch, "E5734", {"start": v(-23.83, 5.09) * mm, "end": v(-23.88, 5.05) * mm});
            skLineSegment(sketch, "E5735", {"start": v(-23.88, 5.05) * mm, "end": v(-23.94, 5.02) * mm});
            skLineSegment(sketch, "E5736", {"start": v(-23.94, 5.02) * mm, "end": v(-23.99, 4.99) * mm});
            skLineSegment(sketch, "E5737", {"start": v(-23.99, 4.99) * mm, "end": v(-24.03, 4.96) * mm});
            skLineSegment(sketch, "E5738", {"start": v(-24.03, 4.96) * mm, "end": v(-24.08, 4.93) * mm});
            skLineSegment(sketch, "E5739", {"start": v(-24.08, 4.93) * mm, "end": v(-24.12, 4.9) * mm});
            skLineSegment(sketch, "E5740", {"start": v(-24.12, 4.9) * mm, "end": v(-24.16, 4.89) * mm});
            skLineSegment(sketch, "E5741", {"start": v(-24.16, 4.89) * mm, "end": v(-24.18, 4.88) * mm});
            skLineSegment(sketch, "E5742", {"start": v(-24.18, 4.88) * mm, "end": v(-24.2, 4.87) * mm});
            skLineSegment(sketch, "E5743", {"start": v(-24.2, 4.87) * mm, "end": v(-24.21, 4.86) * mm});
            skLineSegment(sketch, "E5744", {"start": v(-24.21, 4.86) * mm, "end": v(-24.23, 4.85) * mm});
            skLineSegment(sketch, "E5745", {"start": v(-24.23, 4.85) * mm, "end": v(-24.24, 4.85) * mm});
            skLineSegment(sketch, "E5746", {"start": v(-24.24, 4.85) * mm, "end": v(-24.26, 4.84) * mm});
            skLineSegment(sketch, "E5747", {"start": v(-24.26, 4.84) * mm, "end": v(-24.27, 4.83) * mm});
            skLineSegment(sketch, "E5748", {"start": v(-24.27, 4.83) * mm, "end": v(-24.28, 4.83) * mm});
            skLineSegment(sketch, "E5749", {"start": v(-24.28, 4.83) * mm, "end": v(-24.3, 4.82) * mm});
            skLineSegment(sketch, "E5750", {"start": v(-24.3, 4.82) * mm, "end": v(-24.3, 4.82) * mm});
            skLineSegment(sketch, "E5751", {"start": v(-24.3, 4.82) * mm, "end": v(-24.32, 4.82) * mm});
            skLineSegment(sketch, "E5752", {"start": v(-24.32, 4.82) * mm, "end": v(-24.32, 4.81) * mm});
            skLineSegment(sketch, "E5753", {"start": v(-24.32, 4.81) * mm, "end": v(-24.33, 4.81) * mm});
            skLineSegment(sketch, "E5754", {"start": v(-24.33, 4.81) * mm, "end": v(-24.33, 4.81) * mm});
            skLineSegment(sketch, "E5755", {"start": v(-24.33, 4.81) * mm, "end": v(-24.34, 4.81) * mm});
            skLineSegment(sketch, "E5756", {"start": v(-24.34, 4.81) * mm, "end": v(-24.34, 4.8) * mm});
            skLineSegment(sketch, "E5757", {"start": v(-24.34, 4.8) * mm, "end": v(-24.35, 4.8) * mm});
            skLineSegment(sketch, "E5758", {"start": v(-24.35, 4.8) * mm, "end": v(-24.35, 4.8) * mm});
            skLineSegment(sketch, "E5759", {"start": v(-24.35, 4.8) * mm, "end": v(-24.36, 4.8) * mm});
            skLineSegment(sketch, "E5760", {"start": v(-24.36, 4.8) * mm, "end": v(-24.36, 4.8) * mm});
            skLineSegment(sketch, "E5761", {"start": v(-24.36, 4.8) * mm, "end": v(-24.38, 4.8) * mm});
            skLineSegment(sketch, "E5762", {"start": v(-24.38, 4.8) * mm, "end": v(-24.39, 4.8) * mm});
            skLineSegment(sketch, "E5763", {"start": v(-24.39, 4.8) * mm, "end": v(-24.4, 4.8) * mm});
            skLineSegment(sketch, "E5764", {"start": v(-24.4, 4.8) * mm, "end": v(-24.4, 4.81) * mm});
            skLineSegment(sketch, "E5765", {"start": v(-24.4, 4.81) * mm, "end": v(-24.41, 4.81) * mm});
            skLineSegment(sketch, "E5766", {"start": v(-24.41, 4.81) * mm, "end": v(-24.42, 4.81) * mm});
            skLineSegment(sketch, "E5767", {"start": v(-24.42, 4.81) * mm, "end": v(-24.43, 4.81) * mm});
            skLineSegment(sketch, "E5768", {"start": v(-24.43, 4.81) * mm, "end": v(-24.43, 4.82) * mm});
            skLineSegment(sketch, "E5769", {"start": v(-24.43, 4.82) * mm, "end": v(-24.44, 4.82) * mm});
            skLineSegment(sketch, "E5770", {"start": v(-24.44, 4.82) * mm, "end": v(-24.45, 4.82) * mm});
            skLineSegment(sketch, "E5771", {"start": v(-24.45, 4.82) * mm, "end": v(-24.45, 4.82) * mm});
            skLineSegment(sketch, "E5772", {"start": v(-24.45, 4.82) * mm, "end": v(-24.46, 4.83) * mm});
            skLineSegment(sketch, "E5773", {"start": v(-24.46, 4.83) * mm, "end": v(-24.46, 4.83) * mm});
            skLineSegment(sketch, "E5774", {"start": v(-24.46, 4.83) * mm, "end": v(-24.47, 4.83) * mm});
            skLineSegment(sketch, "E5775", {"start": v(-24.47, 4.83) * mm, "end": v(-24.47, 4.84) * mm});
            skLineSegment(sketch, "E5776", {"start": v(-24.47, 4.84) * mm, "end": v(-24.48, 4.84) * mm});
            skLineSegment(sketch, "E5777", {"start": v(-24.48, 4.84) * mm, "end": v(-24.48, 4.84) * mm});
            skLineSegment(sketch, "E5778", {"start": v(-24.48, 4.84) * mm, "end": v(-24.48, 4.85) * mm});
            skLineSegment(sketch, "E5779", {"start": v(-24.48, 4.85) * mm, "end": v(-24.49, 4.85) * mm});
            skLineSegment(sketch, "E5780", {"start": v(-24.49, 4.85) * mm, "end": v(-24.5, 4.86) * mm});
            skLineSegment(sketch, "E5781", {"start": v(-24.5, 4.86) * mm, "end": v(-24.5, 4.86) * mm});
            skLineSegment(sketch, "E5782", {"start": v(-24.5, 4.86) * mm, "end": v(-24.5, 4.87) * mm});
            skLineSegment(sketch, "E5783", {"start": v(-24.5, 4.87) * mm, "end": v(-24.5, 4.87) * mm});
            skLineSegment(sketch, "E5784", {"start": v(-24.5, 4.87) * mm, "end": v(-24.5, 4.88) * mm});
            skLineSegment(sketch, "E5785", {"start": v(-24.5, 4.88) * mm, "end": v(-24.5, 4.88) * mm});
            skLineSegment(sketch, "E5786", {"start": v(-24.5, 4.88) * mm, "end": v(-24.5, 4.9) * mm});
            skLineSegment(sketch, "E5787", {"start": v(-24.5, 4.9) * mm, "end": v(-24.5, 4.9) * mm});
            skLineSegment(sketch, "E5788", {"start": v(-24.5, 4.9) * mm, "end": v(-24.5, 4.92) * mm});
            skLineSegment(sketch, "E5789", {"start": v(-24.5, 4.92) * mm, "end": v(-24.5, 4.92) * mm});
            skLineSegment(sketch, "E5790", {"start": v(-24.5, 4.92) * mm, "end": v(-24.5, 4.94) * mm});
            skLineSegment(sketch, "E5791", {"start": v(-24.5, 4.94) * mm, "end": v(-24.5, 4.96) * mm});
            skLineSegment(sketch, "E5792", {"start": v(-24.5, 4.96) * mm, "end": v(-24.5, 4.97) * mm});
            skLineSegment(sketch, "E5793", {"start": v(-24.5, 4.97) * mm, "end": v(-24.5, 4.99) * mm});
            skLineSegment(sketch, "E5794", {"start": v(-24.5, 4.99) * mm, "end": v(-24.5, 5) * mm});
            skLineSegment(sketch, "E5795", {"start": v(-24.5, 5) * mm, "end": v(-24.5, 5.02) * mm});
            skLineSegment(sketch, "E5796", {"start": v(-24.5, 5.02) * mm, "end": v(-24.48, 5.04) * mm});
            skLineSegment(sketch, "E5797", {"start": v(-24.48, 5.04) * mm, "end": v(-24.48, 5.06) * mm});
            skLineSegment(sketch, "E5798", {"start": v(-24.48, 5.06) * mm, "end": v(-24.47, 5.08) * mm});
            skLineSegment(sketch, "E5799", {"start": v(-24.47, 5.08) * mm, "end": v(-24.46, 5.1) * mm});
            skLineSegment(sketch, "E5800", {"start": v(-24.46, 5.1) * mm, "end": v(-24.45, 5.12) * mm});
            skLineSegment(sketch, "E5801", {"start": v(-24.45, 5.12) * mm, "end": v(-24.44, 5.14) * mm});
            skLineSegment(sketch, "E5802", {"start": v(-24.44, 5.14) * mm, "end": v(-24.42, 5.16) * mm});
            skLineSegment(sketch, "E5803", {"start": v(-24.42, 5.16) * mm, "end": v(-24.4, 5.2) * mm});
            skLineSegment(sketch, "E5804", {"start": v(-24.4, 5.2) * mm, "end": v(-24.37, 5.25) * mm});
            skLineSegment(sketch, "E5805", {"start": v(-24.37, 5.25) * mm, "end": v(-24.33, 5.3) * mm});
            skLineSegment(sketch, "E5806", {"start": v(-24.33, 5.3) * mm, "end": v(-24.3, 5.35) * mm});
            skLineSegment(sketch, "E5807", {"start": v(-24.3, 5.35) * mm, "end": v(-24.25, 5.4) * mm});
            skLineSegment(sketch, "E5808", {"start": v(-24.25, 5.4) * mm, "end": v(-24.2, 5.46) * mm});
            skLineSegment(sketch, "E5809", {"start": v(-24.2, 5.46) * mm, "end": v(-24.15, 5.51) * mm});
            skLineSegment(sketch, "E5810", {"start": v(-24.15, 5.51) * mm, "end": v(-24.1, 5.57) * mm});
            skLineSegment(sketch, "E5811", {"start": v(-24.1, 5.57) * mm, "end": v(-24, 5.66) * mm});
            skLineSegment(sketch, "E5812", {"start": v(-24, 5.66) * mm, "end": v(-23.87, 5.79) * mm});
            skLineSegment(sketch, "E5813", {"start": v(-23.87, 5.79) * mm, "end": v(-23.73, 5.9) * mm});
            skLineSegment(sketch, "E5814", {"start": v(-23.73, 5.9) * mm, "end": v(-23.58, 6.02) * mm});
            skLineSegment(sketch, "E5815", {"start": v(-23.58, 6.02) * mm, "end": v(-23.26, 6.24) * mm});
            skLineSegment(sketch, "E5816", {"start": v(-23.26, 6.24) * mm, "end": v(-22.91, 6.45) * mm});
            skLineSegment(sketch, "E5817", {"start": v(-22.91, 6.45) * mm, "end": v(-22.73, 6.54) * mm});
            skLineSegment(sketch, "E5818", {"start": v(-22.73, 6.54) * mm, "end": v(-22.63, 6.6) * mm});
            skLineSegment(sketch, "E5819", {"start": v(-22.63, 6.6) * mm, "end": v(-22.54, 6.64) * mm});
            skLineSegment(sketch, "E5820", {"start": v(-22.54, 6.64) * mm, "end": v(-22.46, 6.69) * mm});
            skLineSegment(sketch, "E5821", {"start": v(-22.46, 6.69) * mm, "end": v(-22.38, 6.73) * mm});
            skLineSegment(sketch, "E5822", {"start": v(-22.38, 6.73) * mm, "end": v(-22.31, 6.78) * mm});
            skLineSegment(sketch, "E5823", {"start": v(-22.31, 6.78) * mm, "end": v(-22.28, 6.8) * mm});
            skLineSegment(sketch, "E5824", {"start": v(-22.28, 6.8) * mm, "end": v(-22.25, 6.81) * mm});
            skLineSegment(sketch, "E5825", {"start": v(-22.25, 6.81) * mm, "end": v(-22.21, 6.83) * mm});
            skLineSegment(sketch, "E5826", {"start": v(-22.21, 6.83) * mm, "end": v(-22.19, 6.85) * mm});
            skLineSegment(sketch, "E5827", {"start": v(-22.19, 6.85) * mm, "end": v(-22.16, 6.87) * mm});
            skLineSegment(sketch, "E5828", {"start": v(-22.16, 6.87) * mm, "end": v(-22.13, 6.89) * mm});
            skLineSegment(sketch, "E5829", {"start": v(-22.13, 6.89) * mm, "end": v(-22.1, 6.9) * mm});
            skLineSegment(sketch, "E5830", {"start": v(-22.1, 6.9) * mm, "end": v(-22.09, 6.92) * mm});
            skLineSegment(sketch, "E5831", {"start": v(-22.09, 6.92) * mm, "end": v(-22.07, 6.93) * mm});
            skLineSegment(sketch, "E5832", {"start": v(-22.07, 6.93) * mm, "end": v(-22.05, 6.95) * mm});
            skLineSegment(sketch, "E5833", {"start": v(-22.05, 6.95) * mm, "end": v(-22.03, 6.96) * mm});
            skLineSegment(sketch, "E5834", {"start": v(-22.03, 6.96) * mm, "end": v(-22.01, 6.98) * mm});
            skLineSegment(sketch, "E5835", {"start": v(-22.01, 6.98) * mm, "end": v(-22, 6.99) * mm});
            skLineSegment(sketch, "E5836", {"start": v(-22, 6.99) * mm, "end": v(-22, 7) * mm});
            skLineSegment(sketch, "E5837", {"start": v(-22, 7) * mm, "end": v(-21.98, 7) * mm});
            skLineSegment(sketch, "E5838", {"start": v(-21.98, 7) * mm, "end": v(-21.98, 7) * mm});
            skLineSegment(sketch, "E5839", {"start": v(-21.98, 7) * mm, "end": v(-21.97, 7.01) * mm});
            skLineSegment(sketch, "E5840", {"start": v(-21.97, 7.01) * mm, "end": v(-21.97, 7.02) * mm});
            skLineSegment(sketch, "E5841", {"start": v(-21.97, 7.02) * mm, "end": v(-21.96, 7.02) * mm});
            skLineSegment(sketch, "E5842", {"start": v(-21.96, 7.02) * mm, "end": v(-21.96, 7.03) * mm});
            skLineSegment(sketch, "E5843", {"start": v(-21.96, 7.03) * mm, "end": v(-21.95, 7.03) * mm});
            skLineSegment(sketch, "E5844", {"start": v(-21.95, 7.03) * mm, "end": v(-21.95, 7.04) * mm});
            skLineSegment(sketch, "E5845", {"start": v(-21.95, 7.04) * mm, "end": v(-21.95, 7.04) * mm});
            skLineSegment(sketch, "E5846", {"start": v(-21.95, 7.04) * mm, "end": v(-21.94, 7.05) * mm});
            skLineSegment(sketch, "E5847", {"start": v(-21.94, 7.05) * mm, "end": v(-21.94, 7.05) * mm});
            skLineSegment(sketch, "E5848", {"start": v(-21.94, 7.05) * mm, "end": v(-21.94, 7.06) * mm});
            skLineSegment(sketch, "E5849", {"start": v(-21.94, 7.06) * mm, "end": v(-21.94, 7.06) * mm});
            skLineSegment(sketch, "E5850", {"start": v(-21.94, 7.06) * mm, "end": v(-21.94, 7.07) * mm});
            skLineSegment(sketch, "E5851", {"start": v(-21.94, 7.07) * mm, "end": v(-21.94, 7.07) * mm});
            skLineSegment(sketch, "E5852", {"start": v(-21.94, 7.07) * mm, "end": v(-21.93, 7.07) * mm});
            skLineSegment(sketch, "E5853", {"start": v(-21.93, 7.07) * mm, "end": v(-21.93, 7.08) * mm});
            skLineSegment(sketch, "E5854", {"start": v(-21.93, 7.08) * mm, "end": v(-21.93, 7.08) * mm});
            skLineSegment(sketch, "E5855", {"start": v(-21.93, 7.08) * mm, "end": v(-21.94, 7.09) * mm});
            skLineSegment(sketch, "E5856", {"start": v(-21.94, 7.09) * mm, "end": v(-21.94, 7.1) * mm});
            skLineSegment(sketch, "E5857", {"start": v(-21.94, 7.1) * mm, "end": v(-21.94, 7.1) * mm});
            skLineSegment(sketch, "E5858", {"start": v(-21.94, 7.1) * mm, "end": v(-21.94, 7.11) * mm});
            skLineSegment(sketch, "E5859", {"start": v(-21.94, 7.11) * mm, "end": v(-21.95, 7.12) * mm});
            skLineSegment(sketch, "E5860", {"start": v(-21.95, 7.12) * mm, "end": v(-21.95, 7.12) * mm});
            skLineSegment(sketch, "E5861", {"start": v(-21.95, 7.12) * mm, "end": v(-21.95, 7.13) * mm});
            skLineSegment(sketch, "E5862", {"start": v(-21.95, 7.13) * mm, "end": v(-21.96, 7.13) * mm});
            skLineSegment(sketch, "E5863", {"start": v(-21.96, 7.13) * mm, "end": v(-21.96, 7.14) * mm});
            skLineSegment(sketch, "E5864", {"start": v(-21.96, 7.14) * mm, "end": v(-21.97, 7.14) * mm});
            skLineSegment(sketch, "E5865", {"start": v(-21.97, 7.14) * mm, "end": v(-21.97, 7.15) * mm});
            skLineSegment(sketch, "E5866", {"start": v(-21.97, 7.15) * mm, "end": v(-21.98, 7.15) * mm});
            skLineSegment(sketch, "E5867", {"start": v(-21.98, 7.15) * mm, "end": v(-21.98, 7.16) * mm});
            skLineSegment(sketch, "E5868", {"start": v(-21.98, 7.16) * mm, "end": v(-21.99, 7.16) * mm});
            skLineSegment(sketch, "E5869", {"start": v(-21.99, 7.16) * mm, "end": v(-22, 7.16) * mm});
            skLineSegment(sketch, "E5870", {"start": v(-22, 7.16) * mm, "end": v(-22, 7.17) * mm});
            skLineSegment(sketch, "E5871", {"start": v(-22, 7.17) * mm, "end": v(-22.01, 7.17) * mm});
            skLineSegment(sketch, "E5872", {"start": v(-22.01, 7.17) * mm, "end": v(-22.02, 7.18) * mm});
            skLineSegment(sketch, "E5873", {"start": v(-22.02, 7.18) * mm, "end": v(-22.03, 7.18) * mm});
            skLineSegment(sketch, "E5874", {"start": v(-22.03, 7.18) * mm, "end": v(-22.05, 7.19) * mm});
            skLineSegment(sketch, "E5875", {"start": v(-22.05, 7.19) * mm, "end": v(-22.07, 7.2) * mm});
            skLineSegment(sketch, "E5876", {"start": v(-22.07, 7.2) * mm, "end": v(-22.1, 7.2) * mm});
            skLineSegment(sketch, "E5877", {"start": v(-22.1, 7.2) * mm, "end": v(-22.12, 7.2) * mm});
            skLineSegment(sketch, "E5878", {"start": v(-22.12, 7.2) * mm, "end": v(-22.14, 7.22) * mm});
            skLineSegment(sketch, "E5879", {"start": v(-22.14, 7.22) * mm, "end": v(-22.17, 7.22) * mm});
            skLineSegment(sketch, "E5880", {"start": v(-22.17, 7.22) * mm, "end": v(-22.2, 7.23) * mm});
            skLineSegment(sketch, "E5881", {"start": v(-22.2, 7.23) * mm, "end": v(-22.23, 7.23) * mm});
            skLineSegment(sketch, "E5882", {"start": v(-22.23, 7.23) * mm, "end": v(-22.26, 7.24) * mm});
            skLineSegment(sketch, "E5883", {"start": v(-22.26, 7.24) * mm, "end": v(-22.3, 7.24) * mm});
            skLineSegment(sketch, "E5884", {"start": v(-22.3, 7.24) * mm, "end": v(-22.33, 7.25) * mm});
            skLineSegment(sketch, "E5885", {"start": v(-22.33, 7.25) * mm, "end": v(-22.37, 7.25) * mm});
            skLineSegment(sketch, "E5886", {"start": v(-22.37, 7.25) * mm, "end": v(-22.45, 7.26) * mm});
            skLineSegment(sketch, "E5887", {"start": v(-22.45, 7.26) * mm, "end": v(-22.54, 7.26) * mm});
            skLineSegment(sketch, "E5888", {"start": v(-22.54, 7.26) * mm, "end": v(-22.63, 7.26) * mm});
            skLineSegment(sketch, "E5889", {"start": v(-22.63, 7.26) * mm, "end": v(-22.74, 7.27) * mm});
            skLineSegment(sketch, "E5890", {"start": v(-22.74, 7.27) * mm, "end": v(-22.82, 7.27) * mm});
            skLineSegment(sketch, "E5891", {"start": v(-22.82, 7.27) * mm, "end": v(-24.13, 7.24) * mm});
            skLineSegment(sketch, "E5892", {"start": v(-24.13, 7.24) * mm, "end": v(-25.4, 7.15) * mm});
            skLineSegment(sketch, "E5893", {"start": v(-25.4, 7.15) * mm, "end": v(-26.6, 7) * mm});
            skLineSegment(sketch, "E5894", {"start": v(-26.6, 7) * mm, "end": v(-27.76, 6.79) * mm});
            skLineSegment(sketch, "E5895", {"start": v(-27.76, 6.79) * mm, "end": v(-28.31, 6.66) * mm});
            skLineSegment(sketch, "E5896", {"start": v(-28.31, 6.66) * mm, "end": v(-28.84, 6.53) * mm});
            skLineSegment(sketch, "E5897", {"start": v(-28.84, 6.53) * mm, "end": v(-29.33, 6.39) * mm});
            skLineSegment(sketch, "E5898", {"start": v(-29.33, 6.39) * mm, "end": v(-29.8, 6.24) * mm});
            skLineSegment(sketch, "E5899", {"start": v(-29.8, 6.24) * mm, "end": v(-30.23, 6.07) * mm});
            skLineSegment(sketch, "E5900", {"start": v(-30.23, 6.07) * mm, "end": v(-30.63, 5.9) * mm});
            skLineSegment(sketch, "E5901", {"start": v(-30.63, 5.9) * mm, "end": v(-31, 5.72) * mm});
            skLineSegment(sketch, "E5902", {"start": v(-31, 5.72) * mm, "end": v(-31.35, 5.53) * mm});
            skLineSegment(sketch, "E5903", {"start": v(-31.35, 5.53) * mm, "end": v(-31.5, 5.43) * mm});
            skLineSegment(sketch, "E5904", {"start": v(-31.5, 5.43) * mm, "end": v(-31.65, 5.34) * mm});
            skLineSegment(sketch, "E5905", {"start": v(-31.65, 5.34) * mm, "end": v(-31.79, 5.24) * mm});
            skLineSegment(sketch, "E5906", {"start": v(-31.79, 5.24) * mm, "end": v(-31.92, 5.14) * mm});
            skLineSegment(sketch, "E5907", {"start": v(-31.92, 5.14) * mm, "end": v(-32.03, 5.04) * mm});
            skLineSegment(sketch, "E5908", {"start": v(-32.03, 5.04) * mm, "end": v(-32.14, 4.94) * mm});
            skLineSegment(sketch, "E5909", {"start": v(-32.14, 4.94) * mm, "end": v(-32.24, 4.84) * mm});
            skLineSegment(sketch, "E5910", {"start": v(-32.24, 4.84) * mm, "end": v(-32.32, 4.74) * mm});
            skLineSegment(sketch, "E5911", {"start": v(-32.32, 4.74) * mm, "end": v(-32.4, 4.64) * mm});
            skLineSegment(sketch, "E5912", {"start": v(-32.4, 4.64) * mm, "end": v(-32.47, 4.54) * mm});
            skLineSegment(sketch, "E5913", {"start": v(-32.47, 4.54) * mm, "end": v(-32.5, 4.5) * mm});
            skLineSegment(sketch, "E5914", {"start": v(-32.5, 4.5) * mm, "end": v(-32.52, 4.44) * mm});
            skLineSegment(sketch, "E5915", {"start": v(-32.52, 4.44) * mm, "end": v(-32.55, 4.4) * mm});
            skLineSegment(sketch, "E5916", {"start": v(-32.55, 4.4) * mm, "end": v(-32.57, 4.34) * mm});
            skLineSegment(sketch, "E5917", {"start": v(-32.57, 4.34) * mm, "end": v(-32.59, 4.3) * mm});
            skLineSegment(sketch, "E5918", {"start": v(-32.59, 4.3) * mm, "end": v(-32.6, 4.24) * mm});
            skLineSegment(sketch, "E5919", {"start": v(-32.6, 4.24) * mm, "end": v(-32.62, 4.2) * mm});
            skLineSegment(sketch, "E5920", {"start": v(-32.62, 4.2) * mm, "end": v(-32.63, 4.14) * mm});
            skLineSegment(sketch, "E5921", {"start": v(-32.63, 4.14) * mm, "end": v(-32.64, 4.1) * mm});
            skLineSegment(sketch, "E5922", {"start": v(-32.64, 4.1) * mm, "end": v(-32.64, 4.04) * mm});
            skLineSegment(sketch, "E5923", {"start": v(-32.64, 4.04) * mm, "end": v(-32.65, 4) * mm});
            skLineSegment(sketch, "E5924", {"start": v(-32.65, 4) * mm, "end": v(-32.65, 3.94) * mm});
            skLineSegment(sketch, "E5925", {"start": v(-32.65, 3.94) * mm, "end": v(-32.65, 3.88) * mm});
            skLineSegment(sketch, "E5926", {"start": v(-32.65, 3.88) * mm, "end": v(-32.64, 3.82) * mm});
            skLineSegment(sketch, "E5927", {"start": v(-32.64, 3.82) * mm, "end": v(-32.63, 3.76) * mm});
            skLineSegment(sketch, "E5928", {"start": v(-32.63, 3.76) * mm, "end": v(-32.62, 3.7) * mm});
            skLineSegment(sketch, "E5929", {"start": v(-32.62, 3.7) * mm, "end": v(-32.6, 3.65) * mm});
            skLineSegment(sketch, "E5930", {"start": v(-32.6, 3.65) * mm, "end": v(-32.57, 3.6) * mm});
            skLineSegment(sketch, "E5931", {"start": v(-32.57, 3.6) * mm, "end": v(-32.55, 3.55) * mm});
            skLineSegment(sketch, "E5932", {"start": v(-32.55, 3.55) * mm, "end": v(-32.52, 3.5) * mm});
            skLineSegment(sketch, "E5933", {"start": v(-32.52, 3.5) * mm, "end": v(-32.48, 3.46) * mm});
            skLineSegment(sketch, "E5934", {"start": v(-32.48, 3.46) * mm, "end": v(-32.44, 3.42) * mm});
            skLineSegment(sketch, "E5935", {"start": v(-32.44, 3.42) * mm, "end": v(-32.4, 3.38) * mm});
            skLineSegment(sketch, "E5936", {"start": v(-32.4, 3.38) * mm, "end": v(-32.35, 3.34) * mm});
            skLineSegment(sketch, "E5937", {"start": v(-32.35, 3.34) * mm, "end": v(-32.3, 3.3) * mm});
            skLineSegment(sketch, "E5938", {"start": v(-32.3, 3.3) * mm, "end": v(-32.24, 3.28) * mm});
            skLineSegment(sketch, "E5939", {"start": v(-32.24, 3.28) * mm, "end": v(-32.18, 3.25) * mm});
            skLineSegment(sketch, "E5940", {"start": v(-32.18, 3.25) * mm, "end": v(-32.11, 3.22) * mm});
            skLineSegment(sketch, "E5941", {"start": v(-32.11, 3.22) * mm, "end": v(-32.08, 3.2) * mm});
            skLineSegment(sketch, "E5942", {"start": v(-32.08, 3.2) * mm, "end": v(-32.04, 3.2) * mm});
            skLineSegment(sketch, "E5943", {"start": v(-32.04, 3.2) * mm, "end": v(-32, 3.18) * mm});
            skLineSegment(sketch, "E5944", {"start": v(-32, 3.18) * mm, "end": v(-31.96, 3.16) * mm});
            skLineSegment(sketch, "E5945", {"start": v(-31.96, 3.16) * mm, "end": v(-31.91, 3.15) * mm});
            skLineSegment(sketch, "E5946", {"start": v(-31.91, 3.15) * mm, "end": v(-31.86, 3.13) * mm});
            skLineSegment(sketch, "E5947", {"start": v(-31.86, 3.13) * mm, "end": v(-31.81, 3.11) * mm});
            skLineSegment(sketch, "E5948", {"start": v(-31.81, 3.11) * mm, "end": v(-31.76, 3.1) * mm});
            skLineSegment(sketch, "E5949", {"start": v(-31.76, 3.1) * mm, "end": v(-31.64, 3.06) * mm});
            skLineSegment(sketch, "E5950", {"start": v(-31.64, 3.06) * mm, "end": v(-31.52, 3.02) * mm});
            skLineSegment(sketch, "E5951", {"start": v(-31.52, 3.02) * mm, "end": v(-31.38, 2.98) * mm});
            skLineSegment(sketch, "E5952", {"start": v(-31.38, 2.98) * mm, "end": v(-31.24, 2.94) * mm});
            skLineSegment(sketch, "E5953", {"start": v(-31.24, 2.94) * mm, "end": v(-31.08, 2.9) * mm});
            skLineSegment(sketch, "E5954", {"start": v(-31.08, 2.9) * mm, "end": v(-30.92, 2.85) * mm});
            skLineSegment(sketch, "E5955", {"start": v(-30.92, 2.85) * mm, "end": v(-30.74, 2.8) * mm});
            skLineSegment(sketch, "E5956", {"start": v(-30.74, 2.8) * mm, "end": v(-30.56, 2.75) * mm});
            skLineSegment(sketch, "E5957", {"start": v(-30.56, 2.75) * mm, "end": v(-30.36, 2.7) * mm});
            skLineSegment(sketch, "E5958", {"start": v(-30.36, 2.7) * mm, "end": v(-30.16, 2.64) * mm});
            skLineSegment(sketch, "E5959", {"start": v(-30.16, 2.64) * mm, "end": v(-29.94, 2.58) * mm});
            skLineSegment(sketch, "E5960", {"start": v(-29.94, 2.58) * mm, "end": v(-29.71, 2.52) * mm});
            skLineSegment(sketch, "E5961", {"start": v(-29.71, 2.52) * mm, "end": v(-28.81, 2.27) * mm});
            skLineSegment(sketch, "E5962", {"start": v(-28.81, 2.27) * mm, "end": v(-27.96, 2) * mm});
            skLineSegment(sketch, "E5963", {"start": v(-27.96, 2) * mm, "end": v(-27.16, 1.7) * mm});
            skLineSegment(sketch, "E5964", {"start": v(-27.16, 1.7) * mm, "end": v(-26.4, 1.4) * mm});
            skLineSegment(sketch, "E5965", {"start": v(-26.4, 1.4) * mm, "end": v(-25.9, 1.17) * mm});
            skLineSegment(sketch, "E5966", {"start": v(-25.9, 1.17) * mm, "end": v(-25.42, 0.94) * mm});
            skLineSegment(sketch, "E5967", {"start": v(-25.42, 0.94) * mm, "end": v(-24.98, 0.71) * mm});
            skLineSegment(sketch, "E5968", {"start": v(-24.98, 0.71) * mm, "end": v(-24.58, 0.48) * mm});
            skLineSegment(sketch, "E5969", {"start": v(-24.58, 0.48) * mm, "end": v(-24.2, 0.25) * mm});
            skLineSegment(sketch, "E5970", {"start": v(-24.2, 0.25) * mm, "end": v(-23.87, 0) * mm});
            skLineSegment(sketch, "E5971", {"start": v(-23.87, 0) * mm, "end": v(-23.71, -0.1) * mm});
            skLineSegment(sketch, "E5972", {"start": v(-23.71, -0.1) * mm, "end": v(-23.56, -0.23) * mm});
            skLineSegment(sketch, "E5973", {"start": v(-23.56, -0.23) * mm, "end": v(-23.42, -0.35) * mm});
            skLineSegment(sketch, "E5974", {"start": v(-23.42, -0.35) * mm, "end": v(-23.3, -0.47) * mm});
            skLineSegment(sketch, "E5975", {"start": v(-23.3, -0.47) * mm, "end": v(-23.17, -0.6) * mm});
            skLineSegment(sketch, "E5976", {"start": v(-23.17, -0.6) * mm, "end": v(-23.06, -0.72) * mm});
            skLineSegment(sketch, "E5977", {"start": v(-23.06, -0.72) * mm, "end": v(-22.95, -0.84) * mm});
            skLineSegment(sketch, "E5978", {"start": v(-22.95, -0.84) * mm, "end": v(-22.85, -0.97) * mm});
            skLineSegment(sketch, "E5979", {"start": v(-22.85, -0.97) * mm, "end": v(-22.76, -1.1) * mm});
            skLineSegment(sketch, "E5980", {"start": v(-22.76, -1.1) * mm, "end": v(-22.68, -1.23) * mm});
            skLineSegment(sketch, "E5981", {"start": v(-22.68, -1.23) * mm, "end": v(-22.6, -1.36) * mm});
            skLineSegment(sketch, "E5982", {"start": v(-22.6, -1.36) * mm, "end": v(-22.53, -1.5) * mm});
            skLineSegment(sketch, "E5983", {"start": v(-22.53, -1.5) * mm, "end": v(-22.48, -1.63) * mm});
            skLineSegment(sketch, "E5984", {"start": v(-22.48, -1.63) * mm, "end": v(-22.42, -1.77) * mm});
            skLineSegment(sketch, "E5985", {"start": v(-22.42, -1.77) * mm, "end": v(-22.38, -1.91) * mm});
            skLineSegment(sketch, "E5986", {"start": v(-22.38, -1.91) * mm, "end": v(-22.34, -2.05) * mm});
            skLineSegment(sketch, "E5987", {"start": v(-22.34, -2.05) * mm, "end": v(-22.32, -2.2) * mm});
            skLineSegment(sketch, "E5988", {"start": v(-22.32, -2.2) * mm, "end": v(-22.3, -2.34) * mm});
            skLineSegment(sketch, "E5989", {"start": v(-22.3, -2.34) * mm, "end": v(-22.29, -2.49) * mm});
            skLineSegment(sketch, "E5990", {"start": v(-22.29, -2.49) * mm, "end": v(-22.28, -2.64) * mm});
            skLineSegment(sketch, "E5991", {"start": v(-22.28, -2.64) * mm, "end": v(-22.29, -2.85) * mm});
            skLineSegment(sketch, "E5992", {"start": v(-22.29, -2.85) * mm, "end": v(-22.3, -3.05) * mm});
            skLineSegment(sketch, "E5993", {"start": v(-22.3, -3.05) * mm, "end": v(-22.34, -3.26) * mm});
            skLineSegment(sketch, "E5994", {"start": v(-22.34, -3.26) * mm, "end": v(-22.38, -3.47) * mm});
            skLineSegment(sketch, "E5995", {"start": v(-22.38, -3.47) * mm, "end": v(-22.44, -3.67) * mm});
            skLineSegment(sketch, "E5996", {"start": v(-22.44, -3.67) * mm, "end": v(-22.5, -3.88) * mm});
            skLineSegment(sketch, "E5997", {"start": v(-22.5, -3.88) * mm, "end": v(-22.6, -4.1) * mm});
            skLineSegment(sketch, "E5998", {"start": v(-22.6, -4.1) * mm, "end": v(-22.69, -4.3) * mm});
            skLineSegment(sketch, "E5999", {"start": v(-22.69, -4.3) * mm, "end": v(-22.8, -4.5) * mm});
            skLineSegment(sketch, "E6000", {"start": v(-22.8, -4.5) * mm, "end": v(-22.9, -4.7) * mm});
            skLineSegment(sketch, "E6001", {"start": v(-22.9, -4.7) * mm, "end": v(-23.03, -4.9) * mm});
            skLineSegment(sketch, "E6002", {"start": v(-23.03, -4.9) * mm, "end": v(-23.17, -5.1) * mm});
            skLineSegment(sketch, "E6003", {"start": v(-23.17, -5.1) * mm, "end": v(-23.32, -5.28) * mm});
            skLineSegment(sketch, "E6004", {"start": v(-23.32, -5.28) * mm, "end": v(-23.48, -5.46) * mm});
            skLineSegment(sketch, "E6005", {"start": v(-23.48, -5.46) * mm, "end": v(-23.66, -5.64) * mm});
            skLineSegment(sketch, "E6006", {"start": v(-23.66, -5.64) * mm, "end": v(-23.84, -5.82) * mm});
            skLineSegment(sketch, "E6007", {"start": v(-23.84, -5.82) * mm, "end": v(-24.24, -6.15) * mm});
            skLineSegment(sketch, "E6008", {"start": v(-24.24, -6.15) * mm, "end": v(-24.67, -6.45) * mm});
            skLineSegment(sketch, "E6009", {"start": v(-24.67, -6.45) * mm, "end": v(-25.12, -6.72) * mm});
            skLineSegment(sketch, "E6010", {"start": v(-25.12, -6.72) * mm, "end": v(-25.6, -6.96) * mm});
            skLineSegment(sketch, "E6011", {"start": v(-25.6, -6.96) * mm, "end": v(-25.83, -7.05) * mm});
            skLineSegment(sketch, "E6012", {"start": v(-25.83, -7.05) * mm, "end": v(-26.06, -7.14) * mm});
            skLineSegment(sketch, "E6013", {"start": v(-26.06, -7.14) * mm, "end": v(-26.31, -7.23) * mm});
            skLineSegment(sketch, "E6014", {"start": v(-26.31, -7.23) * mm, "end": v(-26.57, -7.31) * mm});
            skLineSegment(sketch, "E6015", {"start": v(-26.57, -7.31) * mm, "end": v(-26.85, -7.4) * mm});
            skLineSegment(sketch, "E6016", {"start": v(-26.85, -7.4) * mm, "end": v(-27.14, -7.48) * mm});
            skLineSegment(sketch, "E6017", {"start": v(-27.14, -7.48) * mm, "end": v(-27.44, -7.56) * mm});
            skLineSegment(sketch, "E6018", {"start": v(-27.44, -7.56) * mm, "end": v(-27.76, -7.64) * mm});
            skLineSegment(sketch, "E6019", {"start": v(-27.76, -7.64) * mm, "end": v(-28.42, -7.8) * mm});
            skLineSegment(sketch, "E6020", {"start": v(-28.42, -7.8) * mm, "end": v(-29.1, -7.92) * mm});
            skLineSegment(sketch, "E6021", {"start": v(-29.1, -7.92) * mm, "end": v(-29.82, -8.04) * mm});
            skLineSegment(sketch, "E6022", {"start": v(-29.82, -8.04) * mm, "end": v(-30.57, -8.13) * mm});
            skLineSegment(sketch, "E6023", {"start": v(-30.57, -8.13) * mm, "end": v(-31.31, -8.22) * mm});
            skLineSegment(sketch, "E6024", {"start": v(-31.31, -8.22) * mm, "end": v(-32.75, -8.3) * mm});
            skLineSegment(sketch, "E6025", {"start": v(-32.75, -8.3) * mm, "end": v(-33.44, -8.32) * mm});
            skLineSegment(sketch, "E6026", {"start": v(-33.44, -8.32) * mm, "end": v(-34.06, -8.31) * mm});
            skLineSegment(sketch, "E6027", {"start": v(-34.06, -8.31) * mm, "end": v(-34.65, -8.3) * mm});
            skLineSegment(sketch, "E6028", {"start": v(-34.65, -8.3) * mm, "end": v(-35.2, -8.25) * mm});
            skLineSegment(sketch, "E6029", {"start": v(-35.2, -8.25) * mm, "end": v(-35.73, -8.2) * mm});
            skLineSegment(sketch, "E6030", {"start": v(-35.73, -8.2) * mm, "end": v(-36.22, -8.13) * mm});
            skLineSegment(sketch, "E6031", {"start": v(-36.22, -8.13) * mm, "end": v(-36.69, -8.05) * mm});
            skLineSegment(sketch, "E6032", {"start": v(-36.69, -8.05) * mm, "end": v(-37.12, -7.96) * mm});
            skLineSegment(sketch, "E6033", {"start": v(-37.12, -7.96) * mm, "end": v(-37.52, -7.84) * mm});
            skLineSegment(sketch, "E6034", {"start": v(-37.52, -7.84) * mm, "end": v(-37.7, -7.78) * mm});
            skLineSegment(sketch, "E6035", {"start": v(-37.7, -7.78) * mm, "end": v(-37.88, -7.72) * mm});
            skLineSegment(sketch, "E6036", {"start": v(-37.88, -7.72) * mm, "end": v(-38.04, -7.65) * mm});
            skLineSegment(sketch, "E6037", {"start": v(-38.04, -7.65) * mm, "end": v(-38.2, -7.57) * mm});
            skLineSegment(sketch, "E6038", {"start": v(-38.2, -7.57) * mm, "end": v(-38.33, -7.5) * mm});
            skLineSegment(sketch, "E6039", {"start": v(-38.33, -7.5) * mm, "end": v(-38.46, -7.42) * mm});
            skLineSegment(sketch, "E6040", {"start": v(-38.46, -7.42) * mm, "end": v(-38.51, -7.38) * mm});
            skLineSegment(sketch, "E6041", {"start": v(-38.51, -7.38) * mm, "end": v(-38.57, -7.33) * mm});
            skLineSegment(sketch, "E6042", {"start": v(-38.57, -7.33) * mm, "end": v(-38.62, -7.29) * mm});
            skLineSegment(sketch, "E6043", {"start": v(-38.62, -7.29) * mm, "end": v(-38.67, -7.24) * mm});
            skLineSegment(sketch, "E6044", {"start": v(-38.67, -7.24) * mm, "end": v(-38.72, -7.2) * mm});
            skLineSegment(sketch, "E6045", {"start": v(-38.72, -7.2) * mm, "end": v(-38.76, -7.15) * mm});
            skLineSegment(sketch, "E6046", {"start": v(-38.76, -7.15) * mm, "end": v(-38.8, -7.1) * mm});
            skLineSegment(sketch, "E6047", {"start": v(-38.8, -7.1) * mm, "end": v(-38.84, -7.06) * mm});
            skLineSegment(sketch, "E6048", {"start": v(-38.84, -7.06) * mm, "end": v(-38.87, -7) * mm});
            skLineSegment(sketch, "E6049", {"start": v(-38.87, -7) * mm, "end": v(-38.9, -6.96) * mm});
            skLineSegment(sketch, "E6050", {"start": v(-38.9, -6.96) * mm, "end": v(-38.93, -6.9) * mm});
            skLineSegment(sketch, "E6051", {"start": v(-38.93, -6.9) * mm, "end": v(-38.96, -6.85) * mm});
            skLineSegment(sketch, "E6052", {"start": v(-38.96, -6.85) * mm, "end": v(-38.98, -6.8) * mm});
            skLineSegment(sketch, "E6053", {"start": v(-38.98, -6.8) * mm, "end": v(-39, -6.74) * mm});
            skLineSegment(sketch, "E6054", {"start": v(-39, -6.74) * mm, "end": v(-39.02, -6.69) * mm});
            skLineSegment(sketch, "E6055", {"start": v(-39.02, -6.69) * mm, "end": v(-39.03, -6.63) * mm});
            skLineSegment(sketch, "E6056", {"start": v(-39.03, -6.63) * mm, "end": v(-39.04, -6.58) * mm});
            skLineSegment(sketch, "E6057", {"start": v(-39.04, -6.58) * mm, "end": v(-39.05, -6.52) * mm});
            skLineSegment(sketch, "E6058", {"start": v(-39.05, -6.52) * mm, "end": v(-39.05, -6.46) * mm});
            skLineSegment(sketch, "E6059", {"start": v(-39.05, -6.46) * mm, "end": v(-39.05, -6.4) * mm});
            skLineSegment(sketch, "E6060", {"start": v(-39.05, -6.4) * mm, "end": v(-39.05, -6.37) * mm});
            skLineSegment(sketch, "E6061", {"start": v(-39.05, -6.37) * mm, "end": v(-39.05, -6.34) * mm});
            skLineSegment(sketch, "E6062", {"start": v(-39.05, -6.34) * mm, "end": v(-39.05, -6.31) * mm});
            skLineSegment(sketch, "E6063", {"start": v(-39.05, -6.31) * mm, "end": v(-39.05, -6.28) * mm});
            skLineSegment(sketch, "E6064", {"start": v(-39.05, -6.28) * mm, "end": v(-39.04, -6.22) * mm});
            skLineSegment(sketch, "E6065", {"start": v(-39.04, -6.22) * mm, "end": v(-39.02, -6.15) * mm});
            skLineSegment(sketch, "E6066", {"start": v(-39.02, -6.15) * mm, "end": v(-39, -6.08) * mm});
            skLineSegment(sketch, "E6067", {"start": v(-39, -6.08) * mm, "end": v(-38.98, -6) * mm});
            skLineSegment(sketch, "E6068", {"start": v(-38.98, -6) * mm, "end": v(-38.95, -5.93) * mm});
            skLineSegment(sketch, "E6069", {"start": v(-38.95, -5.93) * mm, "end": v(-38.92, -5.85) * mm});
            skLineSegment(sketch, "E6070", {"start": v(-38.92, -5.85) * mm, "end": v(-38.89, -5.76) * mm});
            skLineSegment(sketch, "E6071", {"start": v(-38.89, -5.76) * mm, "end": v(-38.85, -5.67) * mm});
            skLineSegment(sketch, "E6072", {"start": v(-38.85, -5.67) * mm, "end": v(-38.8, -5.58) * mm});
            skLineSegment(sketch, "E6073", {"start": v(-38.8, -5.58) * mm, "end": v(-38.76, -5.48) * mm});
            skLineSegment(sketch, "E6074", {"start": v(-38.76, -5.48) * mm, "end": v(-38.71, -5.38) * mm});
            skLineSegment(sketch, "E6075", {"start": v(-38.71, -5.38) * mm, "end": v(-38.66, -5.27) * mm});
            skLineSegment(sketch, "E6076", {"start": v(-38.66, -5.27) * mm, "end": v(-38.6, -5.17) * mm});
            skLineSegment(sketch, "E6077", {"start": v(-38.6, -5.17) * mm, "end": v(-38.53, -5.05) * mm});
            skLineSegment(sketch, "E6078", {"start": v(-38.53, -5.05) * mm, "end": v(-38.4, -4.83) * mm});
            skLineSegment(sketch, "E6079", {"start": v(-38.4, -4.83) * mm, "end": v(-38.26, -4.63) * mm});
            skLineSegment(sketch, "E6080", {"start": v(-38.26, -4.63) * mm, "end": v(-38.12, -4.44) * mm});
            skLineSegment(sketch, "E6081", {"start": v(-38.12, -4.44) * mm, "end": v(-38.04, -4.36) * mm});
            skLineSegment(sketch, "E6082", {"start": v(-38.04, -4.36) * mm, "end": v(-37.97, -4.28) * mm});
            skLineSegment(sketch, "E6083", {"start": v(-37.97, -4.28) * mm, "end": v(-37.89, -4.2) * mm});
            skLineSegment(sketch, "E6084", {"start": v(-37.89, -4.2) * mm, "end": v(-37.8, -4.13) * mm});
            skLineSegment(sketch, "E6085", {"start": v(-37.8, -4.13) * mm, "end": v(-37.73, -4.07) * mm});
            skLineSegment(sketch, "E6086", {"start": v(-37.73, -4.07) * mm, "end": v(-37.65, -4) * mm});
            skLineSegment(sketch, "E6087", {"start": v(-37.65, -4) * mm, "end": v(-37.56, -3.95) * mm});
            skLineSegment(sketch, "E6088", {"start": v(-37.56, -3.95) * mm, "end": v(-37.48, -3.9) * mm});
            skLineSegment(sketch, "E6089", {"start": v(-37.48, -3.9) * mm, "end": v(-37.4, -3.85) * mm});
            skLineSegment(sketch, "E6090", {"start": v(-37.4, -3.85) * mm, "end": v(-37.3, -3.81) * mm});
            skLineSegment(sketch, "E6091", {"start": v(-37.3, -3.81) * mm, "end": v(-37, -3.7) * mm});
            skLineSegment(sketch, "E6092", {"start": v(-37, -3.7) * mm, "end": v(-36.84, -3.66) * mm});
            skLineSegment(sketch, "E6093", {"start": v(-36.84, -3.66) * mm, "end": v(-36.7, -3.62) * mm});
            skLineSegment(sketch, "E6094", {"start": v(-36.7, -3.62) * mm, "end": v(-36.54, -3.59) * mm});
            skLineSegment(sketch, "E6095", {"start": v(-36.54, -3.59) * mm, "end": v(-36.4, -3.56) * mm});
            skLineSegment(sketch, "E6096", {"start": v(-36.4, -3.56) * mm, "end": v(-36.25, -3.55) * mm});
            skLineSegment(sketch, "E6097", {"start": v(-36.25, -3.55) * mm, "end": v(-36.1, -3.54) * mm});
            skLineSegment(sketch, "E6098", {"start": v(-36.1, -3.54) * mm, "end": v(-36.03, -3.53) * mm});
            skLineSegment(sketch, "E6099", {"start": v(-36.03, -3.53) * mm, "end": v(-35.97, -3.53) * mm});
            skLineSegment(sketch, "E6100", {"start": v(-35.97, -3.53) * mm, "end": v(-35.9, -3.53) * mm});
            skLineSegment(sketch, "E6101", {"start": v(-35.9, -3.53) * mm, "end": v(-35.85, -3.53) * mm});
            skLineSegment(sketch, "E6102", {"start": v(-35.85, -3.53) * mm, "end": v(-35.83, -3.53) * mm});
            skLineSegment(sketch, "E6103", {"start": v(-35.83, -3.53) * mm, "end": v(-35.8, -3.53) * mm});
            skLineSegment(sketch, "E6104", {"start": v(-35.8, -3.53) * mm, "end": v(-35.78, -3.53) * mm});
            skLineSegment(sketch, "E6105", {"start": v(-35.78, -3.53) * mm, "end": v(-35.75, -3.53) * mm});
            skLineSegment(sketch, "E6106", {"start": v(-35.75, -3.53) * mm, "end": v(-35.73, -3.54) * mm});
            skLineSegment(sketch, "E6107", {"start": v(-35.73, -3.54) * mm, "end": v(-35.7, -3.54) * mm});
            skLineSegment(sketch, "E6108", {"start": v(-35.7, -3.54) * mm, "end": v(-35.69, -3.54) * mm});
            skLineSegment(sketch, "E6109", {"start": v(-35.69, -3.54) * mm, "end": v(-35.67, -3.55) * mm});
            skLineSegment(sketch, "E6110", {"start": v(-35.67, -3.55) * mm, "end": v(-35.65, -3.55) * mm});
            skLineSegment(sketch, "E6111", {"start": v(-35.65, -3.55) * mm, "end": v(-35.64, -3.56) * mm});
            skLineSegment(sketch, "E6112", {"start": v(-35.64, -3.56) * mm, "end": v(-35.62, -3.56) * mm});
            skLineSegment(sketch, "E6113", {"start": v(-35.62, -3.56) * mm, "end": v(-35.6, -3.57) * mm});
            skLineSegment(sketch, "E6114", {"start": v(-35.6, -3.57) * mm, "end": v(-35.6, -3.57) * mm});
            skLineSegment(sketch, "E6115", {"start": v(-35.6, -3.57) * mm, "end": v(-35.59, -3.57) * mm});
            skLineSegment(sketch, "E6116", {"start": v(-35.59, -3.57) * mm, "end": v(-35.58, -3.58) * mm});
            skLineSegment(sketch, "E6117", {"start": v(-35.58, -3.58) * mm, "end": v(-35.58, -3.58) * mm});
            skLineSegment(sketch, "E6118", {"start": v(-35.58, -3.58) * mm, "end": v(-35.57, -3.58) * mm});
            skLineSegment(sketch, "E6119", {"start": v(-35.57, -3.58) * mm, "end": v(-35.57, -3.59) * mm});
            skLineSegment(sketch, "E6120", {"start": v(-35.57, -3.59) * mm, "end": v(-35.56, -3.6) * mm});
            skLineSegment(sketch, "E6121", {"start": v(-35.56, -3.6) * mm, "end": v(-35.56, -3.6) * mm});
            skLineSegment(sketch, "E6122", {"start": v(-35.56, -3.6) * mm, "end": v(-35.55, -3.6) * mm});
            skLineSegment(sketch, "E6123", {"start": v(-35.55, -3.6) * mm, "end": v(-35.55, -3.6) * mm});
            skLineSegment(sketch, "E6124", {"start": v(-35.55, -3.6) * mm, "end": v(-35.54, -3.61) * mm});
            skLineSegment(sketch, "E6125", {"start": v(-35.54, -3.61) * mm, "end": v(-35.54, -3.62) * mm});
            skLineSegment(sketch, "E6126", {"start": v(-35.54, -3.62) * mm, "end": v(-35.54, -3.62) * mm});
            skLineSegment(sketch, "E6127", {"start": v(-35.54, -3.62) * mm, "end": v(-35.54, -3.63) * mm});
            skLineSegment(sketch, "E6128", {"start": v(-35.54, -3.63) * mm, "end": v(-35.53, -3.63) * mm});
            skLineSegment(sketch, "E6129", {"start": v(-35.53, -3.63) * mm, "end": v(-35.53, -3.63) * mm});
            skLineSegment(sketch, "E6130", {"start": v(-35.53, -3.63) * mm, "end": v(-35.53, -3.64) * mm});
            skLineSegment(sketch, "E6131", {"start": v(-35.53, -3.64) * mm, "end": v(-35.53, -3.64) * mm});
            skLineSegment(sketch, "E6132", {"start": v(-35.53, -3.64) * mm, "end": v(-35.53, -3.65) * mm});
            skLineSegment(sketch, "E6133", {"start": v(-35.53, -3.65) * mm, "end": v(-35.53, -3.65) * mm});
            skLineSegment(sketch, "E6134", {"start": v(-35.53, -3.65) * mm, "end": v(-35.53, -3.66) * mm});
            skLineSegment(sketch, "E6135", {"start": v(-35.53, -3.66) * mm, "end": v(-35.53, -3.67) * mm});
            skLineSegment(sketch, "E6136", {"start": v(-35.53, -3.67) * mm, "end": v(-35.53, -3.67) * mm});
            skLineSegment(sketch, "E6137", {"start": v(-35.53, -3.67) * mm, "end": v(-35.53, -3.68) * mm});
            skLineSegment(sketch, "E6138", {"start": v(-35.53, -3.68) * mm, "end": v(-35.53, -3.68) * mm});
            skLineSegment(sketch, "E6139", {"start": v(-35.53, -3.68) * mm, "end": v(-35.53, -3.69) * mm});
            skLineSegment(sketch, "E6140", {"start": v(-35.53, -3.69) * mm, "end": v(-35.53, -3.7) * mm});
            skLineSegment(sketch, "E6141", {"start": v(-35.53, -3.7) * mm, "end": v(-35.53, -3.7) * mm});
            skLineSegment(sketch, "E6142", {"start": v(-35.53, -3.7) * mm, "end": v(-35.54, -3.7) * mm});
            skLineSegment(sketch, "E6143", {"start": v(-35.54, -3.7) * mm, "end": v(-35.54, -3.71) * mm});
            skLineSegment(sketch, "E6144", {"start": v(-35.54, -3.71) * mm, "end": v(-35.54, -3.72) * mm});
            skLineSegment(sketch, "E6145", {"start": v(-35.54, -3.72) * mm, "end": v(-35.55, -3.73) * mm});
            skLineSegment(sketch, "E6146", {"start": v(-35.55, -3.73) * mm, "end": v(-35.55, -3.73) * mm});
            skLineSegment(sketch, "E6147", {"start": v(-35.55, -3.73) * mm, "end": v(-35.56, -3.74) * mm});
            skLineSegment(sketch, "E6148", {"start": v(-35.56, -3.74) * mm, "end": v(-35.56, -3.74) * mm});
            skLineSegment(sketch, "E6149", {"start": v(-35.56, -3.74) * mm, "end": v(-35.56, -3.75) * mm});
            skLineSegment(sketch, "E6150", {"start": v(-35.56, -3.75) * mm, "end": v(-35.57, -3.75) * mm});
            skLineSegment(sketch, "E6151", {"start": v(-35.57, -3.75) * mm, "end": v(-35.6, -3.77) * mm});
            skLineSegment(sketch, "E6152", {"start": v(-35.6, -3.77) * mm, "end": v(-35.62, -3.8) * mm});
            skLineSegment(sketch, "E6153", {"start": v(-35.62, -3.8) * mm, "end": v(-35.64, -3.8) * mm});
            skLineSegment(sketch, "E6154", {"start": v(-35.64, -3.8) * mm, "end": v(-35.67, -3.82) * mm});
            skLineSegment(sketch, "E6155", {"start": v(-35.67, -3.82) * mm, "end": v(-35.7, -3.84) * mm});
            skLineSegment(sketch, "E6156", {"start": v(-35.7, -3.84) * mm, "end": v(-35.76, -3.87) * mm});
            skLineSegment(sketch, "E6157", {"start": v(-35.76, -3.87) * mm, "end": v(-35.79, -3.88) * mm});
            skLineSegment(sketch, "E6158", {"start": v(-35.79, -3.88) * mm, "end": v(-35.86, -3.91) * mm});
            skLineSegment(sketch, "E6159", {"start": v(-35.86, -3.91) * mm, "end": v(-35.92, -3.94) * mm});
            skLineSegment(sketch, "E6160", {"start": v(-35.92, -3.94) * mm, "end": v(-35.99, -3.96) * mm});
            skLineSegment(sketch, "E6161", {"start": v(-35.99, -3.96) * mm, "end": v(-36.05, -3.99) * mm});
            skLineSegment(sketch, "E6162", {"start": v(-36.05, -3.99) * mm, "end": v(-36.1, -4) * mm});
            skLineSegment(sketch, "E6163", {"start": v(-36.1, -4) * mm, "end": v(-36.16, -4.03) * mm});
            skLineSegment(sketch, "E6164", {"start": v(-36.16, -4.03) * mm, "end": v(-36.22, -4.05) * mm});
            skLineSegment(sketch, "E6165", {"start": v(-36.22, -4.05) * mm, "end": v(-36.26, -4.07) * mm});
            skLineSegment(sketch, "E6166", {"start": v(-36.26, -4.07) * mm, "end": v(-36.35, -4.1) * mm});
            skLineSegment(sketch, "E6167", {"start": v(-36.35, -4.1) * mm, "end": v(-36.39, -4.12) * mm});
            skLineSegment(sketch, "E6168", {"start": v(-36.39, -4.12) * mm, "end": v(-36.42, -4.13) * mm});
            skLineSegment(sketch, "E6169", {"start": v(-36.42, -4.13) * mm, "end": v(-36.46, -4.15) * mm});
            skLineSegment(sketch, "E6170", {"start": v(-36.46, -4.15) * mm, "end": v(-36.5, -4.17) * mm});
            skLineSegment(sketch, "E6171", {"start": v(-36.5, -4.17) * mm, "end": v(-36.52, -4.18) * mm});
            skLineSegment(sketch, "E6172", {"start": v(-36.52, -4.18) * mm, "end": v(-36.55, -4.2) * mm});
            skLineSegment(sketch, "E6173", {"start": v(-36.55, -4.2) * mm, "end": v(-36.57, -4.2) * mm});
            skLineSegment(sketch, "E6174", {"start": v(-36.57, -4.2) * mm, "end": v(-36.58, -4.22) * mm});
            skLineSegment(sketch, "E6175", {"start": v(-36.58, -4.22) * mm, "end": v(-36.59, -4.22) * mm});
            skLineSegment(sketch, "E6176", {"start": v(-36.59, -4.22) * mm, "end": v(-36.6, -4.23) * mm});
            skLineSegment(sketch, "E6177", {"start": v(-36.6, -4.23) * mm, "end": v(-36.6, -4.24) * mm});
            skLineSegment(sketch, "E6178", {"start": v(-36.6, -4.24) * mm, "end": v(-36.61, -4.25) * mm});
            skLineSegment(sketch, "E6179", {"start": v(-36.61, -4.25) * mm, "end": v(-36.62, -4.26) * mm});
            skLineSegment(sketch, "E6180", {"start": v(-36.62, -4.26) * mm, "end": v(-36.63, -4.27) * mm});
            skLineSegment(sketch, "E6181", {"start": v(-36.63, -4.27) * mm, "end": v(-36.63, -4.28) * mm});
            skLineSegment(sketch, "E6182", {"start": v(-36.63, -4.28) * mm, "end": v(-36.64, -4.3) * mm});
            skLineSegment(sketch, "E6183", {"start": v(-36.64, -4.3) * mm, "end": v(-36.64, -4.3) * mm});
            skLineSegment(sketch, "E6184", {"start": v(-36.64, -4.3) * mm, "end": v(-36.65, -4.32) * mm});
            skLineSegment(sketch, "E6185", {"start": v(-36.65, -4.32) * mm, "end": v(-36.65, -4.33) * mm});
            skLineSegment(sketch, "E6186", {"start": v(-36.65, -4.33) * mm, "end": v(-36.65, -4.35) * mm});
            skLineSegment(sketch, "E6187", {"start": v(-36.65, -4.35) * mm, "end": v(-36.65, -4.36) * mm});
            skLineSegment(sketch, "E6188", {"start": v(-36.65, -4.36) * mm, "end": v(-36.65, -4.37) * mm});
            skLineSegment(sketch, "E6189", {"start": v(-36.65, -4.37) * mm, "end": v(-36.65, -4.38) * mm});
            skLineSegment(sketch, "E6190", {"start": v(-36.65, -4.38) * mm, "end": v(-36.65, -4.38) * mm});
            skLineSegment(sketch, "E6191", {"start": v(-36.65, -4.38) * mm, "end": v(-36.65, -4.39) * mm});
            skLineSegment(sketch, "E6192", {"start": v(-36.65, -4.39) * mm, "end": v(-36.65, -4.4) * mm});
            skLineSegment(sketch, "E6193", {"start": v(-36.65, -4.4) * mm, "end": v(-36.65, -4.4) * mm});
            skLineSegment(sketch, "E6194", {"start": v(-36.65, -4.4) * mm, "end": v(-36.64, -4.41) * mm});
            skLineSegment(sketch, "E6195", {"start": v(-36.64, -4.41) * mm, "end": v(-36.64, -4.42) * mm});
            skLineSegment(sketch, "E6196", {"start": v(-36.64, -4.42) * mm, "end": v(-36.64, -4.42) * mm});
            skLineSegment(sketch, "E6197", {"start": v(-36.64, -4.42) * mm, "end": v(-36.63, -4.42) * mm});
            skLineSegment(sketch, "E6198", {"start": v(-36.63, -4.42) * mm, "end": v(-36.63, -4.43) * mm});
            skLineSegment(sketch, "E6199", {"start": v(-36.63, -4.43) * mm, "end": v(-36.62, -4.43) * mm});
            skLineSegment(sketch, "E6200", {"start": v(-36.62, -4.43) * mm, "end": v(-36.62, -4.44) * mm});
            skLineSegment(sketch, "E6201", {"start": v(-36.62, -4.44) * mm, "end": v(-36.61, -4.44) * mm});
            skLineSegment(sketch, "E6202", {"start": v(-36.61, -4.44) * mm, "end": v(-36.6, -4.45) * mm});
            skLineSegment(sketch, "E6203", {"start": v(-36.6, -4.45) * mm, "end": v(-36.6, -4.45) * mm});
            skLineSegment(sketch, "E6204", {"start": v(-36.6, -4.45) * mm, "end": v(-36.59, -4.46) * mm});
            skLineSegment(sketch, "E6205", {"start": v(-36.59, -4.46) * mm, "end": v(-36.58, -4.46) * mm});
            skLineSegment(sketch, "E6206", {"start": v(-36.58, -4.46) * mm, "end": v(-36.57, -4.47) * mm});
            skLineSegment(sketch, "E6207", {"start": v(-36.57, -4.47) * mm, "end": v(-36.55, -4.48) * mm});
            skLineSegment(sketch, "E6208", {"start": v(-36.55, -4.48) * mm, "end": v(-36.53, -4.48) * mm});
            skLineSegment(sketch, "E6209", {"start": v(-36.53, -4.48) * mm, "end": v(-36.51, -4.5) * mm});
            skLineSegment(sketch, "E6210", {"start": v(-36.51, -4.5) * mm, "end": v(-36.49, -4.5) * mm});
            skLineSegment(sketch, "E6211", {"start": v(-36.49, -4.5) * mm, "end": v(-36.47, -4.5) * mm});
            skLineSegment(sketch, "E6212", {"start": v(-36.47, -4.5) * mm, "end": v(-36.44, -4.51) * mm});
            skLineSegment(sketch, "E6213", {"start": v(-36.44, -4.51) * mm, "end": v(-36.42, -4.52) * mm});
            skLineSegment(sketch, "E6214", {"start": v(-36.42, -4.52) * mm, "end": v(-36.4, -4.53) * mm});
            skLineSegment(sketch, "E6215", {"start": v(-36.4, -4.53) * mm, "end": v(-36.36, -4.53) * mm});
            skLineSegment(sketch, "E6216", {"start": v(-36.36, -4.53) * mm, "end": v(-36.33, -4.54) * mm});
            skLineSegment(sketch, "E6217", {"start": v(-36.33, -4.54) * mm, "end": v(-36.3, -4.55) * mm});
            skLineSegment(sketch, "E6218", {"start": v(-36.3, -4.55) * mm, "end": v(-36.23, -4.56) * mm});
            skLineSegment(sketch, "E6219", {"start": v(-36.23, -4.56) * mm, "end": v(-36.16, -4.57) * mm});
            skLineSegment(sketch, "E6220", {"start": v(-36.16, -4.57) * mm, "end": v(-36.08, -4.58) * mm});
            skLineSegment(sketch, "E6221", {"start": v(-36.08, -4.58) * mm, "end": v(-36, -4.6) * mm});
            skLineSegment(sketch, "E6222", {"start": v(-36, -4.6) * mm, "end": v(-35.9, -4.6) * mm});
            skLineSegment(sketch, "E6223", {"start": v(-35.9, -4.6) * mm, "end": v(-35.8, -4.61) * mm});
            skLineSegment(sketch, "E6224", {"start": v(-35.8, -4.61) * mm, "end": v(-35.7, -4.62) * mm});
            skLineSegment(sketch, "E6225", {"start": v(-35.7, -4.62) * mm, "end": v(-35.6, -4.63) * mm});
            skLineSegment(sketch, "E6226", {"start": v(-35.6, -4.63) * mm, "end": v(-35.48, -4.63) * mm});
            skLineSegment(sketch, "E6227", {"start": v(-35.48, -4.63) * mm, "end": v(-35.37, -4.64) * mm});
            skLineSegment(sketch, "E6228", {"start": v(-35.37, -4.64) * mm, "end": v(-35.24, -4.65) * mm});
            skLineSegment(sketch, "E6229", {"start": v(-35.24, -4.65) * mm, "end": v(-35.1, -4.65) * mm});
            skLineSegment(sketch, "E6230", {"start": v(-35.1, -4.65) * mm, "end": v(-34.83, -4.66) * mm});
            skLineSegment(sketch, "E6231", {"start": v(-34.83, -4.66) * mm, "end": v(-34.52, -4.67) * mm});
            skLineSegment(sketch, "E6232", {"start": v(-34.52, -4.67) * mm, "end": v(-34.2, -4.67) * mm});
            skLineSegment(sketch, "E6233", {"start": v(-34.2, -4.67) * mm, "end": v(-33.85, -4.68) * mm});
            skLineSegment(sketch, "E6234", {"start": v(-33.85, -4.68) * mm, "end": v(-33.66, -4.68) * mm});
            skLineSegment(sketch, "E6235", {"start": v(-33.66, -4.68) * mm, "end": v(-33.03, -4.67) * mm});
            skLineSegment(sketch, "E6236", {"start": v(-33.03, -4.67) * mm, "end": v(-32.42, -4.67) * mm});
            skLineSegment(sketch, "E6237", {"start": v(-32.42, -4.67) * mm, "end": v(-31.84, -4.65) * mm});
            skLineSegment(sketch, "E6238", {"start": v(-31.84, -4.65) * mm, "end": v(-31.3, -4.63) * mm});
            skLineSegment(sketch, "E6239", {"start": v(-31.3, -4.63) * mm, "end": v(-30.77, -4.6) * mm});
            skLineSegment(sketch, "E6240", {"start": v(-30.77, -4.6) * mm, "end": v(-30.29, -4.57) * mm});
            skLineSegment(sketch, "E6241", {"start": v(-30.29, -4.57) * mm, "end": v(-29.83, -4.53) * mm});
            skLineSegment(sketch, "E6242", {"start": v(-29.83, -4.53) * mm, "end": v(-29.4, -4.49) * mm});
            skLineSegment(sketch, "E6243", {"start": v(-29.4, -4.49) * mm, "end": v(-28.59, -4.38) * mm});
            skLineSegment(sketch, "E6244", {"start": v(-28.59, -4.38) * mm, "end": v(-27.83, -4.23) * mm});
            skLineSegment(sketch, "E6245", {"start": v(-27.83, -4.23) * mm, "end": v(-27.12, -4.04) * mm});
            skLineSegment(sketch, "E6246", {"start": v(-27.12, -4.04) * mm, "end": v(-26.78, -3.93) * mm});
            skLineSegment(sketch, "E6247", {"start": v(-26.78, -3.93) * mm, "end": v(-26.46, -3.81) * mm});
            skLineSegment(sketch, "E6248", {"start": v(-26.46, -3.81) * mm, "end": v(-25.84, -3.54) * mm});
            skLineSegment(sketch, "E6249", {"start": v(-25.84, -3.54) * mm, "end": v(-25.25, -3.22) * mm});
            skLineSegment(sketch, "E6250", {"start": v(-25.25, -3.22) * mm, "end": v(-24.68, -2.86) * mm});
            skLineSegment(sketch, "E6251", {"start": v(-24.68, -2.86) * mm, "end": v(-24.15, -2.45) * mm});
            skLineSegment(sketch, "E6252", {"start": v(-14.9, -2.6) * mm, "end": v(-14.9, -2.96) * mm});
            skLineSegment(sketch, "E6253", {"start": v(-14.9, -2.96) * mm, "end": v(-14.9, -3.16) * mm});
            skLineSegment(sketch, "E6254", {"start": v(-14.9, -3.16) * mm, "end": v(-14.9, -3.26) * mm});
            skLineSegment(sketch, "E6255", {"start": v(-14.9, -3.26) * mm, "end": v(-14.88, -3.36) * mm});
            skLineSegment(sketch, "E6256", {"start": v(-14.88, -3.36) * mm, "end": v(-14.87, -3.45) * mm});
            skLineSegment(sketch, "E6257", {"start": v(-14.87, -3.45) * mm, "end": v(-14.85, -3.54) * mm});
            skLineSegment(sketch, "E6258", {"start": v(-14.85, -3.54) * mm, "end": v(-14.83, -3.63) * mm});
            skLineSegment(sketch, "E6259", {"start": v(-14.83, -3.63) * mm, "end": v(-14.8, -3.72) * mm});
            skLineSegment(sketch, "E6260", {"start": v(-14.8, -3.72) * mm, "end": v(-14.78, -3.8) * mm});
            skLineSegment(sketch, "E6261", {"start": v(-14.78, -3.8) * mm, "end": v(-14.74, -3.88) * mm});
            skLineSegment(sketch, "E6262", {"start": v(-14.74, -3.88) * mm, "end": v(-14.7, -3.95) * mm});
            skLineSegment(sketch, "E6263", {"start": v(-14.7, -3.95) * mm, "end": v(-14.67, -4.03) * mm});
            skLineSegment(sketch, "E6264", {"start": v(-14.67, -4.03) * mm, "end": v(-14.63, -4.1) * mm});
            skLineSegment(sketch, "E6265", {"start": v(-14.63, -4.1) * mm, "end": v(-14.59, -4.16) * mm});
            skLineSegment(sketch, "E6266", {"start": v(-14.59, -4.16) * mm, "end": v(-14.54, -4.23) * mm});
            skLineSegment(sketch, "E6267", {"start": v(-14.54, -4.23) * mm, "end": v(-14.49, -4.29) * mm});
            skLineSegment(sketch, "E6268", {"start": v(-14.49, -4.29) * mm, "end": v(-14.44, -4.34) * mm});
            skLineSegment(sketch, "E6269", {"start": v(-14.44, -4.34) * mm, "end": v(-14.38, -4.4) * mm});
            skLineSegment(sketch, "E6270", {"start": v(-14.38, -4.4) * mm, "end": v(-14.32, -4.45) * mm});
            skLineSegment(sketch, "E6271", {"start": v(-14.32, -4.45) * mm, "end": v(-14.26, -4.5) * mm});
            skLineSegment(sketch, "E6272", {"start": v(-14.26, -4.5) * mm, "end": v(-14.2, -4.54) * mm});
            skLineSegment(sketch, "E6273", {"start": v(-14.2, -4.54) * mm, "end": v(-14.14, -4.58) * mm});
            skLineSegment(sketch, "E6274", {"start": v(-14.14, -4.58) * mm, "end": v(-14.07, -4.61) * mm});
            skLineSegment(sketch, "E6275", {"start": v(-14.07, -4.61) * mm, "end": v(-14, -4.65) * mm});
            skLineSegment(sketch, "E6276", {"start": v(-14, -4.65) * mm, "end": v(-13.93, -4.67) * mm});
            skLineSegment(sketch, "E6277", {"start": v(-13.93, -4.67) * mm, "end": v(-13.86, -4.7) * mm});
            skLineSegment(sketch, "E6278", {"start": v(-13.86, -4.7) * mm, "end": v(-13.79, -4.72) * mm});
            skLineSegment(sketch, "E6279", {"start": v(-13.79, -4.72) * mm, "end": v(-13.71, -4.73) * mm});
            skLineSegment(sketch, "E6280", {"start": v(-13.71, -4.73) * mm, "end": v(-13.64, -4.75) * mm});
            skLineSegment(sketch, "E6281", {"start": v(-13.64, -4.75) * mm, "end": v(-13.56, -4.76) * mm});
            skLineSegment(sketch, "E6282", {"start": v(-13.56, -4.76) * mm, "end": v(-13.47, -4.76) * mm});
            skLineSegment(sketch, "E6283", {"start": v(-13.47, -4.76) * mm, "end": v(-13.4, -4.76) * mm});
            skLineSegment(sketch, "E6284", {"start": v(-13.4, -4.76) * mm, "end": v(-13.21, -4.76) * mm});
            skLineSegment(sketch, "E6285", {"start": v(-13.21, -4.76) * mm, "end": v(-13.03, -4.74) * mm});
            skLineSegment(sketch, "E6286", {"start": v(-13.03, -4.74) * mm, "end": v(-12.85, -4.72) * mm});
            skLineSegment(sketch, "E6287", {"start": v(-12.85, -4.72) * mm, "end": v(-12.67, -4.68) * mm});
            skLineSegment(sketch, "E6288", {"start": v(-12.67, -4.68) * mm, "end": v(-12.49, -4.63) * mm});
            skLineSegment(sketch, "E6289", {"start": v(-12.49, -4.63) * mm, "end": v(-12.3, -4.58) * mm});
            skLineSegment(sketch, "E6290", {"start": v(-12.3, -4.58) * mm, "end": v(-12.12, -4.5) * mm});
            skLineSegment(sketch, "E6291", {"start": v(-12.12, -4.5) * mm, "end": v(-11.93, -4.43) * mm});
            skLineSegment(sketch, "E6292", {"start": v(-11.93, -4.43) * mm, "end": v(-11.55, -4.25) * mm});
            skLineSegment(sketch, "E6293", {"start": v(-11.55, -4.25) * mm, "end": v(-11.17, -4.04) * mm});
            skLineSegment(sketch, "E6294", {"start": v(-11.17, -4.04) * mm, "end": v(-10.79, -3.81) * mm});
            skLineSegment(sketch, "E6295", {"start": v(-10.79, -3.81) * mm, "end": v(-10.41, -3.55) * mm});
            skLineSegment(sketch, "E6296", {"start": v(-10.41, -3.55) * mm, "end": v(-10.22, -3.4) * mm});
            skLineSegment(sketch, "E6297", {"start": v(-10.22, -3.4) * mm, "end": v(-10.01, -3.25) * mm});
            skLineSegment(sketch, "E6298", {"start": v(-10.01, -3.25) * mm, "end": v(-9.8, -3.08) * mm});
            skLineSegment(sketch, "E6299", {"start": v(-9.8, -3.08) * mm, "end": v(-9.58, -2.9) * mm});
            skLineSegment(sketch, "E6300", {"start": v(-9.58, -2.9) * mm, "end": v(-9.34, -2.72) * mm});
            skLineSegment(sketch, "E6301", {"start": v(-9.34, -2.72) * mm, "end": v(-9.1, -2.51) * mm});
            skLineSegment(sketch, "E6302", {"start": v(-9.1, -2.51) * mm, "end": v(-8.84, -2.3) * mm});
            skLineSegment(sketch, "E6303", {"start": v(-8.84, -2.3) * mm, "end": v(-8.58, -2.07) * mm});
            skLineSegment(sketch, "E6304", {"start": v(-8.58, -2.07) * mm, "end": v(-8.58, -2.96) * mm});
            skLineSegment(sketch, "E6305", {"start": v(-8.58, -2.96) * mm, "end": v(-8.98, -3.43) * mm});
            skLineSegment(sketch, "E6306", {"start": v(-8.98, -3.43) * mm, "end": v(-9.38, -3.88) * mm});
            skLineSegment(sketch, "E6307", {"start": v(-9.38, -3.88) * mm, "end": v(-9.77, -4.3) * mm});
            skLineSegment(sketch, "E6308", {"start": v(-9.77, -4.3) * mm, "end": v(-10.16, -4.7) * mm});
            skLineSegment(sketch, "E6309", {"start": v(-10.16, -4.7) * mm, "end": v(-10.54, -5.06) * mm});
            skLineSegment(sketch, "E6310", {"start": v(-10.54, -5.06) * mm, "end": v(-10.91, -5.4) * mm});
            skLineSegment(sketch, "E6311", {"start": v(-10.91, -5.4) * mm, "end": v(-11.28, -5.7) * mm});
            skLineSegment(sketch, "E6312", {"start": v(-11.28, -5.7) * mm, "end": v(-11.64, -5.98) * mm});
            skLineSegment(sketch, "E6313", {"start": v(-11.64, -5.98) * mm, "end": v(-12, -6.22) * mm});
            skLineSegment(sketch, "E6314", {"start": v(-12, -6.22) * mm, "end": v(-12.36, -6.43) * mm});
            skLineSegment(sketch, "E6315", {"start": v(-12.36, -6.43) * mm, "end": v(-12.72, -6.61) * mm});
            skLineSegment(sketch, "E6316", {"start": v(-12.72, -6.61) * mm, "end": v(-13.08, -6.76) * mm});
            skLineSegment(sketch, "E6317", {"start": v(-13.08, -6.76) * mm, "end": v(-13.45, -6.87) * mm});
            skLineSegment(sketch, "E6318", {"start": v(-13.45, -6.87) * mm, "end": v(-13.81, -6.95) * mm});
            skLineSegment(sketch, "E6319", {"start": v(-13.81, -6.95) * mm, "end": v(-14, -6.98) * mm});
            skLineSegment(sketch, "E6320", {"start": v(-14, -6.98) * mm, "end": v(-14.18, -7) * mm});
            skLineSegment(sketch, "E6321", {"start": v(-14.18, -7) * mm, "end": v(-14.36, -7.02) * mm});
            skLineSegment(sketch, "E6322", {"start": v(-14.36, -7.02) * mm, "end": v(-14.55, -7.02) * mm});
            skLineSegment(sketch, "E6323", {"start": v(-14.55, -7.02) * mm, "end": v(-14.7, -7.02) * mm});
            skLineSegment(sketch, "E6324", {"start": v(-14.7, -7.02) * mm, "end": v(-14.86, -7) * mm});
            skLineSegment(sketch, "E6325", {"start": v(-14.86, -7) * mm, "end": v(-15.01, -6.98) * mm});
            skLineSegment(sketch, "E6326", {"start": v(-15.01, -6.98) * mm, "end": v(-15.16, -6.96) * mm});
            skLineSegment(sketch, "E6327", {"start": v(-15.16, -6.96) * mm, "end": v(-15.3, -6.92) * mm});
            skLineSegment(sketch, "E6328", {"start": v(-15.3, -6.92) * mm, "end": v(-15.44, -6.88) * mm});
            skLineSegment(sketch, "E6329", {"start": v(-15.44, -6.88) * mm, "end": v(-15.57, -6.83) * mm});
            skLineSegment(sketch, "E6330", {"start": v(-15.57, -6.83) * mm, "end": v(-15.7, -6.77) * mm});
            skLineSegment(sketch, "E6331", {"start": v(-15.7, -6.77) * mm, "end": v(-15.83, -6.7) * mm});
            skLineSegment(sketch, "E6332", {"start": v(-15.83, -6.7) * mm, "end": v(-15.95, -6.63) * mm});
            skLineSegment(sketch, "E6333", {"start": v(-15.95, -6.63) * mm, "end": v(-16.06, -6.55) * mm});
            skLineSegment(sketch, "E6334", {"start": v(-16.06, -6.55) * mm, "end": v(-16.18, -6.46) * mm});
            skLineSegment(sketch, "E6335", {"start": v(-16.18, -6.46) * mm, "end": v(-16.28, -6.36) * mm});
            skLineSegment(sketch, "E6336", {"start": v(-16.28, -6.36) * mm, "end": v(-16.39, -6.26) * mm});
            skLineSegment(sketch, "E6337", {"start": v(-16.39, -6.26) * mm, "end": v(-16.49, -6.14) * mm});
            skLineSegment(sketch, "E6338", {"start": v(-16.49, -6.14) * mm, "end": v(-16.59, -6.02) * mm});
            skLineSegment(sketch, "E6339", {"start": v(-16.59, -6.02) * mm, "end": v(-16.68, -5.9) * mm});
            skLineSegment(sketch, "E6340", {"start": v(-16.68, -5.9) * mm, "end": v(-16.76, -5.76) * mm});
            skLineSegment(sketch, "E6341", {"start": v(-16.76, -5.76) * mm, "end": v(-16.84, -5.62) * mm});
            skLineSegment(sketch, "E6342", {"start": v(-16.84, -5.62) * mm, "end": v(-16.91, -5.48) * mm});
            skLineSegment(sketch, "E6343", {"start": v(-16.91, -5.48) * mm, "end": v(-16.98, -5.33) * mm});
            skLineSegment(sketch, "E6344", {"start": v(-16.98, -5.33) * mm, "end": v(-17.04, -5.17) * mm});
            skLineSegment(sketch, "E6345", {"start": v(-17.04, -5.17) * mm, "end": v(-17.1, -5) * mm});
            skLineSegment(sketch, "E6346", {"start": v(-17.1, -5) * mm, "end": v(-17.15, -4.84) * mm});
            skLineSegment(sketch, "E6347", {"start": v(-17.15, -4.84) * mm, "end": v(-17.2, -4.67) * mm});
            skLineSegment(sketch, "E6348", {"start": v(-17.2, -4.67) * mm, "end": v(-17.23, -4.49) * mm});
            skLineSegment(sketch, "E6349", {"start": v(-17.23, -4.49) * mm, "end": v(-17.3, -4.11) * mm});
            skLineSegment(sketch, "E6350", {"start": v(-17.3, -4.11) * mm, "end": v(-17.33, -3.71) * mm});
            skLineSegment(sketch, "E6351", {"start": v(-17.33, -3.71) * mm, "end": v(-17.34, -3.29) * mm});
            skLineSegment(sketch, "E6352", {"start": v(-17.34, -3.29) * mm, "end": v(-17.33, -2.91) * mm});
            skLineSegment(sketch, "E6353", {"start": v(-17.33, -2.91) * mm, "end": v(-17.3, -2.55) * mm});
            skLineSegment(sketch, "E6354", {"start": v(-17.3, -2.55) * mm, "end": v(-17.24, -2.2) * mm});
            skLineSegment(sketch, "E6355", {"start": v(-17.24, -2.2) * mm, "end": v(-17.16, -1.84) * mm});
            skLineSegment(sketch, "E6356", {"start": v(-17.16, -1.84) * mm, "end": v(-17.06, -1.5) * mm});
            skLineSegment(sketch, "E6357", {"start": v(-17.06, -1.5) * mm, "end": v(-16.94, -1.17) * mm});
            skLineSegment(sketch, "E6358", {"start": v(-16.94, -1.17) * mm, "end": v(-16.8, -0.85) * mm});
            skLineSegment(sketch, "E6359", {"start": v(-16.8, -0.85) * mm, "end": v(-16.63, -0.54) * mm});
            skLineSegment(sketch, "E6360", {"start": v(-16.63, -0.54) * mm, "end": v(-16.44, -0.23) * mm});
            skLineSegment(sketch, "E6361", {"start": v(-16.44, -0.23) * mm, "end": v(-16.22, 0.09) * mm});
            skLineSegment(sketch, "E6362", {"start": v(-16.22, 0.09) * mm, "end": v(-15.97, 0.4) * mm});
            skLineSegment(sketch, "E6363", {"start": v(-15.97, 0.4) * mm, "end": v(-15.7, 0.73) * mm});
            skLineSegment(sketch, "E6364", {"start": v(-15.7, 0.73) * mm, "end": v(-15.4, 1.06) * mm});
            skLineSegment(sketch, "E6365", {"start": v(-15.4, 1.06) * mm, "end": v(-15.06, 1.4) * mm});
            skLineSegment(sketch, "E6366", {"start": v(-15.06, 1.4) * mm, "end": v(-14.7, 1.73) * mm});
            skLineSegment(sketch, "E6367", {"start": v(-14.7, 1.73) * mm, "end": v(-14.32, 2.07) * mm});
            skLineSegment(sketch, "E6368", {"start": v(-14.32, 2.07) * mm, "end": v(-13.77, 2.52) * mm});
            skLineSegment(sketch, "E6369", {"start": v(-13.77, 2.52) * mm, "end": v(-13.22, 2.9) * mm});
            skLineSegment(sketch, "E6370", {"start": v(-13.22, 2.9) * mm, "end": v(-12.95, 3.07) * mm});
            skLineSegment(sketch, "E6371", {"start": v(-12.95, 3.07) * mm, "end": v(-12.68, 3.22) * mm});
            skLineSegment(sketch, "E6372", {"start": v(-12.68, 3.22) * mm, "end": v(-12.4, 3.37) * mm});
            skLineSegment(sketch, "E6373", {"start": v(-12.4, 3.37) * mm, "end": v(-12.13, 3.5) * mm});
            skLineSegment(sketch, "E6374", {"start": v(-12.13, 3.5) * mm, "end": v(-11.86, 3.6) * mm});
            skLineSegment(sketch, "E6375", {"start": v(-11.86, 3.6) * mm, "end": v(-11.6, 3.7) * mm});
            skLineSegment(sketch, "E6376", {"start": v(-11.6, 3.7) * mm, "end": v(-11.35, 3.78) * mm});
            skLineSegment(sketch, "E6377", {"start": v(-11.35, 3.78) * mm, "end": v(-11.1, 3.85) * mm});
            skLineSegment(sketch, "E6378", {"start": v(-11.1, 3.85) * mm, "end": v(-10.87, 3.9) * mm});
            skLineSegment(sketch, "E6379", {"start": v(-10.87, 3.9) * mm, "end": v(-10.64, 3.94) * mm});
            skLineSegment(sketch, "E6380", {"start": v(-10.64, 3.94) * mm, "end": v(-10.41, 3.96) * mm});
            skLineSegment(sketch, "E6381", {"start": v(-10.41, 3.96) * mm, "end": v(-10.2, 3.97) * mm});
            skLineSegment(sketch, "E6382", {"start": v(-10.2, 3.97) * mm, "end": v(-10.03, 3.96) * mm});
            skLineSegment(sketch, "E6383", {"start": v(-10.03, 3.96) * mm, "end": v(-9.87, 3.95) * mm});
            skLineSegment(sketch, "E6384", {"start": v(-9.87, 3.95) * mm, "end": v(-9.8, 3.94) * mm});
            skLineSegment(sketch, "E6385", {"start": v(-9.8, 3.94) * mm, "end": v(-9.73, 3.92) * mm});
            skLineSegment(sketch, "E6386", {"start": v(-9.73, 3.92) * mm, "end": v(-9.66, 3.9) * mm});
            skLineSegment(sketch, "E6387", {"start": v(-9.66, 3.9) * mm, "end": v(-9.59, 3.89) * mm});
            skLineSegment(sketch, "E6388", {"start": v(-9.59, 3.89) * mm, "end": v(-9.52, 3.87) * mm});
            skLineSegment(sketch, "E6389", {"start": v(-9.52, 3.87) * mm, "end": v(-9.46, 3.84) * mm});
            skLineSegment(sketch, "E6390", {"start": v(-9.46, 3.84) * mm, "end": v(-9.4, 3.82) * mm});
            skLineSegment(sketch, "E6391", {"start": v(-9.4, 3.82) * mm, "end": v(-9.34, 3.8) * mm});
            skLineSegment(sketch, "E6392", {"start": v(-9.34, 3.8) * mm, "end": v(-9.28, 3.76) * mm});
            skLineSegment(sketch, "E6393", {"start": v(-9.28, 3.76) * mm, "end": v(-9.23, 3.73) * mm});
            skLineSegment(sketch, "E6394", {"start": v(-9.23, 3.73) * mm, "end": v(-9.17, 3.69) * mm});
            skLineSegment(sketch, "E6395", {"start": v(-9.17, 3.69) * mm, "end": v(-9.12, 3.65) * mm});
            skLineSegment(sketch, "E6396", {"start": v(-9.12, 3.65) * mm, "end": v(-9.08, 3.61) * mm});
            skLineSegment(sketch, "E6397", {"start": v(-9.08, 3.61) * mm, "end": v(-9.03, 3.57) * mm});
            skLineSegment(sketch, "E6398", {"start": v(-9.03, 3.57) * mm, "end": v(-8.99, 3.53) * mm});
            skLineSegment(sketch, "E6399", {"start": v(-8.99, 3.53) * mm, "end": v(-8.95, 3.48) * mm});
            skLineSegment(sketch, "E6400", {"start": v(-8.95, 3.48) * mm, "end": v(-8.91, 3.43) * mm});
            skLineSegment(sketch, "E6401", {"start": v(-8.91, 3.43) * mm, "end": v(-8.88, 3.38) * mm});
            skLineSegment(sketch, "E6402", {"start": v(-8.88, 3.38) * mm, "end": v(-8.85, 3.32) * mm});
            skLineSegment(sketch, "E6403", {"start": v(-8.85, 3.32) * mm, "end": v(-8.82, 3.27) * mm});
            skLineSegment(sketch, "E6404", {"start": v(-8.82, 3.27) * mm, "end": v(-8.8, 3.2) * mm});
            skLineSegment(sketch, "E6405", {"start": v(-8.8, 3.2) * mm, "end": v(-8.78, 3.15) * mm});
            skLineSegment(sketch, "E6406", {"start": v(-8.78, 3.15) * mm, "end": v(-8.76, 3.08) * mm});
            skLineSegment(sketch, "E6407", {"start": v(-8.76, 3.08) * mm, "end": v(-8.74, 3.02) * mm});
            skLineSegment(sketch, "E6408", {"start": v(-8.74, 3.02) * mm, "end": v(-8.73, 2.95) * mm});
            skLineSegment(sketch, "E6409", {"start": v(-8.73, 2.95) * mm, "end": v(-8.73, 2.88) * mm});
            skLineSegment(sketch, "E6410", {"start": v(-8.73, 2.88) * mm, "end": v(-8.72, 2.8) * mm});
            skLineSegment(sketch, "E6411", {"start": v(-8.72, 2.8) * mm, "end": v(-8.72, 2.73) * mm});
            skLineSegment(sketch, "E6412", {"start": v(-8.72, 2.73) * mm, "end": v(-8.72, 2.61) * mm});
            skLineSegment(sketch, "E6413", {"start": v(-8.72, 2.61) * mm, "end": v(-8.73, 2.5) * mm});
            skLineSegment(sketch, "E6414", {"start": v(-8.73, 2.5) * mm, "end": v(-8.74, 2.38) * mm});
            skLineSegment(sketch, "E6415", {"start": v(-8.74, 2.38) * mm, "end": v(-8.76, 2.27) * mm});
            skLineSegment(sketch, "E6416", {"start": v(-8.76, 2.27) * mm, "end": v(-8.79, 2.16) * mm});
            skLineSegment(sketch, "E6417", {"start": v(-8.79, 2.16) * mm, "end": v(-8.82, 2.04) * mm});
            skLineSegment(sketch, "E6418", {"start": v(-8.82, 2.04) * mm, "end": v(-8.85, 1.93) * mm});
            skLineSegment(sketch, "E6419", {"start": v(-8.85, 1.93) * mm, "end": v(-8.89, 1.81) * mm});
            skLineSegment(sketch, "E6420", {"start": v(-8.89, 1.81) * mm, "end": v(-8.99, 1.59) * mm});
            skLineSegment(sketch, "E6421", {"start": v(-8.99, 1.59) * mm, "end": v(-9.1, 1.36) * mm});
            skLineSegment(sketch, "E6422", {"start": v(-9.1, 1.36) * mm, "end": v(-9.24, 1.13) * mm});
            skLineSegment(sketch, "E6423", {"start": v(-9.24, 1.13) * mm, "end": v(-9.4, 0.9) * mm});
            skLineSegment(sketch, "E6424", {"start": v(-9.4, 0.9) * mm, "end": v(-9.58, 0.68) * mm});
            skLineSegment(sketch, "E6425", {"start": v(-9.58, 0.68) * mm, "end": v(-9.78, 0.46) * mm});
            skLineSegment(sketch, "E6426", {"start": v(-9.78, 0.46) * mm, "end": v(-10.01, 0.23) * mm});
            skLineSegment(sketch, "E6427", {"start": v(-10.01, 0.23) * mm, "end": v(-10.26, 0) * mm});
            skLineSegment(sketch, "E6428", {"start": v(-10.26, 0) * mm, "end": v(-10.53, -0.22) * mm});
            skLineSegment(sketch, "E6429", {"start": v(-10.53, -0.22) * mm, "end": v(-10.83, -0.44) * mm});
            skLineSegment(sketch, "E6430", {"start": v(-10.83, -0.44) * mm, "end": v(-11.14, -0.67) * mm});
            skLineSegment(sketch, "E6431", {"start": v(-11.14, -0.67) * mm, "end": v(-11.48, -0.89) * mm});
            skLineSegment(sketch, "E6432", {"start": v(-11.48, -0.89) * mm, "end": v(-11.84, -1.1) * mm});
            skLineSegment(sketch, "E6433", {"start": v(-11.84, -1.1) * mm, "end": v(-12.22, -1.33) * mm});
            skLineSegment(sketch, "E6434", {"start": v(-12.22, -1.33) * mm, "end": v(-12.61, -1.54) * mm});
            skLineSegment(sketch, "E6435", {"start": v(-12.61, -1.54) * mm, "end": v(-13.47, -1.97) * mm});
            skLineSegment(sketch, "E6436", {"start": v(-13.47, -1.97) * mm, "end": v(-14.4, -2.39) * mm});
            skLineSegment(sketch, "E6437", {"start": v(-14.4, -2.39) * mm, "end": v(-14.9, -2.6) * mm});
            skLineSegment(sketch, "E6438", {"start": v(-14.76, -1.66) * mm, "end": v(-14.14, -1.39) * mm});
            skLineSegment(sketch, "E6439", {"start": v(-14.14, -1.39) * mm, "end": v(-13.56, -1.09) * mm});
            skLineSegment(sketch, "E6440", {"start": v(-13.56, -1.09) * mm, "end": v(-13.28, -0.93) * mm});
            skLineSegment(sketch, "E6441", {"start": v(-13.28, -0.93) * mm, "end": v(-13.02, -0.76) * mm});
            skLineSegment(sketch, "E6442", {"start": v(-13.02, -0.76) * mm, "end": v(-12.77, -0.58) * mm});
            skLineSegment(sketch, "E6443", {"start": v(-12.77, -0.58) * mm, "end": v(-12.54, -0.4) * mm});
            skLineSegment(sketch, "E6444", {"start": v(-12.54, -0.4) * mm, "end": v(-12.31, -0.21) * mm});
            skLineSegment(sketch, "E6445", {"start": v(-12.31, -0.21) * mm, "end": v(-12.1, -0.03) * mm});
            skLineSegment(sketch, "E6446", {"start": v(-12.1, -0.03) * mm, "end": v(-11.91, 0.16) * mm});
            skLineSegment(sketch, "E6447", {"start": v(-11.91, 0.16) * mm, "end": v(-11.73, 0.34) * mm});
            skLineSegment(sketch, "E6448", {"start": v(-11.73, 0.34) * mm, "end": v(-11.57, 0.51) * mm});
            skLineSegment(sketch, "E6449", {"start": v(-11.57, 0.51) * mm, "end": v(-11.43, 0.69) * mm});
            skLineSegment(sketch, "E6450", {"start": v(-11.43, 0.69) * mm, "end": v(-11.3, 0.86) * mm});
            skLineSegment(sketch, "E6451", {"start": v(-11.3, 0.86) * mm, "end": v(-11.18, 1.03) * mm});
            skLineSegment(sketch, "E6452", {"start": v(-11.18, 1.03) * mm, "end": v(-11.12, 1.12) * mm});
            skLineSegment(sketch, "E6453", {"start": v(-11.12, 1.12) * mm, "end": v(-11.07, 1.2) * mm});
            skLineSegment(sketch, "E6454", {"start": v(-11.07, 1.2) * mm, "end": v(-11.03, 1.28) * mm});
            skLineSegment(sketch, "E6455", {"start": v(-11.03, 1.28) * mm, "end": v(-10.98, 1.36) * mm});
            skLineSegment(sketch, "E6456", {"start": v(-10.98, 1.36) * mm, "end": v(-10.94, 1.43) * mm});
            skLineSegment(sketch, "E6457", {"start": v(-10.94, 1.43) * mm, "end": v(-10.9, 1.5) * mm});
            skLineSegment(sketch, "E6458", {"start": v(-10.9, 1.5) * mm, "end": v(-10.87, 1.57) * mm});
            skLineSegment(sketch, "E6459", {"start": v(-10.87, 1.57) * mm, "end": v(-10.84, 1.63) * mm});
            skLineSegment(sketch, "E6460", {"start": v(-10.84, 1.63) * mm, "end": v(-10.82, 1.7) * mm});
            skLineSegment(sketch, "E6461", {"start": v(-10.82, 1.7) * mm, "end": v(-10.8, 1.75) * mm});
            skLineSegment(sketch, "E6462", {"start": v(-10.8, 1.75) * mm, "end": v(-10.77, 1.81) * mm});
            skLineSegment(sketch, "E6463", {"start": v(-10.77, 1.81) * mm, "end": v(-10.76, 1.86) * mm});
            skLineSegment(sketch, "E6464", {"start": v(-10.76, 1.86) * mm, "end": v(-10.75, 1.89) * mm});
            skLineSegment(sketch, "E6465", {"start": v(-10.75, 1.89) * mm, "end": v(-10.75, 1.91) * mm});
            skLineSegment(sketch, "E6466", {"start": v(-10.75, 1.91) * mm, "end": v(-10.74, 1.94) * mm});
            skLineSegment(sketch, "E6467", {"start": v(-10.74, 1.94) * mm, "end": v(-10.74, 1.96) * mm});
            skLineSegment(sketch, "E6468", {"start": v(-10.74, 1.96) * mm, "end": v(-10.73, 1.98) * mm});
            skLineSegment(sketch, "E6469", {"start": v(-10.73, 1.98) * mm, "end": v(-10.73, 2) * mm});
            skLineSegment(sketch, "E6470", {"start": v(-10.73, 2) * mm, "end": v(-10.73, 2.03) * mm});
            skLineSegment(sketch, "E6471", {"start": v(-10.73, 2.03) * mm, "end": v(-10.73, 2.05) * mm});
            skLineSegment(sketch, "E6472", {"start": v(-10.73, 2.05) * mm, "end": v(-10.73, 2.07) * mm});
            skLineSegment(sketch, "E6473", {"start": v(-10.73, 2.07) * mm, "end": v(-10.73, 2.09) * mm});
            skLineSegment(sketch, "E6474", {"start": v(-10.73, 2.09) * mm, "end": v(-10.73, 2.1) * mm});
            skLineSegment(sketch, "E6475", {"start": v(-10.73, 2.1) * mm, "end": v(-10.73, 2.12) * mm});
            skLineSegment(sketch, "E6476", {"start": v(-10.73, 2.12) * mm, "end": v(-10.74, 2.14) * mm});
            skLineSegment(sketch, "E6477", {"start": v(-10.74, 2.14) * mm, "end": v(-10.74, 2.16) * mm});
            skLineSegment(sketch, "E6478", {"start": v(-10.74, 2.16) * mm, "end": v(-10.74, 2.18) * mm});
            skLineSegment(sketch, "E6479", {"start": v(-10.74, 2.18) * mm, "end": v(-10.75, 2.2) * mm});
            skLineSegment(sketch, "E6480", {"start": v(-10.75, 2.2) * mm, "end": v(-10.75, 2.2) * mm});
            skLineSegment(sketch, "E6481", {"start": v(-10.75, 2.2) * mm, "end": v(-10.76, 2.22) * mm});
            skLineSegment(sketch, "E6482", {"start": v(-10.76, 2.22) * mm, "end": v(-10.77, 2.24) * mm});
            skLineSegment(sketch, "E6483", {"start": v(-10.77, 2.24) * mm, "end": v(-10.77, 2.25) * mm});
            skLineSegment(sketch, "E6484", {"start": v(-10.77, 2.25) * mm, "end": v(-10.78, 2.26) * mm});
            skLineSegment(sketch, "E6485", {"start": v(-10.78, 2.26) * mm, "end": v(-10.79, 2.27) * mm});
            skLineSegment(sketch, "E6486", {"start": v(-10.79, 2.27) * mm, "end": v(-10.8, 2.28) * mm});
            skLineSegment(sketch, "E6487", {"start": v(-10.8, 2.28) * mm, "end": v(-10.8, 2.3) * mm});
            skLineSegment(sketch, "E6488", {"start": v(-10.8, 2.3) * mm, "end": v(-10.82, 2.3) * mm});
            skLineSegment(sketch, "E6489", {"start": v(-10.82, 2.3) * mm, "end": v(-10.83, 2.31) * mm});
            skLineSegment(sketch, "E6490", {"start": v(-10.83, 2.31) * mm, "end": v(-10.84, 2.32) * mm});
            skLineSegment(sketch, "E6491", {"start": v(-10.84, 2.32) * mm, "end": v(-10.85, 2.33) * mm});
            skLineSegment(sketch, "E6492", {"start": v(-10.85, 2.33) * mm, "end": v(-10.86, 2.34) * mm});
            skLineSegment(sketch, "E6493", {"start": v(-10.86, 2.34) * mm, "end": v(-10.87, 2.35) * mm});
            skLineSegment(sketch, "E6494", {"start": v(-10.87, 2.35) * mm, "end": v(-10.89, 2.35) * mm});
            skLineSegment(sketch, "E6495", {"start": v(-10.89, 2.35) * mm, "end": v(-10.9, 2.36) * mm});
            skLineSegment(sketch, "E6496", {"start": v(-10.9, 2.36) * mm, "end": v(-10.91, 2.36) * mm});
            skLineSegment(sketch, "E6497", {"start": v(-10.91, 2.36) * mm, "end": v(-10.93, 2.37) * mm});
            skLineSegment(sketch, "E6498", {"start": v(-10.93, 2.37) * mm, "end": v(-10.95, 2.37) * mm});
            skLineSegment(sketch, "E6499", {"start": v(-10.95, 2.37) * mm, "end": v(-10.96, 2.37) * mm});
            skLineSegment(sketch, "E6500", {"start": v(-10.96, 2.37) * mm, "end": v(-10.98, 2.38) * mm});
            skLineSegment(sketch, "E6501", {"start": v(-10.98, 2.38) * mm, "end": v(-11, 2.38) * mm});
            skLineSegment(sketch, "E6502", {"start": v(-11, 2.38) * mm, "end": v(-11.01, 2.38) * mm});
            skLineSegment(sketch, "E6503", {"start": v(-11.01, 2.38) * mm, "end": v(-11.03, 2.38) * mm});
            skLineSegment(sketch, "E6504", {"start": v(-11.03, 2.38) * mm, "end": v(-11.05, 2.38) * mm});
            skLineSegment(sketch, "E6505", {"start": v(-11.05, 2.38) * mm, "end": v(-11.07, 2.38) * mm});
            skLineSegment(sketch, "E6506", {"start": v(-11.07, 2.38) * mm, "end": v(-11.08, 2.38) * mm});
            skLineSegment(sketch, "E6507", {"start": v(-11.08, 2.38) * mm, "end": v(-11.1, 2.37) * mm});
            skLineSegment(sketch, "E6508", {"start": v(-11.1, 2.37) * mm, "end": v(-11.12, 2.37) * mm});
            skLineSegment(sketch, "E6509", {"start": v(-11.12, 2.37) * mm, "end": v(-11.14, 2.37) * mm});
            skLineSegment(sketch, "E6510", {"start": v(-11.14, 2.37) * mm, "end": v(-11.18, 2.36) * mm});
            skLineSegment(sketch, "E6511", {"start": v(-11.18, 2.36) * mm, "end": v(-11.23, 2.35) * mm});
            skLineSegment(sketch, "E6512", {"start": v(-11.23, 2.35) * mm, "end": v(-11.28, 2.33) * mm});
            skLineSegment(sketch, "E6513", {"start": v(-11.28, 2.33) * mm, "end": v(-11.32, 2.31) * mm});
            skLineSegment(sketch, "E6514", {"start": v(-11.32, 2.31) * mm, "end": v(-11.38, 2.3) * mm});
            skLineSegment(sketch, "E6515", {"start": v(-11.38, 2.3) * mm, "end": v(-11.43, 2.27) * mm});
            skLineSegment(sketch, "E6516", {"start": v(-11.43, 2.27) * mm, "end": v(-11.49, 2.25) * mm});
            skLineSegment(sketch, "E6517", {"start": v(-11.49, 2.25) * mm, "end": v(-11.55, 2.22) * mm});
            skLineSegment(sketch, "E6518", {"start": v(-11.55, 2.22) * mm, "end": v(-11.61, 2.2) * mm});
            skLineSegment(sketch, "E6519", {"start": v(-11.61, 2.2) * mm, "end": v(-11.68, 2.16) * mm});
            skLineSegment(sketch, "E6520", {"start": v(-11.68, 2.16) * mm, "end": v(-11.74, 2.12) * mm});
            skLineSegment(sketch, "E6521", {"start": v(-11.74, 2.12) * mm, "end": v(-11.81, 2.09) * mm});
            skLineSegment(sketch, "E6522", {"start": v(-11.81, 2.09) * mm, "end": v(-11.89, 2.05) * mm});
            skLineSegment(sketch, "E6523", {"start": v(-11.89, 2.05) * mm, "end": v(-12.18, 1.87) * mm});
            skLineSegment(sketch, "E6524", {"start": v(-12.18, 1.87) * mm, "end": v(-12.47, 1.66) * mm});
            skLineSegment(sketch, "E6525", {"start": v(-12.47, 1.66) * mm, "end": v(-12.77, 1.43) * mm});
            skLineSegment(sketch, "E6526", {"start": v(-12.77, 1.43) * mm, "end": v(-13.07, 1.18) * mm});
            skLineSegment(sketch, "E6527", {"start": v(-13.07, 1.18) * mm, "end": v(-13.36, 0.9) * mm});
            skLineSegment(sketch, "E6528", {"start": v(-13.36, 0.9) * mm, "end": v(-13.64, 0.6) * mm});
            skLineSegment(sketch, "E6529", {"start": v(-13.64, 0.6) * mm, "end": v(-13.9, 0.27) * mm});
            skLineSegment(sketch, "E6530", {"start": v(-13.9, 0.27) * mm, "end": v(-14.14, -0.08) * mm});
            skLineSegment(sketch, "E6531", {"start": v(-14.14, -0.08) * mm, "end": v(-14.26, -0.26) * mm});
            skLineSegment(sketch, "E6532", {"start": v(-14.26, -0.26) * mm, "end": v(-14.36, -0.45) * mm});
            skLineSegment(sketch, "E6533", {"start": v(-14.36, -0.45) * mm, "end": v(-14.45, -0.64) * mm});
            skLineSegment(sketch, "E6534", {"start": v(-14.45, -0.64) * mm, "end": v(-14.54, -0.84) * mm});
            skLineSegment(sketch, "E6535", {"start": v(-14.54, -0.84) * mm, "end": v(-14.6, -1.03) * mm});
            skLineSegment(sketch, "E6536", {"start": v(-14.6, -1.03) * mm, "end": v(-14.67, -1.24) * mm});
            skLineSegment(sketch, "E6537", {"start": v(-14.67, -1.24) * mm, "end": v(-14.72, -1.44) * mm});
            skLineSegment(sketch, "E6538", {"start": v(-14.72, -1.44) * mm, "end": v(-14.76, -1.66) * mm});
            skLineSegment(sketch, "E6539", {"start": v(-7.06, -3.29) * mm, "end": v(-7.06, -2.28) * mm});
            skLineSegment(sketch, "E6540", {"start": v(-7.06, -2.28) * mm, "end": v(-6.08, -1.2) * mm});
            skLineSegment(sketch, "E6541", {"start": v(-6.08, -1.2) * mm, "end": v(-5.17, -0.14) * mm});
            skLineSegment(sketch, "E6542", {"start": v(-5.17, -0.14) * mm, "end": v(-4.34, 0.87) * mm});
            skLineSegment(sketch, "E6543", {"start": v(-4.34, 0.87) * mm, "end": v(-3.57, 1.86) * mm});
            skLineSegment(sketch, "E6544", {"start": v(-3.57, 1.86) * mm, "end": v(-3.21, 2.33) * mm});
            skLineSegment(sketch, "E6545", {"start": v(-3.21, 2.33) * mm, "end": v(-2.87, 2.78) * mm});
            skLineSegment(sketch, "E6546", {"start": v(-2.87, 2.78) * mm, "end": v(-2.55, 3.2) * mm});
            skLineSegment(sketch, "E6547", {"start": v(-2.55, 3.2) * mm, "end": v(-2.25, 3.6) * mm});
            skLineSegment(sketch, "E6548", {"start": v(-2.25, 3.6) * mm, "end": v(-1.97, 3.97) * mm});
            skLineSegment(sketch, "E6549", {"start": v(-1.97, 3.97) * mm, "end": v(-1.71, 4.32) * mm});
            skLineSegment(sketch, "E6550", {"start": v(-1.71, 4.32) * mm, "end": v(-1.47, 4.64) * mm});
            skLineSegment(sketch, "E6551", {"start": v(-1.47, 4.64) * mm, "end": v(-1.24, 4.94) * mm});
            skLineSegment(sketch, "E6552", {"start": v(-1.24, 4.94) * mm, "end": v(-1.03, 5.21) * mm});
            skLineSegment(sketch, "E6553", {"start": v(-1.03, 5.21) * mm, "end": v(-0.83, 5.47) * mm});
            skLineSegment(sketch, "E6554", {"start": v(-0.83, 5.47) * mm, "end": v(-0.63, 5.7) * mm});
            skLineSegment(sketch, "E6555", {"start": v(-0.63, 5.7) * mm, "end": v(-0.44, 5.91) * mm});
            skLineSegment(sketch, "E6556", {"start": v(-0.44, 5.91) * mm, "end": v(-0.26, 6.1) * mm});
            skLineSegment(sketch, "E6557", {"start": v(-0.26, 6.1) * mm, "end": v(-0.17, 6.19) * mm});
            skLineSegment(sketch, "E6558", {"start": v(-0.17, 6.19) * mm, "end": v(-0.08, 6.27) * mm});
            skLineSegment(sketch, "E6559", {"start": v(-0.08, 6.27) * mm, "end": v(0, 6.35) * mm});
            skLineSegment(sketch, "E6560", {"start": v(0, 6.35) * mm, "end": v(0.1, 6.42) * mm});
            skLineSegment(sketch, "E6561", {"start": v(0.1, 6.42) * mm, "end": v(0.18, 6.48) * mm});
            skLineSegment(sketch, "E6562", {"start": v(0.18, 6.48) * mm, "end": v(0.26, 6.54) * mm});
            skLineSegment(sketch, "E6563", {"start": v(0.26, 6.54) * mm, "end": v(0.34, 6.6) * mm});
            skLineSegment(sketch, "E6564", {"start": v(0.34, 6.6) * mm, "end": v(0.43, 6.65) * mm});
            skLineSegment(sketch, "E6565", {"start": v(0.43, 6.65) * mm, "end": v(0.51, 6.7) * mm});
            skLineSegment(sketch, "E6566", {"start": v(0.51, 6.7) * mm, "end": v(0.6, 6.75) * mm});
            skLineSegment(sketch, "E6567", {"start": v(0.6, 6.75) * mm, "end": v(0.7, 6.8) * mm});
            skLineSegment(sketch, "E6568", {"start": v(0.7, 6.8) * mm, "end": v(0.8, 6.83) * mm});
            skLineSegment(sketch, "E6569", {"start": v(0.8, 6.83) * mm, "end": v(1, 6.9) * mm});
            skLineSegment(sketch, "E6570", {"start": v(1, 6.9) * mm, "end": v(1.2, 6.95) * mm});
            skLineSegment(sketch, "E6571", {"start": v(1.2, 6.95) * mm, "end": v(1.42, 7) * mm});
            skLineSegment(sketch, "E6572", {"start": v(1.42, 7) * mm, "end": v(1.65, 7.01) * mm});
            skLineSegment(sketch, "E6573", {"start": v(1.65, 7.01) * mm, "end": v(1.9, 7.02) * mm});
            skLineSegment(sketch, "E6574", {"start": v(1.9, 7.02) * mm, "end": v(1.95, 7.02) * mm});
            skLineSegment(sketch, "E6575", {"start": v(1.95, 7.02) * mm, "end": v(2, 7.01) * mm});
            skLineSegment(sketch, "E6576", {"start": v(2, 7.01) * mm, "end": v(2.03, 7.01) * mm});
            skLineSegment(sketch, "E6577", {"start": v(2.03, 7.01) * mm, "end": v(2.06, 7) * mm});
            skLineSegment(sketch, "E6578", {"start": v(2.06, 7) * mm, "end": v(2.08, 7) * mm});
            skLineSegment(sketch, "E6579", {"start": v(2.08, 7) * mm, "end": v(2.1, 7) * mm});
            skLineSegment(sketch, "E6580", {"start": v(2.1, 7) * mm, "end": v(2.13, 7) * mm});
            skLineSegment(sketch, "E6581", {"start": v(2.13, 7) * mm, "end": v(2.15, 6.98) * mm});
            skLineSegment(sketch, "E6582", {"start": v(2.15, 6.98) * mm, "end": v(2.17, 6.98) * mm});
            skLineSegment(sketch, "E6583", {"start": v(2.17, 6.98) * mm, "end": v(2.2, 6.97) * mm});
            skLineSegment(sketch, "E6584", {"start": v(2.2, 6.97) * mm, "end": v(2.21, 6.96) * mm});
            skLineSegment(sketch, "E6585", {"start": v(2.21, 6.96) * mm, "end": v(2.23, 6.95) * mm});
            skLineSegment(sketch, "E6586", {"start": v(2.23, 6.95) * mm, "end": v(2.25, 6.94) * mm});
            skLineSegment(sketch, "E6587", {"start": v(2.25, 6.94) * mm, "end": v(2.26, 6.93) * mm});
            skLineSegment(sketch, "E6588", {"start": v(2.26, 6.93) * mm, "end": v(2.28, 6.91) * mm});
            skLineSegment(sketch, "E6589", {"start": v(2.28, 6.91) * mm, "end": v(2.3, 6.9) * mm});
            skLineSegment(sketch, "E6590", {"start": v(2.3, 6.9) * mm, "end": v(2.3, 6.89) * mm});
            skLineSegment(sketch, "E6591", {"start": v(2.3, 6.89) * mm, "end": v(2.32, 6.87) * mm});
            skLineSegment(sketch, "E6592", {"start": v(2.32, 6.87) * mm, "end": v(2.33, 6.86) * mm});
            skLineSegment(sketch, "E6593", {"start": v(2.33, 6.86) * mm, "end": v(2.34, 6.84) * mm});
            skLineSegment(sketch, "E6594", {"start": v(2.34, 6.84) * mm, "end": v(2.35, 6.83) * mm});
            skLineSegment(sketch, "E6595", {"start": v(2.35, 6.83) * mm, "end": v(2.35, 6.8) * mm});
            skLineSegment(sketch, "E6596", {"start": v(2.35, 6.8) * mm, "end": v(2.36, 6.8) * mm});
            skLineSegment(sketch, "E6597", {"start": v(2.36, 6.8) * mm, "end": v(2.37, 6.77) * mm});
            skLineSegment(sketch, "E6598", {"start": v(2.37, 6.77) * mm, "end": v(2.37, 6.75) * mm});
            skLineSegment(sketch, "E6599", {"start": v(2.37, 6.75) * mm, "end": v(2.38, 6.73) * mm});
            skLineSegment(sketch, "E6600", {"start": v(2.38, 6.73) * mm, "end": v(2.38, 6.71) * mm});
            skLineSegment(sketch, "E6601", {"start": v(2.38, 6.71) * mm, "end": v(2.38, 6.69) * mm});
            skLineSegment(sketch, "E6602", {"start": v(2.38, 6.69) * mm, "end": v(2.38, 6.67) * mm});
            skLineSegment(sketch, "E6603", {"start": v(2.38, 6.67) * mm, "end": v(2.38, 6.64) * mm});
            skLineSegment(sketch, "E6604", {"start": v(2.38, 6.64) * mm, "end": v(2.38, 6.62) * mm});
            skLineSegment(sketch, "E6605", {"start": v(2.38, 6.62) * mm, "end": v(2.38, 6.6) * mm});
            skLineSegment(sketch, "E6606", {"start": v(2.38, 6.6) * mm, "end": v(2.38, 6.58) * mm});
            skLineSegment(sketch, "E6607", {"start": v(2.38, 6.58) * mm, "end": v(2.38, 6.56) * mm});
            skLineSegment(sketch, "E6608", {"start": v(2.38, 6.56) * mm, "end": v(2.37, 6.54) * mm});
            skLineSegment(sketch, "E6609", {"start": v(2.37, 6.54) * mm, "end": v(2.36, 6.5) * mm});
            skLineSegment(sketch, "E6610", {"start": v(2.36, 6.5) * mm, "end": v(2.35, 6.45) * mm});
            skLineSegment(sketch, "E6611", {"start": v(2.35, 6.45) * mm, "end": v(2.34, 6.4) * mm});
            skLineSegment(sketch, "E6612", {"start": v(2.34, 6.4) * mm, "end": v(2.32, 6.35) * mm});
            skLineSegment(sketch, "E6613", {"start": v(2.32, 6.35) * mm, "end": v(2.3, 6.3) * mm});
            skLineSegment(sketch, "E6614", {"start": v(2.3, 6.3) * mm, "end": v(2.27, 6.24) * mm});
            skLineSegment(sketch, "E6615", {"start": v(2.27, 6.24) * mm, "end": v(2.24, 6.18) * mm});
            skLineSegment(sketch, "E6616", {"start": v(2.24, 6.18) * mm, "end": v(2.21, 6.12) * mm});
            skLineSegment(sketch, "E6617", {"start": v(2.21, 6.12) * mm, "end": v(2.18, 6.06) * mm});
            skLineSegment(sketch, "E6618", {"start": v(2.18, 6.06) * mm, "end": v(2.14, 6) * mm});
            skLineSegment(sketch, "E6619", {"start": v(2.14, 6) * mm, "end": v(2.1, 5.93) * mm});
            skLineSegment(sketch, "E6620", {"start": v(2.1, 5.93) * mm, "end": v(2.05, 5.86) * mm});
            skLineSegment(sketch, "E6621", {"start": v(2.05, 5.86) * mm, "end": v(1.98, 5.75) * mm});
            skLineSegment(sketch, "E6622", {"start": v(1.98, 5.75) * mm, "end": v(1.77, 5.45) * mm});
            skLineSegment(sketch, "E6623", {"start": v(1.77, 5.45) * mm, "end": v(1.53, 5.15) * mm});
            skLineSegment(sketch, "E6624", {"start": v(1.53, 5.15) * mm, "end": v(1.26, 4.84) * mm});
            skLineSegment(sketch, "E6625", {"start": v(1.26, 4.84) * mm, "end": v(0.97, 4.53) * mm});
            skLineSegment(sketch, "E6626", {"start": v(0.97, 4.53) * mm, "end": v(0.76, 4.32) * mm});
            skLineSegment(sketch, "E6627", {"start": v(0.76, 4.32) * mm, "end": v(0.35, 3.87) * mm});
            skLineSegment(sketch, "E6628", {"start": v(0.35, 3.87) * mm, "end": v(-0.05, 3.36) * mm});
            skLineSegment(sketch, "E6629", {"start": v(-0.05, 3.36) * mm, "end": v(-0.45, 2.8) * mm});
            skLineSegment(sketch, "E6630", {"start": v(-0.45, 2.8) * mm, "end": v(-0.65, 2.5) * mm});
            skLineSegment(sketch, "E6631", {"start": v(-0.65, 2.5) * mm, "end": v(-0.85, 2.18) * mm});
            skLineSegment(sketch, "E6632", {"start": v(-0.85, 2.18) * mm, "end": v(-1.06, 1.84) * mm});
            skLineSegment(sketch, "E6633", {"start": v(-1.06, 1.84) * mm, "end": v(-1.27, 1.49) * mm});
            skLineSegment(sketch, "E6634", {"start": v(-1.27, 1.49) * mm, "end": v(-1.49, 1.1) * mm});
            skLineSegment(sketch, "E6635", {"start": v(-1.49, 1.1) * mm, "end": v(-1.71, 0.71) * mm});
            skLineSegment(sketch, "E6636", {"start": v(-1.71, 0.71) * mm, "end": v(-1.95, 0.3) * mm});
            skLineSegment(sketch, "E6637", {"start": v(-1.95, 0.3) * mm, "end": v(-2.43, -0.61) * mm});
            skLineSegment(sketch, "E6638", {"start": v(-2.43, -0.61) * mm, "end": v(-2.03, -0.3) * mm});
            skLineSegment(sketch, "E6639", {"start": v(-2.03, -0.3) * mm, "end": v(-1.6, 0.05) * mm});
            skLineSegment(sketch, "E6640", {"start": v(-1.6, 0.05) * mm, "end": v(-1.13, 0.42) * mm});
            skLineSegment(sketch, "E6641", {"start": v(-1.13, 0.42) * mm, "end": v(-0.64, 0.82) * mm});
            skLineSegment(sketch, "E6642", {"start": v(-0.64, 0.82) * mm, "end": v(-0.39, 1.02) * mm});
            skLineSegment(sketch, "E6643", {"start": v(-0.39, 1.02) * mm, "end": v(-0.15, 1.21) * mm});
            skLineSegment(sketch, "E6644", {"start": v(-0.15, 1.21) * mm, "end": v(0.08, 1.4) * mm});
            skLineSegment(sketch, "E6645", {"start": v(0.08, 1.4) * mm, "end": v(0.3, 1.56) * mm});
            skLineSegment(sketch, "E6646", {"start": v(0.3, 1.56) * mm, "end": v(0.5, 1.72) * mm});
            skLineSegment(sketch, "E6647", {"start": v(0.5, 1.72) * mm, "end": v(0.68, 1.86) * mm});
            skLineSegment(sketch, "E6648", {"start": v(0.68, 1.86) * mm, "end": v(0.86, 2) * mm});
            skLineSegment(sketch, "E6649", {"start": v(0.86, 2) * mm, "end": v(1.03, 2.12) * mm});
            skLineSegment(sketch, "E6650", {"start": v(1.03, 2.12) * mm, "end": v(1.35, 2.34) * mm});
            skLineSegment(sketch, "E6651", {"start": v(1.35, 2.34) * mm, "end": v(1.67, 2.54) * mm});
            skLineSegment(sketch, "E6652", {"start": v(1.67, 2.54) * mm, "end": v(1.98, 2.72) * mm});
            skLineSegment(sketch, "E6653", {"start": v(1.98, 2.72) * mm, "end": v(2.3, 2.87) * mm});
            skLineSegment(sketch, "E6654", {"start": v(2.3, 2.87) * mm, "end": v(2.46, 2.93) * mm});
            skLineSegment(sketch, "E6655", {"start": v(2.46, 2.93) * mm, "end": v(2.62, 3) * mm});
            skLineSegment(sketch, "E6656", {"start": v(2.62, 3) * mm, "end": v(2.77, 3.04) * mm});
            skLineSegment(sketch, "E6657", {"start": v(2.77, 3.04) * mm, "end": v(2.93, 3.08) * mm});
            skLineSegment(sketch, "E6658", {"start": v(2.93, 3.08) * mm, "end": v(3.1, 3.1) * mm});
            skLineSegment(sketch, "E6659", {"start": v(3.1, 3.1) * mm, "end": v(3.25, 3.13) * mm});
            skLineSegment(sketch, "E6660", {"start": v(3.25, 3.13) * mm, "end": v(3.41, 3.14) * mm});
            skLineSegment(sketch, "E6661", {"start": v(3.41, 3.14) * mm, "end": v(3.57, 3.14) * mm});
            skLineSegment(sketch, "E6662", {"start": v(3.57, 3.14) * mm, "end": v(3.62, 3.14) * mm});
            skLineSegment(sketch, "E6663", {"start": v(3.62, 3.14) * mm, "end": v(3.67, 3.14) * mm});
            skLineSegment(sketch, "E6664", {"start": v(3.67, 3.14) * mm, "end": v(3.71, 3.14) * mm});
            skLineSegment(sketch, "E6665", {"start": v(3.71, 3.14) * mm, "end": v(3.75, 3.14) * mm});
            skLineSegment(sketch, "E6666", {"start": v(3.75, 3.14) * mm, "end": v(3.8, 3.13) * mm});
            skLineSegment(sketch, "E6667", {"start": v(3.8, 3.13) * mm, "end": v(3.83, 3.12) * mm});
            skLineSegment(sketch, "E6668", {"start": v(3.83, 3.12) * mm, "end": v(3.87, 3.12) * mm});
            skLineSegment(sketch, "E6669", {"start": v(3.87, 3.12) * mm, "end": v(3.9, 3.1) * mm});
            skLineSegment(sketch, "E6670", {"start": v(3.9, 3.1) * mm, "end": v(3.93, 3.1) * mm});
            skLineSegment(sketch, "E6671", {"start": v(3.93, 3.1) * mm, "end": v(3.96, 3.09) * mm});
            skLineSegment(sketch, "E6672", {"start": v(3.96, 3.09) * mm, "end": v(3.99, 3.08) * mm});
            skLineSegment(sketch, "E6673", {"start": v(3.99, 3.08) * mm, "end": v(4, 3.07) * mm});
            skLineSegment(sketch, "E6674", {"start": v(4, 3.07) * mm, "end": v(4.01, 3.06) * mm});
            skLineSegment(sketch, "E6675", {"start": v(4.01, 3.06) * mm, "end": v(4.03, 3.06) * mm});
            skLineSegment(sketch, "E6676", {"start": v(4.03, 3.06) * mm, "end": v(4.04, 3.05) * mm});
            skLineSegment(sketch, "E6677", {"start": v(4.04, 3.05) * mm, "end": v(4.05, 3.04) * mm});
            skLineSegment(sketch, "E6678", {"start": v(4.05, 3.04) * mm, "end": v(4.06, 3.03) * mm});
            skLineSegment(sketch, "E6679", {"start": v(4.06, 3.03) * mm, "end": v(4.07, 3.03) * mm});
            skLineSegment(sketch, "E6680", {"start": v(4.07, 3.03) * mm, "end": v(4.07, 3.02) * mm});
            skLineSegment(sketch, "E6681", {"start": v(4.07, 3.02) * mm, "end": v(4.08, 3) * mm});
            skLineSegment(sketch, "E6682", {"start": v(4.08, 3) * mm, "end": v(4.1, 3) * mm});
            skLineSegment(sketch, "E6683", {"start": v(4.1, 3) * mm, "end": v(4.1, 3) * mm});
            skLineSegment(sketch, "E6684", {"start": v(4.1, 3) * mm, "end": v(4.1, 2.98) * mm});
            skLineSegment(sketch, "E6685", {"start": v(4.1, 2.98) * mm, "end": v(4.11, 2.97) * mm});
            skLineSegment(sketch, "E6686", {"start": v(4.11, 2.97) * mm, "end": v(4.12, 2.96) * mm});
            skLineSegment(sketch, "E6687", {"start": v(4.12, 2.96) * mm, "end": v(4.13, 2.95) * mm});
            skLineSegment(sketch, "E6688", {"start": v(4.13, 2.95) * mm, "end": v(4.14, 2.92) * mm});
            skLineSegment(sketch, "E6689", {"start": v(4.14, 2.92) * mm, "end": v(4.15, 2.9) * mm});
            skLineSegment(sketch, "E6690", {"start": v(4.15, 2.9) * mm, "end": v(4.16, 2.87) * mm});
            skLineSegment(sketch, "E6691", {"start": v(4.16, 2.87) * mm, "end": v(4.17, 2.84) * mm});
            skLineSegment(sketch, "E6692", {"start": v(4.17, 2.84) * mm, "end": v(4.18, 2.8) * mm});
            skLineSegment(sketch, "E6693", {"start": v(4.18, 2.8) * mm, "end": v(4.2, 2.77) * mm});
            skLineSegment(sketch, "E6694", {"start": v(4.2, 2.77) * mm, "end": v(4.2, 2.73) * mm});
            skLineSegment(sketch, "E6695", {"start": v(4.2, 2.73) * mm, "end": v(4.2, 2.7) * mm});
            skLineSegment(sketch, "E6696", {"start": v(4.2, 2.7) * mm, "end": v(4.21, 2.65) * mm});
            skLineSegment(sketch, "E6697", {"start": v(4.21, 2.65) * mm, "end": v(4.21, 2.6) * mm});
            skLineSegment(sketch, "E6698", {"start": v(4.21, 2.6) * mm, "end": v(4.22, 2.56) * mm});
            skLineSegment(sketch, "E6699", {"start": v(4.22, 2.56) * mm, "end": v(4.22, 2.51) * mm});
            skLineSegment(sketch, "E6700", {"start": v(4.22, 2.51) * mm, "end": v(4.22, 2.44) * mm});
            skLineSegment(sketch, "E6701", {"start": v(4.22, 2.44) * mm, "end": v(4.21, 2.16) * mm});
            skLineSegment(sketch, "E6702", {"start": v(4.21, 2.16) * mm, "end": v(4.19, 1.89) * mm});
            skLineSegment(sketch, "E6703", {"start": v(4.19, 1.89) * mm, "end": v(4.15, 1.62) * mm});
            skLineSegment(sketch, "E6704", {"start": v(4.15, 1.62) * mm, "end": v(4.09, 1.35) * mm});
            skLineSegment(sketch, "E6705", {"start": v(4.09, 1.35) * mm, "end": v(4.01, 1.08) * mm});
            skLineSegment(sketch, "E6706", {"start": v(4.01, 1.08) * mm, "end": v(3.92, 0.81) * mm});
            skLineSegment(sketch, "E6707", {"start": v(3.92, 0.81) * mm, "end": v(3.81, 0.55) * mm});
            skLineSegment(sketch, "E6708", {"start": v(3.81, 0.55) * mm, "end": v(3.69, 0.28) * mm});
            skLineSegment(sketch, "E6709", {"start": v(3.69, 0.28) * mm, "end": v(3.54, 0.02) * mm});
            skLineSegment(sketch, "E6710", {"start": v(3.54, 0.02) * mm, "end": v(3.39, -0.24) * mm});
            skLineSegment(sketch, "E6711", {"start": v(3.39, -0.24) * mm, "end": v(3.22, -0.51) * mm});
            skLineSegment(sketch, "E6712", {"start": v(3.22, -0.51) * mm, "end": v(3.03, -0.78) * mm});
            skLineSegment(sketch, "E6713", {"start": v(3.03, -0.78) * mm, "end": v(2.62, -1.33) * mm});
            skLineSegment(sketch, "E6714", {"start": v(2.62, -1.33) * mm, "end": v(2.15, -1.89) * mm});
            skLineSegment(sketch, "E6715", {"start": v(2.15, -1.89) * mm, "end": v(1.63, -2.46) * mm});
            skLineSegment(sketch, "E6716", {"start": v(1.63, -2.46) * mm, "end": v(1.04, -3.07) * mm});
            skLineSegment(sketch, "E6717", {"start": v(1.04, -3.07) * mm, "end": v(0.4, -3.7) * mm});
            skLineSegment(sketch, "E6718", {"start": v(0.4, -3.7) * mm, "end": v(-0.3, -4.34) * mm});
            skLineSegment(sketch, "E6719", {"start": v(-0.3, -4.34) * mm, "end": v(-0.18, -4.39) * mm});
            skLineSegment(sketch, "E6720", {"start": v(-0.18, -4.39) * mm, "end": v(-0.05, -4.43) * mm});
            skLineSegment(sketch, "E6721", {"start": v(-0.05, -4.43) * mm, "end": v(0.08, -4.46) * mm});
            skLineSegment(sketch, "E6722", {"start": v(0.08, -4.46) * mm, "end": v(0.2, -4.49) * mm});
            skLineSegment(sketch, "E6723", {"start": v(0.2, -4.49) * mm, "end": v(0.34, -4.5) * mm});
            skLineSegment(sketch, "E6724", {"start": v(0.34, -4.5) * mm, "end": v(0.47, -4.52) * mm});
            skLineSegment(sketch, "E6725", {"start": v(0.47, -4.52) * mm, "end": v(0.6, -4.53) * mm});
            skLineSegment(sketch, "E6726", {"start": v(0.6, -4.53) * mm, "end": v(0.74, -4.53) * mm});
            skLineSegment(sketch, "E6727", {"start": v(0.74, -4.53) * mm, "end": v(0.84, -4.53) * mm});
            skLineSegment(sketch, "E6728", {"start": v(0.84, -4.53) * mm, "end": v(0.95, -4.52) * mm});
            skLineSegment(sketch, "E6729", {"start": v(0.95, -4.52) * mm, "end": v(1.06, -4.51) * mm});
            skLineSegment(sketch, "E6730", {"start": v(1.06, -4.51) * mm, "end": v(1.17, -4.5) * mm});
            skLineSegment(sketch, "E6731", {"start": v(1.17, -4.5) * mm, "end": v(1.29, -4.47) * mm});
            skLineSegment(sketch, "E6732", {"start": v(1.29, -4.47) * mm, "end": v(1.4, -4.44) * mm});
            skLineSegment(sketch, "E6733", {"start": v(1.4, -4.44) * mm, "end": v(1.52, -4.41) * mm});
            skLineSegment(sketch, "E6734", {"start": v(1.52, -4.41) * mm, "end": v(1.77, -4.33) * mm});
            skLineSegment(sketch, "E6735", {"start": v(1.77, -4.33) * mm, "end": v(2.02, -4.23) * mm});
            skLineSegment(sketch, "E6736", {"start": v(2.02, -4.23) * mm, "end": v(2.29, -4.11) * mm});
            skLineSegment(sketch, "E6737", {"start": v(2.29, -4.11) * mm, "end": v(2.56, -3.97) * mm});
            skLineSegment(sketch, "E6738", {"start": v(2.56, -3.97) * mm, "end": v(2.84, -3.81) * mm});
            skLineSegment(sketch, "E6739", {"start": v(2.84, -3.81) * mm, "end": v(3.13, -3.63) * mm});
            skLineSegment(sketch, "E6740", {"start": v(3.13, -3.63) * mm, "end": v(3.43, -3.43) * mm});
            skLineSegment(sketch, "E6741", {"start": v(3.43, -3.43) * mm, "end": v(3.74, -3.21) * mm});
            skLineSegment(sketch, "E6742", {"start": v(3.74, -3.21) * mm, "end": v(4.05, -2.97) * mm});
            skLineSegment(sketch, "E6743", {"start": v(4.05, -2.97) * mm, "end": v(4.38, -2.71) * mm});
            skLineSegment(sketch, "E6744", {"start": v(4.38, -2.71) * mm, "end": v(4.71, -2.43) * mm});
            skLineSegment(sketch, "E6745", {"start": v(4.71, -2.43) * mm, "end": v(5.23, -1.97) * mm});
            skLineSegment(sketch, "E6746", {"start": v(5.23, -1.97) * mm, "end": v(5.23, -3.01) * mm});
            skLineSegment(sketch, "E6747", {"start": v(5.23, -3.01) * mm, "end": v(4.69, -3.5) * mm});
            skLineSegment(sketch, "E6748", {"start": v(4.69, -3.5) * mm, "end": v(3.6, -4.42) * mm});
            skLineSegment(sketch, "E6749", {"start": v(3.6, -4.42) * mm, "end": v(3.08, -4.87) * mm});
            skLineSegment(sketch, "E6750", {"start": v(3.08, -4.87) * mm, "end": v(2.57, -5.28) * mm});
            skLineSegment(sketch, "E6751", {"start": v(2.57, -5.28) * mm, "end": v(2.07, -5.65) * mm});
            skLineSegment(sketch, "E6752", {"start": v(2.07, -5.65) * mm, "end": v(1.58, -5.97) * mm});
            skLineSegment(sketch, "E6753", {"start": v(1.58, -5.97) * mm, "end": v(1.11, -6.25) * mm});
            skLineSegment(sketch, "E6754", {"start": v(1.11, -6.25) * mm, "end": v(0.88, -6.38) * mm});
            skLineSegment(sketch, "E6755", {"start": v(0.88, -6.38) * mm, "end": v(0.66, -6.48) * mm});
            skLineSegment(sketch, "E6756", {"start": v(0.66, -6.48) * mm, "end": v(0.44, -6.57) * mm});
            skLineSegment(sketch, "E6757", {"start": v(0.44, -6.57) * mm, "end": v(0.22, -6.64) * mm});
            skLineSegment(sketch, "E6758", {"start": v(0.22, -6.64) * mm, "end": v(0.01, -6.7) * mm});
            skLineSegment(sketch, "E6759", {"start": v(0.01, -6.7) * mm, "end": v(-0.2, -6.74) * mm});
            skLineSegment(sketch, "E6760", {"start": v(-0.2, -6.74) * mm, "end": v(-0.4, -6.77) * mm});
            skLineSegment(sketch, "E6761", {"start": v(-0.4, -6.77) * mm, "end": v(-0.6, -6.77) * mm});
            skLineSegment(sketch, "E6762", {"start": v(-0.6, -6.77) * mm, "end": v(-0.74, -6.77) * mm});
            skLineSegment(sketch, "E6763", {"start": v(-0.74, -6.77) * mm, "end": v(-0.9, -6.76) * mm});
            skLineSegment(sketch, "E6764", {"start": v(-0.9, -6.76) * mm, "end": v(-1.05, -6.73) * mm});
            skLineSegment(sketch, "E6765", {"start": v(-1.05, -6.73) * mm, "end": v(-1.22, -6.7) * mm});
            skLineSegment(sketch, "E6766", {"start": v(-1.22, -6.7) * mm, "end": v(-1.37, -6.67) * mm});
            skLineSegment(sketch, "E6767", {"start": v(-1.37, -6.67) * mm, "end": v(-1.67, -6.6) * mm});
            skLineSegment(sketch, "E6768", {"start": v(-1.67, -6.6) * mm, "end": v(-1.8, -6.56) * mm});
            skLineSegment(sketch, "E6769", {"start": v(-1.8, -6.56) * mm, "end": v(-1.88, -6.53) * mm});
            skLineSegment(sketch, "E6770", {"start": v(-1.88, -6.53) * mm, "end": v(-1.96, -6.5) * mm});
            skLineSegment(sketch, "E6771", {"start": v(-1.96, -6.5) * mm, "end": v(-2.04, -6.47) * mm});
            skLineSegment(sketch, "E6772", {"start": v(-2.04, -6.47) * mm, "end": v(-2.12, -6.44) * mm});
            skLineSegment(sketch, "E6773", {"start": v(-2.12, -6.44) * mm, "end": v(-2.21, -6.4) * mm});
            skLineSegment(sketch, "E6774", {"start": v(-2.21, -6.4) * mm, "end": v(-2.31, -6.36) * mm});
            skLineSegment(sketch, "E6775", {"start": v(-2.31, -6.36) * mm, "end": v(-2.41, -6.32) * mm});
            skLineSegment(sketch, "E6776", {"start": v(-2.41, -6.32) * mm, "end": v(-2.52, -6.28) * mm});
            skLineSegment(sketch, "E6777", {"start": v(-2.52, -6.28) * mm, "end": v(-2.62, -6.24) * mm});
            skLineSegment(sketch, "E6778", {"start": v(-2.62, -6.24) * mm, "end": v(-2.72, -6.2) * mm});
            skLineSegment(sketch, "E6779", {"start": v(-2.72, -6.2) * mm, "end": v(-2.81, -6.17) * mm});
            skLineSegment(sketch, "E6780", {"start": v(-2.81, -6.17) * mm, "end": v(-2.9, -6.13) * mm});
            skLineSegment(sketch, "E6781", {"start": v(-2.9, -6.13) * mm, "end": v(-2.98, -6.1) * mm});
            skLineSegment(sketch, "E6782", {"start": v(-2.98, -6.1) * mm, "end": v(-3.02, -6.1) * mm});
            skLineSegment(sketch, "E6783", {"start": v(-3.02, -6.1) * mm, "end": v(-3.05, -6.08) * mm});
            skLineSegment(sketch, "E6784", {"start": v(-3.05, -6.08) * mm, "end": v(-3.09, -6.07) * mm});
            skLineSegment(sketch, "E6785", {"start": v(-3.09, -6.07) * mm, "end": v(-3.12, -6.06) * mm});
            skLineSegment(sketch, "E6786", {"start": v(-3.12, -6.06) * mm, "end": v(-3.15, -6.05) * mm});
            skLineSegment(sketch, "E6787", {"start": v(-3.15, -6.05) * mm, "end": v(-3.18, -6.04) * mm});
            skLineSegment(sketch, "E6788", {"start": v(-3.18, -6.04) * mm, "end": v(-3.24, -6.05) * mm});
            skLineSegment(sketch, "E6789", {"start": v(-3.24, -6.05) * mm, "end": v(-3.3, -6.06) * mm});
            skLineSegment(sketch, "E6790", {"start": v(-3.3, -6.06) * mm, "end": v(-3.34, -6.08) * mm});
            skLineSegment(sketch, "E6791", {"start": v(-3.34, -6.08) * mm, "end": v(-3.39, -6.09) * mm});
            skLineSegment(sketch, "E6792", {"start": v(-3.39, -6.09) * mm, "end": v(-3.43, -6.1) * mm});
            skLineSegment(sketch, "E6793", {"start": v(-3.43, -6.1) * mm, "end": v(-3.47, -6.1) * mm});
            skLineSegment(sketch, "E6794", {"start": v(-3.47, -6.1) * mm, "end": v(-3.5, -6.12) * mm});
            skLineSegment(sketch, "E6795", {"start": v(-3.5, -6.12) * mm, "end": v(-3.53, -6.12) * mm});
            skLineSegment(sketch, "E6796", {"start": v(-3.53, -6.12) * mm, "end": v(-3.54, -6.12) * mm});
            skLineSegment(sketch, "E6797", {"start": v(-3.54, -6.12) * mm, "end": v(-3.56, -6.13) * mm});
            skLineSegment(sketch, "E6798", {"start": v(-3.56, -6.13) * mm, "end": v(-3.57, -6.13) * mm});
            skLineSegment(sketch, "E6799", {"start": v(-3.57, -6.13) * mm, "end": v(-3.59, -6.13) * mm});
            skLineSegment(sketch, "E6800", {"start": v(-3.59, -6.13) * mm, "end": v(-3.6, -6.14) * mm});
            skLineSegment(sketch, "E6801", {"start": v(-3.6, -6.14) * mm, "end": v(-3.62, -6.14) * mm});
            skLineSegment(sketch, "E6802", {"start": v(-3.62, -6.14) * mm, "end": v(-3.63, -6.14) * mm});
            skLineSegment(sketch, "E6803", {"start": v(-3.63, -6.14) * mm, "end": v(-3.64, -6.14) * mm});
            skLineSegment(sketch, "E6804", {"start": v(-3.64, -6.14) * mm, "end": v(-3.65, -6.15) * mm});
            skLineSegment(sketch, "E6805", {"start": v(-3.65, -6.15) * mm, "end": v(-3.66, -6.15) * mm});
            skLineSegment(sketch, "E6806", {"start": v(-3.66, -6.15) * mm, "end": v(-3.66, -6.15) * mm});
            skLineSegment(sketch, "E6807", {"start": v(-3.66, -6.15) * mm, "end": v(-3.67, -6.15) * mm});
            skLineSegment(sketch, "E6808", {"start": v(-3.67, -6.15) * mm, "end": v(-3.67, -6.15) * mm});
            skLineSegment(sketch, "E6809", {"start": v(-3.67, -6.15) * mm, "end": v(-3.68, -6.15) * mm});
            skLineSegment(sketch, "E6810", {"start": v(-3.68, -6.15) * mm, "end": v(-3.68, -6.15) * mm});
            skLineSegment(sketch, "E6811", {"start": v(-3.68, -6.15) * mm, "end": v(-3.69, -6.15) * mm});
            skLineSegment(sketch, "E6812", {"start": v(-3.69, -6.15) * mm, "end": v(-3.69, -6.15) * mm});
            skLineSegment(sketch, "E6813", {"start": v(-3.69, -6.15) * mm, "end": v(-3.7, -6.15) * mm});
            skLineSegment(sketch, "E6814", {"start": v(-3.7, -6.15) * mm, "end": v(-3.7, -6.15) * mm});
            skLineSegment(sketch, "E6815", {"start": v(-3.7, -6.15) * mm, "end": v(-3.77, -6.15) * mm});
            skLineSegment(sketch, "E6816", {"start": v(-3.77, -6.15) * mm, "end": v(-3.83, -6.15) * mm});
            skLineSegment(sketch, "E6817", {"start": v(-3.83, -6.15) * mm, "end": v(-3.9, -6.14) * mm});
            skLineSegment(sketch, "E6818", {"start": v(-3.9, -6.14) * mm, "end": v(-3.97, -6.13) * mm});
            skLineSegment(sketch, "E6819", {"start": v(-3.97, -6.13) * mm, "end": v(-4.04, -6.11) * mm});
            skLineSegment(sketch, "E6820", {"start": v(-4.04, -6.11) * mm, "end": v(-4.1, -6.1) * mm});
            skLineSegment(sketch, "E6821", {"start": v(-4.1, -6.1) * mm, "end": v(-4.18, -6.08) * mm});
            skLineSegment(sketch, "E6822", {"start": v(-4.18, -6.08) * mm, "end": v(-4.25, -6.05) * mm});
            skLineSegment(sketch, "E6823", {"start": v(-4.25, -6.05) * mm, "end": v(-4.4, -6) * mm});
            skLineSegment(sketch, "E6824", {"start": v(-4.4, -6) * mm, "end": v(-4.56, -5.92) * mm});
            skLineSegment(sketch, "E6825", {"start": v(-4.56, -5.92) * mm, "end": v(-4.72, -5.84) * mm});
            skLineSegment(sketch, "E6826", {"start": v(-4.72, -5.84) * mm, "end": v(-4.89, -5.75) * mm});
            skLineSegment(sketch, "E6827", {"start": v(-4.89, -5.75) * mm, "end": v(-5, -5.99) * mm});
            skLineSegment(sketch, "E6828", {"start": v(-5, -5.99) * mm, "end": v(-5.13, -6.24) * mm});
            skLineSegment(sketch, "E6829", {"start": v(-5.13, -6.24) * mm, "end": v(-5.26, -6.52) * mm});
            skLineSegment(sketch, "E6830", {"start": v(-5.26, -6.52) * mm, "end": v(-5.4, -6.8) * mm});
            skLineSegment(sketch, "E6831", {"start": v(-5.4, -6.8) * mm, "end": v(-5.52, -7.11) * mm});
            skLineSegment(sketch, "E6832", {"start": v(-5.52, -7.11) * mm, "end": v(-5.66, -7.44) * mm});
            skLineSegment(sketch, "E6833", {"start": v(-5.66, -7.44) * mm, "end": v(-5.8, -7.78) * mm});
            skLineSegment(sketch, "E6834", {"start": v(-5.8, -7.78) * mm, "end": v(-5.94, -8.13) * mm});
            skLineSegment(sketch, "E6835", {"start": v(-5.94, -8.13) * mm, "end": v(-6.08, -8.5) * mm});
            skLineSegment(sketch, "E6836", {"start": v(-6.08, -8.5) * mm, "end": v(-6.22, -8.83) * mm});
            skLineSegment(sketch, "E6837", {"start": v(-6.22, -8.83) * mm, "end": v(-6.34, -9.15) * mm});
            skLineSegment(sketch, "E6838", {"start": v(-6.34, -9.15) * mm, "end": v(-6.46, -9.46) * mm});
            skLineSegment(sketch, "E6839", {"start": v(-6.46, -9.46) * mm, "end": v(-6.58, -9.74) * mm});
            skLineSegment(sketch, "E6840", {"start": v(-6.58, -9.74) * mm, "end": v(-6.7, -10) * mm});
            skLineSegment(sketch, "E6841", {"start": v(-6.7, -10) * mm, "end": v(-6.8, -10.25) * mm});
            skLineSegment(sketch, "E6842", {"start": v(-6.8, -10.25) * mm, "end": v(-6.9, -10.48) * mm});
            skLineSegment(sketch, "E6843", {"start": v(-6.9, -10.48) * mm, "end": v(-7.11, -10.9) * mm});
            skLineSegment(sketch, "E6844", {"start": v(-7.11, -10.9) * mm, "end": v(-7.35, -11.33) * mm});
            skLineSegment(sketch, "E6845", {"start": v(-7.35, -11.33) * mm, "end": v(-7.63, -11.74) * mm});
            skLineSegment(sketch, "E6846", {"start": v(-7.63, -11.74) * mm, "end": v(-7.94, -12.14) * mm});
            skLineSegment(sketch, "E6847", {"start": v(-7.94, -12.14) * mm, "end": v(-7.98, -12.18) * mm});
            skLineSegment(sketch, "E6848", {"start": v(-7.98, -12.18) * mm, "end": v(-8.03, -12.22) * mm});
            skLineSegment(sketch, "E6849", {"start": v(-8.03, -12.22) * mm, "end": v(-8.07, -12.26) * mm});
            skLineSegment(sketch, "E6850", {"start": v(-8.07, -12.26) * mm, "end": v(-8.1, -12.3) * mm});
            skLineSegment(sketch, "E6851", {"start": v(-8.1, -12.3) * mm, "end": v(-8.14, -12.33) * mm});
            skLineSegment(sketch, "E6852", {"start": v(-8.14, -12.33) * mm, "end": v(-8.18, -12.36) * mm});
            skLineSegment(sketch, "E6853", {"start": v(-8.18, -12.36) * mm, "end": v(-8.21, -12.39) * mm});
            skLineSegment(sketch, "E6854", {"start": v(-8.21, -12.39) * mm, "end": v(-8.25, -12.4) * mm});
            skLineSegment(sketch, "E6855", {"start": v(-8.25, -12.4) * mm, "end": v(-8.26, -12.42) * mm});
            skLineSegment(sketch, "E6856", {"start": v(-8.26, -12.42) * mm, "end": v(-8.28, -12.43) * mm});
            skLineSegment(sketch, "E6857", {"start": v(-8.28, -12.43) * mm, "end": v(-8.3, -12.44) * mm});
            skLineSegment(sketch, "E6858", {"start": v(-8.3, -12.44) * mm, "end": v(-8.3, -12.45) * mm});
            skLineSegment(sketch, "E6859", {"start": v(-8.3, -12.45) * mm, "end": v(-8.32, -12.46) * mm});
            skLineSegment(sketch, "E6860", {"start": v(-8.32, -12.46) * mm, "end": v(-8.33, -12.46) * mm});
            skLineSegment(sketch, "E6861", {"start": v(-8.33, -12.46) * mm, "end": v(-8.35, -12.47) * mm});
            skLineSegment(sketch, "E6862", {"start": v(-8.35, -12.47) * mm, "end": v(-8.36, -12.48) * mm});
            skLineSegment(sketch, "E6863", {"start": v(-8.36, -12.48) * mm, "end": v(-8.37, -12.48) * mm});
            skLineSegment(sketch, "E6864", {"start": v(-8.37, -12.48) * mm, "end": v(-8.38, -12.49) * mm});
            skLineSegment(sketch, "E6865", {"start": v(-8.38, -12.49) * mm, "end": v(-8.4, -12.5) * mm});
            skLineSegment(sketch, "E6866", {"start": v(-8.4, -12.5) * mm, "end": v(-8.4, -12.5) * mm});
            skLineSegment(sketch, "E6867", {"start": v(-8.4, -12.5) * mm, "end": v(-8.42, -12.5) * mm});
            skLineSegment(sketch, "E6868", {"start": v(-8.42, -12.5) * mm, "end": v(-8.43, -12.5) * mm});
            skLineSegment(sketch, "E6869", {"start": v(-8.43, -12.5) * mm, "end": v(-8.44, -12.5) * mm});
            skLineSegment(sketch, "E6870", {"start": v(-8.44, -12.5) * mm, "end": v(-8.44, -12.5) * mm});
            skLineSegment(sketch, "E6871", {"start": v(-8.44, -12.5) * mm, "end": v(-8.45, -12.5) * mm});
            skLineSegment(sketch, "E6872", {"start": v(-8.45, -12.5) * mm, "end": v(-8.48, -12.5) * mm});
            skLineSegment(sketch, "E6873", {"start": v(-8.48, -12.5) * mm, "end": v(-8.52, -12.5) * mm});
            skLineSegment(sketch, "E6874", {"start": v(-8.52, -12.5) * mm, "end": v(-8.56, -12.5) * mm});
            skLineSegment(sketch, "E6875", {"start": v(-8.56, -12.5) * mm, "end": v(-8.6, -12.48) * mm});
            skLineSegment(sketch, "E6876", {"start": v(-8.6, -12.48) * mm, "end": v(-8.62, -12.47) * mm});
            skLineSegment(sketch, "E6877", {"start": v(-8.62, -12.47) * mm, "end": v(-8.66, -12.46) * mm});
            skLineSegment(sketch, "E6878", {"start": v(-8.66, -12.46) * mm, "end": v(-8.69, -12.45) * mm});
            skLineSegment(sketch, "E6879", {"start": v(-8.69, -12.45) * mm, "end": v(-8.72, -12.43) * mm});
            skLineSegment(sketch, "E6880", {"start": v(-8.72, -12.43) * mm, "end": v(-8.75, -12.41) * mm});
            skLineSegment(sketch, "E6881", {"start": v(-8.75, -12.41) * mm, "end": v(-8.77, -12.4) * mm});
            skLineSegment(sketch, "E6882", {"start": v(-8.77, -12.4) * mm, "end": v(-8.8, -12.37) * mm});
            skLineSegment(sketch, "E6883", {"start": v(-8.8, -12.37) * mm, "end": v(-8.82, -12.35) * mm});
            skLineSegment(sketch, "E6884", {"start": v(-8.82, -12.35) * mm, "end": v(-8.85, -12.32) * mm});
            skLineSegment(sketch, "E6885", {"start": v(-8.85, -12.32) * mm, "end": v(-8.87, -12.29) * mm});
            skLineSegment(sketch, "E6886", {"start": v(-8.87, -12.29) * mm, "end": v(-8.9, -12.26) * mm});
            skLineSegment(sketch, "E6887", {"start": v(-8.9, -12.26) * mm, "end": v(-8.91, -12.23) * mm});
            skLineSegment(sketch, "E6888", {"start": v(-8.91, -12.23) * mm, "end": v(-8.93, -12.19) * mm});
            skLineSegment(sketch, "E6889", {"start": v(-8.93, -12.19) * mm, "end": v(-8.95, -12.15) * mm});
            skLineSegment(sketch, "E6890", {"start": v(-8.95, -12.15) * mm, "end": v(-8.96, -12.11) * mm});
            skLineSegment(sketch, "E6891", {"start": v(-8.96, -12.11) * mm, "end": v(-8.98, -12.07) * mm});
            skLineSegment(sketch, "E6892", {"start": v(-8.98, -12.07) * mm, "end": v(-9, -12.03) * mm});
            skLineSegment(sketch, "E6893", {"start": v(-9, -12.03) * mm, "end": v(-9, -11.98) * mm});
            skLineSegment(sketch, "E6894", {"start": v(-9, -11.98) * mm, "end": v(-9.02, -11.93) * mm});
            skLineSegment(sketch, "E6895", {"start": v(-9.02, -11.93) * mm, "end": v(-9.03, -11.88) * mm});
            skLineSegment(sketch, "E6896", {"start": v(-9.03, -11.88) * mm, "end": v(-9.04, -11.83) * mm});
            skLineSegment(sketch, "E6897", {"start": v(-9.04, -11.83) * mm, "end": v(-9.05, -11.77) * mm});
            skLineSegment(sketch, "E6898", {"start": v(-9.05, -11.77) * mm, "end": v(-9.06, -11.66) * mm});
            skLineSegment(sketch, "E6899", {"start": v(-9.06, -11.66) * mm, "end": v(-9.06, -11.53) * mm});
            skLineSegment(sketch, "E6900", {"start": v(-9.06, -11.53) * mm, "end": v(-9.07, -11.4) * mm});
            skLineSegment(sketch, "E6901", {"start": v(-9.07, -11.4) * mm, "end": v(-9.06, -11.16) * mm});
            skLineSegment(sketch, "E6902", {"start": v(-9.06, -11.16) * mm, "end": v(-9.04, -10.92) * mm});
            skLineSegment(sketch, "E6903", {"start": v(-9.04, -10.92) * mm, "end": v(-9.01, -10.67) * mm});
            skLineSegment(sketch, "E6904", {"start": v(-9.01, -10.67) * mm, "end": v(-8.97, -10.43) * mm});
            skLineSegment(sketch, "E6905", {"start": v(-8.97, -10.43) * mm, "end": v(-8.91, -10.17) * mm});
            skLineSegment(sketch, "E6906", {"start": v(-8.91, -10.17) * mm, "end": v(-8.85, -9.92) * mm});
            skLineSegment(sketch, "E6907", {"start": v(-8.85, -9.92) * mm, "end": v(-8.77, -9.66) * mm});
            skLineSegment(sketch, "E6908", {"start": v(-8.77, -9.66) * mm, "end": v(-8.68, -9.4) * mm});
            skLineSegment(sketch, "E6909", {"start": v(-8.68, -9.4) * mm, "end": v(-8.48, -8.9) * mm});
            skLineSegment(sketch, "E6910", {"start": v(-8.48, -8.9) * mm, "end": v(-8.25, -8.4) * mm});
            skLineSegment(sketch, "E6911", {"start": v(-8.25, -8.4) * mm, "end": v(-8, -7.92) * mm});
            skLineSegment(sketch, "E6912", {"start": v(-8, -7.92) * mm, "end": v(-7.74, -7.45) * mm});
            skLineSegment(sketch, "E6913", {"start": v(-7.74, -7.45) * mm, "end": v(-7.46, -7) * mm});
            skLineSegment(sketch, "E6914", {"start": v(-7.46, -7) * mm, "end": v(-6.85, -6.06) * mm});
            skLineSegment(sketch, "E6915", {"start": v(-6.85, -6.06) * mm, "end": v(-6.52, -5.59) * mm});
            skLineSegment(sketch, "E6916", {"start": v(-6.52, -5.59) * mm, "end": v(-6.36, -5.36) * mm});
            skLineSegment(sketch, "E6917", {"start": v(-6.36, -5.36) * mm, "end": v(-6.21, -5.14) * mm});
            skLineSegment(sketch, "E6918", {"start": v(-6.21, -5.14) * mm, "end": v(-6.08, -4.94) * mm});
            skLineSegment(sketch, "E6919", {"start": v(-6.08, -4.94) * mm, "end": v(-6.02, -4.85) * mm});
            skLineSegment(sketch, "E6920", {"start": v(-6.02, -4.85) * mm, "end": v(-5.95, -4.76) * mm});
            skLineSegment(sketch, "E6921", {"start": v(-5.95, -4.76) * mm, "end": v(-5.9, -4.67) * mm});
            skLineSegment(sketch, "E6922", {"start": v(-5.9, -4.67) * mm, "end": v(-5.84, -4.59) * mm});
            skLineSegment(sketch, "E6923", {"start": v(-5.84, -4.59) * mm, "end": v(-5.8, -4.5) * mm});
            skLineSegment(sketch, "E6924", {"start": v(-5.8, -4.5) * mm, "end": v(-5.74, -4.43) * mm});
            skLineSegment(sketch, "E6925", {"start": v(-5.74, -4.43) * mm, "end": v(-5.7, -4.36) * mm});
            skLineSegment(sketch, "E6926", {"start": v(-5.7, -4.36) * mm, "end": v(-5.66, -4.3) * mm});
            skLineSegment(sketch, "E6927", {"start": v(-5.66, -4.3) * mm, "end": v(-5.62, -4.23) * mm});
            skLineSegment(sketch, "E6928", {"start": v(-5.62, -4.23) * mm, "end": v(-5.58, -4.17) * mm});
            skLineSegment(sketch, "E6929", {"start": v(-5.58, -4.17) * mm, "end": v(-5.03, -3.2) * mm});
            skLineSegment(sketch, "E6930", {"start": v(-5.03, -3.2) * mm, "end": v(-4.5, -2.28) * mm});
            skLineSegment(sketch, "E6931", {"start": v(-4.5, -2.28) * mm, "end": v(-4.01, -1.39) * mm});
            skLineSegment(sketch, "E6932", {"start": v(-4.01, -1.39) * mm, "end": v(-3.55, -0.53) * mm});
            skLineSegment(sketch, "E6933", {"start": v(-3.55, -0.53) * mm, "end": v(-3.12, 0.29) * mm});
            skLineSegment(sketch, "E6934", {"start": v(-3.12, 0.29) * mm, "end": v(-2.73, 1.07) * mm});
            skLineSegment(sketch, "E6935", {"start": v(-2.73, 1.07) * mm, "end": v(-2.36, 1.81) * mm});
            skLineSegment(sketch, "E6936", {"start": v(-2.36, 1.81) * mm, "end": v(-2.03, 2.52) * mm});
            skLineSegment(sketch, "E6937", {"start": v(-2.03, 2.52) * mm, "end": v(-2.83, 1.55) * mm});
            skLineSegment(sketch, "E6938", {"start": v(-2.83, 1.55) * mm, "end": v(-3.59, 0.64) * mm});
            skLineSegment(sketch, "E6939", {"start": v(-3.59, 0.64) * mm, "end": v(-4.3, -0.2) * mm});
            skLineSegment(sketch, "E6940", {"start": v(-4.3, -0.2) * mm, "end": v(-4.95, -0.95) * mm});
            skLineSegment(sketch, "E6941", {"start": v(-4.95, -0.95) * mm, "end": v(-5.25, -1.3) * mm});
            skLineSegment(sketch, "E6942", {"start": v(-5.25, -1.3) * mm, "end": v(-5.55, -1.65) * mm});
            skLineSegment(sketch, "E6943", {"start": v(-5.55, -1.65) * mm, "end": v(-5.83, -1.96) * mm});
            skLineSegment(sketch, "E6944", {"start": v(-5.83, -1.96) * mm, "end": v(-6.1, -2.26) * mm});
            skLineSegment(sketch, "E6945", {"start": v(-6.1, -2.26) * mm, "end": v(-6.36, -2.55) * mm});
            skLineSegment(sketch, "E6946", {"start": v(-6.36, -2.55) * mm, "end": v(-6.6, -2.81) * mm});
            skLineSegment(sketch, "E6947", {"start": v(-6.6, -2.81) * mm, "end": v(-6.84, -3.06) * mm});
            skLineSegment(sketch, "E6948", {"start": v(-6.84, -3.06) * mm, "end": v(-7.06, -3.29) * mm});
            skLineSegment(sketch, "E6949", {"start": v(-1.19, -4) * mm, "end": v(-0.84, -3.63) * mm});
            skLineSegment(sketch, "E6950", {"start": v(-0.84, -3.63) * mm, "end": v(-0.52, -3.27) * mm});
            skLineSegment(sketch, "E6951", {"start": v(-0.52, -3.27) * mm, "end": v(-0.22, -2.93) * mm});
            skLineSegment(sketch, "E6952", {"start": v(-0.22, -2.93) * mm, "end": v(0.06, -2.6) * mm});
            skLineSegment(sketch, "E6953", {"start": v(0.06, -2.6) * mm, "end": v(0.31, -2.3) * mm});
            skLineSegment(sketch, "E6954", {"start": v(0.31, -2.3) * mm, "end": v(0.55, -2) * mm});
            skLineSegment(sketch, "E6955", {"start": v(0.55, -2) * mm, "end": v(0.75, -1.7) * mm});
            skLineSegment(sketch, "E6956", {"start": v(0.75, -1.7) * mm, "end": v(0.94, -1.44) * mm});
            skLineSegment(sketch, "E6957", {"start": v(0.94, -1.44) * mm, "end": v(1.02, -1.3) * mm});
            skLineSegment(sketch, "E6958", {"start": v(1.02, -1.3) * mm, "end": v(1.1, -1.18) * mm});
            skLineSegment(sketch, "E6959", {"start": v(1.1, -1.18) * mm, "end": v(1.18, -1.06) * mm});
            skLineSegment(sketch, "E6960", {"start": v(1.18, -1.06) * mm, "end": v(1.25, -0.94) * mm});
            skLineSegment(sketch, "E6961", {"start": v(1.25, -0.94) * mm, "end": v(1.31, -0.83) * mm});
            skLineSegment(sketch, "E6962", {"start": v(1.31, -0.83) * mm, "end": v(1.37, -0.72) * mm});
            skLineSegment(sketch, "E6963", {"start": v(1.37, -0.72) * mm, "end": v(1.42, -0.6) * mm});
            skLineSegment(sketch, "E6964", {"start": v(1.42, -0.6) * mm, "end": v(1.47, -0.5) * mm});
            skLineSegment(sketch, "E6965", {"start": v(1.47, -0.5) * mm, "end": v(1.51, -0.4) * mm});
            skLineSegment(sketch, "E6966", {"start": v(1.51, -0.4) * mm, "end": v(1.55, -0.31) * mm});
            skLineSegment(sketch, "E6967", {"start": v(1.55, -0.31) * mm, "end": v(1.58, -0.22) * mm});
            skLineSegment(sketch, "E6968", {"start": v(1.58, -0.22) * mm, "end": v(1.6, -0.13) * mm});
            skLineSegment(sketch, "E6969", {"start": v(1.6, -0.13) * mm, "end": v(1.62, -0.05) * mm});
            skLineSegment(sketch, "E6970", {"start": v(1.62, -0.05) * mm, "end": v(1.64, 0.03) * mm});
            skLineSegment(sketch, "E6971", {"start": v(1.64, 0.03) * mm, "end": v(1.64, 0.07) * mm});
            skLineSegment(sketch, "E6972", {"start": v(1.64, 0.07) * mm, "end": v(1.64, 0.1) * mm});
            skLineSegment(sketch, "E6973", {"start": v(1.64, 0.1) * mm, "end": v(1.65, 0.15) * mm});
            skLineSegment(sketch, "E6974", {"start": v(1.65, 0.15) * mm, "end": v(1.65, 0.18) * mm});
            skLineSegment(sketch, "E6975", {"start": v(1.65, 0.18) * mm, "end": v(1.65, 0.21) * mm});
            skLineSegment(sketch, "E6976", {"start": v(1.65, 0.21) * mm, "end": v(1.64, 0.25) * mm});
            skLineSegment(sketch, "E6977", {"start": v(1.64, 0.25) * mm, "end": v(1.64, 0.28) * mm});
            skLineSegment(sketch, "E6978", {"start": v(1.64, 0.28) * mm, "end": v(1.64, 0.3) * mm});
            skLineSegment(sketch, "E6979", {"start": v(1.64, 0.3) * mm, "end": v(1.63, 0.33) * mm});
            skLineSegment(sketch, "E6980", {"start": v(1.63, 0.33) * mm, "end": v(1.63, 0.36) * mm});
            skLineSegment(sketch, "E6981", {"start": v(1.63, 0.36) * mm, "end": v(1.62, 0.39) * mm});
            skLineSegment(sketch, "E6982", {"start": v(1.62, 0.39) * mm, "end": v(1.61, 0.41) * mm});
            skLineSegment(sketch, "E6983", {"start": v(1.61, 0.41) * mm, "end": v(1.6, 0.44) * mm});
            skLineSegment(sketch, "E6984", {"start": v(1.6, 0.44) * mm, "end": v(1.6, 0.46) * mm});
            skLineSegment(sketch, "E6985", {"start": v(1.6, 0.46) * mm, "end": v(1.58, 0.49) * mm});
            skLineSegment(sketch, "E6986", {"start": v(1.58, 0.49) * mm, "end": v(1.57, 0.5) * mm});
            skLineSegment(sketch, "E6987", {"start": v(1.57, 0.5) * mm, "end": v(1.56, 0.53) * mm});
            skLineSegment(sketch, "E6988", {"start": v(1.56, 0.53) * mm, "end": v(1.54, 0.55) * mm});
            skLineSegment(sketch, "E6989", {"start": v(1.54, 0.55) * mm, "end": v(1.53, 0.56) * mm});
            skLineSegment(sketch, "E6990", {"start": v(1.53, 0.56) * mm, "end": v(1.51, 0.58) * mm});
            skLineSegment(sketch, "E6991", {"start": v(1.51, 0.58) * mm, "end": v(1.5, 0.6) * mm});
            skLineSegment(sketch, "E6992", {"start": v(1.5, 0.6) * mm, "end": v(1.48, 0.61) * mm});
            skLineSegment(sketch, "E6993", {"start": v(1.48, 0.61) * mm, "end": v(1.46, 0.63) * mm});
            skLineSegment(sketch, "E6994", {"start": v(1.46, 0.63) * mm, "end": v(1.44, 0.64) * mm});
            skLineSegment(sketch, "E6995", {"start": v(1.44, 0.64) * mm, "end": v(1.42, 0.65) * mm});
            skLineSegment(sketch, "E6996", {"start": v(1.42, 0.65) * mm, "end": v(1.4, 0.66) * mm});
            skLineSegment(sketch, "E6997", {"start": v(1.4, 0.66) * mm, "end": v(1.37, 0.67) * mm});
            skLineSegment(sketch, "E6998", {"start": v(1.37, 0.67) * mm, "end": v(1.35, 0.68) * mm});
            skLineSegment(sketch, "E6999", {"start": v(1.35, 0.68) * mm, "end": v(1.32, 0.7) * mm});
            skLineSegment(sketch, "E7000", {"start": v(1.32, 0.7) * mm, "end": v(1.3, 0.7) * mm});
            skLineSegment(sketch, "E7001", {"start": v(1.3, 0.7) * mm, "end": v(1.27, 0.7) * mm});
            skLineSegment(sketch, "E7002", {"start": v(1.27, 0.7) * mm, "end": v(1.24, 0.7) * mm});
            skLineSegment(sketch, "E7003", {"start": v(1.24, 0.7) * mm, "end": v(1.2, 0.71) * mm});
            skLineSegment(sketch, "E7004", {"start": v(1.2, 0.71) * mm, "end": v(1.18, 0.71) * mm});
            skLineSegment(sketch, "E7005", {"start": v(1.18, 0.71) * mm, "end": v(1.14, 0.72) * mm});
            skLineSegment(sketch, "E7006", {"start": v(1.14, 0.72) * mm, "end": v(1.11, 0.72) * mm});
            skLineSegment(sketch, "E7007", {"start": v(1.11, 0.72) * mm, "end": v(1.07, 0.71) * mm});
            skLineSegment(sketch, "E7008", {"start": v(1.07, 0.71) * mm, "end": v(1.02, 0.71) * mm});
            skLineSegment(sketch, "E7009", {"start": v(1.02, 0.71) * mm, "end": v(0.97, 0.7) * mm});
            skLineSegment(sketch, "E7010", {"start": v(0.97, 0.7) * mm, "end": v(0.92, 0.7) * mm});
            skLineSegment(sketch, "E7011", {"start": v(0.92, 0.7) * mm, "end": v(0.87, 0.69) * mm});
            skLineSegment(sketch, "E7012", {"start": v(0.87, 0.69) * mm, "end": v(0.82, 0.67) * mm});
            skLineSegment(sketch, "E7013", {"start": v(0.82, 0.67) * mm, "end": v(0.77, 0.66) * mm});
            skLineSegment(sketch, "E7014", {"start": v(0.77, 0.66) * mm, "end": v(0.71, 0.64) * mm});
            skLineSegment(sketch, "E7015", {"start": v(0.71, 0.64) * mm, "end": v(0.66, 0.62) * mm});
            skLineSegment(sketch, "E7016", {"start": v(0.66, 0.62) * mm, "end": v(0.54, 0.57) * mm});
            skLineSegment(sketch, "E7017", {"start": v(0.54, 0.57) * mm, "end": v(0.43, 0.52) * mm});
            skLineSegment(sketch, "E7018", {"start": v(0.43, 0.52) * mm, "end": v(0.3, 0.45) * mm});
            skLineSegment(sketch, "E7019", {"start": v(0.3, 0.45) * mm, "end": v(0.18, 0.38) * mm});
            skLineSegment(sketch, "E7020", {"start": v(0.18, 0.38) * mm, "end": v(0.04, 0.3) * mm});
            skLineSegment(sketch, "E7021", {"start": v(0.04, 0.3) * mm, "end": v(-0.1, 0.2) * mm});
            skLineSegment(sketch, "E7022", {"start": v(-0.1, 0.2) * mm, "end": v(-0.23, 0.1) * mm});
            skLineSegment(sketch, "E7023", {"start": v(-0.23, 0.1) * mm, "end": v(-0.38, -0.02) * mm});
            skLineSegment(sketch, "E7024", {"start": v(-0.38, -0.02) * mm, "end": v(-0.53, -0.14) * mm});
            skLineSegment(sketch, "E7025", {"start": v(-0.53, -0.14) * mm, "end": v(-0.69, -0.27) * mm});
            skLineSegment(sketch, "E7026", {"start": v(-0.69, -0.27) * mm, "end": v(-0.93, -0.48) * mm});
            skLineSegment(sketch, "E7027", {"start": v(-0.93, -0.48) * mm, "end": v(-1.25, -0.8) * mm});
            skLineSegment(sketch, "E7028", {"start": v(-1.25, -0.8) * mm, "end": v(-1.58, -1.13) * mm});
            skLineSegment(sketch, "E7029", {"start": v(-1.58, -1.13) * mm, "end": v(-1.91, -1.5) * mm});
            skLineSegment(sketch, "E7030", {"start": v(-1.91, -1.5) * mm, "end": v(-2.25, -1.88) * mm});
            skLineSegment(sketch, "E7031", {"start": v(-2.25, -1.88) * mm, "end": v(-2.59, -2.3) * mm});
            skLineSegment(sketch, "E7032", {"start": v(-2.59, -2.3) * mm, "end": v(-2.93, -2.73) * mm});
            skLineSegment(sketch, "E7033", {"start": v(-2.93, -2.73) * mm, "end": v(-3.27, -3.2) * mm});
            skLineSegment(sketch, "E7034", {"start": v(-3.27, -3.2) * mm, "end": v(-3.62, -3.7) * mm});
            skLineSegment(sketch, "E7035", {"start": v(-3.62, -3.7) * mm, "end": v(-3.49, -3.68) * mm});
            skLineSegment(sketch, "E7036", {"start": v(-3.49, -3.68) * mm, "end": v(-3.36, -3.67) * mm});
            skLineSegment(sketch, "E7037", {"start": v(-3.36, -3.67) * mm, "end": v(-3.24, -3.66) * mm});
            skLineSegment(sketch, "E7038", {"start": v(-3.24, -3.66) * mm, "end": v(-3.13, -3.65) * mm});
            skLineSegment(sketch, "E7039", {"start": v(-3.13, -3.65) * mm, "end": v(-3.02, -3.64) * mm});
            skLineSegment(sketch, "E7040", {"start": v(-3.02, -3.64) * mm, "end": v(-2.91, -3.63) * mm});
            skLineSegment(sketch, "E7041", {"start": v(-2.91, -3.63) * mm, "end": v(-2.82, -3.62) * mm});
            skLineSegment(sketch, "E7042", {"start": v(-2.82, -3.62) * mm, "end": v(-2.72, -3.62) * mm});
            skLineSegment(sketch, "E7043", {"start": v(-2.72, -3.62) * mm, "end": v(-2.64, -3.61) * mm});
            skLineSegment(sketch, "E7044", {"start": v(-2.64, -3.61) * mm, "end": v(-2.56, -3.61) * mm});
            skLineSegment(sketch, "E7045", {"start": v(-2.56, -3.61) * mm, "end": v(-2.48, -3.61) * mm});
            skLineSegment(sketch, "E7046", {"start": v(-2.48, -3.61) * mm, "end": v(-2.4, -3.61) * mm});
            skLineSegment(sketch, "E7047", {"start": v(-2.4, -3.61) * mm, "end": v(-2.38, -3.61) * mm});
            skLineSegment(sketch, "E7048", {"start": v(-2.38, -3.61) * mm, "end": v(-2.35, -3.61) * mm});
            skLineSegment(sketch, "E7049", {"start": v(-2.35, -3.61) * mm, "end": v(-2.31, -3.61) * mm});
            skLineSegment(sketch, "E7050", {"start": v(-2.31, -3.61) * mm, "end": v(-2.29, -3.61) * mm});
            skLineSegment(sketch, "E7051", {"start": v(-2.29, -3.61) * mm, "end": v(-2.26, -3.62) * mm});
            skLineSegment(sketch, "E7052", {"start": v(-2.26, -3.62) * mm, "end": v(-2.23, -3.62) * mm});
            skLineSegment(sketch, "E7053", {"start": v(-2.23, -3.62) * mm, "end": v(-2.2, -3.62) * mm});
            skLineSegment(sketch, "E7054", {"start": v(-2.2, -3.62) * mm, "end": v(-2.18, -3.62) * mm});
            skLineSegment(sketch, "E7055", {"start": v(-2.18, -3.62) * mm, "end": v(-2.14, -3.63) * mm});
            skLineSegment(sketch, "E7056", {"start": v(-2.14, -3.63) * mm, "end": v(-2.1, -3.63) * mm});
            skLineSegment(sketch, "E7057", {"start": v(-2.1, -3.63) * mm, "end": v(-2.04, -3.64) * mm});
            skLineSegment(sketch, "E7058", {"start": v(-2.04, -3.64) * mm, "end": v(-1.99, -3.66) * mm});
            skLineSegment(sketch, "E7059", {"start": v(-1.99, -3.66) * mm, "end": v(-1.93, -3.67) * mm});
            skLineSegment(sketch, "E7060", {"start": v(-1.93, -3.67) * mm, "end": v(-1.88, -3.69) * mm});
            skLineSegment(sketch, "E7061", {"start": v(-1.88, -3.69) * mm, "end": v(-1.82, -3.7) * mm});
            skLineSegment(sketch, "E7062", {"start": v(-1.82, -3.7) * mm, "end": v(-1.75, -3.73) * mm});
            skLineSegment(sketch, "E7063", {"start": v(-1.75, -3.73) * mm, "end": v(-1.7, -3.76) * mm});
            skLineSegment(sketch, "E7064", {"start": v(-1.7, -3.76) * mm, "end": v(-1.63, -3.78) * mm});
            skLineSegment(sketch, "E7065", {"start": v(-1.63, -3.78) * mm, "end": v(-1.49, -3.84) * mm});
            skLineSegment(sketch, "E7066", {"start": v(-1.49, -3.84) * mm, "end": v(-1.34, -3.92) * mm});
            skLineSegment(sketch, "E7067", {"start": v(-1.34, -3.92) * mm, "end": v(-1.19, -4) * mm});
            skLineSegment(sketch, "E7068", {"start": v(12, 5.43) * mm, "end": v(12.62, 5.43) * mm});
            skLineSegment(sketch, "E7069", {"start": v(12.62, 5.43) * mm, "end": v(12.81, 5.76) * mm});
            skLineSegment(sketch, "E7070", {"start": v(12.81, 5.76) * mm, "end": v(13, 6.07) * mm});
            skLineSegment(sketch, "E7071", {"start": v(13, 6.07) * mm, "end": v(13.18, 6.35) * mm});
            skLineSegment(sketch, "E7072", {"start": v(13.18, 6.35) * mm, "end": v(13.35, 6.6) * mm});
            skLineSegment(sketch, "E7073", {"start": v(13.35, 6.6) * mm, "end": v(13.44, 6.72) * mm});
            skLineSegment(sketch, "E7074", {"start": v(13.44, 6.72) * mm, "end": v(13.52, 6.83) * mm});
            skLineSegment(sketch, "E7075", {"start": v(13.52, 6.83) * mm, "end": v(13.6, 6.94) * mm});
            skLineSegment(sketch, "E7076", {"start": v(13.6, 6.94) * mm, "end": v(13.69, 7.03) * mm});
            skLineSegment(sketch, "E7077", {"start": v(13.69, 7.03) * mm, "end": v(13.77, 7.13) * mm});
            skLineSegment(sketch, "E7078", {"start": v(13.77, 7.13) * mm, "end": v(13.85, 7.21) * mm});
            skLineSegment(sketch, "E7079", {"start": v(13.85, 7.21) * mm, "end": v(13.93, 7.3) * mm});
            skLineSegment(sketch, "E7080", {"start": v(13.93, 7.3) * mm, "end": v(14, 7.37) * mm});
            skLineSegment(sketch, "E7081", {"start": v(14, 7.37) * mm, "end": v(14.09, 7.44) * mm});
            skLineSegment(sketch, "E7082", {"start": v(14.09, 7.44) * mm, "end": v(14.17, 7.5) * mm});
            skLineSegment(sketch, "E7083", {"start": v(14.17, 7.5) * mm, "end": v(14.25, 7.56) * mm});
            skLineSegment(sketch, "E7084", {"start": v(14.25, 7.56) * mm, "end": v(14.33, 7.62) * mm});
            skLineSegment(sketch, "E7085", {"start": v(14.33, 7.62) * mm, "end": v(14.41, 7.67) * mm});
            skLineSegment(sketch, "E7086", {"start": v(14.41, 7.67) * mm, "end": v(14.5, 7.72) * mm});
            skLineSegment(sketch, "E7087", {"start": v(14.5, 7.72) * mm, "end": v(14.59, 7.76) * mm});
            skLineSegment(sketch, "E7088", {"start": v(14.59, 7.76) * mm, "end": v(14.67, 7.8) * mm});
            skLineSegment(sketch, "E7089", {"start": v(14.67, 7.8) * mm, "end": v(14.76, 7.83) * mm});
            skLineSegment(sketch, "E7090", {"start": v(14.76, 7.83) * mm, "end": v(14.85, 7.86) * mm});
            skLineSegment(sketch, "E7091", {"start": v(14.85, 7.86) * mm, "end": v(14.95, 7.89) * mm});
            skLineSegment(sketch, "E7092", {"start": v(14.95, 7.89) * mm, "end": v(15.04, 7.9) * mm});
            skLineSegment(sketch, "E7093", {"start": v(15.04, 7.9) * mm, "end": v(15.13, 7.93) * mm});
            skLineSegment(sketch, "E7094", {"start": v(15.13, 7.93) * mm, "end": v(15.23, 7.94) * mm});
            skLineSegment(sketch, "E7095", {"start": v(15.23, 7.94) * mm, "end": v(15.33, 7.94) * mm});
            skLineSegment(sketch, "E7096", {"start": v(15.33, 7.94) * mm, "end": v(15.43, 7.95) * mm});
            skLineSegment(sketch, "E7097", {"start": v(15.43, 7.95) * mm, "end": v(15.52, 7.94) * mm});
            skLineSegment(sketch, "E7098", {"start": v(15.52, 7.94) * mm, "end": v(15.61, 7.94) * mm});
            skLineSegment(sketch, "E7099", {"start": v(15.61, 7.94) * mm, "end": v(15.7, 7.93) * mm});
            skLineSegment(sketch, "E7100", {"start": v(15.7, 7.93) * mm, "end": v(15.77, 7.92) * mm});
            skLineSegment(sketch, "E7101", {"start": v(15.77, 7.92) * mm, "end": v(15.81, 7.92) * mm});
            skLineSegment(sketch, "E7102", {"start": v(15.81, 7.92) * mm, "end": v(15.85, 7.9) * mm});
            skLineSegment(sketch, "E7103", {"start": v(15.85, 7.9) * mm, "end": v(15.88, 7.9) * mm});
            skLineSegment(sketch, "E7104", {"start": v(15.88, 7.9) * mm, "end": v(15.91, 7.9) * mm});
            skLineSegment(sketch, "E7105", {"start": v(15.91, 7.9) * mm, "end": v(15.94, 7.89) * mm});
            skLineSegment(sketch, "E7106", {"start": v(15.94, 7.89) * mm, "end": v(15.97, 7.88) * mm});
            skLineSegment(sketch, "E7107", {"start": v(15.97, 7.88) * mm, "end": v(16, 7.87) * mm});
            skLineSegment(sketch, "E7108", {"start": v(16, 7.87) * mm, "end": v(16.02, 7.85) * mm});
            skLineSegment(sketch, "E7109", {"start": v(16.02, 7.85) * mm, "end": v(16.05, 7.84) * mm});
            skLineSegment(sketch, "E7110", {"start": v(16.05, 7.84) * mm, "end": v(16.07, 7.83) * mm});
            skLineSegment(sketch, "E7111", {"start": v(16.07, 7.83) * mm, "end": v(16.09, 7.82) * mm});
            skLineSegment(sketch, "E7112", {"start": v(16.09, 7.82) * mm, "end": v(16.1, 7.8) * mm});
            skLineSegment(sketch, "E7113", {"start": v(16.1, 7.8) * mm, "end": v(16.13, 7.79) * mm});
            skLineSegment(sketch, "E7114", {"start": v(16.13, 7.79) * mm, "end": v(16.14, 7.77) * mm});
            skLineSegment(sketch, "E7115", {"start": v(16.14, 7.77) * mm, "end": v(16.16, 7.76) * mm});
            skLineSegment(sketch, "E7116", {"start": v(16.16, 7.76) * mm, "end": v(16.17, 7.74) * mm});
            skLineSegment(sketch, "E7117", {"start": v(16.17, 7.74) * mm, "end": v(16.18, 7.72) * mm});
            skLineSegment(sketch, "E7118", {"start": v(16.18, 7.72) * mm, "end": v(16.2, 7.7) * mm});
            skLineSegment(sketch, "E7119", {"start": v(16.2, 7.7) * mm, "end": v(16.2, 7.69) * mm});
            skLineSegment(sketch, "E7120", {"start": v(16.2, 7.69) * mm, "end": v(16.2, 7.67) * mm});
            skLineSegment(sketch, "E7121", {"start": v(16.2, 7.67) * mm, "end": v(16.21, 7.65) * mm});
            skLineSegment(sketch, "E7122", {"start": v(16.21, 7.65) * mm, "end": v(16.22, 7.63) * mm});
            skLineSegment(sketch, "E7123", {"start": v(16.22, 7.63) * mm, "end": v(16.22, 7.6) * mm});
            skLineSegment(sketch, "E7124", {"start": v(16.22, 7.6) * mm, "end": v(16.22, 7.58) * mm});
            skLineSegment(sketch, "E7125", {"start": v(16.22, 7.58) * mm, "end": v(16.22, 7.58) * mm});
            skLineSegment(sketch, "E7126", {"start": v(16.22, 7.58) * mm, "end": v(16.22, 7.57) * mm});
            skLineSegment(sketch, "E7127", {"start": v(16.22, 7.57) * mm, "end": v(16.22, 7.57) * mm});
            skLineSegment(sketch, "E7128", {"start": v(16.22, 7.57) * mm, "end": v(16.22, 7.56) * mm});
            skLineSegment(sketch, "E7129", {"start": v(16.22, 7.56) * mm, "end": v(16.22, 7.55) * mm});
            skLineSegment(sketch, "E7130", {"start": v(16.22, 7.55) * mm, "end": v(16.22, 7.55) * mm});
            skLineSegment(sketch, "E7131", {"start": v(16.22, 7.55) * mm, "end": v(16.21, 7.54) * mm});
            skLineSegment(sketch, "E7132", {"start": v(16.21, 7.54) * mm, "end": v(16.21, 7.53) * mm});
            skLineSegment(sketch, "E7133", {"start": v(16.21, 7.53) * mm, "end": v(16.2, 7.52) * mm});
            skLineSegment(sketch, "E7134", {"start": v(16.2, 7.52) * mm, "end": v(16.2, 7.52) * mm});
            skLineSegment(sketch, "E7135", {"start": v(16.2, 7.52) * mm, "end": v(16.2, 7.5) * mm});
            skLineSegment(sketch, "E7136", {"start": v(16.2, 7.5) * mm, "end": v(16.2, 7.5) * mm});
            skLineSegment(sketch, "E7137", {"start": v(16.2, 7.5) * mm, "end": v(16.2, 7.48) * mm});
            skLineSegment(sketch, "E7138", {"start": v(16.2, 7.48) * mm, "end": v(16.18, 7.46) * mm});
            skLineSegment(sketch, "E7139", {"start": v(16.18, 7.46) * mm, "end": v(16.17, 7.44) * mm});
            skLineSegment(sketch, "E7140", {"start": v(16.17, 7.44) * mm, "end": v(16.16, 7.42) * mm});
            skLineSegment(sketch, "E7141", {"start": v(16.16, 7.42) * mm, "end": v(16.15, 7.4) * mm});
            skLineSegment(sketch, "E7142", {"start": v(16.15, 7.4) * mm, "end": v(16.13, 7.37) * mm});
            skLineSegment(sketch, "E7143", {"start": v(16.13, 7.37) * mm, "end": v(16.12, 7.35) * mm});
            skLineSegment(sketch, "E7144", {"start": v(16.12, 7.35) * mm, "end": v(16.1, 7.32) * mm});
            skLineSegment(sketch, "E7145", {"start": v(16.1, 7.32) * mm, "end": v(16.08, 7.3) * mm});
            skLineSegment(sketch, "E7146", {"start": v(16.08, 7.3) * mm, "end": v(16.07, 7.26) * mm});
            skLineSegment(sketch, "E7147", {"start": v(16.07, 7.26) * mm, "end": v(16.05, 7.23) * mm});
            skLineSegment(sketch, "E7148", {"start": v(16.05, 7.23) * mm, "end": v(16, 7.17) * mm});
            skLineSegment(sketch, "E7149", {"start": v(16, 7.17) * mm, "end": v(15.95, 7.1) * mm});
            skLineSegment(sketch, "E7150", {"start": v(15.95, 7.1) * mm, "end": v(15.9, 7.03) * mm});
            skLineSegment(sketch, "E7151", {"start": v(15.9, 7.03) * mm, "end": v(15.84, 6.95) * mm});
            skLineSegment(sketch, "E7152", {"start": v(15.84, 6.95) * mm, "end": v(15.78, 6.87) * mm});
            skLineSegment(sketch, "E7153", {"start": v(15.78, 6.87) * mm, "end": v(15.71, 6.78) * mm});
            skLineSegment(sketch, "E7154", {"start": v(15.71, 6.78) * mm, "end": v(15.6, 6.64) * mm});
            skLineSegment(sketch, "E7155", {"start": v(15.6, 6.64) * mm, "end": v(15.45, 6.46) * mm});
            skLineSegment(sketch, "E7156", {"start": v(15.45, 6.46) * mm, "end": v(15.3, 6.28) * mm});
            skLineSegment(sketch, "E7157", {"start": v(15.3, 6.28) * mm, "end": v(15.18, 6.1) * mm});
            skLineSegment(sketch, "E7158", {"start": v(15.18, 6.1) * mm, "end": v(15.05, 5.94) * mm});
            skLineSegment(sketch, "E7159", {"start": v(15.05, 5.94) * mm, "end": v(14.94, 5.78) * mm});
            skLineSegment(sketch, "E7160", {"start": v(14.94, 5.78) * mm, "end": v(14.84, 5.63) * mm});
            skLineSegment(sketch, "E7161", {"start": v(14.84, 5.63) * mm, "end": v(14.74, 5.5) * mm});
            skLineSegment(sketch, "E7162", {"start": v(14.74, 5.5) * mm, "end": v(14.66, 5.36) * mm});
            skLineSegment(sketch, "E7163", {"start": v(14.66, 5.36) * mm, "end": v(14.9, 5.33) * mm});
            skLineSegment(sketch, "E7164", {"start": v(14.9, 5.33) * mm, "end": v(15.12, 5.3) * mm});
            skLineSegment(sketch, "E7165", {"start": v(15.12, 5.3) * mm, "end": v(15.33, 5.28) * mm});
            skLineSegment(sketch, "E7166", {"start": v(15.33, 5.28) * mm, "end": v(15.53, 5.26) * mm});
            skLineSegment(sketch, "E7167", {"start": v(15.53, 5.26) * mm, "end": v(15.62, 5.25) * mm});
            skLineSegment(sketch, "E7168", {"start": v(15.62, 5.25) * mm, "end": v(15.71, 5.24) * mm});
            skLineSegment(sketch, "E7169", {"start": v(15.71, 5.24) * mm, "end": v(15.8, 5.23) * mm});
            skLineSegment(sketch, "E7170", {"start": v(15.8, 5.23) * mm, "end": v(15.87, 5.22) * mm});
            skLineSegment(sketch, "E7171", {"start": v(15.87, 5.22) * mm, "end": v(15.95, 5.2) * mm});
            skLineSegment(sketch, "E7172", {"start": v(15.95, 5.2) * mm, "end": v(16.02, 5.2) * mm});
            skLineSegment(sketch, "E7173", {"start": v(16.02, 5.2) * mm, "end": v(16.08, 5.2) * mm});
            skLineSegment(sketch, "E7174", {"start": v(16.08, 5.2) * mm, "end": v(16.1, 5.19) * mm});
            skLineSegment(sketch, "E7175", {"start": v(16.1, 5.19) * mm, "end": v(16.13, 5.18) * mm});
            skLineSegment(sketch, "E7176", {"start": v(16.13, 5.18) * mm, "end": v(15.7, 4.41) * mm});
            skLineSegment(sketch, "E7177", {"start": v(15.7, 4.41) * mm, "end": v(15.2, 3.63) * mm});
            skLineSegment(sketch, "E7178", {"start": v(15.2, 3.63) * mm, "end": v(14.66, 2.84) * mm});
            skLineSegment(sketch, "E7179", {"start": v(14.66, 2.84) * mm, "end": v(14.07, 2.05) * mm});
            skLineSegment(sketch, "E7180", {"start": v(14.07, 2.05) * mm, "end": v(13.87, 2.06) * mm});
            skLineSegment(sketch, "E7181", {"start": v(13.87, 2.06) * mm, "end": v(13.78, 2.07) * mm});
            skLineSegment(sketch, "E7182", {"start": v(13.78, 2.07) * mm, "end": v(13.7, 2.07) * mm});
            skLineSegment(sketch, "E7183", {"start": v(13.7, 2.07) * mm, "end": v(13.61, 2.08) * mm});
            skLineSegment(sketch, "E7184", {"start": v(13.61, 2.08) * mm, "end": v(13.53, 2.08) * mm});
            skLineSegment(sketch, "E7185", {"start": v(13.53, 2.08) * mm, "end": v(13.46, 2.09) * mm});
            skLineSegment(sketch, "E7186", {"start": v(13.46, 2.09) * mm, "end": v(13.39, 2.09) * mm});
            skLineSegment(sketch, "E7187", {"start": v(13.39, 2.09) * mm, "end": v(13.25, 2.1) * mm});
            skLineSegment(sketch, "E7188", {"start": v(13.25, 2.1) * mm, "end": v(12.97, 2.12) * mm});
            skLineSegment(sketch, "E7189", {"start": v(12.97, 2.12) * mm, "end": v(12.82, 2.13) * mm});
            skLineSegment(sketch, "E7190", {"start": v(12.82, 2.13) * mm, "end": v(12.75, 2.14) * mm});
            skLineSegment(sketch, "E7191", {"start": v(12.75, 2.14) * mm, "end": v(12.68, 2.15) * mm});
            skLineSegment(sketch, "E7192", {"start": v(12.68, 2.15) * mm, "end": v(12.6, 2.15) * mm});
            skLineSegment(sketch, "E7193", {"start": v(12.6, 2.15) * mm, "end": v(12.52, 2.16) * mm});
            skLineSegment(sketch, "E7194", {"start": v(12.52, 2.16) * mm, "end": v(12.43, 2.17) * mm});
            skLineSegment(sketch, "E7195", {"start": v(12.43, 2.17) * mm, "end": v(12.24, 2.18) * mm});
            skLineSegment(sketch, "E7196", {"start": v(12.24, 2.18) * mm, "end": v(12.14, 2.2) * mm});
            skLineSegment(sketch, "E7197", {"start": v(12.14, 2.2) * mm, "end": v(11.77, 1.58) * mm});
            skLineSegment(sketch, "E7198", {"start": v(11.77, 1.58) * mm, "end": v(11.42, 1) * mm});
            skLineSegment(sketch, "E7199", {"start": v(11.42, 1) * mm, "end": v(11.11, 0.45) * mm});
            skLineSegment(sketch, "E7200", {"start": v(11.11, 0.45) * mm, "end": v(10.83, -0.07) * mm});
            skLineSegment(sketch, "E7201", {"start": v(10.83, -0.07) * mm, "end": v(10.58, -0.55) * mm});
            skLineSegment(sketch, "E7202", {"start": v(10.58, -0.55) * mm, "end": v(10.37, -1) * mm});
            skLineSegment(sketch, "E7203", {"start": v(10.37, -1) * mm, "end": v(10.18, -1.45) * mm});
            skLineSegment(sketch, "E7204", {"start": v(10.18, -1.45) * mm, "end": v(10.02, -1.87) * mm});
            skLineSegment(sketch, "E7205", {"start": v(10.02, -1.87) * mm, "end": v(9.9, -2.28) * mm});
            skLineSegment(sketch, "E7206", {"start": v(9.9, -2.28) * mm, "end": v(9.85, -2.48) * mm});
            skLineSegment(sketch, "E7207", {"start": v(9.85, -2.48) * mm, "end": v(9.81, -2.67) * mm});
            skLineSegment(sketch, "E7208", {"start": v(9.81, -2.67) * mm, "end": v(9.78, -2.87) * mm});
            skLineSegment(sketch, "E7209", {"start": v(9.78, -2.87) * mm, "end": v(9.76, -3.06) * mm});
            skLineSegment(sketch, "E7210", {"start": v(9.76, -3.06) * mm, "end": v(9.75, -3.25) * mm});
            skLineSegment(sketch, "E7211", {"start": v(9.75, -3.25) * mm, "end": v(9.74, -3.43) * mm});
            skLineSegment(sketch, "E7212", {"start": v(9.74, -3.43) * mm, "end": v(9.75, -3.55) * mm});
            skLineSegment(sketch, "E7213", {"start": v(9.75, -3.55) * mm, "end": v(9.75, -3.61) * mm});
            skLineSegment(sketch, "E7214", {"start": v(9.75, -3.61) * mm, "end": v(9.76, -3.67) * mm});
            skLineSegment(sketch, "E7215", {"start": v(9.76, -3.67) * mm, "end": v(9.76, -3.72) * mm});
            skLineSegment(sketch, "E7216", {"start": v(9.76, -3.72) * mm, "end": v(9.77, -3.77) * mm});
            skLineSegment(sketch, "E7217", {"start": v(9.77, -3.77) * mm, "end": v(9.78, -3.82) * mm});
            skLineSegment(sketch, "E7218", {"start": v(9.78, -3.82) * mm, "end": v(9.8, -3.87) * mm});
            skLineSegment(sketch, "E7219", {"start": v(9.8, -3.87) * mm, "end": v(9.8, -3.92) * mm});
            skLineSegment(sketch, "E7220", {"start": v(9.8, -3.92) * mm, "end": v(9.82, -3.96) * mm});
            skLineSegment(sketch, "E7221", {"start": v(9.82, -3.96) * mm, "end": v(9.84, -4) * mm});
            skLineSegment(sketch, "E7222", {"start": v(9.84, -4) * mm, "end": v(9.86, -4.04) * mm});
            skLineSegment(sketch, "E7223", {"start": v(9.86, -4.04) * mm, "end": v(9.87, -4.08) * mm});
            skLineSegment(sketch, "E7224", {"start": v(9.87, -4.08) * mm, "end": v(9.9, -4.12) * mm});
            skLineSegment(sketch, "E7225", {"start": v(9.9, -4.12) * mm, "end": v(9.92, -4.15) * mm});
            skLineSegment(sketch, "E7226", {"start": v(9.92, -4.15) * mm, "end": v(9.94, -4.18) * mm});
            skLineSegment(sketch, "E7227", {"start": v(9.94, -4.18) * mm, "end": v(9.97, -4.21) * mm});
            skLineSegment(sketch, "E7228", {"start": v(9.97, -4.21) * mm, "end": v(10, -4.24) * mm});
            skLineSegment(sketch, "E7229", {"start": v(10, -4.24) * mm, "end": v(10.02, -4.27) * mm});
            skLineSegment(sketch, "E7230", {"start": v(10.02, -4.27) * mm, "end": v(10.05, -4.3) * mm});
            skLineSegment(sketch, "E7231", {"start": v(10.05, -4.3) * mm, "end": v(10.09, -4.31) * mm});
            skLineSegment(sketch, "E7232", {"start": v(10.09, -4.31) * mm, "end": v(10.12, -4.33) * mm});
            skLineSegment(sketch, "E7233", {"start": v(10.12, -4.33) * mm, "end": v(10.15, -4.35) * mm});
            skLineSegment(sketch, "E7234", {"start": v(10.15, -4.35) * mm, "end": v(10.2, -4.37) * mm});
            skLineSegment(sketch, "E7235", {"start": v(10.2, -4.37) * mm, "end": v(10.23, -4.38) * mm});
            skLineSegment(sketch, "E7236", {"start": v(10.23, -4.38) * mm, "end": v(10.27, -4.4) * mm});
            skLineSegment(sketch, "E7237", {"start": v(10.27, -4.4) * mm, "end": v(10.3, -4.4) * mm});
            skLineSegment(sketch, "E7238", {"start": v(10.3, -4.4) * mm, "end": v(10.35, -4.42) * mm});
            skLineSegment(sketch, "E7239", {"start": v(10.35, -4.42) * mm, "end": v(10.4, -4.42) * mm});
            skLineSegment(sketch, "E7240", {"start": v(10.4, -4.42) * mm, "end": v(10.44, -4.43) * mm});
            skLineSegment(sketch, "E7241", {"start": v(10.44, -4.43) * mm, "end": v(10.49, -4.43) * mm});
            skLineSegment(sketch, "E7242", {"start": v(10.49, -4.43) * mm, "end": v(10.54, -4.43) * mm});
            skLineSegment(sketch, "E7243", {"start": v(10.54, -4.43) * mm, "end": v(10.6, -4.43) * mm});
            skLineSegment(sketch, "E7244", {"start": v(10.6, -4.43) * mm, "end": v(10.68, -4.42) * mm});
            skLineSegment(sketch, "E7245", {"start": v(10.68, -4.42) * mm, "end": v(10.76, -4.41) * mm});
            skLineSegment(sketch, "E7246", {"start": v(10.76, -4.41) * mm, "end": v(10.83, -4.4) * mm});
            skLineSegment(sketch, "E7247", {"start": v(10.83, -4.4) * mm, "end": v(10.91, -4.38) * mm});
            skLineSegment(sketch, "E7248", {"start": v(10.91, -4.38) * mm, "end": v(11, -4.35) * mm});
            skLineSegment(sketch, "E7249", {"start": v(11, -4.35) * mm, "end": v(11.08, -4.32) * mm});
            skLineSegment(sketch, "E7250", {"start": v(11.08, -4.32) * mm, "end": v(11.17, -4.29) * mm});
            skLineSegment(sketch, "E7251", {"start": v(11.17, -4.29) * mm, "end": v(11.26, -4.25) * mm});
            skLineSegment(sketch, "E7252", {"start": v(11.26, -4.25) * mm, "end": v(11.36, -4.2) * mm});
            skLineSegment(sketch, "E7253", {"start": v(11.36, -4.2) * mm, "end": v(11.45, -4.16) * mm});
            skLineSegment(sketch, "E7254", {"start": v(11.45, -4.16) * mm, "end": v(11.55, -4.1) * mm});
            skLineSegment(sketch, "E7255", {"start": v(11.55, -4.1) * mm, "end": v(11.65, -4.05) * mm});
            skLineSegment(sketch, "E7256", {"start": v(11.65, -4.05) * mm, "end": v(11.86, -3.92) * mm});
            skLineSegment(sketch, "E7257", {"start": v(11.86, -3.92) * mm, "end": v(11.97, -3.85) * mm});
            skLineSegment(sketch, "E7258", {"start": v(11.97, -3.85) * mm, "end": v(12.08, -3.78) * mm});
            skLineSegment(sketch, "E7259", {"start": v(12.08, -3.78) * mm, "end": v(12.2, -3.7) * mm});
            skLineSegment(sketch, "E7260", {"start": v(12.2, -3.7) * mm, "end": v(12.46, -3.52) * mm});
            skLineSegment(sketch, "E7261", {"start": v(12.46, -3.52) * mm, "end": v(12.73, -3.32) * mm});
            skLineSegment(sketch, "E7262", {"start": v(12.73, -3.32) * mm, "end": v(13.01, -3.1) * mm});
            skLineSegment(sketch, "E7263", {"start": v(13.01, -3.1) * mm, "end": v(13.32, -2.87) * mm});
            skLineSegment(sketch, "E7264", {"start": v(13.32, -2.87) * mm, "end": v(13.65, -2.61) * mm});
            skLineSegment(sketch, "E7265", {"start": v(13.65, -2.61) * mm, "end": v(14, -2.34) * mm});
            skLineSegment(sketch, "E7266", {"start": v(14, -2.34) * mm, "end": v(14.36, -2.05) * mm});
            skLineSegment(sketch, "E7267", {"start": v(14.36, -2.05) * mm, "end": v(14.36, -3.01) * mm});
            skLineSegment(sketch, "E7268", {"start": v(14.36, -3.01) * mm, "end": v(13.88, -3.53) * mm});
            skLineSegment(sketch, "E7269", {"start": v(13.88, -3.53) * mm, "end": v(13.41, -4) * mm});
            skLineSegment(sketch, "E7270", {"start": v(13.41, -4) * mm, "end": v(12.96, -4.45) * mm});
            skLineSegment(sketch, "E7271", {"start": v(12.96, -4.45) * mm, "end": v(12.53, -4.87) * mm});
            skLineSegment(sketch, "E7272", {"start": v(12.53, -4.87) * mm, "end": v(12.11, -5.25) * mm});
            skLineSegment(sketch, "E7273", {"start": v(12.11, -5.25) * mm, "end": v(11.71, -5.6) * mm});
            skLineSegment(sketch, "E7274", {"start": v(11.71, -5.6) * mm, "end": v(11.33, -5.91) * mm});
            skLineSegment(sketch, "E7275", {"start": v(11.33, -5.91) * mm, "end": v(10.96, -6.2) * mm});
            skLineSegment(sketch, "E7276", {"start": v(10.96, -6.2) * mm, "end": v(10.6, -6.44) * mm});
            skLineSegment(sketch, "E7277", {"start": v(10.6, -6.44) * mm, "end": v(10.44, -6.55) * mm});
            skLineSegment(sketch, "E7278", {"start": v(10.44, -6.55) * mm, "end": v(10.27, -6.66) * mm});
            skLineSegment(sketch, "E7279", {"start": v(10.27, -6.66) * mm, "end": v(10.1, -6.75) * mm});
            skLineSegment(sketch, "E7280", {"start": v(10.1, -6.75) * mm, "end": v(9.95, -6.84) * mm});
            skLineSegment(sketch, "E7281", {"start": v(9.95, -6.84) * mm, "end": v(9.8, -6.92) * mm});
            skLineSegment(sketch, "E7282", {"start": v(9.8, -6.92) * mm, "end": v(9.65, -6.99) * mm});
            skLineSegment(sketch, "E7283", {"start": v(9.65, -6.99) * mm, "end": v(9.5, -7.05) * mm});
            skLineSegment(sketch, "E7284", {"start": v(9.5, -7.05) * mm, "end": v(9.36, -7.1) * mm});
            skLineSegment(sketch, "E7285", {"start": v(9.36, -7.1) * mm, "end": v(9.22, -7.15) * mm});
            skLineSegment(sketch, "E7286", {"start": v(9.22, -7.15) * mm, "end": v(9.08, -7.19) * mm});
            skLineSegment(sketch, "E7287", {"start": v(9.08, -7.19) * mm, "end": v(8.95, -7.21) * mm});
            skLineSegment(sketch, "E7288", {"start": v(8.95, -7.21) * mm, "end": v(8.83, -7.23) * mm});
            skLineSegment(sketch, "E7289", {"start": v(8.83, -7.23) * mm, "end": v(8.7, -7.25) * mm});
            skLineSegment(sketch, "E7290", {"start": v(8.7, -7.25) * mm, "end": v(8.59, -7.25) * mm});
            skLineSegment(sketch, "E7291", {"start": v(8.59, -7.25) * mm, "end": v(8.5, -7.25) * mm});
            skLineSegment(sketch, "E7292", {"start": v(8.5, -7.25) * mm, "end": v(8.43, -7.24) * mm});
            skLineSegment(sketch, "E7293", {"start": v(8.43, -7.24) * mm, "end": v(8.35, -7.23) * mm});
            skLineSegment(sketch, "E7294", {"start": v(8.35, -7.23) * mm, "end": v(8.28, -7.22) * mm});
            skLineSegment(sketch, "E7295", {"start": v(8.28, -7.22) * mm, "end": v(8.2, -7.2) * mm});
            skLineSegment(sketch, "E7296", {"start": v(8.2, -7.2) * mm, "end": v(8.13, -7.18) * mm});
            skLineSegment(sketch, "E7297", {"start": v(8.13, -7.18) * mm, "end": v(8.06, -7.15) * mm});
            skLineSegment(sketch, "E7298", {"start": v(8.06, -7.15) * mm, "end": v(8, -7.12) * mm});
            skLineSegment(sketch, "E7299", {"start": v(8, -7.12) * mm, "end": v(7.93, -7.1) * mm});
            skLineSegment(sketch, "E7300", {"start": v(7.93, -7.1) * mm, "end": v(7.87, -7.05) * mm});
            skLineSegment(sketch, "E7301", {"start": v(7.87, -7.05) * mm, "end": v(7.8, -7.01) * mm});
            skLineSegment(sketch, "E7302", {"start": v(7.8, -7.01) * mm, "end": v(7.75, -6.97) * mm});
            skLineSegment(sketch, "E7303", {"start": v(7.75, -6.97) * mm, "end": v(7.7, -6.92) * mm});
            skLineSegment(sketch, "E7304", {"start": v(7.7, -6.92) * mm, "end": v(7.64, -6.86) * mm});
            skLineSegment(sketch, "E7305", {"start": v(7.64, -6.86) * mm, "end": v(7.58, -6.8) * mm});
            skLineSegment(sketch, "E7306", {"start": v(7.58, -6.8) * mm, "end": v(7.53, -6.75) * mm});
            skLineSegment(sketch, "E7307", {"start": v(7.53, -6.75) * mm, "end": v(7.48, -6.68) * mm});
            skLineSegment(sketch, "E7308", {"start": v(7.48, -6.68) * mm, "end": v(7.44, -6.61) * mm});
            skLineSegment(sketch, "E7309", {"start": v(7.44, -6.61) * mm, "end": v(7.4, -6.55) * mm});
            skLineSegment(sketch, "E7310", {"start": v(7.4, -6.55) * mm, "end": v(7.36, -6.47) * mm});
            skLineSegment(sketch, "E7311", {"start": v(7.36, -6.47) * mm, "end": v(7.33, -6.4) * mm});
            skLineSegment(sketch, "E7312", {"start": v(7.33, -6.4) * mm, "end": v(7.3, -6.33) * mm});
            skLineSegment(sketch, "E7313", {"start": v(7.3, -6.33) * mm, "end": v(7.26, -6.25) * mm});
            skLineSegment(sketch, "E7314", {"start": v(7.26, -6.25) * mm, "end": v(7.24, -6.17) * mm});
            skLineSegment(sketch, "E7315", {"start": v(7.24, -6.17) * mm, "end": v(7.22, -6.08) * mm});
            skLineSegment(sketch, "E7316", {"start": v(7.22, -6.08) * mm, "end": v(7.18, -5.91) * mm});
            skLineSegment(sketch, "E7317", {"start": v(7.18, -5.91) * mm, "end": v(7.15, -5.73) * mm});
            skLineSegment(sketch, "E7318", {"start": v(7.15, -5.73) * mm, "end": v(7.14, -5.54) * mm});
            skLineSegment(sketch, "E7319", {"start": v(7.14, -5.54) * mm, "end": v(7.14, -5.44) * mm});
            skLineSegment(sketch, "E7320", {"start": v(7.14, -5.44) * mm, "end": v(7.14, -5.3) * mm});
            skLineSegment(sketch, "E7321", {"start": v(7.14, -5.3) * mm, "end": v(7.15, -5.16) * mm});
            skLineSegment(sketch, "E7322", {"start": v(7.15, -5.16) * mm, "end": v(7.17, -5.01) * mm});
            skLineSegment(sketch, "E7323", {"start": v(7.17, -5.01) * mm, "end": v(7.2, -4.86) * mm});
            skLineSegment(sketch, "E7324", {"start": v(7.2, -4.86) * mm, "end": v(7.23, -4.7) * mm});
            skLineSegment(sketch, "E7325", {"start": v(7.23, -4.7) * mm, "end": v(7.26, -4.53) * mm});
            skLineSegment(sketch, "E7326", {"start": v(7.26, -4.53) * mm, "end": v(7.3, -4.35) * mm});
            skLineSegment(sketch, "E7327", {"start": v(7.3, -4.35) * mm, "end": v(7.36, -4.17) * mm});
            skLineSegment(sketch, "E7328", {"start": v(7.36, -4.17) * mm, "end": v(7.39, -4.08) * mm});
            skLineSegment(sketch, "E7329", {"start": v(7.39, -4.08) * mm, "end": v(7.42, -3.98) * mm});
            skLineSegment(sketch, "E7330", {"start": v(7.42, -3.98) * mm, "end": v(7.46, -3.87) * mm});
            skLineSegment(sketch, "E7331", {"start": v(7.46, -3.87) * mm, "end": v(7.5, -3.76) * mm});
            skLineSegment(sketch, "E7332", {"start": v(7.5, -3.76) * mm, "end": v(7.54, -3.64) * mm});
            skLineSegment(sketch, "E7333", {"start": v(7.54, -3.64) * mm, "end": v(7.58, -3.51) * mm});
            skLineSegment(sketch, "E7334", {"start": v(7.58, -3.51) * mm, "end": v(7.63, -3.38) * mm});
            skLineSegment(sketch, "E7335", {"start": v(7.63, -3.38) * mm, "end": v(7.68, -3.25) * mm});
            skLineSegment(sketch, "E7336", {"start": v(7.68, -3.25) * mm, "end": v(7.78, -2.96) * mm});
            skLineSegment(sketch, "E7337", {"start": v(7.78, -2.96) * mm, "end": v(7.9, -2.64) * mm});
            skLineSegment(sketch, "E7338", {"start": v(7.9, -2.64) * mm, "end": v(8.03, -2.3) * mm});
            skLineSegment(sketch, "E7339", {"start": v(8.03, -2.3) * mm, "end": v(8.17, -1.94) * mm});
            skLineSegment(sketch, "E7340", {"start": v(8.17, -1.94) * mm, "end": v(8.07, -2.03) * mm});
            skLineSegment(sketch, "E7341", {"start": v(8.07, -2.03) * mm, "end": v(7.87, -2.2) * mm});
            skLineSegment(sketch, "E7342", {"start": v(7.87, -2.2) * mm, "end": v(7.78, -2.3) * mm});
            skLineSegment(sketch, "E7343", {"start": v(7.78, -2.3) * mm, "end": v(7.7, -2.37) * mm});
            skLineSegment(sketch, "E7344", {"start": v(7.7, -2.37) * mm, "end": v(7.52, -2.52) * mm});
            skLineSegment(sketch, "E7345", {"start": v(7.52, -2.52) * mm, "end": v(7.44, -2.6) * mm});
            skLineSegment(sketch, "E7346", {"start": v(7.44, -2.6) * mm, "end": v(7.37, -2.66) * mm});
            skLineSegment(sketch, "E7347", {"start": v(7.37, -2.66) * mm, "end": v(7.3, -2.73) * mm});
            skLineSegment(sketch, "E7348", {"start": v(7.3, -2.73) * mm, "end": v(7.21, -2.8) * mm});
            skLineSegment(sketch, "E7349", {"start": v(7.21, -2.8) * mm, "end": v(7.13, -2.88) * mm});
            skLineSegment(sketch, "E7350", {"start": v(7.13, -2.88) * mm, "end": v(7.04, -2.96) * mm});
            skLineSegment(sketch, "E7351", {"start": v(7.04, -2.96) * mm, "end": v(6.87, -3.1) * mm});
            skLineSegment(sketch, "E7352", {"start": v(6.87, -3.1) * mm, "end": v(6.78, -3.19) * mm});
            skLineSegment(sketch, "E7353", {"start": v(6.78, -3.19) * mm, "end": v(6.78, -2.2) * mm});
            skLineSegment(sketch, "E7354", {"start": v(6.78, -2.2) * mm, "end": v(6.97, -2.02) * mm});
            skLineSegment(sketch, "E7355", {"start": v(6.97, -2.02) * mm, "end": v(7.17, -1.84) * mm});
            skLineSegment(sketch, "E7356", {"start": v(7.17, -1.84) * mm, "end": v(7.37, -1.65) * mm});
            skLineSegment(sketch, "E7357", {"start": v(7.37, -1.65) * mm, "end": v(7.58, -1.43) * mm});
            skLineSegment(sketch, "E7358", {"start": v(7.58, -1.43) * mm, "end": v(7.8, -1.2) * mm});
            skLineSegment(sketch, "E7359", {"start": v(7.8, -1.2) * mm, "end": v(8, -0.97) * mm});
            skLineSegment(sketch, "E7360", {"start": v(8, -0.97) * mm, "end": v(8.23, -0.7) * mm});
            skLineSegment(sketch, "E7361", {"start": v(8.23, -0.7) * mm, "end": v(8.46, -0.44) * mm});
            skLineSegment(sketch, "E7362", {"start": v(8.46, -0.44) * mm, "end": v(8.93, 0.15) * mm});
            skLineSegment(sketch, "E7363", {"start": v(8.93, 0.15) * mm, "end": v(9.41, 0.8) * mm});
            skLineSegment(sketch, "E7364", {"start": v(9.41, 0.8) * mm, "end": v(9.92, 1.5) * mm});
            skLineSegment(sketch, "E7365", {"start": v(9.92, 1.5) * mm, "end": v(10.45, 2.28) * mm});
            skLineSegment(sketch, "E7366", {"start": v(10.45, 2.28) * mm, "end": v(10.35, 2.28) * mm});
            skLineSegment(sketch, "E7367", {"start": v(10.35, 2.28) * mm, "end": v(10.14, 2.3) * mm});
            skLineSegment(sketch, "E7368", {"start": v(10.14, 2.3) * mm, "end": v(10.05, 2.3) * mm});
            skLineSegment(sketch, "E7369", {"start": v(10.05, 2.3) * mm, "end": v(10, 2.3) * mm});
            skLineSegment(sketch, "E7370", {"start": v(10, 2.3) * mm, "end": v(9.95, 2.3) * mm});
            skLineSegment(sketch, "E7371", {"start": v(9.95, 2.3) * mm, "end": v(9.84, 2.3) * mm});
            skLineSegment(sketch, "E7372", {"start": v(9.84, 2.3) * mm, "end": v(9.72, 2.3) * mm});
            skLineSegment(sketch, "E7373", {"start": v(9.72, 2.3) * mm, "end": v(9.6, 2.3) * mm});
            skLineSegment(sketch, "E7374", {"start": v(9.6, 2.3) * mm, "end": v(9.4, 2.3) * mm});
            skLineSegment(sketch, "E7375", {"start": v(9.4, 2.3) * mm, "end": v(9.2, 2.3) * mm});
            skLineSegment(sketch, "E7376", {"start": v(9.2, 2.3) * mm, "end": v(9.02, 2.29) * mm});
            skLineSegment(sketch, "E7377", {"start": v(9.02, 2.29) * mm, "end": v(8.85, 2.28) * mm});
            skLineSegment(sketch, "E7378", {"start": v(8.85, 2.28) * mm, "end": v(8.78, 2.27) * mm});
            skLineSegment(sketch, "E7379", {"start": v(8.78, 2.27) * mm, "end": v(8.7, 2.26) * mm});
            skLineSegment(sketch, "E7380", {"start": v(8.7, 2.26) * mm, "end": v(8.63, 2.25) * mm});
            skLineSegment(sketch, "E7381", {"start": v(8.63, 2.25) * mm, "end": v(8.56, 2.24) * mm});
            skLineSegment(sketch, "E7382", {"start": v(8.56, 2.24) * mm, "end": v(8.5, 2.23) * mm});
            skLineSegment(sketch, "E7383", {"start": v(8.5, 2.23) * mm, "end": v(8.44, 2.22) * mm});
            skLineSegment(sketch, "E7384", {"start": v(8.44, 2.22) * mm, "end": v(8.38, 2.2) * mm});
            skLineSegment(sketch, "E7385", {"start": v(8.38, 2.2) * mm, "end": v(8.33, 2.2) * mm});
            skLineSegment(sketch, "E7386", {"start": v(8.33, 2.2) * mm, "end": v(8.24, 2.17) * mm});
            skLineSegment(sketch, "E7387", {"start": v(8.24, 2.17) * mm, "end": v(8.07, 2.12) * mm});
            skLineSegment(sketch, "E7388", {"start": v(8.07, 2.12) * mm, "end": v(8, 2.09) * mm});
            skLineSegment(sketch, "E7389", {"start": v(8, 2.09) * mm, "end": v(7.96, 2.08) * mm});
            skLineSegment(sketch, "E7390", {"start": v(7.96, 2.08) * mm, "end": v(7.94, 2.07) * mm});
            skLineSegment(sketch, "E7391", {"start": v(7.94, 2.07) * mm, "end": v(7.93, 2.07) * mm});
            skLineSegment(sketch, "E7392", {"start": v(7.93, 2.07) * mm, "end": v(7.91, 2.07) * mm});
            skLineSegment(sketch, "E7393", {"start": v(7.91, 2.07) * mm, "end": v(7.9, 2.06) * mm});
            skLineSegment(sketch, "E7394", {"start": v(7.9, 2.06) * mm, "end": v(7.88, 2.06) * mm});
            skLineSegment(sketch, "E7395", {"start": v(7.88, 2.06) * mm, "end": v(7.87, 2.06) * mm});
            skLineSegment(sketch, "E7396", {"start": v(7.87, 2.06) * mm, "end": v(7.86, 2.05) * mm});
            skLineSegment(sketch, "E7397", {"start": v(7.86, 2.05) * mm, "end": v(7.85, 2.05) * mm});
            skLineSegment(sketch, "E7398", {"start": v(7.85, 2.05) * mm, "end": v(7.84, 2.05) * mm});
            skLineSegment(sketch, "E7399", {"start": v(7.84, 2.05) * mm, "end": v(7.83, 2.05) * mm});
            skLineSegment(sketch, "E7400", {"start": v(7.83, 2.05) * mm, "end": v(7.82, 2.05) * mm});
            skLineSegment(sketch, "E7401", {"start": v(7.82, 2.05) * mm, "end": v(7.8, 2.05) * mm});
            skLineSegment(sketch, "E7402", {"start": v(7.8, 2.05) * mm, "end": v(7.8, 2.05) * mm});
            skLineSegment(sketch, "E7403", {"start": v(7.8, 2.05) * mm, "end": v(7.79, 2.05) * mm});
            skLineSegment(sketch, "E7404", {"start": v(7.79, 2.05) * mm, "end": v(7.78, 2.05) * mm});
            skLineSegment(sketch, "E7405", {"start": v(7.78, 2.05) * mm, "end": v(7.78, 2.05) * mm});
            skLineSegment(sketch, "E7406", {"start": v(7.78, 2.05) * mm, "end": v(7.77, 2.05) * mm});
            skLineSegment(sketch, "E7407", {"start": v(7.77, 2.05) * mm, "end": v(7.77, 2.05) * mm});
            skLineSegment(sketch, "E7408", {"start": v(7.77, 2.05) * mm, "end": v(7.76, 2.05) * mm});
            skLineSegment(sketch, "E7409", {"start": v(7.76, 2.05) * mm, "end": v(7.76, 2.05) * mm});
            skLineSegment(sketch, "E7410", {"start": v(7.76, 2.05) * mm, "end": v(7.76, 2.06) * mm});
            skLineSegment(sketch, "E7411", {"start": v(7.76, 2.06) * mm, "end": v(7.76, 2.06) * mm});
            skLineSegment(sketch, "E7412", {"start": v(7.76, 2.06) * mm, "end": v(7.75, 2.06) * mm});
            skLineSegment(sketch, "E7413", {"start": v(7.75, 2.06) * mm, "end": v(7.75, 2.06) * mm});
            skLineSegment(sketch, "E7414", {"start": v(7.75, 2.06) * mm, "end": v(7.75, 2.07) * mm});
            skLineSegment(sketch, "E7415", {"start": v(7.75, 2.07) * mm, "end": v(7.75, 2.07) * mm});
            skLineSegment(sketch, "E7416", {"start": v(7.75, 2.07) * mm, "end": v(7.74, 2.07) * mm});
            skLineSegment(sketch, "E7417", {"start": v(7.74, 2.07) * mm, "end": v(7.74, 2.08) * mm});
            skLineSegment(sketch, "E7418", {"start": v(7.74, 2.08) * mm, "end": v(7.74, 2.08) * mm});
            skLineSegment(sketch, "E7419", {"start": v(7.74, 2.08) * mm, "end": v(7.74, 2.09) * mm});
            skLineSegment(sketch, "E7420", {"start": v(7.74, 2.09) * mm, "end": v(7.74, 2.1) * mm});
            skLineSegment(sketch, "E7421", {"start": v(7.74, 2.1) * mm, "end": v(7.74, 2.1) * mm});
            skLineSegment(sketch, "E7422", {"start": v(7.74, 2.1) * mm, "end": v(7.73, 2.1) * mm});
            skLineSegment(sketch, "E7423", {"start": v(7.73, 2.1) * mm, "end": v(7.73, 2.12) * mm});
            skLineSegment(sketch, "E7424", {"start": v(7.73, 2.12) * mm, "end": v(7.73, 2.13) * mm});
            skLineSegment(sketch, "E7425", {"start": v(7.73, 2.13) * mm, "end": v(7.73, 2.13) * mm});
            skLineSegment(sketch, "E7426", {"start": v(7.73, 2.13) * mm, "end": v(7.73, 2.16) * mm});
            skLineSegment(sketch, "E7427", {"start": v(7.73, 2.16) * mm, "end": v(7.74, 2.2) * mm});
            skLineSegment(sketch, "E7428", {"start": v(7.74, 2.2) * mm, "end": v(7.74, 2.23) * mm});
            skLineSegment(sketch, "E7429", {"start": v(7.74, 2.23) * mm, "end": v(7.74, 2.26) * mm});
            skLineSegment(sketch, "E7430", {"start": v(7.74, 2.26) * mm, "end": v(7.75, 2.33) * mm});
            skLineSegment(sketch, "E7431", {"start": v(7.75, 2.33) * mm, "end": v(7.77, 2.4) * mm});
            skLineSegment(sketch, "E7432", {"start": v(7.77, 2.4) * mm, "end": v(7.8, 2.48) * mm});
            skLineSegment(sketch, "E7433", {"start": v(7.8, 2.48) * mm, "end": v(7.82, 2.56) * mm});
            skLineSegment(sketch, "E7434", {"start": v(7.82, 2.56) * mm, "end": v(7.85, 2.64) * mm});
            skLineSegment(sketch, "E7435", {"start": v(7.85, 2.64) * mm, "end": v(7.88, 2.73) * mm});
            skLineSegment(sketch, "E7436", {"start": v(7.88, 2.73) * mm, "end": v(7.92, 2.82) * mm});
            skLineSegment(sketch, "E7437", {"start": v(7.92, 2.82) * mm, "end": v(7.97, 2.92) * mm});
            skLineSegment(sketch, "E7438", {"start": v(7.97, 2.92) * mm, "end": v(8.01, 3.01) * mm});
            skLineSegment(sketch, "E7439", {"start": v(8.01, 3.01) * mm, "end": v(8.07, 3.12) * mm});
            skLineSegment(sketch, "E7440", {"start": v(8.07, 3.12) * mm, "end": v(8.12, 3.22) * mm});
            skLineSegment(sketch, "E7441", {"start": v(8.12, 3.22) * mm, "end": v(8.19, 3.33) * mm});
            skLineSegment(sketch, "E7442", {"start": v(8.19, 3.33) * mm, "end": v(8.25, 3.45) * mm});
            skLineSegment(sketch, "E7443", {"start": v(8.25, 3.45) * mm, "end": v(8.33, 3.56) * mm});
            skLineSegment(sketch, "E7444", {"start": v(8.33, 3.56) * mm, "end": v(8.44, 3.76) * mm});
            skLineSegment(sketch, "E7445", {"start": v(8.44, 3.76) * mm, "end": v(8.56, 3.94) * mm});
            skLineSegment(sketch, "E7446", {"start": v(8.56, 3.94) * mm, "end": v(8.68, 4.11) * mm});
            skLineSegment(sketch, "E7447", {"start": v(8.68, 4.11) * mm, "end": v(8.79, 4.27) * mm});
            skLineSegment(sketch, "E7448", {"start": v(8.79, 4.27) * mm, "end": v(8.9, 4.41) * mm});
            skLineSegment(sketch, "E7449", {"start": v(8.9, 4.41) * mm, "end": v(9, 4.54) * mm});
            skLineSegment(sketch, "E7450", {"start": v(9, 4.54) * mm, "end": v(9.12, 4.66) * mm});
            skLineSegment(sketch, "E7451", {"start": v(9.12, 4.66) * mm, "end": v(9.17, 4.71) * mm});
            skLineSegment(sketch, "E7452", {"start": v(9.17, 4.71) * mm, "end": v(9.22, 4.76) * mm});
            skLineSegment(sketch, "E7453", {"start": v(9.22, 4.76) * mm, "end": v(9.33, 4.86) * mm});
            skLineSegment(sketch, "E7454", {"start": v(9.33, 4.86) * mm, "end": v(9.45, 4.94) * mm});
            skLineSegment(sketch, "E7455", {"start": v(9.45, 4.94) * mm, "end": v(9.57, 5.02) * mm});
            skLineSegment(sketch, "E7456", {"start": v(9.57, 5.02) * mm, "end": v(9.7, 5.09) * mm});
            skLineSegment(sketch, "E7457", {"start": v(9.7, 5.09) * mm, "end": v(9.83, 5.15) * mm});
            skLineSegment(sketch, "E7458", {"start": v(9.83, 5.15) * mm, "end": v(9.97, 5.2) * mm});
            skLineSegment(sketch, "E7459", {"start": v(9.97, 5.2) * mm, "end": v(10.11, 5.25) * mm});
            skLineSegment(sketch, "E7460", {"start": v(10.11, 5.25) * mm, "end": v(10.26, 5.28) * mm});
            skLineSegment(sketch, "E7461", {"start": v(10.26, 5.28) * mm, "end": v(10.34, 5.3) * mm});
            skLineSegment(sketch, "E7462", {"start": v(10.34, 5.3) * mm, "end": v(10.43, 5.32) * mm});
            skLineSegment(sketch, "E7463", {"start": v(10.43, 5.32) * mm, "end": v(10.51, 5.33) * mm});
            skLineSegment(sketch, "E7464", {"start": v(10.51, 5.33) * mm, "end": v(10.7, 5.36) * mm});
            skLineSegment(sketch, "E7465", {"start": v(10.7, 5.36) * mm, "end": v(10.9, 5.38) * mm});
            skLineSegment(sketch, "E7466", {"start": v(10.9, 5.38) * mm, "end": v(11.12, 5.4) * mm});
            skLineSegment(sketch, "E7467", {"start": v(11.12, 5.4) * mm, "end": v(11.35, 5.42) * mm});
            skLineSegment(sketch, "E7468", {"start": v(11.35, 5.42) * mm, "end": v(11.6, 5.42) * mm});
            skLineSegment(sketch, "E7469", {"start": v(11.6, 5.42) * mm, "end": v(11.86, 5.43) * mm});
            skLineSegment(sketch, "E7470", {"start": v(11.86, 5.43) * mm, "end": v(12, 5.43) * mm});
            skLineSegment(sketch, "E7471", {"start": v(20.23, -2.6) * mm, "end": v(20.23, -2.96) * mm});
            skLineSegment(sketch, "E7472", {"start": v(20.23, -2.96) * mm, "end": v(20.23, -3.16) * mm});
            skLineSegment(sketch, "E7473", {"start": v(20.23, -3.16) * mm, "end": v(20.24, -3.26) * mm});
            skLineSegment(sketch, "E7474", {"start": v(20.24, -3.26) * mm, "end": v(20.25, -3.36) * mm});
            skLineSegment(sketch, "E7475", {"start": v(20.25, -3.36) * mm, "end": v(20.27, -3.45) * mm});
            skLineSegment(sketch, "E7476", {"start": v(20.27, -3.45) * mm, "end": v(20.28, -3.54) * mm});
            skLineSegment(sketch, "E7477", {"start": v(20.28, -3.54) * mm, "end": v(20.3, -3.63) * mm});
            skLineSegment(sketch, "E7478", {"start": v(20.3, -3.63) * mm, "end": v(20.33, -3.72) * mm});
            skLineSegment(sketch, "E7479", {"start": v(20.33, -3.72) * mm, "end": v(20.36, -3.8) * mm});
            skLineSegment(sketch, "E7480", {"start": v(20.36, -3.8) * mm, "end": v(20.39, -3.88) * mm});
            skLineSegment(sketch, "E7481", {"start": v(20.39, -3.88) * mm, "end": v(20.42, -3.95) * mm});
            skLineSegment(sketch, "E7482", {"start": v(20.42, -3.95) * mm, "end": v(20.46, -4.03) * mm});
            skLineSegment(sketch, "E7483", {"start": v(20.46, -4.03) * mm, "end": v(20.5, -4.1) * mm});
            skLineSegment(sketch, "E7484", {"start": v(20.5, -4.1) * mm, "end": v(20.55, -4.16) * mm});
            skLineSegment(sketch, "E7485", {"start": v(20.55, -4.16) * mm, "end": v(20.6, -4.23) * mm});
            skLineSegment(sketch, "E7486", {"start": v(20.6, -4.23) * mm, "end": v(20.64, -4.29) * mm});
            skLineSegment(sketch, "E7487", {"start": v(20.64, -4.29) * mm, "end": v(20.7, -4.34) * mm});
            skLineSegment(sketch, "E7488", {"start": v(20.7, -4.34) * mm, "end": v(20.75, -4.4) * mm});
            skLineSegment(sketch, "E7489", {"start": v(20.75, -4.4) * mm, "end": v(20.81, -4.45) * mm});
            skLineSegment(sketch, "E7490", {"start": v(20.81, -4.45) * mm, "end": v(20.87, -4.5) * mm});
            skLineSegment(sketch, "E7491", {"start": v(20.87, -4.5) * mm, "end": v(20.93, -4.54) * mm});
            skLineSegment(sketch, "E7492", {"start": v(20.93, -4.54) * mm, "end": v(21, -4.58) * mm});
            skLineSegment(sketch, "E7493", {"start": v(21, -4.58) * mm, "end": v(21.06, -4.61) * mm});
            skLineSegment(sketch, "E7494", {"start": v(21.06, -4.61) * mm, "end": v(21.13, -4.65) * mm});
            skLineSegment(sketch, "E7495", {"start": v(21.13, -4.65) * mm, "end": v(21.2, -4.67) * mm});
            skLineSegment(sketch, "E7496", {"start": v(21.2, -4.67) * mm, "end": v(21.27, -4.7) * mm});
            skLineSegment(sketch, "E7497", {"start": v(21.27, -4.7) * mm, "end": v(21.34, -4.72) * mm});
            skLineSegment(sketch, "E7498", {"start": v(21.34, -4.72) * mm, "end": v(21.42, -4.73) * mm});
            skLineSegment(sketch, "E7499", {"start": v(21.42, -4.73) * mm, "end": v(21.5, -4.75) * mm});
            skLineSegment(sketch, "E7500", {"start": v(21.5, -4.75) * mm, "end": v(21.58, -4.76) * mm});
            skLineSegment(sketch, "E7501", {"start": v(21.58, -4.76) * mm, "end": v(21.66, -4.76) * mm});
            skLineSegment(sketch, "E7502", {"start": v(21.66, -4.76) * mm, "end": v(21.74, -4.76) * mm});
            skLineSegment(sketch, "E7503", {"start": v(21.74, -4.76) * mm, "end": v(21.92, -4.76) * mm});
            skLineSegment(sketch, "E7504", {"start": v(21.92, -4.76) * mm, "end": v(22.1, -4.74) * mm});
            skLineSegment(sketch, "E7505", {"start": v(22.1, -4.74) * mm, "end": v(22.28, -4.72) * mm});
            skLineSegment(sketch, "E7506", {"start": v(22.28, -4.72) * mm, "end": v(22.46, -4.68) * mm});
            skLineSegment(sketch, "E7507", {"start": v(22.46, -4.68) * mm, "end": v(22.65, -4.63) * mm});
            skLineSegment(sketch, "E7508", {"start": v(22.65, -4.63) * mm, "end": v(22.83, -4.58) * mm});
            skLineSegment(sketch, "E7509", {"start": v(22.83, -4.58) * mm, "end": v(23.02, -4.5) * mm});
            skLineSegment(sketch, "E7510", {"start": v(23.02, -4.5) * mm, "end": v(23.2, -4.43) * mm});
            skLineSegment(sketch, "E7511", {"start": v(23.2, -4.43) * mm, "end": v(23.59, -4.25) * mm});
            skLineSegment(sketch, "E7512", {"start": v(23.59, -4.25) * mm, "end": v(23.97, -4.04) * mm});
            skLineSegment(sketch, "E7513", {"start": v(23.97, -4.04) * mm, "end": v(24.35, -3.81) * mm});
            skLineSegment(sketch, "E7514", {"start": v(24.35, -3.81) * mm, "end": v(24.72, -3.55) * mm});
            skLineSegment(sketch, "E7515", {"start": v(24.72, -3.55) * mm, "end": v(24.92, -3.4) * mm});
            skLineSegment(sketch, "E7516", {"start": v(24.92, -3.4) * mm, "end": v(25.12, -3.25) * mm});
            skLineSegment(sketch, "E7517", {"start": v(25.12, -3.25) * mm, "end": v(25.33, -3.08) * mm});
            skLineSegment(sketch, "E7518", {"start": v(25.33, -3.08) * mm, "end": v(25.56, -2.9) * mm});
            skLineSegment(sketch, "E7519", {"start": v(25.56, -2.9) * mm, "end": v(25.8, -2.72) * mm});
            skLineSegment(sketch, "E7520", {"start": v(25.8, -2.72) * mm, "end": v(26.04, -2.51) * mm});
            skLineSegment(sketch, "E7521", {"start": v(26.04, -2.51) * mm, "end": v(26.3, -2.3) * mm});
            skLineSegment(sketch, "E7522", {"start": v(26.3, -2.3) * mm, "end": v(26.56, -2.07) * mm});
            skLineSegment(sketch, "E7523", {"start": v(26.56, -2.07) * mm, "end": v(26.56, -2.96) * mm});
            skLineSegment(sketch, "E7524", {"start": v(26.56, -2.96) * mm, "end": v(26.15, -3.43) * mm});
            skLineSegment(sketch, "E7525", {"start": v(26.15, -3.43) * mm, "end": v(25.75, -3.88) * mm});
            skLineSegment(sketch, "E7526", {"start": v(25.75, -3.88) * mm, "end": v(25.36, -4.3) * mm});
            skLineSegment(sketch, "E7527", {"start": v(25.36, -4.3) * mm, "end": v(24.98, -4.7) * mm});
            skLineSegment(sketch, "E7528", {"start": v(24.98, -4.7) * mm, "end": v(24.6, -5.06) * mm});
            skLineSegment(sketch, "E7529", {"start": v(24.6, -5.06) * mm, "end": v(24.22, -5.4) * mm});
            skLineSegment(sketch, "E7530", {"start": v(24.22, -5.4) * mm, "end": v(23.85, -5.7) * mm});
            skLineSegment(sketch, "E7531", {"start": v(23.85, -5.7) * mm, "end": v(23.5, -5.98) * mm});
            skLineSegment(sketch, "E7532", {"start": v(23.5, -5.98) * mm, "end": v(23.13, -6.22) * mm});
            skLineSegment(sketch, "E7533", {"start": v(23.13, -6.22) * mm, "end": v(22.77, -6.43) * mm});
            skLineSegment(sketch, "E7534", {"start": v(22.77, -6.43) * mm, "end": v(22.41, -6.61) * mm});
            skLineSegment(sketch, "E7535", {"start": v(22.41, -6.61) * mm, "end": v(22.05, -6.76) * mm});
            skLineSegment(sketch, "E7536", {"start": v(22.05, -6.76) * mm, "end": v(21.69, -6.87) * mm});
            skLineSegment(sketch, "E7537", {"start": v(21.69, -6.87) * mm, "end": v(21.32, -6.95) * mm});
            skLineSegment(sketch, "E7538", {"start": v(21.32, -6.95) * mm, "end": v(21.14, -6.98) * mm});
            skLineSegment(sketch, "E7539", {"start": v(21.14, -6.98) * mm, "end": v(20.96, -7) * mm});
            skLineSegment(sketch, "E7540", {"start": v(20.96, -7) * mm, "end": v(20.77, -7.02) * mm});
            skLineSegment(sketch, "E7541", {"start": v(20.77, -7.02) * mm, "end": v(20.59, -7.02) * mm});
            skLineSegment(sketch, "E7542", {"start": v(20.59, -7.02) * mm, "end": v(20.43, -7.02) * mm});
            skLineSegment(sketch, "E7543", {"start": v(20.43, -7.02) * mm, "end": v(20.27, -7) * mm});
            skLineSegment(sketch, "E7544", {"start": v(20.27, -7) * mm, "end": v(20.12, -6.98) * mm});
            skLineSegment(sketch, "E7545", {"start": v(20.12, -6.98) * mm, "end": v(19.98, -6.96) * mm});
            skLineSegment(sketch, "E7546", {"start": v(19.98, -6.96) * mm, "end": v(19.84, -6.92) * mm});
            skLineSegment(sketch, "E7547", {"start": v(19.84, -6.92) * mm, "end": v(19.7, -6.88) * mm});
            skLineSegment(sketch, "E7548", {"start": v(19.7, -6.88) * mm, "end": v(19.56, -6.83) * mm});
            skLineSegment(sketch, "E7549", {"start": v(19.56, -6.83) * mm, "end": v(19.43, -6.77) * mm});
            skLineSegment(sketch, "E7550", {"start": v(19.43, -6.77) * mm, "end": v(19.3, -6.7) * mm});
            skLineSegment(sketch, "E7551", {"start": v(19.3, -6.7) * mm, "end": v(19.19, -6.63) * mm});
            skLineSegment(sketch, "E7552", {"start": v(19.19, -6.63) * mm, "end": v(19.07, -6.55) * mm});
            skLineSegment(sketch, "E7553", {"start": v(19.07, -6.55) * mm, "end": v(18.96, -6.46) * mm});
            skLineSegment(sketch, "E7554", {"start": v(18.96, -6.46) * mm, "end": v(18.85, -6.36) * mm});
            skLineSegment(sketch, "E7555", {"start": v(18.85, -6.36) * mm, "end": v(18.74, -6.26) * mm});
            skLineSegment(sketch, "E7556", {"start": v(18.74, -6.26) * mm, "end": v(18.64, -6.14) * mm});
            skLineSegment(sketch, "E7557", {"start": v(18.64, -6.14) * mm, "end": v(18.55, -6.02) * mm});
            skLineSegment(sketch, "E7558", {"start": v(18.55, -6.02) * mm, "end": v(18.46, -5.9) * mm});
            skLineSegment(sketch, "E7559", {"start": v(18.46, -5.9) * mm, "end": v(18.37, -5.76) * mm});
            skLineSegment(sketch, "E7560", {"start": v(18.37, -5.76) * mm, "end": v(18.3, -5.62) * mm});
            skLineSegment(sketch, "E7561", {"start": v(18.3, -5.62) * mm, "end": v(18.22, -5.48) * mm});
            skLineSegment(sketch, "E7562", {"start": v(18.22, -5.48) * mm, "end": v(18.15, -5.33) * mm});
            skLineSegment(sketch, "E7563", {"start": v(18.15, -5.33) * mm, "end": v(18.1, -5.17) * mm});
            skLineSegment(sketch, "E7564", {"start": v(18.1, -5.17) * mm, "end": v(18.03, -5) * mm});
            skLineSegment(sketch, "E7565", {"start": v(18.03, -5) * mm, "end": v(17.98, -4.84) * mm});
            skLineSegment(sketch, "E7566", {"start": v(17.98, -4.84) * mm, "end": v(17.94, -4.67) * mm});
            skLineSegment(sketch, "E7567", {"start": v(17.94, -4.67) * mm, "end": v(17.9, -4.49) * mm});
            skLineSegment(sketch, "E7568", {"start": v(17.9, -4.49) * mm, "end": v(17.84, -4.11) * mm});
            skLineSegment(sketch, "E7569", {"start": v(17.84, -4.11) * mm, "end": v(17.8, -3.71) * mm});
            skLineSegment(sketch, "E7570", {"start": v(17.8, -3.71) * mm, "end": v(17.8, -3.29) * mm});
            skLineSegment(sketch, "E7571", {"start": v(17.8, -3.29) * mm, "end": v(17.8, -2.91) * mm});
            skLineSegment(sketch, "E7572", {"start": v(17.8, -2.91) * mm, "end": v(17.84, -2.55) * mm});
            skLineSegment(sketch, "E7573", {"start": v(17.84, -2.55) * mm, "end": v(17.9, -2.2) * mm});
            skLineSegment(sketch, "E7574", {"start": v(17.9, -2.2) * mm, "end": v(17.97, -1.84) * mm});
            skLineSegment(sketch, "E7575", {"start": v(17.97, -1.84) * mm, "end": v(18.07, -1.5) * mm});
            skLineSegment(sketch, "E7576", {"start": v(18.07, -1.5) * mm, "end": v(18.2, -1.17) * mm});
            skLineSegment(sketch, "E7577", {"start": v(18.2, -1.17) * mm, "end": v(18.34, -0.85) * mm});
            skLineSegment(sketch, "E7578", {"start": v(18.34, -0.85) * mm, "end": v(18.5, -0.54) * mm});
            skLineSegment(sketch, "E7579", {"start": v(18.5, -0.54) * mm, "end": v(18.7, -0.23) * mm});
            skLineSegment(sketch, "E7580", {"start": v(18.7, -0.23) * mm, "end": v(18.92, 0.09) * mm});
            skLineSegment(sketch, "E7581", {"start": v(18.92, 0.09) * mm, "end": v(19.16, 0.4) * mm});
            skLineSegment(sketch, "E7582", {"start": v(19.16, 0.4) * mm, "end": v(19.44, 0.73) * mm});
            skLineSegment(sketch, "E7583", {"start": v(19.44, 0.73) * mm, "end": v(19.74, 1.06) * mm});
            skLineSegment(sketch, "E7584", {"start": v(19.74, 1.06) * mm, "end": v(20.07, 1.4) * mm});
            skLineSegment(sketch, "E7585", {"start": v(20.07, 1.4) * mm, "end": v(20.43, 1.73) * mm});
            skLineSegment(sketch, "E7586", {"start": v(20.43, 1.73) * mm, "end": v(20.82, 2.07) * mm});
            skLineSegment(sketch, "E7587", {"start": v(20.82, 2.07) * mm, "end": v(21.37, 2.52) * mm});
            skLineSegment(sketch, "E7588", {"start": v(21.37, 2.52) * mm, "end": v(21.91, 2.9) * mm});
            skLineSegment(sketch, "E7589", {"start": v(21.91, 2.9) * mm, "end": v(22.19, 3.07) * mm});
            skLineSegment(sketch, "E7590", {"start": v(22.19, 3.07) * mm, "end": v(22.46, 3.22) * mm});
            skLineSegment(sketch, "E7591", {"start": v(22.46, 3.22) * mm, "end": v(22.73, 3.37) * mm});
            skLineSegment(sketch, "E7592", {"start": v(22.73, 3.37) * mm, "end": v(23, 3.5) * mm});
            skLineSegment(sketch, "E7593", {"start": v(23, 3.5) * mm, "end": v(23.27, 3.6) * mm});
            skLineSegment(sketch, "E7594", {"start": v(23.27, 3.6) * mm, "end": v(23.53, 3.7) * mm});
            skLineSegment(sketch, "E7595", {"start": v(23.53, 3.7) * mm, "end": v(23.78, 3.78) * mm});
            skLineSegment(sketch, "E7596", {"start": v(23.78, 3.78) * mm, "end": v(24.03, 3.85) * mm});
            skLineSegment(sketch, "E7597", {"start": v(24.03, 3.85) * mm, "end": v(24.27, 3.9) * mm});
            skLineSegment(sketch, "E7598", {"start": v(24.27, 3.9) * mm, "end": v(24.5, 3.94) * mm});
            skLineSegment(sketch, "E7599", {"start": v(24.5, 3.94) * mm, "end": v(24.72, 3.96) * mm});
            skLineSegment(sketch, "E7600", {"start": v(24.72, 3.96) * mm, "end": v(24.94, 3.97) * mm});
            skLineSegment(sketch, "E7601", {"start": v(24.94, 3.97) * mm, "end": v(25.1, 3.96) * mm});
            skLineSegment(sketch, "E7602", {"start": v(25.1, 3.96) * mm, "end": v(25.26, 3.95) * mm});
            skLineSegment(sketch, "E7603", {"start": v(25.26, 3.95) * mm, "end": v(25.34, 3.94) * mm});
            skLineSegment(sketch, "E7604", {"start": v(25.34, 3.94) * mm, "end": v(25.4, 3.92) * mm});
            skLineSegment(sketch, "E7605", {"start": v(25.4, 3.92) * mm, "end": v(25.48, 3.9) * mm});
            skLineSegment(sketch, "E7606", {"start": v(25.48, 3.9) * mm, "end": v(25.55, 3.89) * mm});
            skLineSegment(sketch, "E7607", {"start": v(25.55, 3.89) * mm, "end": v(25.61, 3.87) * mm});
            skLineSegment(sketch, "E7608", {"start": v(25.61, 3.87) * mm, "end": v(25.68, 3.84) * mm});
            skLineSegment(sketch, "E7609", {"start": v(25.68, 3.84) * mm, "end": v(25.74, 3.82) * mm});
            skLineSegment(sketch, "E7610", {"start": v(25.74, 3.82) * mm, "end": v(25.8, 3.8) * mm});
            skLineSegment(sketch, "E7611", {"start": v(25.8, 3.8) * mm, "end": v(25.85, 3.76) * mm});
            skLineSegment(sketch, "E7612", {"start": v(25.85, 3.76) * mm, "end": v(25.9, 3.73) * mm});
            skLineSegment(sketch, "E7613", {"start": v(25.9, 3.73) * mm, "end": v(25.96, 3.69) * mm});
            skLineSegment(sketch, "E7614", {"start": v(25.96, 3.69) * mm, "end": v(26, 3.65) * mm});
            skLineSegment(sketch, "E7615", {"start": v(26, 3.65) * mm, "end": v(26.06, 3.61) * mm});
            skLineSegment(sketch, "E7616", {"start": v(26.06, 3.61) * mm, "end": v(26.1, 3.57) * mm});
            skLineSegment(sketch, "E7617", {"start": v(26.1, 3.57) * mm, "end": v(26.15, 3.53) * mm});
            skLineSegment(sketch, "E7618", {"start": v(26.15, 3.53) * mm, "end": v(26.19, 3.48) * mm});
            skLineSegment(sketch, "E7619", {"start": v(26.19, 3.48) * mm, "end": v(26.22, 3.43) * mm});
            skLineSegment(sketch, "E7620", {"start": v(26.22, 3.43) * mm, "end": v(26.26, 3.38) * mm});
            skLineSegment(sketch, "E7621", {"start": v(26.26, 3.38) * mm, "end": v(26.29, 3.32) * mm});
            skLineSegment(sketch, "E7622", {"start": v(26.29, 3.32) * mm, "end": v(26.31, 3.27) * mm});
            skLineSegment(sketch, "E7623", {"start": v(26.31, 3.27) * mm, "end": v(26.34, 3.2) * mm});
            skLineSegment(sketch, "E7624", {"start": v(26.34, 3.2) * mm, "end": v(26.36, 3.15) * mm});
            skLineSegment(sketch, "E7625", {"start": v(26.36, 3.15) * mm, "end": v(26.37, 3.08) * mm});
            skLineSegment(sketch, "E7626", {"start": v(26.37, 3.08) * mm, "end": v(26.39, 3.02) * mm});
            skLineSegment(sketch, "E7627", {"start": v(26.39, 3.02) * mm, "end": v(26.4, 2.95) * mm});
            skLineSegment(sketch, "E7628", {"start": v(26.4, 2.95) * mm, "end": v(26.4, 2.88) * mm});
            skLineSegment(sketch, "E7629", {"start": v(26.4, 2.88) * mm, "end": v(26.41, 2.8) * mm});
            skLineSegment(sketch, "E7630", {"start": v(26.41, 2.8) * mm, "end": v(26.41, 2.73) * mm});
            skLineSegment(sketch, "E7631", {"start": v(26.41, 2.73) * mm, "end": v(26.41, 2.61) * mm});
            skLineSegment(sketch, "E7632", {"start": v(26.41, 2.61) * mm, "end": v(26.4, 2.5) * mm});
            skLineSegment(sketch, "E7633", {"start": v(26.4, 2.5) * mm, "end": v(26.4, 2.38) * mm});
            skLineSegment(sketch, "E7634", {"start": v(26.4, 2.38) * mm, "end": v(26.37, 2.27) * mm});
            skLineSegment(sketch, "E7635", {"start": v(26.37, 2.27) * mm, "end": v(26.35, 2.16) * mm});
            skLineSegment(sketch, "E7636", {"start": v(26.35, 2.16) * mm, "end": v(26.32, 2.04) * mm});
            skLineSegment(sketch, "E7637", {"start": v(26.32, 2.04) * mm, "end": v(26.28, 1.93) * mm});
            skLineSegment(sketch, "E7638", {"start": v(26.28, 1.93) * mm, "end": v(26.24, 1.81) * mm});
            skLineSegment(sketch, "E7639", {"start": v(26.24, 1.81) * mm, "end": v(26.15, 1.59) * mm});
            skLineSegment(sketch, "E7640", {"start": v(26.15, 1.59) * mm, "end": v(26.03, 1.36) * mm});
            skLineSegment(sketch, "E7641", {"start": v(26.03, 1.36) * mm, "end": v(25.9, 1.13) * mm});
            skLineSegment(sketch, "E7642", {"start": v(25.9, 1.13) * mm, "end": v(25.73, 0.9) * mm});
            skLineSegment(sketch, "E7643", {"start": v(25.73, 0.9) * mm, "end": v(25.55, 0.68) * mm});
            skLineSegment(sketch, "E7644", {"start": v(25.55, 0.68) * mm, "end": v(25.35, 0.46) * mm});
            skLineSegment(sketch, "E7645", {"start": v(25.35, 0.46) * mm, "end": v(25.12, 0.23) * mm});
            skLineSegment(sketch, "E7646", {"start": v(25.12, 0.23) * mm, "end": v(24.87, 0) * mm});
            skLineSegment(sketch, "E7647", {"start": v(24.87, 0) * mm, "end": v(24.6, -0.22) * mm});
            skLineSegment(sketch, "E7648", {"start": v(24.6, -0.22) * mm, "end": v(24.3, -0.44) * mm});
            skLineSegment(sketch, "E7649", {"start": v(24.3, -0.44) * mm, "end": v(24, -0.67) * mm});
            skLineSegment(sketch, "E7650", {"start": v(24, -0.67) * mm, "end": v(23.65, -0.89) * mm});
            skLineSegment(sketch, "E7651", {"start": v(23.65, -0.89) * mm, "end": v(23.3, -1.1) * mm});
            skLineSegment(sketch, "E7652", {"start": v(23.3, -1.1) * mm, "end": v(22.92, -1.33) * mm});
            skLineSegment(sketch, "E7653", {"start": v(22.92, -1.33) * mm, "end": v(22.52, -1.54) * mm});
            skLineSegment(sketch, "E7654", {"start": v(22.52, -1.54) * mm, "end": v(21.66, -1.97) * mm});
            skLineSegment(sketch, "E7655", {"start": v(21.66, -1.97) * mm, "end": v(20.73, -2.39) * mm});
            skLineSegment(sketch, "E7656", {"start": v(20.73, -2.39) * mm, "end": v(20.23, -2.6) * mm});
            skLineSegment(sketch, "E7657", {"start": v(20.37, -1.66) * mm, "end": v(21, -1.39) * mm});
            skLineSegment(sketch, "E7658", {"start": v(21, -1.39) * mm, "end": v(21.58, -1.09) * mm});
            skLineSegment(sketch, "E7659", {"start": v(21.58, -1.09) * mm, "end": v(21.85, -0.93) * mm});
            skLineSegment(sketch, "E7660", {"start": v(21.85, -0.93) * mm, "end": v(22.11, -0.76) * mm});
            skLineSegment(sketch, "E7661", {"start": v(22.11, -0.76) * mm, "end": v(22.36, -0.58) * mm});
            skLineSegment(sketch, "E7662", {"start": v(22.36, -0.58) * mm, "end": v(22.6, -0.4) * mm});
            skLineSegment(sketch, "E7663", {"start": v(22.6, -0.4) * mm, "end": v(22.82, -0.21) * mm});
            skLineSegment(sketch, "E7664", {"start": v(22.82, -0.21) * mm, "end": v(23.03, -0.03) * mm});
            skLineSegment(sketch, "E7665", {"start": v(23.03, -0.03) * mm, "end": v(23.22, 0.16) * mm});
            skLineSegment(sketch, "E7666", {"start": v(23.22, 0.16) * mm, "end": v(23.4, 0.34) * mm});
            skLineSegment(sketch, "E7667", {"start": v(23.4, 0.34) * mm, "end": v(23.56, 0.51) * mm});
            skLineSegment(sketch, "E7668", {"start": v(23.56, 0.51) * mm, "end": v(23.7, 0.69) * mm});
            skLineSegment(sketch, "E7669", {"start": v(23.7, 0.69) * mm, "end": v(23.84, 0.86) * mm});
            skLineSegment(sketch, "E7670", {"start": v(23.84, 0.86) * mm, "end": v(23.96, 1.03) * mm});
            skLineSegment(sketch, "E7671", {"start": v(23.96, 1.03) * mm, "end": v(24.01, 1.12) * mm});
            skLineSegment(sketch, "E7672", {"start": v(24.01, 1.12) * mm, "end": v(24.06, 1.2) * mm});
            skLineSegment(sketch, "E7673", {"start": v(24.06, 1.2) * mm, "end": v(24.1, 1.28) * mm});
            skLineSegment(sketch, "E7674", {"start": v(24.1, 1.28) * mm, "end": v(24.15, 1.36) * mm});
            skLineSegment(sketch, "E7675", {"start": v(24.15, 1.36) * mm, "end": v(24.2, 1.43) * mm});
            skLineSegment(sketch, "E7676", {"start": v(24.2, 1.43) * mm, "end": v(24.23, 1.5) * mm});
            skLineSegment(sketch, "E7677", {"start": v(24.23, 1.5) * mm, "end": v(24.26, 1.57) * mm});
            skLineSegment(sketch, "E7678", {"start": v(24.26, 1.57) * mm, "end": v(24.3, 1.63) * mm});
            skLineSegment(sketch, "E7679", {"start": v(24.3, 1.63) * mm, "end": v(24.32, 1.7) * mm});
            skLineSegment(sketch, "E7680", {"start": v(24.32, 1.7) * mm, "end": v(24.34, 1.75) * mm});
            skLineSegment(sketch, "E7681", {"start": v(24.34, 1.75) * mm, "end": v(24.36, 1.81) * mm});
            skLineSegment(sketch, "E7682", {"start": v(24.36, 1.81) * mm, "end": v(24.38, 1.86) * mm});
            skLineSegment(sketch, "E7683", {"start": v(24.38, 1.86) * mm, "end": v(24.38, 1.89) * mm});
            skLineSegment(sketch, "E7684", {"start": v(24.38, 1.89) * mm, "end": v(24.39, 1.91) * mm});
            skLineSegment(sketch, "E7685", {"start": v(24.39, 1.91) * mm, "end": v(24.4, 1.94) * mm});
            skLineSegment(sketch, "E7686", {"start": v(24.4, 1.94) * mm, "end": v(24.4, 1.96) * mm});
            skLineSegment(sketch, "E7687", {"start": v(24.4, 1.96) * mm, "end": v(24.4, 1.98) * mm});
            skLineSegment(sketch, "E7688", {"start": v(24.4, 1.98) * mm, "end": v(24.4, 2) * mm});
            skLineSegment(sketch, "E7689", {"start": v(24.4, 2) * mm, "end": v(24.4, 2.03) * mm});
            skLineSegment(sketch, "E7690", {"start": v(24.4, 2.03) * mm, "end": v(24.4, 2.05) * mm});
            skLineSegment(sketch, "E7691", {"start": v(24.4, 2.05) * mm, "end": v(24.4, 2.07) * mm});
            skLineSegment(sketch, "E7692", {"start": v(24.4, 2.07) * mm, "end": v(24.4, 2.09) * mm});
            skLineSegment(sketch, "E7693", {"start": v(24.4, 2.09) * mm, "end": v(24.4, 2.1) * mm});
            skLineSegment(sketch, "E7694", {"start": v(24.4, 2.1) * mm, "end": v(24.4, 2.12) * mm});
            skLineSegment(sketch, "E7695", {"start": v(24.4, 2.12) * mm, "end": v(24.4, 2.14) * mm});
            skLineSegment(sketch, "E7696", {"start": v(24.4, 2.14) * mm, "end": v(24.4, 2.16) * mm});
            skLineSegment(sketch, "E7697", {"start": v(24.4, 2.16) * mm, "end": v(24.39, 2.18) * mm});
            skLineSegment(sketch, "E7698", {"start": v(24.39, 2.18) * mm, "end": v(24.39, 2.2) * mm});
            skLineSegment(sketch, "E7699", {"start": v(24.39, 2.2) * mm, "end": v(24.38, 2.2) * mm});
            skLineSegment(sketch, "E7700", {"start": v(24.38, 2.2) * mm, "end": v(24.37, 2.22) * mm});
            skLineSegment(sketch, "E7701", {"start": v(24.37, 2.22) * mm, "end": v(24.37, 2.24) * mm});
            skLineSegment(sketch, "E7702", {"start": v(24.37, 2.24) * mm, "end": v(24.36, 2.25) * mm});
            skLineSegment(sketch, "E7703", {"start": v(24.36, 2.25) * mm, "end": v(24.35, 2.26) * mm});
            skLineSegment(sketch, "E7704", {"start": v(24.35, 2.26) * mm, "end": v(24.35, 2.27) * mm});
            skLineSegment(sketch, "E7705", {"start": v(24.35, 2.27) * mm, "end": v(24.34, 2.28) * mm});
            skLineSegment(sketch, "E7706", {"start": v(24.34, 2.28) * mm, "end": v(24.33, 2.3) * mm});
            skLineSegment(sketch, "E7707", {"start": v(24.33, 2.3) * mm, "end": v(24.32, 2.3) * mm});
            skLineSegment(sketch, "E7708", {"start": v(24.32, 2.3) * mm, "end": v(24.3, 2.31) * mm});
            skLineSegment(sketch, "E7709", {"start": v(24.3, 2.31) * mm, "end": v(24.3, 2.32) * mm});
            skLineSegment(sketch, "E7710", {"start": v(24.3, 2.32) * mm, "end": v(24.29, 2.33) * mm});
            skLineSegment(sketch, "E7711", {"start": v(24.29, 2.33) * mm, "end": v(24.27, 2.34) * mm});
            skLineSegment(sketch, "E7712", {"start": v(24.27, 2.34) * mm, "end": v(24.26, 2.35) * mm});
            skLineSegment(sketch, "E7713", {"start": v(24.26, 2.35) * mm, "end": v(24.25, 2.35) * mm});
            skLineSegment(sketch, "E7714", {"start": v(24.25, 2.35) * mm, "end": v(24.23, 2.36) * mm});
            skLineSegment(sketch, "E7715", {"start": v(24.23, 2.36) * mm, "end": v(24.22, 2.36) * mm});
            skLineSegment(sketch, "E7716", {"start": v(24.22, 2.36) * mm, "end": v(24.2, 2.37) * mm});
            skLineSegment(sketch, "E7717", {"start": v(24.2, 2.37) * mm, "end": v(24.19, 2.37) * mm});
            skLineSegment(sketch, "E7718", {"start": v(24.19, 2.37) * mm, "end": v(24.17, 2.37) * mm});
            skLineSegment(sketch, "E7719", {"start": v(24.17, 2.37) * mm, "end": v(24.15, 2.38) * mm});
            skLineSegment(sketch, "E7720", {"start": v(24.15, 2.38) * mm, "end": v(24.14, 2.38) * mm});
            skLineSegment(sketch, "E7721", {"start": v(24.14, 2.38) * mm, "end": v(24.12, 2.38) * mm});
            skLineSegment(sketch, "E7722", {"start": v(24.12, 2.38) * mm, "end": v(24.1, 2.38) * mm});
            skLineSegment(sketch, "E7723", {"start": v(24.1, 2.38) * mm, "end": v(24.08, 2.38) * mm});
            skLineSegment(sketch, "E7724", {"start": v(24.08, 2.38) * mm, "end": v(24.07, 2.38) * mm});
            skLineSegment(sketch, "E7725", {"start": v(24.07, 2.38) * mm, "end": v(24.05, 2.38) * mm});
            skLineSegment(sketch, "E7726", {"start": v(24.05, 2.38) * mm, "end": v(24.03, 2.37) * mm});
            skLineSegment(sketch, "E7727", {"start": v(24.03, 2.37) * mm, "end": v(24.01, 2.37) * mm});
            skLineSegment(sketch, "E7728", {"start": v(24.01, 2.37) * mm, "end": v(24, 2.37) * mm});
            skLineSegment(sketch, "E7729", {"start": v(24, 2.37) * mm, "end": v(23.95, 2.36) * mm});
            skLineSegment(sketch, "E7730", {"start": v(23.95, 2.36) * mm, "end": v(23.9, 2.35) * mm});
            skLineSegment(sketch, "E7731", {"start": v(23.9, 2.35) * mm, "end": v(23.86, 2.33) * mm});
            skLineSegment(sketch, "E7732", {"start": v(23.86, 2.33) * mm, "end": v(23.8, 2.31) * mm});
            skLineSegment(sketch, "E7733", {"start": v(23.8, 2.31) * mm, "end": v(23.76, 2.3) * mm});
            skLineSegment(sketch, "E7734", {"start": v(23.76, 2.3) * mm, "end": v(23.7, 2.27) * mm});
            skLineSegment(sketch, "E7735", {"start": v(23.7, 2.27) * mm, "end": v(23.65, 2.25) * mm});
            skLineSegment(sketch, "E7736", {"start": v(23.65, 2.25) * mm, "end": v(23.59, 2.22) * mm});
            skLineSegment(sketch, "E7737", {"start": v(23.59, 2.22) * mm, "end": v(23.52, 2.2) * mm});
            skLineSegment(sketch, "E7738", {"start": v(23.52, 2.2) * mm, "end": v(23.46, 2.16) * mm});
            skLineSegment(sketch, "E7739", {"start": v(23.46, 2.16) * mm, "end": v(23.4, 2.12) * mm});
            skLineSegment(sketch, "E7740", {"start": v(23.4, 2.12) * mm, "end": v(23.32, 2.09) * mm});
            skLineSegment(sketch, "E7741", {"start": v(23.32, 2.09) * mm, "end": v(23.25, 2.05) * mm});
            skLineSegment(sketch, "E7742", {"start": v(23.25, 2.05) * mm, "end": v(22.96, 1.87) * mm});
            skLineSegment(sketch, "E7743", {"start": v(22.96, 1.87) * mm, "end": v(22.66, 1.66) * mm});
            skLineSegment(sketch, "E7744", {"start": v(22.66, 1.66) * mm, "end": v(22.36, 1.43) * mm});
            skLineSegment(sketch, "E7745", {"start": v(22.36, 1.43) * mm, "end": v(22.06, 1.18) * mm});
            skLineSegment(sketch, "E7746", {"start": v(22.06, 1.18) * mm, "end": v(21.77, 0.9) * mm});
            skLineSegment(sketch, "E7747", {"start": v(21.77, 0.9) * mm, "end": v(21.5, 0.6) * mm});
            skLineSegment(sketch, "E7748", {"start": v(21.5, 0.6) * mm, "end": v(21.24, 0.27) * mm});
            skLineSegment(sketch, "E7749", {"start": v(21.24, 0.27) * mm, "end": v(21, -0.08) * mm});
            skLineSegment(sketch, "E7750", {"start": v(21, -0.08) * mm, "end": v(20.88, -0.26) * mm});
            skLineSegment(sketch, "E7751", {"start": v(20.88, -0.26) * mm, "end": v(20.77, -0.45) * mm});
            skLineSegment(sketch, "E7752", {"start": v(20.77, -0.45) * mm, "end": v(20.68, -0.64) * mm});
            skLineSegment(sketch, "E7753", {"start": v(20.68, -0.64) * mm, "end": v(20.6, -0.84) * mm});
            skLineSegment(sketch, "E7754", {"start": v(20.6, -0.84) * mm, "end": v(20.53, -1.03) * mm});
            skLineSegment(sketch, "E7755", {"start": v(20.53, -1.03) * mm, "end": v(20.46, -1.24) * mm});
            skLineSegment(sketch, "E7756", {"start": v(20.46, -1.24) * mm, "end": v(20.41, -1.44) * mm});
            skLineSegment(sketch, "E7757", {"start": v(20.41, -1.44) * mm, "end": v(20.37, -1.66) * mm});
            skLineSegment(sketch, "E7758", {"start": v(34.86, -4.06) * mm, "end": v(35.82, -3.2) * mm});
            skLineSegment(sketch, "E7759", {"start": v(35.82, -3.2) * mm, "end": v(36.71, -2.4) * mm});
            skLineSegment(sketch, "E7760", {"start": v(36.71, -2.4) * mm, "end": v(37.53, -1.67) * mm});
            skLineSegment(sketch, "E7761", {"start": v(37.53, -1.67) * mm, "end": v(37.92, -1.32) * mm});
            skLineSegment(sketch, "E7762", {"start": v(37.92, -1.32) * mm, "end": v(38.28, -1) * mm});
            skLineSegment(sketch, "E7763", {"start": v(38.28, -1) * mm, "end": v(38.63, -0.67) * mm});
            skLineSegment(sketch, "E7764", {"start": v(38.63, -0.67) * mm, "end": v(38.96, -0.37) * mm});
            skLineSegment(sketch, "E7765", {"start": v(38.96, -0.37) * mm, "end": v(39.27, -0.08) * mm});
            skLineSegment(sketch, "E7766", {"start": v(39.27, -0.08) * mm, "end": v(39.56, 0.18) * mm});
            skLineSegment(sketch, "E7767", {"start": v(39.56, 0.18) * mm, "end": v(39.83, 0.43) * mm});
            skLineSegment(sketch, "E7768", {"start": v(39.83, 0.43) * mm, "end": v(40.08, 0.67) * mm});
            skLineSegment(sketch, "E7769", {"start": v(40.08, 0.67) * mm, "end": v(40.31, 0.88) * mm});
            skLineSegment(sketch, "E7770", {"start": v(40.31, 0.88) * mm, "end": v(40.42, 0.98) * mm});
            skLineSegment(sketch, "E7771", {"start": v(40.42, 0.98) * mm, "end": v(40.53, 1.08) * mm});
            skLineSegment(sketch, "E7772", {"start": v(40.53, 1.08) * mm, "end": v(40.92, 1.44) * mm});
            skLineSegment(sketch, "E7773", {"start": v(40.92, 1.44) * mm, "end": v(41.3, 1.77) * mm});
            skLineSegment(sketch, "E7774", {"start": v(41.3, 1.77) * mm, "end": v(41.65, 2.07) * mm});
            skLineSegment(sketch, "E7775", {"start": v(41.65, 2.07) * mm, "end": v(41.81, 2.22) * mm});
            skLineSegment(sketch, "E7776", {"start": v(41.81, 2.22) * mm, "end": v(41.97, 2.35) * mm});
            skLineSegment(sketch, "E7777", {"start": v(41.97, 2.35) * mm, "end": v(42.05, 2.41) * mm});
            skLineSegment(sketch, "E7778", {"start": v(42.05, 2.41) * mm, "end": v(42.12, 2.47) * mm});
            skLineSegment(sketch, "E7779", {"start": v(42.12, 2.47) * mm, "end": v(42.19, 2.53) * mm});
            skLineSegment(sketch, "E7780", {"start": v(42.19, 2.53) * mm, "end": v(42.25, 2.58) * mm});
            skLineSegment(sketch, "E7781", {"start": v(42.25, 2.58) * mm, "end": v(42.32, 2.62) * mm});
            skLineSegment(sketch, "E7782", {"start": v(42.32, 2.62) * mm, "end": v(42.37, 2.67) * mm});
            skLineSegment(sketch, "E7783", {"start": v(42.37, 2.67) * mm, "end": v(42.43, 2.7) * mm});
            skLineSegment(sketch, "E7784", {"start": v(42.43, 2.7) * mm, "end": v(42.48, 2.74) * mm});
            skLineSegment(sketch, "E7785", {"start": v(42.48, 2.74) * mm, "end": v(42.5, 2.76) * mm});
            skLineSegment(sketch, "E7786", {"start": v(42.5, 2.76) * mm, "end": v(42.53, 2.77) * mm});
            skLineSegment(sketch, "E7787", {"start": v(42.53, 2.77) * mm, "end": v(42.55, 2.78) * mm});
            skLineSegment(sketch, "E7788", {"start": v(42.55, 2.78) * mm, "end": v(42.57, 2.8) * mm});
            skLineSegment(sketch, "E7789", {"start": v(42.57, 2.8) * mm, "end": v(42.6, 2.8) * mm});
            skLineSegment(sketch, "E7790", {"start": v(42.6, 2.8) * mm, "end": v(42.61, 2.82) * mm});
            skLineSegment(sketch, "E7791", {"start": v(42.61, 2.82) * mm, "end": v(42.63, 2.83) * mm});
            skLineSegment(sketch, "E7792", {"start": v(42.63, 2.83) * mm, "end": v(42.65, 2.84) * mm});
            skLineSegment(sketch, "E7793", {"start": v(42.65, 2.84) * mm, "end": v(42.67, 2.85) * mm});
            skLineSegment(sketch, "E7794", {"start": v(42.67, 2.85) * mm, "end": v(42.69, 2.85) * mm});
            skLineSegment(sketch, "E7795", {"start": v(42.69, 2.85) * mm, "end": v(42.7, 2.86) * mm});
            skLineSegment(sketch, "E7796", {"start": v(42.7, 2.86) * mm, "end": v(42.72, 2.86) * mm});
            skLineSegment(sketch, "E7797", {"start": v(42.72, 2.86) * mm, "end": v(42.72, 2.86) * mm});
            skLineSegment(sketch, "E7798", {"start": v(42.72, 2.86) * mm, "end": v(42.73, 2.87) * mm});
            skLineSegment(sketch, "E7799", {"start": v(42.73, 2.87) * mm, "end": v(42.74, 2.87) * mm});
            skLineSegment(sketch, "E7800", {"start": v(42.74, 2.87) * mm, "end": v(42.74, 2.87) * mm});
            skLineSegment(sketch, "E7801", {"start": v(42.74, 2.87) * mm, "end": v(42.75, 2.87) * mm});
            skLineSegment(sketch, "E7802", {"start": v(42.75, 2.87) * mm, "end": v(42.76, 2.87) * mm});
            skLineSegment(sketch, "E7803", {"start": v(42.76, 2.87) * mm, "end": v(42.76, 2.87) * mm});
            skLineSegment(sketch, "E7804", {"start": v(42.76, 2.87) * mm, "end": v(42.77, 2.87) * mm});
            skLineSegment(sketch, "E7805", {"start": v(42.77, 2.87) * mm, "end": v(42.79, 2.87) * mm});
            skLineSegment(sketch, "E7806", {"start": v(42.79, 2.87) * mm, "end": v(42.8, 2.87) * mm});
            skLineSegment(sketch, "E7807", {"start": v(42.8, 2.87) * mm, "end": v(42.83, 2.87) * mm});
            skLineSegment(sketch, "E7808", {"start": v(42.83, 2.87) * mm, "end": v(42.85, 2.86) * mm});
            skLineSegment(sketch, "E7809", {"start": v(42.85, 2.86) * mm, "end": v(42.87, 2.86) * mm});
            skLineSegment(sketch, "E7810", {"start": v(42.87, 2.86) * mm, "end": v(42.9, 2.85) * mm});
            skLineSegment(sketch, "E7811", {"start": v(42.9, 2.85) * mm, "end": v(42.91, 2.84) * mm});
            skLineSegment(sketch, "E7812", {"start": v(42.91, 2.84) * mm, "end": v(42.93, 2.83) * mm});
            skLineSegment(sketch, "E7813", {"start": v(42.93, 2.83) * mm, "end": v(42.95, 2.82) * mm});
            skLineSegment(sketch, "E7814", {"start": v(42.95, 2.82) * mm, "end": v(42.97, 2.8) * mm});
            skLineSegment(sketch, "E7815", {"start": v(42.97, 2.8) * mm, "end": v(43, 2.8) * mm});
            skLineSegment(sketch, "E7816", {"start": v(43, 2.8) * mm, "end": v(43.01, 2.78) * mm});
            skLineSegment(sketch, "E7817", {"start": v(43.01, 2.78) * mm, "end": v(43.03, 2.76) * mm});
            skLineSegment(sketch, "E7818", {"start": v(43.03, 2.76) * mm, "end": v(43.05, 2.74) * mm});
            skLineSegment(sketch, "E7819", {"start": v(43.05, 2.74) * mm, "end": v(43.07, 2.72) * mm});
            skLineSegment(sketch, "E7820", {"start": v(43.07, 2.72) * mm, "end": v(43.1, 2.7) * mm});
            skLineSegment(sketch, "E7821", {"start": v(43.1, 2.7) * mm, "end": v(43.11, 2.68) * mm});
            skLineSegment(sketch, "E7822", {"start": v(43.11, 2.68) * mm, "end": v(43.13, 2.66) * mm});
            skLineSegment(sketch, "E7823", {"start": v(43.13, 2.66) * mm, "end": v(43.17, 2.6) * mm});
            skLineSegment(sketch, "E7824", {"start": v(43.17, 2.6) * mm, "end": v(43.21, 2.55) * mm});
            skLineSegment(sketch, "E7825", {"start": v(43.21, 2.55) * mm, "end": v(43.25, 2.49) * mm});
            skLineSegment(sketch, "E7826", {"start": v(43.25, 2.49) * mm, "end": v(43.29, 2.42) * mm});
            skLineSegment(sketch, "E7827", {"start": v(43.29, 2.42) * mm, "end": v(43.33, 2.34) * mm});
            skLineSegment(sketch, "E7828", {"start": v(43.33, 2.34) * mm, "end": v(43.36, 2.26) * mm});
            skLineSegment(sketch, "E7829", {"start": v(43.36, 2.26) * mm, "end": v(43.4, 2.18) * mm});
            skLineSegment(sketch, "E7830", {"start": v(43.4, 2.18) * mm, "end": v(43.47, 2) * mm});
            skLineSegment(sketch, "E7831", {"start": v(43.47, 2) * mm, "end": v(43.54, 1.85) * mm});
            skLineSegment(sketch, "E7832", {"start": v(43.54, 1.85) * mm, "end": v(43.59, 1.7) * mm});
            skLineSegment(sketch, "E7833", {"start": v(43.59, 1.7) * mm, "end": v(43.63, 1.55) * mm});
            skLineSegment(sketch, "E7834", {"start": v(43.63, 1.55) * mm, "end": v(43.65, 1.48) * mm});
            skLineSegment(sketch, "E7835", {"start": v(43.65, 1.48) * mm, "end": v(43.66, 1.42) * mm});
            skLineSegment(sketch, "E7836", {"start": v(43.66, 1.42) * mm, "end": v(43.68, 1.35) * mm});
            skLineSegment(sketch, "E7837", {"start": v(43.68, 1.35) * mm, "end": v(43.69, 1.29) * mm});
            skLineSegment(sketch, "E7838", {"start": v(43.69, 1.29) * mm, "end": v(43.7, 1.23) * mm});
            skLineSegment(sketch, "E7839", {"start": v(43.7, 1.23) * mm, "end": v(43.7, 1.17) * mm});
            skLineSegment(sketch, "E7840", {"start": v(43.7, 1.17) * mm, "end": v(43.7, 1.12) * mm});
            skLineSegment(sketch, "E7841", {"start": v(43.7, 1.12) * mm, "end": v(43.7, 1.06) * mm});
            skLineSegment(sketch, "E7842", {"start": v(43.7, 1.06) * mm, "end": v(43.7, 1.05) * mm});
            skLineSegment(sketch, "E7843", {"start": v(43.7, 1.05) * mm, "end": v(43.7, 1.04) * mm});
            skLineSegment(sketch, "E7844", {"start": v(43.7, 1.04) * mm, "end": v(43.7, 1.04) * mm});
            skLineSegment(sketch, "E7845", {"start": v(43.7, 1.04) * mm, "end": v(43.7, 1.03) * mm});
            skLineSegment(sketch, "E7846", {"start": v(43.7, 1.03) * mm, "end": v(43.7, 1.02) * mm});
            skLineSegment(sketch, "E7847", {"start": v(43.7, 1.02) * mm, "end": v(43.7, 1) * mm});
            skLineSegment(sketch, "E7848", {"start": v(43.7, 1) * mm, "end": v(43.7, 1) * mm});
            skLineSegment(sketch, "E7849", {"start": v(43.7, 1) * mm, "end": v(43.7, 0.98) * mm});
            skLineSegment(sketch, "E7850", {"start": v(43.7, 0.98) * mm, "end": v(43.69, 0.97) * mm});
            skLineSegment(sketch, "E7851", {"start": v(43.69, 0.97) * mm, "end": v(43.68, 0.96) * mm});
            skLineSegment(sketch, "E7852", {"start": v(43.68, 0.96) * mm, "end": v(43.67, 0.93) * mm});
            skLineSegment(sketch, "E7853", {"start": v(43.67, 0.93) * mm, "end": v(43.66, 0.9) * mm});
            skLineSegment(sketch, "E7854", {"start": v(43.66, 0.9) * mm, "end": v(43.65, 0.88) * mm});
            skLineSegment(sketch, "E7855", {"start": v(43.65, 0.88) * mm, "end": v(43.63, 0.85) * mm});
            skLineSegment(sketch, "E7856", {"start": v(43.63, 0.85) * mm, "end": v(43.62, 0.82) * mm});
            skLineSegment(sketch, "E7857", {"start": v(43.62, 0.82) * mm, "end": v(43.6, 0.79) * mm});
            skLineSegment(sketch, "E7858", {"start": v(43.6, 0.79) * mm, "end": v(43.58, 0.75) * mm});
            skLineSegment(sketch, "E7859", {"start": v(43.58, 0.75) * mm, "end": v(43.55, 0.72) * mm});
            skLineSegment(sketch, "E7860", {"start": v(43.55, 0.72) * mm, "end": v(43.53, 0.68) * mm});
            skLineSegment(sketch, "E7861", {"start": v(43.53, 0.68) * mm, "end": v(43.5, 0.64) * mm});
            skLineSegment(sketch, "E7862", {"start": v(43.5, 0.64) * mm, "end": v(43.48, 0.6) * mm});
            skLineSegment(sketch, "E7863", {"start": v(43.48, 0.6) * mm, "end": v(43.45, 0.56) * mm});
            skLineSegment(sketch, "E7864", {"start": v(43.45, 0.56) * mm, "end": v(43.38, 0.47) * mm});
            skLineSegment(sketch, "E7865", {"start": v(43.38, 0.47) * mm, "end": v(43.3, 0.38) * mm});
            skLineSegment(sketch, "E7866", {"start": v(43.3, 0.38) * mm, "end": v(43.23, 0.28) * mm});
            skLineSegment(sketch, "E7867", {"start": v(43.23, 0.28) * mm, "end": v(43.14, 0.17) * mm});
            skLineSegment(sketch, "E7868", {"start": v(43.14, 0.17) * mm, "end": v(43.05, 0.06) * mm});
            skLineSegment(sketch, "E7869", {"start": v(43.05, 0.06) * mm, "end": v(42.95, -0.05) * mm});
            skLineSegment(sketch, "E7870", {"start": v(42.95, -0.05) * mm, "end": v(42.78, -0.24) * mm});
            skLineSegment(sketch, "E7871", {"start": v(42.78, -0.24) * mm, "end": v(42.56, -0.49) * mm});
            skLineSegment(sketch, "E7872", {"start": v(42.56, -0.49) * mm, "end": v(42.35, -0.72) * mm});
            skLineSegment(sketch, "E7873", {"start": v(42.35, -0.72) * mm, "end": v(42.16, -0.94) * mm});
            skLineSegment(sketch, "E7874", {"start": v(42.16, -0.94) * mm, "end": v(41.98, -1.15) * mm});
            skLineSegment(sketch, "E7875", {"start": v(41.98, -1.15) * mm, "end": v(41.82, -1.35) * mm});
            skLineSegment(sketch, "E7876", {"start": v(41.82, -1.35) * mm, "end": v(41.67, -1.53) * mm});
            skLineSegment(sketch, "E7877", {"start": v(41.67, -1.53) * mm, "end": v(41.53, -1.7) * mm});
            skLineSegment(sketch, "E7878", {"start": v(41.53, -1.7) * mm, "end": v(41.47, -1.78) * mm});
            skLineSegment(sketch, "E7879", {"start": v(41.47, -1.78) * mm, "end": v(41.4, -1.86) * mm});
            skLineSegment(sketch, "E7880", {"start": v(41.4, -1.86) * mm, "end": v(41.3, -2.01) * mm});
            skLineSegment(sketch, "E7881", {"start": v(41.3, -2.01) * mm, "end": v(41.21, -2.17) * mm});
            skLineSegment(sketch, "E7882", {"start": v(41.21, -2.17) * mm, "end": v(41.13, -2.32) * mm});
            skLineSegment(sketch, "E7883", {"start": v(41.13, -2.32) * mm, "end": v(41.07, -2.48) * mm});
            skLineSegment(sketch, "E7884", {"start": v(41.07, -2.48) * mm, "end": v(41.02, -2.64) * mm});
            skLineSegment(sketch, "E7885", {"start": v(41.02, -2.64) * mm, "end": v(40.99, -2.8) * mm});
            skLineSegment(sketch, "E7886", {"start": v(40.99, -2.8) * mm, "end": v(40.97, -2.97) * mm});
            skLineSegment(sketch, "E7887", {"start": v(40.97, -2.97) * mm, "end": v(40.96, -3.13) * mm});
            skLineSegment(sketch, "E7888", {"start": v(40.96, -3.13) * mm, "end": v(40.96, -3.18) * mm});
            skLineSegment(sketch, "E7889", {"start": v(40.96, -3.18) * mm, "end": v(40.96, -3.23) * mm});
            skLineSegment(sketch, "E7890", {"start": v(40.96, -3.23) * mm, "end": v(40.97, -3.27) * mm});
            skLineSegment(sketch, "E7891", {"start": v(40.97, -3.27) * mm, "end": v(40.98, -3.32) * mm});
            skLineSegment(sketch, "E7892", {"start": v(40.98, -3.32) * mm, "end": v(40.98, -3.36) * mm});
            skLineSegment(sketch, "E7893", {"start": v(40.98, -3.36) * mm, "end": v(41, -3.4) * mm});
            skLineSegment(sketch, "E7894", {"start": v(41, -3.4) * mm, "end": v(41, -3.44) * mm});
            skLineSegment(sketch, "E7895", {"start": v(41, -3.44) * mm, "end": v(41.02, -3.48) * mm});
            skLineSegment(sketch, "E7896", {"start": v(41.02, -3.48) * mm, "end": v(41.04, -3.52) * mm});
            skLineSegment(sketch, "E7897", {"start": v(41.04, -3.52) * mm, "end": v(41.06, -3.56) * mm});
            skLineSegment(sketch, "E7898", {"start": v(41.06, -3.56) * mm, "end": v(41.08, -3.6) * mm});
            skLineSegment(sketch, "E7899", {"start": v(41.08, -3.6) * mm, "end": v(41.1, -3.63) * mm});
            skLineSegment(sketch, "E7900", {"start": v(41.1, -3.63) * mm, "end": v(41.13, -3.67) * mm});
            skLineSegment(sketch, "E7901", {"start": v(41.13, -3.67) * mm, "end": v(41.16, -3.7) * mm});
            skLineSegment(sketch, "E7902", {"start": v(41.16, -3.7) * mm, "end": v(41.19, -3.74) * mm});
            skLineSegment(sketch, "E7903", {"start": v(41.19, -3.74) * mm, "end": v(41.22, -3.77) * mm});
            skLineSegment(sketch, "E7904", {"start": v(41.22, -3.77) * mm, "end": v(41.25, -3.8) * mm});
            skLineSegment(sketch, "E7905", {"start": v(41.25, -3.8) * mm, "end": v(41.29, -3.82) * mm});
            skLineSegment(sketch, "E7906", {"start": v(41.29, -3.82) * mm, "end": v(41.32, -3.85) * mm});
            skLineSegment(sketch, "E7907", {"start": v(41.32, -3.85) * mm, "end": v(41.36, -3.87) * mm});
            skLineSegment(sketch, "E7908", {"start": v(41.36, -3.87) * mm, "end": v(41.4, -3.89) * mm});
            skLineSegment(sketch, "E7909", {"start": v(41.4, -3.89) * mm, "end": v(41.43, -3.9) * mm});
            skLineSegment(sketch, "E7910", {"start": v(41.43, -3.9) * mm, "end": v(41.47, -3.92) * mm});
            skLineSegment(sketch, "E7911", {"start": v(41.47, -3.92) * mm, "end": v(41.5, -3.94) * mm});
            skLineSegment(sketch, "E7912", {"start": v(41.5, -3.94) * mm, "end": v(41.54, -3.95) * mm});
            skLineSegment(sketch, "E7913", {"start": v(41.54, -3.95) * mm, "end": v(41.58, -3.97) * mm});
            skLineSegment(sketch, "E7914", {"start": v(41.58, -3.97) * mm, "end": v(41.63, -3.98) * mm});
            skLineSegment(sketch, "E7915", {"start": v(41.63, -3.98) * mm, "end": v(41.67, -3.98) * mm});
            skLineSegment(sketch, "E7916", {"start": v(41.67, -3.98) * mm, "end": v(41.7, -3.99) * mm});
            skLineSegment(sketch, "E7917", {"start": v(41.7, -3.99) * mm, "end": v(41.75, -4) * mm});
            skLineSegment(sketch, "E7918", {"start": v(41.75, -4) * mm, "end": v(41.8, -4) * mm});
            skLineSegment(sketch, "E7919", {"start": v(41.8, -4) * mm, "end": v(41.84, -4) * mm});
            skLineSegment(sketch, "E7920", {"start": v(41.84, -4) * mm, "end": v(41.9, -4) * mm});
            skLineSegment(sketch, "E7921", {"start": v(41.9, -4) * mm, "end": v(41.95, -4) * mm});
            skLineSegment(sketch, "E7922", {"start": v(41.95, -4) * mm, "end": v(42, -3.98) * mm});
            skLineSegment(sketch, "E7923", {"start": v(42, -3.98) * mm, "end": v(42.06, -3.97) * mm});
            skLineSegment(sketch, "E7924", {"start": v(42.06, -3.97) * mm, "end": v(42.12, -3.96) * mm});
            skLineSegment(sketch, "E7925", {"start": v(42.12, -3.96) * mm, "end": v(42.18, -3.94) * mm});
            skLineSegment(sketch, "E7926", {"start": v(42.18, -3.94) * mm, "end": v(42.24, -3.92) * mm});
            skLineSegment(sketch, "E7927", {"start": v(42.24, -3.92) * mm, "end": v(42.3, -3.89) * mm});
            skLineSegment(sketch, "E7928", {"start": v(42.3, -3.89) * mm, "end": v(42.36, -3.86) * mm});
            skLineSegment(sketch, "E7929", {"start": v(42.36, -3.86) * mm, "end": v(42.43, -3.83) * mm});
            skLineSegment(sketch, "E7930", {"start": v(42.43, -3.83) * mm, "end": v(42.5, -3.8) * mm});
            skLineSegment(sketch, "E7931", {"start": v(42.5, -3.8) * mm, "end": v(42.56, -3.75) * mm});
            skLineSegment(sketch, "E7932", {"start": v(42.56, -3.75) * mm, "end": v(42.63, -3.71) * mm});
            skLineSegment(sketch, "E7933", {"start": v(42.63, -3.71) * mm, "end": v(42.77, -3.62) * mm});
            skLineSegment(sketch, "E7934", {"start": v(42.77, -3.62) * mm, "end": v(42.84, -3.56) * mm});
            skLineSegment(sketch, "E7935", {"start": v(42.84, -3.56) * mm, "end": v(42.92, -3.5) * mm});
            skLineSegment(sketch, "E7936", {"start": v(42.92, -3.5) * mm, "end": v(43, -3.45) * mm});
            skLineSegment(sketch, "E7937", {"start": v(43, -3.45) * mm, "end": v(43.08, -3.38) * mm});
            skLineSegment(sketch, "E7938", {"start": v(43.08, -3.38) * mm, "end": v(43.18, -3.3) * mm});
            skLineSegment(sketch, "E7939", {"start": v(43.18, -3.3) * mm, "end": v(43.27, -3.23) * mm});
            skLineSegment(sketch, "E7940", {"start": v(43.27, -3.23) * mm, "end": v(43.38, -3.14) * mm});
            skLineSegment(sketch, "E7941", {"start": v(43.38, -3.14) * mm, "end": v(43.49, -3.05) * mm});
            skLineSegment(sketch, "E7942", {"start": v(43.49, -3.05) * mm, "end": v(43.6, -2.96) * mm});
            skLineSegment(sketch, "E7943", {"start": v(43.6, -2.96) * mm, "end": v(43.72, -2.86) * mm});
            skLineSegment(sketch, "E7944", {"start": v(43.72, -2.86) * mm, "end": v(43.84, -2.76) * mm});
            skLineSegment(sketch, "E7945", {"start": v(43.84, -2.76) * mm, "end": v(44.1, -2.53) * mm});
            skLineSegment(sketch, "E7946", {"start": v(44.1, -2.53) * mm, "end": v(44.39, -2.28) * mm});
            skLineSegment(sketch, "E7947", {"start": v(44.39, -2.28) * mm, "end": v(44.69, -2.02) * mm});
            skLineSegment(sketch, "E7948", {"start": v(44.69, -2.02) * mm, "end": v(44.69, -3.04) * mm});
            skLineSegment(sketch, "E7949", {"start": v(44.69, -3.04) * mm, "end": v(44.08, -3.62) * mm});
            skLineSegment(sketch, "E7950", {"start": v(44.08, -3.62) * mm, "end": v(43.49, -4.15) * mm});
            skLineSegment(sketch, "E7951", {"start": v(43.49, -4.15) * mm, "end": v(42.93, -4.64) * mm});
            skLineSegment(sketch, "E7952", {"start": v(42.93, -4.64) * mm, "end": v(42.4, -5.1) * mm});
            skLineSegment(sketch, "E7953", {"start": v(42.4, -5.1) * mm, "end": v(42.15, -5.3) * mm});
            skLineSegment(sketch, "E7954", {"start": v(42.15, -5.3) * mm, "end": v(41.9, -5.5) * mm});
            skLineSegment(sketch, "E7955", {"start": v(41.9, -5.5) * mm, "end": v(41.67, -5.68) * mm});
            skLineSegment(sketch, "E7956", {"start": v(41.67, -5.68) * mm, "end": v(41.44, -5.85) * mm});
            skLineSegment(sketch, "E7957", {"start": v(41.44, -5.85) * mm, "end": v(41.22, -6) * mm});
            skLineSegment(sketch, "E7958", {"start": v(41.22, -6) * mm, "end": v(41.01, -6.14) * mm});
            skLineSegment(sketch, "E7959", {"start": v(41.01, -6.14) * mm, "end": v(40.8, -6.27) * mm});
            skLineSegment(sketch, "E7960", {"start": v(40.8, -6.27) * mm, "end": v(40.61, -6.38) * mm});
            skLineSegment(sketch, "E7961", {"start": v(40.61, -6.38) * mm, "end": v(40.43, -6.48) * mm});
            skLineSegment(sketch, "E7962", {"start": v(40.43, -6.48) * mm, "end": v(40.25, -6.57) * mm});
            skLineSegment(sketch, "E7963", {"start": v(40.25, -6.57) * mm, "end": v(40.08, -6.64) * mm});
            skLineSegment(sketch, "E7964", {"start": v(40.08, -6.64) * mm, "end": v(40, -6.67) * mm});
            skLineSegment(sketch, "E7965", {"start": v(40, -6.67) * mm, "end": v(39.92, -6.7) * mm});
            skLineSegment(sketch, "E7966", {"start": v(39.92, -6.7) * mm, "end": v(39.84, -6.72) * mm});
            skLineSegment(sketch, "E7967", {"start": v(39.84, -6.72) * mm, "end": v(39.77, -6.74) * mm});
            skLineSegment(sketch, "E7968", {"start": v(39.77, -6.74) * mm, "end": v(39.7, -6.76) * mm});
            skLineSegment(sketch, "E7969", {"start": v(39.7, -6.76) * mm, "end": v(39.62, -6.78) * mm});
            skLineSegment(sketch, "E7970", {"start": v(39.62, -6.78) * mm, "end": v(39.55, -6.79) * mm});
            skLineSegment(sketch, "E7971", {"start": v(39.55, -6.79) * mm, "end": v(39.48, -6.8) * mm});
            skLineSegment(sketch, "E7972", {"start": v(39.48, -6.8) * mm, "end": v(39.42, -6.8) * mm});
            skLineSegment(sketch, "E7973", {"start": v(39.42, -6.8) * mm, "end": v(39.35, -6.8) * mm});
            skLineSegment(sketch, "E7974", {"start": v(39.35, -6.8) * mm, "end": v(39.3, -6.8) * mm});
            skLineSegment(sketch, "E7975", {"start": v(39.3, -6.8) * mm, "end": v(39.24, -6.8) * mm});
            skLineSegment(sketch, "E7976", {"start": v(39.24, -6.8) * mm, "end": v(39.2, -6.8) * mm});
            skLineSegment(sketch, "E7977", {"start": v(39.2, -6.8) * mm, "end": v(39.14, -6.78) * mm});
            skLineSegment(sketch, "E7978", {"start": v(39.14, -6.78) * mm, "end": v(39.09, -6.77) * mm});
            skLineSegment(sketch, "E7979", {"start": v(39.09, -6.77) * mm, "end": v(39.04, -6.76) * mm});
            skLineSegment(sketch, "E7980", {"start": v(39.04, -6.76) * mm, "end": v(38.99, -6.74) * mm});
            skLineSegment(sketch, "E7981", {"start": v(38.99, -6.74) * mm, "end": v(38.94, -6.72) * mm});
            skLineSegment(sketch, "E7982", {"start": v(38.94, -6.72) * mm, "end": v(38.9, -6.7) * mm});
            skLineSegment(sketch, "E7983", {"start": v(38.9, -6.7) * mm, "end": v(38.85, -6.67) * mm});
            skLineSegment(sketch, "E7984", {"start": v(38.85, -6.67) * mm, "end": v(38.8, -6.65) * mm});
            skLineSegment(sketch, "E7985", {"start": v(38.8, -6.65) * mm, "end": v(38.76, -6.62) * mm});
            skLineSegment(sketch, "E7986", {"start": v(38.76, -6.62) * mm, "end": v(38.72, -6.58) * mm});
            skLineSegment(sketch, "E7987", {"start": v(38.72, -6.58) * mm, "end": v(38.68, -6.55) * mm});
            skLineSegment(sketch, "E7988", {"start": v(38.68, -6.55) * mm, "end": v(38.64, -6.51) * mm});
            skLineSegment(sketch, "E7989", {"start": v(38.64, -6.51) * mm, "end": v(38.6, -6.47) * mm});
            skLineSegment(sketch, "E7990", {"start": v(38.6, -6.47) * mm, "end": v(38.57, -6.43) * mm});
            skLineSegment(sketch, "E7991", {"start": v(38.57, -6.43) * mm, "end": v(38.53, -6.38) * mm});
            skLineSegment(sketch, "E7992", {"start": v(38.53, -6.38) * mm, "end": v(38.5, -6.33) * mm});
            skLineSegment(sketch, "E7993", {"start": v(38.5, -6.33) * mm, "end": v(38.47, -6.29) * mm});
            skLineSegment(sketch, "E7994", {"start": v(38.47, -6.29) * mm, "end": v(38.44, -6.24) * mm});
            skLineSegment(sketch, "E7995", {"start": v(38.44, -6.24) * mm, "end": v(38.42, -6.19) * mm});
            skLineSegment(sketch, "E7996", {"start": v(38.42, -6.19) * mm, "end": v(38.4, -6.14) * mm});
            skLineSegment(sketch, "E7997", {"start": v(38.4, -6.14) * mm, "end": v(38.37, -6.08) * mm});
            skLineSegment(sketch, "E7998", {"start": v(38.37, -6.08) * mm, "end": v(38.36, -6.03) * mm});
            skLineSegment(sketch, "E7999", {"start": v(38.36, -6.03) * mm, "end": v(38.34, -5.97) * mm});
            skLineSegment(sketch, "E8000", {"start": v(38.34, -5.97) * mm, "end": v(38.33, -5.92) * mm});
            skLineSegment(sketch, "E8001", {"start": v(38.33, -5.92) * mm, "end": v(38.32, -5.86) * mm});
            skLineSegment(sketch, "E8002", {"start": v(38.32, -5.86) * mm, "end": v(38.3, -5.8) * mm});
            skLineSegment(sketch, "E8003", {"start": v(38.3, -5.8) * mm, "end": v(38.3, -5.74) * mm});
            skLineSegment(sketch, "E8004", {"start": v(38.3, -5.74) * mm, "end": v(38.3, -5.62) * mm});
            skLineSegment(sketch, "E8005", {"start": v(38.3, -5.62) * mm, "end": v(38.3, -5.5) * mm});
            skLineSegment(sketch, "E8006", {"start": v(38.3, -5.5) * mm, "end": v(38.3, -5.37) * mm});
            skLineSegment(sketch, "E8007", {"start": v(38.3, -5.37) * mm, "end": v(38.34, -5.12) * mm});
            skLineSegment(sketch, "E8008", {"start": v(38.34, -5.12) * mm, "end": v(38.4, -4.87) * mm});
            skLineSegment(sketch, "E8009", {"start": v(38.4, -4.87) * mm, "end": v(38.47, -4.62) * mm});
            skLineSegment(sketch, "E8010", {"start": v(38.47, -4.62) * mm, "end": v(38.52, -4.5) * mm});
            skLineSegment(sketch, "E8011", {"start": v(38.52, -4.5) * mm, "end": v(38.57, -4.36) * mm});
            skLineSegment(sketch, "E8012", {"start": v(38.57, -4.36) * mm, "end": v(38.63, -4.21) * mm});
            skLineSegment(sketch, "E8013", {"start": v(38.63, -4.21) * mm, "end": v(38.7, -4.07) * mm});
            skLineSegment(sketch, "E8014", {"start": v(38.7, -4.07) * mm, "end": v(38.76, -3.91) * mm});
            skLineSegment(sketch, "E8015", {"start": v(38.76, -3.91) * mm, "end": v(38.84, -3.75) * mm});
            skLineSegment(sketch, "E8016", {"start": v(38.84, -3.75) * mm, "end": v(38.92, -3.6) * mm});
            skLineSegment(sketch, "E8017", {"start": v(38.92, -3.6) * mm, "end": v(39, -3.42) * mm});
            skLineSegment(sketch, "E8018", {"start": v(39, -3.42) * mm, "end": v(39.1, -3.24) * mm});
            skLineSegment(sketch, "E8019", {"start": v(39.1, -3.24) * mm, "end": v(39.2, -3.06) * mm});
            skLineSegment(sketch, "E8020", {"start": v(39.2, -3.06) * mm, "end": v(39.31, -2.86) * mm});
            skLineSegment(sketch, "E8021", {"start": v(39.31, -2.86) * mm, "end": v(39.43, -2.66) * mm});
            skLineSegment(sketch, "E8022", {"start": v(39.43, -2.66) * mm, "end": v(39.55, -2.44) * mm});
            skLineSegment(sketch, "E8023", {"start": v(39.55, -2.44) * mm, "end": v(39.82, -2) * mm});
            skLineSegment(sketch, "E8024", {"start": v(39.82, -2) * mm, "end": v(39.96, -1.76) * mm});
            skLineSegment(sketch, "E8025", {"start": v(39.96, -1.76) * mm, "end": v(40.25, -1.28) * mm});
            skLineSegment(sketch, "E8026", {"start": v(40.25, -1.28) * mm, "end": v(40.53, -0.82) * mm});
            skLineSegment(sketch, "E8027", {"start": v(40.53, -0.82) * mm, "end": v(40.8, -0.38) * mm});
            skLineSegment(sketch, "E8028", {"start": v(40.8, -0.38) * mm, "end": v(41.05, 0.04) * mm});
            skLineSegment(sketch, "E8029", {"start": v(41.05, 0.04) * mm, "end": v(40.33, -0.56) * mm});
            skLineSegment(sketch, "E8030", {"start": v(40.33, -0.56) * mm, "end": v(39.65, -1.14) * mm});
            skLineSegment(sketch, "E8031", {"start": v(39.65, -1.14) * mm, "end": v(39.02, -1.72) * mm});
            skLineSegment(sketch, "E8032", {"start": v(39.02, -1.72) * mm, "end": v(38.43, -2.28) * mm});
            skLineSegment(sketch, "E8033", {"start": v(38.43, -2.28) * mm, "end": v(37.88, -2.82) * mm});
            skLineSegment(sketch, "E8034", {"start": v(37.88, -2.82) * mm, "end": v(37.63, -3.07) * mm});
            skLineSegment(sketch, "E8035", {"start": v(37.63, -3.07) * mm, "end": v(37.4, -3.32) * mm});
            skLineSegment(sketch, "E8036", {"start": v(37.4, -3.32) * mm, "end": v(37.17, -3.56) * mm});
            skLineSegment(sketch, "E8037", {"start": v(37.17, -3.56) * mm, "end": v(36.95, -3.8) * mm});
            skLineSegment(sketch, "E8038", {"start": v(36.95, -3.8) * mm, "end": v(36.75, -4.02) * mm});
            skLineSegment(sketch, "E8039", {"start": v(36.75, -4.02) * mm, "end": v(36.56, -4.23) * mm});
            skLineSegment(sketch, "E8040", {"start": v(36.56, -4.23) * mm, "end": v(36.39, -4.43) * mm});
            skLineSegment(sketch, "E8041", {"start": v(36.39, -4.43) * mm, "end": v(36.22, -4.62) * mm});
            skLineSegment(sketch, "E8042", {"start": v(36.22, -4.62) * mm, "end": v(36.06, -4.8) * mm});
            skLineSegment(sketch, "E8043", {"start": v(36.06, -4.8) * mm, "end": v(35.92, -4.97) * mm});
            skLineSegment(sketch, "E8044", {"start": v(35.92, -4.97) * mm, "end": v(35.78, -5.12) * mm});
            skLineSegment(sketch, "E8045", {"start": v(35.78, -5.12) * mm, "end": v(35.65, -5.27) * mm});
            skLineSegment(sketch, "E8046", {"start": v(35.65, -5.27) * mm, "end": v(35.53, -5.4) * mm});
            skLineSegment(sketch, "E8047", {"start": v(35.53, -5.4) * mm, "end": v(35.42, -5.53) * mm});
            skLineSegment(sketch, "E8048", {"start": v(35.42, -5.53) * mm, "end": v(35.32, -5.64) * mm});
            skLineSegment(sketch, "E8049", {"start": v(35.32, -5.64) * mm, "end": v(35.22, -5.74) * mm});
            skLineSegment(sketch, "E8050", {"start": v(35.22, -5.74) * mm, "end": v(35.12, -5.84) * mm});
            skLineSegment(sketch, "E8051", {"start": v(35.12, -5.84) * mm, "end": v(35.02, -5.92) * mm});
            skLineSegment(sketch, "E8052", {"start": v(35.02, -5.92) * mm, "end": v(34.93, -6) * mm});
            skLineSegment(sketch, "E8053", {"start": v(34.93, -6) * mm, "end": v(34.83, -6.08) * mm});
            skLineSegment(sketch, "E8054", {"start": v(34.83, -6.08) * mm, "end": v(34.74, -6.14) * mm});
            skLineSegment(sketch, "E8055", {"start": v(34.74, -6.14) * mm, "end": v(34.64, -6.2) * mm});
            skLineSegment(sketch, "E8056", {"start": v(34.64, -6.2) * mm, "end": v(34.55, -6.26) * mm});
            skLineSegment(sketch, "E8057", {"start": v(34.55, -6.26) * mm, "end": v(34.45, -6.3) * mm});
            skLineSegment(sketch, "E8058", {"start": v(34.45, -6.3) * mm, "end": v(34.36, -6.34) * mm});
            skLineSegment(sketch, "E8059", {"start": v(34.36, -6.34) * mm, "end": v(34.27, -6.37) * mm});
            skLineSegment(sketch, "E8060", {"start": v(34.27, -6.37) * mm, "end": v(34.18, -6.4) * mm});
            skLineSegment(sketch, "E8061", {"start": v(34.18, -6.4) * mm, "end": v(34.1, -6.41) * mm});
            skLineSegment(sketch, "E8062", {"start": v(34.1, -6.41) * mm, "end": v(34, -6.42) * mm});
            skLineSegment(sketch, "E8063", {"start": v(34, -6.42) * mm, "end": v(33.92, -6.43) * mm});
            skLineSegment(sketch, "E8064", {"start": v(33.92, -6.43) * mm, "end": v(33.87, -6.43) * mm});
            skLineSegment(sketch, "E8065", {"start": v(33.87, -6.43) * mm, "end": v(33.83, -6.42) * mm});
            skLineSegment(sketch, "E8066", {"start": v(33.83, -6.42) * mm, "end": v(33.78, -6.42) * mm});
            skLineSegment(sketch, "E8067", {"start": v(33.78, -6.42) * mm, "end": v(33.74, -6.41) * mm});
            skLineSegment(sketch, "E8068", {"start": v(33.74, -6.41) * mm, "end": v(33.7, -6.4) * mm});
            skLineSegment(sketch, "E8069", {"start": v(33.7, -6.4) * mm, "end": v(33.66, -6.39) * mm});
            skLineSegment(sketch, "E8070", {"start": v(33.66, -6.39) * mm, "end": v(33.62, -6.38) * mm});
            skLineSegment(sketch, "E8071", {"start": v(33.62, -6.38) * mm, "end": v(33.59, -6.36) * mm});
            skLineSegment(sketch, "E8072", {"start": v(33.59, -6.36) * mm, "end": v(33.55, -6.34) * mm});
            skLineSegment(sketch, "E8073", {"start": v(33.55, -6.34) * mm, "end": v(33.52, -6.32) * mm});
            skLineSegment(sketch, "E8074", {"start": v(33.52, -6.32) * mm, "end": v(33.49, -6.3) * mm});
            skLineSegment(sketch, "E8075", {"start": v(33.49, -6.3) * mm, "end": v(33.46, -6.28) * mm});
            skLineSegment(sketch, "E8076", {"start": v(33.46, -6.28) * mm, "end": v(33.43, -6.25) * mm});
            skLineSegment(sketch, "E8077", {"start": v(33.43, -6.25) * mm, "end": v(33.4, -6.22) * mm});
            skLineSegment(sketch, "E8078", {"start": v(33.4, -6.22) * mm, "end": v(33.38, -6.2) * mm});
            skLineSegment(sketch, "E8079", {"start": v(33.38, -6.2) * mm, "end": v(33.35, -6.16) * mm});
            skLineSegment(sketch, "E8080", {"start": v(33.35, -6.16) * mm, "end": v(33.33, -6.13) * mm});
            skLineSegment(sketch, "E8081", {"start": v(33.33, -6.13) * mm, "end": v(33.3, -6.09) * mm});
            skLineSegment(sketch, "E8082", {"start": v(33.3, -6.09) * mm, "end": v(33.29, -6.05) * mm});
            skLineSegment(sketch, "E8083", {"start": v(33.29, -6.05) * mm, "end": v(33.27, -6) * mm});
            skLineSegment(sketch, "E8084", {"start": v(33.27, -6) * mm, "end": v(33.25, -5.97) * mm});
            skLineSegment(sketch, "E8085", {"start": v(33.25, -5.97) * mm, "end": v(33.24, -5.92) * mm});
            skLineSegment(sketch, "E8086", {"start": v(33.24, -5.92) * mm, "end": v(33.23, -5.87) * mm});
            skLineSegment(sketch, "E8087", {"start": v(33.23, -5.87) * mm, "end": v(33.21, -5.83) * mm});
            skLineSegment(sketch, "E8088", {"start": v(33.21, -5.83) * mm, "end": v(33.2, -5.77) * mm});
            skLineSegment(sketch, "E8089", {"start": v(33.2, -5.77) * mm, "end": v(33.2, -5.72) * mm});
            skLineSegment(sketch, "E8090", {"start": v(33.2, -5.72) * mm, "end": v(33.18, -5.67) * mm});
            skLineSegment(sketch, "E8091", {"start": v(33.18, -5.67) * mm, "end": v(33.17, -5.55) * mm});
            skLineSegment(sketch, "E8092", {"start": v(33.17, -5.55) * mm, "end": v(33.17, -5.42) * mm});
            skLineSegment(sketch, "E8093", {"start": v(33.17, -5.42) * mm, "end": v(33.17, -5.36) * mm});
            skLineSegment(sketch, "E8094", {"start": v(33.17, -5.36) * mm, "end": v(33.17, -5.33) * mm});
            skLineSegment(sketch, "E8095", {"start": v(33.17, -5.33) * mm, "end": v(33.17, -5.3) * mm});
            skLineSegment(sketch, "E8096", {"start": v(33.17, -5.3) * mm, "end": v(33.17, -5.27) * mm});
            skLineSegment(sketch, "E8097", {"start": v(33.17, -5.27) * mm, "end": v(33.17, -5.24) * mm});
            skLineSegment(sketch, "E8098", {"start": v(33.17, -5.24) * mm, "end": v(33.18, -5.2) * mm});
            skLineSegment(sketch, "E8099", {"start": v(33.18, -5.2) * mm, "end": v(33.19, -5.17) * mm});
            skLineSegment(sketch, "E8100", {"start": v(33.19, -5.17) * mm, "end": v(33.2, -5.13) * mm});
            skLineSegment(sketch, "E8101", {"start": v(33.2, -5.13) * mm, "end": v(33.2, -5.1) * mm});
            skLineSegment(sketch, "E8102", {"start": v(33.2, -5.1) * mm, "end": v(33.22, -5.02) * mm});
            skLineSegment(sketch, "E8103", {"start": v(33.22, -5.02) * mm, "end": v(33.25, -4.94) * mm});
            skLineSegment(sketch, "E8104", {"start": v(33.25, -4.94) * mm, "end": v(33.27, -4.85) * mm});
            skLineSegment(sketch, "E8105", {"start": v(33.27, -4.85) * mm, "end": v(33.3, -4.75) * mm});
            skLineSegment(sketch, "E8106", {"start": v(33.3, -4.75) * mm, "end": v(33.34, -4.65) * mm});
            skLineSegment(sketch, "E8107", {"start": v(33.34, -4.65) * mm, "end": v(33.39, -4.55) * mm});
            skLineSegment(sketch, "E8108", {"start": v(33.39, -4.55) * mm, "end": v(33.43, -4.44) * mm});
            skLineSegment(sketch, "E8109", {"start": v(33.43, -4.44) * mm, "end": v(33.48, -4.32) * mm});
            skLineSegment(sketch, "E8110", {"start": v(33.48, -4.32) * mm, "end": v(33.54, -4.2) * mm});
            skLineSegment(sketch, "E8111", {"start": v(33.54, -4.2) * mm, "end": v(33.6, -4.08) * mm});
            skLineSegment(sketch, "E8112", {"start": v(33.6, -4.08) * mm, "end": v(33.66, -3.95) * mm});
            skLineSegment(sketch, "E8113", {"start": v(33.66, -3.95) * mm, "end": v(33.73, -3.81) * mm});
            skLineSegment(sketch, "E8114", {"start": v(33.73, -3.81) * mm, "end": v(33.88, -3.52) * mm});
            skLineSegment(sketch, "E8115", {"start": v(33.88, -3.52) * mm, "end": v(34.04, -3.2) * mm});
            skLineSegment(sketch, "E8116", {"start": v(34.04, -3.2) * mm, "end": v(34.22, -2.88) * mm});
            skLineSegment(sketch, "E8117", {"start": v(34.22, -2.88) * mm, "end": v(34.41, -2.53) * mm});
            skLineSegment(sketch, "E8118", {"start": v(34.41, -2.53) * mm, "end": v(34.62, -2.16) * mm});
            skLineSegment(sketch, "E8119", {"start": v(34.62, -2.16) * mm, "end": v(34.84, -1.78) * mm});
            skLineSegment(sketch, "E8120", {"start": v(34.84, -1.78) * mm, "end": v(35.08, -1.37) * mm});
            skLineSegment(sketch, "E8121", {"start": v(35.08, -1.37) * mm, "end": v(35.33, -0.95) * mm});
            skLineSegment(sketch, "E8122", {"start": v(35.33, -0.95) * mm, "end": v(35.35, -0.93) * mm});
            skLineSegment(sketch, "E8123", {"start": v(35.35, -0.93) * mm, "end": v(35.36, -0.92) * mm});
            skLineSegment(sketch, "E8124", {"start": v(35.36, -0.92) * mm, "end": v(35.36, -0.9) * mm});
            skLineSegment(sketch, "E8125", {"start": v(35.36, -0.9) * mm, "end": v(35.37, -0.88) * mm});
            skLineSegment(sketch, "E8126", {"start": v(35.37, -0.88) * mm, "end": v(35.38, -0.86) * mm});
            skLineSegment(sketch, "E8127", {"start": v(35.38, -0.86) * mm, "end": v(35.39, -0.84) * mm});
            skLineSegment(sketch, "E8128", {"start": v(35.39, -0.84) * mm, "end": v(35.4, -0.82) * mm});
            skLineSegment(sketch, "E8129", {"start": v(35.4, -0.82) * mm, "end": v(35.4, -0.8) * mm});
            skLineSegment(sketch, "E8130", {"start": v(35.4, -0.8) * mm, "end": v(35.4, -0.78) * mm});
            skLineSegment(sketch, "E8131", {"start": v(35.4, -0.78) * mm, "end": v(35.4, -0.75) * mm});
            skLineSegment(sketch, "E8132", {"start": v(35.4, -0.75) * mm, "end": v(35.41, -0.73) * mm});
            skLineSegment(sketch, "E8133", {"start": v(35.41, -0.73) * mm, "end": v(35.42, -0.7) * mm});
            skLineSegment(sketch, "E8134", {"start": v(35.42, -0.7) * mm, "end": v(35.42, -0.67) * mm});
            skLineSegment(sketch, "E8135", {"start": v(35.42, -0.67) * mm, "end": v(35.42, -0.62) * mm});
            skLineSegment(sketch, "E8136", {"start": v(35.42, -0.62) * mm, "end": v(35.42, -0.59) * mm});
            skLineSegment(sketch, "E8137", {"start": v(35.42, -0.59) * mm, "end": v(35.42, -0.57) * mm});
            skLineSegment(sketch, "E8138", {"start": v(35.42, -0.57) * mm, "end": v(35.42, -0.55) * mm});
            skLineSegment(sketch, "E8139", {"start": v(35.42, -0.55) * mm, "end": v(35.42, -0.53) * mm});
            skLineSegment(sketch, "E8140", {"start": v(35.42, -0.53) * mm, "end": v(35.42, -0.52) * mm});
            skLineSegment(sketch, "E8141", {"start": v(35.42, -0.52) * mm, "end": v(35.41, -0.5) * mm});
            skLineSegment(sketch, "E8142", {"start": v(35.41, -0.5) * mm, "end": v(35.41, -0.49) * mm});
            skLineSegment(sketch, "E8143", {"start": v(35.41, -0.49) * mm, "end": v(35.4, -0.47) * mm});
            skLineSegment(sketch, "E8144", {"start": v(35.4, -0.47) * mm, "end": v(35.4, -0.46) * mm});
            skLineSegment(sketch, "E8145", {"start": v(35.4, -0.46) * mm, "end": v(35.4, -0.45) * mm});
            skLineSegment(sketch, "E8146", {"start": v(35.4, -0.45) * mm, "end": v(35.4, -0.43) * mm});
            skLineSegment(sketch, "E8147", {"start": v(35.4, -0.43) * mm, "end": v(35.39, -0.42) * mm});
            skLineSegment(sketch, "E8148", {"start": v(35.39, -0.42) * mm, "end": v(35.38, -0.4) * mm});
            skLineSegment(sketch, "E8149", {"start": v(35.38, -0.4) * mm, "end": v(35.37, -0.4) * mm});
            skLineSegment(sketch, "E8150", {"start": v(35.37, -0.4) * mm, "end": v(35.37, -0.39) * mm});
            skLineSegment(sketch, "E8151", {"start": v(35.37, -0.39) * mm, "end": v(35.36, -0.38) * mm});
            skLineSegment(sketch, "E8152", {"start": v(35.36, -0.38) * mm, "end": v(35.35, -0.37) * mm});
            skLineSegment(sketch, "E8153", {"start": v(35.35, -0.37) * mm, "end": v(35.34, -0.36) * mm});
            skLineSegment(sketch, "E8154", {"start": v(35.34, -0.36) * mm, "end": v(35.33, -0.35) * mm});
            skLineSegment(sketch, "E8155", {"start": v(35.33, -0.35) * mm, "end": v(35.32, -0.34) * mm});
            skLineSegment(sketch, "E8156", {"start": v(35.32, -0.34) * mm, "end": v(35.3, -0.34) * mm});
            skLineSegment(sketch, "E8157", {"start": v(35.3, -0.34) * mm, "end": v(35.3, -0.33) * mm});
            skLineSegment(sketch, "E8158", {"start": v(35.3, -0.33) * mm, "end": v(35.28, -0.32) * mm});
            skLineSegment(sketch, "E8159", {"start": v(35.28, -0.32) * mm, "end": v(35.27, -0.32) * mm});
            skLineSegment(sketch, "E8160", {"start": v(35.27, -0.32) * mm, "end": v(35.26, -0.31) * mm});
            skLineSegment(sketch, "E8161", {"start": v(35.26, -0.31) * mm, "end": v(35.25, -0.31) * mm});
            skLineSegment(sketch, "E8162", {"start": v(35.25, -0.31) * mm, "end": v(35.23, -0.3) * mm});
            skLineSegment(sketch, "E8163", {"start": v(35.23, -0.3) * mm, "end": v(35.22, -0.3) * mm});
            skLineSegment(sketch, "E8164", {"start": v(35.22, -0.3) * mm, "end": v(35.2, -0.3) * mm});
            skLineSegment(sketch, "E8165", {"start": v(35.2, -0.3) * mm, "end": v(35.18, -0.3) * mm});
            skLineSegment(sketch, "E8166", {"start": v(35.18, -0.3) * mm, "end": v(35.17, -0.3) * mm});
            skLineSegment(sketch, "E8167", {"start": v(35.17, -0.3) * mm, "end": v(35.15, -0.3) * mm});
            skLineSegment(sketch, "E8168", {"start": v(35.15, -0.3) * mm, "end": v(35.13, -0.3) * mm});
            skLineSegment(sketch, "E8169", {"start": v(35.13, -0.3) * mm, "end": v(35.11, -0.3) * mm});
            skLineSegment(sketch, "E8170", {"start": v(35.11, -0.3) * mm, "end": v(35.1, -0.3) * mm});
            skLineSegment(sketch, "E8171", {"start": v(35.1, -0.3) * mm, "end": v(35.07, -0.3) * mm});
            skLineSegment(sketch, "E8172", {"start": v(35.07, -0.3) * mm, "end": v(35.05, -0.3) * mm});
            skLineSegment(sketch, "E8173", {"start": v(35.05, -0.3) * mm, "end": v(35.03, -0.31) * mm});
            skLineSegment(sketch, "E8174", {"start": v(35.03, -0.31) * mm, "end": v(35, -0.32) * mm});
            skLineSegment(sketch, "E8175", {"start": v(35, -0.32) * mm, "end": v(34.98, -0.33) * mm});
            skLineSegment(sketch, "E8176", {"start": v(34.98, -0.33) * mm, "end": v(34.96, -0.33) * mm});
            skLineSegment(sketch, "E8177", {"start": v(34.96, -0.33) * mm, "end": v(34.93, -0.34) * mm});
            skLineSegment(sketch, "E8178", {"start": v(34.93, -0.34) * mm, "end": v(34.9, -0.36) * mm});
            skLineSegment(sketch, "E8179", {"start": v(34.9, -0.36) * mm, "end": v(34.88, -0.37) * mm});
            skLineSegment(sketch, "E8180", {"start": v(34.88, -0.37) * mm, "end": v(34.83, -0.4) * mm});
            skLineSegment(sketch, "E8181", {"start": v(34.83, -0.4) * mm, "end": v(34.77, -0.43) * mm});
            skLineSegment(sketch, "E8182", {"start": v(34.77, -0.43) * mm, "end": v(34.71, -0.47) * mm});
            skLineSegment(sketch, "E8183", {"start": v(34.71, -0.47) * mm, "end": v(34.65, -0.51) * mm});
            skLineSegment(sketch, "E8184", {"start": v(34.65, -0.51) * mm, "end": v(34.6, -0.56) * mm});
            skLineSegment(sketch, "E8185", {"start": v(34.6, -0.56) * mm, "end": v(34.53, -0.61) * mm});
            skLineSegment(sketch, "E8186", {"start": v(34.53, -0.61) * mm, "end": v(34.46, -0.67) * mm});
            skLineSegment(sketch, "E8187", {"start": v(34.46, -0.67) * mm, "end": v(34.39, -0.73) * mm});
            skLineSegment(sketch, "E8188", {"start": v(34.39, -0.73) * mm, "end": v(34.32, -0.8) * mm});
            skLineSegment(sketch, "E8189", {"start": v(34.32, -0.8) * mm, "end": v(34.2, -0.9) * mm});
            skLineSegment(sketch, "E8190", {"start": v(34.2, -0.9) * mm, "end": v(34.17, -0.94) * mm});
            skLineSegment(sketch, "E8191", {"start": v(34.17, -0.94) * mm, "end": v(34.13, -0.98) * mm});
            skLineSegment(sketch, "E8192", {"start": v(34.13, -0.98) * mm, "end": v(34.09, -1.03) * mm});
            skLineSegment(sketch, "E8193", {"start": v(34.09, -1.03) * mm, "end": v(34.04, -1.07) * mm});
            skLineSegment(sketch, "E8194", {"start": v(34.04, -1.07) * mm, "end": v(34, -1.12) * mm});
            skLineSegment(sketch, "E8195", {"start": v(34, -1.12) * mm, "end": v(33.95, -1.17) * mm});
            skLineSegment(sketch, "E8196", {"start": v(33.95, -1.17) * mm, "end": v(33.9, -1.23) * mm});
            skLineSegment(sketch, "E8197", {"start": v(33.9, -1.23) * mm, "end": v(33.78, -1.34) * mm});
            skLineSegment(sketch, "E8198", {"start": v(33.78, -1.34) * mm, "end": v(33.67, -1.47) * mm});
            skLineSegment(sketch, "E8199", {"start": v(33.67, -1.47) * mm, "end": v(33.54, -1.6) * mm});
            skLineSegment(sketch, "E8200", {"start": v(33.54, -1.6) * mm, "end": v(33.4, -1.75) * mm});
            skLineSegment(sketch, "E8201", {"start": v(33.4, -1.75) * mm, "end": v(33.26, -1.9) * mm});
            skLineSegment(sketch, "E8202", {"start": v(33.26, -1.9) * mm, "end": v(33.1, -2.07) * mm});
            skLineSegment(sketch, "E8203", {"start": v(33.1, -2.07) * mm, "end": v(32.94, -2.25) * mm});
            skLineSegment(sketch, "E8204", {"start": v(32.94, -2.25) * mm, "end": v(32.77, -2.44) * mm});
            skLineSegment(sketch, "E8205", {"start": v(32.77, -2.44) * mm, "end": v(32.6, -2.63) * mm});
            skLineSegment(sketch, "E8206", {"start": v(32.6, -2.63) * mm, "end": v(32.4, -2.84) * mm});
            skLineSegment(sketch, "E8207", {"start": v(32.4, -2.84) * mm, "end": v(32.2, -3.06) * mm});
            skLineSegment(sketch, "E8208", {"start": v(32.2, -3.06) * mm, "end": v(31.9, -3.4) * mm});
            skLineSegment(sketch, "E8209", {"start": v(31.9, -3.4) * mm, "end": v(31.77, -3.54) * mm});
            skLineSegment(sketch, "E8210", {"start": v(31.77, -3.54) * mm, "end": v(31.65, -3.7) * mm});
            skLineSegment(sketch, "E8211", {"start": v(31.65, -3.7) * mm, "end": v(31.52, -3.85) * mm});
            skLineSegment(sketch, "E8212", {"start": v(31.52, -3.85) * mm, "end": v(31.38, -4.02) * mm});
            skLineSegment(sketch, "E8213", {"start": v(31.38, -4.02) * mm, "end": v(31.25, -4.2) * mm});
            skLineSegment(sketch, "E8214", {"start": v(31.25, -4.2) * mm, "end": v(31.1, -4.4) * mm});
            skLineSegment(sketch, "E8215", {"start": v(31.1, -4.4) * mm, "end": v(30.96, -4.6) * mm});
            skLineSegment(sketch, "E8216", {"start": v(30.96, -4.6) * mm, "end": v(30.8, -4.8) * mm});
            skLineSegment(sketch, "E8217", {"start": v(30.8, -4.8) * mm, "end": v(30.67, -5.01) * mm});
            skLineSegment(sketch, "E8218", {"start": v(30.67, -5.01) * mm, "end": v(30.6, -5.1) * mm});
            skLineSegment(sketch, "E8219", {"start": v(30.6, -5.1) * mm, "end": v(30.53, -5.2) * mm});
            skLineSegment(sketch, "E8220", {"start": v(30.53, -5.2) * mm, "end": v(30.47, -5.29) * mm});
            skLineSegment(sketch, "E8221", {"start": v(30.47, -5.29) * mm, "end": v(30.41, -5.37) * mm});
            skLineSegment(sketch, "E8222", {"start": v(30.41, -5.37) * mm, "end": v(30.35, -5.45) * mm});
            skLineSegment(sketch, "E8223", {"start": v(30.35, -5.45) * mm, "end": v(30.3, -5.52) * mm});
            skLineSegment(sketch, "E8224", {"start": v(30.3, -5.52) * mm, "end": v(30.25, -5.59) * mm});
            skLineSegment(sketch, "E8225", {"start": v(30.25, -5.59) * mm, "end": v(30.2, -5.65) * mm});
            skLineSegment(sketch, "E8226", {"start": v(30.2, -5.65) * mm, "end": v(30.15, -5.71) * mm});
            skLineSegment(sketch, "E8227", {"start": v(30.15, -5.71) * mm, "end": v(30.1, -5.77) * mm});
            skLineSegment(sketch, "E8228", {"start": v(30.1, -5.77) * mm, "end": v(30.07, -5.82) * mm});
            skLineSegment(sketch, "E8229", {"start": v(30.07, -5.82) * mm, "end": v(30.03, -5.87) * mm});
            skLineSegment(sketch, "E8230", {"start": v(30.03, -5.87) * mm, "end": v(30, -5.9) * mm});
            skLineSegment(sketch, "E8231", {"start": v(30, -5.9) * mm, "end": v(29.99, -5.91) * mm});
            skLineSegment(sketch, "E8232", {"start": v(29.99, -5.91) * mm, "end": v(29.97, -5.93) * mm});
            skLineSegment(sketch, "E8233", {"start": v(29.97, -5.93) * mm, "end": v(29.96, -5.95) * mm});
            skLineSegment(sketch, "E8234", {"start": v(29.96, -5.95) * mm, "end": v(29.92, -5.99) * mm});
            skLineSegment(sketch, "E8235", {"start": v(29.92, -5.99) * mm, "end": v(29.9, -6.02) * mm});
            skLineSegment(sketch, "E8236", {"start": v(29.9, -6.02) * mm, "end": v(29.86, -6.05) * mm});
            skLineSegment(sketch, "E8237", {"start": v(29.86, -6.05) * mm, "end": v(29.83, -6.08) * mm});
            skLineSegment(sketch, "E8238", {"start": v(29.83, -6.08) * mm, "end": v(29.8, -6.1) * mm});
            skLineSegment(sketch, "E8239", {"start": v(29.8, -6.1) * mm, "end": v(29.76, -6.13) * mm});
            skLineSegment(sketch, "E8240", {"start": v(29.76, -6.13) * mm, "end": v(29.73, -6.15) * mm});
            skLineSegment(sketch, "E8241", {"start": v(29.73, -6.15) * mm, "end": v(29.7, -6.17) * mm});
            skLineSegment(sketch, "E8242", {"start": v(29.7, -6.17) * mm, "end": v(29.66, -6.18) * mm});
            skLineSegment(sketch, "E8243", {"start": v(29.66, -6.18) * mm, "end": v(29.63, -6.2) * mm});
            skLineSegment(sketch, "E8244", {"start": v(29.63, -6.2) * mm, "end": v(29.6, -6.21) * mm});
            skLineSegment(sketch, "E8245", {"start": v(29.6, -6.21) * mm, "end": v(29.57, -6.22) * mm});
            skLineSegment(sketch, "E8246", {"start": v(29.57, -6.22) * mm, "end": v(29.53, -6.23) * mm});
            skLineSegment(sketch, "E8247", {"start": v(29.53, -6.23) * mm, "end": v(29.5, -6.23) * mm});
            skLineSegment(sketch, "E8248", {"start": v(29.5, -6.23) * mm, "end": v(29.47, -6.24) * mm});
            skLineSegment(sketch, "E8249", {"start": v(29.47, -6.24) * mm, "end": v(29.44, -6.24) * mm});
            skLineSegment(sketch, "E8250", {"start": v(29.44, -6.24) * mm, "end": v(29.4, -6.24) * mm});
            skLineSegment(sketch, "E8251", {"start": v(29.4, -6.24) * mm, "end": v(29.37, -6.24) * mm});
            skLineSegment(sketch, "E8252", {"start": v(29.37, -6.24) * mm, "end": v(29.34, -6.23) * mm});
            skLineSegment(sketch, "E8253", {"start": v(29.34, -6.23) * mm, "end": v(29.3, -6.22) * mm});
            skLineSegment(sketch, "E8254", {"start": v(29.3, -6.22) * mm, "end": v(29.27, -6.22) * mm});
            skLineSegment(sketch, "E8255", {"start": v(29.27, -6.22) * mm, "end": v(29.24, -6.2) * mm});
            skLineSegment(sketch, "E8256", {"start": v(29.24, -6.2) * mm, "end": v(29.21, -6.2) * mm});
            skLineSegment(sketch, "E8257", {"start": v(29.21, -6.2) * mm, "end": v(29.18, -6.18) * mm});
            skLineSegment(sketch, "E8258", {"start": v(29.18, -6.18) * mm, "end": v(29.15, -6.17) * mm});
            skLineSegment(sketch, "E8259", {"start": v(29.15, -6.17) * mm, "end": v(29.12, -6.15) * mm});
            skLineSegment(sketch, "E8260", {"start": v(29.12, -6.15) * mm, "end": v(29.09, -6.13) * mm});
            skLineSegment(sketch, "E8261", {"start": v(29.09, -6.13) * mm, "end": v(29.06, -6.1) * mm});
            skLineSegment(sketch, "E8262", {"start": v(29.06, -6.1) * mm, "end": v(29.02, -6.09) * mm});
            skLineSegment(sketch, "E8263", {"start": v(29.02, -6.09) * mm, "end": v(29, -6.06) * mm});
            skLineSegment(sketch, "E8264", {"start": v(29, -6.06) * mm, "end": v(28.96, -6.04) * mm});
            skLineSegment(sketch, "E8265", {"start": v(28.96, -6.04) * mm, "end": v(28.9, -5.98) * mm});
            skLineSegment(sketch, "E8266", {"start": v(28.9, -5.98) * mm, "end": v(28.84, -5.91) * mm});
            skLineSegment(sketch, "E8267", {"start": v(28.84, -5.91) * mm, "end": v(28.78, -5.84) * mm});
            skLineSegment(sketch, "E8268", {"start": v(28.78, -5.84) * mm, "end": v(28.72, -5.76) * mm});
            skLineSegment(sketch, "E8269", {"start": v(28.72, -5.76) * mm, "end": v(28.67, -5.67) * mm});
            skLineSegment(sketch, "E8270", {"start": v(28.67, -5.67) * mm, "end": v(28.6, -5.58) * mm});
            skLineSegment(sketch, "E8271", {"start": v(28.6, -5.58) * mm, "end": v(28.55, -5.48) * mm});
            skLineSegment(sketch, "E8272", {"start": v(28.55, -5.48) * mm, "end": v(28.5, -5.37) * mm});
            skLineSegment(sketch, "E8273", {"start": v(28.5, -5.37) * mm, "end": v(28.47, -5.31) * mm});
            skLineSegment(sketch, "E8274", {"start": v(28.47, -5.31) * mm, "end": v(28.36, -5.08) * mm});
            skLineSegment(sketch, "E8275", {"start": v(28.36, -5.08) * mm, "end": v(28.27, -4.83) * mm});
            skLineSegment(sketch, "E8276", {"start": v(28.27, -4.83) * mm, "end": v(28.2, -4.58) * mm});
            skLineSegment(sketch, "E8277", {"start": v(28.2, -4.58) * mm, "end": v(28.13, -4.31) * mm});
            skLineSegment(sketch, "E8278", {"start": v(28.13, -4.31) * mm, "end": v(28.08, -4.04) * mm});
            skLineSegment(sketch, "E8279", {"start": v(28.08, -4.04) * mm, "end": v(28.05, -3.75) * mm});
            skLineSegment(sketch, "E8280", {"start": v(28.05, -3.75) * mm, "end": v(28.03, -3.46) * mm});
            skLineSegment(sketch, "E8281", {"start": v(28.03, -3.46) * mm, "end": v(28.02, -3.16) * mm});
            skLineSegment(sketch, "E8282", {"start": v(28.02, -3.16) * mm, "end": v(28.02, -2.94) * mm});
            skLineSegment(sketch, "E8283", {"start": v(28.02, -2.94) * mm, "end": v(28.04, -2.73) * mm});
            skLineSegment(sketch, "E8284", {"start": v(28.04, -2.73) * mm, "end": v(28.06, -2.52) * mm});
            skLineSegment(sketch, "E8285", {"start": v(28.06, -2.52) * mm, "end": v(28.1, -2.32) * mm});
            skLineSegment(sketch, "E8286", {"start": v(28.1, -2.32) * mm, "end": v(28.13, -2.13) * mm});
            skLineSegment(sketch, "E8287", {"start": v(28.13, -2.13) * mm, "end": v(28.18, -1.95) * mm});
            skLineSegment(sketch, "E8288", {"start": v(28.18, -1.95) * mm, "end": v(28.24, -1.78) * mm});
            skLineSegment(sketch, "E8289", {"start": v(28.24, -1.78) * mm, "end": v(28.3, -1.61) * mm});
            skLineSegment(sketch, "E8290", {"start": v(28.3, -1.61) * mm, "end": v(28.39, -1.44) * mm});
            skLineSegment(sketch, "E8291", {"start": v(28.39, -1.44) * mm, "end": v(28.48, -1.27) * mm});
            skLineSegment(sketch, "E8292", {"start": v(28.48, -1.27) * mm, "end": v(28.58, -1.08) * mm});
            skLineSegment(sketch, "E8293", {"start": v(28.58, -1.08) * mm, "end": v(28.7, -0.88) * mm});
            skLineSegment(sketch, "E8294", {"start": v(28.7, -0.88) * mm, "end": v(28.81, -0.67) * mm});
            skLineSegment(sketch, "E8295", {"start": v(28.81, -0.67) * mm, "end": v(28.94, -0.46) * mm});
            skLineSegment(sketch, "E8296", {"start": v(28.94, -0.46) * mm, "end": v(29.08, -0.23) * mm});
            skLineSegment(sketch, "E8297", {"start": v(29.08, -0.23) * mm, "end": v(29.23, 0) * mm});
            skLineSegment(sketch, "E8298", {"start": v(29.23, 0) * mm, "end": v(29.47, 0.35) * mm});
            skLineSegment(sketch, "E8299", {"start": v(29.47, 0.35) * mm, "end": v(29.7, 0.66) * mm});
            skLineSegment(sketch, "E8300", {"start": v(29.7, 0.66) * mm, "end": v(29.9, 0.95) * mm});
            skLineSegment(sketch, "E8301", {"start": v(29.9, 0.95) * mm, "end": v(30.11, 1.2) * mm});
            skLineSegment(sketch, "E8302", {"start": v(30.11, 1.2) * mm, "end": v(30.2, 1.33) * mm});
            skLineSegment(sketch, "E8303", {"start": v(30.2, 1.33) * mm, "end": v(30.3, 1.44) * mm});
            skLineSegment(sketch, "E8304", {"start": v(30.3, 1.44) * mm, "end": v(30.4, 1.55) * mm});
            skLineSegment(sketch, "E8305", {"start": v(30.4, 1.55) * mm, "end": v(30.48, 1.66) * mm});
            skLineSegment(sketch, "E8306", {"start": v(30.48, 1.66) * mm, "end": v(30.57, 1.75) * mm});
            skLineSegment(sketch, "E8307", {"start": v(30.57, 1.75) * mm, "end": v(30.65, 1.84) * mm});
            skLineSegment(sketch, "E8308", {"start": v(30.65, 1.84) * mm, "end": v(30.73, 1.93) * mm});
            skLineSegment(sketch, "E8309", {"start": v(30.73, 1.93) * mm, "end": v(30.8, 2) * mm});
            skLineSegment(sketch, "E8310", {"start": v(30.8, 2) * mm, "end": v(30.89, 2.08) * mm});
            skLineSegment(sketch, "E8311", {"start": v(30.89, 2.08) * mm, "end": v(30.97, 2.14) * mm});
            skLineSegment(sketch, "E8312", {"start": v(30.97, 2.14) * mm, "end": v(31.04, 2.2) * mm});
            skLineSegment(sketch, "E8313", {"start": v(31.04, 2.2) * mm, "end": v(31.12, 2.27) * mm});
            skLineSegment(sketch, "E8314", {"start": v(31.12, 2.27) * mm, "end": v(31.2, 2.32) * mm});
            skLineSegment(sketch, "E8315", {"start": v(31.2, 2.32) * mm, "end": v(31.28, 2.37) * mm});
            skLineSegment(sketch, "E8316", {"start": v(31.28, 2.37) * mm, "end": v(31.36, 2.42) * mm});
            skLineSegment(sketch, "E8317", {"start": v(31.36, 2.42) * mm, "end": v(31.45, 2.46) * mm});
            skLineSegment(sketch, "E8318", {"start": v(31.45, 2.46) * mm, "end": v(31.53, 2.5) * mm});
            skLineSegment(sketch, "E8319", {"start": v(31.53, 2.5) * mm, "end": v(31.6, 2.52) * mm});
            skLineSegment(sketch, "E8320", {"start": v(31.6, 2.52) * mm, "end": v(31.7, 2.55) * mm});
            skLineSegment(sketch, "E8321", {"start": v(31.7, 2.55) * mm, "end": v(31.77, 2.57) * mm});
            skLineSegment(sketch, "E8322", {"start": v(31.77, 2.57) * mm, "end": v(31.86, 2.59) * mm});
            skLineSegment(sketch, "E8323", {"start": v(31.86, 2.59) * mm, "end": v(31.94, 2.6) * mm});
            skLineSegment(sketch, "E8324", {"start": v(31.94, 2.6) * mm, "end": v(32.03, 2.6) * mm});
            skLineSegment(sketch, "E8325", {"start": v(32.03, 2.6) * mm, "end": v(32.11, 2.6) * mm});
            skLineSegment(sketch, "E8326", {"start": v(32.11, 2.6) * mm, "end": v(32.21, 2.6) * mm});
            skLineSegment(sketch, "E8327", {"start": v(32.21, 2.6) * mm, "end": v(32.31, 2.6) * mm});
            skLineSegment(sketch, "E8328", {"start": v(32.31, 2.6) * mm, "end": v(32.4, 2.59) * mm});
            skLineSegment(sketch, "E8329", {"start": v(32.4, 2.59) * mm, "end": v(32.5, 2.57) * mm});
            skLineSegment(sketch, "E8330", {"start": v(32.5, 2.57) * mm, "end": v(32.58, 2.54) * mm});
            skLineSegment(sketch, "E8331", {"start": v(32.58, 2.54) * mm, "end": v(32.67, 2.51) * mm});
            skLineSegment(sketch, "E8332", {"start": v(32.67, 2.51) * mm, "end": v(32.74, 2.48) * mm});
            skLineSegment(sketch, "E8333", {"start": v(32.74, 2.48) * mm, "end": v(32.82, 2.44) * mm});
            skLineSegment(sketch, "E8334", {"start": v(32.82, 2.44) * mm, "end": v(32.85, 2.42) * mm});
            skLineSegment(sketch, "E8335", {"start": v(32.85, 2.42) * mm, "end": v(32.89, 2.4) * mm});
            skLineSegment(sketch, "E8336", {"start": v(32.89, 2.4) * mm, "end": v(32.92, 2.37) * mm});
            skLineSegment(sketch, "E8337", {"start": v(32.92, 2.37) * mm, "end": v(32.95, 2.35) * mm});
            skLineSegment(sketch, "E8338", {"start": v(32.95, 2.35) * mm, "end": v(32.97, 2.32) * mm});
            skLineSegment(sketch, "E8339", {"start": v(32.97, 2.32) * mm, "end": v(33, 2.3) * mm});
            skLineSegment(sketch, "E8340", {"start": v(33, 2.3) * mm, "end": v(33.02, 2.27) * mm});
            skLineSegment(sketch, "E8341", {"start": v(33.02, 2.27) * mm, "end": v(33.04, 2.24) * mm});
            skLineSegment(sketch, "E8342", {"start": v(33.04, 2.24) * mm, "end": v(33.05, 2.22) * mm});
            skLineSegment(sketch, "E8343", {"start": v(33.05, 2.22) * mm, "end": v(33.07, 2.19) * mm});
            skLineSegment(sketch, "E8344", {"start": v(33.07, 2.19) * mm, "end": v(33.08, 2.16) * mm});
            skLineSegment(sketch, "E8345", {"start": v(33.08, 2.16) * mm, "end": v(33.09, 2.12) * mm});
            skLineSegment(sketch, "E8346", {"start": v(33.09, 2.12) * mm, "end": v(33.1, 2.1) * mm});
            skLineSegment(sketch, "E8347", {"start": v(33.1, 2.1) * mm, "end": v(33.1, 2.06) * mm});
            skLineSegment(sketch, "E8348", {"start": v(33.1, 2.06) * mm, "end": v(33.1, 2.02) * mm});
            skLineSegment(sketch, "E8349", {"start": v(33.1, 2.02) * mm, "end": v(33.1, 1.99) * mm});
            skLineSegment(sketch, "E8350", {"start": v(33.1, 1.99) * mm, "end": v(33.1, 1.97) * mm});
            skLineSegment(sketch, "E8351", {"start": v(33.1, 1.97) * mm, "end": v(33.1, 1.95) * mm});
            skLineSegment(sketch, "E8352", {"start": v(33.1, 1.95) * mm, "end": v(33.1, 1.93) * mm});
            skLineSegment(sketch, "E8353", {"start": v(33.1, 1.93) * mm, "end": v(33.1, 1.9) * mm});
            skLineSegment(sketch, "E8354", {"start": v(33.1, 1.9) * mm, "end": v(33.1, 1.88) * mm});
            skLineSegment(sketch, "E8355", {"start": v(33.1, 1.88) * mm, "end": v(33.09, 1.86) * mm});
            skLineSegment(sketch, "E8356", {"start": v(33.09, 1.86) * mm, "end": v(33.08, 1.84) * mm});
            skLineSegment(sketch, "E8357", {"start": v(33.08, 1.84) * mm, "end": v(33.07, 1.81) * mm});
            skLineSegment(sketch, "E8358", {"start": v(33.07, 1.81) * mm, "end": v(33.07, 1.79) * mm});
            skLineSegment(sketch, "E8359", {"start": v(33.07, 1.79) * mm, "end": v(33.06, 1.76) * mm});
            skLineSegment(sketch, "E8360", {"start": v(33.06, 1.76) * mm, "end": v(33.03, 1.7) * mm});
            skLineSegment(sketch, "E8361", {"start": v(33.03, 1.7) * mm, "end": v(33, 1.65) * mm});
            skLineSegment(sketch, "E8362", {"start": v(33, 1.65) * mm, "end": v(32.97, 1.59) * mm});
            skLineSegment(sketch, "E8363", {"start": v(32.97, 1.59) * mm, "end": v(32.94, 1.52) * mm});
            skLineSegment(sketch, "E8364", {"start": v(32.94, 1.52) * mm, "end": v(32.9, 1.46) * mm});
            skLineSegment(sketch, "E8365", {"start": v(32.9, 1.46) * mm, "end": v(32.86, 1.39) * mm});
            skLineSegment(sketch, "E8366", {"start": v(32.86, 1.39) * mm, "end": v(32.8, 1.31) * mm});
            skLineSegment(sketch, "E8367", {"start": v(32.8, 1.31) * mm, "end": v(32.75, 1.24) * mm});
            skLineSegment(sketch, "E8368", {"start": v(32.75, 1.24) * mm, "end": v(32.7, 1.16) * mm});
            skLineSegment(sketch, "E8369", {"start": v(32.7, 1.16) * mm, "end": v(32.64, 1.08) * mm});
            skLineSegment(sketch, "E8370", {"start": v(32.64, 1.08) * mm, "end": v(32.57, 1) * mm});
            skLineSegment(sketch, "E8371", {"start": v(32.57, 1) * mm, "end": v(32.3, 0.64) * mm});
            skLineSegment(sketch, "E8372", {"start": v(32.3, 0.64) * mm, "end": v(31.98, 0.29) * mm});
            skLineSegment(sketch, "E8373", {"start": v(31.98, 0.29) * mm, "end": v(31.63, -0.08) * mm});
            skLineSegment(sketch, "E8374", {"start": v(31.63, -0.08) * mm, "end": v(31.24, -0.44) * mm});
            skLineSegment(sketch, "E8375", {"start": v(31.24, -0.44) * mm, "end": v(31.03, -0.66) * mm});
            skLineSegment(sketch, "E8376", {"start": v(31.03, -0.66) * mm, "end": v(30.82, -0.91) * mm});
            skLineSegment(sketch, "E8377", {"start": v(30.82, -0.91) * mm, "end": v(30.62, -1.18) * mm});
            skLineSegment(sketch, "E8378", {"start": v(30.62, -1.18) * mm, "end": v(30.42, -1.48) * mm});
            skLineSegment(sketch, "E8379", {"start": v(30.42, -1.48) * mm, "end": v(30.37, -1.56) * mm});
            skLineSegment(sketch, "E8380", {"start": v(30.37, -1.56) * mm, "end": v(30.33, -1.63) * mm});
            skLineSegment(sketch, "E8381", {"start": v(30.33, -1.63) * mm, "end": v(30.29, -1.7) * mm});
            skLineSegment(sketch, "E8382", {"start": v(30.29, -1.7) * mm, "end": v(30.25, -1.76) * mm});
            skLineSegment(sketch, "E8383", {"start": v(30.25, -1.76) * mm, "end": v(30.21, -1.83) * mm});
            skLineSegment(sketch, "E8384", {"start": v(30.21, -1.83) * mm, "end": v(30.18, -1.9) * mm});
            skLineSegment(sketch, "E8385", {"start": v(30.18, -1.9) * mm, "end": v(30.15, -1.95) * mm});
            skLineSegment(sketch, "E8386", {"start": v(30.15, -1.95) * mm, "end": v(30.13, -2) * mm});
            skLineSegment(sketch, "E8387", {"start": v(30.13, -2) * mm, "end": v(30.1, -2.06) * mm});
            skLineSegment(sketch, "E8388", {"start": v(30.1, -2.06) * mm, "end": v(30.08, -2.11) * mm});
            skLineSegment(sketch, "E8389", {"start": v(30.08, -2.11) * mm, "end": v(30.07, -2.16) * mm});
            skLineSegment(sketch, "E8390", {"start": v(30.07, -2.16) * mm, "end": v(30.05, -2.2) * mm});
            skLineSegment(sketch, "E8391", {"start": v(30.05, -2.2) * mm, "end": v(30.05, -2.23) * mm});
            skLineSegment(sketch, "E8392", {"start": v(30.05, -2.23) * mm, "end": v(30.04, -2.25) * mm});
            skLineSegment(sketch, "E8393", {"start": v(30.04, -2.25) * mm, "end": v(30.04, -2.27) * mm});
            skLineSegment(sketch, "E8394", {"start": v(30.04, -2.27) * mm, "end": v(30.03, -2.3) * mm});
            skLineSegment(sketch, "E8395", {"start": v(30.03, -2.3) * mm, "end": v(30.03, -2.3) * mm});
            skLineSegment(sketch, "E8396", {"start": v(30.03, -2.3) * mm, "end": v(30.03, -2.33) * mm});
            skLineSegment(sketch, "E8397", {"start": v(30.03, -2.33) * mm, "end": v(30.03, -2.35) * mm});
            skLineSegment(sketch, "E8398", {"start": v(30.03, -2.35) * mm, "end": v(30.03, -2.36) * mm});
            skLineSegment(sketch, "E8399", {"start": v(30.03, -2.36) * mm, "end": v(30.03, -2.41) * mm});
            skLineSegment(sketch, "E8400", {"start": v(30.03, -2.41) * mm, "end": v(30.03, -2.46) * mm});
            skLineSegment(sketch, "E8401", {"start": v(30.03, -2.46) * mm, "end": v(30.04, -2.48) * mm});
            skLineSegment(sketch, "E8402", {"start": v(30.04, -2.48) * mm, "end": v(30.04, -2.5) * mm});
            skLineSegment(sketch, "E8403", {"start": v(30.04, -2.5) * mm, "end": v(30.04, -2.52) * mm});
            skLineSegment(sketch, "E8404", {"start": v(30.04, -2.52) * mm, "end": v(30.05, -2.53) * mm});
            skLineSegment(sketch, "E8405", {"start": v(30.05, -2.53) * mm, "end": v(30.05, -2.55) * mm});
            skLineSegment(sketch, "E8406", {"start": v(30.05, -2.55) * mm, "end": v(30.06, -2.57) * mm});
            skLineSegment(sketch, "E8407", {"start": v(30.06, -2.57) * mm, "end": v(30.06, -2.59) * mm});
            skLineSegment(sketch, "E8408", {"start": v(30.06, -2.59) * mm, "end": v(30.07, -2.6) * mm});
            skLineSegment(sketch, "E8409", {"start": v(30.07, -2.6) * mm, "end": v(30.08, -2.62) * mm});
            skLineSegment(sketch, "E8410", {"start": v(30.08, -2.62) * mm, "end": v(30.09, -2.63) * mm});
            skLineSegment(sketch, "E8411", {"start": v(30.09, -2.63) * mm, "end": v(30.1, -2.64) * mm});
            skLineSegment(sketch, "E8412", {"start": v(30.1, -2.64) * mm, "end": v(30.1, -2.66) * mm});
            skLineSegment(sketch, "E8413", {"start": v(30.1, -2.66) * mm, "end": v(30.11, -2.67) * mm});
            skLineSegment(sketch, "E8414", {"start": v(30.11, -2.67) * mm, "end": v(30.12, -2.68) * mm});
            skLineSegment(sketch, "E8415", {"start": v(30.12, -2.68) * mm, "end": v(30.14, -2.7) * mm});
            skLineSegment(sketch, "E8416", {"start": v(30.14, -2.7) * mm, "end": v(30.15, -2.7) * mm});
            skLineSegment(sketch, "E8417", {"start": v(30.15, -2.7) * mm, "end": v(30.16, -2.7) * mm});
            skLineSegment(sketch, "E8418", {"start": v(30.16, -2.7) * mm, "end": v(30.17, -2.72) * mm});
            skLineSegment(sketch, "E8419", {"start": v(30.17, -2.72) * mm, "end": v(30.19, -2.72) * mm});
            skLineSegment(sketch, "E8420", {"start": v(30.19, -2.72) * mm, "end": v(30.2, -2.73) * mm});
            skLineSegment(sketch, "E8421", {"start": v(30.2, -2.73) * mm, "end": v(30.21, -2.74) * mm});
            skLineSegment(sketch, "E8422", {"start": v(30.21, -2.74) * mm, "end": v(30.23, -2.74) * mm});
            skLineSegment(sketch, "E8423", {"start": v(30.23, -2.74) * mm, "end": v(30.24, -2.75) * mm});
            skLineSegment(sketch, "E8424", {"start": v(30.24, -2.75) * mm, "end": v(30.26, -2.75) * mm});
            skLineSegment(sketch, "E8425", {"start": v(30.26, -2.75) * mm, "end": v(30.28, -2.75) * mm});
            skLineSegment(sketch, "E8426", {"start": v(30.28, -2.75) * mm, "end": v(30.3, -2.75) * mm});
            skLineSegment(sketch, "E8427", {"start": v(30.3, -2.75) * mm, "end": v(30.31, -2.75) * mm});
            skLineSegment(sketch, "E8428", {"start": v(30.31, -2.75) * mm, "end": v(30.33, -2.75) * mm});
            skLineSegment(sketch, "E8429", {"start": v(30.33, -2.75) * mm, "end": v(30.34, -2.75) * mm});
            skLineSegment(sketch, "E8430", {"start": v(30.34, -2.75) * mm, "end": v(30.35, -2.75) * mm});
            skLineSegment(sketch, "E8431", {"start": v(30.35, -2.75) * mm, "end": v(30.36, -2.75) * mm});
            skLineSegment(sketch, "E8432", {"start": v(30.36, -2.75) * mm, "end": v(30.37, -2.75) * mm});
            skLineSegment(sketch, "E8433", {"start": v(30.37, -2.75) * mm, "end": v(30.37, -2.75) * mm});
            skLineSegment(sketch, "E8434", {"start": v(30.37, -2.75) * mm, "end": v(30.38, -2.75) * mm});
            skLineSegment(sketch, "E8435", {"start": v(30.38, -2.75) * mm, "end": v(30.4, -2.74) * mm});
            skLineSegment(sketch, "E8436", {"start": v(30.4, -2.74) * mm, "end": v(30.4, -2.74) * mm});
            skLineSegment(sketch, "E8437", {"start": v(30.4, -2.74) * mm, "end": v(30.42, -2.73) * mm});
            skLineSegment(sketch, "E8438", {"start": v(30.42, -2.73) * mm, "end": v(30.43, -2.73) * mm});
            skLineSegment(sketch, "E8439", {"start": v(30.43, -2.73) * mm, "end": v(30.44, -2.72) * mm});
            skLineSegment(sketch, "E8440", {"start": v(30.44, -2.72) * mm, "end": v(30.45, -2.72) * mm});
            skLineSegment(sketch, "E8441", {"start": v(30.45, -2.72) * mm, "end": v(30.46, -2.71) * mm});
            skLineSegment(sketch, "E8442", {"start": v(30.46, -2.71) * mm, "end": v(30.49, -2.7) * mm});
            skLineSegment(sketch, "E8443", {"start": v(30.49, -2.7) * mm, "end": v(30.52, -2.68) * mm});
            skLineSegment(sketch, "E8444", {"start": v(30.52, -2.68) * mm, "end": v(30.54, -2.67) * mm});
            skLineSegment(sketch, "E8445", {"start": v(30.54, -2.67) * mm, "end": v(30.57, -2.65) * mm});
            skLineSegment(sketch, "E8446", {"start": v(30.57, -2.65) * mm, "end": v(30.6, -2.62) * mm});
            skLineSegment(sketch, "E8447", {"start": v(30.6, -2.62) * mm, "end": v(30.64, -2.6) * mm});
            skLineSegment(sketch, "E8448", {"start": v(30.64, -2.6) * mm, "end": v(30.67, -2.57) * mm});
            skLineSegment(sketch, "E8449", {"start": v(30.67, -2.57) * mm, "end": v(30.7, -2.55) * mm});
            skLineSegment(sketch, "E8450", {"start": v(30.7, -2.55) * mm, "end": v(30.75, -2.52) * mm});
            skLineSegment(sketch, "E8451", {"start": v(30.75, -2.52) * mm, "end": v(30.79, -2.49) * mm});
            skLineSegment(sketch, "E8452", {"start": v(30.79, -2.49) * mm, "end": v(30.83, -2.45) * mm});
            skLineSegment(sketch, "E8453", {"start": v(30.83, -2.45) * mm, "end": v(30.87, -2.42) * mm});
            skLineSegment(sketch, "E8454", {"start": v(30.87, -2.42) * mm, "end": v(30.96, -2.34) * mm});
            skLineSegment(sketch, "E8455", {"start": v(30.96, -2.34) * mm, "end": v(31.05, -2.25) * mm});
            skLineSegment(sketch, "E8456", {"start": v(31.05, -2.25) * mm, "end": v(31.15, -2.16) * mm});
            skLineSegment(sketch, "E8457", {"start": v(31.15, -2.16) * mm, "end": v(31.25, -2.06) * mm});
            skLineSegment(sketch, "E8458", {"start": v(31.25, -2.06) * mm, "end": v(31.37, -1.95) * mm});
            skLineSegment(sketch, "E8459", {"start": v(31.37, -1.95) * mm, "end": v(31.48, -1.83) * mm});
            skLineSegment(sketch, "E8460", {"start": v(31.48, -1.83) * mm, "end": v(31.58, -1.74) * mm});
            skLineSegment(sketch, "E8461", {"start": v(31.58, -1.74) * mm, "end": v(32.09, -1.23) * mm});
            skLineSegment(sketch, "E8462", {"start": v(32.09, -1.23) * mm, "end": v(33.18, -0.13) * mm});
            skLineSegment(sketch, "E8463", {"start": v(33.18, -0.13) * mm, "end": v(33.76, 0.46) * mm});
            skLineSegment(sketch, "E8464", {"start": v(33.76, 0.46) * mm, "end": v(34.35, 1.03) * mm});
            skLineSegment(sketch, "E8465", {"start": v(34.35, 1.03) * mm, "end": v(34.91, 1.55) * mm});
            skLineSegment(sketch, "E8466", {"start": v(34.91, 1.55) * mm, "end": v(35.45, 2.02) * mm});
            skLineSegment(sketch, "E8467", {"start": v(35.45, 2.02) * mm, "end": v(35.97, 2.44) * mm});
            skLineSegment(sketch, "E8468", {"start": v(35.97, 2.44) * mm, "end": v(36.22, 2.62) * mm});
            skLineSegment(sketch, "E8469", {"start": v(36.22, 2.62) * mm, "end": v(36.34, 2.7) * mm});
            skLineSegment(sketch, "E8470", {"start": v(36.34, 2.7) * mm, "end": v(36.46, 2.78) * mm});
            skLineSegment(sketch, "E8471", {"start": v(36.46, 2.78) * mm, "end": v(36.58, 2.86) * mm});
            skLineSegment(sketch, "E8472", {"start": v(36.58, 2.86) * mm, "end": v(36.7, 2.92) * mm});
            skLineSegment(sketch, "E8473", {"start": v(36.7, 2.92) * mm, "end": v(36.8, 2.98) * mm});
            skLineSegment(sketch, "E8474", {"start": v(36.8, 2.98) * mm, "end": v(36.92, 3.03) * mm});
            skLineSegment(sketch, "E8475", {"start": v(36.92, 3.03) * mm, "end": v(37.03, 3.08) * mm});
            skLineSegment(sketch, "E8476", {"start": v(37.03, 3.08) * mm, "end": v(37.13, 3.12) * mm});
            skLineSegment(sketch, "E8477", {"start": v(37.13, 3.12) * mm, "end": v(37.23, 3.15) * mm});
            skLineSegment(sketch, "E8478", {"start": v(37.23, 3.15) * mm, "end": v(37.33, 3.18) * mm});
            skLineSegment(sketch, "E8479", {"start": v(37.33, 3.18) * mm, "end": v(37.43, 3.2) * mm});
            skLineSegment(sketch, "E8480", {"start": v(37.43, 3.2) * mm, "end": v(37.52, 3.22) * mm});
            skLineSegment(sketch, "E8481", {"start": v(37.52, 3.22) * mm, "end": v(37.62, 3.23) * mm});
            skLineSegment(sketch, "E8482", {"start": v(37.62, 3.23) * mm, "end": v(37.7, 3.23) * mm});
            skLineSegment(sketch, "E8483", {"start": v(37.7, 3.23) * mm, "end": v(37.76, 3.23) * mm});
            skLineSegment(sketch, "E8484", {"start": v(37.76, 3.23) * mm, "end": v(37.81, 3.23) * mm});
            skLineSegment(sketch, "E8485", {"start": v(37.81, 3.23) * mm, "end": v(37.86, 3.22) * mm});
            skLineSegment(sketch, "E8486", {"start": v(37.86, 3.22) * mm, "end": v(37.91, 3.21) * mm});
            skLineSegment(sketch, "E8487", {"start": v(37.91, 3.21) * mm, "end": v(37.96, 3.2) * mm});
            skLineSegment(sketch, "E8488", {"start": v(37.96, 3.2) * mm, "end": v(38, 3.18) * mm});
            skLineSegment(sketch, "E8489", {"start": v(38, 3.18) * mm, "end": v(38.06, 3.17) * mm});
            skLineSegment(sketch, "E8490", {"start": v(38.06, 3.17) * mm, "end": v(38.1, 3.15) * mm});
            skLineSegment(sketch, "E8491", {"start": v(38.1, 3.15) * mm, "end": v(38.14, 3.13) * mm});
            skLineSegment(sketch, "E8492", {"start": v(38.14, 3.13) * mm, "end": v(38.19, 3.1) * mm});
            skLineSegment(sketch, "E8493", {"start": v(38.19, 3.1) * mm, "end": v(38.23, 3.07) * mm});
            skLineSegment(sketch, "E8494", {"start": v(38.23, 3.07) * mm, "end": v(38.27, 3.04) * mm});
            skLineSegment(sketch, "E8495", {"start": v(38.27, 3.04) * mm, "end": v(38.3, 3.01) * mm});
            skLineSegment(sketch, "E8496", {"start": v(38.3, 3.01) * mm, "end": v(38.34, 2.98) * mm});
            skLineSegment(sketch, "E8497", {"start": v(38.34, 2.98) * mm, "end": v(38.38, 2.94) * mm});
            skLineSegment(sketch, "E8498", {"start": v(38.38, 2.94) * mm, "end": v(38.41, 2.9) * mm});
            skLineSegment(sketch, "E8499", {"start": v(38.41, 2.9) * mm, "end": v(38.45, 2.86) * mm});
            skLineSegment(sketch, "E8500", {"start": v(38.45, 2.86) * mm, "end": v(38.48, 2.82) * mm});
            skLineSegment(sketch, "E8501", {"start": v(38.48, 2.82) * mm, "end": v(38.51, 2.77) * mm});
            skLineSegment(sketch, "E8502", {"start": v(38.51, 2.77) * mm, "end": v(38.54, 2.73) * mm});
            skLineSegment(sketch, "E8503", {"start": v(38.54, 2.73) * mm, "end": v(38.57, 2.68) * mm});
            skLineSegment(sketch, "E8504", {"start": v(38.57, 2.68) * mm, "end": v(38.6, 2.64) * mm});
            skLineSegment(sketch, "E8505", {"start": v(38.6, 2.64) * mm, "end": v(38.61, 2.6) * mm});
            skLineSegment(sketch, "E8506", {"start": v(38.61, 2.6) * mm, "end": v(38.63, 2.54) * mm});
            skLineSegment(sketch, "E8507", {"start": v(38.63, 2.54) * mm, "end": v(38.65, 2.5) * mm});
            skLineSegment(sketch, "E8508", {"start": v(38.65, 2.5) * mm, "end": v(38.66, 2.44) * mm});
            skLineSegment(sketch, "E8509", {"start": v(38.66, 2.44) * mm, "end": v(38.68, 2.39) * mm});
            skLineSegment(sketch, "E8510", {"start": v(38.68, 2.39) * mm, "end": v(38.69, 2.33) * mm});
            skLineSegment(sketch, "E8511", {"start": v(38.69, 2.33) * mm, "end": v(38.7, 2.28) * mm});
            skLineSegment(sketch, "E8512", {"start": v(38.7, 2.28) * mm, "end": v(38.7, 2.22) * mm});
            skLineSegment(sketch, "E8513", {"start": v(38.7, 2.22) * mm, "end": v(38.7, 2.16) * mm});
            skLineSegment(sketch, "E8514", {"start": v(38.7, 2.16) * mm, "end": v(38.7, 2.1) * mm});
            skLineSegment(sketch, "E8515", {"start": v(38.7, 2.1) * mm, "end": v(38.7, 2.08) * mm});
            skLineSegment(sketch, "E8516", {"start": v(38.7, 2.08) * mm, "end": v(38.7, 2.06) * mm});
            skLineSegment(sketch, "E8517", {"start": v(38.7, 2.06) * mm, "end": v(38.7, 2.04) * mm});
            skLineSegment(sketch, "E8518", {"start": v(38.7, 2.04) * mm, "end": v(38.7, 2.02) * mm});
            skLineSegment(sketch, "E8519", {"start": v(38.7, 2.02) * mm, "end": v(38.7, 2) * mm});
            skLineSegment(sketch, "E8520", {"start": v(38.7, 2) * mm, "end": v(38.69, 1.97) * mm});
            skLineSegment(sketch, "E8521", {"start": v(38.69, 1.97) * mm, "end": v(38.68, 1.94) * mm});
            skLineSegment(sketch, "E8522", {"start": v(38.68, 1.94) * mm, "end": v(38.68, 1.91) * mm});
            skLineSegment(sketch, "E8523", {"start": v(38.68, 1.91) * mm, "end": v(38.67, 1.88) * mm});
            skLineSegment(sketch, "E8524", {"start": v(38.67, 1.88) * mm, "end": v(38.65, 1.82) * mm});
            skLineSegment(sketch, "E8525", {"start": v(38.65, 1.82) * mm, "end": v(38.63, 1.76) * mm});
            skLineSegment(sketch, "E8526", {"start": v(38.63, 1.76) * mm, "end": v(38.6, 1.7) * mm});
            skLineSegment(sketch, "E8527", {"start": v(38.6, 1.7) * mm, "end": v(38.58, 1.62) * mm});
            skLineSegment(sketch, "E8528", {"start": v(38.58, 1.62) * mm, "end": v(38.55, 1.54) * mm});
            skLineSegment(sketch, "E8529", {"start": v(38.55, 1.54) * mm, "end": v(38.52, 1.46) * mm});
            skLineSegment(sketch, "E8530", {"start": v(38.52, 1.46) * mm, "end": v(38.48, 1.38) * mm});
            skLineSegment(sketch, "E8531", {"start": v(38.48, 1.38) * mm, "end": v(38.44, 1.29) * mm});
            skLineSegment(sketch, "E8532", {"start": v(38.44, 1.29) * mm, "end": v(38.4, 1.2) * mm});
            skLineSegment(sketch, "E8533", {"start": v(38.4, 1.2) * mm, "end": v(38.35, 1.1) * mm});
            skLineSegment(sketch, "E8534", {"start": v(38.35, 1.1) * mm, "end": v(38.27, 0.95) * mm});
            skLineSegment(sketch, "E8535", {"start": v(38.27, 0.95) * mm, "end": v(38.16, 0.73) * mm});
            skLineSegment(sketch, "E8536", {"start": v(38.16, 0.73) * mm, "end": v(38.03, 0.5) * mm});
            skLineSegment(sketch, "E8537", {"start": v(38.03, 0.5) * mm, "end": v(37.89, 0.27) * mm});
            skLineSegment(sketch, "E8538", {"start": v(37.89, 0.27) * mm, "end": v(37.73, 0.02) * mm});
            skLineSegment(sketch, "E8539", {"start": v(37.73, 0.02) * mm, "end": v(37.57, -0.24) * mm});
            skLineSegment(sketch, "E8540", {"start": v(37.57, -0.24) * mm, "end": v(37.4, -0.52) * mm});
            skLineSegment(sketch, "E8541", {"start": v(37.4, -0.52) * mm, "end": v(37.2, -0.8) * mm});
            skLineSegment(sketch, "E8542", {"start": v(37.2, -0.8) * mm, "end": v(37, -1.1) * mm});
            skLineSegment(sketch, "E8543", {"start": v(37, -1.1) * mm, "end": v(36.78, -1.42) * mm});
            skLineSegment(sketch, "E8544", {"start": v(36.78, -1.42) * mm, "end": v(36.55, -1.75) * mm});
            skLineSegment(sketch, "E8545", {"start": v(36.55, -1.75) * mm, "end": v(36.31, -2.1) * mm});
            skLineSegment(sketch, "E8546", {"start": v(36.31, -2.1) * mm, "end": v(36.05, -2.45) * mm});
            skLineSegment(sketch, "E8547", {"start": v(36.05, -2.45) * mm, "end": v(35.78, -2.83) * mm});
            skLineSegment(sketch, "E8548", {"start": v(35.78, -2.83) * mm, "end": v(35.48, -3.22) * mm});
            skLineSegment(sketch, "E8549", {"start": v(35.48, -3.22) * mm, "end": v(34.86, -4.06) * mm});
            skLineSegment(sketch, "E8550", {"start": v(55.95, -2.1) * mm, "end": v(55.95, -3.04) * mm});
            skLineSegment(sketch, "E8551", {"start": v(55.95, -3.04) * mm, "end": v(55.59, -3.27) * mm});
            skLineSegment(sketch, "E8552", {"start": v(55.59, -3.27) * mm, "end": v(55.41, -3.37) * mm});
            skLineSegment(sketch, "E8553", {"start": v(55.41, -3.37) * mm, "end": v(55.24, -3.46) * mm});
            skLineSegment(sketch, "E8554", {"start": v(55.24, -3.46) * mm, "end": v(55.08, -3.55) * mm});
            skLineSegment(sketch, "E8555", {"start": v(55.08, -3.55) * mm, "end": v(54.91, -3.63) * mm});
            skLineSegment(sketch, "E8556", {"start": v(54.91, -3.63) * mm, "end": v(54.76, -3.7) * mm});
            skLineSegment(sketch, "E8557", {"start": v(54.76, -3.7) * mm, "end": v(54.6, -3.76) * mm});
            skLineSegment(sketch, "E8558", {"start": v(54.6, -3.76) * mm, "end": v(54.46, -3.82) * mm});
            skLineSegment(sketch, "E8559", {"start": v(54.46, -3.82) * mm, "end": v(54.32, -3.86) * mm});
            skLineSegment(sketch, "E8560", {"start": v(54.32, -3.86) * mm, "end": v(54.19, -3.9) * mm});
            skLineSegment(sketch, "E8561", {"start": v(54.19, -3.9) * mm, "end": v(54.06, -3.94) * mm});
            skLineSegment(sketch, "E8562", {"start": v(54.06, -3.94) * mm, "end": v(53.93, -3.96) * mm});
            skLineSegment(sketch, "E8563", {"start": v(53.93, -3.96) * mm, "end": v(53.8, -3.98) * mm});
            skLineSegment(sketch, "E8564", {"start": v(53.8, -3.98) * mm, "end": v(53.7, -4) * mm});
            skLineSegment(sketch, "E8565", {"start": v(53.7, -4) * mm, "end": v(53.58, -4) * mm});
            skLineSegment(sketch, "E8566", {"start": v(53.58, -4) * mm, "end": v(53.46, -4) * mm});
            skLineSegment(sketch, "E8567", {"start": v(53.46, -4) * mm, "end": v(53.22, -3.98) * mm});
            skLineSegment(sketch, "E8568", {"start": v(53.22, -3.98) * mm, "end": v(52.96, -3.94) * mm});
            skLineSegment(sketch, "E8569", {"start": v(52.96, -3.94) * mm, "end": v(52.7, -3.88) * mm});
            skLineSegment(sketch, "E8570", {"start": v(52.7, -3.88) * mm, "end": v(52.57, -3.84) * mm});
            skLineSegment(sketch, "E8571", {"start": v(52.57, -3.84) * mm, "end": v(52.25, -4.24) * mm});
            skLineSegment(sketch, "E8572", {"start": v(52.25, -4.24) * mm, "end": v(51.94, -4.6) * mm});
            skLineSegment(sketch, "E8573", {"start": v(51.94, -4.6) * mm, "end": v(51.64, -4.95) * mm});
            skLineSegment(sketch, "E8574", {"start": v(51.64, -4.95) * mm, "end": v(51.36, -5.27) * mm});
            skLineSegment(sketch, "E8575", {"start": v(51.36, -5.27) * mm, "end": v(51.08, -5.55) * mm});
            skLineSegment(sketch, "E8576", {"start": v(51.08, -5.55) * mm, "end": v(50.82, -5.82) * mm});
            skLineSegment(sketch, "E8577", {"start": v(50.82, -5.82) * mm, "end": v(50.57, -6.05) * mm});
            skLineSegment(sketch, "E8578", {"start": v(50.57, -6.05) * mm, "end": v(50.45, -6.15) * mm});
            skLineSegment(sketch, "E8579", {"start": v(50.45, -6.15) * mm, "end": v(50.33, -6.25) * mm});
            skLineSegment(sketch, "E8580", {"start": v(50.33, -6.25) * mm, "end": v(50.1, -6.43) * mm});
            skLineSegment(sketch, "E8581", {"start": v(50.1, -6.43) * mm, "end": v(49.86, -6.59) * mm});
            skLineSegment(sketch, "E8582", {"start": v(49.86, -6.59) * mm, "end": v(49.75, -6.66) * mm});
            skLineSegment(sketch, "E8583", {"start": v(49.75, -6.66) * mm, "end": v(49.63, -6.72) * mm});
            skLineSegment(sketch, "E8584", {"start": v(49.63, -6.72) * mm, "end": v(49.52, -6.78) * mm});
            skLineSegment(sketch, "E8585", {"start": v(49.52, -6.78) * mm, "end": v(49.4, -6.83) * mm});
            skLineSegment(sketch, "E8586", {"start": v(49.4, -6.83) * mm, "end": v(49.28, -6.87) * mm});
            skLineSegment(sketch, "E8587", {"start": v(49.28, -6.87) * mm, "end": v(49.17, -6.91) * mm});
            skLineSegment(sketch, "E8588", {"start": v(49.17, -6.91) * mm, "end": v(49.05, -6.95) * mm});
            skLineSegment(sketch, "E8589", {"start": v(49.05, -6.95) * mm, "end": v(48.93, -6.97) * mm});
            skLineSegment(sketch, "E8590", {"start": v(48.93, -6.97) * mm, "end": v(48.81, -7) * mm});
            skLineSegment(sketch, "E8591", {"start": v(48.81, -7) * mm, "end": v(48.7, -7) * mm});
            skLineSegment(sketch, "E8592", {"start": v(48.7, -7) * mm, "end": v(48.58, -7.02) * mm});
            skLineSegment(sketch, "E8593", {"start": v(48.58, -7.02) * mm, "end": v(48.46, -7.02) * mm});
            skLineSegment(sketch, "E8594", {"start": v(48.46, -7.02) * mm, "end": v(48.33, -7.02) * mm});
            skLineSegment(sketch, "E8595", {"start": v(48.33, -7.02) * mm, "end": v(48.2, -7) * mm});
            skLineSegment(sketch, "E8596", {"start": v(48.2, -7) * mm, "end": v(48.07, -6.98) * mm});
            skLineSegment(sketch, "E8597", {"start": v(48.07, -6.98) * mm, "end": v(47.95, -6.95) * mm});
            skLineSegment(sketch, "E8598", {"start": v(47.95, -6.95) * mm, "end": v(47.83, -6.9) * mm});
            skLineSegment(sketch, "E8599", {"start": v(47.83, -6.9) * mm, "end": v(47.72, -6.86) * mm});
            skLineSegment(sketch, "E8600", {"start": v(47.72, -6.86) * mm, "end": v(47.6, -6.8) * mm});
            skLineSegment(sketch, "E8601", {"start": v(47.6, -6.8) * mm, "end": v(47.5, -6.73) * mm});
            skLineSegment(sketch, "E8602", {"start": v(47.5, -6.73) * mm, "end": v(47.4, -6.66) * mm});
            skLineSegment(sketch, "E8603", {"start": v(47.4, -6.66) * mm, "end": v(47.3, -6.57) * mm});
            skLineSegment(sketch, "E8604", {"start": v(47.3, -6.57) * mm, "end": v(47.2, -6.48) * mm});
            skLineSegment(sketch, "E8605", {"start": v(47.2, -6.48) * mm, "end": v(47.11, -6.38) * mm});
            skLineSegment(sketch, "E8606", {"start": v(47.11, -6.38) * mm, "end": v(47.03, -6.27) * mm});
            skLineSegment(sketch, "E8607", {"start": v(47.03, -6.27) * mm, "end": v(46.94, -6.15) * mm});
            skLineSegment(sketch, "E8608", {"start": v(46.94, -6.15) * mm, "end": v(46.86, -6.02) * mm});
            skLineSegment(sketch, "E8609", {"start": v(46.86, -6.02) * mm, "end": v(46.79, -5.88) * mm});
            skLineSegment(sketch, "E8610", {"start": v(46.79, -5.88) * mm, "end": v(46.65, -5.58) * mm});
            skLineSegment(sketch, "E8611", {"start": v(46.65, -5.58) * mm, "end": v(46.53, -5.27) * mm});
            skLineSegment(sketch, "E8612", {"start": v(46.53, -5.27) * mm, "end": v(46.43, -4.94) * mm});
            skLineSegment(sketch, "E8613", {"start": v(46.43, -4.94) * mm, "end": v(46.35, -4.6) * mm});
            skLineSegment(sketch, "E8614", {"start": v(46.35, -4.6) * mm, "end": v(46.29, -4.24) * mm});
            skLineSegment(sketch, "E8615", {"start": v(46.29, -4.24) * mm, "end": v(46.24, -3.86) * mm});
            skLineSegment(sketch, "E8616", {"start": v(46.24, -3.86) * mm, "end": v(46.22, -3.46) * mm});
            skLineSegment(sketch, "E8617", {"start": v(46.22, -3.46) * mm, "end": v(46.2, -3.04) * mm});
            skLineSegment(sketch, "E8618", {"start": v(46.2, -3.04) * mm, "end": v(46.23, -2.46) * mm});
            skLineSegment(sketch, "E8619", {"start": v(46.23, -2.46) * mm, "end": v(46.3, -1.87) * mm});
            skLineSegment(sketch, "E8620", {"start": v(46.3, -1.87) * mm, "end": v(46.4, -1.26) * mm});
            skLineSegment(sketch, "E8621", {"start": v(46.4, -1.26) * mm, "end": v(46.55, -0.64) * mm});
            skLineSegment(sketch, "E8622", {"start": v(46.55, -0.64) * mm, "end": v(46.75, -0.01) * mm});
            skLineSegment(sketch, "E8623", {"start": v(46.75, -0.01) * mm, "end": v(46.99, 0.63) * mm});
            skLineSegment(sketch, "E8624", {"start": v(46.99, 0.63) * mm, "end": v(47.27, 1.29) * mm});
            skLineSegment(sketch, "E8625", {"start": v(47.27, 1.29) * mm, "end": v(47.6, 1.96) * mm});
            skLineSegment(sketch, "E8626", {"start": v(47.6, 1.96) * mm, "end": v(48.32, 3.3) * mm});
            skLineSegment(sketch, "E8627", {"start": v(48.32, 3.3) * mm, "end": v(49.12, 4.59) * mm});
            skLineSegment(sketch, "E8628", {"start": v(49.12, 4.59) * mm, "end": v(50, 5.83) * mm});
            skLineSegment(sketch, "E8629", {"start": v(50, 5.83) * mm, "end": v(50.94, 7.03) * mm});
            skLineSegment(sketch, "E8630", {"start": v(50.94, 7.03) * mm, "end": v(51.91, 8.17) * mm});
            skLineSegment(sketch, "E8631", {"start": v(51.91, 8.17) * mm, "end": v(52.87, 9.2) * mm});
            skLineSegment(sketch, "E8632", {"start": v(52.87, 9.2) * mm, "end": v(53.81, 10.13) * mm});
            skLineSegment(sketch, "E8633", {"start": v(53.81, 10.13) * mm, "end": v(54.74, 10.95) * mm});
            skLineSegment(sketch, "E8634", {"start": v(54.74, 10.95) * mm, "end": v(54.96, 11.14) * mm});
            skLineSegment(sketch, "E8635", {"start": v(54.96, 11.14) * mm, "end": v(55.18, 11.32) * mm});
            skLineSegment(sketch, "E8636", {"start": v(55.18, 11.32) * mm, "end": v(55.39, 11.48) * mm});
            skLineSegment(sketch, "E8637", {"start": v(55.39, 11.48) * mm, "end": v(55.58, 11.63) * mm});
            skLineSegment(sketch, "E8638", {"start": v(55.58, 11.63) * mm, "end": v(55.77, 11.77) * mm});
            skLineSegment(sketch, "E8639", {"start": v(55.77, 11.77) * mm, "end": v(55.95, 11.9) * mm});
            skLineSegment(sketch, "E8640", {"start": v(55.95, 11.9) * mm, "end": v(56.12, 12.01) * mm});
            skLineSegment(sketch, "E8641", {"start": v(56.12, 12.01) * mm, "end": v(56.28, 12.11) * mm});
            skLineSegment(sketch, "E8642", {"start": v(56.28, 12.11) * mm, "end": v(56.43, 12.2) * mm});
            skLineSegment(sketch, "E8643", {"start": v(56.43, 12.2) * mm, "end": v(56.5, 12.24) * mm});
            skLineSegment(sketch, "E8644", {"start": v(56.5, 12.24) * mm, "end": v(56.57, 12.28) * mm});
            skLineSegment(sketch, "E8645", {"start": v(56.57, 12.28) * mm, "end": v(56.64, 12.32) * mm});
            skLineSegment(sketch, "E8646", {"start": v(56.64, 12.32) * mm, "end": v(56.7, 12.35) * mm});
            skLineSegment(sketch, "E8647", {"start": v(56.7, 12.35) * mm, "end": v(56.77, 12.38) * mm});
            skLineSegment(sketch, "E8648", {"start": v(56.77, 12.38) * mm, "end": v(56.83, 12.4) * mm});
            skLineSegment(sketch, "E8649", {"start": v(56.83, 12.4) * mm, "end": v(56.88, 12.43) * mm});
            skLineSegment(sketch, "E8650", {"start": v(56.88, 12.43) * mm, "end": v(56.94, 12.45) * mm});
            skLineSegment(sketch, "E8651", {"start": v(56.94, 12.45) * mm, "end": v(57, 12.46) * mm});
            skLineSegment(sketch, "E8652", {"start": v(57, 12.46) * mm, "end": v(57.04, 12.48) * mm});
            skLineSegment(sketch, "E8653", {"start": v(57.04, 12.48) * mm, "end": v(57.1, 12.49) * mm});
            skLineSegment(sketch, "E8654", {"start": v(57.1, 12.49) * mm, "end": v(57.14, 12.5) * mm});
            skLineSegment(sketch, "E8655", {"start": v(57.14, 12.5) * mm, "end": v(57.18, 12.5) * mm});
            skLineSegment(sketch, "E8656", {"start": v(57.18, 12.5) * mm, "end": v(57.2, 12.5) * mm});
            skLineSegment(sketch, "E8657", {"start": v(57.2, 12.5) * mm, "end": v(57.23, 12.5) * mm});
            skLineSegment(sketch, "E8658", {"start": v(57.23, 12.5) * mm, "end": v(57.26, 12.5) * mm});
            skLineSegment(sketch, "E8659", {"start": v(57.26, 12.5) * mm, "end": v(57.3, 12.5) * mm});
            skLineSegment(sketch, "E8660", {"start": v(57.3, 12.5) * mm, "end": v(57.34, 12.5) * mm});
            skLineSegment(sketch, "E8661", {"start": v(57.34, 12.5) * mm, "end": v(57.37, 12.49) * mm});
            skLineSegment(sketch, "E8662", {"start": v(57.37, 12.49) * mm, "end": v(57.4, 12.48) * mm});
            skLineSegment(sketch, "E8663", {"start": v(57.4, 12.48) * mm, "end": v(57.44, 12.47) * mm});
            skLineSegment(sketch, "E8664", {"start": v(57.44, 12.47) * mm, "end": v(57.47, 12.46) * mm});
            skLineSegment(sketch, "E8665", {"start": v(57.47, 12.46) * mm, "end": v(57.5, 12.45) * mm});
            skLineSegment(sketch, "E8666", {"start": v(57.5, 12.45) * mm, "end": v(57.53, 12.43) * mm});
            skLineSegment(sketch, "E8667", {"start": v(57.53, 12.43) * mm, "end": v(57.55, 12.42) * mm});
            skLineSegment(sketch, "E8668", {"start": v(57.55, 12.42) * mm, "end": v(57.58, 12.4) * mm});
            skLineSegment(sketch, "E8669", {"start": v(57.58, 12.4) * mm, "end": v(57.6, 12.38) * mm});
            skLineSegment(sketch, "E8670", {"start": v(57.6, 12.38) * mm, "end": v(57.63, 12.36) * mm});
            skLineSegment(sketch, "E8671", {"start": v(57.63, 12.36) * mm, "end": v(57.65, 12.34) * mm});
            skLineSegment(sketch, "E8672", {"start": v(57.65, 12.34) * mm, "end": v(57.67, 12.31) * mm});
            skLineSegment(sketch, "E8673", {"start": v(57.67, 12.31) * mm, "end": v(57.7, 12.29) * mm});
            skLineSegment(sketch, "E8674", {"start": v(57.7, 12.29) * mm, "end": v(57.71, 12.26) * mm});
            skLineSegment(sketch, "E8675", {"start": v(57.71, 12.26) * mm, "end": v(57.73, 12.23) * mm});
            skLineSegment(sketch, "E8676", {"start": v(57.73, 12.23) * mm, "end": v(57.74, 12.2) * mm});
            skLineSegment(sketch, "E8677", {"start": v(57.74, 12.2) * mm, "end": v(57.76, 12.17) * mm});
            skLineSegment(sketch, "E8678", {"start": v(57.76, 12.17) * mm, "end": v(57.77, 12.13) * mm});
            skLineSegment(sketch, "E8679", {"start": v(57.77, 12.13) * mm, "end": v(57.79, 12.1) * mm});
            skLineSegment(sketch, "E8680", {"start": v(57.79, 12.1) * mm, "end": v(57.8, 12.06) * mm});
            skLineSegment(sketch, "E8681", {"start": v(57.8, 12.06) * mm, "end": v(57.8, 12.02) * mm});
            skLineSegment(sketch, "E8682", {"start": v(57.8, 12.02) * mm, "end": v(57.82, 11.98) * mm});
            skLineSegment(sketch, "E8683", {"start": v(57.82, 11.98) * mm, "end": v(57.83, 11.94) * mm});
            skLineSegment(sketch, "E8684", {"start": v(57.83, 11.94) * mm, "end": v(57.83, 11.9) * mm});
            skLineSegment(sketch, "E8685", {"start": v(57.83, 11.9) * mm, "end": v(57.84, 11.85) * mm});
            skLineSegment(sketch, "E8686", {"start": v(57.84, 11.85) * mm, "end": v(57.84, 11.75) * mm});
            skLineSegment(sketch, "E8687", {"start": v(57.84, 11.75) * mm, "end": v(57.85, 11.65) * mm});
            skLineSegment(sketch, "E8688", {"start": v(57.85, 11.65) * mm, "end": v(57.84, 11.53) * mm});
            skLineSegment(sketch, "E8689", {"start": v(57.84, 11.53) * mm, "end": v(57.84, 11.4) * mm});
            skLineSegment(sketch, "E8690", {"start": v(57.84, 11.4) * mm, "end": v(57.8, 11.15) * mm});
            skLineSegment(sketch, "E8691", {"start": v(57.8, 11.15) * mm, "end": v(57.76, 10.89) * mm});
            skLineSegment(sketch, "E8692", {"start": v(57.76, 10.89) * mm, "end": v(57.7, 10.61) * mm});
            skLineSegment(sketch, "E8693", {"start": v(57.7, 10.61) * mm, "end": v(57.6, 10.33) * mm});
            skLineSegment(sketch, "E8694", {"start": v(57.6, 10.33) * mm, "end": v(57.5, 10.03) * mm});
            skLineSegment(sketch, "E8695", {"start": v(57.5, 10.03) * mm, "end": v(57.38, 9.72) * mm});
            skLineSegment(sketch, "E8696", {"start": v(57.38, 9.72) * mm, "end": v(57.24, 9.4) * mm});
            skLineSegment(sketch, "E8697", {"start": v(57.24, 9.4) * mm, "end": v(57.08, 9.07) * mm});
            skLineSegment(sketch, "E8698", {"start": v(57.08, 9.07) * mm, "end": v(56.9, 8.73) * mm});
            skLineSegment(sketch, "E8699", {"start": v(56.9, 8.73) * mm, "end": v(56.7, 8.38) * mm});
            skLineSegment(sketch, "E8700", {"start": v(56.7, 8.38) * mm, "end": v(56.48, 8.01) * mm});
            skLineSegment(sketch, "E8701", {"start": v(56.48, 8.01) * mm, "end": v(56.24, 7.64) * mm});
            skLineSegment(sketch, "E8702", {"start": v(56.24, 7.64) * mm, "end": v(55.99, 7.25) * mm});
            skLineSegment(sketch, "E8703", {"start": v(55.99, 7.25) * mm, "end": v(55.71, 6.86) * mm});
            skLineSegment(sketch, "E8704", {"start": v(55.71, 6.86) * mm, "end": v(55.1, 6.03) * mm});
            skLineSegment(sketch, "E8705", {"start": v(55.1, 6.03) * mm, "end": v(54.42, 5.16) * mm});
            skLineSegment(sketch, "E8706", {"start": v(54.42, 5.16) * mm, "end": v(53.66, 4.25) * mm});
            skLineSegment(sketch, "E8707", {"start": v(53.66, 4.25) * mm, "end": v(52.83, 3.29) * mm});
            skLineSegment(sketch, "E8708", {"start": v(52.83, 3.29) * mm, "end": v(51.92, 2.29) * mm});
            skLineSegment(sketch, "E8709", {"start": v(51.92, 2.29) * mm, "end": v(50.93, 1.24) * mm});
            skLineSegment(sketch, "E8710", {"start": v(50.93, 1.24) * mm, "end": v(49.87, 0.15) * mm});
            skLineSegment(sketch, "E8711", {"start": v(49.87, 0.15) * mm, "end": v(48.13, -1.57) * mm});
            skLineSegment(sketch, "E8712", {"start": v(48.13, -1.57) * mm, "end": v(48.13, -1.59) * mm});
            skLineSegment(sketch, "E8713", {"start": v(48.13, -1.59) * mm, "end": v(48.13, -1.6) * mm});
            skLineSegment(sketch, "E8714", {"start": v(48.13, -1.6) * mm, "end": v(48.13, -1.62) * mm});
            skLineSegment(sketch, "E8715", {"start": v(48.13, -1.62) * mm, "end": v(48.12, -1.64) * mm});
            skLineSegment(sketch, "E8716", {"start": v(48.12, -1.64) * mm, "end": v(48.12, -1.66) * mm});
            skLineSegment(sketch, "E8717", {"start": v(48.12, -1.66) * mm, "end": v(48.12, -1.68) * mm});
            skLineSegment(sketch, "E8718", {"start": v(48.12, -1.68) * mm, "end": v(48.12, -1.73) * mm});
            skLineSegment(sketch, "E8719", {"start": v(48.12, -1.73) * mm, "end": v(48.12, -1.78) * mm});
            skLineSegment(sketch, "E8720", {"start": v(48.12, -1.78) * mm, "end": v(48.11, -1.84) * mm});
            skLineSegment(sketch, "E8721", {"start": v(48.11, -1.84) * mm, "end": v(48.11, -1.9) * mm});
            skLineSegment(sketch, "E8722", {"start": v(48.11, -1.9) * mm, "end": v(48.1, -1.96) * mm});
            skLineSegment(sketch, "E8723", {"start": v(48.1, -1.96) * mm, "end": v(48.1, -2.02) * mm});
            skLineSegment(sketch, "E8724", {"start": v(48.1, -2.02) * mm, "end": v(48.1, -2.1) * mm});
            skLineSegment(sketch, "E8725", {"start": v(48.1, -2.1) * mm, "end": v(48.1, -2.17) * mm});
            skLineSegment(sketch, "E8726", {"start": v(48.1, -2.17) * mm, "end": v(48.1, -2.24) * mm});
            skLineSegment(sketch, "E8727", {"start": v(48.1, -2.24) * mm, "end": v(48.1, -2.33) * mm});
            skLineSegment(sketch, "E8728", {"start": v(48.1, -2.33) * mm, "end": v(48.1, -2.41) * mm});
            skLineSegment(sketch, "E8729", {"start": v(48.1, -2.41) * mm, "end": v(48.1, -2.6) * mm});
            skLineSegment(sketch, "E8730", {"start": v(48.1, -2.6) * mm, "end": v(48.1, -2.84) * mm});
            skLineSegment(sketch, "E8731", {"start": v(48.1, -2.84) * mm, "end": v(48.12, -3.06) * mm});
            skLineSegment(sketch, "E8732", {"start": v(48.12, -3.06) * mm, "end": v(48.14, -3.27) * mm});
            skLineSegment(sketch, "E8733", {"start": v(48.14, -3.27) * mm, "end": v(48.15, -3.37) * mm});
            skLineSegment(sketch, "E8734", {"start": v(48.15, -3.37) * mm, "end": v(48.17, -3.47) * mm});
            skLineSegment(sketch, "E8735", {"start": v(48.17, -3.47) * mm, "end": v(48.19, -3.56) * mm});
            skLineSegment(sketch, "E8736", {"start": v(48.19, -3.56) * mm, "end": v(48.2, -3.65) * mm});
            skLineSegment(sketch, "E8737", {"start": v(48.2, -3.65) * mm, "end": v(48.23, -3.73) * mm});
            skLineSegment(sketch, "E8738", {"start": v(48.23, -3.73) * mm, "end": v(48.25, -3.81) * mm});
            skLineSegment(sketch, "E8739", {"start": v(48.25, -3.81) * mm, "end": v(48.28, -3.89) * mm});
            skLineSegment(sketch, "E8740", {"start": v(48.28, -3.89) * mm, "end": v(48.3, -3.96) * mm});
            skLineSegment(sketch, "E8741", {"start": v(48.3, -3.96) * mm, "end": v(48.34, -4.03) * mm});
            skLineSegment(sketch, "E8742", {"start": v(48.34, -4.03) * mm, "end": v(48.37, -4.1) * mm});
            skLineSegment(sketch, "E8743", {"start": v(48.37, -4.1) * mm, "end": v(48.4, -4.15) * mm});
            skLineSegment(sketch, "E8744", {"start": v(48.4, -4.15) * mm, "end": v(48.44, -4.2) * mm});
            skLineSegment(sketch, "E8745", {"start": v(48.44, -4.2) * mm, "end": v(48.48, -4.26) * mm});
            skLineSegment(sketch, "E8746", {"start": v(48.48, -4.26) * mm, "end": v(48.52, -4.31) * mm});
            skLineSegment(sketch, "E8747", {"start": v(48.52, -4.31) * mm, "end": v(48.56, -4.36) * mm});
            skLineSegment(sketch, "E8748", {"start": v(48.56, -4.36) * mm, "end": v(48.6, -4.4) * mm});
            skLineSegment(sketch, "E8749", {"start": v(48.6, -4.4) * mm, "end": v(48.65, -4.43) * mm});
            skLineSegment(sketch, "E8750", {"start": v(48.65, -4.43) * mm, "end": v(48.7, -4.47) * mm});
            skLineSegment(sketch, "E8751", {"start": v(48.7, -4.47) * mm, "end": v(48.75, -4.5) * mm});
            skLineSegment(sketch, "E8752", {"start": v(48.75, -4.5) * mm, "end": v(48.8, -4.52) * mm});
            skLineSegment(sketch, "E8753", {"start": v(48.8, -4.52) * mm, "end": v(48.86, -4.54) * mm});
            skLineSegment(sketch, "E8754", {"start": v(48.86, -4.54) * mm, "end": v(48.92, -4.56) * mm});
            skLineSegment(sketch, "E8755", {"start": v(48.92, -4.56) * mm, "end": v(48.98, -4.57) * mm});
            skLineSegment(sketch, "E8756", {"start": v(48.98, -4.57) * mm, "end": v(49.04, -4.58) * mm});
            skLineSegment(sketch, "E8757", {"start": v(49.04, -4.58) * mm, "end": v(49.1, -4.59) * mm});
            skLineSegment(sketch, "E8758", {"start": v(49.1, -4.59) * mm, "end": v(49.17, -4.6) * mm});
            skLineSegment(sketch, "E8759", {"start": v(49.17, -4.6) * mm, "end": v(49.22, -4.59) * mm});
            skLineSegment(sketch, "E8760", {"start": v(49.22, -4.59) * mm, "end": v(49.28, -4.59) * mm});
            skLineSegment(sketch, "E8761", {"start": v(49.28, -4.59) * mm, "end": v(49.33, -4.58) * mm});
            skLineSegment(sketch, "E8762", {"start": v(49.33, -4.58) * mm, "end": v(49.38, -4.57) * mm});
            skLineSegment(sketch, "E8763", {"start": v(49.38, -4.57) * mm, "end": v(49.43, -4.56) * mm});
            skLineSegment(sketch, "E8764", {"start": v(49.43, -4.56) * mm, "end": v(49.49, -4.54) * mm});
            skLineSegment(sketch, "E8765", {"start": v(49.49, -4.54) * mm, "end": v(49.54, -4.53) * mm});
            skLineSegment(sketch, "E8766", {"start": v(49.54, -4.53) * mm, "end": v(49.6, -4.5) * mm});
            skLineSegment(sketch, "E8767", {"start": v(49.6, -4.5) * mm, "end": v(49.64, -4.49) * mm});
            skLineSegment(sketch, "E8768", {"start": v(49.64, -4.49) * mm, "end": v(49.7, -4.46) * mm});
            skLineSegment(sketch, "E8769", {"start": v(49.7, -4.46) * mm, "end": v(49.8, -4.4) * mm});
            skLineSegment(sketch, "E8770", {"start": v(49.8, -4.4) * mm, "end": v(49.9, -4.34) * mm});
            skLineSegment(sketch, "E8771", {"start": v(49.9, -4.34) * mm, "end": v(50.01, -4.26) * mm});
            skLineSegment(sketch, "E8772", {"start": v(50.01, -4.26) * mm, "end": v(50.07, -4.21) * mm});
            skLineSegment(sketch, "E8773", {"start": v(50.07, -4.21) * mm, "end": v(50.13, -4.16) * mm});
            skLineSegment(sketch, "E8774", {"start": v(50.13, -4.16) * mm, "end": v(50.19, -4.1) * mm});
            skLineSegment(sketch, "E8775", {"start": v(50.19, -4.1) * mm, "end": v(50.26, -4.05) * mm});
            skLineSegment(sketch, "E8776", {"start": v(50.26, -4.05) * mm, "end": v(50.33, -3.98) * mm});
            skLineSegment(sketch, "E8777", {"start": v(50.33, -3.98) * mm, "end": v(50.4, -3.91) * mm});
            skLineSegment(sketch, "E8778", {"start": v(50.4, -3.91) * mm, "end": v(50.48, -3.84) * mm});
            skLineSegment(sketch, "E8779", {"start": v(50.48, -3.84) * mm, "end": v(50.56, -3.76) * mm});
            skLineSegment(sketch, "E8780", {"start": v(50.56, -3.76) * mm, "end": v(50.64, -3.68) * mm});
            skLineSegment(sketch, "E8781", {"start": v(50.64, -3.68) * mm, "end": v(50.73, -3.59) * mm});
            skLineSegment(sketch, "E8782", {"start": v(50.73, -3.59) * mm, "end": v(50.82, -3.5) * mm});
            skLineSegment(sketch, "E8783", {"start": v(50.82, -3.5) * mm, "end": v(51.01, -3.3) * mm});
            skLineSegment(sketch, "E8784", {"start": v(51.01, -3.3) * mm, "end": v(51.22, -3.07) * mm});
            skLineSegment(sketch, "E8785", {"start": v(51.22, -3.07) * mm, "end": v(51.33, -2.96) * mm});
            skLineSegment(sketch, "E8786", {"start": v(51.33, -2.96) * mm, "end": v(51.24, -2.77) * mm});
            skLineSegment(sketch, "E8787", {"start": v(51.24, -2.77) * mm, "end": v(51.2, -2.68) * mm});
            skLineSegment(sketch, "E8788", {"start": v(51.2, -2.68) * mm, "end": v(51.17, -2.6) * mm});
            skLineSegment(sketch, "E8789", {"start": v(51.17, -2.6) * mm, "end": v(51.14, -2.5) * mm});
            skLineSegment(sketch, "E8790", {"start": v(51.14, -2.5) * mm, "end": v(51.11, -2.43) * mm});
            skLineSegment(sketch, "E8791", {"start": v(51.11, -2.43) * mm, "end": v(51.09, -2.35) * mm});
            skLineSegment(sketch, "E8792", {"start": v(51.09, -2.35) * mm, "end": v(51.07, -2.28) * mm});
            skLineSegment(sketch, "E8793", {"start": v(51.07, -2.28) * mm, "end": v(51.05, -2.2) * mm});
            skLineSegment(sketch, "E8794", {"start": v(51.05, -2.2) * mm, "end": v(51.03, -2.14) * mm});
            skLineSegment(sketch, "E8795", {"start": v(51.03, -2.14) * mm, "end": v(51.01, -2.07) * mm});
            skLineSegment(sketch, "E8796", {"start": v(51.01, -2.07) * mm, "end": v(51, -2.01) * mm});
            skLineSegment(sketch, "E8797", {"start": v(51, -2.01) * mm, "end": v(51, -1.96) * mm});
            skLineSegment(sketch, "E8798", {"start": v(51, -1.96) * mm, "end": v(50.98, -1.9) * mm});
            skLineSegment(sketch, "E8799", {"start": v(50.98, -1.9) * mm, "end": v(50.98, -1.85) * mm});
            skLineSegment(sketch, "E8800", {"start": v(50.98, -1.85) * mm, "end": v(50.98, -1.8) * mm});
            skLineSegment(sketch, "E8801", {"start": v(50.98, -1.8) * mm, "end": v(50.98, -1.7) * mm});
            skLineSegment(sketch, "E8802", {"start": v(50.98, -1.7) * mm, "end": v(50.99, -1.6) * mm});
            skLineSegment(sketch, "E8803", {"start": v(50.99, -1.6) * mm, "end": v(51, -1.5) * mm});
            skLineSegment(sketch, "E8804", {"start": v(51, -1.5) * mm, "end": v(51.02, -1.4) * mm});
            skLineSegment(sketch, "E8805", {"start": v(51.02, -1.4) * mm, "end": v(51.04, -1.3) * mm});
            skLineSegment(sketch, "E8806", {"start": v(51.04, -1.3) * mm, "end": v(51.07, -1.19) * mm});
            skLineSegment(sketch, "E8807", {"start": v(51.07, -1.19) * mm, "end": v(51.1, -1.08) * mm});
            skLineSegment(sketch, "E8808", {"start": v(51.1, -1.08) * mm, "end": v(51.14, -0.97) * mm});
            skLineSegment(sketch, "E8809", {"start": v(51.14, -0.97) * mm, "end": v(51.18, -0.86) * mm});
            skLineSegment(sketch, "E8810", {"start": v(51.18, -0.86) * mm, "end": v(51.29, -0.65) * mm});
            skLineSegment(sketch, "E8811", {"start": v(51.29, -0.65) * mm, "end": v(51.4, -0.42) * mm});
            skLineSegment(sketch, "E8812", {"start": v(51.4, -0.42) * mm, "end": v(51.55, -0.2) * mm});
            skLineSegment(sketch, "E8813", {"start": v(51.55, -0.2) * mm, "end": v(51.63, -0.08) * mm});
            skLineSegment(sketch, "E8814", {"start": v(51.63, -0.08) * mm, "end": v(51.97, 0.37) * mm});
            skLineSegment(sketch, "E8815", {"start": v(51.97, 0.37) * mm, "end": v(52.32, 0.78) * mm});
            skLineSegment(sketch, "E8816", {"start": v(52.32, 0.78) * mm, "end": v(52.7, 1.16) * mm});
            skLineSegment(sketch, "E8817", {"start": v(52.7, 1.16) * mm, "end": v(53.1, 1.51) * mm});
            skLineSegment(sketch, "E8818", {"start": v(53.1, 1.51) * mm, "end": v(53.2, 1.6) * mm});
            skLineSegment(sketch, "E8819", {"start": v(53.2, 1.6) * mm, "end": v(53.3, 1.67) * mm});
            skLineSegment(sketch, "E8820", {"start": v(53.3, 1.67) * mm, "end": v(53.4, 1.74) * mm});
            skLineSegment(sketch, "E8821", {"start": v(53.4, 1.74) * mm, "end": v(53.5, 1.8) * mm});
            skLineSegment(sketch, "E8822", {"start": v(53.5, 1.8) * mm, "end": v(53.58, 1.87) * mm});
            skLineSegment(sketch, "E8823", {"start": v(53.58, 1.87) * mm, "end": v(53.67, 1.93) * mm});
            skLineSegment(sketch, "E8824", {"start": v(53.67, 1.93) * mm, "end": v(53.75, 1.98) * mm});
            skLineSegment(sketch, "E8825", {"start": v(53.75, 1.98) * mm, "end": v(53.83, 2.02) * mm});
            skLineSegment(sketch, "E8826", {"start": v(53.83, 2.02) * mm, "end": v(53.9, 2.06) * mm});
            skLineSegment(sketch, "E8827", {"start": v(53.9, 2.06) * mm, "end": v(53.97, 2.1) * mm});
            skLineSegment(sketch, "E8828", {"start": v(53.97, 2.1) * mm, "end": v(54, 2.11) * mm});
            skLineSegment(sketch, "E8829", {"start": v(54, 2.11) * mm, "end": v(54.04, 2.12) * mm});
            skLineSegment(sketch, "E8830", {"start": v(54.04, 2.12) * mm, "end": v(54.07, 2.14) * mm});
            skLineSegment(sketch, "E8831", {"start": v(54.07, 2.14) * mm, "end": v(54.1, 2.15) * mm});
            skLineSegment(sketch, "E8832", {"start": v(54.1, 2.15) * mm, "end": v(54.13, 2.16) * mm});
            skLineSegment(sketch, "E8833", {"start": v(54.13, 2.16) * mm, "end": v(54.16, 2.17) * mm});
            skLineSegment(sketch, "E8834", {"start": v(54.16, 2.17) * mm, "end": v(54.2, 2.17) * mm});
            skLineSegment(sketch, "E8835", {"start": v(54.2, 2.17) * mm, "end": v(54.22, 2.18) * mm});
            skLineSegment(sketch, "E8836", {"start": v(54.22, 2.18) * mm, "end": v(54.24, 2.18) * mm});
            skLineSegment(sketch, "E8837", {"start": v(54.24, 2.18) * mm, "end": v(54.27, 2.19) * mm});
            skLineSegment(sketch, "E8838", {"start": v(54.27, 2.19) * mm, "end": v(54.3, 2.19) * mm});
            skLineSegment(sketch, "E8839", {"start": v(54.3, 2.19) * mm, "end": v(54.32, 2.2) * mm});
            skLineSegment(sketch, "E8840", {"start": v(54.32, 2.2) * mm, "end": v(54.36, 2.19) * mm});
            skLineSegment(sketch, "E8841", {"start": v(54.36, 2.19) * mm, "end": v(54.4, 2.19) * mm});
            skLineSegment(sketch, "E8842", {"start": v(54.4, 2.19) * mm, "end": v(54.42, 2.18) * mm});
            skLineSegment(sketch, "E8843", {"start": v(54.42, 2.18) * mm, "end": v(54.46, 2.18) * mm});
            skLineSegment(sketch, "E8844", {"start": v(54.46, 2.18) * mm, "end": v(54.49, 2.17) * mm});
            skLineSegment(sketch, "E8845", {"start": v(54.49, 2.17) * mm, "end": v(54.52, 2.16) * mm});
            skLineSegment(sketch, "E8846", {"start": v(54.52, 2.16) * mm, "end": v(54.55, 2.15) * mm});
            skLineSegment(sketch, "E8847", {"start": v(54.55, 2.15) * mm, "end": v(54.58, 2.14) * mm});
            skLineSegment(sketch, "E8848", {"start": v(54.58, 2.14) * mm, "end": v(54.6, 2.12) * mm});
            skLineSegment(sketch, "E8849", {"start": v(54.6, 2.12) * mm, "end": v(54.63, 2.1) * mm});
            skLineSegment(sketch, "E8850", {"start": v(54.63, 2.1) * mm, "end": v(54.66, 2.09) * mm});
            skLineSegment(sketch, "E8851", {"start": v(54.66, 2.09) * mm, "end": v(54.68, 2.07) * mm});
            skLineSegment(sketch, "E8852", {"start": v(54.68, 2.07) * mm, "end": v(54.7, 2.05) * mm});
            skLineSegment(sketch, "E8853", {"start": v(54.7, 2.05) * mm, "end": v(54.72, 2.03) * mm});
            skLineSegment(sketch, "E8854", {"start": v(54.72, 2.03) * mm, "end": v(54.74, 2) * mm});
            skLineSegment(sketch, "E8855", {"start": v(54.74, 2) * mm, "end": v(54.76, 1.98) * mm});
            skLineSegment(sketch, "E8856", {"start": v(54.76, 1.98) * mm, "end": v(54.78, 1.95) * mm});
            skLineSegment(sketch, "E8857", {"start": v(54.78, 1.95) * mm, "end": v(54.8, 1.92) * mm});
            skLineSegment(sketch, "E8858", {"start": v(54.8, 1.92) * mm, "end": v(54.81, 1.89) * mm});
            skLineSegment(sketch, "E8859", {"start": v(54.81, 1.89) * mm, "end": v(54.83, 1.86) * mm});
            skLineSegment(sketch, "E8860", {"start": v(54.83, 1.86) * mm, "end": v(54.84, 1.82) * mm});
            skLineSegment(sketch, "E8861", {"start": v(54.84, 1.82) * mm, "end": v(54.85, 1.79) * mm});
            skLineSegment(sketch, "E8862", {"start": v(54.85, 1.79) * mm, "end": v(54.86, 1.75) * mm});
            skLineSegment(sketch, "E8863", {"start": v(54.86, 1.75) * mm, "end": v(54.87, 1.71) * mm});
            skLineSegment(sketch, "E8864", {"start": v(54.87, 1.71) * mm, "end": v(54.88, 1.67) * mm});
            skLineSegment(sketch, "E8865", {"start": v(54.88, 1.67) * mm, "end": v(54.9, 1.63) * mm});
            skLineSegment(sketch, "E8866", {"start": v(54.9, 1.63) * mm, "end": v(54.9, 1.58) * mm});
            skLineSegment(sketch, "E8867", {"start": v(54.9, 1.58) * mm, "end": v(54.9, 1.49) * mm});
            skLineSegment(sketch, "E8868", {"start": v(54.9, 1.49) * mm, "end": v(54.91, 1.39) * mm});
            skLineSegment(sketch, "E8869", {"start": v(54.91, 1.39) * mm, "end": v(54.91, 1.34) * mm});
            skLineSegment(sketch, "E8870", {"start": v(54.91, 1.34) * mm, "end": v(54.9, 1.17) * mm});
            skLineSegment(sketch, "E8871", {"start": v(54.9, 1.17) * mm, "end": v(54.9, 1) * mm});
            skLineSegment(sketch, "E8872", {"start": v(54.9, 1) * mm, "end": v(54.86, 0.81) * mm});
            skLineSegment(sketch, "E8873", {"start": v(54.86, 0.81) * mm, "end": v(54.83, 0.62) * mm});
            skLineSegment(sketch, "E8874", {"start": v(54.83, 0.62) * mm, "end": v(54.78, 0.42) * mm});
            skLineSegment(sketch, "E8875", {"start": v(54.78, 0.42) * mm, "end": v(54.72, 0.21) * mm});
            skLineSegment(sketch, "E8876", {"start": v(54.72, 0.21) * mm, "end": v(54.65, 0) * mm});
            skLineSegment(sketch, "E8877", {"start": v(54.65, 0) * mm, "end": v(54.56, -0.22) * mm});
            skLineSegment(sketch, "E8878", {"start": v(54.56, -0.22) * mm, "end": v(54.48, -0.46) * mm});
            skLineSegment(sketch, "E8879", {"start": v(54.48, -0.46) * mm, "end": v(54.38, -0.7) * mm});
            skLineSegment(sketch, "E8880", {"start": v(54.38, -0.7) * mm, "end": v(54.27, -0.94) * mm});
            skLineSegment(sketch, "E8881", {"start": v(54.27, -0.94) * mm, "end": v(54.15, -1.2) * mm});
            skLineSegment(sketch, "E8882", {"start": v(54.15, -1.2) * mm, "end": v(53.89, -1.74) * mm});
            skLineSegment(sketch, "E8883", {"start": v(53.89, -1.74) * mm, "end": v(53.58, -2.3) * mm});
            skLineSegment(sketch, "E8884", {"start": v(53.58, -2.3) * mm, "end": v(53.64, -2.36) * mm});
            skLineSegment(sketch, "E8885", {"start": v(53.64, -2.36) * mm, "end": v(53.7, -2.4) * mm});
            skLineSegment(sketch, "E8886", {"start": v(53.7, -2.4) * mm, "end": v(53.75, -2.44) * mm});
            skLineSegment(sketch, "E8887", {"start": v(53.75, -2.44) * mm, "end": v(53.8, -2.48) * mm});
            skLineSegment(sketch, "E8888", {"start": v(53.8, -2.48) * mm, "end": v(53.85, -2.52) * mm});
            skLineSegment(sketch, "E8889", {"start": v(53.85, -2.52) * mm, "end": v(53.9, -2.55) * mm});
            skLineSegment(sketch, "E8890", {"start": v(53.9, -2.55) * mm, "end": v(53.91, -2.57) * mm});
            skLineSegment(sketch, "E8891", {"start": v(53.91, -2.57) * mm, "end": v(53.93, -2.58) * mm});
            skLineSegment(sketch, "E8892", {"start": v(53.93, -2.58) * mm, "end": v(53.95, -2.6) * mm});
            skLineSegment(sketch, "E8893", {"start": v(53.95, -2.6) * mm, "end": v(53.97, -2.6) * mm});
            skLineSegment(sketch, "E8894", {"start": v(53.97, -2.6) * mm, "end": v(54, -2.62) * mm});
            skLineSegment(sketch, "E8895", {"start": v(54, -2.62) * mm, "end": v(54.01, -2.63) * mm});
            skLineSegment(sketch, "E8896", {"start": v(54.01, -2.63) * mm, "end": v(54.03, -2.64) * mm});
            skLineSegment(sketch, "E8897", {"start": v(54.03, -2.64) * mm, "end": v(54.05, -2.65) * mm});
            skLineSegment(sketch, "E8898", {"start": v(54.05, -2.65) * mm, "end": v(54.08, -2.66) * mm});
            skLineSegment(sketch, "E8899", {"start": v(54.08, -2.66) * mm, "end": v(54.1, -2.66) * mm});
            skLineSegment(sketch, "E8900", {"start": v(54.1, -2.66) * mm, "end": v(54.13, -2.67) * mm});
            skLineSegment(sketch, "E8901", {"start": v(54.13, -2.67) * mm, "end": v(54.15, -2.67) * mm});
            skLineSegment(sketch, "E8902", {"start": v(54.15, -2.67) * mm, "end": v(54.18, -2.68) * mm});
            skLineSegment(sketch, "E8903", {"start": v(54.18, -2.68) * mm, "end": v(54.2, -2.68) * mm});
            skLineSegment(sketch, "E8904", {"start": v(54.2, -2.68) * mm, "end": v(54.27, -2.7) * mm});
            skLineSegment(sketch, "E8905", {"start": v(54.27, -2.7) * mm, "end": v(54.34, -2.7) * mm});
            skLineSegment(sketch, "E8906", {"start": v(54.34, -2.7) * mm, "end": v(54.4, -2.7) * mm});
            skLineSegment(sketch, "E8907", {"start": v(54.4, -2.7) * mm, "end": v(54.49, -2.7) * mm});
            skLineSegment(sketch, "E8908", {"start": v(54.49, -2.7) * mm, "end": v(54.58, -2.69) * mm});
            skLineSegment(sketch, "E8909", {"start": v(54.58, -2.69) * mm, "end": v(54.66, -2.68) * mm});
            skLineSegment(sketch, "E8910", {"start": v(54.66, -2.68) * mm, "end": v(54.75, -2.66) * mm});
            skLineSegment(sketch, "E8911", {"start": v(54.75, -2.66) * mm, "end": v(54.84, -2.64) * mm});
            skLineSegment(sketch, "E8912", {"start": v(54.84, -2.64) * mm, "end": v(54.94, -2.61) * mm});
            skLineSegment(sketch, "E8913", {"start": v(54.94, -2.61) * mm, "end": v(55.03, -2.58) * mm});
            skLineSegment(sketch, "E8914", {"start": v(55.03, -2.58) * mm, "end": v(55.13, -2.55) * mm});
            skLineSegment(sketch, "E8915", {"start": v(55.13, -2.55) * mm, "end": v(55.22, -2.5) * mm});
            skLineSegment(sketch, "E8916", {"start": v(55.22, -2.5) * mm, "end": v(55.32, -2.47) * mm});
            skLineSegment(sketch, "E8917", {"start": v(55.32, -2.47) * mm, "end": v(55.53, -2.36) * mm});
            skLineSegment(sketch, "E8918", {"start": v(55.53, -2.36) * mm, "end": v(55.74, -2.24) * mm});
            skLineSegment(sketch, "E8919", {"start": v(55.74, -2.24) * mm, "end": v(55.95, -2.1) * mm});
            skLineSegment(sketch, "E8920", {"start": v(48.6, 0.07) * mm, "end": v(48.98, 0.4) * mm});
            skLineSegment(sketch, "E8921", {"start": v(48.98, 0.4) * mm, "end": v(49.36, 0.77) * mm});
            skLineSegment(sketch, "E8922", {"start": v(49.36, 0.77) * mm, "end": v(49.74, 1.17) * mm});
            skLineSegment(sketch, "E8923", {"start": v(49.74, 1.17) * mm, "end": v(50.11, 1.6) * mm});
            skLineSegment(sketch, "E8924", {"start": v(50.11, 1.6) * mm, "end": v(50.2, 1.71) * mm});
            skLineSegment(sketch, "E8925", {"start": v(50.2, 1.71) * mm, "end": v(50.31, 1.84) * mm});
            skLineSegment(sketch, "E8926", {"start": v(50.31, 1.84) * mm, "end": v(50.42, 1.97) * mm});
            skLineSegment(sketch, "E8927", {"start": v(50.42, 1.97) * mm, "end": v(50.54, 2.1) * mm});
            skLineSegment(sketch, "E8928", {"start": v(50.54, 2.1) * mm, "end": v(50.66, 2.25) * mm});
            skLineSegment(sketch, "E8929", {"start": v(50.66, 2.25) * mm, "end": v(50.78, 2.4) * mm});
            skLineSegment(sketch, "E8930", {"start": v(50.78, 2.4) * mm, "end": v(51.05, 2.73) * mm});
            skLineSegment(sketch, "E8931", {"start": v(51.05, 2.73) * mm, "end": v(51.34, 3.09) * mm});
            skLineSegment(sketch, "E8932", {"start": v(51.34, 3.09) * mm, "end": v(51.65, 3.47) * mm});
            skLineSegment(sketch, "E8933", {"start": v(51.65, 3.47) * mm, "end": v(51.98, 3.89) * mm});
            skLineSegment(sketch, "E8934", {"start": v(51.98, 3.89) * mm, "end": v(52.34, 4.33) * mm});
            skLineSegment(sketch, "E8935", {"start": v(52.34, 4.33) * mm, "end": v(52.68, 4.76) * mm});
            skLineSegment(sketch, "E8936", {"start": v(52.68, 4.76) * mm, "end": v(53, 5.18) * mm});
            skLineSegment(sketch, "E8937", {"start": v(53, 5.18) * mm, "end": v(53.3, 5.57) * mm});
            skLineSegment(sketch, "E8938", {"start": v(53.3, 5.57) * mm, "end": v(53.59, 5.95) * mm});
            skLineSegment(sketch, "E8939", {"start": v(53.59, 5.95) * mm, "end": v(53.85, 6.3) * mm});
            skLineSegment(sketch, "E8940", {"start": v(53.85, 6.3) * mm, "end": v(54.1, 6.64) * mm});
            skLineSegment(sketch, "E8941", {"start": v(54.1, 6.64) * mm, "end": v(54.33, 6.96) * mm});
            skLineSegment(sketch, "E8942", {"start": v(54.33, 6.96) * mm, "end": v(54.54, 7.27) * mm});
            skLineSegment(sketch, "E8943", {"start": v(54.54, 7.27) * mm, "end": v(54.73, 7.56) * mm});
            skLineSegment(sketch, "E8944", {"start": v(54.73, 7.56) * mm, "end": v(54.92, 7.83) * mm});
            skLineSegment(sketch, "E8945", {"start": v(54.92, 7.83) * mm, "end": v(55.09, 8.1) * mm});
            skLineSegment(sketch, "E8946", {"start": v(55.09, 8.1) * mm, "end": v(55.24, 8.35) * mm});
            skLineSegment(sketch, "E8947", {"start": v(55.24, 8.35) * mm, "end": v(55.39, 8.59) * mm});
            skLineSegment(sketch, "E8948", {"start": v(55.39, 8.59) * mm, "end": v(55.52, 8.82) * mm});
            skLineSegment(sketch, "E8949", {"start": v(55.52, 8.82) * mm, "end": v(55.64, 9.03) * mm});
            skLineSegment(sketch, "E8950", {"start": v(55.64, 9.03) * mm, "end": v(55.75, 9.23) * mm});
            skLineSegment(sketch, "E8951", {"start": v(55.75, 9.23) * mm, "end": v(55.8, 9.33) * mm});
            skLineSegment(sketch, "E8952", {"start": v(55.8, 9.33) * mm, "end": v(55.85, 9.42) * mm});
            skLineSegment(sketch, "E8953", {"start": v(55.85, 9.42) * mm, "end": v(55.89, 9.5) * mm});
            skLineSegment(sketch, "E8954", {"start": v(55.89, 9.5) * mm, "end": v(55.93, 9.6) * mm});
            skLineSegment(sketch, "E8955", {"start": v(55.93, 9.6) * mm, "end": v(55.96, 9.67) * mm});
            skLineSegment(sketch, "E8956", {"start": v(55.96, 9.67) * mm, "end": v(56, 9.75) * mm});
            skLineSegment(sketch, "E8957", {"start": v(56, 9.75) * mm, "end": v(56.03, 9.82) * mm});
            skLineSegment(sketch, "E8958", {"start": v(56.03, 9.82) * mm, "end": v(56.05, 9.9) * mm});
            skLineSegment(sketch, "E8959", {"start": v(56.05, 9.9) * mm, "end": v(56.08, 9.95) * mm});
            skLineSegment(sketch, "E8960", {"start": v(56.08, 9.95) * mm, "end": v(56.1, 10.02) * mm});
            skLineSegment(sketch, "E8961", {"start": v(56.1, 10.02) * mm, "end": v(56.12, 10.07) * mm});
            skLineSegment(sketch, "E8962", {"start": v(56.12, 10.07) * mm, "end": v(56.12, 10.1) * mm});
            skLineSegment(sketch, "E8963", {"start": v(56.12, 10.1) * mm, "end": v(56.13, 10.13) * mm});
            skLineSegment(sketch, "E8964", {"start": v(56.13, 10.13) * mm, "end": v(56.14, 10.15) * mm});
            skLineSegment(sketch, "E8965", {"start": v(56.14, 10.15) * mm, "end": v(56.14, 10.18) * mm});
            skLineSegment(sketch, "E8966", {"start": v(56.14, 10.18) * mm, "end": v(56.15, 10.2) * mm});
            skLineSegment(sketch, "E8967", {"start": v(56.15, 10.2) * mm, "end": v(56.15, 10.22) * mm});
            skLineSegment(sketch, "E8968", {"start": v(56.15, 10.22) * mm, "end": v(56.15, 10.24) * mm});
            skLineSegment(sketch, "E8969", {"start": v(56.15, 10.24) * mm, "end": v(56.15, 10.26) * mm});
            skLineSegment(sketch, "E8970", {"start": v(56.15, 10.26) * mm, "end": v(56.15, 10.28) * mm});
            skLineSegment(sketch, "E8971", {"start": v(56.15, 10.28) * mm, "end": v(56.16, 10.3) * mm});
            skLineSegment(sketch, "E8972", {"start": v(56.16, 10.3) * mm, "end": v(56.15, 10.33) * mm});
            skLineSegment(sketch, "E8973", {"start": v(56.15, 10.33) * mm, "end": v(56.15, 10.35) * mm});
            skLineSegment(sketch, "E8974", {"start": v(56.15, 10.35) * mm, "end": v(56.15, 10.38) * mm});
            skLineSegment(sketch, "E8975", {"start": v(56.15, 10.38) * mm, "end": v(56.15, 10.39) * mm});
            skLineSegment(sketch, "E8976", {"start": v(56.15, 10.39) * mm, "end": v(56.15, 10.4) * mm});
            skLineSegment(sketch, "E8977", {"start": v(56.15, 10.4) * mm, "end": v(56.15, 10.4) * mm});
            skLineSegment(sketch, "E8978", {"start": v(56.15, 10.4) * mm, "end": v(56.14, 10.42) * mm});
            skLineSegment(sketch, "E8979", {"start": v(56.14, 10.42) * mm, "end": v(56.14, 10.43) * mm});
            skLineSegment(sketch, "E8980", {"start": v(56.14, 10.43) * mm, "end": v(56.14, 10.43) * mm});
            skLineSegment(sketch, "E8981", {"start": v(56.14, 10.43) * mm, "end": v(56.14, 10.44) * mm});
            skLineSegment(sketch, "E8982", {"start": v(56.14, 10.44) * mm, "end": v(56.13, 10.45) * mm});
            skLineSegment(sketch, "E8983", {"start": v(56.13, 10.45) * mm, "end": v(56.13, 10.46) * mm});
            skLineSegment(sketch, "E8984", {"start": v(56.13, 10.46) * mm, "end": v(56.13, 10.46) * mm});
            skLineSegment(sketch, "E8985", {"start": v(56.13, 10.46) * mm, "end": v(56.12, 10.47) * mm});
            skLineSegment(sketch, "E8986", {"start": v(56.12, 10.47) * mm, "end": v(56.12, 10.48) * mm});
            skLineSegment(sketch, "E8987", {"start": v(56.12, 10.48) * mm, "end": v(56.11, 10.48) * mm});
            skLineSegment(sketch, "E8988", {"start": v(56.11, 10.48) * mm, "end": v(56.11, 10.49) * mm});
            skLineSegment(sketch, "E8989", {"start": v(56.11, 10.49) * mm, "end": v(56.1, 10.5) * mm});
            skLineSegment(sketch, "E8990", {"start": v(56.1, 10.5) * mm, "end": v(56.1, 10.5) * mm});
            skLineSegment(sketch, "E8991", {"start": v(56.1, 10.5) * mm, "end": v(56.08, 10.5) * mm});
            skLineSegment(sketch, "E8992", {"start": v(56.08, 10.5) * mm, "end": v(56.08, 10.51) * mm});
            skLineSegment(sketch, "E8993", {"start": v(56.08, 10.51) * mm, "end": v(56.07, 10.51) * mm});
            skLineSegment(sketch, "E8994", {"start": v(56.07, 10.51) * mm, "end": v(56.07, 10.52) * mm});
            skLineSegment(sketch, "E8995", {"start": v(56.07, 10.52) * mm, "end": v(56.06, 10.52) * mm});
            skLineSegment(sketch, "E8996", {"start": v(56.06, 10.52) * mm, "end": v(56.05, 10.52) * mm});
            skLineSegment(sketch, "E8997", {"start": v(56.05, 10.52) * mm, "end": v(56.05, 10.52) * mm});
            skLineSegment(sketch, "E8998", {"start": v(56.05, 10.52) * mm, "end": v(56.04, 10.52) * mm});
            skLineSegment(sketch, "E8999", {"start": v(56.04, 10.52) * mm, "end": v(56.03, 10.52) * mm});
            skLineSegment(sketch, "E9000", {"start": v(56.03, 10.52) * mm, "end": v(56.02, 10.52) * mm});
            skLineSegment(sketch, "E9001", {"start": v(56.02, 10.52) * mm, "end": v(56, 10.52) * mm});
            skLineSegment(sketch, "E9002", {"start": v(56, 10.52) * mm, "end": v(56, 10.51) * mm});
            skLineSegment(sketch, "E9003", {"start": v(56, 10.51) * mm, "end": v(55.99, 10.51) * mm});
            skLineSegment(sketch, "E9004", {"start": v(55.99, 10.51) * mm, "end": v(55.97, 10.5) * mm});
            skLineSegment(sketch, "E9005", {"start": v(55.97, 10.5) * mm, "end": v(55.96, 10.5) * mm});
            skLineSegment(sketch, "E9006", {"start": v(55.96, 10.5) * mm, "end": v(55.95, 10.5) * mm});
            skLineSegment(sketch, "E9007", {"start": v(55.95, 10.5) * mm, "end": v(55.94, 10.5) * mm});
            skLineSegment(sketch, "E9008", {"start": v(55.94, 10.5) * mm, "end": v(55.9, 10.49) * mm});
            skLineSegment(sketch, "E9009", {"start": v(55.9, 10.49) * mm, "end": v(55.88, 10.48) * mm});
            skLineSegment(sketch, "E9010", {"start": v(55.88, 10.48) * mm, "end": v(55.85, 10.46) * mm});
            skLineSegment(sketch, "E9011", {"start": v(55.85, 10.46) * mm, "end": v(55.82, 10.44) * mm});
            skLineSegment(sketch, "E9012", {"start": v(55.82, 10.44) * mm, "end": v(55.79, 10.43) * mm});
            skLineSegment(sketch, "E9013", {"start": v(55.79, 10.43) * mm, "end": v(55.76, 10.4) * mm});
            skLineSegment(sketch, "E9014", {"start": v(55.76, 10.4) * mm, "end": v(55.72, 10.38) * mm});
            skLineSegment(sketch, "E9015", {"start": v(55.72, 10.38) * mm, "end": v(55.69, 10.36) * mm});
            skLineSegment(sketch, "E9016", {"start": v(55.69, 10.36) * mm, "end": v(55.65, 10.33) * mm});
            skLineSegment(sketch, "E9017", {"start": v(55.65, 10.33) * mm, "end": v(55.6, 10.3) * mm});
            skLineSegment(sketch, "E9018", {"start": v(55.6, 10.3) * mm, "end": v(55.57, 10.27) * mm});
            skLineSegment(sketch, "E9019", {"start": v(55.57, 10.27) * mm, "end": v(55.53, 10.24) * mm});
            skLineSegment(sketch, "E9020", {"start": v(55.53, 10.24) * mm, "end": v(55.44, 10.17) * mm});
            skLineSegment(sketch, "E9021", {"start": v(55.44, 10.17) * mm, "end": v(55.35, 10.09) * mm});
            skLineSegment(sketch, "E9022", {"start": v(55.35, 10.09) * mm, "end": v(55.25, 10) * mm});
            skLineSegment(sketch, "E9023", {"start": v(55.25, 10) * mm, "end": v(55.15, 9.9) * mm});
            skLineSegment(sketch, "E9024", {"start": v(55.15, 9.9) * mm, "end": v(55.04, 9.8) * mm});
            skLineSegment(sketch, "E9025", {"start": v(55.04, 9.8) * mm, "end": v(54.92, 9.68) * mm});
            skLineSegment(sketch, "E9026", {"start": v(54.92, 9.68) * mm, "end": v(54.8, 9.56) * mm});
            skLineSegment(sketch, "E9027", {"start": v(54.8, 9.56) * mm, "end": v(54.7, 9.46) * mm});
            skLineSegment(sketch, "E9028", {"start": v(54.7, 9.46) * mm, "end": v(54.46, 9.2) * mm});
            skLineSegment(sketch, "E9029", {"start": v(54.46, 9.2) * mm, "end": v(54.2, 8.9) * mm});
            skLineSegment(sketch, "E9030", {"start": v(54.2, 8.9) * mm, "end": v(53.92, 8.57) * mm});
            skLineSegment(sketch, "E9031", {"start": v(53.92, 8.57) * mm, "end": v(53.64, 8.23) * mm});
            skLineSegment(sketch, "E9032", {"start": v(53.64, 8.23) * mm, "end": v(53.35, 7.86) * mm});
            skLineSegment(sketch, "E9033", {"start": v(53.35, 7.86) * mm, "end": v(53.05, 7.46) * mm});
            skLineSegment(sketch, "E9034", {"start": v(53.05, 7.46) * mm, "end": v(52.74, 7.04) * mm});
            skLineSegment(sketch, "E9035", {"start": v(52.74, 7.04) * mm, "end": v(52.42, 6.6) * mm});
            skLineSegment(sketch, "E9036", {"start": v(52.42, 6.6) * mm, "end": v(52, 6) * mm});
            skLineSegment(sketch, "E9037", {"start": v(52, 6) * mm, "end": v(51.6, 5.42) * mm});
            skLineSegment(sketch, "E9038", {"start": v(51.6, 5.42) * mm, "end": v(51.23, 4.89) * mm});
            skLineSegment(sketch, "E9039", {"start": v(51.23, 4.89) * mm, "end": v(50.9, 4.4) * mm});
            skLineSegment(sketch, "E9040", {"start": v(50.9, 4.4) * mm, "end": v(50.74, 4.16) * mm});
            skLineSegment(sketch, "E9041", {"start": v(50.74, 4.16) * mm, "end": v(50.59, 3.94) * mm});
            skLineSegment(sketch, "E9042", {"start": v(50.59, 3.94) * mm, "end": v(50.44, 3.73) * mm});
            skLineSegment(sketch, "E9043", {"start": v(50.44, 3.73) * mm, "end": v(50.31, 3.53) * mm});
            skLineSegment(sketch, "E9044", {"start": v(50.31, 3.53) * mm, "end": v(50.18, 3.33) * mm});
            skLineSegment(sketch, "E9045", {"start": v(50.18, 3.33) * mm, "end": v(50.07, 3.15) * mm});
            skLineSegment(sketch, "E9046", {"start": v(50.07, 3.15) * mm, "end": v(49.95, 2.98) * mm});
            skLineSegment(sketch, "E9047", {"start": v(49.95, 2.98) * mm, "end": v(49.85, 2.81) * mm});
            skLineSegment(sketch, "E9048", {"start": v(49.85, 2.81) * mm, "end": v(49.48, 2.16) * mm});
            skLineSegment(sketch, "E9049", {"start": v(49.48, 2.16) * mm, "end": v(49.14, 1.49) * mm});
            skLineSegment(sketch, "E9050", {"start": v(49.14, 1.49) * mm, "end": v(48.85, 0.79) * mm});
            skLineSegment(sketch, "E9051", {"start": v(48.85, 0.79) * mm, "end": v(48.6, 0.07) * mm});
            skLineSegment(sketch, "E9052", {"start": v(61.85, -2.6) * mm, "end": v(61.85, -2.96) * mm});
            skLineSegment(sketch, "E9053", {"start": v(61.85, -2.96) * mm, "end": v(61.86, -3.16) * mm});
            skLineSegment(sketch, "E9054", {"start": v(61.86, -3.16) * mm, "end": v(61.87, -3.26) * mm});
            skLineSegment(sketch, "E9055", {"start": v(61.87, -3.26) * mm, "end": v(61.88, -3.36) * mm});
            skLineSegment(sketch, "E9056", {"start": v(61.88, -3.36) * mm, "end": v(61.9, -3.45) * mm});
            skLineSegment(sketch, "E9057", {"start": v(61.9, -3.45) * mm, "end": v(61.91, -3.54) * mm});
            skLineSegment(sketch, "E9058", {"start": v(61.91, -3.54) * mm, "end": v(61.93, -3.63) * mm});
            skLineSegment(sketch, "E9059", {"start": v(61.93, -3.63) * mm, "end": v(61.96, -3.72) * mm});
            skLineSegment(sketch, "E9060", {"start": v(61.96, -3.72) * mm, "end": v(61.98, -3.8) * mm});
            skLineSegment(sketch, "E9061", {"start": v(61.98, -3.8) * mm, "end": v(62.02, -3.88) * mm});
            skLineSegment(sketch, "E9062", {"start": v(62.02, -3.88) * mm, "end": v(62.05, -3.95) * mm});
            skLineSegment(sketch, "E9063", {"start": v(62.05, -3.95) * mm, "end": v(62.09, -4.03) * mm});
            skLineSegment(sketch, "E9064", {"start": v(62.09, -4.03) * mm, "end": v(62.13, -4.1) * mm});
            skLineSegment(sketch, "E9065", {"start": v(62.13, -4.1) * mm, "end": v(62.17, -4.16) * mm});
            skLineSegment(sketch, "E9066", {"start": v(62.17, -4.16) * mm, "end": v(62.22, -4.23) * mm});
            skLineSegment(sketch, "E9067", {"start": v(62.22, -4.23) * mm, "end": v(62.27, -4.29) * mm});
            skLineSegment(sketch, "E9068", {"start": v(62.27, -4.29) * mm, "end": v(62.32, -4.34) * mm});
            skLineSegment(sketch, "E9069", {"start": v(62.32, -4.34) * mm, "end": v(62.38, -4.4) * mm});
            skLineSegment(sketch, "E9070", {"start": v(62.38, -4.4) * mm, "end": v(62.44, -4.45) * mm});
            skLineSegment(sketch, "E9071", {"start": v(62.44, -4.45) * mm, "end": v(62.5, -4.5) * mm});
            skLineSegment(sketch, "E9072", {"start": v(62.5, -4.5) * mm, "end": v(62.56, -4.54) * mm});
            skLineSegment(sketch, "E9073", {"start": v(62.56, -4.54) * mm, "end": v(62.62, -4.58) * mm});
            skLineSegment(sketch, "E9074", {"start": v(62.62, -4.58) * mm, "end": v(62.69, -4.61) * mm});
            skLineSegment(sketch, "E9075", {"start": v(62.69, -4.61) * mm, "end": v(62.76, -4.65) * mm});
            skLineSegment(sketch, "E9076", {"start": v(62.76, -4.65) * mm, "end": v(62.82, -4.67) * mm});
            skLineSegment(sketch, "E9077", {"start": v(62.82, -4.67) * mm, "end": v(62.9, -4.7) * mm});
            skLineSegment(sketch, "E9078", {"start": v(62.9, -4.7) * mm, "end": v(62.97, -4.72) * mm});
            skLineSegment(sketch, "E9079", {"start": v(62.97, -4.72) * mm, "end": v(63.05, -4.73) * mm});
            skLineSegment(sketch, "E9080", {"start": v(63.05, -4.73) * mm, "end": v(63.12, -4.75) * mm});
            skLineSegment(sketch, "E9081", {"start": v(63.12, -4.75) * mm, "end": v(63.2, -4.76) * mm});
            skLineSegment(sketch, "E9082", {"start": v(63.2, -4.76) * mm, "end": v(63.29, -4.76) * mm});
            skLineSegment(sketch, "E9083", {"start": v(63.29, -4.76) * mm, "end": v(63.37, -4.76) * mm});
            skLineSegment(sketch, "E9084", {"start": v(63.37, -4.76) * mm, "end": v(63.55, -4.76) * mm});
            skLineSegment(sketch, "E9085", {"start": v(63.55, -4.76) * mm, "end": v(63.73, -4.74) * mm});
            skLineSegment(sketch, "E9086", {"start": v(63.73, -4.74) * mm, "end": v(63.9, -4.72) * mm});
            skLineSegment(sketch, "E9087", {"start": v(63.9, -4.72) * mm, "end": v(64.09, -4.68) * mm});
            skLineSegment(sketch, "E9088", {"start": v(64.09, -4.68) * mm, "end": v(64.27, -4.63) * mm});
            skLineSegment(sketch, "E9089", {"start": v(64.27, -4.63) * mm, "end": v(64.46, -4.58) * mm});
            skLineSegment(sketch, "E9090", {"start": v(64.46, -4.58) * mm, "end": v(64.64, -4.5) * mm});
            skLineSegment(sketch, "E9091", {"start": v(64.64, -4.5) * mm, "end": v(64.83, -4.43) * mm});
            skLineSegment(sketch, "E9092", {"start": v(64.83, -4.43) * mm, "end": v(65.21, -4.25) * mm});
            skLineSegment(sketch, "E9093", {"start": v(65.21, -4.25) * mm, "end": v(65.6, -4.04) * mm});
            skLineSegment(sketch, "E9094", {"start": v(65.6, -4.04) * mm, "end": v(65.97, -3.81) * mm});
            skLineSegment(sketch, "E9095", {"start": v(65.97, -3.81) * mm, "end": v(66.35, -3.55) * mm});
            skLineSegment(sketch, "E9096", {"start": v(66.35, -3.55) * mm, "end": v(66.54, -3.4) * mm});
            skLineSegment(sketch, "E9097", {"start": v(66.54, -3.4) * mm, "end": v(66.75, -3.25) * mm});
            skLineSegment(sketch, "E9098", {"start": v(66.75, -3.25) * mm, "end": v(66.96, -3.08) * mm});
            skLineSegment(sketch, "E9099", {"start": v(66.96, -3.08) * mm, "end": v(67.18, -2.9) * mm});
            skLineSegment(sketch, "E9100", {"start": v(67.18, -2.9) * mm, "end": v(67.42, -2.72) * mm});
            skLineSegment(sketch, "E9101", {"start": v(67.42, -2.72) * mm, "end": v(67.66, -2.51) * mm});
            skLineSegment(sketch, "E9102", {"start": v(67.66, -2.51) * mm, "end": v(67.92, -2.3) * mm});
            skLineSegment(sketch, "E9103", {"start": v(67.92, -2.3) * mm, "end": v(68.18, -2.07) * mm});
            skLineSegment(sketch, "E9104", {"start": v(68.18, -2.07) * mm, "end": v(68.18, -2.96) * mm});
            skLineSegment(sketch, "E9105", {"start": v(68.18, -2.96) * mm, "end": v(67.78, -3.43) * mm});
            skLineSegment(sketch, "E9106", {"start": v(67.78, -3.43) * mm, "end": v(67.38, -3.88) * mm});
            skLineSegment(sketch, "E9107", {"start": v(67.38, -3.88) * mm, "end": v(66.99, -4.3) * mm});
            skLineSegment(sketch, "E9108", {"start": v(66.99, -4.3) * mm, "end": v(66.6, -4.7) * mm});
            skLineSegment(sketch, "E9109", {"start": v(66.6, -4.7) * mm, "end": v(66.22, -5.06) * mm});
            skLineSegment(sketch, "E9110", {"start": v(66.22, -5.06) * mm, "end": v(65.85, -5.4) * mm});
            skLineSegment(sketch, "E9111", {"start": v(65.85, -5.4) * mm, "end": v(65.48, -5.7) * mm});
            skLineSegment(sketch, "E9112", {"start": v(65.48, -5.7) * mm, "end": v(65.12, -5.98) * mm});
            skLineSegment(sketch, "E9113", {"start": v(65.12, -5.98) * mm, "end": v(64.76, -6.22) * mm});
            skLineSegment(sketch, "E9114", {"start": v(64.76, -6.22) * mm, "end": v(64.4, -6.43) * mm});
            skLineSegment(sketch, "E9115", {"start": v(64.4, -6.43) * mm, "end": v(64.04, -6.61) * mm});
            skLineSegment(sketch, "E9116", {"start": v(64.04, -6.61) * mm, "end": v(63.68, -6.76) * mm});
            skLineSegment(sketch, "E9117", {"start": v(63.68, -6.76) * mm, "end": v(63.31, -6.87) * mm});
            skLineSegment(sketch, "E9118", {"start": v(63.31, -6.87) * mm, "end": v(62.95, -6.95) * mm});
            skLineSegment(sketch, "E9119", {"start": v(62.95, -6.95) * mm, "end": v(62.76, -6.98) * mm});
            skLineSegment(sketch, "E9120", {"start": v(62.76, -6.98) * mm, "end": v(62.58, -7) * mm});
            skLineSegment(sketch, "E9121", {"start": v(62.58, -7) * mm, "end": v(62.4, -7.02) * mm});
            skLineSegment(sketch, "E9122", {"start": v(62.4, -7.02) * mm, "end": v(62.21, -7.02) * mm});
            skLineSegment(sketch, "E9123", {"start": v(62.21, -7.02) * mm, "end": v(62.05, -7.02) * mm});
            skLineSegment(sketch, "E9124", {"start": v(62.05, -7.02) * mm, "end": v(61.9, -7) * mm});
            skLineSegment(sketch, "E9125", {"start": v(61.9, -7) * mm, "end": v(61.75, -6.98) * mm});
            skLineSegment(sketch, "E9126", {"start": v(61.75, -6.98) * mm, "end": v(61.6, -6.96) * mm});
            skLineSegment(sketch, "E9127", {"start": v(61.6, -6.96) * mm, "end": v(61.46, -6.92) * mm});
            skLineSegment(sketch, "E9128", {"start": v(61.46, -6.92) * mm, "end": v(61.32, -6.88) * mm});
            skLineSegment(sketch, "E9129", {"start": v(61.32, -6.88) * mm, "end": v(61.19, -6.83) * mm});
            skLineSegment(sketch, "E9130", {"start": v(61.19, -6.83) * mm, "end": v(61.06, -6.77) * mm});
            skLineSegment(sketch, "E9131", {"start": v(61.06, -6.77) * mm, "end": v(60.93, -6.7) * mm});
            skLineSegment(sketch, "E9132", {"start": v(60.93, -6.7) * mm, "end": v(60.81, -6.63) * mm});
            skLineSegment(sketch, "E9133", {"start": v(60.81, -6.63) * mm, "end": v(60.7, -6.55) * mm});
            skLineSegment(sketch, "E9134", {"start": v(60.7, -6.55) * mm, "end": v(60.58, -6.46) * mm});
            skLineSegment(sketch, "E9135", {"start": v(60.58, -6.46) * mm, "end": v(60.48, -6.36) * mm});
            skLineSegment(sketch, "E9136", {"start": v(60.48, -6.36) * mm, "end": v(60.37, -6.26) * mm});
            skLineSegment(sketch, "E9137", {"start": v(60.37, -6.26) * mm, "end": v(60.27, -6.14) * mm});
            skLineSegment(sketch, "E9138", {"start": v(60.27, -6.14) * mm, "end": v(60.17, -6.02) * mm});
            skLineSegment(sketch, "E9139", {"start": v(60.17, -6.02) * mm, "end": v(60.08, -5.9) * mm});
            skLineSegment(sketch, "E9140", {"start": v(60.08, -5.9) * mm, "end": v(60, -5.76) * mm});
            skLineSegment(sketch, "E9141", {"start": v(60, -5.76) * mm, "end": v(59.92, -5.62) * mm});
            skLineSegment(sketch, "E9142", {"start": v(59.92, -5.62) * mm, "end": v(59.85, -5.48) * mm});
            skLineSegment(sketch, "E9143", {"start": v(59.85, -5.48) * mm, "end": v(59.78, -5.33) * mm});
            skLineSegment(sketch, "E9144", {"start": v(59.78, -5.33) * mm, "end": v(59.72, -5.17) * mm});
            skLineSegment(sketch, "E9145", {"start": v(59.72, -5.17) * mm, "end": v(59.66, -5) * mm});
            skLineSegment(sketch, "E9146", {"start": v(59.66, -5) * mm, "end": v(59.61, -4.84) * mm});
            skLineSegment(sketch, "E9147", {"start": v(59.61, -4.84) * mm, "end": v(59.57, -4.67) * mm});
            skLineSegment(sketch, "E9148", {"start": v(59.57, -4.67) * mm, "end": v(59.53, -4.49) * mm});
            skLineSegment(sketch, "E9149", {"start": v(59.53, -4.49) * mm, "end": v(59.47, -4.11) * mm});
            skLineSegment(sketch, "E9150", {"start": v(59.47, -4.11) * mm, "end": v(59.43, -3.71) * mm});
            skLineSegment(sketch, "E9151", {"start": v(59.43, -3.71) * mm, "end": v(59.42, -3.29) * mm});
            skLineSegment(sketch, "E9152", {"start": v(59.42, -3.29) * mm, "end": v(59.43, -2.91) * mm});
            skLineSegment(sketch, "E9153", {"start": v(59.43, -2.91) * mm, "end": v(59.47, -2.55) * mm});
            skLineSegment(sketch, "E9154", {"start": v(59.47, -2.55) * mm, "end": v(59.52, -2.2) * mm});
            skLineSegment(sketch, "E9155", {"start": v(59.52, -2.2) * mm, "end": v(59.6, -1.84) * mm});
            skLineSegment(sketch, "E9156", {"start": v(59.6, -1.84) * mm, "end": v(59.7, -1.5) * mm});
            skLineSegment(sketch, "E9157", {"start": v(59.7, -1.5) * mm, "end": v(59.82, -1.17) * mm});
            skLineSegment(sketch, "E9158", {"start": v(59.82, -1.17) * mm, "end": v(59.96, -0.85) * mm});
            skLineSegment(sketch, "E9159", {"start": v(59.96, -0.85) * mm, "end": v(60.13, -0.54) * mm});
            skLineSegment(sketch, "E9160", {"start": v(60.13, -0.54) * mm, "end": v(60.32, -0.23) * mm});
            skLineSegment(sketch, "E9161", {"start": v(60.32, -0.23) * mm, "end": v(60.54, 0.09) * mm});
            skLineSegment(sketch, "E9162", {"start": v(60.54, 0.09) * mm, "end": v(60.79, 0.4) * mm});
            skLineSegment(sketch, "E9163", {"start": v(60.79, 0.4) * mm, "end": v(61.06, 0.73) * mm});
            skLineSegment(sketch, "E9164", {"start": v(61.06, 0.73) * mm, "end": v(61.37, 1.06) * mm});
            skLineSegment(sketch, "E9165", {"start": v(61.37, 1.06) * mm, "end": v(61.7, 1.4) * mm});
            skLineSegment(sketch, "E9166", {"start": v(61.7, 1.4) * mm, "end": v(62.06, 1.73) * mm});
            skLineSegment(sketch, "E9167", {"start": v(62.06, 1.73) * mm, "end": v(62.44, 2.07) * mm});
            skLineSegment(sketch, "E9168", {"start": v(62.44, 2.07) * mm, "end": v(63, 2.52) * mm});
            skLineSegment(sketch, "E9169", {"start": v(63, 2.52) * mm, "end": v(63.54, 2.9) * mm});
            skLineSegment(sketch, "E9170", {"start": v(63.54, 2.9) * mm, "end": v(63.81, 3.07) * mm});
            skLineSegment(sketch, "E9171", {"start": v(63.81, 3.07) * mm, "end": v(64.08, 3.22) * mm});
            skLineSegment(sketch, "E9172", {"start": v(64.08, 3.22) * mm, "end": v(64.36, 3.37) * mm});
            skLineSegment(sketch, "E9173", {"start": v(64.36, 3.37) * mm, "end": v(64.63, 3.5) * mm});
            skLineSegment(sketch, "E9174", {"start": v(64.63, 3.5) * mm, "end": v(64.9, 3.6) * mm});
            skLineSegment(sketch, "E9175", {"start": v(64.9, 3.6) * mm, "end": v(65.16, 3.7) * mm});
            skLineSegment(sketch, "E9176", {"start": v(65.16, 3.7) * mm, "end": v(65.4, 3.78) * mm});
            skLineSegment(sketch, "E9177", {"start": v(65.4, 3.78) * mm, "end": v(65.65, 3.85) * mm});
            skLineSegment(sketch, "E9178", {"start": v(65.65, 3.85) * mm, "end": v(65.9, 3.9) * mm});
            skLineSegment(sketch, "E9179", {"start": v(65.9, 3.9) * mm, "end": v(66.12, 3.94) * mm});
            skLineSegment(sketch, "E9180", {"start": v(66.12, 3.94) * mm, "end": v(66.35, 3.96) * mm});
            skLineSegment(sketch, "E9181", {"start": v(66.35, 3.96) * mm, "end": v(66.57, 3.97) * mm});
            skLineSegment(sketch, "E9182", {"start": v(66.57, 3.97) * mm, "end": v(66.73, 3.96) * mm});
            skLineSegment(sketch, "E9183", {"start": v(66.73, 3.96) * mm, "end": v(66.89, 3.95) * mm});
            skLineSegment(sketch, "E9184", {"start": v(66.89, 3.95) * mm, "end": v(66.96, 3.94) * mm});
            skLineSegment(sketch, "E9185", {"start": v(66.96, 3.94) * mm, "end": v(67.03, 3.92) * mm});
            skLineSegment(sketch, "E9186", {"start": v(67.03, 3.92) * mm, "end": v(67.1, 3.9) * mm});
            skLineSegment(sketch, "E9187", {"start": v(67.1, 3.9) * mm, "end": v(67.17, 3.89) * mm});
            skLineSegment(sketch, "E9188", {"start": v(67.17, 3.89) * mm, "end": v(67.24, 3.87) * mm});
            skLineSegment(sketch, "E9189", {"start": v(67.24, 3.87) * mm, "end": v(67.3, 3.84) * mm});
            skLineSegment(sketch, "E9190", {"start": v(67.3, 3.84) * mm, "end": v(67.36, 3.82) * mm});
            skLineSegment(sketch, "E9191", {"start": v(67.36, 3.82) * mm, "end": v(67.42, 3.8) * mm});
            skLineSegment(sketch, "E9192", {"start": v(67.42, 3.8) * mm, "end": v(67.48, 3.76) * mm});
            skLineSegment(sketch, "E9193", {"start": v(67.48, 3.76) * mm, "end": v(67.53, 3.73) * mm});
            skLineSegment(sketch, "E9194", {"start": v(67.53, 3.73) * mm, "end": v(67.59, 3.69) * mm});
            skLineSegment(sketch, "E9195", {"start": v(67.59, 3.69) * mm, "end": v(67.64, 3.65) * mm});
            skLineSegment(sketch, "E9196", {"start": v(67.64, 3.65) * mm, "end": v(67.68, 3.61) * mm});
            skLineSegment(sketch, "E9197", {"start": v(67.68, 3.61) * mm, "end": v(67.73, 3.57) * mm});
            skLineSegment(sketch, "E9198", {"start": v(67.73, 3.57) * mm, "end": v(67.77, 3.53) * mm});
            skLineSegment(sketch, "E9199", {"start": v(67.77, 3.53) * mm, "end": v(67.81, 3.48) * mm});
            skLineSegment(sketch, "E9200", {"start": v(67.81, 3.48) * mm, "end": v(67.85, 3.43) * mm});
            skLineSegment(sketch, "E9201", {"start": v(67.85, 3.43) * mm, "end": v(67.88, 3.38) * mm});
            skLineSegment(sketch, "E9202", {"start": v(67.88, 3.38) * mm, "end": v(67.91, 3.32) * mm});
            skLineSegment(sketch, "E9203", {"start": v(67.91, 3.32) * mm, "end": v(67.94, 3.27) * mm});
            skLineSegment(sketch, "E9204", {"start": v(67.94, 3.27) * mm, "end": v(67.96, 3.2) * mm});
            skLineSegment(sketch, "E9205", {"start": v(67.96, 3.2) * mm, "end": v(67.98, 3.15) * mm});
            skLineSegment(sketch, "E9206", {"start": v(67.98, 3.15) * mm, "end": v(68, 3.08) * mm});
            skLineSegment(sketch, "E9207", {"start": v(68, 3.08) * mm, "end": v(68.01, 3.02) * mm});
            skLineSegment(sketch, "E9208", {"start": v(68.01, 3.02) * mm, "end": v(68.03, 2.95) * mm});
            skLineSegment(sketch, "E9209", {"start": v(68.03, 2.95) * mm, "end": v(68.03, 2.88) * mm});
            skLineSegment(sketch, "E9210", {"start": v(68.03, 2.88) * mm, "end": v(68.04, 2.8) * mm});
            skLineSegment(sketch, "E9211", {"start": v(68.04, 2.8) * mm, "end": v(68.04, 2.73) * mm});
            skLineSegment(sketch, "E9212", {"start": v(68.04, 2.73) * mm, "end": v(68.04, 2.61) * mm});
            skLineSegment(sketch, "E9213", {"start": v(68.04, 2.61) * mm, "end": v(68.03, 2.5) * mm});
            skLineSegment(sketch, "E9214", {"start": v(68.03, 2.5) * mm, "end": v(68.02, 2.38) * mm});
            skLineSegment(sketch, "E9215", {"start": v(68.02, 2.38) * mm, "end": v(68, 2.27) * mm});
            skLineSegment(sketch, "E9216", {"start": v(68, 2.27) * mm, "end": v(67.97, 2.16) * mm});
            skLineSegment(sketch, "E9217", {"start": v(67.97, 2.16) * mm, "end": v(67.94, 2.04) * mm});
            skLineSegment(sketch, "E9218", {"start": v(67.94, 2.04) * mm, "end": v(67.91, 1.93) * mm});
            skLineSegment(sketch, "E9219", {"start": v(67.91, 1.93) * mm, "end": v(67.87, 1.81) * mm});
            skLineSegment(sketch, "E9220", {"start": v(67.87, 1.81) * mm, "end": v(67.77, 1.59) * mm});
            skLineSegment(sketch, "E9221", {"start": v(67.77, 1.59) * mm, "end": v(67.66, 1.36) * mm});
            skLineSegment(sketch, "E9222", {"start": v(67.66, 1.36) * mm, "end": v(67.52, 1.13) * mm});
            skLineSegment(sketch, "E9223", {"start": v(67.52, 1.13) * mm, "end": v(67.36, 0.9) * mm});
            skLineSegment(sketch, "E9224", {"start": v(67.36, 0.9) * mm, "end": v(67.18, 0.68) * mm});
            skLineSegment(sketch, "E9225", {"start": v(67.18, 0.68) * mm, "end": v(66.98, 0.46) * mm});
            skLineSegment(sketch, "E9226", {"start": v(66.98, 0.46) * mm, "end": v(66.75, 0.23) * mm});
            skLineSegment(sketch, "E9227", {"start": v(66.75, 0.23) * mm, "end": v(66.5, 0) * mm});
            skLineSegment(sketch, "E9228", {"start": v(66.5, 0) * mm, "end": v(66.23, -0.22) * mm});
            skLineSegment(sketch, "E9229", {"start": v(66.23, -0.22) * mm, "end": v(65.93, -0.44) * mm});
            skLineSegment(sketch, "E9230", {"start": v(65.93, -0.44) * mm, "end": v(65.62, -0.67) * mm});
            skLineSegment(sketch, "E9231", {"start": v(65.62, -0.67) * mm, "end": v(65.28, -0.89) * mm});
            skLineSegment(sketch, "E9232", {"start": v(65.28, -0.89) * mm, "end": v(64.92, -1.1) * mm});
            skLineSegment(sketch, "E9233", {"start": v(64.92, -1.1) * mm, "end": v(64.54, -1.33) * mm});
            skLineSegment(sketch, "E9234", {"start": v(64.54, -1.33) * mm, "end": v(64.15, -1.54) * mm});
            skLineSegment(sketch, "E9235", {"start": v(64.15, -1.54) * mm, "end": v(63.29, -1.97) * mm});
            skLineSegment(sketch, "E9236", {"start": v(63.29, -1.97) * mm, "end": v(62.35, -2.39) * mm});
            skLineSegment(sketch, "E9237", {"start": v(62.35, -2.39) * mm, "end": v(61.85, -2.6) * mm});
            skLineSegment(sketch, "E9238", {"start": v(62, -1.66) * mm, "end": v(62.62, -1.39) * mm});
            skLineSegment(sketch, "E9239", {"start": v(62.62, -1.39) * mm, "end": v(63.2, -1.09) * mm});
            skLineSegment(sketch, "E9240", {"start": v(63.2, -1.09) * mm, "end": v(63.48, -0.93) * mm});
            skLineSegment(sketch, "E9241", {"start": v(63.48, -0.93) * mm, "end": v(63.74, -0.76) * mm});
            skLineSegment(sketch, "E9242", {"start": v(63.74, -0.76) * mm, "end": v(63.99, -0.58) * mm});
            skLineSegment(sketch, "E9243", {"start": v(63.99, -0.58) * mm, "end": v(64.22, -0.4) * mm});
            skLineSegment(sketch, "E9244", {"start": v(64.22, -0.4) * mm, "end": v(64.45, -0.21) * mm});
            skLineSegment(sketch, "E9245", {"start": v(64.45, -0.21) * mm, "end": v(64.65, -0.03) * mm});
            skLineSegment(sketch, "E9246", {"start": v(64.65, -0.03) * mm, "end": v(64.85, 0.16) * mm});
            skLineSegment(sketch, "E9247", {"start": v(64.85, 0.16) * mm, "end": v(65.03, 0.34) * mm});
            skLineSegment(sketch, "E9248", {"start": v(65.03, 0.34) * mm, "end": v(65.19, 0.51) * mm});
            skLineSegment(sketch, "E9249", {"start": v(65.19, 0.51) * mm, "end": v(65.33, 0.69) * mm});
            skLineSegment(sketch, "E9250", {"start": v(65.33, 0.69) * mm, "end": v(65.47, 0.86) * mm});
            skLineSegment(sketch, "E9251", {"start": v(65.47, 0.86) * mm, "end": v(65.58, 1.03) * mm});
            skLineSegment(sketch, "E9252", {"start": v(65.58, 1.03) * mm, "end": v(65.64, 1.12) * mm});
            skLineSegment(sketch, "E9253", {"start": v(65.64, 1.12) * mm, "end": v(65.69, 1.2) * mm});
            skLineSegment(sketch, "E9254", {"start": v(65.69, 1.2) * mm, "end": v(65.73, 1.28) * mm});
            skLineSegment(sketch, "E9255", {"start": v(65.73, 1.28) * mm, "end": v(65.78, 1.36) * mm});
            skLineSegment(sketch, "E9256", {"start": v(65.78, 1.36) * mm, "end": v(65.82, 1.43) * mm});
            skLineSegment(sketch, "E9257", {"start": v(65.82, 1.43) * mm, "end": v(65.86, 1.5) * mm});
            skLineSegment(sketch, "E9258", {"start": v(65.86, 1.5) * mm, "end": v(65.89, 1.57) * mm});
            skLineSegment(sketch, "E9259", {"start": v(65.89, 1.57) * mm, "end": v(65.92, 1.63) * mm});
            skLineSegment(sketch, "E9260", {"start": v(65.92, 1.63) * mm, "end": v(65.94, 1.7) * mm});
            skLineSegment(sketch, "E9261", {"start": v(65.94, 1.7) * mm, "end": v(65.97, 1.75) * mm});
            skLineSegment(sketch, "E9262", {"start": v(65.97, 1.75) * mm, "end": v(65.99, 1.81) * mm});
            skLineSegment(sketch, "E9263", {"start": v(65.99, 1.81) * mm, "end": v(66, 1.86) * mm});
            skLineSegment(sketch, "E9264", {"start": v(66, 1.86) * mm, "end": v(66, 1.89) * mm});
            skLineSegment(sketch, "E9265", {"start": v(66, 1.89) * mm, "end": v(66.01, 1.91) * mm});
            skLineSegment(sketch, "E9266", {"start": v(66.01, 1.91) * mm, "end": v(66.02, 1.94) * mm});
            skLineSegment(sketch, "E9267", {"start": v(66.02, 1.94) * mm, "end": v(66.02, 1.96) * mm});
            skLineSegment(sketch, "E9268", {"start": v(66.02, 1.96) * mm, "end": v(66.03, 1.98) * mm});
            skLineSegment(sketch, "E9269", {"start": v(66.03, 1.98) * mm, "end": v(66.03, 2) * mm});
            skLineSegment(sketch, "E9270", {"start": v(66.03, 2) * mm, "end": v(66.03, 2.03) * mm});
            skLineSegment(sketch, "E9271", {"start": v(66.03, 2.03) * mm, "end": v(66.03, 2.05) * mm});
            skLineSegment(sketch, "E9272", {"start": v(66.03, 2.05) * mm, "end": v(66.03, 2.07) * mm});
            skLineSegment(sketch, "E9273", {"start": v(66.03, 2.07) * mm, "end": v(66.03, 2.09) * mm});
            skLineSegment(sketch, "E9274", {"start": v(66.03, 2.09) * mm, "end": v(66.03, 2.1) * mm});
            skLineSegment(sketch, "E9275", {"start": v(66.03, 2.1) * mm, "end": v(66.03, 2.12) * mm});
            skLineSegment(sketch, "E9276", {"start": v(66.03, 2.12) * mm, "end": v(66.02, 2.14) * mm});
            skLineSegment(sketch, "E9277", {"start": v(66.02, 2.14) * mm, "end": v(66.02, 2.16) * mm});
            skLineSegment(sketch, "E9278", {"start": v(66.02, 2.16) * mm, "end": v(66.02, 2.18) * mm});
            skLineSegment(sketch, "E9279", {"start": v(66.02, 2.18) * mm, "end": v(66.01, 2.2) * mm});
            skLineSegment(sketch, "E9280", {"start": v(66.01, 2.2) * mm, "end": v(66, 2.2) * mm});
            skLineSegment(sketch, "E9281", {"start": v(66, 2.2) * mm, "end": v(66, 2.22) * mm});
            skLineSegment(sketch, "E9282", {"start": v(66, 2.22) * mm, "end": v(66, 2.24) * mm});
            skLineSegment(sketch, "E9283", {"start": v(66, 2.24) * mm, "end": v(65.99, 2.25) * mm});
            skLineSegment(sketch, "E9284", {"start": v(65.99, 2.25) * mm, "end": v(65.98, 2.26) * mm});
            skLineSegment(sketch, "E9285", {"start": v(65.98, 2.26) * mm, "end": v(65.97, 2.27) * mm});
            skLineSegment(sketch, "E9286", {"start": v(65.97, 2.27) * mm, "end": v(65.96, 2.28) * mm});
            skLineSegment(sketch, "E9287", {"start": v(65.96, 2.28) * mm, "end": v(65.95, 2.3) * mm});
            skLineSegment(sketch, "E9288", {"start": v(65.95, 2.3) * mm, "end": v(65.94, 2.3) * mm});
            skLineSegment(sketch, "E9289", {"start": v(65.94, 2.3) * mm, "end": v(65.93, 2.31) * mm});
            skLineSegment(sketch, "E9290", {"start": v(65.93, 2.31) * mm, "end": v(65.92, 2.32) * mm});
            skLineSegment(sketch, "E9291", {"start": v(65.92, 2.32) * mm, "end": v(65.91, 2.33) * mm});
            skLineSegment(sketch, "E9292", {"start": v(65.91, 2.33) * mm, "end": v(65.9, 2.34) * mm});
            skLineSegment(sketch, "E9293", {"start": v(65.9, 2.34) * mm, "end": v(65.89, 2.35) * mm});
            skLineSegment(sketch, "E9294", {"start": v(65.89, 2.35) * mm, "end": v(65.87, 2.35) * mm});
            skLineSegment(sketch, "E9295", {"start": v(65.87, 2.35) * mm, "end": v(65.86, 2.36) * mm});
            skLineSegment(sketch, "E9296", {"start": v(65.86, 2.36) * mm, "end": v(65.84, 2.36) * mm});
            skLineSegment(sketch, "E9297", {"start": v(65.84, 2.36) * mm, "end": v(65.83, 2.37) * mm});
            skLineSegment(sketch, "E9298", {"start": v(65.83, 2.37) * mm, "end": v(65.81, 2.37) * mm});
            skLineSegment(sketch, "E9299", {"start": v(65.81, 2.37) * mm, "end": v(65.8, 2.37) * mm});
            skLineSegment(sketch, "E9300", {"start": v(65.8, 2.37) * mm, "end": v(65.78, 2.38) * mm});
            skLineSegment(sketch, "E9301", {"start": v(65.78, 2.38) * mm, "end": v(65.76, 2.38) * mm});
            skLineSegment(sketch, "E9302", {"start": v(65.76, 2.38) * mm, "end": v(65.75, 2.38) * mm});
            skLineSegment(sketch, "E9303", {"start": v(65.75, 2.38) * mm, "end": v(65.73, 2.38) * mm});
            skLineSegment(sketch, "E9304", {"start": v(65.73, 2.38) * mm, "end": v(65.7, 2.38) * mm});
            skLineSegment(sketch, "E9305", {"start": v(65.7, 2.38) * mm, "end": v(65.7, 2.38) * mm});
            skLineSegment(sketch, "E9306", {"start": v(65.7, 2.38) * mm, "end": v(65.67, 2.38) * mm});
            skLineSegment(sketch, "E9307", {"start": v(65.67, 2.38) * mm, "end": v(65.66, 2.37) * mm});
            skLineSegment(sketch, "E9308", {"start": v(65.66, 2.37) * mm, "end": v(65.64, 2.37) * mm});
            skLineSegment(sketch, "E9309", {"start": v(65.64, 2.37) * mm, "end": v(65.62, 2.37) * mm});
            skLineSegment(sketch, "E9310", {"start": v(65.62, 2.37) * mm, "end": v(65.58, 2.36) * mm});
            skLineSegment(sketch, "E9311", {"start": v(65.58, 2.36) * mm, "end": v(65.53, 2.35) * mm});
            skLineSegment(sketch, "E9312", {"start": v(65.53, 2.35) * mm, "end": v(65.48, 2.33) * mm});
            skLineSegment(sketch, "E9313", {"start": v(65.48, 2.33) * mm, "end": v(65.44, 2.31) * mm});
            skLineSegment(sketch, "E9314", {"start": v(65.44, 2.31) * mm, "end": v(65.38, 2.3) * mm});
            skLineSegment(sketch, "E9315", {"start": v(65.38, 2.3) * mm, "end": v(65.33, 2.27) * mm});
            skLineSegment(sketch, "E9316", {"start": v(65.33, 2.27) * mm, "end": v(65.27, 2.25) * mm});
            skLineSegment(sketch, "E9317", {"start": v(65.27, 2.25) * mm, "end": v(65.21, 2.22) * mm});
            skLineSegment(sketch, "E9318", {"start": v(65.21, 2.22) * mm, "end": v(65.15, 2.2) * mm});
            skLineSegment(sketch, "E9319", {"start": v(65.15, 2.2) * mm, "end": v(65.08, 2.16) * mm});
            skLineSegment(sketch, "E9320", {"start": v(65.08, 2.16) * mm, "end": v(65.02, 2.12) * mm});
            skLineSegment(sketch, "E9321", {"start": v(65.02, 2.12) * mm, "end": v(64.95, 2.09) * mm});
            skLineSegment(sketch, "E9322", {"start": v(64.95, 2.09) * mm, "end": v(64.87, 2.05) * mm});
            skLineSegment(sketch, "E9323", {"start": v(64.87, 2.05) * mm, "end": v(64.58, 1.87) * mm});
            skLineSegment(sketch, "E9324", {"start": v(64.58, 1.87) * mm, "end": v(64.29, 1.66) * mm});
            skLineSegment(sketch, "E9325", {"start": v(64.29, 1.66) * mm, "end": v(63.99, 1.43) * mm});
            skLineSegment(sketch, "E9326", {"start": v(63.99, 1.43) * mm, "end": v(63.69, 1.18) * mm});
            skLineSegment(sketch, "E9327", {"start": v(63.69, 1.18) * mm, "end": v(63.4, 0.9) * mm});
            skLineSegment(sketch, "E9328", {"start": v(63.4, 0.9) * mm, "end": v(63.12, 0.6) * mm});
            skLineSegment(sketch, "E9329", {"start": v(63.12, 0.6) * mm, "end": v(62.86, 0.27) * mm});
            skLineSegment(sketch, "E9330", {"start": v(62.86, 0.27) * mm, "end": v(62.62, -0.08) * mm});
            skLineSegment(sketch, "E9331", {"start": v(62.62, -0.08) * mm, "end": v(62.5, -0.26) * mm});
            skLineSegment(sketch, "E9332", {"start": v(62.5, -0.26) * mm, "end": v(62.4, -0.45) * mm});
            skLineSegment(sketch, "E9333", {"start": v(62.4, -0.45) * mm, "end": v(62.3, -0.64) * mm});
            skLineSegment(sketch, "E9334", {"start": v(62.3, -0.64) * mm, "end": v(62.22, -0.84) * mm});
            skLineSegment(sketch, "E9335", {"start": v(62.22, -0.84) * mm, "end": v(62.15, -1.03) * mm});
            skLineSegment(sketch, "E9336", {"start": v(62.15, -1.03) * mm, "end": v(62.09, -1.24) * mm});
            skLineSegment(sketch, "E9337", {"start": v(62.09, -1.24) * mm, "end": v(62.04, -1.44) * mm});
            skLineSegment(sketch, "E9338", {"start": v(62.04, -1.44) * mm, "end": v(62, -1.66) * mm});
            skLineSegment(sketch, "E9339", {"start": v(69.73, -3.19) * mm, "end": v(69.73, -2.25) * mm});
            skLineSegment(sketch, "E9340", {"start": v(69.73, -2.25) * mm, "end": v(69.92, -2.02) * mm});
            skLineSegment(sketch, "E9341", {"start": v(69.92, -2.02) * mm, "end": v(70.1, -1.8) * mm});
            skLineSegment(sketch, "E9342", {"start": v(70.1, -1.8) * mm, "end": v(70.26, -1.6) * mm});
            skLineSegment(sketch, "E9343", {"start": v(70.26, -1.6) * mm, "end": v(70.42, -1.4) * mm});
            skLineSegment(sketch, "E9344", {"start": v(70.42, -1.4) * mm, "end": v(70.56, -1.2) * mm});
            skLineSegment(sketch, "E9345", {"start": v(70.56, -1.2) * mm, "end": v(70.7, -1.01) * mm});
            skLineSegment(sketch, "E9346", {"start": v(70.7, -1.01) * mm, "end": v(70.8, -0.84) * mm});
            skLineSegment(sketch, "E9347", {"start": v(70.8, -0.84) * mm, "end": v(70.92, -0.67) * mm});
            skLineSegment(sketch, "E9348", {"start": v(70.92, -0.67) * mm, "end": v(70.8, -0.63) * mm});
            skLineSegment(sketch, "E9349", {"start": v(70.8, -0.63) * mm, "end": v(70.7, -0.59) * mm});
            skLineSegment(sketch, "E9350", {"start": v(70.7, -0.59) * mm, "end": v(70.6, -0.54) * mm});
            skLineSegment(sketch, "E9351", {"start": v(70.6, -0.54) * mm, "end": v(70.52, -0.5) * mm});
            skLineSegment(sketch, "E9352", {"start": v(70.52, -0.5) * mm, "end": v(70.43, -0.45) * mm});
            skLineSegment(sketch, "E9353", {"start": v(70.43, -0.45) * mm, "end": v(70.4, -0.42) * mm});
            skLineSegment(sketch, "E9354", {"start": v(70.4, -0.42) * mm, "end": v(70.36, -0.4) * mm});
            skLineSegment(sketch, "E9355", {"start": v(70.36, -0.4) * mm, "end": v(70.33, -0.37) * mm});
            skLineSegment(sketch, "E9356", {"start": v(70.33, -0.37) * mm, "end": v(70.3, -0.34) * mm});
            skLineSegment(sketch, "E9357", {"start": v(70.3, -0.34) * mm, "end": v(70.27, -0.31) * mm});
            skLineSegment(sketch, "E9358", {"start": v(70.27, -0.31) * mm, "end": v(70.24, -0.28) * mm});
            skLineSegment(sketch, "E9359", {"start": v(70.24, -0.28) * mm, "end": v(70.21, -0.25) * mm});
            skLineSegment(sketch, "E9360", {"start": v(70.21, -0.25) * mm, "end": v(70.19, -0.22) * mm});
            skLineSegment(sketch, "E9361", {"start": v(70.19, -0.22) * mm, "end": v(70.17, -0.19) * mm});
            skLineSegment(sketch, "E9362", {"start": v(70.17, -0.19) * mm, "end": v(70.15, -0.15) * mm});
            skLineSegment(sketch, "E9363", {"start": v(70.15, -0.15) * mm, "end": v(70.13, -0.11) * mm});
            skLineSegment(sketch, "E9364", {"start": v(70.13, -0.11) * mm, "end": v(70.11, -0.08) * mm});
            skLineSegment(sketch, "E9365", {"start": v(70.11, -0.08) * mm, "end": v(70.1, -0.04) * mm});
            skLineSegment(sketch, "E9366", {"start": v(70.1, -0.04) * mm, "end": v(70.09, 0) * mm});
            skLineSegment(sketch, "E9367", {"start": v(70.09, 0) * mm, "end": v(70.07, 0.05) * mm});
            skLineSegment(sketch, "E9368", {"start": v(70.07, 0.05) * mm, "end": v(70.06, 0.1) * mm});
            skLineSegment(sketch, "E9369", {"start": v(70.06, 0.1) * mm, "end": v(70.05, 0.15) * mm});
            skLineSegment(sketch, "E9370", {"start": v(70.05, 0.15) * mm, "end": v(70.05, 0.2) * mm});
            skLineSegment(sketch, "E9371", {"start": v(70.05, 0.2) * mm, "end": v(70.04, 0.25) * mm});
            skLineSegment(sketch, "E9372", {"start": v(70.04, 0.25) * mm, "end": v(70.04, 0.3) * mm});
            skLineSegment(sketch, "E9373", {"start": v(70.04, 0.3) * mm, "end": v(70.03, 0.41) * mm});
            skLineSegment(sketch, "E9374", {"start": v(70.03, 0.41) * mm, "end": v(70.04, 0.48) * mm});
            skLineSegment(sketch, "E9375", {"start": v(70.04, 0.48) * mm, "end": v(70.04, 0.55) * mm});
            skLineSegment(sketch, "E9376", {"start": v(70.04, 0.55) * mm, "end": v(70.05, 0.62) * mm});
            skLineSegment(sketch, "E9377", {"start": v(70.05, 0.62) * mm, "end": v(70.06, 0.69) * mm});
            skLineSegment(sketch, "E9378", {"start": v(70.06, 0.69) * mm, "end": v(70.08, 0.76) * mm});
            skLineSegment(sketch, "E9379", {"start": v(70.08, 0.76) * mm, "end": v(70.1, 0.84) * mm});
            skLineSegment(sketch, "E9380", {"start": v(70.1, 0.84) * mm, "end": v(70.12, 0.92) * mm});
            skLineSegment(sketch, "E9381", {"start": v(70.12, 0.92) * mm, "end": v(70.14, 1) * mm});
            skLineSegment(sketch, "E9382", {"start": v(70.14, 1) * mm, "end": v(70.17, 1.08) * mm});
            skLineSegment(sketch, "E9383", {"start": v(70.17, 1.08) * mm, "end": v(70.24, 1.26) * mm});
            skLineSegment(sketch, "E9384", {"start": v(70.24, 1.26) * mm, "end": v(70.32, 1.44) * mm});
            skLineSegment(sketch, "E9385", {"start": v(70.32, 1.44) * mm, "end": v(70.42, 1.63) * mm});
            skLineSegment(sketch, "E9386", {"start": v(70.42, 1.63) * mm, "end": v(70.47, 1.73) * mm});
            skLineSegment(sketch, "E9387", {"start": v(70.47, 1.73) * mm, "end": v(70.7, 2.12) * mm});
            skLineSegment(sketch, "E9388", {"start": v(70.7, 2.12) * mm, "end": v(70.95, 2.5) * mm});
            skLineSegment(sketch, "E9389", {"start": v(70.95, 2.5) * mm, "end": v(71.23, 2.86) * mm});
            skLineSegment(sketch, "E9390", {"start": v(71.23, 2.86) * mm, "end": v(71.54, 3.22) * mm});
            skLineSegment(sketch, "E9391", {"start": v(71.54, 3.22) * mm, "end": v(71.7, 3.38) * mm});
            skLineSegment(sketch, "E9392", {"start": v(71.7, 3.38) * mm, "end": v(71.85, 3.53) * mm});
            skLineSegment(sketch, "E9393", {"start": v(71.85, 3.53) * mm, "end": v(72, 3.67) * mm});
            skLineSegment(sketch, "E9394", {"start": v(72, 3.67) * mm, "end": v(72.15, 3.79) * mm});
            skLineSegment(sketch, "E9395", {"start": v(72.15, 3.79) * mm, "end": v(72.22, 3.84) * mm});
            skLineSegment(sketch, "E9396", {"start": v(72.22, 3.84) * mm, "end": v(72.29, 3.9) * mm});
            skLineSegment(sketch, "E9397", {"start": v(72.29, 3.9) * mm, "end": v(72.36, 3.94) * mm});
            skLineSegment(sketch, "E9398", {"start": v(72.36, 3.94) * mm, "end": v(72.43, 3.98) * mm});
            skLineSegment(sketch, "E9399", {"start": v(72.43, 3.98) * mm, "end": v(72.5, 4.02) * mm});
            skLineSegment(sketch, "E9400", {"start": v(72.5, 4.02) * mm, "end": v(72.56, 4.06) * mm});
            skLineSegment(sketch, "E9401", {"start": v(72.56, 4.06) * mm, "end": v(72.63, 4.09) * mm});
            skLineSegment(sketch, "E9402", {"start": v(72.63, 4.09) * mm, "end": v(72.7, 4.11) * mm});
            skLineSegment(sketch, "E9403", {"start": v(72.7, 4.11) * mm, "end": v(72.75, 4.14) * mm});
            skLineSegment(sketch, "E9404", {"start": v(72.75, 4.14) * mm, "end": v(72.8, 4.16) * mm});
            skLineSegment(sketch, "E9405", {"start": v(72.8, 4.16) * mm, "end": v(72.85, 4.18) * mm});
            skLineSegment(sketch, "E9406", {"start": v(72.85, 4.18) * mm, "end": v(72.9, 4.19) * mm});
            skLineSegment(sketch, "E9407", {"start": v(72.9, 4.19) * mm, "end": v(72.94, 4.2) * mm});
            skLineSegment(sketch, "E9408", {"start": v(72.94, 4.2) * mm, "end": v(73, 4.2) * mm});
            skLineSegment(sketch, "E9409", {"start": v(73, 4.2) * mm, "end": v(73.04, 4.21) * mm});
            skLineSegment(sketch, "E9410", {"start": v(73.04, 4.21) * mm, "end": v(73.09, 4.21) * mm});
            skLineSegment(sketch, "E9411", {"start": v(73.09, 4.21) * mm, "end": v(73.1, 4.21) * mm});
            skLineSegment(sketch, "E9412", {"start": v(73.1, 4.21) * mm, "end": v(73.12, 4.21) * mm});
            skLineSegment(sketch, "E9413", {"start": v(73.12, 4.21) * mm, "end": v(73.14, 4.21) * mm});
            skLineSegment(sketch, "E9414", {"start": v(73.14, 4.21) * mm, "end": v(73.15, 4.21) * mm});
            skLineSegment(sketch, "E9415", {"start": v(73.15, 4.21) * mm, "end": v(73.17, 4.2) * mm});
            skLineSegment(sketch, "E9416", {"start": v(73.17, 4.2) * mm, "end": v(73.18, 4.2) * mm});
            skLineSegment(sketch, "E9417", {"start": v(73.18, 4.2) * mm, "end": v(73.2, 4.2) * mm});
            skLineSegment(sketch, "E9418", {"start": v(73.2, 4.2) * mm, "end": v(73.21, 4.2) * mm});
            skLineSegment(sketch, "E9419", {"start": v(73.21, 4.2) * mm, "end": v(73.23, 4.2) * mm});
            skLineSegment(sketch, "E9420", {"start": v(73.23, 4.2) * mm, "end": v(73.24, 4.19) * mm});
            skLineSegment(sketch, "E9421", {"start": v(73.24, 4.19) * mm, "end": v(73.25, 4.18) * mm});
            skLineSegment(sketch, "E9422", {"start": v(73.25, 4.18) * mm, "end": v(73.26, 4.18) * mm});
            skLineSegment(sketch, "E9423", {"start": v(73.26, 4.18) * mm, "end": v(73.27, 4.17) * mm});
            skLineSegment(sketch, "E9424", {"start": v(73.27, 4.17) * mm, "end": v(73.28, 4.16) * mm});
            skLineSegment(sketch, "E9425", {"start": v(73.28, 4.16) * mm, "end": v(73.3, 4.15) * mm});
            skLineSegment(sketch, "E9426", {"start": v(73.3, 4.15) * mm, "end": v(73.3, 4.15) * mm});
            skLineSegment(sketch, "E9427", {"start": v(73.3, 4.15) * mm, "end": v(73.31, 4.14) * mm});
            skLineSegment(sketch, "E9428", {"start": v(73.31, 4.14) * mm, "end": v(73.32, 4.13) * mm});
            skLineSegment(sketch, "E9429", {"start": v(73.32, 4.13) * mm, "end": v(73.33, 4.12) * mm});
            skLineSegment(sketch, "E9430", {"start": v(73.33, 4.12) * mm, "end": v(73.33, 4.1) * mm});
            skLineSegment(sketch, "E9431", {"start": v(73.33, 4.1) * mm, "end": v(73.34, 4.1) * mm});
            skLineSegment(sketch, "E9432", {"start": v(73.34, 4.1) * mm, "end": v(73.35, 4.09) * mm});
            skLineSegment(sketch, "E9433", {"start": v(73.35, 4.09) * mm, "end": v(73.35, 4.07) * mm});
            skLineSegment(sketch, "E9434", {"start": v(73.35, 4.07) * mm, "end": v(73.36, 4.06) * mm});
            skLineSegment(sketch, "E9435", {"start": v(73.36, 4.06) * mm, "end": v(73.36, 4.05) * mm});
            skLineSegment(sketch, "E9436", {"start": v(73.36, 4.05) * mm, "end": v(73.36, 4.03) * mm});
            skLineSegment(sketch, "E9437", {"start": v(73.36, 4.03) * mm, "end": v(73.37, 4.02) * mm});
            skLineSegment(sketch, "E9438", {"start": v(73.37, 4.02) * mm, "end": v(73.37, 4) * mm});
            skLineSegment(sketch, "E9439", {"start": v(73.37, 4) * mm, "end": v(73.37, 3.99) * mm});
            skLineSegment(sketch, "E9440", {"start": v(73.37, 3.99) * mm, "end": v(73.37, 3.97) * mm});
            skLineSegment(sketch, "E9441", {"start": v(73.37, 3.97) * mm, "end": v(73.37, 3.96) * mm});
            skLineSegment(sketch, "E9442", {"start": v(73.37, 3.96) * mm, "end": v(73.37, 3.94) * mm});
            skLineSegment(sketch, "E9443", {"start": v(73.37, 3.94) * mm, "end": v(73.37, 3.92) * mm});
            skLineSegment(sketch, "E9444", {"start": v(73.37, 3.92) * mm, "end": v(73.37, 3.9) * mm});
            skLineSegment(sketch, "E9445", {"start": v(73.37, 3.9) * mm, "end": v(73.37, 3.89) * mm});
            skLineSegment(sketch, "E9446", {"start": v(73.37, 3.89) * mm, "end": v(73.37, 3.87) * mm});
            skLineSegment(sketch, "E9447", {"start": v(73.37, 3.87) * mm, "end": v(73.36, 3.85) * mm});
            skLineSegment(sketch, "E9448", {"start": v(73.36, 3.85) * mm, "end": v(73.36, 3.83) * mm});
            skLineSegment(sketch, "E9449", {"start": v(73.36, 3.83) * mm, "end": v(73.35, 3.8) * mm});
            skLineSegment(sketch, "E9450", {"start": v(73.35, 3.8) * mm, "end": v(73.35, 3.79) * mm});
            skLineSegment(sketch, "E9451", {"start": v(73.35, 3.79) * mm, "end": v(73.34, 3.76) * mm});
            skLineSegment(sketch, "E9452", {"start": v(73.34, 3.76) * mm, "end": v(73.33, 3.74) * mm});
            skLineSegment(sketch, "E9453", {"start": v(73.33, 3.74) * mm, "end": v(73.32, 3.71) * mm});
            skLineSegment(sketch, "E9454", {"start": v(73.32, 3.71) * mm, "end": v(73.31, 3.68) * mm});
            skLineSegment(sketch, "E9455", {"start": v(73.31, 3.68) * mm, "end": v(73.29, 3.63) * mm});
            skLineSegment(sketch, "E9456", {"start": v(73.29, 3.63) * mm, "end": v(73.26, 3.57) * mm});
            skLineSegment(sketch, "E9457", {"start": v(73.26, 3.57) * mm, "end": v(73.23, 3.5) * mm});
            skLineSegment(sketch, "E9458", {"start": v(73.23, 3.5) * mm, "end": v(73.2, 3.44) * mm});
            skLineSegment(sketch, "E9459", {"start": v(73.2, 3.44) * mm, "end": v(73.16, 3.36) * mm});
            skLineSegment(sketch, "E9460", {"start": v(73.16, 3.36) * mm, "end": v(73.12, 3.29) * mm});
            skLineSegment(sketch, "E9461", {"start": v(73.12, 3.29) * mm, "end": v(73.08, 3.2) * mm});
            skLineSegment(sketch, "E9462", {"start": v(73.08, 3.2) * mm, "end": v(73.03, 3.12) * mm});
            skLineSegment(sketch, "E9463", {"start": v(73.03, 3.12) * mm, "end": v(72.98, 3.03) * mm});
            skLineSegment(sketch, "E9464", {"start": v(72.98, 3.03) * mm, "end": v(72.93, 2.94) * mm});
            skLineSegment(sketch, "E9465", {"start": v(72.93, 2.94) * mm, "end": v(73.3, 3) * mm});
            skLineSegment(sketch, "E9466", {"start": v(73.3, 3) * mm, "end": v(73.64, 3.05) * mm});
            skLineSegment(sketch, "E9467", {"start": v(73.64, 3.05) * mm, "end": v(73.97, 3.1) * mm});
            skLineSegment(sketch, "E9468", {"start": v(73.97, 3.1) * mm, "end": v(74.28, 3.14) * mm});
            skLineSegment(sketch, "E9469", {"start": v(74.28, 3.14) * mm, "end": v(74.57, 3.19) * mm});
            skLineSegment(sketch, "E9470", {"start": v(74.57, 3.19) * mm, "end": v(74.85, 3.22) * mm});
            skLineSegment(sketch, "E9471", {"start": v(74.85, 3.22) * mm, "end": v(75.11, 3.26) * mm});
            skLineSegment(sketch, "E9472", {"start": v(75.11, 3.26) * mm, "end": v(75.36, 3.29) * mm});
            skLineSegment(sketch, "E9473", {"start": v(75.36, 3.29) * mm, "end": v(75.58, 3.32) * mm});
            skLineSegment(sketch, "E9474", {"start": v(75.58, 3.32) * mm, "end": v(75.8, 3.34) * mm});
            skLineSegment(sketch, "E9475", {"start": v(75.8, 3.34) * mm, "end": v(75.89, 3.35) * mm});
            skLineSegment(sketch, "E9476", {"start": v(75.89, 3.35) * mm, "end": v(75.98, 3.36) * mm});
            skLineSegment(sketch, "E9477", {"start": v(75.98, 3.36) * mm, "end": v(76.07, 3.37) * mm});
            skLineSegment(sketch, "E9478", {"start": v(76.07, 3.37) * mm, "end": v(76.16, 3.38) * mm});
            skLineSegment(sketch, "E9479", {"start": v(76.16, 3.38) * mm, "end": v(76.24, 3.38) * mm});
            skLineSegment(sketch, "E9480", {"start": v(76.24, 3.38) * mm, "end": v(76.32, 3.39) * mm});
            skLineSegment(sketch, "E9481", {"start": v(76.32, 3.39) * mm, "end": v(76.39, 3.4) * mm});
            skLineSegment(sketch, "E9482", {"start": v(76.39, 3.4) * mm, "end": v(76.46, 3.4) * mm});
            skLineSegment(sketch, "E9483", {"start": v(76.46, 3.4) * mm, "end": v(76.52, 3.4) * mm});
            skLineSegment(sketch, "E9484", {"start": v(76.52, 3.4) * mm, "end": v(76.58, 3.4) * mm});
            skLineSegment(sketch, "E9485", {"start": v(76.58, 3.4) * mm, "end": v(76.64, 3.4) * mm});
            skLineSegment(sketch, "E9486", {"start": v(76.64, 3.4) * mm, "end": v(76.69, 3.4) * mm});
            skLineSegment(sketch, "E9487", {"start": v(76.69, 3.4) * mm, "end": v(76.76, 3.4) * mm});
            skLineSegment(sketch, "E9488", {"start": v(76.76, 3.4) * mm, "end": v(76.8, 3.4) * mm});
            skLineSegment(sketch, "E9489", {"start": v(76.8, 3.4) * mm, "end": v(76.83, 3.4) * mm});
            skLineSegment(sketch, "E9490", {"start": v(76.83, 3.4) * mm, "end": v(76.86, 3.4) * mm});
            skLineSegment(sketch, "E9491", {"start": v(76.86, 3.4) * mm, "end": v(76.89, 3.4) * mm});
            skLineSegment(sketch, "E9492", {"start": v(76.89, 3.4) * mm, "end": v(76.92, 3.4) * mm});
            skLineSegment(sketch, "E9493", {"start": v(76.92, 3.4) * mm, "end": v(76.94, 3.4) * mm});
            skLineSegment(sketch, "E9494", {"start": v(76.94, 3.4) * mm, "end": v(76.97, 3.39) * mm});
            skLineSegment(sketch, "E9495", {"start": v(76.97, 3.39) * mm, "end": v(77, 3.38) * mm});
            skLineSegment(sketch, "E9496", {"start": v(77, 3.38) * mm, "end": v(77.01, 3.38) * mm});
            skLineSegment(sketch, "E9497", {"start": v(77.01, 3.38) * mm, "end": v(77.04, 3.37) * mm});
            skLineSegment(sketch, "E9498", {"start": v(77.04, 3.37) * mm, "end": v(77.06, 3.37) * mm});
            skLineSegment(sketch, "E9499", {"start": v(77.06, 3.37) * mm, "end": v(77.07, 3.36) * mm});
            skLineSegment(sketch, "E9500", {"start": v(77.07, 3.36) * mm, "end": v(77.1, 3.35) * mm});
            skLineSegment(sketch, "E9501", {"start": v(77.1, 3.35) * mm, "end": v(77.1, 3.35) * mm});
            skLineSegment(sketch, "E9502", {"start": v(77.1, 3.35) * mm, "end": v(77.14, 3.33) * mm});
            skLineSegment(sketch, "E9503", {"start": v(77.14, 3.33) * mm, "end": v(77.17, 3.3) * mm});
            skLineSegment(sketch, "E9504", {"start": v(77.17, 3.3) * mm, "end": v(77.2, 3.29) * mm});
            skLineSegment(sketch, "E9505", {"start": v(77.2, 3.29) * mm, "end": v(77.22, 3.26) * mm});
            skLineSegment(sketch, "E9506", {"start": v(77.22, 3.26) * mm, "end": v(77.25, 3.23) * mm});
            skLineSegment(sketch, "E9507", {"start": v(77.25, 3.23) * mm, "end": v(77.28, 3.2) * mm});
            skLineSegment(sketch, "E9508", {"start": v(77.28, 3.2) * mm, "end": v(77.3, 3.17) * mm});
            skLineSegment(sketch, "E9509", {"start": v(77.3, 3.17) * mm, "end": v(77.33, 3.13) * mm});
            skLineSegment(sketch, "E9510", {"start": v(77.33, 3.13) * mm, "end": v(77.35, 3.1) * mm});
            skLineSegment(sketch, "E9511", {"start": v(77.35, 3.1) * mm, "end": v(77.38, 3.05) * mm});
            skLineSegment(sketch, "E9512", {"start": v(77.38, 3.05) * mm, "end": v(77.4, 3) * mm});
            skLineSegment(sketch, "E9513", {"start": v(77.4, 3) * mm, "end": v(77.43, 2.96) * mm});
            skLineSegment(sketch, "E9514", {"start": v(77.43, 2.96) * mm, "end": v(77.45, 2.9) * mm});
            skLineSegment(sketch, "E9515", {"start": v(77.45, 2.9) * mm, "end": v(77.47, 2.85) * mm});
            skLineSegment(sketch, "E9516", {"start": v(77.47, 2.85) * mm, "end": v(77.49, 2.8) * mm});
            skLineSegment(sketch, "E9517", {"start": v(77.49, 2.8) * mm, "end": v(77.51, 2.74) * mm});
            skLineSegment(sketch, "E9518", {"start": v(77.51, 2.74) * mm, "end": v(77.58, 2.5) * mm});
            skLineSegment(sketch, "E9519", {"start": v(77.58, 2.5) * mm, "end": v(77.63, 2.26) * mm});
            skLineSegment(sketch, "E9520", {"start": v(77.63, 2.26) * mm, "end": v(77.66, 2.02) * mm});
            skLineSegment(sketch, "E9521", {"start": v(77.66, 2.02) * mm, "end": v(77.67, 1.79) * mm});
            skLineSegment(sketch, "E9522", {"start": v(77.67, 1.79) * mm, "end": v(77.67, 1.75) * mm});
            skLineSegment(sketch, "E9523", {"start": v(77.67, 1.75) * mm, "end": v(77.66, 1.7) * mm});
            skLineSegment(sketch, "E9524", {"start": v(77.66, 1.7) * mm, "end": v(77.66, 1.67) * mm});
            skLineSegment(sketch, "E9525", {"start": v(77.66, 1.67) * mm, "end": v(77.65, 1.63) * mm});
            skLineSegment(sketch, "E9526", {"start": v(77.65, 1.63) * mm, "end": v(77.64, 1.6) * mm});
            skLineSegment(sketch, "E9527", {"start": v(77.64, 1.6) * mm, "end": v(77.63, 1.55) * mm});
            skLineSegment(sketch, "E9528", {"start": v(77.63, 1.55) * mm, "end": v(77.62, 1.5) * mm});
            skLineSegment(sketch, "E9529", {"start": v(77.62, 1.5) * mm, "end": v(77.6, 1.47) * mm});
            skLineSegment(sketch, "E9530", {"start": v(77.6, 1.47) * mm, "end": v(77.58, 1.43) * mm});
            skLineSegment(sketch, "E9531", {"start": v(77.58, 1.43) * mm, "end": v(77.56, 1.38) * mm});
            skLineSegment(sketch, "E9532", {"start": v(77.56, 1.38) * mm, "end": v(77.54, 1.34) * mm});
            skLineSegment(sketch, "E9533", {"start": v(77.54, 1.34) * mm, "end": v(77.49, 1.25) * mm});
            skLineSegment(sketch, "E9534", {"start": v(77.49, 1.25) * mm, "end": v(77.43, 1.17) * mm});
            skLineSegment(sketch, "E9535", {"start": v(77.43, 1.17) * mm, "end": v(77.4, 1.12) * mm});
            skLineSegment(sketch, "E9536", {"start": v(77.4, 1.12) * mm, "end": v(77.36, 1.08) * mm});
            skLineSegment(sketch, "E9537", {"start": v(77.36, 1.08) * mm, "end": v(77.32, 1.03) * mm});
            skLineSegment(sketch, "E9538", {"start": v(77.32, 1.03) * mm, "end": v(77.28, 0.98) * mm});
            skLineSegment(sketch, "E9539", {"start": v(77.28, 0.98) * mm, "end": v(77.24, 0.93) * mm});
            skLineSegment(sketch, "E9540", {"start": v(77.24, 0.93) * mm, "end": v(77.2, 0.87) * mm});
            skLineSegment(sketch, "E9541", {"start": v(77.2, 0.87) * mm, "end": v(77.14, 0.81) * mm});
            skLineSegment(sketch, "E9542", {"start": v(77.14, 0.81) * mm, "end": v(77.1, 0.75) * mm});
            skLineSegment(sketch, "E9543", {"start": v(77.1, 0.75) * mm, "end": v(77.04, 0.7) * mm});
            skLineSegment(sketch, "E9544", {"start": v(77.04, 0.7) * mm, "end": v(76.98, 0.62) * mm});
            skLineSegment(sketch, "E9545", {"start": v(76.98, 0.62) * mm, "end": v(76.85, 0.49) * mm});
            skLineSegment(sketch, "E9546", {"start": v(76.85, 0.49) * mm, "end": v(76.71, 0.34) * mm});
            skLineSegment(sketch, "E9547", {"start": v(76.71, 0.34) * mm, "end": v(76.56, 0.18) * mm});
            skLineSegment(sketch, "E9548", {"start": v(76.56, 0.18) * mm, "end": v(76.48, 0.1) * mm});
            skLineSegment(sketch, "E9549", {"start": v(76.48, 0.1) * mm, "end": v(76.12, -0.33) * mm});
            skLineSegment(sketch, "E9550", {"start": v(76.12, -0.33) * mm, "end": v(75.78, -0.77) * mm});
            skLineSegment(sketch, "E9551", {"start": v(75.78, -0.77) * mm, "end": v(75.47, -1.22) * mm});
            skLineSegment(sketch, "E9552", {"start": v(75.47, -1.22) * mm, "end": v(75.2, -1.7) * mm});
            skLineSegment(sketch, "E9553", {"start": v(75.2, -1.7) * mm, "end": v(75.07, -1.93) * mm});
            skLineSegment(sketch, "E9554", {"start": v(75.07, -1.93) * mm, "end": v(75.02, -2.05) * mm});
            skLineSegment(sketch, "E9555", {"start": v(75.02, -2.05) * mm, "end": v(74.97, -2.15) * mm});
            skLineSegment(sketch, "E9556", {"start": v(74.97, -2.15) * mm, "end": v(74.92, -2.26) * mm});
            skLineSegment(sketch, "E9557", {"start": v(74.92, -2.26) * mm, "end": v(74.88, -2.36) * mm});
            skLineSegment(sketch, "E9558", {"start": v(74.88, -2.36) * mm, "end": v(74.84, -2.46) * mm});
            skLineSegment(sketch, "E9559", {"start": v(74.84, -2.46) * mm, "end": v(74.8, -2.55) * mm});
            skLineSegment(sketch, "E9560", {"start": v(74.8, -2.55) * mm, "end": v(74.78, -2.64) * mm});
            skLineSegment(sketch, "E9561", {"start": v(74.78, -2.64) * mm, "end": v(74.75, -2.72) * mm});
            skLineSegment(sketch, "E9562", {"start": v(74.75, -2.72) * mm, "end": v(74.73, -2.8) * mm});
            skLineSegment(sketch, "E9563", {"start": v(74.73, -2.8) * mm, "end": v(74.7, -2.88) * mm});
            skLineSegment(sketch, "E9564", {"start": v(74.7, -2.88) * mm, "end": v(74.7, -2.96) * mm});
            skLineSegment(sketch, "E9565", {"start": v(74.7, -2.96) * mm, "end": v(74.68, -3.03) * mm});
            skLineSegment(sketch, "E9566", {"start": v(74.68, -3.03) * mm, "end": v(74.68, -3.1) * mm});
            skLineSegment(sketch, "E9567", {"start": v(74.68, -3.1) * mm, "end": v(74.68, -3.16) * mm});
            skLineSegment(sketch, "E9568", {"start": v(74.68, -3.16) * mm, "end": v(74.68, -3.2) * mm});
            skLineSegment(sketch, "E9569", {"start": v(74.68, -3.2) * mm, "end": v(74.68, -3.24) * mm});
            skLineSegment(sketch, "E9570", {"start": v(74.68, -3.24) * mm, "end": v(74.68, -3.28) * mm});
            skLineSegment(sketch, "E9571", {"start": v(74.68, -3.28) * mm, "end": v(74.69, -3.32) * mm});
            skLineSegment(sketch, "E9572", {"start": v(74.69, -3.32) * mm, "end": v(74.7, -3.36) * mm});
            skLineSegment(sketch, "E9573", {"start": v(74.7, -3.36) * mm, "end": v(74.7, -3.4) * mm});
            skLineSegment(sketch, "E9574", {"start": v(74.7, -3.4) * mm, "end": v(74.72, -3.42) * mm});
            skLineSegment(sketch, "E9575", {"start": v(74.72, -3.42) * mm, "end": v(74.73, -3.46) * mm});
            skLineSegment(sketch, "E9576", {"start": v(74.73, -3.46) * mm, "end": v(74.74, -3.49) * mm});
            skLineSegment(sketch, "E9577", {"start": v(74.74, -3.49) * mm, "end": v(74.76, -3.52) * mm});
            skLineSegment(sketch, "E9578", {"start": v(74.76, -3.52) * mm, "end": v(74.78, -3.55) * mm});
            skLineSegment(sketch, "E9579", {"start": v(74.78, -3.55) * mm, "end": v(74.8, -3.57) * mm});
            skLineSegment(sketch, "E9580", {"start": v(74.8, -3.57) * mm, "end": v(74.81, -3.6) * mm});
            skLineSegment(sketch, "E9581", {"start": v(74.81, -3.6) * mm, "end": v(74.84, -3.62) * mm});
            skLineSegment(sketch, "E9582", {"start": v(74.84, -3.62) * mm, "end": v(74.86, -3.65) * mm});
            skLineSegment(sketch, "E9583", {"start": v(74.86, -3.65) * mm, "end": v(74.89, -3.67) * mm});
            skLineSegment(sketch, "E9584", {"start": v(74.89, -3.67) * mm, "end": v(74.91, -3.69) * mm});
            skLineSegment(sketch, "E9585", {"start": v(74.91, -3.69) * mm, "end": v(74.94, -3.7) * mm});
            skLineSegment(sketch, "E9586", {"start": v(74.94, -3.7) * mm, "end": v(74.97, -3.73) * mm});
            skLineSegment(sketch, "E9587", {"start": v(74.97, -3.73) * mm, "end": v(75, -3.74) * mm});
            skLineSegment(sketch, "E9588", {"start": v(75, -3.74) * mm, "end": v(75.04, -3.76) * mm});
            skLineSegment(sketch, "E9589", {"start": v(75.04, -3.76) * mm, "end": v(75.07, -3.77) * mm});
            skLineSegment(sketch, "E9590", {"start": v(75.07, -3.77) * mm, "end": v(75.1, -3.79) * mm});
            skLineSegment(sketch, "E9591", {"start": v(75.1, -3.79) * mm, "end": v(75.15, -3.8) * mm});
            skLineSegment(sketch, "E9592", {"start": v(75.15, -3.8) * mm, "end": v(75.19, -3.8) * mm});
            skLineSegment(sketch, "E9593", {"start": v(75.19, -3.8) * mm, "end": v(75.23, -3.82) * mm});
            skLineSegment(sketch, "E9594", {"start": v(75.23, -3.82) * mm, "end": v(75.27, -3.82) * mm});
            skLineSegment(sketch, "E9595", {"start": v(75.27, -3.82) * mm, "end": v(75.32, -3.83) * mm});
            skLineSegment(sketch, "E9596", {"start": v(75.32, -3.83) * mm, "end": v(75.36, -3.83) * mm});
            skLineSegment(sketch, "E9597", {"start": v(75.36, -3.83) * mm, "end": v(75.46, -3.84) * mm});
            skLineSegment(sketch, "E9598", {"start": v(75.46, -3.84) * mm, "end": v(75.51, -3.84) * mm});
            skLineSegment(sketch, "E9599", {"start": v(75.51, -3.84) * mm, "end": v(75.57, -3.84) * mm});
            skLineSegment(sketch, "E9600", {"start": v(75.57, -3.84) * mm, "end": v(75.63, -3.83) * mm});
            skLineSegment(sketch, "E9601", {"start": v(75.63, -3.83) * mm, "end": v(75.7, -3.82) * mm});
            skLineSegment(sketch, "E9602", {"start": v(75.7, -3.82) * mm, "end": v(75.76, -3.81) * mm});
            skLineSegment(sketch, "E9603", {"start": v(75.76, -3.81) * mm, "end": v(75.82, -3.8) * mm});
            skLineSegment(sketch, "E9604", {"start": v(75.82, -3.8) * mm, "end": v(75.9, -3.78) * mm});
            skLineSegment(sketch, "E9605", {"start": v(75.9, -3.78) * mm, "end": v(75.96, -3.75) * mm});
            skLineSegment(sketch, "E9606", {"start": v(75.96, -3.75) * mm, "end": v(76.04, -3.73) * mm});
            skLineSegment(sketch, "E9607", {"start": v(76.04, -3.73) * mm, "end": v(76.11, -3.7) * mm});
            skLineSegment(sketch, "E9608", {"start": v(76.11, -3.7) * mm, "end": v(76.2, -3.66) * mm});
            skLineSegment(sketch, "E9609", {"start": v(76.2, -3.66) * mm, "end": v(76.27, -3.63) * mm});
            skLineSegment(sketch, "E9610", {"start": v(76.27, -3.63) * mm, "end": v(76.36, -3.59) * mm});
            skLineSegment(sketch, "E9611", {"start": v(76.36, -3.59) * mm, "end": v(76.54, -3.5) * mm});
            skLineSegment(sketch, "E9612", {"start": v(76.54, -3.5) * mm, "end": v(76.72, -3.4) * mm});
            skLineSegment(sketch, "E9613", {"start": v(76.72, -3.4) * mm, "end": v(76.92, -3.27) * mm});
            skLineSegment(sketch, "E9614", {"start": v(76.92, -3.27) * mm, "end": v(77.13, -3.14) * mm});
            skLineSegment(sketch, "E9615", {"start": v(77.13, -3.14) * mm, "end": v(77.34, -3) * mm});
            skLineSegment(sketch, "E9616", {"start": v(77.34, -3) * mm, "end": v(77.57, -2.83) * mm});
            skLineSegment(sketch, "E9617", {"start": v(77.57, -2.83) * mm, "end": v(77.8, -2.66) * mm});
            skLineSegment(sketch, "E9618", {"start": v(77.8, -2.66) * mm, "end": v(78.05, -2.47) * mm});
            skLineSegment(sketch, "E9619", {"start": v(78.05, -2.47) * mm, "end": v(78.31, -2.26) * mm});
            skLineSegment(sketch, "E9620", {"start": v(78.31, -2.26) * mm, "end": v(78.58, -2.05) * mm});
            skLineSegment(sketch, "E9621", {"start": v(78.58, -2.05) * mm, "end": v(78.58, -3.01) * mm});
            skLineSegment(sketch, "E9622", {"start": v(78.58, -3.01) * mm, "end": v(78.29, -3.32) * mm});
            skLineSegment(sketch, "E9623", {"start": v(78.29, -3.32) * mm, "end": v(78, -3.61) * mm});
            skLineSegment(sketch, "E9624", {"start": v(78, -3.61) * mm, "end": v(77.74, -3.88) * mm});
            skLineSegment(sketch, "E9625", {"start": v(77.74, -3.88) * mm, "end": v(77.48, -4.14) * mm});
            skLineSegment(sketch, "E9626", {"start": v(77.48, -4.14) * mm, "end": v(77.24, -4.38) * mm});
            skLineSegment(sketch, "E9627", {"start": v(77.24, -4.38) * mm, "end": v(77.02, -4.6) * mm});
            skLineSegment(sketch, "E9628", {"start": v(77.02, -4.6) * mm, "end": v(76.8, -4.8) * mm});
            skLineSegment(sketch, "E9629", {"start": v(76.8, -4.8) * mm, "end": v(76.6, -5) * mm});
            skLineSegment(sketch, "E9630", {"start": v(76.6, -5) * mm, "end": v(76.22, -5.34) * mm});
            skLineSegment(sketch, "E9631", {"start": v(76.22, -5.34) * mm, "end": v(75.85, -5.65) * mm});
            skLineSegment(sketch, "E9632", {"start": v(75.85, -5.65) * mm, "end": v(75.67, -5.79) * mm});
            skLineSegment(sketch, "E9633", {"start": v(75.67, -5.79) * mm, "end": v(75.5, -5.92) * mm});
            skLineSegment(sketch, "E9634", {"start": v(75.5, -5.92) * mm, "end": v(75.32, -6.04) * mm});
            skLineSegment(sketch, "E9635", {"start": v(75.32, -6.04) * mm, "end": v(75.15, -6.15) * mm});
            skLineSegment(sketch, "E9636", {"start": v(75.15, -6.15) * mm, "end": v(74.99, -6.25) * mm});
            skLineSegment(sketch, "E9637", {"start": v(74.99, -6.25) * mm, "end": v(74.83, -6.34) * mm});
            skLineSegment(sketch, "E9638", {"start": v(74.83, -6.34) * mm, "end": v(74.67, -6.4) * mm});
            skLineSegment(sketch, "E9639", {"start": v(74.67, -6.4) * mm, "end": v(74.52, -6.47) * mm});
            skLineSegment(sketch, "E9640", {"start": v(74.52, -6.47) * mm, "end": v(74.45, -6.5) * mm});
            skLineSegment(sketch, "E9641", {"start": v(74.45, -6.5) * mm, "end": v(74.38, -6.51) * mm});
            skLineSegment(sketch, "E9642", {"start": v(74.38, -6.51) * mm, "end": v(74.3, -6.53) * mm});
            skLineSegment(sketch, "E9643", {"start": v(74.3, -6.53) * mm, "end": v(74.24, -6.55) * mm});
            skLineSegment(sketch, "E9644", {"start": v(74.24, -6.55) * mm, "end": v(74.17, -6.56) * mm});
            skLineSegment(sketch, "E9645", {"start": v(74.17, -6.56) * mm, "end": v(74.1, -6.57) * mm});
            skLineSegment(sketch, "E9646", {"start": v(74.1, -6.57) * mm, "end": v(74.03, -6.57) * mm});
            skLineSegment(sketch, "E9647", {"start": v(74.03, -6.57) * mm, "end": v(73.97, -6.57) * mm});
            skLineSegment(sketch, "E9648", {"start": v(73.97, -6.57) * mm, "end": v(73.9, -6.57) * mm});
            skLineSegment(sketch, "E9649", {"start": v(73.9, -6.57) * mm, "end": v(73.82, -6.56) * mm});
            skLineSegment(sketch, "E9650", {"start": v(73.82, -6.56) * mm, "end": v(73.75, -6.55) * mm});
            skLineSegment(sketch, "E9651", {"start": v(73.75, -6.55) * mm, "end": v(73.68, -6.54) * mm});
            skLineSegment(sketch, "E9652", {"start": v(73.68, -6.54) * mm, "end": v(73.6, -6.52) * mm});
            skLineSegment(sketch, "E9653", {"start": v(73.6, -6.52) * mm, "end": v(73.54, -6.5) * mm});
            skLineSegment(sketch, "E9654", {"start": v(73.54, -6.5) * mm, "end": v(73.48, -6.47) * mm});
            skLineSegment(sketch, "E9655", {"start": v(73.48, -6.47) * mm, "end": v(73.41, -6.43) * mm});
            skLineSegment(sketch, "E9656", {"start": v(73.41, -6.43) * mm, "end": v(73.35, -6.4) * mm});
            skLineSegment(sketch, "E9657", {"start": v(73.35, -6.4) * mm, "end": v(73.29, -6.36) * mm});
            skLineSegment(sketch, "E9658", {"start": v(73.29, -6.36) * mm, "end": v(73.23, -6.31) * mm});
            skLineSegment(sketch, "E9659", {"start": v(73.23, -6.31) * mm, "end": v(73.17, -6.26) * mm});
            skLineSegment(sketch, "E9660", {"start": v(73.17, -6.26) * mm, "end": v(73.11, -6.2) * mm});
            skLineSegment(sketch, "E9661", {"start": v(73.11, -6.2) * mm, "end": v(73.06, -6.15) * mm});
            skLineSegment(sketch, "E9662", {"start": v(73.06, -6.15) * mm, "end": v(73, -6.09) * mm});
            skLineSegment(sketch, "E9663", {"start": v(73, -6.09) * mm, "end": v(72.96, -6.02) * mm});
            skLineSegment(sketch, "E9664", {"start": v(72.96, -6.02) * mm, "end": v(72.9, -5.95) * mm});
            skLineSegment(sketch, "E9665", {"start": v(72.9, -5.95) * mm, "end": v(72.86, -5.87) * mm});
            skLineSegment(sketch, "E9666", {"start": v(72.86, -5.87) * mm, "end": v(72.82, -5.8) * mm});
            skLineSegment(sketch, "E9667", {"start": v(72.82, -5.8) * mm, "end": v(72.78, -5.7) * mm});
            skLineSegment(sketch, "E9668", {"start": v(72.78, -5.7) * mm, "end": v(72.74, -5.62) * mm});
            skLineSegment(sketch, "E9669", {"start": v(72.74, -5.62) * mm, "end": v(72.7, -5.53) * mm});
            skLineSegment(sketch, "E9670", {"start": v(72.7, -5.53) * mm, "end": v(72.68, -5.43) * mm});
            skLineSegment(sketch, "E9671", {"start": v(72.68, -5.43) * mm, "end": v(72.65, -5.34) * mm});
            skLineSegment(sketch, "E9672", {"start": v(72.65, -5.34) * mm, "end": v(72.63, -5.23) * mm});
            skLineSegment(sketch, "E9673", {"start": v(72.63, -5.23) * mm, "end": v(72.6, -5.13) * mm});
            skLineSegment(sketch, "E9674", {"start": v(72.6, -5.13) * mm, "end": v(72.6, -5.01) * mm});
            skLineSegment(sketch, "E9675", {"start": v(72.6, -5.01) * mm, "end": v(72.56, -4.78) * mm});
            skLineSegment(sketch, "E9676", {"start": v(72.56, -4.78) * mm, "end": v(72.55, -4.53) * mm});
            skLineSegment(sketch, "E9677", {"start": v(72.55, -4.53) * mm, "end": v(72.55, -4.4) * mm});
            skLineSegment(sketch, "E9678", {"start": v(72.55, -4.4) * mm, "end": v(72.56, -4.24) * mm});
            skLineSegment(sketch, "E9679", {"start": v(72.56, -4.24) * mm, "end": v(72.57, -4.08) * mm});
            skLineSegment(sketch, "E9680", {"start": v(72.57, -4.08) * mm, "end": v(72.6, -3.91) * mm});
            skLineSegment(sketch, "E9681", {"start": v(72.6, -3.91) * mm, "end": v(72.63, -3.74) * mm});
            skLineSegment(sketch, "E9682", {"start": v(72.63, -3.74) * mm, "end": v(72.67, -3.56) * mm});
            skLineSegment(sketch, "E9683", {"start": v(72.67, -3.56) * mm, "end": v(72.73, -3.37) * mm});
            skLineSegment(sketch, "E9684", {"start": v(72.73, -3.37) * mm, "end": v(72.8, -3.18) * mm});
            skLineSegment(sketch, "E9685", {"start": v(72.8, -3.18) * mm, "end": v(72.87, -2.99) * mm});
            skLineSegment(sketch, "E9686", {"start": v(72.87, -2.99) * mm, "end": v(72.95, -2.79) * mm});
            skLineSegment(sketch, "E9687", {"start": v(72.95, -2.79) * mm, "end": v(73.15, -2.37) * mm});
            skLineSegment(sketch, "E9688", {"start": v(73.15, -2.37) * mm, "end": v(73.38, -1.94) * mm});
            skLineSegment(sketch, "E9689", {"start": v(73.38, -1.94) * mm, "end": v(73.65, -1.5) * mm});
            skLineSegment(sketch, "E9690", {"start": v(73.65, -1.5) * mm, "end": v(73.8, -1.27) * mm});
            skLineSegment(sketch, "E9691", {"start": v(73.8, -1.27) * mm, "end": v(74.11, -0.8) * mm});
            skLineSegment(sketch, "E9692", {"start": v(74.11, -0.8) * mm, "end": v(74.8, 0.14) * mm});
            skLineSegment(sketch, "E9693", {"start": v(74.8, 0.14) * mm, "end": v(75.18, 0.6) * mm});
            skLineSegment(sketch, "E9694", {"start": v(75.18, 0.6) * mm, "end": v(74.97, 0.56) * mm});
            skLineSegment(sketch, "E9695", {"start": v(74.97, 0.56) * mm, "end": v(74.75, 0.5) * mm});
            skLineSegment(sketch, "E9696", {"start": v(74.75, 0.5) * mm, "end": v(74.52, 0.46) * mm});
            skLineSegment(sketch, "E9697", {"start": v(74.52, 0.46) * mm, "end": v(74.27, 0.41) * mm});
            skLineSegment(sketch, "E9698", {"start": v(74.27, 0.41) * mm, "end": v(74.01, 0.37) * mm});
            skLineSegment(sketch, "E9699", {"start": v(74.01, 0.37) * mm, "end": v(73.48, 0.27) * mm});
            skLineSegment(sketch, "E9700", {"start": v(73.48, 0.27) * mm, "end": v(73.2, 0.22) * mm});
            skLineSegment(sketch, "E9701", {"start": v(73.2, 0.22) * mm, "end": v(73.06, 0.2) * mm});
            skLineSegment(sketch, "E9702", {"start": v(73.06, 0.2) * mm, "end": v(72.94, 0.18) * mm});
            skLineSegment(sketch, "E9703", {"start": v(72.94, 0.18) * mm, "end": v(72.81, 0.15) * mm});
            skLineSegment(sketch, "E9704", {"start": v(72.81, 0.15) * mm, "end": v(72.7, 0.13) * mm});
            skLineSegment(sketch, "E9705", {"start": v(72.7, 0.13) * mm, "end": v(72.6, 0.11) * mm});
            skLineSegment(sketch, "E9706", {"start": v(72.6, 0.11) * mm, "end": v(72.5, 0.1) * mm});
            skLineSegment(sketch, "E9707", {"start": v(72.5, 0.1) * mm, "end": v(72.46, 0.09) * mm});
            skLineSegment(sketch, "E9708", {"start": v(72.46, 0.09) * mm, "end": v(72.41, 0.08) * mm});
            skLineSegment(sketch, "E9709", {"start": v(72.41, 0.08) * mm, "end": v(72.37, 0.07) * mm});
            skLineSegment(sketch, "E9710", {"start": v(72.37, 0.07) * mm, "end": v(72.33, 0.07) * mm});
            skLineSegment(sketch, "E9711", {"start": v(72.33, 0.07) * mm, "end": v(72.1, -0.38) * mm});
            skLineSegment(sketch, "E9712", {"start": v(72.1, -0.38) * mm, "end": v(71.83, -0.81) * mm});
            skLineSegment(sketch, "E9713", {"start": v(71.83, -0.81) * mm, "end": v(71.55, -1.23) * mm});
            skLineSegment(sketch, "E9714", {"start": v(71.55, -1.23) * mm, "end": v(71.23, -1.64) * mm});
            skLineSegment(sketch, "E9715", {"start": v(71.23, -1.64) * mm, "end": v(70.9, -2.05) * mm});
            skLineSegment(sketch, "E9716", {"start": v(70.9, -2.05) * mm, "end": v(70.53, -2.44) * mm});
            skLineSegment(sketch, "E9717", {"start": v(70.53, -2.44) * mm, "end": v(70.14, -2.82) * mm});
            skLineSegment(sketch, "E9718", {"start": v(70.14, -2.82) * mm, "end": v(69.73, -3.19) * mm});
            skSolve(sketch);
        }
        {
            var Q0;
            Q0=qCreatedBy(makeId("Front.planeOp"),FACE);
            var sketch = newSketch(context, id + "F4", { "sketchPlane" : qUnion([Q0])});
            skLineSegment(sketch, "E9719.bottom", {"start": v(82.02, 19.66) * mm, "end": v(-82.02, 19.66) * mm});
            skLineSegment(sketch, "E9719.top", {"start": v(82.02, -19.66) * mm, "end": v(-82.02, -19.66) * mm});
            skLineSegment(sketch, "E9719.left", {"start": v(82.02, 19.66) * mm, "end": v(82.02, -19.66) * mm});
            skLineSegment(sketch, "E9719.right", {"start": v(-82.02, 19.66) * mm, "end": v(-82.02, -19.66) * mm});
            skPoint(sketch, "E9719.middle", {"position": v(0, 0) * mm});
            skSolve(sketch);
        }
        {
            var Q0;
            Q0 = qSketchRegion(id + "F4", true);
            extrude(context, id + "F5", {"entities" : qUnion([Q0]), "depth" : 0.2 * mm, "offsetDistance" : 25 * mm});
        }
        {
            var Q0;
            Q0=qCreatedBy(makeId("Front.planeOp"),FACE);
            var sketch = newSketch(context, id + "F6", { "sketchPlane" : qUnion([Q0])});
            skText(sketch, "E9720", { "text": "1957-2017", "fontName": "Tinos-Regular.ttf"});
            const initialGuessF6  = {"E9720": [-0.05963, -0.01042, 1, 0, 0.01979]};
            skSetInitialGuess(sketch, initialGuessF6);
            skSolve(sketch);
        }
        {
            var Q0;
            Q0=makeQuery(id+"F6.imprint","IMPRINT",FACE,{"disambiguationData":[TD([[makeQuery(id+"F6.imprint","IMPRINT",EDGE,{"derivedFrom":sQuery(id+"F6.wireOp",EDGE,"E9720.sketch_text.stroke-0")}),-1.0]])]});
            var Q1;
            Q1=makeQuery(id+"F6.imprint","IMPRINT",FACE,{"disambiguationData":[TD([[makeQuery(id+"F6.imprint","IMPRINT",EDGE,{"derivedFrom":sQuery(id+"F6.wireOp",EDGE,"E9720.sketch_text.stroke-11")}),-1.0]])]});
            var Q2;
            Q2=makeQuery(id+"F6.imprint","IMPRINT",FACE,{"disambiguationData":[TD([[makeQuery(id+"F6.imprint","IMPRINT",EDGE,{"derivedFrom":sQuery(id+"F6.wireOp",EDGE,"E9720.sketch_text.stroke-34")}),-1.0]])]});
            var Q3;
            Q3=makeQuery(id+"F6.imprint","IMPRINT",FACE,{"disambiguationData":[TD([[makeQuery(id+"F6.imprint","IMPRINT",EDGE,{"derivedFrom":sQuery(id+"F6.wireOp",EDGE,"E9720.sketch_text.stroke-57")}),-1.0]])]});
            var Q4;
            Q4=makeQuery(id+"F6.imprint","IMPRINT",FACE,{"disambiguationData":[TD([[makeQuery(id+"F6.imprint","IMPRINT",EDGE,{"derivedFrom":sQuery(id+"F6.wireOp",EDGE,"E9720.sketch_text.stroke-66")}),-1.0]])]});
            var Q5;
            Q5=makeQuery(id+"F6.imprint","IMPRINT",FACE,{"disambiguationData":[TD([[makeQuery(id+"F6.imprint","IMPRINT",EDGE,{"derivedFrom":sQuery(id+"F6.wireOp",EDGE,"E9720.sketch_text.stroke-70")}),-1.0]])]});
            var Q6;
            Q6=makeQuery(id+"F6.imprint","IMPRINT",FACE,{"disambiguationData":[TD([[makeQuery(id+"F6.imprint","IMPRINT",EDGE,{"derivedFrom":sQuery(id+"F6.wireOp",EDGE,"E9720.sketch_text.stroke-92")}),-1.0]])]});
            var Q7;
            Q7=makeQuery(id+"F6.imprint","IMPRINT",FACE,{"disambiguationData":[TD([[makeQuery(id+"F6.imprint","IMPRINT",EDGE,{"derivedFrom":sQuery(id+"F6.wireOp",EDGE,"E9720.sketch_text.stroke-107")}),-1.0]])]});
            var Q8;
            Q8=makeQuery(id+"F6.imprint","IMPRINT",FACE,{"disambiguationData":[TD([[makeQuery(id+"F6.imprint","IMPRINT",EDGE,{"derivedFrom":sQuery(id+"F6.wireOp",EDGE,"E9720.sketch_text.stroke-118")}),-1.0]])]});
            extrude(context, id + "F7", {"entities" : qUnion([Q0, Q1, Q2, Q3, Q4, Q5, Q6, Q7, Q8]), "operationType" : NewBodyOperationType.ADD, "depth" : 2.2 * mm, "offsetDistance" : 25 * mm});
        }
    });
